FCSTD DOCUMENT  (FreeCAD 0.18R16117 (Git))
Label: final-prototype
License: All rights reserved
LicenseURL: http://en.wikipedia.org/wiki/All_rights_reserved
objects: Part::Feature×843, Sketcher::SketchObject×264, PartDesign::Pad×127, PartDesign::Pocket×86, PartDesign::Body×36, Part::MultiFuse×28, App::DocumentObjectGroup×24, App::Part×18, Part::FeaturePython×14, Part::Fillet×12, PartDesign::Hole×10, PartDesign::AdditivePipe×10, PartDesign::FeatureBase×8, Part::Mirroring×6, Part::Part2DObjectPython×2, Part::Box×2, PartDesign::Mirrored×2, Spreadsheet::Sheet×1, Mesh::Feature×1, PartDesign::Fillet×1
note: 1684 computed .brp shape members not serialized (recipe doc carries the construction recipe); baked Part::Feature solids carry a one-line shape summary decoded from their .brp

FEATURE [Spreadsheet::Sheet] Spreadsheet  label="bom"
  cells = A1=Part; B1=Number; C1=Prize; D1=Total prize; E1=Comments; F1=Links; A2=SG90; B2=8; C2=1.5; D2==B2 * C2; E2=If the SG90 are limited in torque, take a look at the SG91; A3=Icezum Alhambra II; B3=1; C3=60; D3==B3 * C3; A4=RaspberryPi3_ModelB+; B4=1; C4=50
FEATURE [App::DocumentObjectGroup] Grupo003  label="doc"
  Group = -> [Spreadsheet]
FEATURE [Mesh::Feature] RaspberryPi3_ModelB  label="RaspberryPi3-ModelB"
  Placement = pos=(0,0,0) rot=(1,0,0;4.71239rad)
FEATURE [Part::Feature] Fusion007001  label="Servo-sg90-final"
  Placement = pos=(0,-16.6,0) rot=(0,0,1;0rad)
  shape: bbox 11.8 x 32.4 x 29.9 mm, 77 faces (baked)
FEATURE [Part::Feature] Pocket002001  label="Final-1-arm-horn"
  Placement = pos=(0.0197124,-0.0361996,31.3278) rot=(1,0,0;3.14159rad)
  shape: bbox 22.5 x 8 x 5 mm, 19 faces (baked)
FEATURE [Part::Feature] Pocket003001  label="Final-2-arms-horn"
  Placement = pos=(28.7491,12.6638,37.3278) rot=(1,0,0;3.14159rad)
  shape: bbox 33 x 8 x 5 mm, 28 faces (baked)
FEATURE [Part::Feature] Pocket003004  label="Final-1-rotated"
  Placement = pos=(-0.0921605,3.85986,31.3278) rot=(0.996709,-0.081069,0;3.14159rad)
  shape: bbox 22.28 x 8.247 x 5 mm, 19 faces (baked)
FEATURE [App::DocumentObjectGroup] Grupo005  label="horns"
  Group = -> [Pocket002001,Pocket003001,Pocket003004]
FEATURE [App::DocumentObjectGroup] Grupo006  label="Servomotors"
  Group = -> [Grupo005,Fusion007001]
FEATURE [Part::Feature] Part__Feature388  label="LiPo battery 500 mAh158"
  Placement = pos=(-6e-15,47,-5) rot=(0,0,1;3.14159rad)
  shape: bbox 0.3004 x 0.1808 x 0.005 mm, 6 faces (baked)
FEATURE [Part::Feature] Part__Feature389  label="LiPo battery 500 mAh159"
  Placement = pos=(-6e-15,47,-5) rot=(0,0,1;3.14159rad)
  shape: bbox 0.3004 x 0.1808 x 0.005 mm, 6 faces (baked)
FEATURE [Part::Feature] Part__Feature391  label="LiPo battery 500 mAh161"
  Placement = pos=(-6e-15,47,-5) rot=(0,0,1;3.14159rad)
  shape: bbox 0.3004 x 0.1808 x 0.005 mm, 6 faces (baked)
FEATURE [Part::Feature] Part__Feature230  label="LiPo battery 500 mAh"
  Placement = pos=(-6e-15,47,-5) rot=(0,0,1;3.14159rad)
  shape: bbox 32.9 x 35 x 5 mm, 51 faces (baked)
FEATURE [Part::Feature] Part__Feature231  label="LiPo battery 500 mAh001"
  Placement = pos=(-6e-15,47,-5) rot=(0,0,1;3.14159rad)
  shape: bbox 29 x 4.5 x 1.2 mm, 6 faces (baked)
FEATURE [Part::Feature] Part__Feature232  label="LiPo battery 500 mAh002"
  Placement = pos=(-6e-15,47,-5) rot=(0,0,1;3.14159rad)
  shape: bbox 4 x 4.2 x 0.035 mm, 10 faces (baked)
FEATURE [Part::Feature] Part__Feature233  label="LiPo battery 500 mAh003"
  Placement = pos=(-6e-15,47,-5) rot=(0,0,1;3.14159rad)
  shape: bbox 4 x 4.2 x 0.035 mm, 10 faces (baked)
FEATURE [Part::Feature] Part__Feature234  label="LiPo battery 500 mAh004"
  Placement = pos=(-6e-15,47,-5) rot=(0,0,1;3.14159rad)
  shape: bbox 31.44 x 35.54 x 5.5 mm, 94 faces (baked)
FEATURE [Part::Feature] Part__Feature235  label="LiPo battery 500 mAh005"
  Placement = pos=(-6e-15,47,-5) rot=(0,0,1;3.14159rad)
  shape: bbox 1.098 x 2.25 x 1 mm, 3 faces (baked)
FEATURE [Part::Feature] Part__Feature236  label="LiPo battery 500 mAh006"
  Placement = pos=(-6e-15,47,-5) rot=(0,0,1;3.14159rad)
  shape: bbox 3.548 x 12.25 x 1 mm, 5 faces (baked)
FEATURE [Part::Feature] Part__Feature237  label="LiPo battery 500 mAh007"
  Placement = pos=(-6e-15,47,-5) rot=(0,0,1;3.14159rad)
  shape: bbox 3.45 x 10 x 1 mm, 5 faces (baked)
FEATURE [Part::Feature] Part__Feature238  label="LiPo battery 500 mAh008"
  Placement = pos=(-6e-15,47,-5) rot=(0,0,1;3.14159rad)
  shape: bbox 0.3004 x 0.1793 x 0.005 mm, 6 faces (baked)
FEATURE [Part::Feature] Part__Feature239  label="LiPo battery 500 mAh009"
  Placement = pos=(-6e-15,47,-5) rot=(0,0,1;3.14159rad)
  shape: bbox 0.3004 x 0.1793 x 0.005 mm, 6 faces (baked)
FEATURE [Part::Feature] Part__Feature240  label="LiPo battery 500 mAh010"
  Placement = pos=(-6e-15,47,-5) rot=(0,0,1;3.14159rad)
  shape: bbox 0.3004 x 0.1793 x 0.005 mm, 6 faces (baked)
FEATURE [Part::Feature] Part__Feature241  label="LiPo battery 500 mAh011"
  Placement = pos=(-6e-15,47,-5) rot=(0,0,1;3.14159rad)
  shape: bbox 0.3004 x 0.1808 x 0.005 mm, 6 faces (baked)
FEATURE [Part::Feature] Part__Feature242  label="LiPo battery 500 mAh012"
  Placement = pos=(-6e-15,47,-5) rot=(0,0,1;3.14159rad)
  shape: bbox 0.3004 x 0.1808 x 0.005 mm, 6 faces (baked)
FEATURE [Part::Feature] Part__Feature243  label="LiPo battery 500 mAh013"
  Placement = pos=(-6e-15,47,-5) rot=(0,0,1;3.14159rad)
  shape: bbox 0.3004 x 0.1808 x 0.005 mm, 6 faces (baked)
FEATURE [Part::Feature] Part__Feature244  label="LiPo battery 500 mAh014"
  Placement = pos=(-6e-15,47,-5) rot=(0,0,1;3.14159rad)
  shape: bbox 0.3004 x 0.1808 x 0.005 mm, 6 faces (baked)
FEATURE [Part::Feature] Part__Feature245  label="LiPo battery 500 mAh015"
  Placement = pos=(-6e-15,47,-5) rot=(0,0,1;3.14159rad)
  shape: bbox 0.3004 x 0.1808 x 0.005 mm, 6 faces (baked)
FEATURE [Part::Feature] Part__Feature246  label="LiPo battery 500 mAh016"
  Placement = pos=(-6e-15,47,-5) rot=(0,0,1;3.14159rad)
  shape: bbox 0.3004 x 0.1793 x 0.005 mm, 6 faces (baked)
FEATURE [Part::Feature] Part__Feature247  label="LiPo battery 500 mAh017"
  Placement = pos=(-6e-15,47,-5) rot=(0,0,1;3.14159rad)
  shape: bbox 0.3004 x 0.1793 x 0.005 mm, 6 faces (baked)
FEATURE [Part::Feature] Part__Feature248  label="LiPo battery 500 mAh018"
  Placement = pos=(-6e-15,47,-5) rot=(0,0,1;3.14159rad)
  shape: bbox 0.3004 x 0.1808 x 0.005 mm, 6 faces (baked)
FEATURE [Part::Feature] Part__Feature249  label="LiPo battery 500 mAh019"
  Placement = pos=(-6e-15,47,-5) rot=(0,0,1;3.14159rad)
  shape: bbox 0.3004 x 0.1808 x 0.005 mm, 6 faces (baked)
FEATURE [Part::Feature] Part__Feature250  label="LiPo battery 500 mAh020"
  Placement = pos=(-6e-15,47,-5) rot=(0,0,1;3.14159rad)
  shape: bbox 0.3004 x 0.1808 x 0.005 mm, 6 faces (baked)
FEATURE [Part::Feature] Part__Feature251  label="LiPo battery 500 mAh021"
  Placement = pos=(-6e-15,47,-5) rot=(0,0,1;3.14159rad)
  shape: bbox 0.3004 x 0.1793 x 0.005 mm, 6 faces (baked)
FEATURE [Part::Feature] Part__Feature252  label="LiPo battery 500 mAh022"
  Placement = pos=(-6e-15,47,-5) rot=(0,0,1;3.14159rad)
  shape: bbox 0.3004 x 0.1808 x 0.005 mm, 6 faces (baked)
FEATURE [Part::Feature] Part__Feature253  label="LiPo battery 500 mAh023"
  Placement = pos=(-6e-15,47,-5) rot=(0,0,1;3.14159rad)
  shape: bbox 0.3004 x 0.1808 x 0.005 mm, 6 faces (baked)
FEATURE [Part::Feature] Part__Feature254  label="LiPo battery 500 mAh024"
  Placement = pos=(-6e-15,47,-5) rot=(0,0,1;3.14159rad)
  shape: bbox 0.3004 x 0.1793 x 0.005 mm, 6 faces (baked)
FEATURE [Part::Feature] Part__Feature255  label="LiPo battery 500 mAh025"
  Placement = pos=(-6e-15,47,-5) rot=(0,0,1;3.14159rad)
  shape: bbox 0.3004 x 0.1793 x 0.005 mm, 6 faces (baked)
FEATURE [Part::Feature] Part__Feature256  label="LiPo battery 500 mAh026"
  Placement = pos=(-6e-15,47,-5) rot=(0,0,1;3.14159rad)
  shape: bbox 0.3004 x 0.1793 x 0.005 mm, 6 faces (baked)
FEATURE [Part::Feature] Part__Feature257  label="LiPo battery 500 mAh027"
  Placement = pos=(-6e-15,47,-5) rot=(0,0,1;3.14159rad)
  shape: bbox 0.3004 x 0.1808 x 0.005 mm, 6 faces (baked)
FEATURE [Part::Feature] Part__Feature258  label="LiPo battery 500 mAh028"
  Placement = pos=(-6e-15,47,-5) rot=(0,0,1;3.14159rad)
  shape: bbox 0.3004 x 0.1808 x 0.005 mm, 6 faces (baked)
FEATURE [Part::Feature] Part__Feature259  label="LiPo battery 500 mAh029"
  Placement = pos=(-6e-15,47,-5) rot=(0,0,1;3.14159rad)
  shape: bbox 0.3004 x 0.1808 x 0.005 mm, 6 faces (baked)
FEATURE [Part::Feature] Part__Feature260  label="LiPo battery 500 mAh030"
  Placement = pos=(-6e-15,47,-5) rot=(0,0,1;3.14159rad)
  shape: bbox 0.3004 x 0.1808 x 0.005 mm, 6 faces (baked)
FEATURE [Part::Feature] Part__Feature261  label="LiPo battery 500 mAh031"
  Placement = pos=(-6e-15,47,-5) rot=(0,0,1;3.14159rad)
  shape: bbox 0.3004 x 0.1808 x 0.005 mm, 6 faces (baked)
FEATURE [Part::Feature] Part__Feature262  label="LiPo battery 500 mAh032"
  Placement = pos=(-6e-15,47,-5) rot=(0,0,1;3.14159rad)
  shape: bbox 0.3004 x 0.1793 x 0.005 mm, 6 faces (baked)
FEATURE [Part::Feature] Part__Feature263  label="LiPo battery 500 mAh033"
  Placement = pos=(-6e-15,47,-5) rot=(0,0,1;3.14159rad)
  shape: bbox 0.3004 x 0.1793 x 0.005 mm, 6 faces (baked)
FEATURE [Part::Feature] Part__Feature264  label="LiPo battery 500 mAh034"
  Placement = pos=(-6e-15,47,-5) rot=(0,0,1;3.14159rad)
  shape: bbox 0.3004 x 0.1793 x 0.005 mm, 6 faces (baked)
FEATURE [Part::Feature] Part__Feature265  label="LiPo battery 500 mAh035"
  Placement = pos=(-6e-15,47,-5) rot=(0,0,1;3.14159rad)
  shape: bbox 0.3004 x 0.1808 x 0.005 mm, 6 faces (baked)
FEATURE [Part::Feature] Part__Feature266  label="LiPo battery 500 mAh036"
  Placement = pos=(-6e-15,47,-5) rot=(0,0,1;3.14159rad)
  shape: bbox 0.3004 x 0.1808 x 0.005 mm, 6 faces (baked)
FEATURE [Part::Feature] Part__Feature267  label="LiPo battery 500 mAh037"
  Placement = pos=(-6e-15,47,-5) rot=(0,0,1;3.14159rad)
  shape: bbox 0.3004 x 0.1808 x 0.005 mm, 6 faces (baked)
FEATURE [Part::Feature] Part__Feature268  label="LiPo battery 500 mAh038"
  Placement = pos=(-6e-15,47,-5) rot=(0,0,1;3.14159rad)
  shape: bbox 0.3004 x 0.1808 x 0.005 mm, 6 faces (baked)
FEATURE [Part::Feature] Part__Feature269  label="LiPo battery 500 mAh039"
  Placement = pos=(-6e-15,47,-5) rot=(0,0,1;3.14159rad)
  shape: bbox 0.3004 x 0.1808 x 0.005 mm, 6 faces (baked)
FEATURE [Part::Feature] Part__Feature270  label="LiPo battery 500 mAh040"
  Placement = pos=(-6e-15,47,-5) rot=(0,0,1;3.14159rad)
  shape: bbox 0.3004 x 0.1808 x 0.005 mm, 6 faces (baked)
FEATURE [Part::Feature] Part__Feature271  label="LiPo battery 500 mAh041"
  Placement = pos=(-6e-15,47,-5) rot=(0,0,1;3.14159rad)
  shape: bbox 0.3004 x 0.1808 x 0.005 mm, 6 faces (baked)
FEATURE [Part::Feature] Part__Feature272  label="LiPo battery 500 mAh042"
  Placement = pos=(-6e-15,47,-5) rot=(0,0,1;3.14159rad)
  shape: bbox 0.3004 x 0.1793 x 0.005 mm, 6 faces (baked)
FEATURE [Part::Feature] Part__Feature273  label="LiPo battery 500 mAh043"
  Placement = pos=(-6e-15,47,-5) rot=(0,0,1;3.14159rad)
  shape: bbox 0.3004 x 0.1808 x 0.005 mm, 6 faces (baked)
FEATURE [Part::Feature] Part__Feature274  label="LiPo battery 500 mAh044"
  Placement = pos=(-6e-15,47,-5) rot=(0,0,1;3.14159rad)
  shape: bbox 0.3004 x 0.1793 x 0.005 mm, 6 faces (baked)
FEATURE [Part::Feature] Part__Feature275  label="LiPo battery 500 mAh045"
  Placement = pos=(-6e-15,47,-5) rot=(0,0,1;3.14159rad)
  shape: bbox 0.3004 x 0.1793 x 0.005 mm, 6 faces (baked)
FEATURE [Part::Feature] Part__Feature276  label="LiPo battery 500 mAh046"
  Placement = pos=(-6e-15,47,-5) rot=(0,0,1;3.14159rad)
  shape: bbox 0.3004 x 0.1793 x 0.005 mm, 6 faces (baked)
FEATURE [Part::Feature] Part__Feature277  label="LiPo battery 500 mAh047"
  Placement = pos=(-6e-15,47,-5) rot=(0,0,1;3.14159rad)
  shape: bbox 0.3004 x 0.1808 x 0.005 mm, 6 faces (baked)
FEATURE [Part::Feature] Part__Feature278  label="LiPo battery 500 mAh048"
  Placement = pos=(-6e-15,47,-5) rot=(0,0,1;3.14159rad)
  shape: bbox 0.3004 x 0.1808 x 0.005 mm, 6 faces (baked)
FEATURE [Part::Feature] Part__Feature279  label="LiPo battery 500 mAh049"
  Placement = pos=(-6e-15,47,-5) rot=(0,0,1;3.14159rad)
  shape: bbox 0.3004 x 0.1808 x 0.005 mm, 6 faces (baked)
FEATURE [Part::Feature] Part__Feature280  label="LiPo battery 500 mAh050"
  Placement = pos=(-6e-15,47,-5) rot=(0,0,1;3.14159rad)
  shape: bbox 0.3004 x 0.1808 x 0.005 mm, 6 faces (baked)
FEATURE [Part::Feature] Part__Feature281  label="LiPo battery 500 mAh051"
  Placement = pos=(-6e-15,47,-5) rot=(0,0,1;3.14159rad)
  shape: bbox 0.3004 x 0.1808 x 0.005 mm, 6 faces (baked)
FEATURE [Part::Feature] Part__Feature282  label="LiPo battery 500 mAh052"
  Placement = pos=(-6e-15,47,-5) rot=(0,0,1;3.14159rad)
  shape: bbox 0.3004 x 0.1808 x 0.005 mm, 6 faces (baked)
FEATURE [Part::Feature] Part__Feature283  label="LiPo battery 500 mAh053"
  Placement = pos=(-6e-15,47,-5) rot=(0,0,1;3.14159rad)
  shape: bbox 0.3004 x 0.1793 x 0.005 mm, 6 faces (baked)
FEATURE [Part::Feature] Part__Feature284  label="LiPo battery 500 mAh054"
  Placement = pos=(-6e-15,47,-5) rot=(0,0,1;3.14159rad)
  shape: bbox 0.3004 x 0.1808 x 0.005 mm, 6 faces (baked)
FEATURE [Part::Feature] Part__Feature285  label="LiPo battery 500 mAh055"
  Placement = pos=(-6e-15,47,-5) rot=(0,0,1;3.14159rad)
  shape: bbox 0.3004 x 0.1808 x 0.005 mm, 6 faces (baked)
FEATURE [Part::Feature] Part__Feature286  label="LiPo battery 500 mAh056"
  Placement = pos=(-6e-15,47,-5) rot=(0,0,1;3.14159rad)
  shape: bbox 0.3004 x 0.1808 x 0.005 mm, 6 faces (baked)
FEATURE [Part::Feature] Part__Feature287  label="LiPo battery 500 mAh057"
  Placement = pos=(-6e-15,47,-5) rot=(0,0,1;3.14159rad)
  shape: bbox 0.3004 x 0.1808 x 0.005 mm, 6 faces (baked)
FEATURE [Part::Feature] Part__Feature288  label="LiPo battery 500 mAh058"
  Placement = pos=(-6e-15,47,-5) rot=(0,0,1;3.14159rad)
  shape: bbox 0.3004 x 0.1793 x 0.005 mm, 6 faces (baked)
FEATURE [Part::Feature] Part__Feature289  label="LiPo battery 500 mAh059"
  Placement = pos=(-6e-15,47,-5) rot=(0,0,1;3.14159rad)
  shape: bbox 0.3004 x 0.1793 x 0.005 mm, 6 faces (baked)
FEATURE [Part::Feature] Part__Feature290  label="LiPo battery 500 mAh060"
  Placement = pos=(-6e-15,47,-5) rot=(0,0,1;3.14159rad)
  shape: bbox 0.3004 x 0.1793 x 0.005 mm, 6 faces (baked)
FEATURE [Part::Feature] Part__Feature291  label="LiPo battery 500 mAh061"
  Placement = pos=(-6e-15,47,-5) rot=(0,0,1;3.14159rad)
  shape: bbox 0.3004 x 0.1808 x 0.005 mm, 6 faces (baked)
FEATURE [Part::Feature] Part__Feature292  label="LiPo battery 500 mAh062"
  Placement = pos=(-6e-15,47,-5) rot=(0,0,1;3.14159rad)
  shape: bbox 0.3004 x 0.1808 x 0.005 mm, 6 faces (baked)
FEATURE [Part::Feature] Part__Feature293  label="LiPo battery 500 mAh063"
  Placement = pos=(-6e-15,47,-5) rot=(0,0,1;3.14159rad)
  shape: bbox 0.3004 x 0.1808 x 0.005 mm, 6 faces (baked)
FEATURE [Part::Feature] Part__Feature294  label="LiPo battery 500 mAh064"
  Placement = pos=(-6e-15,47,-5) rot=(0,0,1;3.14159rad)
  shape: bbox 0.3004 x 0.1808 x 0.005 mm, 6 faces (baked)
FEATURE [Part::Feature] Part__Feature295  label="LiPo battery 500 mAh065"
  Placement = pos=(-6e-15,47,-5) rot=(0,0,1;3.14159rad)
  shape: bbox 0.3004 x 0.1808 x 0.005 mm, 6 faces (baked)
FEATURE [Part::Feature] Part__Feature296  label="LiPo battery 500 mAh066"
  Placement = pos=(-6e-15,47,-5) rot=(0,0,1;3.14159rad)
  shape: bbox 0.3004 x 0.1808 x 0.005 mm, 6 faces (baked)
FEATURE [Part::Feature] Part__Feature297  label="LiPo battery 500 mAh067"
  Placement = pos=(-6e-15,47,-5) rot=(0,0,1;3.14159rad)
  shape: bbox 0.3004 x 0.1793 x 0.005 mm, 6 faces (baked)
FEATURE [Part::Feature] Part__Feature298  label="LiPo battery 500 mAh068"
  Placement = pos=(-6e-15,47,-5) rot=(0,0,1;3.14159rad)
  shape: bbox 0.3004 x 0.1793 x 0.005 mm, 6 faces (baked)
FEATURE [Part::Feature] Part__Feature299  label="LiPo battery 500 mAh069"
  Placement = pos=(-6e-15,47,-5) rot=(0,0,1;3.14159rad)
  shape: bbox 0.3004 x 0.1793 x 0.005 mm, 6 faces (baked)
FEATURE [Part::Feature] Part__Feature300  label="LiPo battery 500 mAh070"
  Placement = pos=(-6e-15,47,-5) rot=(0,0,1;3.14159rad)
  shape: bbox 0.3004 x 0.1808 x 0.005 mm, 6 faces (baked)
FEATURE [Part::Feature] Part__Feature301  label="LiPo battery 500 mAh071"
  Placement = pos=(-6e-15,47,-5) rot=(0,0,1;3.14159rad)
  shape: bbox 0.3004 x 0.1808 x 0.005 mm, 6 faces (baked)
FEATURE [Part::Feature] Part__Feature302  label="LiPo battery 500 mAh072"
  Placement = pos=(-6e-15,47,-5) rot=(0,0,1;3.14159rad)
  shape: bbox 0.3004 x 0.1808 x 0.005 mm, 6 faces (baked)
FEATURE [Part::Feature] Part__Feature303  label="LiPo battery 500 mAh073"
  Placement = pos=(-6e-15,47,-5) rot=(0,0,1;3.14159rad)
  shape: bbox 0.3004 x 0.1808 x 0.005 mm, 6 faces (baked)
FEATURE [Part::Feature] Part__Feature304  label="LiPo battery 500 mAh074"
  Placement = pos=(-6e-15,47,-5) rot=(0,0,1;3.14159rad)
  shape: bbox 0.3004 x 0.1808 x 0.005 mm, 6 faces (baked)
FEATURE [Part::Feature] Part__Feature305  label="LiPo battery 500 mAh075"
  Placement = pos=(-6e-15,47,-5) rot=(0,0,1;3.14159rad)
  shape: bbox 0.3004 x 0.1793 x 0.005 mm, 6 faces (baked)
FEATURE [Part::Feature] Part__Feature306  label="LiPo battery 500 mAh076"
  Placement = pos=(-6e-15,47,-5) rot=(0,0,1;3.14159rad)
  shape: bbox 0.3004 x 0.1808 x 0.005 mm, 6 faces (baked)
FEATURE [Part::Feature] Part__Feature307  label="LiPo battery 500 mAh077"
  Placement = pos=(-6e-15,47,-5) rot=(0,0,1;3.14159rad)
  shape: bbox 0.3004 x 0.1808 x 0.005 mm, 6 faces (baked)
FEATURE [Part::Feature] Part__Feature308  label="LiPo battery 500 mAh078"
  Placement = pos=(-6e-15,47,-5) rot=(0,0,1;3.14159rad)
  shape: bbox 0.3004 x 0.1808 x 0.005 mm, 6 faces (baked)
FEATURE [Part::Feature] Part__Feature309  label="LiPo battery 500 mAh079"
  Placement = pos=(-6e-15,47,-5) rot=(0,0,1;3.14159rad)
  shape: bbox 0.3004 x 0.1808 x 0.005 mm, 6 faces (baked)
FEATURE [Part::Feature] Part__Feature310  label="LiPo battery 500 mAh080"
  Placement = pos=(-6e-15,47,-5) rot=(0,0,1;3.14159rad)
  shape: bbox 0.3004 x 0.1808 x 0.005 mm, 6 faces (baked)
FEATURE [Part::Feature] Part__Feature311  label="LiPo battery 500 mAh081"
  Placement = pos=(-6e-15,47,-5) rot=(0,0,1;3.14159rad)
  shape: bbox 0.3004 x 0.1808 x 0.005 mm, 6 faces (baked)
FEATURE [Part::Feature] Part__Feature312  label="LiPo battery 500 mAh082"
  Placement = pos=(-6e-15,47,-5) rot=(0,0,1;3.14159rad)
  shape: bbox 0.3004 x 0.1808 x 0.005 mm, 6 faces (baked)
FEATURE [Part::Feature] Part__Feature313  label="LiPo battery 500 mAh083"
  Placement = pos=(-6e-15,47,-5) rot=(0,0,1;3.14159rad)
  shape: bbox 0.3004 x 0.1793 x 0.005 mm, 6 faces (baked)
FEATURE [Part::Feature] Part__Feature314  label="LiPo battery 500 mAh084"
  Placement = pos=(-6e-15,47,-5) rot=(0,0,1;3.14159rad)
  shape: bbox 0.3004 x 0.1793 x 0.005 mm, 6 faces (baked)
FEATURE [Part::Feature] Part__Feature315  label="LiPo battery 500 mAh085"
  Placement = pos=(-6e-15,47,-5) rot=(0,0,1;3.14159rad)
  shape: bbox 0.3004 x 0.1808 x 0.005 mm, 6 faces (baked)
FEATURE [Part::Feature] Part__Feature316  label="LiPo battery 500 mAh086"
  Placement = pos=(-6e-15,47,-5) rot=(0,0,1;3.14159rad)
  shape: bbox 0.3004 x 0.1808 x 0.005 mm, 6 faces (baked)
FEATURE [Part::Feature] Part__Feature317  label="LiPo battery 500 mAh087"
  Placement = pos=(-6e-15,47,-5) rot=(0,0,1;3.14159rad)
  shape: bbox 0.3004 x 0.1808 x 0.005 mm, 6 faces (baked)
FEATURE [Part::Feature] Part__Feature318  label="LiPo battery 500 mAh088"
  Placement = pos=(-6e-15,47,-5) rot=(0,0,1;3.14159rad)
  shape: bbox 0.3004 x 0.1808 x 0.005 mm, 6 faces (baked)
FEATURE [Part::Feature] Part__Feature319  label="LiPo battery 500 mAh089"
  Placement = pos=(-6e-15,47,-5) rot=(0,0,1;3.14159rad)
  shape: bbox 0.3004 x 0.1808 x 0.005 mm, 6 faces (baked)
FEATURE [Part::Feature] Part__Feature320  label="LiPo battery 500 mAh090"
  Placement = pos=(-6e-15,47,-5) rot=(0,0,1;3.14159rad)
  shape: bbox 0.3004 x 0.1808 x 0.005 mm, 6 faces (baked)
FEATURE [Part::Feature] Part__Feature321  label="LiPo battery 500 mAh091"
  Placement = pos=(-6e-15,47,-5) rot=(0,0,1;3.14159rad)
  shape: bbox 0.3004 x 0.1793 x 0.005 mm, 6 faces (baked)
FEATURE [Part::Feature] Part__Feature322  label="LiPo battery 500 mAh092"
  Placement = pos=(-6e-15,47,-5) rot=(0,0,1;3.14159rad)
  shape: bbox 0.3004 x 0.1808 x 0.005 mm, 6 faces (baked)
FEATURE [Part::Feature] Part__Feature323  label="LiPo battery 500 mAh093"
  Placement = pos=(-6e-15,47,-5) rot=(0,0,1;3.14159rad)
  shape: bbox 0.3004 x 0.1808 x 0.005 mm, 6 faces (baked)
FEATURE [Part::Feature] Part__Feature324  label="LiPo battery 500 mAh094"
  Placement = pos=(-6e-15,47,-5) rot=(0,0,1;3.14159rad)
  shape: bbox 0.3004 x 0.1808 x 0.005 mm, 6 faces (baked)
FEATURE [Part::Feature] Part__Feature325  label="LiPo battery 500 mAh095"
  Placement = pos=(-6e-15,47,-5) rot=(0,0,1;3.14159rad)
  shape: bbox 0.3004 x 0.1808 x 0.005 mm, 6 faces (baked)
FEATURE [Part::Feature] Part__Feature326  label="LiPo battery 500 mAh096"
  Placement = pos=(-6e-15,47,-5) rot=(0,0,1;3.14159rad)
  shape: bbox 0.3004 x 0.1808 x 0.005 mm, 6 faces (baked)
FEATURE [Part::Feature] Part__Feature327  label="LiPo battery 500 mAh097"
  Placement = pos=(-6e-15,47,-5) rot=(0,0,1;3.14159rad)
  shape: bbox 0.3004 x 0.1808 x 0.005 mm, 6 faces (baked)
FEATURE [Part::Feature] Part__Feature328  label="LiPo battery 500 mAh098"
  Placement = pos=(-6e-15,47,-5) rot=(0,0,1;3.14159rad)
  shape: bbox 0.3004 x 0.1793 x 0.005 mm, 6 faces (baked)
FEATURE [Part::Feature] Part__Feature329  label="LiPo battery 500 mAh099"
  Placement = pos=(-6e-15,47,-5) rot=(0,0,1;3.14159rad)
  shape: bbox 0.3004 x 0.1793 x 0.005 mm, 6 faces (baked)
FEATURE [Part::Feature] Part__Feature330  label="LiPo battery 500 mAh100"
  Placement = pos=(-6e-15,47,-5) rot=(0,0,1;3.14159rad)
  shape: bbox 0.3004 x 0.1793 x 0.005 mm, 6 faces (baked)
FEATURE [Part::Feature] Part__Feature331  label="LiPo battery 500 mAh101"
  Placement = pos=(-6e-15,47,-5) rot=(0,0,1;3.14159rad)
  shape: bbox 0.3004 x 0.1808 x 0.005 mm, 6 faces (baked)
FEATURE [Part::Feature] Part__Feature332  label="LiPo battery 500 mAh102"
  Placement = pos=(-6e-15,47,-5) rot=(0,0,1;3.14159rad)
  shape: bbox 0.3004 x 0.1808 x 0.005 mm, 6 faces (baked)
FEATURE [Part::Feature] Part__Feature333  label="LiPo battery 500 mAh103"
  Placement = pos=(-6e-15,47,-5) rot=(0,0,1;3.14159rad)
  shape: bbox 0.3004 x 0.1808 x 0.005 mm, 6 faces (baked)
FEATURE [Part::Feature] Part__Feature334  label="LiPo battery 500 mAh104"
  Placement = pos=(-6e-15,47,-5) rot=(0,0,1;3.14159rad)
  shape: bbox 0.3004 x 0.1808 x 0.005 mm, 6 faces (baked)
FEATURE [Part::Feature] Part__Feature335  label="LiPo battery 500 mAh105"
  Placement = pos=(-6e-15,47,-5) rot=(0,0,1;3.14159rad)
  shape: bbox 0.3004 x 0.1808 x 0.005 mm, 6 faces (baked)
FEATURE [Part::Feature] Part__Feature336  label="LiPo battery 500 mAh106"
  Placement = pos=(-6e-15,47,-5) rot=(0,0,1;3.14159rad)
  shape: bbox 0.3004 x 0.1808 x 0.005 mm, 6 faces (baked)
FEATURE [Part::Feature] Part__Feature337  label="LiPo battery 500 mAh107"
  Placement = pos=(-6e-15,47,-5) rot=(0,0,1;3.14159rad)
  shape: bbox 0.3004 x 0.1808 x 0.005 mm, 6 faces (baked)
FEATURE [Part::Feature] Part__Feature338  label="LiPo battery 500 mAh108"
  Placement = pos=(-6e-15,47,-5) rot=(0,0,1;3.14159rad)
  shape: bbox 0.3004 x 0.1793 x 0.005 mm, 6 faces (baked)
FEATURE [Part::Feature] Part__Feature339  label="LiPo battery 500 mAh109"
  Placement = pos=(-6e-15,47,-5) rot=(0,0,1;3.14159rad)
  shape: bbox 0.3004 x 0.1793 x 0.005 mm, 6 faces (baked)
FEATURE [Part::Feature] Part__Feature340  label="LiPo battery 500 mAh110"
  Placement = pos=(-6e-15,47,-5) rot=(0,0,1;3.14159rad)
  shape: bbox 0.3004 x 0.1793 x 0.005 mm, 6 faces (baked)
FEATURE [Part::Feature] Part__Feature341  label="LiPo battery 500 mAh111"
  Placement = pos=(-6e-15,47,-5) rot=(0,0,1;3.14159rad)
  shape: bbox 0.3004 x 0.1808 x 0.005 mm, 6 faces (baked)
FEATURE [Part::Feature] Part__Feature342  label="LiPo battery 500 mAh112"
  Placement = pos=(-6e-15,47,-5) rot=(0,0,1;3.14159rad)
  shape: bbox 0.3004 x 0.1808 x 0.005 mm, 6 faces (baked)
FEATURE [Part::Feature] Part__Feature343  label="LiPo battery 500 mAh113"
  Placement = pos=(-6e-15,47,-5) rot=(0,0,1;3.14159rad)
  shape: bbox 0.3004 x 0.1808 x 0.005 mm, 6 faces (baked)
FEATURE [Part::Feature] Part__Feature344  label="LiPo battery 500 mAh114"
  Placement = pos=(-6e-15,47,-5) rot=(0,0,1;3.14159rad)
  shape: bbox 0.3004 x 0.1808 x 0.005 mm, 6 faces (baked)
FEATURE [Part::Feature] Part__Feature345  label="LiPo battery 500 mAh115"
  Placement = pos=(-6e-15,47,-5) rot=(0,0,1;3.14159rad)
  shape: bbox 0.3004 x 0.1808 x 0.005 mm, 6 faces (baked)
FEATURE [Part::Feature] Part__Feature346  label="LiPo battery 500 mAh116"
  Placement = pos=(-6e-15,47,-5) rot=(0,0,1;3.14159rad)
  shape: bbox 0.3004 x 0.1808 x 0.005 mm, 6 faces (baked)
FEATURE [Part::Feature] Part__Feature347  label="LiPo battery 500 mAh117"
  Placement = pos=(-6e-15,47,-5) rot=(0,0,1;3.14159rad)
  shape: bbox 0.3004 x 0.1793 x 0.005 mm, 6 faces (baked)
FEATURE [Part::Feature] Part__Feature348  label="LiPo battery 500 mAh118"
  Placement = pos=(-6e-15,47,-5) rot=(0,0,1;3.14159rad)
  shape: bbox 0.3004 x 0.1793 x 0.005 mm, 6 faces (baked)
FEATURE [Part::Feature] Part__Feature349  label="LiPo battery 500 mAh119"
  Placement = pos=(-6e-15,47,-5) rot=(0,0,1;3.14159rad)
  shape: bbox 0.3004 x 0.1793 x 0.005 mm, 6 faces (baked)
FEATURE [Part::Feature] Part__Feature350  label="LiPo battery 500 mAh120"
  Placement = pos=(-6e-15,47,-5) rot=(0,0,1;3.14159rad)
  shape: bbox 0.3004 x 0.1808 x 0.005 mm, 6 faces (baked)
FEATURE [Part::Feature] Part__Feature351  label="LiPo battery 500 mAh121"
  Placement = pos=(-6e-15,47,-5) rot=(0,0,1;3.14159rad)
  shape: bbox 0.3004 x 0.1808 x 0.005 mm, 6 faces (baked)
FEATURE [Part::Feature] Part__Feature352  label="LiPo battery 500 mAh122"
  Placement = pos=(-6e-15,47,-5) rot=(0,0,1;3.14159rad)
  shape: bbox 0.3004 x 0.1808 x 0.005 mm, 6 faces (baked)
FEATURE [Part::Feature] Part__Feature353  label="LiPo battery 500 mAh123"
  Placement = pos=(-6e-15,47,-5) rot=(0,0,1;3.14159rad)
  shape: bbox 0.3004 x 0.1808 x 0.005 mm, 6 faces (baked)
FEATURE [Part::Feature] Part__Feature354  label="LiPo battery 500 mAh124"
  Placement = pos=(-6e-15,47,-5) rot=(0,0,1;3.14159rad)
  shape: bbox 0.3004 x 0.1808 x 0.005 mm, 6 faces (baked)
FEATURE [Part::Feature] Part__Feature355  label="LiPo battery 500 mAh125"
  Placement = pos=(-6e-15,47,-5) rot=(0,0,1;3.14159rad)
  shape: bbox 0.3004 x 0.1808 x 0.005 mm, 6 faces (baked)
FEATURE [Part::Feature] Part__Feature356  label="LiPo battery 500 mAh126"
  Placement = pos=(-6e-15,47,-5) rot=(0,0,1;3.14159rad)
  shape: bbox 0.3004 x 0.1793 x 0.005 mm, 6 faces (baked)
FEATURE [Part::Feature] Part__Feature357  label="LiPo battery 500 mAh127"
  Placement = pos=(-6e-15,47,-5) rot=(0,0,1;3.14159rad)
  shape: bbox 0.3004 x 0.1808 x 0.005 mm, 6 faces (baked)
FEATURE [Part::Feature] Part__Feature358  label="LiPo battery 500 mAh128"
  Placement = pos=(-6e-15,47,-5) rot=(0,0,1;3.14159rad)
  shape: bbox 0.3004 x 0.1808 x 0.005 mm, 6 faces (baked)
FEATURE [Part::Feature] Part__Feature359  label="LiPo battery 500 mAh129"
  Placement = pos=(-6e-15,47,-5) rot=(0,0,1;3.14159rad)
  shape: bbox 0.3004 x 0.1808 x 0.005 mm, 6 faces (baked)
FEATURE [Part::Feature] Part__Feature360  label="LiPo battery 500 mAh130"
  Placement = pos=(-6e-15,47,-5) rot=(0,0,1;3.14159rad)
  shape: bbox 0.3004 x 0.1808 x 0.005 mm, 6 faces (baked)
FEATURE [Part::Feature] Part__Feature361  label="LiPo battery 500 mAh131"
  Placement = pos=(-6e-15,47,-5) rot=(0,0,1;3.14159rad)
  shape: bbox 0.3004 x 0.1808 x 0.005 mm, 6 faces (baked)
FEATURE [Part::Feature] Part__Feature362  label="LiPo battery 500 mAh132"
  Placement = pos=(-6e-15,47,-5) rot=(0,0,1;3.14159rad)
  shape: bbox 0.3004 x 0.1793 x 0.005 mm, 6 faces (baked)
FEATURE [Part::Feature] Part__Feature363  label="LiPo battery 500 mAh133"
  Placement = pos=(-6e-15,47,-5) rot=(0,0,1;3.14159rad)
  shape: bbox 0.3004 x 0.1793 x 0.005 mm, 6 faces (baked)
FEATURE [Part::Feature] Part__Feature364  label="LiPo battery 500 mAh134"
  Placement = pos=(-6e-15,47,-5) rot=(0,0,1;3.14159rad)
  shape: bbox 0.3004 x 0.1808 x 0.005 mm, 6 faces (baked)
FEATURE [Part::Feature] Part__Feature365  label="LiPo battery 500 mAh135"
  Placement = pos=(-6e-15,47,-5) rot=(0,0,1;3.14159rad)
  shape: bbox 0.3004 x 0.1808 x 0.005 mm, 6 faces (baked)
FEATURE [Part::Feature] Part__Feature366  label="LiPo battery 500 mAh136"
  Placement = pos=(-6e-15,47,-5) rot=(0,0,1;3.14159rad)
  shape: bbox 0.3004 x 0.1808 x 0.005 mm, 6 faces (baked)
FEATURE [Part::Feature] Part__Feature367  label="LiPo battery 500 mAh137"
  Placement = pos=(-6e-15,47,-5) rot=(0,0,1;3.14159rad)
  shape: bbox 0.3004 x 0.1808 x 0.005 mm, 6 faces (baked)
FEATURE [Part::Feature] Part__Feature368  label="LiPo battery 500 mAh138"
  Placement = pos=(-6e-15,47,-5) rot=(0,0,1;3.14159rad)
  shape: bbox 0.3004 x 0.1793 x 0.005 mm, 6 faces (baked)
FEATURE [Part::Feature] Part__Feature369  label="LiPo battery 500 mAh139"
  Placement = pos=(-6e-15,47,-5) rot=(0,0,1;3.14159rad)
  shape: bbox 0.3004 x 0.1808 x 0.005 mm, 6 faces (baked)
FEATURE [Part::Feature] Part__Feature370  label="LiPo battery 500 mAh140"
  Placement = pos=(-6e-15,47,-5) rot=(0,0,1;3.14159rad)
  shape: bbox 0.3004 x 0.1793 x 0.005 mm, 6 faces (baked)
FEATURE [Part::Feature] Part__Feature371  label="LiPo battery 500 mAh141"
  Placement = pos=(-6e-15,47,-5) rot=(0,0,1;3.14159rad)
  shape: bbox 0.3004 x 0.1793 x 0.005 mm, 6 faces (baked)
FEATURE [Part::Feature] Part__Feature372  label="LiPo battery 500 mAh142"
  Placement = pos=(-6e-15,47,-5) rot=(0,0,1;3.14159rad)
  shape: bbox 0.3004 x 0.1793 x 0.005 mm, 6 faces (baked)
FEATURE [Part::Feature] Part__Feature373  label="LiPo battery 500 mAh143"
  Placement = pos=(-6e-15,47,-5) rot=(0,0,1;3.14159rad)
  shape: bbox 0.3004 x 0.1808 x 0.005 mm, 6 faces (baked)
FEATURE [Part::Feature] Part__Feature374  label="LiPo battery 500 mAh144"
  Placement = pos=(-6e-15,47,-5) rot=(0,0,1;3.14159rad)
  shape: bbox 0.3004 x 0.1808 x 0.005 mm, 6 faces (baked)
FEATURE [Part::Feature] Part__Feature375  label="LiPo battery 500 mAh145"
  Placement = pos=(-6e-15,47,-5) rot=(0,0,1;3.14159rad)
  shape: bbox 0.3004 x 0.1808 x 0.005 mm, 6 faces (baked)
FEATURE [Part::Feature] Part__Feature376  label="LiPo battery 500 mAh146"
  Placement = pos=(-6e-15,47,-5) rot=(0,0,1;3.14159rad)
  shape: bbox 0.3004 x 0.1808 x 0.005 mm, 6 faces (baked)
FEATURE [Part::Feature] Part__Feature377  label="LiPo battery 500 mAh147"
  Placement = pos=(-6e-15,47,-5) rot=(0,0,1;3.14159rad)
  shape: bbox 3.883 x 0.7165 x 0.005 mm, 6 faces (baked)
FEATURE [Part::Feature] Part__Feature378  label="LiPo battery 500 mAh148"
  Placement = pos=(-6e-15,47,-5) rot=(0,0,1;3.14159rad)
  shape: bbox 3.498 x 3.487 x 0.005 mm, 14 faces (baked)
FEATURE [Part::Feature] Part__Feature379  label="LiPo battery 500 mAh149"
  Placement = pos=(-6e-15,47,-5) rot=(0,0,1;3.14159rad)
  shape: bbox 0.3004 x 0.1808 x 0.005 mm, 6 faces (baked)
FEATURE [Part::Feature] Part__Feature380  label="LiPo battery 500 mAh150"
  Placement = pos=(-6e-15,47,-5) rot=(0,0,1;3.14159rad)
  shape: bbox 0.3004 x 0.1808 x 0.005 mm, 6 faces (baked)
FEATURE [Part::Feature] Part__Feature381  label="LiPo battery 500 mAh151"
  Placement = pos=(-6e-15,47,-5) rot=(0,0,1;3.14159rad)
  shape: bbox 0.3004 x 0.1808 x 0.005 mm, 6 faces (baked)
FEATURE [Part::Feature] Part__Feature382  label="LiPo battery 500 mAh152"
  Placement = pos=(-6e-15,47,-5) rot=(0,0,1;3.14159rad)
  shape: bbox 0.3004 x 0.1808 x 0.005 mm, 6 faces (baked)
FEATURE [Part::Feature] Part__Feature383  label="LiPo battery 500 mAh153"
  Placement = pos=(-6e-15,47,-5) rot=(0,0,1;3.14159rad)
  shape: bbox 0.3004 x 0.1808 x 0.005 mm, 6 faces (baked)
FEATURE [Part::Feature] Part__Feature384  label="LiPo battery 500 mAh154"
  Placement = pos=(-6e-15,47,-5) rot=(0,0,1;3.14159rad)
  shape: bbox 0.3004 x 0.1793 x 0.005 mm, 6 faces (baked)
FEATURE [Part::Feature] Part__Feature385  label="LiPo battery 500 mAh155"
  Placement = pos=(-6e-15,47,-5) rot=(0,0,1;3.14159rad)
  shape: bbox 0.3004 x 0.1793 x 0.005 mm, 6 faces (baked)
FEATURE [Part::Feature] Part__Feature386  label="LiPo battery 500 mAh156"
  Placement = pos=(-6e-15,47,-5) rot=(0,0,1;3.14159rad)
  shape: bbox 0.3004 x 0.1808 x 0.005 mm, 6 faces (baked)
FEATURE [Part::Feature] Part__Feature387  label="LiPo battery 500 mAh157"
  Placement = pos=(-6e-15,47,-5) rot=(0,0,1;3.14159rad)
  shape: bbox 0.3004 x 0.1793 x 0.005 mm, 6 faces (baked)
FEATURE [Part::Feature] Part__Feature390  label="LiPo battery 500 mAh160"
  Placement = pos=(-6e-15,47,-5) rot=(0,0,1;3.14159rad)
  shape: bbox 0.3004 x 0.1808 x 0.005 mm, 6 faces (baked)
FEATURE [Part::Feature] Part__Feature392  label="LiPo battery 500 mAh162"
  Placement = pos=(-6e-15,47,-5) rot=(0,0,1;3.14159rad)
  shape: bbox 0.3004 x 0.1808 x 0.005 mm, 6 faces (baked)
FEATURE [Part::Feature] Part__Feature393  label="LiPo battery 500 mAh163"
  Placement = pos=(-6e-15,47,-5) rot=(0,0,1;3.14159rad)
  shape: bbox 0.3004 x 0.1793 x 0.005 mm, 6 faces (baked)
FEATURE [Part::Feature] Part__Feature394  label="LiPo battery 500 mAh164"
  Placement = pos=(-6e-15,47,-5) rot=(0,0,1;3.14159rad)
  shape: bbox 0.3004 x 0.1808 x 0.005 mm, 6 faces (baked)
FEATURE [Part::Feature] Part__Feature395  label="LiPo battery 500 mAh165"
  Placement = pos=(-6e-15,47,-5) rot=(0,0,1;3.14159rad)
  shape: bbox 0.3004 x 0.1808 x 0.005 mm, 6 faces (baked)
FEATURE [Part::Feature] Part__Feature396  label="LiPo battery 500 mAh166"
  Placement = pos=(-6e-15,47,-5) rot=(0,0,1;3.14159rad)
  shape: bbox 0.3004 x 0.1808 x 0.005 mm, 6 faces (baked)
FEATURE [Part::Feature] Part__Feature397  label="LiPo battery 500 mAh167"
  Placement = pos=(-6e-15,47,-5) rot=(0,0,1;3.14159rad)
  shape: bbox 0.3004 x 0.1808 x 0.005 mm, 6 faces (baked)
FEATURE [Part::Feature] Part__Feature398  label="LiPo battery 500 mAh168"
  Placement = pos=(-6e-15,47,-5) rot=(0,0,1;3.14159rad)
  shape: bbox 0.3004 x 0.1808 x 0.005 mm, 6 faces (baked)
FEATURE [Part::Feature] Part__Feature399  label="LiPo battery 500 mAh169"
  Placement = pos=(-6e-15,47,-5) rot=(0,0,1;3.14159rad)
  shape: bbox 0.3004 x 0.1808 x 0.005 mm, 6 faces (baked)
FEATURE [Part::Feature] Part__Feature400  label="LiPo battery 500 mAh170"
  Placement = pos=(-6e-15,47,-5) rot=(0,0,1;3.14159rad)
  shape: bbox 0.3004 x 0.1793 x 0.005 mm, 6 faces (baked)
FEATURE [Part::Feature] Part__Feature401  label="LiPo battery 500 mAh171"
  Placement = pos=(-6e-15,47,-5) rot=(0,0,1;3.14159rad)
  shape: bbox 0.3004 x 0.1808 x 0.005 mm, 6 faces (baked)
FEATURE [Part::Feature] Part__Feature402  label="LiPo battery 500 mAh172"
  Placement = pos=(-6e-15,47,-5) rot=(0,0,1;3.14159rad)
  shape: bbox 0.3004 x 0.1808 x 0.005 mm, 6 faces (baked)
FEATURE [Part::Feature] Part__Feature403  label="LiPo battery 500 mAh173"
  Placement = pos=(-6e-15,47,-5) rot=(0,0,1;3.14159rad)
  shape: bbox 0.3004 x 0.1808 x 0.005 mm, 6 faces (baked)
FEATURE [Part::Feature] Part__Feature404  label="LiPo battery 500 mAh174"
  Placement = pos=(-6e-15,47,-5) rot=(0,0,1;3.14159rad)
  shape: bbox 0.3004 x 0.1808 x 0.005 mm, 6 faces (baked)
FEATURE [Part::Feature] Part__Feature405  label="LiPo battery 500 mAh175"
  Placement = pos=(-6e-15,47,-5) rot=(0,0,1;3.14159rad)
  shape: bbox 0.3004 x 0.1808 x 0.005 mm, 6 faces (baked)
FEATURE [Part::Feature] Part__Feature406  label="LiPo battery 500 mAh176"
  Placement = pos=(-6e-15,47,-5) rot=(0,0,1;3.14159rad)
  shape: bbox 0.3004 x 0.1793 x 0.005 mm, 6 faces (baked)
FEATURE [Part::Feature] Part__Feature407  label="LiPo battery 500 mAh177"
  Placement = pos=(-6e-15,47,-5) rot=(0,0,1;3.14159rad)
  shape: bbox 0.3004 x 0.1793 x 0.005 mm, 6 faces (baked)
FEATURE [Part::Feature] Part__Feature408  label="LiPo battery 500 mAh178"
  Placement = pos=(-6e-15,47,-5) rot=(0,0,1;3.14159rad)
  shape: bbox 0.3004 x 0.1793 x 0.005 mm, 6 faces (baked)
FEATURE [Part::Feature] Part__Feature409  label="LiPo battery 500 mAh179"
  Placement = pos=(-6e-15,47,-5) rot=(0,0,1;3.14159rad)
  shape: bbox 0.3004 x 0.1808 x 0.005 mm, 6 faces (baked)
FEATURE [Part::Feature] Part__Feature410  label="LiPo battery 500 mAh180"
  Placement = pos=(-6e-15,47,-5) rot=(0,0,1;3.14159rad)
  shape: bbox 0.3004 x 0.1808 x 0.005 mm, 6 faces (baked)
FEATURE [Part::Feature] Part__Feature411  label="LiPo battery 500 mAh181"
  Placement = pos=(-6e-15,47,-5) rot=(0,0,1;3.14159rad)
  shape: bbox 0.3004 x 0.1808 x 0.005 mm, 6 faces (baked)
FEATURE [Part::Feature] Part__Feature412  label="LiPo battery 500 mAh182"
  Placement = pos=(-6e-15,47,-5) rot=(0,0,1;3.14159rad)
  shape: bbox 0.3004 x 0.1808 x 0.005 mm, 6 faces (baked)
FEATURE [Part::Feature] Part__Feature413  label="LiPo battery 500 mAh183"
  Placement = pos=(-6e-15,47,-5) rot=(0,0,1;3.14159rad)
  shape: bbox 0.3004 x 0.1808 x 0.005 mm, 6 faces (baked)
FEATURE [Part::Feature] Part__Feature414  label="LiPo battery 500 mAh184"
  Placement = pos=(-6e-15,47,-5) rot=(0,0,1;3.14159rad)
  shape: bbox 0.3004 x 0.1808 x 0.005 mm, 6 faces (baked)
FEATURE [Part::Feature] Part__Feature415  label="LiPo battery 500 mAh185"
  Placement = pos=(-6e-15,47,-5) rot=(0,0,1;3.14159rad)
  shape: bbox 0.3004 x 0.1808 x 0.005 mm, 6 faces (baked)
FEATURE [Part::Feature] Part__Feature416  label="LiPo battery 500 mAh186"
  Placement = pos=(-6e-15,47,-5) rot=(0,0,1;3.14159rad)
  shape: bbox 0.3004 x 0.1793 x 0.005 mm, 6 faces (baked)
FEATURE [Part::Feature] Part__Feature417  label="LiPo battery 500 mAh187"
  Placement = pos=(-6e-15,47,-5) rot=(0,0,1;3.14159rad)
  shape: bbox 0.3004 x 0.1793 x 0.005 mm, 6 faces (baked)
FEATURE [Part::Feature] Part__Feature418  label="LiPo battery 500 mAh188"
  Placement = pos=(-6e-15,47,-5) rot=(0,0,1;3.14159rad)
  shape: bbox 0.3004 x 0.1793 x 0.005 mm, 6 faces (baked)
FEATURE [Part::Feature] Part__Feature419  label="LiPo battery 500 mAh189"
  Placement = pos=(-6e-15,47,-5) rot=(0,0,1;3.14159rad)
  shape: bbox 0.3004 x 0.1808 x 0.005 mm, 6 faces (baked)
FEATURE [Part::Feature] Part__Feature420  label="LiPo battery 500 mAh190"
  Placement = pos=(-6e-15,47,-5) rot=(0,0,1;3.14159rad)
  shape: bbox 0.3004 x 0.1808 x 0.005 mm, 6 faces (baked)
FEATURE [Part::Feature] Part__Feature421  label="LiPo battery 500 mAh191"
  Placement = pos=(-6e-15,47,-5) rot=(0,0,1;3.14159rad)
  shape: bbox 0.3004 x 0.1808 x 0.005 mm, 6 faces (baked)
FEATURE [Part::Feature] Part__Feature422  label="LiPo battery 500 mAh192"
  Placement = pos=(-6e-15,47,-5) rot=(0,0,1;3.14159rad)
  shape: bbox 0.3004 x 0.1808 x 0.005 mm, 6 faces (baked)
FEATURE [Part::Feature] Part__Feature423  label="LiPo battery 500 mAh193"
  Placement = pos=(-6e-15,47,-5) rot=(0,0,1;3.14159rad)
  shape: bbox 0.3004 x 0.1808 x 0.005 mm, 6 faces (baked)
FEATURE [Part::Feature] Part__Feature424  label="LiPo battery 500 mAh194"
  Placement = pos=(-6e-15,47,-5) rot=(0,0,1;3.14159rad)
  shape: bbox 0.3004 x 0.1808 x 0.005 mm, 6 faces (baked)
FEATURE [Part::Feature] Part__Feature425  label="LiPo battery 500 mAh195"
  Placement = pos=(-6e-15,47,-5) rot=(0,0,1;3.14159rad)
  shape: bbox 0.3004 x 0.1793 x 0.005 mm, 6 faces (baked)
FEATURE [Part::Feature] Part__Feature426  label="LiPo battery 500 mAh196"
  Placement = pos=(-6e-15,47,-5) rot=(0,0,1;3.14159rad)
  shape: bbox 0.3004 x 0.1793 x 0.005 mm, 6 faces (baked)
FEATURE [Part::Feature] Part__Feature427  label="LiPo battery 500 mAh197"
  Placement = pos=(-6e-15,47,-5) rot=(0,0,1;3.14159rad)
  shape: bbox 0.3004 x 0.1793 x 0.005 mm, 6 faces (baked)
FEATURE [Part::Feature] Part__Feature428  label="LiPo battery 500 mAh198"
  Placement = pos=(-6e-15,47,-5) rot=(0,0,1;3.14159rad)
  shape: bbox 0.3004 x 0.1808 x 0.005 mm, 6 faces (baked)
FEATURE [Part::Feature] Part__Feature429  label="LiPo battery 500 mAh199"
  Placement = pos=(-6e-15,47,-5) rot=(0,0,1;3.14159rad)
  shape: bbox 0.3004 x 0.1808 x 0.005 mm, 6 faces (baked)
FEATURE [Part::Feature] Part__Feature430  label="LiPo battery 500 mAh200"
  Placement = pos=(-6e-15,47,-5) rot=(0,0,1;3.14159rad)
  shape: bbox 0.3004 x 0.1808 x 0.005 mm, 6 faces (baked)
FEATURE [Part::Feature] Part__Feature431  label="LiPo battery 500 mAh201"
  Placement = pos=(-6e-15,47,-5) rot=(0,0,1;3.14159rad)
  shape: bbox 0.3004 x 0.1808 x 0.005 mm, 6 faces (baked)
FEATURE [Part::Feature] Part__Feature432  label="LiPo battery 500 mAh202"
  Placement = pos=(-6e-15,47,-5) rot=(0,0,1;3.14159rad)
  shape: bbox 0.3004 x 0.1808 x 0.005 mm, 6 faces (baked)
FEATURE [Part::Feature] Part__Feature433  label="LiPo battery 500 mAh203"
  Placement = pos=(-6e-15,47,-5) rot=(0,0,1;3.14159rad)
  shape: bbox 0.3004 x 0.1808 x 0.005 mm, 6 faces (baked)
FEATURE [Part::Feature] Part__Feature434  label="LiPo battery 500 mAh204"
  Placement = pos=(-6e-15,47,-5) rot=(0,0,1;3.14159rad)
  shape: bbox 0.3004 x 0.1793 x 0.005 mm, 6 faces (baked)
FEATURE [Part::Feature] Part__Feature435  label="LiPo battery 500 mAh205"
  Placement = pos=(-6e-15,47,-5) rot=(0,0,1;3.14159rad)
  shape: bbox 0.3004 x 0.1808 x 0.005 mm, 6 faces (baked)
FEATURE [Part::Feature] Part__Feature436  label="LiPo battery 500 mAh206"
  Placement = pos=(-6e-15,47,-5) rot=(0,0,1;3.14159rad)
  shape: bbox 0.3004 x 0.1808 x 0.005 mm, 6 faces (baked)
FEATURE [Part::Feature] Part__Feature437  label="LiPo battery 500 mAh207"
  Placement = pos=(-6e-15,47,-5) rot=(0,0,1;3.14159rad)
  shape: bbox 0.3004 x 0.1808 x 0.005 mm, 6 faces (baked)
FEATURE [Part::Feature] Part__Feature438  label="LiPo battery 500 mAh208"
  Placement = pos=(-6e-15,47,-5) rot=(0,0,1;3.14159rad)
  shape: bbox 0.3004 x 0.1808 x 0.005 mm, 6 faces (baked)
FEATURE [Part::Feature] Part__Feature439  label="LiPo battery 500 mAh209"
  Placement = pos=(-6e-15,47,-5) rot=(0,0,1;3.14159rad)
  shape: bbox 0.3004 x 0.1808 x 0.005 mm, 6 faces (baked)
FEATURE [Part::Feature] Part__Feature440  label="LiPo battery 500 mAh210"
  Placement = pos=(-6e-15,47,-5) rot=(0,0,1;3.14159rad)
  shape: bbox 0.3004 x 0.1808 x 0.005 mm, 6 faces (baked)
FEATURE [Part::Feature] Part__Feature441  label="LiPo battery 500 mAh211"
  Placement = pos=(-6e-15,47,-5) rot=(0,0,1;3.14159rad)
  shape: bbox 0.3004 x 0.1793 x 0.005 mm, 6 faces (baked)
FEATURE [Part::Feature] Part__Feature442  label="LiPo battery 500 mAh212"
  Placement = pos=(-6e-15,47,-5) rot=(0,0,1;3.14159rad)
  shape: bbox 0.3004 x 0.1793 x 0.005 mm, 6 faces (baked)
FEATURE [Part::Feature] Part__Feature443  label="LiPo battery 500 mAh213"
  Placement = pos=(-6e-15,47,-5) rot=(0,0,1;3.14159rad)
  shape: bbox 0.3004 x 0.1808 x 0.005 mm, 6 faces (baked)
FEATURE [Part::Feature] Part__Feature444  label="LiPo battery 500 mAh214"
  Placement = pos=(-6e-15,47,-5) rot=(0,0,1;3.14159rad)
  shape: bbox 0.3004 x 0.1808 x 0.005 mm, 6 faces (baked)
FEATURE [Part::Feature] Part__Feature445  label="LiPo battery 500 mAh215"
  Placement = pos=(-6e-15,47,-5) rot=(0,0,1;3.14159rad)
  shape: bbox 0.3004 x 0.1808 x 0.005 mm, 6 faces (baked)
FEATURE [Part::Feature] Part__Feature446  label="LiPo battery 500 mAh216"
  Placement = pos=(-6e-15,47,-5) rot=(0,0,1;3.14159rad)
  shape: bbox 0.3004 x 0.1808 x 0.005 mm, 6 faces (baked)
FEATURE [Part::Feature] Part__Feature447  label="LiPo battery 500 mAh217"
  Placement = pos=(-6e-15,47,-5) rot=(0,0,1;3.14159rad)
  shape: bbox 0.3004 x 0.1808 x 0.005 mm, 6 faces (baked)
FEATURE [Part::Feature] Part__Feature448  label="LiPo battery 500 mAh218"
  Placement = pos=(-6e-15,47,-5) rot=(0,0,1;3.14159rad)
  shape: bbox 0.3004 x 0.1808 x 0.005 mm, 6 faces (baked)
FEATURE [Part::Feature] Part__Feature449  label="LiPo battery 500 mAh219"
  Placement = pos=(-6e-15,47,-5) rot=(0,0,1;3.14159rad)
  shape: bbox 0.3004 x 0.1808 x 0.005 mm, 6 faces (baked)
FEATURE [Part::Feature] Part__Feature450  label="LiPo battery 500 mAh220"
  Placement = pos=(-6e-15,47,-5) rot=(0,0,1;3.14159rad)
  shape: bbox 0.3004 x 0.1808 x 0.005 mm, 6 faces (baked)
FEATURE [Part::Feature] Part__Feature451  label="LiPo battery 500 mAh221"
  Placement = pos=(-6e-15,47,-5) rot=(0,0,1;3.14159rad)
  shape: bbox 0.3004 x 0.1793 x 0.005 mm, 6 faces (baked)
FEATURE [Part::Feature] Part__Feature452  label="LiPo battery 500 mAh222"
  Placement = pos=(-6e-15,47,-5) rot=(0,0,1;3.14159rad)
  shape: bbox 0.3004 x 0.1808 x 0.005 mm, 6 faces (baked)
FEATURE [Part::Feature] Part__Feature453  label="LiPo battery 500 mAh223"
  Placement = pos=(-6e-15,47,-5) rot=(0,0,1;3.14159rad)
  shape: bbox 0.3004 x 0.1808 x 0.005 mm, 6 faces (baked)
FEATURE [Part::Feature] Part__Feature454  label="LiPo battery 500 mAh224"
  Placement = pos=(-6e-15,47,-5) rot=(0,0,1;3.14159rad)
  shape: bbox 0.3004 x 0.1808 x 0.005 mm, 6 faces (baked)
FEATURE [Part::Feature] Part__Feature455  label="LiPo battery 500 mAh225"
  Placement = pos=(-6e-15,47,-5) rot=(0,0,1;3.14159rad)
  shape: bbox 0.3004 x 0.1808 x 0.005 mm, 6 faces (baked)
FEATURE [Part::Feature] Part__Feature456  label="LiPo battery 500 mAh226"
  Placement = pos=(-6e-15,47,-5) rot=(0,0,1;3.14159rad)
  shape: bbox 0.3004 x 0.1793 x 0.005 mm, 6 faces (baked)
FEATURE [Part::Feature] Part__Feature457  label="LiPo battery 500 mAh227"
  Placement = pos=(-6e-15,47,-5) rot=(0,0,1;3.14159rad)
  shape: bbox 0.3004 x 0.1793 x 0.005 mm, 6 faces (baked)
FEATURE [Part::Feature] Part__Feature458  label="LiPo battery 500 mAh228"
  Placement = pos=(-6e-15,47,-5) rot=(0,0,1;3.14159rad)
  shape: bbox 0.3004 x 0.1793 x 0.005 mm, 6 faces (baked)
FEATURE [Part::Feature] Part__Feature459  label="LiPo battery 500 mAh229"
  Placement = pos=(-6e-15,47,-5) rot=(0,0,1;3.14159rad)
  shape: bbox 0.3004 x 0.1808 x 0.005 mm, 6 faces (baked)
FEATURE [Part::Feature] Part__Feature460  label="LiPo battery 500 mAh230"
  Placement = pos=(-6e-15,47,-5) rot=(0,0,1;3.14159rad)
  shape: bbox 0.3004 x 0.1808 x 0.005 mm, 6 faces (baked)
FEATURE [Part::Feature] Part__Feature461  label="LiPo battery 500 mAh231"
  Placement = pos=(-6e-15,47,-5) rot=(0,0,1;3.14159rad)
  shape: bbox 0.3004 x 0.1808 x 0.005 mm, 6 faces (baked)
FEATURE [Part::Feature] Part__Feature462  label="LiPo battery 500 mAh232"
  Placement = pos=(-6e-15,47,-5) rot=(0,0,1;3.14159rad)
  shape: bbox 0.3004 x 0.1808 x 0.005 mm, 6 faces (baked)
FEATURE [Part::Feature] Part__Feature463  label="LiPo battery 500 mAh233"
  Placement = pos=(-6e-15,47,-5) rot=(0,0,1;3.14159rad)
  shape: bbox 0.3004 x 0.1808 x 0.005 mm, 6 faces (baked)
FEATURE [Part::Feature] Part__Feature464  label="LiPo battery 500 mAh234"
  Placement = pos=(-6e-15,47,-5) rot=(0,0,1;3.14159rad)
  shape: bbox 0.3004 x 0.1808 x 0.005 mm, 6 faces (baked)
FEATURE [Part::Feature] Part__Feature465  label="LiPo battery 500 mAh235"
  Placement = pos=(-6e-15,47,-5) rot=(0,0,1;3.14159rad)
  shape: bbox 0.3004 x 0.1808 x 0.005 mm, 6 faces (baked)
FEATURE [Part::Feature] Part__Feature466  label="LiPo battery 500 mAh236"
  Placement = pos=(-6e-15,47,-5) rot=(0,0,1;3.14159rad)
  shape: bbox 0.3004 x 0.1793 x 0.005 mm, 6 faces (baked)
FEATURE [Part::Feature] Part__Feature467  label="LiPo battery 500 mAh237"
  Placement = pos=(-6e-15,47,-5) rot=(0,0,1;3.14159rad)
  shape: bbox 0.3004 x 0.1793 x 0.005 mm, 6 faces (baked)
FEATURE [Part::Feature] Part__Feature468  label="LiPo battery 500 mAh238"
  Placement = pos=(-6e-15,47,-5) rot=(0,0,1;3.14159rad)
  shape: bbox 0.3004 x 0.1793 x 0.005 mm, 6 faces (baked)
FEATURE [Part::Feature] Part__Feature469  label="LiPo battery 500 mAh239"
  Placement = pos=(-6e-15,47,-5) rot=(0,0,1;3.14159rad)
  shape: bbox 0.3004 x 0.1808 x 0.005 mm, 6 faces (baked)
FEATURE [Part::Feature] Part__Feature470  label="LiPo battery 500 mAh240"
  Placement = pos=(-6e-15,47,-5) rot=(0,0,1;3.14159rad)
  shape: bbox 0.3004 x 0.1808 x 0.005 mm, 6 faces (baked)
FEATURE [Part::Feature] Part__Feature471  label="LiPo battery 500 mAh241"
  Placement = pos=(-6e-15,47,-5) rot=(0,0,1;3.14159rad)
  shape: bbox 0.3004 x 0.1808 x 0.005 mm, 6 faces (baked)
FEATURE [Part::Feature] Part__Feature472  label="LiPo battery 500 mAh242"
  Placement = pos=(-6e-15,47,-5) rot=(0,0,1;3.14159rad)
  shape: bbox 0.3004 x 0.1793 x 0.005 mm, 6 faces (baked)
FEATURE [Part::Feature] Part__Feature473  label="LiPo battery 500 mAh243"
  Placement = pos=(-6e-15,47,-5) rot=(0,0,1;3.14159rad)
  shape: bbox 0.3004 x 0.1793 x 0.005 mm, 6 faces (baked)
FEATURE [Part::Feature] Part__Feature474  label="LiPo battery 500 mAh244"
  Placement = pos=(-6e-15,47,-5) rot=(0,0,1;3.14159rad)
  shape: bbox 0.3004 x 0.1808 x 0.005 mm, 6 faces (baked)
FEATURE [Part::Feature] Part__Feature475  label="LiPo battery 500 mAh245"
  Placement = pos=(-6e-15,47,-5) rot=(0,0,1;3.14159rad)
  shape: bbox 0.3004 x 0.1808 x 0.005 mm, 6 faces (baked)
FEATURE [Part::Feature] Part__Feature476  label="LiPo battery 500 mAh246"
  Placement = pos=(-6e-15,47,-5) rot=(0,0,1;3.14159rad)
  shape: bbox 0.3004 x 0.1808 x 0.005 mm, 6 faces (baked)
FEATURE [Part::Feature] Part__Feature477  label="LiPo battery 500 mAh247"
  Placement = pos=(-6e-15,47,-5) rot=(0,0,1;3.14159rad)
  shape: bbox 0.3004 x 0.1808 x 0.005 mm, 6 faces (baked)
FEATURE [Part::Feature] Part__Feature478  label="LiPo battery 500 mAh248"
  Placement = pos=(-6e-15,47,-5) rot=(0,0,1;3.14159rad)
  shape: bbox 0.3004 x 0.1808 x 0.005 mm, 6 faces (baked)
FEATURE [Part::Feature] Part__Feature479  label="LiPo battery 500 mAh249"
  Placement = pos=(-6e-15,47,-5) rot=(0,0,1;3.14159rad)
  shape: bbox 0.3004 x 0.1793 x 0.005 mm, 6 faces (baked)
FEATURE [Part::Feature] Part__Feature480  label="LiPo battery 500 mAh250"
  Placement = pos=(-6e-15,47,-5) rot=(0,0,1;3.14159rad)
  shape: bbox 0.3004 x 0.1793 x 0.005 mm, 6 faces (baked)
FEATURE [Part::Feature] Part__Feature481  label="LiPo battery 500 mAh251"
  Placement = pos=(-6e-15,47,-5) rot=(0,0,1;3.14159rad)
  shape: bbox 0.3004 x 0.1793 x 0.005 mm, 6 faces (baked)
FEATURE [Part::Feature] Part__Feature482  label="LiPo battery 500 mAh252"
  Placement = pos=(-6e-15,47,-5) rot=(0,0,1;3.14159rad)
  shape: bbox 0.3004 x 0.1808 x 0.005 mm, 6 faces (baked)
FEATURE [Part::Feature] Part__Feature483  label="LiPo battery 500 mAh253"
  Placement = pos=(-6e-15,47,-5) rot=(0,0,1;3.14159rad)
  shape: bbox 0.3004 x 0.1808 x 0.005 mm, 6 faces (baked)
FEATURE [Part::Feature] Part__Feature484  label="LiPo battery 500 mAh254"
  Placement = pos=(-6e-15,47,-5) rot=(0,0,1;3.14159rad)
  shape: bbox 0.3004 x 0.1793 x 0.005 mm, 6 faces (baked)
FEATURE [Part::Feature] Part__Feature485  label="LiPo battery 500 mAh255"
  Placement = pos=(-6e-15,47,-5) rot=(0,0,1;3.14159rad)
  shape: bbox 0.3004 x 0.1808 x 0.005 mm, 6 faces (baked)
FEATURE [Part::Feature] Part__Feature486  label="LiPo battery 500 mAh256"
  Placement = pos=(-6e-15,47,-5) rot=(0,0,1;3.14159rad)
  shape: bbox 0.3004 x 0.1808 x 0.005 mm, 6 faces (baked)
FEATURE [Part::Feature] Part__Feature487  label="LiPo battery 500 mAh257"
  Placement = pos=(-6e-15,47,-5) rot=(0,0,1;3.14159rad)
  shape: bbox 0.3004 x 0.1808 x 0.005 mm, 6 faces (baked)
FEATURE [Part::Feature] Part__Feature488  label="LiPo battery 500 mAh258"
  Placement = pos=(-6e-15,47,-5) rot=(0,0,1;3.14159rad)
  shape: bbox 0.3004 x 0.1808 x 0.005 mm, 6 faces (baked)
FEATURE [Part::Feature] Part__Feature489  label="LiPo battery 500 mAh259"
  Placement = pos=(-6e-15,47,-5) rot=(0,0,1;3.14159rad)
  shape: bbox 0.3004 x 0.1808 x 0.005 mm, 6 faces (baked)
FEATURE [Part::Feature] Part__Feature490  label="LiPo battery 500 mAh260"
  Placement = pos=(-6e-15,47,-5) rot=(0,0,1;3.14159rad)
  shape: bbox 0.3004 x 0.1808 x 0.005 mm, 6 faces (baked)
FEATURE [Part::Feature] Part__Feature491  label="LiPo battery 500 mAh261"
  Placement = pos=(-6e-15,47,-5) rot=(0,0,1;3.14159rad)
  shape: bbox 0.3004 x 0.1793 x 0.005 mm, 6 faces (baked)
FEATURE [Part::Feature] Part__Feature492  label="LiPo battery 500 mAh262"
  Placement = pos=(-6e-15,47,-5) rot=(0,0,1;3.14159rad)
  shape: bbox 0.3004 x 0.1793 x 0.005 mm, 6 faces (baked)
FEATURE [Part::Feature] Part__Feature493  label="LiPo battery 500 mAh263"
  Placement = pos=(-6e-15,47,-5) rot=(0,0,1;3.14159rad)
  shape: bbox 0.3004 x 0.1793 x 0.005 mm, 6 faces (baked)
FEATURE [Part::Feature] Part__Feature494  label="LiPo battery 500 mAh264"
  Placement = pos=(-6e-15,47,-5) rot=(0,0,1;3.14159rad)
  shape: bbox 0.3004 x 0.1808 x 0.005 mm, 6 faces (baked)
FEATURE [Part::Feature] Part__Feature495  label="LiPo battery 500 mAh265"
  Placement = pos=(-6e-15,47,-5) rot=(0,0,1;3.14159rad)
  shape: bbox 0.3004 x 0.1808 x 0.005 mm, 6 faces (baked)
FEATURE [Part::Feature] Part__Feature496  label="LiPo battery 500 mAh266"
  Placement = pos=(-6e-15,47,-5) rot=(0,0,1;3.14159rad)
  shape: bbox 0.3004 x 0.1808 x 0.005 mm, 6 faces (baked)
FEATURE [Part::Feature] Part__Feature497  label="LiPo battery 500 mAh267"
  Placement = pos=(-6e-15,47,-5) rot=(0,0,1;3.14159rad)
  shape: bbox 0.3004 x 0.1808 x 0.005 mm, 6 faces (baked)
FEATURE [Part::Feature] Part__Feature498  label="LiPo battery 500 mAh268"
  Placement = pos=(-6e-15,47,-5) rot=(0,0,1;3.14159rad)
  shape: bbox 0.3004 x 0.1808 x 0.005 mm, 6 faces (baked)
FEATURE [Part::Feature] Part__Feature499  label="LiPo battery 500 mAh269"
  Placement = pos=(-6e-15,47,-5) rot=(0,0,1;3.14159rad)
  shape: bbox 0.3004 x 0.1808 x 0.005 mm, 6 faces (baked)
FEATURE [Part::Feature] Part__Feature500  label="LiPo battery 500 mAh270"
  Placement = pos=(-6e-15,47,-5) rot=(0,0,1;3.14159rad)
  shape: bbox 0.3004 x 0.1793 x 0.005 mm, 6 faces (baked)
FEATURE [Part::Feature] Part__Feature501  label="LiPo battery 500 mAh271"
  Placement = pos=(-6e-15,47,-5) rot=(0,0,1;3.14159rad)
  shape: bbox 0.3004 x 0.1793 x 0.005 mm, 6 faces (baked)
FEATURE [Part::Feature] Part__Feature502  label="LiPo battery 500 mAh272"
  Placement = pos=(-6e-15,47,-5) rot=(0,0,1;3.14159rad)
  shape: bbox 0.3004 x 0.1793 x 0.005 mm, 6 faces (baked)
FEATURE [Part::Feature] Part__Feature503  label="LiPo battery 500 mAh273"
  Placement = pos=(-6e-15,47,-5) rot=(0,0,1;3.14159rad)
  shape: bbox 0.3004 x 0.1808 x 0.005 mm, 6 faces (baked)
FEATURE [Part::Feature] Part__Feature504  label="LiPo battery 500 mAh274"
  Placement = pos=(-6e-15,47,-5) rot=(0,0,1;3.14159rad)
  shape: bbox 0.3004 x 0.1793 x 0.005 mm, 6 faces (baked)
FEATURE [Part::Feature] Part__Feature505  label="LiPo battery 500 mAh275"
  Placement = pos=(-6e-15,47,-5) rot=(0,0,1;3.14159rad)
  shape: bbox 0.3004 x 0.1808 x 0.005 mm, 6 faces (baked)
FEATURE [Part::Feature] Part__Feature506  label="LiPo battery 500 mAh276"
  Placement = pos=(-6e-15,47,-5) rot=(0,0,1;3.14159rad)
  shape: bbox 0.3004 x 0.1808 x 0.005 mm, 6 faces (baked)
FEATURE [Part::Feature] Part__Feature507  label="LiPo battery 500 mAh277"
  Placement = pos=(-6e-15,47,-5) rot=(0,0,1;3.14159rad)
  shape: bbox 0.3004 x 0.1808 x 0.005 mm, 6 faces (baked)
FEATURE [Part::Feature] Part__Feature508  label="LiPo battery 500 mAh278"
  Placement = pos=(-6e-15,47,-5) rot=(0,0,1;3.14159rad)
  shape: bbox 0.3004 x 0.1808 x 0.005 mm, 6 faces (baked)
FEATURE [Part::Feature] Part__Feature509  label="LiPo battery 500 mAh279"
  Placement = pos=(-6e-15,47,-5) rot=(0,0,1;3.14159rad)
  shape: bbox 0.3004 x 0.1793 x 0.005 mm, 6 faces (baked)
FEATURE [Part::Feature] Part__Feature510  label="LiPo battery 500 mAh280"
  Placement = pos=(-6e-15,47,-5) rot=(0,0,1;3.14159rad)
  shape: bbox 0.3004 x 0.1808 x 0.005 mm, 6 faces (baked)
FEATURE [Part::Feature] Part__Feature511  label="LiPo battery 500 mAh281"
  Placement = pos=(-6e-15,47,-5) rot=(0,0,1;3.14159rad)
  shape: bbox 0.3004 x 0.1808 x 0.005 mm, 6 faces (baked)
FEATURE [Part::Feature] Part__Feature512  label="LiPo battery 500 mAh282"
  Placement = pos=(-6e-15,47,-5) rot=(0,0,1;3.14159rad)
  shape: bbox 0.3004 x 0.1808 x 0.005 mm, 6 faces (baked)
FEATURE [Part::Feature] Part__Feature513  label="LiPo battery 500 mAh283"
  Placement = pos=(-6e-15,47,-5) rot=(0,0,1;3.14159rad)
  shape: bbox 0.3004 x 0.1808 x 0.005 mm, 6 faces (baked)
FEATURE [Part::Feature] Part__Feature514  label="LiPo battery 500 mAh284"
  Placement = pos=(-6e-15,47,-5) rot=(0,0,1;3.14159rad)
  shape: bbox 0.3004 x 0.1808 x 0.005 mm, 6 faces (baked)
FEATURE [Part::Feature] Part__Feature515  label="LiPo battery 500 mAh285"
  Placement = pos=(-6e-15,47,-5) rot=(0,0,1;3.14159rad)
  shape: bbox 0.3004 x 0.1808 x 0.005 mm, 6 faces (baked)
FEATURE [Part::Feature] Part__Feature516  label="LiPo battery 500 mAh286"
  Placement = pos=(-6e-15,47,-5) rot=(0,0,1;3.14159rad)
  shape: bbox 0.3004 x 0.1793 x 0.005 mm, 6 faces (baked)
FEATURE [Part::Feature] Part__Feature517  label="LiPo battery 500 mAh287"
  Placement = pos=(-6e-15,47,-5) rot=(0,0,1;3.14159rad)
  shape: bbox 0.3004 x 0.1793 x 0.005 mm, 6 faces (baked)
FEATURE [Part::Feature] Part__Feature518  label="LiPo battery 500 mAh288"
  Placement = pos=(-6e-15,47,-5) rot=(0,0,1;3.14159rad)
  shape: bbox 0.3004 x 0.1793 x 0.005 mm, 6 faces (baked)
FEATURE [App::DocumentObjectGroup] Grupo021  label="battery 3,7 V 500 mah"
  Group = -> [Part__Feature230,Part__Feature231,Part__Feature232,Part__Feature233,Part__Feature234,Part__Feature235,Part__Feature236,Part__Feature237,Part__Feature238,Part__Feature239,Part__Feature240,Part__Feature241,Part__Feature242,Part__Feature243,Part__Feature244,Part__Feature245,Part__Feature246,Part__Feature247,Part__Feature248,Part__Feature249,Part__Feature250,Part__Feature251,Part__Feature252,+266 more]
FEATURE [Part::FeaturePython] Clone029  label="Clone of plus_wire"  # WARN: FeaturePython — macro-defined, semantics opaque (R4)
  Placement = pos=(-2.5,22,-1.4) rot=(0,0,1;1.5708rad)
  Scale = (1,1,1)
FEATURE [Part::FeaturePython] Clone002  label="Clone of celonfan_rounded_2"  # WARN: FeaturePython — macro-defined, semantics opaque (R4)
  Placement = pos=(15,30,-6.5) rot=(0,0,1;1.5708rad)
  Scale = (1,1,1)
FEATURE [Part::FeaturePython] Clone004  label="Clone of celofan_rounded"  # WARN: FeaturePython — macro-defined, semantics opaque (R4)
  Placement = pos=(15,30,-2) rot=(0,0,1;1.5708rad)
  Scale = (1,1,1)
FEATURE [Part::Part2DObjectPython] Clone2D  label="Clone of data_text (2D)"  # Draft 2D object (typed FeaturePython)
  MapMode = 5
  Placement = pos=(-7.613,55.4561,-0.5) rot=(0,0,1;1.5708rad)
  Scale = (1,1,1)
FEATURE [Part::FeaturePython] Clone001  label="Clone of minus_wire"  # WARN: FeaturePython — macro-defined, semantics opaque (R4)
  Placement = pos=(2.5,22,-1.4) rot=(0,0,1;1.5708rad)
  Scale = (1,1,1)
FEATURE [Part::FeaturePython] Clone003  label="Clone of battery_rounded"  # WARN: FeaturePython — macro-defined, semantics opaque (R4)
  Placement = pos=(15,30,-6.5) rot=(0,0,1;1.5708rad)
  Scale = (1,1,1)
FEATURE [App::DocumentObjectGroup] Grupo022  label="battery_3_7v_240mah"
  Group = -> [Clone004,Clone003,Clone029,Clone002,Clone2D,Clone001]
FEATURE [Part::FeaturePython] Clone030  label="Clone of celofan_rounded001"  # WARN: FeaturePython — macro-defined, semantics opaque (R4)
  Placement = pos=(15,30,-8.5) rot=(0,0,1;1.5708rad)
  Scale = (1,1,1)
FEATURE [Part::FeaturePython] Clone031  label="Clone of battery_rounded001"  # WARN: FeaturePython — macro-defined, semantics opaque (R4)
  Placement = pos=(15,30,-13) rot=(0,0,1;1.5708rad)
  Scale = (1,1,1)
FEATURE [Part::FeaturePython] Clone032  label="Clone of plus_wire001"  # WARN: FeaturePython — macro-defined, semantics opaque (R4)
  Placement = pos=(-2.5,22,-7.9) rot=(0,0,1;1.5708rad)
  Scale = (1,1,1)
FEATURE [Part::FeaturePython] Clone033  label="Clone of celonfan_rounded_003"  # WARN: FeaturePython — macro-defined, semantics opaque (R4)
  Placement = pos=(15,30,-13) rot=(0,0,1;1.5708rad)
  Scale = (1,1,1)
FEATURE [Part::Part2DObjectPython] Clone2D001  label="Clone of data_text (2D)001"  # Draft 2D object (typed FeaturePython)
  MapMode = 5
  Placement = pos=(-7.613,55.4561,-7) rot=(0,0,1;1.5708rad)
  Scale = (1,1,1)
FEATURE [Part::FeaturePython] Clone034  label="Clone of minus_wire001"  # WARN: FeaturePython — macro-defined, semantics opaque (R4)
  Placement = pos=(2.5,22,-7.9) rot=(0,0,1;1.5708rad)
  Scale = (1,1,1)
FEATURE [App::DocumentObjectGroup] Grupo023  label="batterry_2_3_7v_240mah"
  Group = -> [Clone034,Clone031,Clone2D001,Clone030,Clone032,Clone033]
FEATURE [App::DocumentObjectGroup] Grupo020  label="lipo_battery"
  Group = -> [Grupo021,Grupo022,Grupo023]
FEATURE [Part::Feature] Fusion007024  label="hex-m3-30mm001"
  shape: bbox 5.5 x 5.5 x 33 mm, 16 faces (baked)
FEATURE [Part::Feature] Chamfer019  label="hex-m2-4mm001"
  shape: bbox 5.445 x 6.287 x 6.3 mm, 16 faces (baked)
FEATURE [Part::Feature] Chamfer020  label="hex-m2-6mm001"
  shape: bbox 5.445 x 6.287 x 7.5 mm, 16 faces (baked)
FEATURE [Part::Feature] Part__Feature172  label="m3-nut001"
  Placement = pos=(17.5,5,29) rot=(0,0,1;0.523599rad)
  shape: bbox 6.35 x 6.35 x 2.4 mm, 29 faces (baked)
FEATURE [Part::Feature] Part__Feature173  label="m3-nut002"
  Placement = pos=(17.5,6.5,29) rot=(0,0,1;0.191986rad)
  shape: bbox 6.35 x 6.35 x 2.4 mm, 29 faces (baked)
FEATURE [App::DocumentObjectGroup] Grupo015  label="screws_nuts001"
  Group = -> [Fusion007024,Chamfer020,Chamfer019,Part__Feature172,Part__Feature173]
FEATURE [Part::Feature] Part__Feature519  label="Nyloc-nut-M3"
  shape: bbox 6.35 x 6.35 x 3.86 mm, 32 faces (baked)
FEATURE [Part::Feature] Part__Feature520  label="Nyloc-nut-M004"
  shape: bbox 3.5 x 3.5 x 0.95 mm, 4 faces (baked)
FEATURE [Part::MultiFuse] Fusion007031  label="m3-nyloc-nut"
  Refine = true
  Shapes = -> [Part__Feature519,Part__Feature520]
FEATURE [Part::Feature] Part__Feature521  label="m3-nut003"
  Placement = pos=(0,0,0) rot=(0,0,1;0.523599rad)
  shape: bbox 6.35 x 6.35 x 2.4 mm, 29 faces (baked)
FEATURE [Part::Feature] Part__Feature522  label="hex-bolt"
  shape: bbox 5.5 x 5.5 x 13 mm, 16 faces (baked)
FEATURE [Part::Feature] Fusion007032  label="hex-m3-30mm002"
  shape: bbox 5.5 x 5.5 x 33 mm, 16 faces (baked)
FEATURE [Part::Feature] Chamfer010  label="hex-m3-8mm"
  Placement = pos=(160,0,0) rot=(0,0,1;0rad)
  shape: bbox 5.5 x 5.5 x 11 mm, 16 faces (baked)
FEATURE [Part::Feature] Chamfer021  label="hex-m2-4mm002"
  shape: bbox 5.445 x 6.287 x 6.3 mm, 16 faces (baked)
FEATURE [Part::Feature] Chamfer022  label="hex-m2-6mm002"
  shape: bbox 5.445 x 6.287 x 7.5 mm, 16 faces (baked)
FEATURE [App::DocumentObjectGroup] Grupo025  label="bolts and nuts"
  Group = -> [Chamfer010,Fusion007031,Part__Feature521,Part__Feature522,Fusion007032,Chamfer021,Chamfer022]
FEATURE [App::DocumentObjectGroup] Grupo026  label="screws_nuts"
  Group = -> [Grupo025,Grupo015]
FEATURE [Part::Feature] Part__Feature635  label="R_0402_038"
  Placement = pos=(-10.5283,-5.1855,26.1) rot=(0,0,1;3.14159rad)
  shape: bbox 1 x 0.5 x 0.3 mm, 40 faces (baked)
FEATURE [Part::Feature] Part__Feature524  label="Pcb007"
  Placement = pos=(-115.57,-125.01,26.1) rot=(0,0,1;1.5708rad)
  shape: bbox 53.34 x 68.58 x 1.6 mm, 170 faces (baked)
FEATURE [Part::Feature] Part__Feature525  label="LED_0603_009"
  Placement = pos=(-14.13,-25.59,26.1) rot=(0,0,1;1.5708rad)
  shape: bbox 0.725 x 1.65 x 0.675 mm, 50 faces (baked)
FEATURE [Part::Feature] Part__Feature526  label="LED_0603_010"
  Placement = pos=(-18.63,-25.57,26.1) rot=(0,0,1;1.5708rad)
  shape: bbox 0.725 x 1.65 x 0.675 mm, 50 faces (baked)
FEATURE [Part::Feature] Part__Feature527  label="1x10-socket-header_001"
  Placement = pos=(-24.13,13.166,26.1) rot=(0,0,1;1.5708rad)
  shape: bbox 2.54 x 25.4 x 11.85 mm, 186 faces (baked)
FEATURE [Part::Feature] Part__Feature528  label="1x6-male-pin-header-gray_002"
  Placement = pos=(14.605,18.5,26.1) rot=(0,0,-1;1.5708rad)
  shape: bbox 2.54 x 15.24 x 11.2 mm, 210 faces (baked)
FEATURE [Part::Feature] Part__Feature529  label="1x8-socket-header_002"
  Placement = pos=(-24.13,35.01,26.1) rot=(0,0,1;1.5708rad)
  shape: bbox 2.54 x 20.32 x 11.85 mm, 150 faces (baked)
FEATURE [Part::Feature] Part__Feature530  label="1x8-male-pin-header_001"
  Placement = pos=(-19.685,35.01,26.1) rot=(0,0,1;1.5708rad)
  shape: bbox 2.54 x 20.32 x 11.2 mm, 278 faces (baked)
FEATURE [Part::Feature] Part__Feature531  label="1x6-male-pin-header-red_002"
  Placement = pos=(17.145,18.5,26.1) rot=(0,0,-1;1.5708rad)
  shape: bbox 2.54 x 15.24 x 11.2 mm, 210 faces (baked)
FEATURE [Part::Feature] Part__Feature532  label="1x8-male-pin-header-red_001"
  Placement = pos=(-17.145,35.01,26.1) rot=(0,0,1;1.5708rad)
  shape: bbox 2.54 x 20.32 x 11.2 mm, 278 faces (baked)
FEATURE [Part::Feature] Part__Feature533  label="1x4-male-pin-header-red004_001"
  Placement = pos=(2.0574,35.7085,26.1) rot=(0,0,1;3.14159rad)
  shape: bbox 10.16 x 2.54 x 11.2 mm, 142 faces (baked)
FEATURE [Part::Feature] Part__Feature534  label="1x8-male-pin-header-gray_001"
  Placement = pos=(-14.605,35.01,26.1) rot=(0,0,1;1.5708rad)
  shape: bbox 2.54 x 20.32 x 11.2 mm, 278 faces (baked)
FEATURE [Part::Feature] Part__Feature535  label="1x8-socket-header_003"
  Placement = pos=(24.13,-0.55,26.1) rot=(0,0,-1;1.5708rad)
  shape: bbox 2.54 x 20.32 x 11.85 mm, 150 faces (baked)
FEATURE [Part::Feature] Part__Feature536  label="1x6-socket-header_001"
  Placement = pos=(24.13,22.31,26.1) rot=(0,0,-1;1.5708rad)
  shape: bbox 2.54 x 15.24 x 11.85 mm, 114 faces (baked)
FEATURE [Part::Feature] Part__Feature537  label="SOT23-3_003"
  Placement = pos=(4.57,-18.48,26.1) rot=(0,0,1;3.14159rad)
  shape: bbox 2.76 x 2.9 x 1.1 mm, 49 faces (baked)
FEATURE [Part::Feature] Part__Feature538  label="1x4-male-pin-header_001"
  Placement = pos=(2.0574,38.2485,26.1) rot=(0,0,1;3.14159rad)
  shape: bbox 10.16 x 2.54 x 11.2 mm, 142 faces (baked)
FEATURE [Part::Feature] Part__Feature539  label="SOT-563_001"
  Placement = pos=(-2.4384,-20.9208,26.1) rot=(0,0,-1;1.5708rad)
  shape: bbox 1.6 x 1.6 x 0.55 mm, 48 faces (baked)
FEATURE [Part::Feature] Part__Feature540  label="1x4-male-pin-header-cyan_001"
  Placement = pos=(2.0574,33.1685,26.1) rot=(0,0,1;3.14159rad)
  shape: bbox 10.16 x 2.54 x 11.2 mm, 142 faces (baked)
FEATURE [Part::Feature] Part__Feature541  label="2x4-pin-header-yello_001"
  Placement = pos=(8.8392,-12.7039,26.1) rot=(0,0,1;1.5708rad)
  shape: bbox 5.08 x 10.16 x 11.2 mm, 271 faces (baked)
FEATURE [Part::Feature] Part__Feature542  label="USB-micro-B_001"
  Placement = pos=(-2.25,-26.52,26.1) rot=(0,0,1;1.5708rad)
  shape: bbox 7.977 x 5.438 x 2.937 mm, 448 faces (baked)
FEATURE [Part::Feature] Part__Feature543  label="slide-sw-right-angle_001"
  Placement = pos=(21.463,-7.3953,26.1) rot=(0,0,1;1.5708rad)
  shape: bbox 7.561 x 10 x 5.5 mm, 95 faces (baked)
FEATURE [Part::Feature] Part__Feature544  label="SOT23-3_004"
  Placement = pos=(8.18,-25.79,26.1) rot=(0,0,1;1.5708rad)
  shape: bbox 2.9 x 2.76 x 1.1 mm, 49 faces (baked)
FEATURE [Part::Feature] Part__Feature545  label="LED_0603_011"
  Placement = pos=(-15.63,-25.59,26.1) rot=(0,0,1;1.5708rad)
  shape: bbox 0.725 x 1.65 x 0.675 mm, 50 faces (baked)
FEATURE [Part::Feature] Part__Feature546  label="R_Array_4x0603_002"
  Placement = pos=(-16.4211,-21.5304,26.1) rot=(0,0,-1;1.5708rad)
  shape: bbox 3.498 x 1.62 x 0.5525 mm, 95 faces (baked)
FEATURE [Part::Feature] Part__Feature547  label="LED_0603_012"
  Placement = pos=(-23.13,-25.59,26.1) rot=(0,0,1;1.5708rad)
  shape: bbox 0.725 x 1.65 x 0.675 mm, 50 faces (baked)
FEATURE [Part::Feature] Part__Feature548  label="sw_smd_6.0x3.8_002"
  Placement = pos=(-17.53,-11.39,26.1) rot=(0,0,1;1.5708rad)
  shape: bbox 7.3 x 3.899 x 2.5 mm, 90 faces (baked)
FEATURE [Part::Feature] Part__Feature549  label="1x6-pin-header_002"
  Placement = pos=(-19.685,13.166,26.1) rot=(0,0,1;1.5708rad)
  shape: bbox 2.54 x 15.24 x 11.2 mm, 210 faces (baked)
FEATURE [Part::Feature] Part__Feature550  label="PVQFN20_002"
  Placement = pos=(9.5631,27.5043,26.1) rot=(0,0,-1;1.5708rad)
  shape: bbox 3.52 x 4.52 x 0.9 mm, 133 faces (baked)
FEATURE [Part::Feature] Part__Feature551  label="1x6-pin-header_003"
  Placement = pos=(19.685,18.5,26.1) rot=(0,0,-1;1.5708rad)
  shape: bbox 2.54 x 15.24 x 11.2 mm, 210 faces (baked)
FEATURE [Part::Feature] Part__Feature552  label="LED_0603_013"
  Placement = pos=(-24.63,-25.59,26.1) rot=(0,0,1;1.5708rad)
  shape: bbox 0.725 x 1.65 x 0.675 mm, 50 faces (baked)
FEATURE [Part::Feature] Part__Feature553  label="1x6-male-pin-header-red_003"
  Placement = pos=(-17.145,13.166,26.1) rot=(0,0,1;1.5708rad)
  shape: bbox 2.54 x 15.24 x 11.2 mm, 210 faces (baked)
FEATURE [Part::Feature] Part__Feature554  label="LED_0603_014"
  Placement = pos=(-21.63,-25.59,26.1) rot=(0,0,1;1.5708rad)
  shape: bbox 0.725 x 1.65 x 0.675 mm, 50 faces (baked)
FEATURE [Part::Feature] Part__Feature555  label="1x6-male-pin-header-gray_003"
  Placement = pos=(-14.605,13.166,26.1) rot=(0,0,1;1.5708rad)
  shape: bbox 2.54 x 15.24 x 11.2 mm, 210 faces (baked)
FEATURE [Part::Feature] Part__Feature556  label="LED_0603_015"
  Placement = pos=(-17.13,-25.59,26.1) rot=(0,0,1;1.5708rad)
  shape: bbox 0.725 x 1.65 x 0.675 mm, 50 faces (baked)
FEATURE [Part::Feature] Part__Feature557  label="LED_0603_016"
  Placement = pos=(-20.13,-25.59,26.1) rot=(0,0,1;1.5708rad)
  shape: bbox 0.725 x 1.65 x 0.675 mm, 50 faces (baked)
FEATURE [Part::Feature] Part__Feature558  label="R_Array_4x0603_003"
  Placement = pos=(-21.9964,-21.5304,26.1) rot=(0,0,-1;1.5708rad)
  shape: bbox 3.498 x 1.62 x 0.5525 mm, 95 faces (baked)
FEATURE [Part::Feature] Part__Feature559  label="LED_0603_017"
  Placement = pos=(19.939,-1.9978,26.1) rot=(0,0,1;1.5708rad)
  shape: bbox 0.725 x 1.65 x 0.675 mm, 50 faces (baked)
FEATURE [Part::Feature] Part__Feature560  label="sw_smd_6.0x3.8_003"
  Placement = pos=(-17.53,-16.79,26.1) rot=(0,0,1;1.5708rad)
  shape: bbox 7.3 x 3.899 x 2.5 mm, 90 faces (baked)
FEATURE [Part::Feature] Part__Feature561  label="PVQFN20_003"
  Placement = pos=(-8.7122,28.0758,26.1) rot=(0,0,1;1.5708rad)
  shape: bbox 3.52 x 4.52 x 0.9 mm, 133 faces (baked)
FEATURE [Part::Feature] Part__Feature562  label="SOT23-3_005"
  Placement = pos=(4.56,-25.79,26.1) rot=(0,0,1;1.5708rad)
  shape: bbox 2.9 x 2.76 x 1.1 mm, 49 faces (baked)
FEATURE [Part::Feature] Part__Feature563  label="C_0402_053"
  Placement = pos=(-6.4262,-1.5533,26.1) rot=(0,0,1;3.14159rad)
  shape: bbox 0.985 x 0.5 x 0.5 mm, 44 faces (baked)
FEATURE [Part::Feature] Part__Feature564  label="MSOP-8_001"
  Placement = pos=(-9.7917,-12.0562,26.1) rot=(0,0,1;1.5708rad)
  shape: bbox 3.2 x 5.141 x 1 mm, 115 faces (baked)
FEATURE [Part::Feature] Part__Feature565  label="xtal-3_2x2_5_001"
  Placement = pos=(-8.8265,-18.7491,26.1) rot=(0,0,1;1.5708rad)
  shape: bbox 3.2 x 2.5 x 0.92 mm, 29 faces (baked)
FEATURE [Part::Feature] Part__Feature566  label="F1812-505k_001"
  Placement = pos=(-11.09,-24.72,26.1) rot=(0,0,-1;1.5708rad)
  shape: bbox 3.41 x 4.73 x 1.39 mm, 94 faces (baked)
FEATURE [Part::Feature] Part__Feature567  label="jack_DC_2.1mm_PCB_001"
  Placement = pos=(18.3134,-23.0798,26.1) rot=(0,0,1;0rad)
  shape: bbox 9.46 x 14.5 x 14.8 mm, 34 faces (baked)
FEATURE [Part::Feature] Part__Feature568  label="DO-214AC_001"
  Placement = pos=(11.7602,-24.2228,26.1) rot=(0,0,-1;1.5708rad)
  shape: bbox 2.8 x 5.475 x 2.574 mm, 39 faces (baked)
FEATURE [Part::Feature] Part__Feature569  label="SOD-323_002"
  Placement = pos=(3.1496,-21.6574,26.1) rot=(0,0,1;1.5708rad)
  shape: bbox 1.35 x 2.6 x 1.113 mm, 38 faces (baked)
FEATURE [Part::Feature] Part__Feature570  label="DFN-2523-6_003"
  Placement = pos=(11.7348,-14.3168,26.1) rot=(0,0,1;0rad)
  shape: bbox 2.5 x 2.4 x 0.62 mm, 44 faces (baked)
FEATURE [Part::Feature] Part__Feature571  label="DFN-2523-6_004"
  Placement = pos=(11.7729,-18.6602,26.1) rot=(0,0,1;3.14159rad)
  shape: bbox 2.5 x 2.4 x 0.62 mm, 44 faces (baked)
FEATURE [Part::Feature] Part__Feature572  label="C_0402_054"
  Placement = pos=(-16.8275,-7.3953,26.1) rot=(0,0,1;0rad)
  shape: bbox 0.985 x 0.5 x 0.5 mm, 44 faces (baked)
FEATURE [Part::Feature] Part__Feature573  label="DFN-2523-6_005"
  Placement = pos=(20.066,5.9016,26.1) rot=(0,0,1;0rad)
  shape: bbox 2.5 x 2.4 x 0.62 mm, 44 faces (baked)
FEATURE [Part::Feature] Part__Feature574  label="PVQFN16_001"
  Placement = pos=(-15.82,-3.72,26.1) rot=(0,0,1;1.5708rad)
  shape: bbox 3.7 x 4.17 x 1.1 mm, 109 faces (baked)
FEATURE [Part::Feature] Part__Feature575  label="C_0402_055"
  Placement = pos=(8.7757,31.1111,26.1) rot=(0,0,1;3.14159rad)
  shape: bbox 0.985 x 0.5 x 0.5 mm, 44 faces (baked)
FEATURE [Part::Feature] Part__Feature576  label="L_4040_001"
  Placement = pos=(15.0495,-2.2391,26.1) rot=(0,0,1;0rad)
  shape: bbox 4.3 x 4.3 x 2.33 mm, 122 faces (baked)
FEATURE [Part::Feature] Part__Feature577  label="QFN16_002"
  Placement = pos=(0.4826,27.7837,26.1) rot=(0,0,1;1.5708rad)
  shape: bbox 3.08 x 3.08 x 0.9 mm, 118 faces (baked)
FEATURE [Part::Feature] Part__Feature578  label="QFN16_003"
  Placement = pos=(14.6431,-7.0778,26.1) rot=(0,0,-1;1.5708rad)
  shape: bbox 3.08 x 3.08 x 0.9 mm, 118 faces (baked)
FEATURE [Part::Feature] Part__Feature579  label="C_0402_056"
  Placement = pos=(-8.2042,-22.8004,26.1) rot=(0,0,-1;1.5708rad)
  shape: bbox 0.5 x 0.985 x 0.5 mm, 44 faces (baked)
FEATURE [Part::Feature] Part__Feature580  label="FTDI-QFN-64_001"
  Placement = pos=(-1.4732,-11.9419,26.1) rot=(0,0,1;1.5708rad)
  shape: bbox 9.04 x 9.04 x 0.95 mm, 849 faces (baked)
FEATURE [Part::Feature] Part__Feature581  label="C_0402_057"
  Placement = pos=(-20.3327,-4.6902,26.1) rot=(0,0,1;3.14159rad)
  shape: bbox 0.985 x 0.5 x 0.5 mm, 44 faces (baked)
FEATURE [Part::Feature] Part__Feature582  label="C_0402_058"
  Placement = pos=(0.2667,-18.1903,26.1) rot=(0,0,-1;1.5708rad)
  shape: bbox 0.5 x 0.985 x 0.5 mm, 44 faces (baked)
FEATURE [Part::Feature] Part__Feature583  label="C_0402_059"
  Placement = pos=(-9.8298,24.6087,26.1) rot=(0,0,1;0rad)
  shape: bbox 0.985 x 0.5 x 0.5 mm, 44 faces (baked)
FEATURE [Part::Feature] Part__Feature584  label="C_1206_002"
  Placement = pos=(19.0373,-6.8238,26.1) rot=(0,0,-1;1.5708rad)
  shape: bbox 1.6 x 3.2 x 1 mm, 44 faces (baked)
FEATURE [Part::Feature] Part__Feature585  label="C_0402_060"
  Placement = pos=(17.399,-5.7062,26.1) rot=(0,0,-1;1.5708rad)
  shape: bbox 0.5 x 0.985 x 0.5 mm, 44 faces (baked)
FEATURE [Part::Feature] Part__Feature586  label="C_0402_061"
  Placement = pos=(-20.3327,-1.6803,26.1) rot=(0,0,1;3.14159rad)
  shape: bbox 0.985 x 0.5 x 0.5 mm, 44 faces (baked)
FEATURE [Part::Feature] Part__Feature587  label="C_0402_062"
  Placement = pos=(4.2799,-1.9978,26.1) rot=(0,0,-1;1.5708rad)
  shape: bbox 0.5 x 0.985 x 0.5 mm, 44 faces (baked)
FEATURE [Part::Feature] Part__Feature588  label="C_0603_014"
  Placement = pos=(11.3665,-8.1954,26.1) rot=(0,0,1;1.5708rad)
  shape: bbox 0.8 x 1.6 x 0.6 mm, 44 faces (baked)
FEATURE [Part::Feature] Part__Feature589  label="C_0402_063"
  Placement = pos=(-16.8275,-8.3859,26.1) rot=(0,0,1;3.14159rad)
  shape: bbox 0.985 x 0.5 x 0.5 mm, 44 faces (baked)
FEATURE [Part::Feature] Part__Feature590  label="C_0402_064"
  Placement = pos=(-20.33,-3.69,26.1) rot=(0,0,1;3.14159rad)
  shape: bbox 0.985 x 0.5 x 0.5 mm, 44 faces (baked)
FEATURE [Part::Feature] Part__Feature591  label="DFN-3030-8_001"
  Placement = pos=(13.8938,2.3202,26.1) rot=(0,0,-1;1.5708rad)
  shape: bbox 3 x 3.02 x 0.85 mm, 89 faces (baked)
FEATURE [Part::Feature] Part__Feature592  label="C_0603_015"
  Placement = pos=(11.6713,-5.3887,26.1) rot=(0,0,1;1.5708rad)
  shape: bbox 0.8 x 1.6 x 0.6 mm, 44 faces (baked)
FEATURE [Part::Feature] Part__Feature593  label="C_0402_065"
  Placement = pos=(-0.635,-18.1903,26.1) rot=(0,0,1;1.5708rad)
  shape: bbox 0.5 x 0.985 x 0.5 mm, 44 faces (baked)
FEATURE [Part::Feature] Part__Feature594  label="C_0402_066"
  Placement = pos=(12.4841,12.6707,26.1) rot=(0,0,1;1.5708rad)
  shape: bbox 0.5 x 0.985 x 0.5 mm, 44 faces (baked)
FEATURE [Part::Feature] Part__Feature595  label="C_0402_067"
  Placement = pos=(12.4714,8.7083,26.1) rot=(0,0,-1;1.5708rad)
  shape: bbox 0.5 x 0.985 x 0.5 mm, 44 faces (baked)
FEATURE [Part::Feature] Part__Feature596  label="C_0402_068"
  Placement = pos=(4.2418,-14.647,26.1) rot=(0,0,-1;1.5708rad)
  shape: bbox 0.5 x 0.985 x 0.5 mm, 44 faces (baked)
FEATURE [Part::Feature] Part__Feature597  label="C_0402_069"
  Placement = pos=(-7.1755,-12.1451,26.1) rot=(0,0,-1;1.5708rad)
  shape: bbox 0.5 x 0.985 x 0.5 mm, 44 faces (baked)
FEATURE [Part::Feature] Part__Feature598  label="C_0402_070"
  Placement = pos=(1.4732,23.199,26.1) rot=(0,0,1;0rad)
  shape: bbox 0.985 x 0.5 x 0.5 mm, 44 faces (baked)
FEATURE [Part::Feature] Part__Feature599  label="C_0603_016"
  Placement = pos=(8.3693,-2.4931,26.1) rot=(0,0,1;3.14159rad)
  shape: bbox 1.6 x 0.8 x 0.6 mm, 44 faces (baked)
FEATURE [Part::Feature] Part__Feature600  label="C_0402_071"
  Placement = pos=(-12.3317,28.7108,26.1) rot=(0,0,1;1.5708rad)
  shape: bbox 0.5 x 0.985 x 0.5 mm, 44 faces (baked)
FEATURE [Part::Feature] Part__Feature601  label="C_0603_017"
  Placement = pos=(-5.7404,-18.4062,26.1) rot=(0,0,-1;1.5708rad)
  shape: bbox 0.8 x 1.6 x 0.6 mm, 44 faces (baked)
FEATURE [Part::Feature] Part__Feature602  label="pushbutton-right-angle_001"
  Placement = pos=(9.779,37.169,26.1) rot=(0,0,1;3.14159rad)
  shape: bbox 7.4 x 7.9 x 11 mm, 130 faces (baked)
FEATURE [Part::Feature] Part__Feature603  label="C_0402_072"
  Placement = pos=(-14.1351,-7.3953,26.1) rot=(0,0,1;0rad)
  shape: bbox 0.985 x 0.5 x 0.5 mm, 44 faces (baked)
FEATURE [Part::Feature] Part__Feature604  label="C_0402_073"
  Placement = pos=(4.2672,-7.8271,26.1) rot=(0,0,1;1.5708rad)
  shape: bbox 0.5 x 0.985 x 0.5 mm, 44 faces (baked)
FEATURE [Part::Feature] Part__Feature605  label="C_0402_074"
  Placement = pos=(-7.62,24.6087,26.1) rot=(0,0,1;0rad)
  shape: bbox 0.985 x 0.5 x 0.5 mm, 44 faces (baked)
FEATURE [Part::Feature] Part__Feature606  label="WSON-6_001"
  Placement = pos=(17.272,3.2854,26.1) rot=(0,0,1;1.5708rad)
  shape: bbox 1.55 x 1.6 x 0.85 mm, 44 faces (baked)
FEATURE [Part::Feature] Part__Feature607  label="C_0402_075"
  Placement = pos=(10.7696,21.8782,26.1) rot=(0,0,1;0rad)
  shape: bbox 0.985 x 0.5 x 0.5 mm, 44 faces (baked)
FEATURE [Part::Feature] Part__Feature608  label="TQFP-144_001"
  Placement = pos=(0,10.9308,26.1) rot=(0,0,1;1.5708rad)
  shape: bbox 21.98 x 21.98 x 1.12 mm, 2168 faces (baked)
FEATURE [Part::Feature] Part__Feature609  label="C_0603_018"
  Placement = pos=(17.0942,5.1142,26.1) rot=(0,0,1;0rad)
  shape: bbox 1.6 x 0.8 x 0.6 mm, 44 faces (baked)
FEATURE [Part::Feature] Part__Feature610  label="C_0402_076"
  Placement = pos=(-9.9314,-15.8916,26.1) rot=(0,0,1;3.14159rad)
  shape: bbox 0.985 x 0.5 x 0.5 mm, 44 faces (baked)
FEATURE [Part::Feature] Part__Feature611  label="C_0603_019"
  Placement = pos=(15.0622,-13.1992,26.1) rot=(0,0,1;0rad)
  shape: bbox 1.6 x 0.8 x 0.6 mm, 44 faces (baked)
FEATURE [Part::Feature] Part__Feature612  label="C_0402_077"
  Placement = pos=(-12.319,31.2,26.1) rot=(0,0,-1;1.5708rad)
  shape: bbox 0.5 x 0.985 x 0.5 mm, 44 faces (baked)
FEATURE [Part::Feature] Part__Feature613  label="C_0402_078"
  Placement = pos=(-12.3317,33.7146,26.1) rot=(0,0,1;1.5708rad)
  shape: bbox 0.5 x 0.985 x 0.5 mm, 44 faces (baked)
FEATURE [Part::Feature] Part__Feature614  label="C_0402_079"
  Placement = pos=(-20.3327,-6.6968,26.1) rot=(0,0,1;3.14159rad)
  shape: bbox 0.985 x 0.5 x 0.5 mm, 44 faces (baked)
FEATURE [Part::Feature] Part__Feature615  label="L_0603_003"
  Placement = pos=(-6.0325,-22.4956,26.1) rot=(0,0,1;3.14159rad)
  shape: bbox 1.6 x 0.8 x 0.6 mm, 44 faces (baked)
FEATURE [Part::Feature] Part__Feature616  label="C_0402_080"
  Placement = pos=(-7.1374,-8.9066,26.1) rot=(0,0,-1;1.5708rad)
  shape: bbox 0.5 x 0.985 x 0.5 mm, 44 faces (baked)
FEATURE [Part::Feature] Part__Feature617  label="C_0603_020"
  Placement = pos=(-8.2042,-24.9467,26.1) rot=(0,0,1;1.5708rad)
  shape: bbox 0.8 x 1.6 x 0.6 mm, 44 faces (baked)
FEATURE [Part::Feature] Part__Feature618  label="C_0402_081"
  Placement = pos=(-5.4229,23.199,26.1) rot=(0,0,1;3.14159rad)
  shape: bbox 0.985 x 0.5 x 0.5 mm, 44 faces (baked)
FEATURE [Part::Feature] Part__Feature619  label="R_0402_037"
  Placement = pos=(-3.6322,-18.203,26.1) rot=(0,0,1;1.5708rad)
  shape: bbox 0.5 x 1 x 0.3 mm, 40 faces (baked)
FEATURE [Part::Feature] Part__Feature620  label="C_0402_082"
  Placement = pos=(-2.2352,-5.7951,26.1) rot=(0,0,1;1.5708rad)
  shape: bbox 0.5 x 0.985 x 0.5 mm, 44 faces (baked)
FEATURE [Part::Feature] Part__Feature621  label="C_0402_083"
  Placement = pos=(-20.3327,-2.6963,26.1) rot=(0,0,1;3.14159rad)
  shape: bbox 0.985 x 0.5 x 0.5 mm, 44 faces (baked)
FEATURE [Part::Feature] Part__Feature622  label="C_0603_021"
  Placement = pos=(-3.429,31.0095,26.1) rot=(0,0,1;3.14159rad)
  shape: bbox 1.6 x 0.8 x 0.6 mm, 44 faces (baked)
FEATURE [Part::Feature] Part__Feature623  label="C_1206_003"
  Placement = pos=(16.51,-11.1037,26.1) rot=(0,0,1;0rad)
  shape: bbox 3.2 x 1.6 x 1 mm, 44 faces (baked)
FEATURE [Part::Feature] Part__Feature624  label="C_0603_022"
  Placement = pos=(-0.3429,-20.7684,26.1) rot=(0,0,-1;1.5708rad)
  shape: bbox 0.8 x 1.6 x 0.6 mm, 44 faces (baked)
FEATURE [Part::Feature] Part__Feature625  label="C_0402_084"
  Placement = pos=(-7.2898,-15.79,26.1) rot=(0,0,-1;1.5708rad)
  shape: bbox 0.5 x 0.985 x 0.5 mm, 44 faces (baked)
FEATURE [Part::Feature] Part__Feature626  label="C_0603_023"
  Placement = pos=(9.271,-22.3432,26.1) rot=(0,0,1;1.5708rad)
  shape: bbox 0.8 x 1.6 x 0.6 mm, 44 faces (baked)
FEATURE [Part::Feature] Part__Feature627  label="C_0402_085"
  Placement = pos=(-14.13,-8.39,26.1) rot=(0,0,1;0rad)
  shape: bbox 0.985 x 0.5 x 0.5 mm, 44 faces (baked)
FEATURE [Part::Feature] Part__Feature628  label="SOD-323_003"
  Placement = pos=(-8.1,23.32,26.1) rot=(0,0,1;0rad)
  shape: bbox 2.6 x 1.35 x 1.113 mm, 38 faces (baked)
FEATURE [Part::Feature] Part__Feature629  label="DFN-8-6x5mm_001"
  Placement = pos=(16.1,12.61,26.1) rot=(0,0,-1;1.5708rad)
  shape: bbox 5 x 6.1 x 0.9466 mm, 62 faces (baked)
FEATURE [Part::Feature] Part__Feature630  label="C_0402_086"
  Placement = pos=(0.8636,-6.1888,26.1) rot=(0,0,1;0rad)
  shape: bbox 0.985 x 0.5 x 0.5 mm, 44 faces (baked)
FEATURE [Part::Feature] Part__Feature631  label="L_0603_004"
  Placement = pos=(-5.1054,-20.5144,26.1) rot=(0,0,1;3.14159rad)
  shape: bbox 1.6 x 0.8 x 0.6 mm, 44 faces (baked)
FEATURE [Part::Feature] Part__Feature632  label="C_0402_087"
  Placement = pos=(-1.524,23.2117,26.1) rot=(0,0,1;3.14159rad)
  shape: bbox 0.985 x 0.5 x 0.5 mm, 44 faces (baked)
FEATURE [Part::Feature] Part__Feature633  label="C_0603_024"
  Placement = pos=(7.4168,-15.9932,26.1) rot=(0,0,1;0rad)
  shape: bbox 1.6 x 0.8 x 0.6 mm, 44 faces (baked)
FEATURE [Part::Feature] Part__Feature634  label="C_0603_025"
  Placement = pos=(13.3477,4.9999,26.1) rot=(0,0,1;3.14159rad)
  shape: bbox 1.6 x 0.8 x 0.6 mm, 44 faces (baked)
FEATURE [Part::Feature] Part__Feature636  label="C_0402_088"
  Placement = pos=(-12.3317,26.1073,26.1) rot=(0,0,-1;1.5708rad)
  shape: bbox 0.5 x 0.985 x 0.5 mm, 44 faces (baked)
FEATURE [Part::Feature] Part__Feature637  label="C_0402_089"
  Placement = pos=(5.7658,-1.9978,26.1) rot=(0,0,-1;1.5708rad)
  shape: bbox 0.5 x 0.985 x 0.5 mm, 44 faces (baked)
FEATURE [Part::Feature] Part__Feature638  label="C_0402_090"
  Placement = pos=(8.5725,-1.3882,26.1) rot=(0,0,1;3.14159rad)
  shape: bbox 0.985 x 0.5 x 0.5 mm, 44 faces (baked)
FEATURE [Part::Feature] Part__Feature639  label="L_0603_005"
  Placement = pos=(13.0683,-11.091,26.1) rot=(0,0,1;1.5708rad)
  shape: bbox 0.8 x 1.6 x 0.6 mm, 44 faces (baked)
FEATURE [Part::Feature] Part__Feature640  label="C_0603_026"
  Placement = pos=(-5.3721,-6.265,26.1) rot=(0,0,1;0rad)
  shape: bbox 1.6 x 0.8 x 0.6 mm, 44 faces (baked)
FEATURE [Part::Feature] Part__Feature641  label="C_0402_091"
  Placement = pos=(10.668,31.1111,26.1) rot=(0,0,1;3.14159rad)
  shape: bbox 0.985 x 0.5 x 0.5 mm, 44 faces (baked)
FEATURE [Part::Feature] Part__Feature642  label="L_0805_001"
  Placement = pos=(1.1176,-21.3272,26.1) rot=(0,0,1;1.5708rad)
  shape: bbox 1.25 x 2 x 1.25 mm, 50 faces (baked)
FEATURE [Part::Feature] Part__Feature643  label="C_0402_092"
  Placement = pos=(-20.3327,-5.6935,26.1) rot=(0,0,1;3.14159rad)
  shape: bbox 0.985 x 0.5 x 0.5 mm, 44 faces (baked)
FEATURE [Part::Feature] Part__Feature644  label="C_0402_093"
  Placement = pos=(-4.6228,-18.203,26.1) rot=(0,0,-1;1.5708rad)
  shape: bbox 0.5 x 0.985 x 0.5 mm, 44 faces (baked)
FEATURE [Part::Feature] Part__Feature645  label="R_0402_039"
  Placement = pos=(-10.5283,-8.1954,26.1) rot=(0,0,1;3.14159rad)
  shape: bbox 1 x 0.5 x 0.3 mm, 40 faces (baked)
FEATURE [Part::Feature] Part__Feature646  label="C_0402_094"
  Placement = pos=(-12.3317,36.3054,26.1) rot=(0,0,-1;1.5708rad)
  shape: bbox 0.5 x 0.985 x 0.5 mm, 44 faces (baked)
FEATURE [Part::Feature] Part__Feature647  label="C_0402_095"
  Placement = pos=(-11.3665,-18.2919,26.1) rot=(0,0,-1;1.5708rad)
  shape: bbox 0.5 x 0.985 x 0.5 mm, 44 faces (baked)
FEATURE [Part::Feature] Part__Feature648  label="C_0402_096"
  Placement = pos=(17.4625,7.9082,26.1) rot=(0,0,1;3.14159rad)
  shape: bbox 0.985 x 0.5 x 0.5 mm, 44 faces (baked)
FEATURE [Part::Feature] Part__Feature649  label="C_0402_097"
  Placement = pos=(12.8651,6.7652,26.1) rot=(0,0,1;0rad)
  shape: bbox 0.985 x 0.5 x 0.5 mm, 44 faces (baked)
FEATURE [Part::Feature] Part__Feature650  label="C_0402_098"
  Placement = pos=(-2.3368,28.5076,26.1) rot=(0,0,-1;1.5708rad)
  shape: bbox 0.5 x 0.985 x 0.5 mm, 44 faces (baked)
FEATURE [Part::Feature] Part__Feature651  label="C_0402_099"
  Placement = pos=(-2.3368,26.6153,26.1) rot=(0,0,-1;1.5708rad)
  shape: bbox 0.5 x 0.985 x 0.5 mm, 44 faces (baked)
FEATURE [Part::Feature] Part__Feature652  label="C_0603_027"
  Placement = pos=(17.0942,6.3207,26.1) rot=(0,0,1;0rad)
  shape: bbox 1.6 x 0.8 x 0.6 mm, 44 faces (baked)
FEATURE [Part::Feature] Part__Feature653  label="C_0402_100"
  Placement = pos=(-12.3317,23.6054,26.1) rot=(0,0,1;1.5708rad)
  shape: bbox 0.5 x 0.985 x 0.5 mm, 44 faces (baked)
FEATURE [Part::Feature] Part__Feature654  label="C_0402_101"
  Placement = pos=(-12.3317,21.0019,26.1) rot=(0,0,1;1.5708rad)
  shape: bbox 0.5 x 0.985 x 0.5 mm, 44 faces (baked)
FEATURE [Part::Feature] Part__Feature655  label="C_0402_102"
  Placement = pos=(-12.3317,18.4111,26.1) rot=(0,0,-1;1.5708rad)
  shape: bbox 0.5 x 0.985 x 0.5 mm, 44 faces (baked)
FEATURE [Part::Feature] Part__Feature656  label="C_0402_103"
  Placement = pos=(-12.3317,12.0738,26.1) rot=(0,0,-1;1.5708rad)
  shape: bbox 0.5 x 0.985 x 0.5 mm, 44 faces (baked)
FEATURE [Part::Feature] Part__Feature657  label="C_0402_104"
  Placement = pos=(-12.3317,15.706,26.1) rot=(0,0,-1;1.5708rad)
  shape: bbox 0.5 x 0.985 x 0.5 mm, 44 faces (baked)
FEATURE [Part::Feature] Part__Feature658  label="C_0402_105"
  Placement = pos=(-12.4333,7.0319,26.1) rot=(0,0,1;1.5708rad)
  shape: bbox 0.5 x 0.985 x 0.5 mm, 44 faces (baked)
FEATURE [Part::Feature] Part__Feature659  label="R_0402_040"
  Placement = pos=(-10.5283,-6.1888,26.1) rot=(0,0,1;0rad)
  shape: bbox 1 x 0.5 x 0.3 mm, 40 faces (baked)
FEATURE [Part::Feature] Part__Feature660  label="R_0402_041"
  Placement = pos=(-10.5283,-7.1921,26.1) rot=(0,0,1;0rad)
  shape: bbox 1 x 0.5 x 0.3 mm, 40 faces (baked)
FEATURE [Part::Feature] Part__Feature661  label="R_0402_042"
  Placement = pos=(1.67,-18.19,26.1) rot=(0,0,1;1.5708rad)
  shape: bbox 0.5 x 1 x 0.3 mm, 40 faces (baked)
FEATURE [Part::Feature] Part__Feature662  label="R_0402_043"
  Placement = pos=(4.9657,-20.7938,26.1) rot=(0,0,1;3.14159rad)
  shape: bbox 1 x 0.5 x 0.3 mm, 40 faces (baked)
FEATURE [Part::Feature] Part__Feature663  label="R_0402_044"
  Placement = pos=(4.4704,-22.4956,26.1) rot=(0,0,-1;1.5708rad)
  shape: bbox 0.5 x 1 x 0.3 mm, 40 faces (baked)
FEATURE [Part::Feature] Part__Feature664  label="R_0402_045"
  Placement = pos=(5.461,-22.4956,26.1) rot=(0,0,-1;1.5708rad)
  shape: bbox 0.5 x 1 x 0.3 mm, 40 faces (baked)
FEATURE [Part::Feature] Part__Feature665  label="R_0402_046"
  Placement = pos=(7.6708,-18.0887,26.1) rot=(0,0,-1;1.5708rad)
  shape: bbox 0.5 x 1 x 0.3 mm, 40 faces (baked)
FEATURE [Part::Feature] Part__Feature666  label="R_0402_047"
  Placement = pos=(9.271,-20.0953,26.1) rot=(0,0,-1;1.5708rad)
  shape: bbox 0.5 x 1 x 0.3 mm, 40 faces (baked)
FEATURE [Part::Feature] Part__Feature667  label="R_0402_048"
  Placement = pos=(7.6708,-19.9937,26.1) rot=(0,0,-1;1.5708rad)
  shape: bbox 0.5 x 1 x 0.3 mm, 40 faces (baked)
FEATURE [Part::Feature] Part__Feature668  label="R_0402_049"
  Placement = pos=(9.271,-18.203,26.1) rot=(0,0,1;1.5708rad)
  shape: bbox 0.5 x 1 x 0.3 mm, 40 faces (baked)
FEATURE [Part::Feature] Part__Feature669  label="R_0402_050"
  Placement = pos=(21.5773,-1.1977,26.1) rot=(0,0,1;3.14159rad)
  shape: bbox 1 x 0.5 x 0.3 mm, 40 faces (baked)
FEATURE [Part::Feature] Part__Feature670  label="R_0402_051"
  Placement = pos=(9.271,-16.298,26.1) rot=(0,0,1;1.5708rad)
  shape: bbox 0.5 x 1 x 0.3 mm, 40 faces (baked)
FEATURE [Part::Feature] Part__Feature671  label="R_0402_052"
  Placement = pos=(10.2743,-1.9978,26.1) rot=(0,0,-1;1.5708rad)
  shape: bbox 0.5 x 1 x 0.3 mm, 40 faces (baked)
FEATURE [Part::Feature] Part__Feature672  label="R_0402_053"
  Placement = pos=(1.27,-1.9978,26.1) rot=(0,0,1;1.5708rad)
  shape: bbox 0.5 x 1 x 0.3 mm, 40 faces (baked)
FEATURE [Part::Feature] Part__Feature673  label="R_0402_054"
  Placement = pos=(17.272,1.3042,26.1) rot=(0,0,1;0rad)
  shape: bbox 1 x 0.5 x 0.3 mm, 40 faces (baked)
FEATURE [Part::Feature] Part__Feature674  label="R_0402_055"
  Placement = pos=(12.4714,15.706,26.1) rot=(0,0,-1;1.5708rad)
  shape: bbox 0.5 x 1 x 0.3 mm, 40 faces (baked)
FEATURE [Part::Feature] Part__Feature675  label="R_0402_056"
  Placement = pos=(18.9738,1.7106,26.1) rot=(0,0,-1;1.5708rad)
  shape: bbox 0.5 x 1 x 0.3 mm, 40 faces (baked)
FEATURE [Part::Feature] Part__Feature676  label="R_0402_057"
  Placement = pos=(6.8707,23.707,26.1) rot=(0,0,1;1.5708rad)
  shape: bbox 0.5 x 1 x 0.3 mm, 40 faces (baked)
FEATURE [Part::Feature] Part__Feature677  label="R_0402_058"
  Placement = pos=(19.9644,1.7106,26.1) rot=(0,0,-1;1.5708rad)
  shape: bbox 0.5 x 1 x 0.3 mm, 40 faces (baked)
FEATURE [Part::Feature] Part__Feature678  label="R_0402_059"
  Placement = pos=(20.0787,12.2135,26.1) rot=(0,0,1;3.14159rad)
  shape: bbox 1 x 0.5 x 0.3 mm, 40 faces (baked)
FEATURE [Part::Feature] Part__Feature679  label="R_0402_060"
  Placement = pos=(20.0787,11.2102,26.1) rot=(0,0,1;3.14159rad)
  shape: bbox 1 x 0.5 x 0.3 mm, 40 faces (baked)
FEATURE [Part::Feature] Part__Feature680  label="R_0402_061"
  Placement = pos=(20.0787,13.2041,26.1) rot=(0,0,1;3.14159rad)
  shape: bbox 1 x 0.5 x 0.3 mm, 40 faces (baked)
FEATURE [Part::Feature] Part__Feature681  label="R_0402_062"
  Placement = pos=(17.7673,33.2066,26.1) rot=(0,0,1;0rad)
  shape: bbox 1 x 0.5 x 0.3 mm, 40 faces (baked)
FEATURE [Part::Feature] Part__Feature682  label="R_0402_063"
  Placement = pos=(20.0787,14.2074,26.1) rot=(0,0,1;3.14159rad)
  shape: bbox 1 x 0.5 x 0.3 mm, 40 faces (baked)
FEATURE [Part::Feature] Part__Feature683  label="R_0402_064"
  Placement = pos=(19.8755,33.2066,26.1) rot=(0,0,1;3.14159rad)
  shape: bbox 1 x 0.5 x 0.3 mm, 40 faces (baked)
FEATURE [Part::Feature] Part__Feature684  label="R_0402_065"
  Placement = pos=(8.7757,32.3049,26.1) rot=(0,0,1;3.14159rad)
  shape: bbox 1 x 0.5 x 0.3 mm, 40 faces (baked)
FEATURE [Part::Feature] Part__Feature685  label="R_0402_066"
  Placement = pos=(1.8669,24.9008,26.1) rot=(0,0,1;0rad)
  shape: bbox 1 x 0.5 x 0.3 mm, 40 faces (baked)
FEATURE [Part::Feature] Part__Feature686  label="R_0402_067"
  Placement = pos=(10.668,32.3049,26.1) rot=(0,0,1;0rad)
  shape: bbox 1 x 0.5 x 0.3 mm, 40 faces (baked)
FEATURE [Part::Feature] Part__Feature687  label="R_0402_068"
  Placement = pos=(-5.63,31,26.1) rot=(0,0,1;3.14159rad)
  shape: bbox 1 x 0.5 x 0.3 mm, 40 faces (baked)
FEATURE [Part::Feature] Part__Feature688  label="R_0402_069"
  Placement = pos=(-1.1303,24.9008,26.1) rot=(0,0,1;3.14159rad)
  shape: bbox 1 x 0.5 x 0.3 mm, 40 faces (baked)
FEATURE [Part::Feature] Part__Feature689  label="R_0402_070"
  Placement = pos=(6.477,-22.4956,26.1) rot=(0,0,1;1.5708rad)
  shape: bbox 0.5 x 1 x 0.3 mm, 40 faces (baked)
FEATURE [Part::Feature] Part__Feature690  label="R_0402_071"
  Placement = pos=(7.6708,-22.4956,26.1) rot=(0,0,-1;1.5708rad)
  shape: bbox 0.5 x 1 x 0.3 mm, 40 faces (baked)
FEATURE [Part::Feature] Part__Feature691  label="R_0402_072"
  Placement = pos=(4.2672,-11.7895,26.1) rot=(0,0,-1;1.5708rad)
  shape: bbox 0.5 x 1 x 0.3 mm, 40 faces (baked)
FEATURE [Part::Feature] Part__Feature692  label="R_0402_073"
  Placement = pos=(4.2672,-9.8972,26.1) rot=(0,0,1;1.5708rad)
  shape: bbox 0.5 x 1 x 0.3 mm, 40 faces (baked)
FEATURE [Part::Feature] Part__Feature693  label="1x3-pin-header_001"
  Placement = pos=(-7.6581,33.0796,26.1) rot=(0,0,1;0rad)
  shape: bbox 7.62 x 2.54 x 11.2 mm, 108 faces (baked)
FEATURE [Part::Feature] Part__Feature694  label="jumper-cap-2.54mm_001"
  Placement = pos=(-7.6581,33.0796,26.1) rot=(0,0,1;3.14159rad)
  shape: bbox 5 x 2.5 x 6 mm, 108 faces (baked)
FEATURE [App::DocumentObjectGroup] Grupo028  label="step001"
  Group = -> [Part__Feature524,Part__Feature525,Part__Feature526,Part__Feature527,Part__Feature528,Part__Feature529,Part__Feature530,Part__Feature531,Part__Feature532,Part__Feature533,Part__Feature534,Part__Feature535,Part__Feature536,Part__Feature537,Part__Feature538,Part__Feature539,Part__Feature540,Part__Feature541,Part__Feature542,Part__Feature543,Part__Feature544,Part__Feature545,Part__Feature546,+148 more]
FEATURE [App::DocumentObjectGroup] Grupo027  label="icezum_alhambra001"
  Group = -> [Grupo028]
FEATURE [Part::Feature] Part__Feature  label="Rpi3Bplus"
  Placement = pos=(-28,41,0) rot=(0.57735,-0.57735,-0.57735;2.0944rad)
  shape: bbox 58.47 x 87.03 x 17.52 mm, 2323 faces, 179 solids (baked)
FEATURE [Part::Feature] Part__Feature816  label="0204- Resistor007"
  Placement = pos=(27.893,-1.45225,22.7279) rot=(-1,0,0;1.5708rad)
  shape: bbox 0.9906 x 0.3566 x 0.51 mm, 20 faces (baked)
FEATURE [Part::Feature] Part__Feature817  label="0204- Resistor008"
  Placement = pos=(4.84352,-1.45225,12.2479) rot=(0.57735,-0.57735,-0.57735;4.18879rad)
  shape: bbox 0.51 x 0.3566 x 0.9906 mm, 20 faces (baked)
FEATURE [Part::Feature] Part__Feature819  label="0204- Resistor010"
  Placement = pos=(-29.3937,-1.45225,25.9026) rot=(-1,0,0;1.5708rad)
  shape: bbox 0.9906 x 0.3566 x 0.51 mm, 20 faces (baked)
FEATURE [Part::Feature] Part__Feature726  label="Raspberry_pizero_PCB"
  Placement = pos=(0.00138154,-0.0966481,18.0542) rot=(0,0,1;3.14159rad)
  shape: bbox 1.5 x 1 x 1.5 mm, 6 faces (baked)
FEATURE [Part::Feature] Part__Feature727  label="Raspberry_pizero_PCB001"
  Placement = pos=(0.00138154,-0.0966481,18.0542) rot=(0,0,1;3.14159rad)
  shape: bbox 1.5 x 1 x 1.5 mm, 6 faces (baked)
FEATURE [Part::Feature] Part__Feature728  label="Raspberry_pizero_PCB002"
  Placement = pos=(0.00138154,-0.0966481,18.0542) rot=(0,0,1;3.14159rad)
  shape: bbox 1.5 x 1 x 1.5 mm, 6 faces (baked)
FEATURE [Part::Feature] Part__Feature729  label="Raspberry_pizero_PCB003"
  Placement = pos=(0.00138154,-0.0966481,18.0542) rot=(0,0,1;3.14159rad)
  shape: bbox 1.5 x 1 x 1.5 mm, 6 faces (baked)
FEATURE [Part::Feature] Part__Feature730  label="Raspberry_pizero_PCB004"
  Placement = pos=(0.00138154,-0.0966481,18.0542) rot=(0,0,1;3.14159rad)
  shape: bbox 1.5 x 1 x 1.5 mm, 6 faces (baked)
FEATURE [Part::Feature] Part__Feature731  label="Raspberry_pizero_PCB005"
  Placement = pos=(0.00138154,-0.0966481,18.0542) rot=(0,0,1;3.14159rad)
  shape: bbox 1.5 x 1 x 1.5 mm, 6 faces (baked)
FEATURE [Part::Feature] Part__Feature732  label="Raspberry_pizero_PCB006"
  Placement = pos=(0.00138154,-0.0966481,18.0542) rot=(0,0,1;3.14159rad)
  shape: bbox 1.5 x 1 x 1.5 mm, 6 faces (baked)
FEATURE [Part::Feature] Part__Feature733  label="Raspberry_pizero_PCB007"
  Placement = pos=(0.00138154,-0.0966481,18.0542) rot=(0,0,1;3.14159rad)
  shape: bbox 1.5 x 1 x 1.5 mm, 6 faces (baked)
FEATURE [Part::Feature] Part__Feature734  label="Raspberry_pizero_PCB008"
  Placement = pos=(0.00138154,-0.0966481,18.0542) rot=(0,0,1;3.14159rad)
  shape: bbox 1.5 x 1 x 1.5 mm, 6 faces (baked)
FEATURE [Part::Feature] Part__Feature735  label="Raspberry_pizero_PCB009"
  Placement = pos=(0.00138154,-0.0966481,18.0542) rot=(0,0,1;3.14159rad)
  shape: bbox 1.5 x 1 x 1.5 mm, 6 faces (baked)
FEATURE [Part::Feature] Part__Feature736  label="Raspberry_pizero_PCB010"
  Placement = pos=(0.00138154,-0.0966481,18.0542) rot=(0,0,1;3.14159rad)
  shape: bbox 1.5 x 1 x 1.5 mm, 6 faces (baked)
FEATURE [Part::Feature] Part__Feature737  label="Raspberry_pizero_PCB011"
  Placement = pos=(0.00138154,-0.0966481,18.0542) rot=(0,0,1;3.14159rad)
  shape: bbox 1.5 x 1 x 1.5 mm, 6 faces (baked)
FEATURE [Part::Feature] Part__Feature738  label="Raspberry_pizero_PCB012"
  Placement = pos=(0.00138154,-0.0966481,18.0542) rot=(0,0,1;3.14159rad)
  shape: bbox 1.5 x 1 x 1.5 mm, 6 faces (baked)
FEATURE [Part::Feature] Part__Feature739  label="Raspberry_pizero_PCB013"
  Placement = pos=(0.00138154,-0.0966481,18.0542) rot=(0,0,1;3.14159rad)
  shape: bbox 1.5 x 1 x 1.5 mm, 6 faces (baked)
FEATURE [Part::Feature] Part__Feature740  label="Raspberry_pizero_PCB014"
  Placement = pos=(0.00138154,-0.0966481,18.0542) rot=(0,0,1;3.14159rad)
  shape: bbox 1.5 x 1 x 1.5 mm, 6 faces (baked)
FEATURE [Part::Feature] Part__Feature741  label="Raspberry_pizero_PCB015"
  Placement = pos=(0.00138154,-0.0966481,18.0542) rot=(0,0,1;3.14159rad)
  shape: bbox 1.5 x 1 x 1.5 mm, 6 faces (baked)
FEATURE [Part::Feature] Part__Feature742  label="Raspberry_pizero_PCB016"
  Placement = pos=(0.00138154,-0.0966481,18.0542) rot=(0,0,1;3.14159rad)
  shape: bbox 1.5 x 1 x 1.5 mm, 6 faces (baked)
FEATURE [Part::Feature] Part__Feature743  label="Raspberry_pizero_PCB017"
  Placement = pos=(0.00138154,-0.0966481,18.0542) rot=(0,0,1;3.14159rad)
  shape: bbox 1.5 x 1 x 1.5 mm, 6 faces (baked)
FEATURE [Part::Feature] Part__Feature744  label="Raspberry_pizero_PCB018"
  Placement = pos=(0.00138154,-0.0966481,18.0542) rot=(0,0,1;3.14159rad)
  shape: bbox 1.5 x 1 x 1.5 mm, 6 faces (baked)
FEATURE [Part::Feature] Part__Feature745  label="Raspberry_pizero_PCB019"
  Placement = pos=(0.00138154,-0.0966481,18.0542) rot=(0,0,1;3.14159rad)
  shape: bbox 1.5 x 1 x 1.5 mm, 6 faces (baked)
FEATURE [Part::Feature] Part__Feature746  label="Raspberry_pizero_PCB020"
  Placement = pos=(0.00138154,-0.0966481,18.0542) rot=(0,0,1;3.14159rad)
  shape: bbox 1.5 x 1 x 1.5 mm, 6 faces (baked)
FEATURE [Part::Feature] Part__Feature747  label="Raspberry_pizero_PCB021"
  Placement = pos=(0.00138154,-0.0966481,18.0542) rot=(0,0,1;3.14159rad)
  shape: bbox 1.5 x 1 x 1.5 mm, 6 faces (baked)
FEATURE [Part::Feature] Part__Feature748  label="Raspberry_pizero_PCB022"
  Placement = pos=(0.00138154,-0.0966481,18.0542) rot=(0,0,1;3.14159rad)
  shape: bbox 1.5 x 1 x 1.5 mm, 6 faces (baked)
FEATURE [Part::Feature] Part__Feature749  label="Raspberry_pizero_PCB023"
  Placement = pos=(0.00138154,-0.0966481,18.0542) rot=(0,0,1;3.14159rad)
  shape: bbox 1.5 x 1 x 1.5 mm, 6 faces (baked)
FEATURE [Part::Feature] Part__Feature750  label="Raspberry_pizero_PCB024"
  Placement = pos=(0.00138154,-0.0966481,18.0542) rot=(0,0,1;3.14159rad)
  shape: bbox 1.5 x 1 x 1.5 mm, 6 faces (baked)
FEATURE [Part::Feature] Part__Feature751  label="Raspberry_pizero_PCB025"
  Placement = pos=(0.00138154,-0.0966481,18.0542) rot=(0,0,1;3.14159rad)
  shape: bbox 1.5 x 1 x 1.5 mm, 6 faces (baked)
FEATURE [Part::Feature] Part__Feature752  label="Raspberry_pizero_PCB026"
  Placement = pos=(0.00138154,-0.0966481,18.0542) rot=(0,0,1;3.14159rad)
  shape: bbox 1.5 x 1 x 1.5 mm, 6 faces (baked)
FEATURE [Part::Feature] Part__Feature753  label="Raspberry_pizero_PCB027"
  Placement = pos=(0.00138154,-0.0966481,18.0542) rot=(0,0,1;3.14159rad)
  shape: bbox 1.5 x 1 x 1.5 mm, 6 faces (baked)
FEATURE [Part::Feature] Part__Feature754  label="Raspberry_pizero_PCB028"
  Placement = pos=(0.00138154,-0.0966481,18.0542) rot=(0,0,1;3.14159rad)
  shape: bbox 1.5 x 1 x 1.5 mm, 6 faces (baked)
FEATURE [Part::Feature] Part__Feature755  label="Raspberry_pizero_PCB029"
  Placement = pos=(0.00138154,-0.0966481,18.0542) rot=(0,0,1;3.14159rad)
  shape: bbox 1.5 x 1 x 1.5 mm, 6 faces (baked)
FEATURE [Part::Feature] Part__Feature756  label="Raspberry_pizero_PCB030"
  Placement = pos=(0.00138154,-0.0966481,18.0542) rot=(0,0,1;3.14159rad)
  shape: bbox 1.5 x 1 x 1.5 mm, 6 faces (baked)
FEATURE [Part::Feature] Part__Feature757  label="Raspberry_pizero_PCB031"
  Placement = pos=(0.00138154,-0.0966481,18.0542) rot=(0,0,1;3.14159rad)
  shape: bbox 1.5 x 1 x 1.5 mm, 6 faces (baked)
FEATURE [Part::Feature] Part__Feature758  label="Raspberry_pizero_PCB032"
  Placement = pos=(0.00138154,-0.0966481,18.0542) rot=(0,0,1;3.14159rad)
  shape: bbox 1.5 x 1 x 1.5 mm, 6 faces (baked)
FEATURE [Part::Feature] Part__Feature759  label="Raspberry_pizero_PCB033"
  Placement = pos=(0.00138154,-0.0966481,18.0542) rot=(0,0,1;3.14159rad)
  shape: bbox 1.5 x 1 x 1.5 mm, 6 faces (baked)
FEATURE [Part::Feature] Part__Feature760  label="Raspberry_pizero_PCB034"
  Placement = pos=(0.00138154,-0.0966481,18.0542) rot=(0,0,1;3.14159rad)
  shape: bbox 1.5 x 1 x 1.5 mm, 6 faces (baked)
FEATURE [Part::Feature] Part__Feature761  label="Raspberry_pizero_PCB035"
  Placement = pos=(0.00138154,-0.0966481,18.0542) rot=(0,0,1;3.14159rad)
  shape: bbox 1.5 x 1 x 1.5 mm, 6 faces (baked)
FEATURE [Part::Feature] Part__Feature762  label="Raspberry_pizero_PCB036"
  Placement = pos=(0.00138154,-0.0966481,18.0542) rot=(0,0,1;3.14159rad)
  shape: bbox 1.5 x 1 x 1.5 mm, 6 faces (baked)
FEATURE [Part::Feature] Part__Feature763  label="Raspberry_pizero_PCB037"
  Placement = pos=(0.00138154,-0.0966481,18.0542) rot=(0,0,1;3.14159rad)
  shape: bbox 1.5 x 1 x 1.5 mm, 6 faces (baked)
FEATURE [Part::Feature] Part__Feature764  label="Raspberry_pizero_PCB038"
  Placement = pos=(0.00138154,-0.0966481,18.0542) rot=(0,0,1;3.14159rad)
  shape: bbox 1.5 x 1 x 1.5 mm, 6 faces (baked)
FEATURE [Part::Feature] Part__Feature765  label="Raspberry_pizero_PCB039"
  Placement = pos=(0.00138154,-0.0966481,18.0542) rot=(0,0,1;3.14159rad)
  shape: bbox 1.5 x 1 x 1.5 mm, 6 faces (baked)
FEATURE [Part::Feature] Part__Feature766  label="Raspberry_pizero_PCB040"
  Placement = pos=(0.00138154,-0.0966481,18.0542) rot=(0,0,1;3.14159rad)
  shape: bbox 1.5 x 1 x 1.5 mm, 6 faces (baked)
FEATURE [Part::Feature] Part__Feature767  label="Raspberry_pizero_PCB041"
  Placement = pos=(0.00138154,-0.0966481,18.0542) rot=(0,0,1;3.14159rad)
  shape: bbox 1.5 x 1 x 1.5 mm, 6 faces (baked)
FEATURE [Part::Feature] Part__Feature768  label="Raspberry_pizero_PCB042"
  Placement = pos=(0.00138154,-0.0966481,18.0542) rot=(0,0,1;3.14159rad)
  shape: bbox 1.541 x 1 x 1.5 mm, 8 faces (baked)
FEATURE [Part::Feature] Part__Feature769  label="Raspberry_pizero_PCB043"
  Placement = pos=(0.00138154,-0.0966481,18.0542) rot=(0,0,1;3.14159rad)
  shape: bbox 1.459 x 1 x 1.5 mm, 8 faces (baked)
FEATURE [Part::Feature] Part__Feature770  label="Raspberry_pizero_PCB044"
  Placement = pos=(0.00138154,-0.0966481,18.0542) rot=(0,0,1;3.14159rad)
  shape: bbox 6 x 1 x 6 mm, 6 faces (baked)
FEATURE [Part::Feature] Part__Feature771  label="Raspberry_pizero_PCB045"
  Placement = pos=(0.00138154,-0.0966481,18.0542) rot=(0,0,1;3.14159rad)
  shape: bbox 6 x 1 x 6 mm, 6 faces (baked)
FEATURE [Part::Feature] Part__Feature772  label="Raspberry_pizero_PCB046"
  Placement = pos=(0.00138154,-0.0966481,18.0542) rot=(0,0,1;3.14159rad)
  shape: bbox 6 x 1 x 6 mm, 6 faces (baked)
FEATURE [Part::Feature] Part__Feature773  label="Raspberry_pizero_PCB047"
  Placement = pos=(0.00138154,-0.0966481,18.0542) rot=(0,0,1;3.14159rad)
  shape: bbox 6 x 1 x 6 mm, 6 faces (baked)
FEATURE [Part::Feature] Part__Feature774  label="Raspberry_pizero_PCB048"
  Placement = pos=(0.00138154,-0.0966481,18.0542) rot=(0,0,1;3.14159rad)
  shape: bbox 65 x 1 x 30 mm, 130 faces (baked)
FEATURE [Part::Feature] Part__Feature775  label="Micro USB_input_female (short)-SMT"
  Placement = pos=(-8.89862,-2.32165,31.5042) rot=(0,0,1;3.14159rad)
  shape: bbox 7.98 x 2.94 x 5.43 mm, 410 faces (baked)
FEATURE [Part::Feature] Part__Feature776  label="Micro USB_input_female (short)-SMT001"
  Placement = pos=(-21.4986,-2.32165,31.5042) rot=(0,0,1;3.14159rad)
  shape: bbox 7.98 x 2.94 x 5.43 mm, 410 faces (baked)
FEATURE [Part::Feature] Part__Feature777  label="0204 - Capacitor"
  Placement = pos=(11.1571,-1.34665,16.2398) rot=(0,0,1;3.14159rad)
  shape: bbox 1 x 0.5 x 0.6 mm, 44 faces (baked)
FEATURE [Part::Feature] Part__Feature778  label="0204 - Capacitor001"
  Placement = pos=(11.1571,-1.34665,17.2528) rot=(0,0,1;3.14159rad)
  shape: bbox 1 x 0.5 x 0.6 mm, 44 faces (baked)
FEATURE [Part::Feature] Part__Feature779  label="0204 - Capacitor002"
  Placement = pos=(10.5572,-1.34665,18.3136) rot=(0,0,1;3.14159rad)
  shape: bbox 1 x 0.5 x 0.6 mm, 44 faces (baked)
FEATURE [Part::Feature] Part__Feature780  label="0204 - Capacitor003"
  Placement = pos=(10.5572,-1.34665,19.2646) rot=(0,0,1;3.14159rad)
  shape: bbox 1 x 0.5 x 0.6 mm, 44 faces (baked)
FEATURE [Part::Feature] Part__Feature781  label="0204 - Capacitor004"
  Placement = pos=(10.5572,-1.34665,20.241) rot=(0,0,1;3.14159rad)
  shape: bbox 1 x 0.5 x 0.6 mm, 44 faces (baked)
FEATURE [Part::Feature] Part__Feature782  label="0204 - Capacitor005"
  Placement = pos=(10.5572,-1.34665,21.2144) rot=(0,0,1;3.14159rad)
  shape: bbox 1 x 0.5 x 0.6 mm, 44 faces (baked)
FEATURE [Part::Feature] Part__Feature783  label="0204 - Capacitor006"
  Placement = pos=(10.5572,-1.34665,22.2416) rot=(0,0,1;3.14159rad)
  shape: bbox 1 x 0.5 x 0.6 mm, 44 faces (baked)
FEATURE [Part::Feature] Part__Feature784  label="0204 - Capacitor007"
  Placement = pos=(11.3369,-1.34665,25.9695) rot=(0,0,1;3.14159rad)
  shape: bbox 1 x 0.5 x 0.6 mm, 44 faces (baked)
FEATURE [Part::Feature] Part__Feature785  label="0204 - Capacitor008"
  Placement = pos=(11.3369,-1.34665,26.919) rot=(0,0,1;3.14159rad)
  shape: bbox 1 x 0.5 x 0.6 mm, 44 faces (baked)
FEATURE [Part::Feature] Part__Feature786  label="0204 - Capacitor009"
  Placement = pos=(9.20338,-1.34665,27.3712) rot=(0.707107,0,0.707107;3.14159rad)
  shape: bbox 0.6 x 0.5 x 1 mm, 44 faces (baked)
FEATURE [Part::Feature] Part__Feature787  label="0204 - Capacitor010"
  Placement = pos=(8.82571,-1.34665,27.3712) rot=(0.707107,0,-0.707107;3.14159rad)
  shape: bbox 0.6 x 0.5 x 1 mm, 44 faces (baked)
FEATURE [Part::Feature] Part__Feature788  label="0204 - Capacitor011"
  Placement = pos=(7.7916,-1.34665,27.3712) rot=(0.707107,0,-0.707107;3.14159rad)
  shape: bbox 0.6 x 0.5 x 1 mm, 44 faces (baked)
FEATURE [Part::Feature] Part__Feature789  label="0204 - Capacitor012"
  Placement = pos=(1.39463,-1.34665,27.316) rot=(0.707107,0,0.707107;3.14159rad)
  shape: bbox 0.6 x 0.5 x 1 mm, 44 faces (baked)
FEATURE [Part::Feature] Part__Feature790  label="0204 - Capacitor013"
  Placement = pos=(0.994966,-1.34665,27.316) rot=(0.707107,0,-0.707107;3.14159rad)
  shape: bbox 0.6 x 0.5 x 1 mm, 44 faces (baked)
FEATURE [Part::Feature] Part__Feature791  label="0204 - Capacitor014"
  Placement = pos=(-0.0151663,-1.34665,27.316) rot=(0.707107,0,-0.707107;3.14159rad)
  shape: bbox 0.6 x 0.5 x 1 mm, 44 faces (baked)
FEATURE [Part::Feature] Part__Feature792  label="0204 - Capacitor015"
  Placement = pos=(-2.07089,-1.34665,27.316) rot=(0.707107,0,-0.707107;3.14159rad)
  shape: bbox 0.6 x 0.5 x 1 mm, 44 faces (baked)
FEATURE [Part::Feature] Part__Feature793  label="0204 - Capacitor016"
  Placement = pos=(-3.11025,-1.34665,27.316) rot=(0.707107,0,-0.707107;3.14159rad)
  shape: bbox 0.6 x 0.5 x 1 mm, 44 faces (baked)
FEATURE [Part::Feature] Part__Feature794  label="0204 - Capacitor017"
  Placement = pos=(-4.77997,-1.34665,26.113) rot=(0,0,1;3.14159rad)
  shape: bbox 1 x 0.5 x 0.6 mm, 44 faces (baked)
FEATURE [Part::Feature] Part__Feature795  label="0204 - Capacitor018"
  Placement = pos=(-5.52276,-1.34665,25.0663) rot=(0,0,1;3.14159rad)
  shape: bbox 1 x 0.5 x 0.6 mm, 44 faces (baked)
FEATURE [Part::Feature] Part__Feature796  label="0204 - Capacitor019"
  Placement = pos=(-5.52276,-1.34665,24.0675) rot=(0,0,1;3.14159rad)
  shape: bbox 1 x 0.5 x 0.6 mm, 44 faces (baked)
FEATURE [Part::Feature] Part__Feature797  label="0204 - Capacitor020"
  Placement = pos=(-5.52276,-1.34665,23.1249) rot=(0,0,1;3.14159rad)
  shape: bbox 1 x 0.5 x 0.6 mm, 44 faces (baked)
FEATURE [Part::Feature] Part__Feature798  label="0204 - Capacitor021"
  Placement = pos=(-5.52276,-1.34665,22.1095) rot=(0,0,1;3.14159rad)
  shape: bbox 1 x 0.5 x 0.6 mm, 44 faces (baked)
FEATURE [Part::Feature] Part__Feature799  label="0204 - Capacitor022"
  Placement = pos=(-4.90927,-1.34665,21.1412) rot=(0,0,1;3.14159rad)
  shape: bbox 1 x 0.5 x 0.6 mm, 44 faces (baked)
FEATURE [Part::Feature] Part__Feature800  label="0204 - Capacitor023"
  Placement = pos=(-4.90927,-1.34665,20.1229) rot=(0,0,1;3.14159rad)
  shape: bbox 1 x 0.5 x 0.6 mm, 44 faces (baked)
FEATURE [Part::Feature] Part__Feature801  label="0204 - Capacitor024"
  Placement = pos=(-4.90927,-1.34665,19.0197) rot=(0,0,1;3.14159rad)
  shape: bbox 1 x 0.5 x 0.6 mm, 44 faces (baked)
FEATURE [Part::Feature] Part__Feature802  label="0204 - Capacitor025"
  Placement = pos=(-4.90927,-1.34665,17.9589) rot=(0,0,1;3.14159rad)
  shape: bbox 1 x 0.5 x 0.6 mm, 44 faces (baked)
FEATURE [Part::Feature] Part__Feature803  label="0204 - Capacitor026"
  Placement = pos=(-7.63943,-1.34665,18.1418) rot=(0,0,1;3.14159rad)
  shape: bbox 1 x 0.5 x 0.6 mm, 44 faces (baked)
FEATURE [Part::Feature] Part__Feature804  label="0204 - Capacitor027"
  Placement = pos=(-7.63943,-1.34665,15.1424) rot=(0,0,1;3.14159rad)
  shape: bbox 1 x 0.5 x 0.6 mm, 44 faces (baked)
FEATURE [Part::Feature] Part__Feature805  label="0204 - Capacitor028"
  Placement = pos=(-2.34331,-1.34665,12.6917) rot=(0,0,1;3.14159rad)
  shape: bbox 1 x 0.5 x 0.6 mm, 44 faces (baked)
FEATURE [Part::Feature] Part__Feature806  label="0204 - Capacitor029"
  Placement = pos=(4.23759,-1.34665,12.2526) rot=(0.707107,0,-0.707107;3.14159rad)
  shape: bbox 0.6 x 0.5 x 1 mm, 44 faces (baked)
FEATURE [Part::Feature] Part__Feature807  label="0204 - Capacitor030"
  Placement = pos=(2.53825,-1.34665,12.2526) rot=(0.707107,0,0.707107;3.14159rad)
  shape: bbox 0.6 x 0.5 x 1 mm, 44 faces (baked)
FEATURE [Part::Feature] Part__Feature808  label="0204 - Capacitor031"
  Placement = pos=(8.59273,-1.34665,12.2526) rot=(0.707107,0,0.707107;3.14159rad)
  shape: bbox 0.6 x 0.5 x 1 mm, 44 faces (baked)
FEATURE [Part::Feature] Part__Feature809  label="0204- Resistor"
  Placement = pos=(-7.64413,-1.45225,20.4193) rot=(-1,0,0;1.5708rad)
  shape: bbox 0.9906 x 0.3566 x 0.51 mm, 20 faces (baked)
FEATURE [Part::Feature] Part__Feature810  label="0204- Resistor001"
  Placement = pos=(-7.64413,-1.45225,19.4127) rot=(-1,0,0;1.5708rad)
  shape: bbox 0.9906 x 0.3566 x 0.51 mm, 20 faces (baked)
FEATURE [Part::Feature] Part__Feature811  label="0204- Resistor002"
  Placement = pos=(-7.64413,-1.45225,17.4047) rot=(-1,0,0;1.5708rad)
  shape: bbox 0.9906 x 0.3566 x 0.51 mm, 20 faces (baked)
FEATURE [Part::Feature] Part__Feature812  label="0204- Resistor003"
  Placement = pos=(-8.5614,-1.45225,23.4076) rot=(-1,0,0;1.5708rad)
  shape: bbox 0.9906 x 0.3566 x 0.51 mm, 20 faces (baked)
FEATURE [Part::Feature] Part__Feature813  label="0204- Resistor004"
  Placement = pos=(-11.424,-1.45225,23.1462) rot=(0.57735,0.57735,0.57735;4.18879rad)
  shape: bbox 0.51 x 0.3566 x 0.9906 mm, 20 faces (baked)
FEATURE [Part::Feature] Part__Feature814  label="0204- Resistor005"
  Placement = pos=(10.5619,-1.45225,24.8533) rot=(-1,0,0;1.5708rad)
  shape: bbox 0.9906 x 0.3566 x 0.51 mm, 20 faces (baked)
FEATURE [Part::Feature] Part__Feature815  label="0204- Resistor006"
  Placement = pos=(10.5619,-1.45225,23.5178) rot=(-1,0,0;1.5708rad)
  shape: bbox 0.9906 x 0.3566 x 0.51 mm, 20 faces (baked)
FEATURE [Part::Feature] Part__Feature818  label="0204- Resistor009"
  Placement = pos=(-23.1723,-1.45225,14.5819) rot=(-1,0,0;1.5708rad)
  shape: bbox 0.9906 x 0.3566 x 0.51 mm, 20 faces (baked)
FEATURE [Part::Feature] Part__Feature820  label="CAP-0306"
  Placement = pos=(-5.36466,-1.49665,13.7634) rot=(0,0,1;3.14159rad)
  shape: bbox 1.6 x 0.8 x 0.9 mm, 44 faces (baked)
FEATURE [Part::Feature] Part__Feature821  label="CAP-0307"
  Placement = pos=(30.7481,-1.49665,24.0464) rot=(0.707107,0,0.707107;3.14159rad)
  shape: bbox 0.9 x 0.8 x 1.6 mm, 44 faces (baked)
FEATURE [Part::Feature] Part__Feature822  label="Raspberry_pizero_BCM2835 with VC4"
  Placement = pos=(2.90576,-1.54665,20.1238) rot=(0,1,0;3.14159rad)
  shape: bbox 12 x 0.65 x 12 mm, 513 faces (baked)
FEATURE [Part::Feature] Part__Feature823  label="Crystal 3.4x2.4mm"
  Placement = pos=(14.0539,-1.09665,24.2633) rot=(0,0,1;3.14159rad)
  shape: bbox 3.2 x 0.7 x 2.4 mm, 10 faces (baked)
FEATURE [Part::Feature] Part__Feature824  label="Crystal 3.4x2.4mm001"
  Placement = pos=(14.0539,-1.09665,24.2633) rot=(0,0,1;3.14159rad)
  shape: bbox 2.972 x 0.15 x 2.174 mm, 10 faces (baked)
FEATURE [Part::Feature] Part__Feature825  label="Crystal 3.4x2.4mm002"
  Placement = pos=(14.0539,-1.09665,24.2633) rot=(0,0,1;3.14159rad)
  shape: bbox 2.889 x 0.15 x 2.082 mm, 18 faces (baked)
FEATURE [Part::Feature] Part__Feature826  label="0204- Resistor011"
  Placement = pos=(17.1779,-1.45225,10.4384) rot=(0.57735,0.57735,0.57735;4.18879rad)
  shape: bbox 0.51 x 0.3566 x 0.9906 mm, 20 faces (baked)
FEATURE [Part::Feature] Part__Feature827  label="0204- Resistor012"
  Placement = pos=(18.4705,-1.45225,10.4384) rot=(0.57735,0.57735,0.57735;4.18879rad)
  shape: bbox 0.51 x 0.3566 x 0.9906 mm, 20 faces (baked)
FEATURE [Part::Feature] Part__Feature828  label="0204- Resistor013"
  Placement = pos=(13.8076,-1.45225,21.5355) rot=(0,0.707107,0.707107;3.14159rad)
  shape: bbox 0.9906 x 0.3566 x 0.51 mm, 20 faces (baked)
FEATURE [Part::Feature] Part__Feature829  label="32,768 Khz Crystal"
  Placement = pos=(9.26038,-1.14283,31.5473) rot=(0,0,1;3.12414rad)
  shape: bbox 3.4 x 1.071 x 1.5 mm, 30 faces (baked)
FEATURE [Part::Feature] Part__Feature830  label="0805- Capacitor"
  Placement = pos=(0.694564,-1.99665,10.2384) rot=(0,0.707107,0.707107;3.14159rad)
  shape: bbox 2 x 0.9 x 1.25 mm, 56 faces (baked)
FEATURE [Part::Feature] Part__Feature831  label="0805- Capacitor001"
  Placement = pos=(0.694564,-1.99665,12.3589) rot=(0,0.707107,0.707107;3.14159rad)
  shape: bbox 2 x 0.9 x 1.25 mm, 56 faces (baked)
FEATURE [Part::Feature] Part__Feature832  label="0805- Capacitor002"
  Placement = pos=(-14.246,-1.99665,27.5384) rot=(0.57735,-0.57735,-0.57735;4.18879rad)
  shape: bbox 1.25 x 0.9 x 2 mm, 56 faces (baked)
FEATURE [Part::Feature] Part__Feature833  label="0805- Capacitor003"
  Placement = pos=(-21.4303,-1.99665,18.3538) rot=(0.57735,0.57735,0.57735;4.18879rad)
  shape: bbox 1.25 x 0.9 x 2 mm, 56 faces (baked)
FEATURE [Part::Feature] Part__Feature834  label="0805- Capacitor004"
  Placement = pos=(-23.3498,-1.99665,18.3538) rot=(0.57735,-0.57735,-0.57735;4.18879rad)
  shape: bbox 1.25 x 0.9 x 2 mm, 56 faces (baked)
FEATURE [Part::Feature] Part__Feature835  label="0805- Capacitor005"
  Placement = pos=(-28.4547,-1.99665,18.3538) rot=(0.57735,-0.57735,-0.57735;4.18879rad)
  shape: bbox 1.25 x 0.9 x 2 mm, 56 faces (baked)
FEATURE [Part::Feature] Part__Feature836  label="0805- Capacitor006"
  Placement = pos=(-30.2626,-1.99665,18.3538) rot=(0.57735,-0.57735,-0.57735;4.18879rad)
  shape: bbox 1.25 x 0.9 x 2 mm, 56 faces (baked)
FEATURE [Part::Feature] Part__Feature837  label="0204- Resistor014"
  Placement = pos=(-2.37813,-1.45225,28.8207) rot=(0,0.707107,0.707107;3.14159rad)
  shape: bbox 0.9906 x 0.3566 x 0.51 mm, 20 faces (baked)
FEATURE [Part::Feature] Part__Feature838  label="0204- Resistor015"
  Placement = pos=(1.16154,-1.45225,29.0419) rot=(0,0.707107,0.707107;3.14159rad)
  shape: bbox 0.9906 x 0.3566 x 0.51 mm, 20 faces (baked)
FEATURE [Part::Feature] Part__Feature839  label="0204 - Capacitor032"
  Placement = pos=(-4.13512,-1.34665,28.926) rot=(0.707107,0,0.707107;3.14159rad)
  shape: bbox 0.6 x 0.5 x 1 mm, 44 faces (baked)
FEATURE [Part::Feature] Part__Feature840  label="0204 - Capacitor Brown"
  Placement = pos=(6.32673,-1.34665,31.803) rot=(0,0,1;3.14159rad)
  shape: bbox 1 x 0.5 x 0.6 mm, 44 faces (baked)
FEATURE [Part::Feature] Part__Feature841  label="0204 - Capacitor Brown001"
  Placement = pos=(12.7762,-1.34665,31.8794) rot=(0,0,1;3.14159rad)
  shape: bbox 1 x 0.5 x 0.6 mm, 44 faces (baked)
FEATURE [Part::Feature] Part__Feature842  label="0204 - Capacitor Brown002"
  Placement = pos=(-4.90927,-1.34665,17.214) rot=(0,0,1;3.14159rad)
  shape: bbox 1 x 0.5 x 0.6 mm, 44 faces (baked)
FEATURE [Part::Feature] Part__Feature843  label="0204 - Capacitor Brown003"
  Placement = pos=(-4.90927,-1.34665,16.0963) rot=(0,0,1;3.14159rad)
  shape: bbox 1 x 0.5 x 0.6 mm, 44 faces (baked)
FEATURE [Part::Feature] Part__Feature844  label="0204 - Capacitor Brown004"
  Placement = pos=(-4.90927,-1.34665,15.1566) rot=(0,0,1;3.14159rad)
  shape: bbox 1 x 0.5 x 0.6 mm, 44 faces (baked)
FEATURE [Part::Feature] Part__Feature845  label="0204 - Capacitor Brown005"
  Placement = pos=(-7.63943,-1.34665,16.1151) rot=(0,0,1;3.14159rad)
  shape: bbox 1 x 0.5 x 0.6 mm, 44 faces (baked)
FEATURE [Part::Feature] Part__Feature846  label="0204 - Capacitor Brown006"
  Placement = pos=(-23.1676,-1.34665,15.3236) rot=(0,0,1;3.14159rad)
  shape: bbox 1 x 0.5 x 0.6 mm, 44 faces (baked)
FEATURE [Part::Feature] Part__Feature847  label="0204 - Capacitor Brown007"
  Placement = pos=(29.3647,-1.34665,25.6997) rot=(0,0,1;3.14159rad)
  shape: bbox 1 x 0.5 x 0.6 mm, 44 faces (baked)
FEATURE [Part::Feature] Part__Feature848  label="0204- Resistor016"
  Placement = pos=(27.6555,-1.45225,26.1554) rot=(0,0.707107,0.707107;3.14159rad)
  shape: bbox 0.9906 x 0.3566 x 0.51 mm, 20 faces (baked)
FEATURE [Part::Feature] Part__Feature849  label="6-Pin SOT"
  Placement = pos=(28.459,-1.09665,24.2138) rot=(0.57735,-0.57735,0.57735;2.0944rad)
  shape: bbox 1.84 x 0.96 x 1.512 mm, 125 faces (baked)
FEATURE [Part::Feature] Part__Feature850  label="micro sd molex"
  Placement = pos=(23.5218,-1.67665,-28.0961) rot=(0.57735,-0.57735,0.57735;2.0944rad)
  shape: bbox 11.43 x 1.48 x 11.98 mm, 410 faces (baked)
FEATURE [Part::Feature] Part__Feature851  label="hdmi type C"
  Placement = pos=(20.1014,-2.94665,33.6542) rot=(0,0,1;3.14159rad)
  shape: bbox 12.9 x 4.05 x 7.7 mm, 690 faces (baked)
FEATURE [Part::Feature] Part__Feature852  label="Voltage Regulator 3x3mm 12-Pin"
  Placement = pos=(-27.5708,-1.09665,17.6105) rot=(0,0.707107,-0.707107;3.14159rad)
  shape: bbox 0.2 x 0.6919 x 0.5488 mm, 13 faces (baked)
FEATURE [Part::Feature] Part__Feature853  label="Voltage Regulator 3x3mm 12-Pin001"
  Placement = pos=(-27.5708,-1.09665,17.6105) rot=(0,0.707107,-0.707107;3.14159rad)
  shape: bbox 3 x 1.28 x 3.549 mm, 145 faces (baked)
FEATURE [Part::Feature] Part__Feature854  label="Voltage Regulator 3x3mm 12-Pin002"
  Placement = pos=(-27.5708,-1.09665,17.6105) rot=(0,0.707107,-0.707107;3.14159rad)
  shape: bbox 0.2 x 0.6919 x 0.5488 mm, 13 faces (baked)
FEATURE [Part::Feature] Part__Feature855  label="Voltage Regulator 3x3mm 12-Pin003"
  Placement = pos=(-27.5708,-1.09665,17.6105) rot=(0,0.707107,-0.707107;3.14159rad)
  shape: bbox 0.2 x 0.6919 x 0.5488 mm, 13 faces (baked)
FEATURE [Part::Feature] Part__Feature856  label="Voltage Regulator 3x3mm 12-Pin004"
  Placement = pos=(-27.5708,-1.09665,17.6105) rot=(0,0.707107,-0.707107;3.14159rad)
  shape: bbox 0.2 x 0.6919 x 0.5488 mm, 13 faces (baked)
FEATURE [Part::Feature] Part__Feature857  label="Voltage Regulator 3x3mm 12-Pin005"
  Placement = pos=(-27.5708,-1.09665,17.6105) rot=(0,0.707107,-0.707107;3.14159rad)
  shape: bbox 0.2 x 0.6919 x 0.5488 mm, 13 faces (baked)
FEATURE [Part::Feature] Part__Feature858  label="Voltage Regulator 3x3mm 12-Pin006"
  Placement = pos=(-27.5708,-1.09665,17.6105) rot=(0,0.707107,-0.707107;3.14159rad)
  shape: bbox 0.2 x 0.6919 x 0.5488 mm, 13 faces (baked)
FEATURE [Part::Feature] Part__Feature859  label="1210 inductor"
  Placement = pos=(-4.75875,-1.09165,11.3909) rot=(0.57735,-0.57735,0.57735;2.0944rad)
  shape: bbox 2.531 x 0.581 x 3.231 mm, 39 faces (baked)
FEATURE [Part::Feature] Part__Feature860  label="1210 inductor001"
  Placement = pos=(-28.5145,-1.09165,14.2394) rot=(0,0.707107,-0.707107;3.14159rad)
  shape: bbox 3.231 x 0.581 x 2.531 mm, 39 faces (baked)
FEATURE [Part::Feature] Part__Feature861  label="1210 inductor002"
  Placement = pos=(-22.9696,-1.09165,22.6682) rot=(0,0.707107,-0.707107;3.14159rad)
  shape: bbox 3.231 x 0.581 x 2.531 mm, 39 faces (baked)
FEATURE [Part::Feature] Part__Feature862  label="0204 - Capacitor033"
  Placement = pos=(-2.34331,-1.34665,11.5273) rot=(0,0,1;3.14159rad)
  shape: bbox 1 x 0.5 x 0.6 mm, 44 faces (baked)
FEATURE [App::DocumentObjectGroup] Grupo029  label="raspberrypizerow"
  Group = -> [Part__Feature726,Part__Feature727,Part__Feature728,Part__Feature729,Part__Feature730,Part__Feature731,Part__Feature732,Part__Feature733,Part__Feature734,Part__Feature735,Part__Feature736,Part__Feature737,Part__Feature738,Part__Feature739,Part__Feature740,Part__Feature741,Part__Feature742,Part__Feature743,Part__Feature744,Part__Feature745,Part__Feature746,Part__Feature747,Part__Feature748,+114 more]
FEATURE [App::DocumentObjectGroup] Grupo035  label="boards"
  Group = -> [Grupo027,RaspberryPi3_ModelB,Part__Feature,Grupo029]
FEATURE [Part::Box] Box  label="Prusa hephestos volume"
  AttacherType = Attacher::AttachEngine3D
  Height = 180
  Length = 215
  Placement = pos=(-107.5,-105,0) rot=(0,0,1;0rad)
  Width = 210
FEATURE [Sketcher::SketchObject] Sketch
  MapMode = 5
  Support = -> [XY_Plane001]
  sketch-geometry (16):
    g0: LineSegment StartX=-25.0001 StartY=40.9997 StartZ=0 EndX=25 EndY=40.9997 EndZ=0
    g1: LineSegment StartX=25 StartY=-25 StartZ=0 EndX=-25 EndY=-25 EndZ=0
    g2: LineSegment StartX=-27.9999 StartY=-22 StartZ=0 EndX=-27.9999 EndY=37.9999 EndZ=0
    g3: LineSegment StartX=22 StartY=33 StartZ=0 EndX=22 EndY=-1 EndZ=0
    g4: LineSegment StartX=23 StartY=-2 StartZ=0 EndX=27 EndY=-2 EndZ=0
    g5: LineSegment StartX=28 StartY=-3 StartZ=0 EndX=28 EndY=-22 EndZ=0
    g6: ArcOfCircle CenterX=23 CenterY=-1 CenterZ=0 NormalX=0 NormalY=0 NormalZ=1 AngleXU=0 Radius=1 StartAngle=3.14159 EndAngle=4.71239
    g7: ArcOfCircle CenterX=27 CenterY=-3 CenterZ=0 NormalX=0 NormalY=0 NormalZ=1 AngleXU=0 Radius=0.999998 StartAngle=0 EndAngle=1.5708
    g8: ArcOfCircle CenterX=25 CenterY=37.9997 CenterZ=0 NormalX=0 NormalY=0 NormalZ=1 AngleXU=0 Radius=3.00006 StartAngle=0.000107291 EndAngle=1.5708
    g9: ArcOfCircle CenterX=-25.0001 CenterY=37.9999 CenterZ=0 NormalX=0 NormalY=0 NormalZ=1 AngleXU=0 Radius=2.99987 StartAngle=1.5708 EndAngle=3.14159
    g10: ArcOfCircle CenterX=-25 CenterY=-22 CenterZ=0 NormalX=0 NormalY=0 NormalZ=1 AngleXU=0 Radius=2.99997 StartAngle=3.14159 EndAngle=4.71239
    g11: ArcOfCircle CenterX=25 CenterY=-22 CenterZ=0 NormalX=0 NormalY=0 NormalZ=1 AngleXU=0 Radius=2.99999 StartAngle=4.71239 EndAngle=6.28319
    g12: LineSegment StartX=28 StartY=38 StartZ=0 EndX=28.0001 EndY=37 EndZ=0
    g13: LineSegment StartX=25.0004 StartY=34 StartZ=0 EndX=23 EndY=34 EndZ=0
    g14: ArcOfCircle CenterX=23 CenterY=33 CenterZ=0 NormalX=0 NormalY=0 NormalZ=1 AngleXU=0 Radius=1 StartAngle=1.5708 EndAngle=3.14159
    g15: ArcOfCircle CenterX=25.0004 CenterY=36.9997 CenterZ=0 NormalX=0 NormalY=0 NormalZ=1 AngleXU=0 Radius=2.99968 StartAngle=4.71239 EndAngle=6.28329
  constraints (23):
    c: Horizontal(g0)
    c: Horizontal(g1)
    c: Vertical(g2)
    c: Vertical(g3)
    c: Horizontal(g4)
    c: Vertical(g5)
    c: Tangent(g3,g6) = -1.5708
    c: Tangent(g4,g6) = -1.5708
    c: Tangent(g4,g7) = 1.5708
    c: Tangent(g5,g7) = 1.5708
    c: Tangent(g0,g8) = 1.5708
    c: Tangent(g0,g9) = 1.5708
    c: Tangent(g2,g9) = 1.5708
    c: Tangent(g2,g10) = 1.5708
    c: Tangent(g1,g10) = 1.5708
    c: Tangent(g5,g11) = 1.5708
    c: Tangent(g1,g11) = 1.5708
    c: Tangent(g8,g12) = 1.5708
    c: Horizontal(g13)
    c: Tangent(g3,g14) = -1.5708
    c: Tangent(g13,g14) = -1.5708
    c: Tangent(g12,g15) = 1.5708
    c: Tangent(g13,g15) = 1.5708
FEATURE [PartDesign::Pad] Pad
  Length = 2
  Length2 = 100
  Profile = -> Sketch
  Refine = true
  Reversed = true
  Type = 0
FEATURE [Sketcher::SketchObject] Sketch001  label="base_hole001"
  MapMode = 5
  Support = -> [Pad]
  sketch-geometry (4):
    g0: Circle CenterX=-8.89655 CenterY=37.5352 CenterZ=0 NormalX=0 NormalY=0 NormalZ=1 AngleXU=0 Radius=1.75
    g1: Circle CenterX=19.0482 CenterY=37.5542 CenterZ=0 NormalX=0 NormalY=0 NormalZ=1 AngleXU=0 Radius=1.75
    g2: Circle CenterX=-24.1122 CenterY=-13.2549 CenterZ=0 NormalX=0 NormalY=0 NormalZ=1 AngleXU=0 Radius=1.75
    g3: Circle CenterX=24.1531 CenterY=-14.5174 CenterZ=0 NormalX=0 NormalY=0 NormalZ=1 AngleXU=0 Radius=1.75
  constraints (4):
    c: Radius(g0) = 1.75
    c: Equal(g0,g1) = 1.75
    c: Equal(g0,g2) = 1.75
    c: Equal(g0,g3) = 1.75
FEATURE [PartDesign::Pocket] Pocket  label="base_hole"
  BaseFeature = -> Pad
  Length = 5
  Length2 = 100
  Profile = -> Sketch001
  Refine = true
  Type = 0
FEATURE [Sketcher::SketchObject] Sketch002  label="columns"
  MapMode = 5
  Placement = pos=(0,0,-2) rot=(1,0,0;3.14159rad)
  Support = -> [Pocket]
  sketch-geometry (8):
    g0: Circle CenterX=-24.441 CenterY=20.4974 CenterZ=0 NormalX=0 NormalY=0 NormalZ=1 AngleXU=0 Radius=3
    g1: Circle CenterX=24.4919 CenterY=20.4964 CenterZ=0 NormalX=0 NormalY=0 NormalZ=1 AngleXU=0 Radius=3
    g2: Circle CenterX=-24.5115 CenterY=-37.516 CenterZ=0 NormalX=0 NormalY=0 NormalZ=1 AngleXU=0 Radius=3
    g3: Circle CenterX=24.5041 CenterY=-37.5051 CenterZ=0 NormalX=0 NormalY=0 NormalZ=1 AngleXU=0 Radius=3
    g4: Circle CenterX=-24.441 CenterY=20.4974 CenterZ=0 NormalX=0 NormalY=0 NormalZ=1 AngleXU=0 Radius=1.6
    g5: Circle CenterX=24.4919 CenterY=20.4964 CenterZ=0 NormalX=0 NormalY=0 NormalZ=1 AngleXU=0 Radius=1.6
    g6: Circle CenterX=-24.5115 CenterY=-37.516 CenterZ=0 NormalX=0 NormalY=0 NormalZ=1 AngleXU=0 Radius=1.6
    g7: Circle CenterX=24.5041 CenterY=-37.5051 CenterZ=0 NormalX=0 NormalY=0 NormalZ=1 AngleXU=0 Radius=1.6
  constraints (12):
    c: Radius(g0) = 3
    c: Equal(g0,g1) = 3
    c: Equal(g0,g2) = 3
    c: Equal(g0,g3) = 3
    c: Coincident(g4,g0)
    c: Radius(g4) = 1.6
    c: Equal(g4,g5) = 1.6
    c: Coincident(g1,g5)
    c: Equal(g4,g6) = 1.6
    c: Coincident(g2,g6)
    c: Equal(g4,g7) = 1.6
    c: Coincident(g3,g7)
FEATURE [PartDesign::Pad] Pad001  label="columns001"
  BaseFeature = -> Pocket
  Length = 21
  Length2 = 100
  Profile = -> Sketch002
  Refine = true
  Type = 0
FEATURE [PartDesign::Body] Body  label="base"
  Group = -> [Sketch,Pad,Sketch001,Pocket,Sketch002,Pad001]
  Origin = -> Origin001
  Placement = pos=(0,0,24.5) rot=(0,0,1;0rad)
  Tip = -> Pad001
FEATURE [App::Part] Part  label="raspy_alhambra_holder"
  Group = -> [Body]
  License = CC BY 3.0
  LicenseURL = http://creativecommons.org/licenses/by/3.0/
  Origin = -> Origin
FEATURE [Sketcher::SketchObject] Sketch003
  MapMode = 5
  Support = -> [XY_Plane002]
  sketch-geometry (6):
    g0: LineSegment StartX=-28 StartY=37.529 StartZ=0 EndX=-28 EndY=33.4133 EndZ=0
    g1: LineSegment StartX=-28 StartY=33.4133 StartZ=0 EndX=-21 EndY=33.4133 EndZ=0
    g2: LineSegment StartX=-21 StartY=33.4133 StartZ=0 EndX=-21 EndY=37.4648 EndZ=0
    g3: LineSegment StartX=-21 StartY=37.4648 StartZ=0 EndX=-22 EndY=37.4648 EndZ=0
    g4: LineSegment StartX=-28 StartY=37.529 StartZ=0 EndX=-27 EndY=37.529 EndZ=0
    g5: ArcOfCircle CenterX=-24.5 CenterY=37.4999 CenterZ=0 NormalX=0 NormalY=0 NormalZ=1 AngleXU=0 Radius=2.50021 StartAngle=6.26915 EndAngle=9.41312
  constraints (11):
    c: Vertical(g0)
    c: Coincident(g0,g1)
    c: Horizontal(g1)
    c: Coincident(g1,g2)
    c: Vertical(g2)
    c: Coincident(g2,g3)
    c: Horizontal(g3)
    c: Coincident(g0,g4)
    c: Horizontal(g4)
    c: Coincident(g5,g4)
    c: Coincident(g5,g3)
FEATURE [PartDesign::Pad] Pad002
  Length = 10
  Length2 = 100
  Profile = -> Sketch003
  Refine = true
  Type = 0
FEATURE [PartDesign::Body] Body001  label="empty_columns"
  Group = -> [Sketch003,Pad002]
  Origin = -> Origin002
  Placement = pos=(0,0,3.5) rot=(0,0,1;0rad)
  Tip = -> Pad002
FEATURE [Sketcher::SketchObject] Sketch004
  MapMode = 5
  Support = -> [XY_Plane003]
  sketch-geometry (6):
    g0: LineSegment StartX=-28 StartY=37.529 StartZ=0 EndX=-28 EndY=33.4133 EndZ=0
    g1: LineSegment StartX=-28 StartY=33.4133 StartZ=0 EndX=-21 EndY=33.4133 EndZ=0
    g2: LineSegment StartX=-21 StartY=33.4133 StartZ=0 EndX=-21 EndY=37.4648 EndZ=0
    g3: LineSegment StartX=-21 StartY=37.4648 StartZ=0 EndX=-22 EndY=37.4648 EndZ=0
    g4: LineSegment StartX=-28 StartY=37.529 StartZ=0 EndX=-27 EndY=37.529 EndZ=0
    g5: ArcOfCircle CenterX=-24.5 CenterY=37.4999 CenterZ=0 NormalX=0 NormalY=0 NormalZ=1 AngleXU=0 Radius=2.50021 StartAngle=6.26915 EndAngle=9.41312
  constraints (11):
    c: Vertical(g0)
    c: Coincident(g0,g1)
    c: Horizontal(g1)
    c: Coincident(g1,g2)
    c: Vertical(g2)
    c: Coincident(g2,g3)
    c: Horizontal(g3)
    c: Coincident(g0,g4)
    c: Horizontal(g4)
    c: Coincident(g5,g4)
    c: Coincident(g5,g3)
FEATURE [PartDesign::Pad] Pad003
  Length = 10
  Length2 = 100
  Profile = -> Sketch004
  Refine = true
  Type = 0
FEATURE [PartDesign::Body] Body002  label="empty_columns001"
  Group = -> [Sketch004,Pad003]
  Origin = -> Origin003
  Placement = pos=(49,0,3.5) rot=(0,0,1;0rad)
  Tip = -> Pad003
FEATURE [Sketcher::SketchObject] Sketch005
  MapMode = 5
  Support = -> [XY_Plane004]
  sketch-geometry (6):
    g0: LineSegment StartX=-28 StartY=37.529 StartZ=0 EndX=-28 EndY=33.4133 EndZ=0
    g1: LineSegment StartX=-28 StartY=33.4133 StartZ=0 EndX=-21 EndY=33.4133 EndZ=0
    g2: LineSegment StartX=-21 StartY=33.4133 StartZ=0 EndX=-21 EndY=37.4648 EndZ=0
    g3: LineSegment StartX=-21 StartY=37.4648 StartZ=0 EndX=-22 EndY=37.4648 EndZ=0
    g4: LineSegment StartX=-28 StartY=37.529 StartZ=0 EndX=-27 EndY=37.529 EndZ=0
    g5: ArcOfCircle CenterX=-24.5 CenterY=37.4999 CenterZ=0 NormalX=0 NormalY=0 NormalZ=1 AngleXU=0 Radius=2.50021 StartAngle=6.26915 EndAngle=9.41312
  constraints (11):
    c: Vertical(g0)
    c: Coincident(g0,g1)
    c: Horizontal(g1)
    c: Coincident(g1,g2)
    c: Vertical(g2)
    c: Coincident(g2,g3)
    c: Horizontal(g3)
    c: Coincident(g0,g4)
    c: Horizontal(g4)
    c: Coincident(g5,g4)
    c: Coincident(g5,g3)
FEATURE [PartDesign::Pad] Pad004
  Length = 10
  Length2 = 100
  Profile = -> Sketch005
  Refine = true
  Type = 0
FEATURE [PartDesign::Body] Body003  label="empty_columns002"
  Group = -> [Sketch005,Pad004]
  Origin = -> Origin004
  Placement = pos=(0,17,3.5) rot=(0,0,1;3.14159rad)
  Tip = -> Pad004
FEATURE [Sketcher::SketchObject] Sketch006
  MapMode = 5
  Support = -> [XY_Plane005]
  sketch-geometry (6):
    g0: LineSegment StartX=-28 StartY=37.529 StartZ=0 EndX=-28 EndY=33.4133 EndZ=0
    g1: LineSegment StartX=-28 StartY=33.4133 StartZ=0 EndX=-21 EndY=33.4133 EndZ=0
    g2: LineSegment StartX=-21 StartY=33.4133 StartZ=0 EndX=-21 EndY=37.4648 EndZ=0
    g3: LineSegment StartX=-21 StartY=37.4648 StartZ=0 EndX=-22 EndY=37.4648 EndZ=0
    g4: LineSegment StartX=-28 StartY=37.529 StartZ=0 EndX=-27 EndY=37.529 EndZ=0
    g5: ArcOfCircle CenterX=-24.5 CenterY=37.4999 CenterZ=0 NormalX=0 NormalY=0 NormalZ=1 AngleXU=0 Radius=2.50021 StartAngle=6.26915 EndAngle=9.41312
  constraints (11):
    c: Vertical(g0)
    c: Coincident(g0,g1)
    c: Horizontal(g1)
    c: Coincident(g1,g2)
    c: Vertical(g2)
    c: Coincident(g2,g3)
    c: Horizontal(g3)
    c: Coincident(g0,g4)
    c: Horizontal(g4)
    c: Coincident(g5,g4)
    c: Coincident(g5,g3)
FEATURE [PartDesign::Pad] Pad005
  Length = 10
  Length2 = 100
  Profile = -> Sketch006
  Refine = true
  Type = 0
FEATURE [PartDesign::Body] Body004  label="empty_columns003"
  Group = -> [Sketch006,Pad005]
  Origin = -> Origin005
  Placement = pos=(-49,17,3.5) rot=(0,0,1;3.14159rad)
  Tip = -> Pad005
FEATURE [Part::MultiFuse] Fusion  label="empty_columns004"
  Refine = true
  Shapes = -> [Body001,Body004,Body003,Body002]
FEATURE [Part::FeaturePython] Clone  label="raspy_alhambra_holder_clone"  # Draft clone (typed FeaturePython)
  AttacherType = Attacher::AttachEngine3D
  Fuse = false
  Objects = -> [Body]
  Placement = pos=(0,0,80) rot=(0,0,1;0rad)
  Scale = (1,1,1)
FEATURE [App::DocumentObjectGroup] Grupo037  label="raspy_alhambra_holder002"
  Group = -> [Clone]
FEATURE [Part::Box] Box001  label="Prusa hephestos area"
  AttacherType = Attacher::AttachEngine3D
  Height = 0.1
  Length = 215
  Placement = pos=(-107.5,-105,-1) rot=(0,0,1;0rad)
  Width = 210
FEATURE [Part::Feature] Fusion007033  label="Servo-sg90-final001"
  Placement = pos=(56.5,-57.5,0) rot=(0,0,1;0rad)
  shape: bbox 11.8 x 32.4 x 29.9 mm, 77 faces (baked)
FEATURE [Part::Feature] Fusion007034  label="Servo-sg90-final002"
  Placement = pos=(56.5,-57.5,0) rot=(0,0,1;0rad)
  shape: bbox 11.8 x 32.4 x 29.9 mm, 77 faces (baked)
FEATURE [Part::Feature] Part__Feature863  label="Rpi3Bplus001"
  Placement = pos=(-28,41,56) rot=(0.57735,-0.57735,-0.57735;2.0944rad)
  shape: bbox 58.47 x 87.03 x 17.52 mm, 2323 faces, 179 solids (baked)
FEATURE [Part::Feature] Part__Feature864  label="C_0402_106"
  Placement = pos=(-8.2042,-22.8004,81.7) rot=(0,0,-1;1.5708rad)
  shape: bbox 0.5 x 0.985 x 0.5 mm, 44 faces (baked)
FEATURE [Part::Feature] Part__Feature865  label="R_0402_074"
  Placement = pos=(-10.5283,-5.1855,81.7) rot=(0,0,1;3.14159rad)
  shape: bbox 1 x 0.5 x 0.3 mm, 40 faces (baked)
FEATURE [Part::Feature] Part__Feature866  label="Pcb008"
  Placement = pos=(-115.57,-125.01,81.7) rot=(0,0,1;1.5708rad)
  shape: bbox 53.34 x 68.58 x 1.6 mm, 170 faces (baked)
FEATURE [Part::Feature] Part__Feature867  label="LED_0603_018"
  Placement = pos=(-14.13,-25.59,81.7) rot=(0,0,1;1.5708rad)
  shape: bbox 0.725 x 1.65 x 0.675 mm, 50 faces (baked)
FEATURE [Part::Feature] Part__Feature868  label="LED_0603_019"
  Placement = pos=(-18.63,-25.57,81.7) rot=(0,0,1;1.5708rad)
  shape: bbox 0.725 x 1.65 x 0.675 mm, 50 faces (baked)
FEATURE [Part::Feature] Part__Feature869  label="1x10-socket-header_002"
  Placement = pos=(-24.13,13.166,81.7) rot=(0,0,1;1.5708rad)
  shape: bbox 2.54 x 25.4 x 11.85 mm, 186 faces (baked)
FEATURE [Part::Feature] Part__Feature870  label="1x6-male-pin-header-gray_004"
  Placement = pos=(14.605,18.5,81.7) rot=(0,0,-1;1.5708rad)
  shape: bbox 2.54 x 15.24 x 11.2 mm, 210 faces (baked)
FEATURE [Part::Feature] Part__Feature871  label="1x8-socket-header_004"
  Placement = pos=(-24.13,35.01,81.7) rot=(0,0,1;1.5708rad)
  shape: bbox 2.54 x 20.32 x 11.85 mm, 150 faces (baked)
FEATURE [Part::Feature] Part__Feature872  label="1x8-male-pin-header_002"
  Placement = pos=(-19.685,35.01,81.7) rot=(0,0,1;1.5708rad)
  shape: bbox 2.54 x 20.32 x 11.2 mm, 278 faces (baked)
FEATURE [Part::Feature] Part__Feature873  label="1x6-male-pin-header-red_004"
  Placement = pos=(17.145,18.5,81.7) rot=(0,0,-1;1.5708rad)
  shape: bbox 2.54 x 15.24 x 11.2 mm, 210 faces (baked)
FEATURE [Part::Feature] Part__Feature874  label="1x8-male-pin-header-red_002"
  Placement = pos=(-17.145,35.01,81.7) rot=(0,0,1;1.5708rad)
  shape: bbox 2.54 x 20.32 x 11.2 mm, 278 faces (baked)
FEATURE [Part::Feature] Part__Feature875  label="1x4-male-pin-header-red004_002"
  Placement = pos=(2.0574,35.7085,81.7) rot=(0,0,1;3.14159rad)
  shape: bbox 10.16 x 2.54 x 11.2 mm, 142 faces (baked)
FEATURE [Part::Feature] Part__Feature876  label="1x8-male-pin-header-gray_002"
  Placement = pos=(-14.605,35.01,81.7) rot=(0,0,1;1.5708rad)
  shape: bbox 2.54 x 20.32 x 11.2 mm, 278 faces (baked)
FEATURE [Part::Feature] Part__Feature877  label="1x8-socket-header_005"
  Placement = pos=(24.13,-0.55,81.7) rot=(0,0,-1;1.5708rad)
  shape: bbox 2.54 x 20.32 x 11.85 mm, 150 faces (baked)
FEATURE [Part::Feature] Part__Feature878  label="1x6-socket-header_002"
  Placement = pos=(24.13,22.31,81.7) rot=(0,0,-1;1.5708rad)
  shape: bbox 2.54 x 15.24 x 11.85 mm, 114 faces (baked)
FEATURE [Part::Feature] Part__Feature879  label="SOT23-3_006"
  Placement = pos=(4.57,-18.48,81.7) rot=(0,0,1;3.14159rad)
  shape: bbox 2.76 x 2.9 x 1.1 mm, 49 faces (baked)
FEATURE [Part::Feature] Part__Feature880  label="1x4-male-pin-header_002"
  Placement = pos=(2.0574,38.2485,81.7) rot=(0,0,1;3.14159rad)
  shape: bbox 10.16 x 2.54 x 11.2 mm, 142 faces (baked)
FEATURE [Part::Feature] Part__Feature881  label="SOT-563_002"
  Placement = pos=(-2.4384,-20.9208,81.7) rot=(0,0,-1;1.5708rad)
  shape: bbox 1.6 x 1.6 x 0.55 mm, 48 faces (baked)
FEATURE [Part::Feature] Part__Feature882  label="1x4-male-pin-header-cyan_002"
  Placement = pos=(2.0574,33.1685,81.7) rot=(0,0,1;3.14159rad)
  shape: bbox 10.16 x 2.54 x 11.2 mm, 142 faces (baked)
FEATURE [Part::Feature] Part__Feature883  label="2x4-pin-header-yello_002"
  Placement = pos=(8.8392,-12.7039,81.7) rot=(0,0,1;1.5708rad)
  shape: bbox 5.08 x 10.16 x 11.2 mm, 271 faces (baked)
FEATURE [Part::Feature] Part__Feature884  label="USB-micro-B_002"
  Placement = pos=(-2.25,-26.52,81.7) rot=(0,0,1;1.5708rad)
  shape: bbox 7.977 x 5.438 x 2.937 mm, 448 faces (baked)
FEATURE [Part::Feature] Part__Feature885  label="slide-sw-right-angle_002"
  Placement = pos=(21.463,-7.3953,81.7) rot=(0,0,1;1.5708rad)
  shape: bbox 7.561 x 10 x 5.5 mm, 95 faces (baked)
FEATURE [Part::Feature] Part__Feature886  label="SOT23-3_007"
  Placement = pos=(8.18,-25.79,81.7) rot=(0,0,1;1.5708rad)
  shape: bbox 2.9 x 2.76 x 1.1 mm, 49 faces (baked)
FEATURE [Part::Feature] Part__Feature887  label="LED_0603_020"
  Placement = pos=(-15.63,-25.59,81.7) rot=(0,0,1;1.5708rad)
  shape: bbox 0.725 x 1.65 x 0.675 mm, 50 faces (baked)
FEATURE [Part::Feature] Part__Feature888  label="R_Array_4x0603_004"
  Placement = pos=(-16.4211,-21.5304,81.7) rot=(0,0,-1;1.5708rad)
  shape: bbox 3.498 x 1.62 x 0.5525 mm, 95 faces (baked)
FEATURE [Part::Feature] Part__Feature889  label="LED_0603_021"
  Placement = pos=(-23.13,-25.59,81.7) rot=(0,0,1;1.5708rad)
  shape: bbox 0.725 x 1.65 x 0.675 mm, 50 faces (baked)
FEATURE [Part::Feature] Part__Feature890  label="sw_smd_6.0x3.8_004"
  Placement = pos=(-17.53,-11.39,81.7) rot=(0,0,1;1.5708rad)
  shape: bbox 7.3 x 3.899 x 2.5 mm, 90 faces (baked)
FEATURE [Part::Feature] Part__Feature891  label="1x6-pin-header_004"
  Placement = pos=(-19.685,13.166,81.7) rot=(0,0,1;1.5708rad)
  shape: bbox 2.54 x 15.24 x 11.2 mm, 210 faces (baked)
FEATURE [Part::Feature] Part__Feature892  label="PVQFN20_004"
  Placement = pos=(9.5631,27.5043,81.7) rot=(0,0,-1;1.5708rad)
  shape: bbox 3.52 x 4.52 x 0.9 mm, 133 faces (baked)
FEATURE [Part::Feature] Part__Feature893  label="1x6-pin-header_005"
  Placement = pos=(19.685,18.5,81.7) rot=(0,0,-1;1.5708rad)
  shape: bbox 2.54 x 15.24 x 11.2 mm, 210 faces (baked)
FEATURE [Part::Feature] Part__Feature894  label="LED_0603_022"
  Placement = pos=(-24.63,-25.59,81.7) rot=(0,0,1;1.5708rad)
  shape: bbox 0.725 x 1.65 x 0.675 mm, 50 faces (baked)
FEATURE [Part::Feature] Part__Feature895  label="1x6-male-pin-header-red_005"
  Placement = pos=(-17.145,13.166,81.7) rot=(0,0,1;1.5708rad)
  shape: bbox 2.54 x 15.24 x 11.2 mm, 210 faces (baked)
FEATURE [Part::Feature] Part__Feature896  label="LED_0603_023"
  Placement = pos=(-21.63,-25.59,81.7) rot=(0,0,1;1.5708rad)
  shape: bbox 0.725 x 1.65 x 0.675 mm, 50 faces (baked)
FEATURE [Part::Feature] Part__Feature897  label="1x6-male-pin-header-gray_005"
  Placement = pos=(-14.605,13.166,81.7) rot=(0,0,1;1.5708rad)
  shape: bbox 2.54 x 15.24 x 11.2 mm, 210 faces (baked)
FEATURE [Part::Feature] Part__Feature898  label="LED_0603_024"
  Placement = pos=(-17.13,-25.59,81.7) rot=(0,0,1;1.5708rad)
  shape: bbox 0.725 x 1.65 x 0.675 mm, 50 faces (baked)
FEATURE [Part::Feature] Part__Feature899  label="LED_0603_025"
  Placement = pos=(-20.13,-25.59,81.7) rot=(0,0,1;1.5708rad)
  shape: bbox 0.725 x 1.65 x 0.675 mm, 50 faces (baked)
FEATURE [Part::Feature] Part__Feature900  label="R_Array_4x0603_005"
  Placement = pos=(-21.9964,-21.5304,81.7) rot=(0,0,-1;1.5708rad)
  shape: bbox 3.498 x 1.62 x 0.5525 mm, 95 faces (baked)
FEATURE [Part::Feature] Part__Feature901  label="LED_0603_026"
  Placement = pos=(19.939,-1.9978,81.7) rot=(0,0,1;1.5708rad)
  shape: bbox 0.725 x 1.65 x 0.675 mm, 50 faces (baked)
FEATURE [Part::Feature] Part__Feature902  label="sw_smd_6.0x3.8_005"
  Placement = pos=(-17.53,-16.79,81.7) rot=(0,0,1;1.5708rad)
  shape: bbox 7.3 x 3.899 x 2.5 mm, 90 faces (baked)
FEATURE [Part::Feature] Part__Feature903  label="PVQFN20_005"
  Placement = pos=(-8.7122,28.0758,81.7) rot=(0,0,1;1.5708rad)
  shape: bbox 3.52 x 4.52 x 0.9 mm, 133 faces (baked)
FEATURE [Part::Feature] Part__Feature904  label="SOT23-3_008"
  Placement = pos=(4.56,-25.79,81.7) rot=(0,0,1;1.5708rad)
  shape: bbox 2.9 x 2.76 x 1.1 mm, 49 faces (baked)
FEATURE [Part::Feature] Part__Feature905  label="C_0402_107"
  Placement = pos=(-6.4262,-1.5533,81.7) rot=(0,0,1;3.14159rad)
  shape: bbox 0.985 x 0.5 x 0.5 mm, 44 faces (baked)
FEATURE [Part::Feature] Part__Feature906  label="MSOP-8_002"
  Placement = pos=(-9.7917,-12.0562,81.7) rot=(0,0,1;1.5708rad)
  shape: bbox 3.2 x 5.141 x 1 mm, 115 faces (baked)
FEATURE [Part::Feature] Part__Feature907  label="xtal-3_2x2_5_002"
  Placement = pos=(-8.8265,-18.7491,81.7) rot=(0,0,1;1.5708rad)
  shape: bbox 3.2 x 2.5 x 0.92 mm, 29 faces (baked)
FEATURE [Part::Feature] Part__Feature908  label="F1812-505k_002"
  Placement = pos=(-11.09,-24.72,81.7) rot=(0,0,-1;1.5708rad)
  shape: bbox 3.41 x 4.73 x 1.39 mm, 94 faces (baked)
FEATURE [Part::Feature] Part__Feature909  label="jack_DC_2.1mm_PCB_002"
  Placement = pos=(18.3134,-23.0798,81.7) rot=(0,0,1;0rad)
  shape: bbox 9.46 x 14.5 x 14.8 mm, 34 faces (baked)
FEATURE [Part::Feature] Part__Feature910  label="DO-214AC_002"
  Placement = pos=(11.7602,-24.2228,81.7) rot=(0,0,-1;1.5708rad)
  shape: bbox 2.8 x 5.475 x 2.574 mm, 39 faces (baked)
FEATURE [Part::Feature] Part__Feature911  label="SOD-323_004"
  Placement = pos=(3.1496,-21.6574,81.7) rot=(0,0,1;1.5708rad)
  shape: bbox 1.35 x 2.6 x 1.113 mm, 38 faces (baked)
FEATURE [Part::Feature] Part__Feature912  label="DFN-2523-6_006"
  Placement = pos=(11.7348,-14.3168,81.7) rot=(0,0,1;0rad)
  shape: bbox 2.5 x 2.4 x 0.62 mm, 44 faces (baked)
FEATURE [Part::Feature] Part__Feature913  label="DFN-2523-6_007"
  Placement = pos=(11.7729,-18.6602,81.7) rot=(0,0,1;3.14159rad)
  shape: bbox 2.5 x 2.4 x 0.62 mm, 44 faces (baked)
FEATURE [Part::Feature] Part__Feature914  label="C_0402_108"
  Placement = pos=(-16.8275,-7.3953,81.7) rot=(0,0,1;0rad)
  shape: bbox 0.985 x 0.5 x 0.5 mm, 44 faces (baked)
FEATURE [Part::Feature] Part__Feature915  label="DFN-2523-6_008"
  Placement = pos=(20.066,5.9016,81.7) rot=(0,0,1;0rad)
  shape: bbox 2.5 x 2.4 x 0.62 mm, 44 faces (baked)
FEATURE [Part::Feature] Part__Feature916  label="PVQFN16_002"
  Placement = pos=(-15.82,-3.72,81.7) rot=(0,0,1;1.5708rad)
  shape: bbox 3.7 x 4.17 x 1.1 mm, 109 faces (baked)
FEATURE [Part::Feature] Part__Feature917  label="C_0402_109"
  Placement = pos=(8.7757,31.1111,81.7) rot=(0,0,1;3.14159rad)
  shape: bbox 0.985 x 0.5 x 0.5 mm, 44 faces (baked)
FEATURE [Part::Feature] Part__Feature918  label="L_4040_002"
  Placement = pos=(15.0495,-2.2391,81.7) rot=(0,0,1;0rad)
  shape: bbox 4.3 x 4.3 x 2.33 mm, 122 faces (baked)
FEATURE [Part::Feature] Part__Feature919  label="QFN16_004"
  Placement = pos=(0.4826,27.7837,81.7) rot=(0,0,1;1.5708rad)
  shape: bbox 3.08 x 3.08 x 0.9 mm, 118 faces (baked)
FEATURE [Part::Feature] Part__Feature920  label="QFN16_005"
  Placement = pos=(14.6431,-7.0778,81.7) rot=(0,0,-1;1.5708rad)
  shape: bbox 3.08 x 3.08 x 0.9 mm, 118 faces (baked)
FEATURE [Part::Feature] Part__Feature921  label="FTDI-QFN-64_002"
  Placement = pos=(-1.4732,-11.9419,81.7) rot=(0,0,1;1.5708rad)
  shape: bbox 9.04 x 9.04 x 0.95 mm, 849 faces (baked)
FEATURE [Part::Feature] Part__Feature922  label="C_0402_110"
  Placement = pos=(-20.3327,-4.6902,81.7) rot=(0,0,1;3.14159rad)
  shape: bbox 0.985 x 0.5 x 0.5 mm, 44 faces (baked)
FEATURE [Part::Feature] Part__Feature923  label="C_0402_111"
  Placement = pos=(0.2667,-18.1903,81.7) rot=(0,0,-1;1.5708rad)
  shape: bbox 0.5 x 0.985 x 0.5 mm, 44 faces (baked)
FEATURE [Part::Feature] Part__Feature924  label="C_0402_112"
  Placement = pos=(-9.8298,24.6087,81.7) rot=(0,0,1;0rad)
  shape: bbox 0.985 x 0.5 x 0.5 mm, 44 faces (baked)
FEATURE [Part::Feature] Part__Feature925  label="C_1206_004"
  Placement = pos=(19.0373,-6.8238,81.7) rot=(0,0,-1;1.5708rad)
  shape: bbox 1.6 x 3.2 x 1 mm, 44 faces (baked)
FEATURE [Part::Feature] Part__Feature926  label="C_0402_113"
  Placement = pos=(17.399,-5.7062,81.7) rot=(0,0,-1;1.5708rad)
  shape: bbox 0.5 x 0.985 x 0.5 mm, 44 faces (baked)
FEATURE [Part::Feature] Part__Feature927  label="C_0402_114"
  Placement = pos=(-20.3327,-1.6803,81.7) rot=(0,0,1;3.14159rad)
  shape: bbox 0.985 x 0.5 x 0.5 mm, 44 faces (baked)
FEATURE [Part::Feature] Part__Feature928  label="C_0402_115"
  Placement = pos=(4.2799,-1.9978,81.7) rot=(0,0,-1;1.5708rad)
  shape: bbox 0.5 x 0.985 x 0.5 mm, 44 faces (baked)
FEATURE [Part::Feature] Part__Feature929  label="C_0603_028"
  Placement = pos=(11.3665,-8.1954,81.7) rot=(0,0,1;1.5708rad)
  shape: bbox 0.8 x 1.6 x 0.6 mm, 44 faces (baked)
FEATURE [Part::Feature] Part__Feature930  label="C_0402_116"
  Placement = pos=(-16.8275,-8.3859,81.7) rot=(0,0,1;3.14159rad)
  shape: bbox 0.985 x 0.5 x 0.5 mm, 44 faces (baked)
FEATURE [Part::Feature] Part__Feature931  label="C_0402_117"
  Placement = pos=(-20.33,-3.69,81.7) rot=(0,0,1;3.14159rad)
  shape: bbox 0.985 x 0.5 x 0.5 mm, 44 faces (baked)
FEATURE [Part::Feature] Part__Feature932  label="DFN-3030-8_002"
  Placement = pos=(13.8938,2.3202,81.7) rot=(0,0,-1;1.5708rad)
  shape: bbox 3 x 3.02 x 0.85 mm, 89 faces (baked)
FEATURE [Part::Feature] Part__Feature933  label="C_0603_029"
  Placement = pos=(11.6713,-5.3887,81.7) rot=(0,0,1;1.5708rad)
  shape: bbox 0.8 x 1.6 x 0.6 mm, 44 faces (baked)
FEATURE [Part::Feature] Part__Feature934  label="C_0402_118"
  Placement = pos=(-0.635,-18.1903,81.7) rot=(0,0,1;1.5708rad)
  shape: bbox 0.5 x 0.985 x 0.5 mm, 44 faces (baked)
FEATURE [Part::Feature] Part__Feature935  label="C_0402_119"
  Placement = pos=(12.4841,12.6707,81.7) rot=(0,0,1;1.5708rad)
  shape: bbox 0.5 x 0.985 x 0.5 mm, 44 faces (baked)
FEATURE [Part::Feature] Part__Feature936  label="C_0402_120"
  Placement = pos=(12.4714,8.7083,81.7) rot=(0,0,-1;1.5708rad)
  shape: bbox 0.5 x 0.985 x 0.5 mm, 44 faces (baked)
FEATURE [Part::Feature] Part__Feature937  label="C_0402_121"
  Placement = pos=(4.2418,-14.647,81.7) rot=(0,0,-1;1.5708rad)
  shape: bbox 0.5 x 0.985 x 0.5 mm, 44 faces (baked)
FEATURE [Part::Feature] Part__Feature938  label="C_0402_122"
  Placement = pos=(-7.1755,-12.1451,81.7) rot=(0,0,-1;1.5708rad)
  shape: bbox 0.5 x 0.985 x 0.5 mm, 44 faces (baked)
FEATURE [Part::Feature] Part__Feature939  label="C_0402_123"
  Placement = pos=(1.4732,23.199,81.7) rot=(0,0,1;0rad)
  shape: bbox 0.985 x 0.5 x 0.5 mm, 44 faces (baked)
FEATURE [Part::Feature] Part__Feature940  label="C_0603_030"
  Placement = pos=(8.3693,-2.4931,81.7) rot=(0,0,1;3.14159rad)
  shape: bbox 1.6 x 0.8 x 0.6 mm, 44 faces (baked)
FEATURE [Part::Feature] Part__Feature941  label="C_0402_124"
  Placement = pos=(-12.3317,28.7108,81.7) rot=(0,0,1;1.5708rad)
  shape: bbox 0.5 x 0.985 x 0.5 mm, 44 faces (baked)
FEATURE [Part::Feature] Part__Feature942  label="C_0603_031"
  Placement = pos=(-5.7404,-18.4062,81.7) rot=(0,0,-1;1.5708rad)
  shape: bbox 0.8 x 1.6 x 0.6 mm, 44 faces (baked)
FEATURE [Part::Feature] Part__Feature943  label="pushbutton-right-angle_002"
  Placement = pos=(9.779,37.169,81.7) rot=(0,0,1;3.14159rad)
  shape: bbox 7.4 x 7.9 x 11 mm, 130 faces (baked)
FEATURE [Part::Feature] Part__Feature944  label="C_0402_125"
  Placement = pos=(-14.1351,-7.3953,81.7) rot=(0,0,1;0rad)
  shape: bbox 0.985 x 0.5 x 0.5 mm, 44 faces (baked)
FEATURE [Part::Feature] Part__Feature945  label="C_0402_126"
  Placement = pos=(4.2672,-7.8271,81.7) rot=(0,0,1;1.5708rad)
  shape: bbox 0.5 x 0.985 x 0.5 mm, 44 faces (baked)
FEATURE [Part::Feature] Part__Feature946  label="C_0402_127"
  Placement = pos=(-7.62,24.6087,81.7) rot=(0,0,1;0rad)
  shape: bbox 0.985 x 0.5 x 0.5 mm, 44 faces (baked)
FEATURE [Part::Feature] Part__Feature947  label="WSON-6_002"
  Placement = pos=(17.272,3.2854,81.7) rot=(0,0,1;1.5708rad)
  shape: bbox 1.55 x 1.6 x 0.85 mm, 44 faces (baked)
FEATURE [Part::Feature] Part__Feature948  label="C_0402_128"
  Placement = pos=(10.7696,21.8782,81.7) rot=(0,0,1;0rad)
  shape: bbox 0.985 x 0.5 x 0.5 mm, 44 faces (baked)
FEATURE [Part::Feature] Part__Feature949  label="TQFP-144_002"
  Placement = pos=(0,10.9308,81.7) rot=(0,0,1;1.5708rad)
  shape: bbox 21.98 x 21.98 x 1.12 mm, 2168 faces (baked)
FEATURE [Part::Feature] Part__Feature950  label="C_0603_032"
  Placement = pos=(17.0942,5.1142,81.7) rot=(0,0,1;0rad)
  shape: bbox 1.6 x 0.8 x 0.6 mm, 44 faces (baked)
FEATURE [Part::Feature] Part__Feature951  label="C_0402_129"
  Placement = pos=(-9.9314,-15.8916,81.7) rot=(0,0,1;3.14159rad)
  shape: bbox 0.985 x 0.5 x 0.5 mm, 44 faces (baked)
FEATURE [Part::Feature] Part__Feature952  label="C_0603_033"
  Placement = pos=(15.0622,-13.1992,81.7) rot=(0,0,1;0rad)
  shape: bbox 1.6 x 0.8 x 0.6 mm, 44 faces (baked)
FEATURE [Part::Feature] Part__Feature953  label="C_0402_130"
  Placement = pos=(-12.319,31.2,81.7) rot=(0,0,-1;1.5708rad)
  shape: bbox 0.5 x 0.985 x 0.5 mm, 44 faces (baked)
FEATURE [Part::Feature] Part__Feature954  label="C_0402_131"
  Placement = pos=(-12.3317,33.7146,81.7) rot=(0,0,1;1.5708rad)
  shape: bbox 0.5 x 0.985 x 0.5 mm, 44 faces (baked)
FEATURE [Part::Feature] Part__Feature955  label="C_0402_132"
  Placement = pos=(-20.3327,-6.6968,81.7) rot=(0,0,1;3.14159rad)
  shape: bbox 0.985 x 0.5 x 0.5 mm, 44 faces (baked)
FEATURE [Part::Feature] Part__Feature956  label="L_0603_006"
  Placement = pos=(-6.0325,-22.4956,81.7) rot=(0,0,1;3.14159rad)
  shape: bbox 1.6 x 0.8 x 0.6 mm, 44 faces (baked)
FEATURE [Part::Feature] Part__Feature957  label="C_0402_133"
  Placement = pos=(-7.1374,-8.9066,81.7) rot=(0,0,-1;1.5708rad)
  shape: bbox 0.5 x 0.985 x 0.5 mm, 44 faces (baked)
FEATURE [Part::Feature] Part__Feature958  label="C_0603_034"
  Placement = pos=(-8.2042,-24.9467,81.7) rot=(0,0,1;1.5708rad)
  shape: bbox 0.8 x 1.6 x 0.6 mm, 44 faces (baked)
FEATURE [Part::Feature] Part__Feature959  label="C_0402_134"
  Placement = pos=(-5.4229,23.199,81.7) rot=(0,0,1;3.14159rad)
  shape: bbox 0.985 x 0.5 x 0.5 mm, 44 faces (baked)
FEATURE [Part::Feature] Part__Feature960  label="R_0402_075"
  Placement = pos=(-3.6322,-18.203,81.7) rot=(0,0,1;1.5708rad)
  shape: bbox 0.5 x 1 x 0.3 mm, 40 faces (baked)
FEATURE [Part::Feature] Part__Feature961  label="C_0402_135"
  Placement = pos=(-2.2352,-5.7951,81.7) rot=(0,0,1;1.5708rad)
  shape: bbox 0.5 x 0.985 x 0.5 mm, 44 faces (baked)
FEATURE [Part::Feature] Part__Feature962  label="C_0402_136"
  Placement = pos=(-20.3327,-2.6963,81.7) rot=(0,0,1;3.14159rad)
  shape: bbox 0.985 x 0.5 x 0.5 mm, 44 faces (baked)
FEATURE [Part::Feature] Part__Feature963  label="C_0603_035"
  Placement = pos=(-3.429,31.0095,81.7) rot=(0,0,1;3.14159rad)
  shape: bbox 1.6 x 0.8 x 0.6 mm, 44 faces (baked)
FEATURE [Part::Feature] Part__Feature964  label="C_1206_005"
  Placement = pos=(16.51,-11.1037,81.7) rot=(0,0,1;0rad)
  shape: bbox 3.2 x 1.6 x 1 mm, 44 faces (baked)
FEATURE [Part::Feature] Part__Feature965  label="C_0603_036"
  Placement = pos=(-0.3429,-20.7684,81.7) rot=(0,0,-1;1.5708rad)
  shape: bbox 0.8 x 1.6 x 0.6 mm, 44 faces (baked)
FEATURE [Part::Feature] Part__Feature966  label="C_0402_137"
  Placement = pos=(-7.2898,-15.79,81.7) rot=(0,0,-1;1.5708rad)
  shape: bbox 0.5 x 0.985 x 0.5 mm, 44 faces (baked)
FEATURE [Part::Feature] Part__Feature967  label="C_0603_037"
  Placement = pos=(9.271,-22.3432,81.7) rot=(0,0,1;1.5708rad)
  shape: bbox 0.8 x 1.6 x 0.6 mm, 44 faces (baked)
FEATURE [Part::Feature] Part__Feature968  label="C_0402_138"
  Placement = pos=(-14.13,-8.39,81.7) rot=(0,0,1;0rad)
  shape: bbox 0.985 x 0.5 x 0.5 mm, 44 faces (baked)
FEATURE [Part::Feature] Part__Feature969  label="SOD-323_005"
  Placement = pos=(-8.1,23.32,81.7) rot=(0,0,1;0rad)
  shape: bbox 2.6 x 1.35 x 1.113 mm, 38 faces (baked)
FEATURE [Part::Feature] Part__Feature970  label="DFN-8-6x5mm_002"
  Placement = pos=(16.1,12.61,81.7) rot=(0,0,-1;1.5708rad)
  shape: bbox 5 x 6.1 x 0.9466 mm, 62 faces (baked)
FEATURE [Part::Feature] Part__Feature971  label="C_0402_139"
  Placement = pos=(0.8636,-6.1888,81.7) rot=(0,0,1;0rad)
  shape: bbox 0.985 x 0.5 x 0.5 mm, 44 faces (baked)
FEATURE [Part::Feature] Part__Feature972  label="L_0603_007"
  Placement = pos=(-5.1054,-20.5144,81.7) rot=(0,0,1;3.14159rad)
  shape: bbox 1.6 x 0.8 x 0.6 mm, 44 faces (baked)
FEATURE [Part::Feature] Part__Feature973  label="C_0402_140"
  Placement = pos=(-1.524,23.2117,81.7) rot=(0,0,1;3.14159rad)
  shape: bbox 0.985 x 0.5 x 0.5 mm, 44 faces (baked)
FEATURE [Part::Feature] Part__Feature974  label="C_0603_038"
  Placement = pos=(7.4168,-15.9932,81.7) rot=(0,0,1;0rad)
  shape: bbox 1.6 x 0.8 x 0.6 mm, 44 faces (baked)
FEATURE [Part::Feature] Part__Feature975  label="C_0603_039"
  Placement = pos=(13.3477,4.9999,81.7) rot=(0,0,1;3.14159rad)
  shape: bbox 1.6 x 0.8 x 0.6 mm, 44 faces (baked)
FEATURE [Part::Feature] Part__Feature976  label="C_0402_141"
  Placement = pos=(-12.3317,26.1073,81.7) rot=(0,0,-1;1.5708rad)
  shape: bbox 0.5 x 0.985 x 0.5 mm, 44 faces (baked)
FEATURE [Part::Feature] Part__Feature977  label="C_0402_142"
  Placement = pos=(5.7658,-1.9978,81.7) rot=(0,0,-1;1.5708rad)
  shape: bbox 0.5 x 0.985 x 0.5 mm, 44 faces (baked)
FEATURE [Part::Feature] Part__Feature978  label="C_0402_143"
  Placement = pos=(8.5725,-1.3882,81.7) rot=(0,0,1;3.14159rad)
  shape: bbox 0.985 x 0.5 x 0.5 mm, 44 faces (baked)
FEATURE [Part::Feature] Part__Feature979  label="L_0603_008"
  Placement = pos=(13.0683,-11.091,81.7) rot=(0,0,1;1.5708rad)
  shape: bbox 0.8 x 1.6 x 0.6 mm, 44 faces (baked)
FEATURE [Part::Feature] Part__Feature980  label="C_0603_040"
  Placement = pos=(-5.3721,-6.265,81.7) rot=(0,0,1;0rad)
  shape: bbox 1.6 x 0.8 x 0.6 mm, 44 faces (baked)
FEATURE [Part::Feature] Part__Feature981  label="C_0402_144"
  Placement = pos=(10.668,31.1111,81.7) rot=(0,0,1;3.14159rad)
  shape: bbox 0.985 x 0.5 x 0.5 mm, 44 faces (baked)
FEATURE [Part::Feature] Part__Feature982  label="L_0805_002"
  Placement = pos=(1.1176,-21.3272,81.7) rot=(0,0,1;1.5708rad)
  shape: bbox 1.25 x 2 x 1.25 mm, 50 faces (baked)
FEATURE [Part::Feature] Part__Feature983  label="C_0402_145"
  Placement = pos=(-20.3327,-5.6935,81.7) rot=(0,0,1;3.14159rad)
  shape: bbox 0.985 x 0.5 x 0.5 mm, 44 faces (baked)
FEATURE [Part::Feature] Part__Feature984  label="C_0402_146"
  Placement = pos=(-4.6228,-18.203,81.7) rot=(0,0,-1;1.5708rad)
  shape: bbox 0.5 x 0.985 x 0.5 mm, 44 faces (baked)
FEATURE [Part::Feature] Part__Feature985  label="R_0402_076"
  Placement = pos=(-10.5283,-8.1954,81.7) rot=(0,0,1;3.14159rad)
  shape: bbox 1 x 0.5 x 0.3 mm, 40 faces (baked)
FEATURE [Part::Feature] Part__Feature986  label="C_0402_147"
  Placement = pos=(-12.3317,36.3054,81.7) rot=(0,0,-1;1.5708rad)
  shape: bbox 0.5 x 0.985 x 0.5 mm, 44 faces (baked)
FEATURE [Part::Feature] Part__Feature987  label="C_0402_148"
  Placement = pos=(-11.3665,-18.2919,81.7) rot=(0,0,-1;1.5708rad)
  shape: bbox 0.5 x 0.985 x 0.5 mm, 44 faces (baked)
FEATURE [Part::Feature] Part__Feature988  label="C_0402_149"
  Placement = pos=(17.4625,7.9082,81.7) rot=(0,0,1;3.14159rad)
  shape: bbox 0.985 x 0.5 x 0.5 mm, 44 faces (baked)
FEATURE [Part::Feature] Part__Feature989  label="C_0402_150"
  Placement = pos=(12.8651,6.7652,81.7) rot=(0,0,1;0rad)
  shape: bbox 0.985 x 0.5 x 0.5 mm, 44 faces (baked)
FEATURE [Part::Feature] Part__Feature990  label="C_0402_151"
  Placement = pos=(-2.3368,28.5076,81.7) rot=(0,0,-1;1.5708rad)
  shape: bbox 0.5 x 0.985 x 0.5 mm, 44 faces (baked)
FEATURE [Part::Feature] Part__Feature991  label="C_0402_152"
  Placement = pos=(-2.3368,26.6153,81.7) rot=(0,0,-1;1.5708rad)
  shape: bbox 0.5 x 0.985 x 0.5 mm, 44 faces (baked)
FEATURE [Part::Feature] Part__Feature992  label="C_0603_041"
  Placement = pos=(17.0942,6.3207,81.7) rot=(0,0,1;0rad)
  shape: bbox 1.6 x 0.8 x 0.6 mm, 44 faces (baked)
FEATURE [Part::Feature] Part__Feature993  label="C_0402_153"
  Placement = pos=(-12.3317,23.6054,81.7) rot=(0,0,1;1.5708rad)
  shape: bbox 0.5 x 0.985 x 0.5 mm, 44 faces (baked)
FEATURE [Part::Feature] Part__Feature994  label="C_0402_154"
  Placement = pos=(-12.3317,21.0019,81.7) rot=(0,0,1;1.5708rad)
  shape: bbox 0.5 x 0.985 x 0.5 mm, 44 faces (baked)
FEATURE [Part::Feature] Part__Feature995  label="C_0402_155"
  Placement = pos=(-12.3317,18.4111,81.7) rot=(0,0,-1;1.5708rad)
  shape: bbox 0.5 x 0.985 x 0.5 mm, 44 faces (baked)
FEATURE [Part::Feature] Part__Feature996  label="C_0402_156"
  Placement = pos=(-12.3317,12.0738,81.7) rot=(0,0,-1;1.5708rad)
  shape: bbox 0.5 x 0.985 x 0.5 mm, 44 faces (baked)
FEATURE [Part::Feature] Part__Feature997  label="C_0402_157"
  Placement = pos=(-12.3317,15.706,81.7) rot=(0,0,-1;1.5708rad)
  shape: bbox 0.5 x 0.985 x 0.5 mm, 44 faces (baked)
FEATURE [Part::Feature] Part__Feature998  label="C_0402_158"
  Placement = pos=(-12.4333,7.0319,81.7) rot=(0,0,1;1.5708rad)
  shape: bbox 0.5 x 0.985 x 0.5 mm, 44 faces (baked)
FEATURE [Part::Feature] Part__Feature999  label="R_0402_077"
  Placement = pos=(-10.5283,-6.1888,81.7) rot=(0,0,1;0rad)
  shape: bbox 1 x 0.5 x 0.3 mm, 40 faces (baked)
FEATURE [Part::Feature] Part__Feature1000  label="R_0402_078"
  Placement = pos=(-10.5283,-7.1921,81.7) rot=(0,0,1;0rad)
  shape: bbox 1 x 0.5 x 0.3 mm, 40 faces (baked)
FEATURE [Part::Feature] Part__Feature1001  label="R_0402_079"
  Placement = pos=(1.67,-18.19,81.7) rot=(0,0,1;1.5708rad)
  shape: bbox 0.5 x 1 x 0.3 mm, 40 faces (baked)
FEATURE [Part::Feature] Part__Feature1002  label="R_0402_080"
  Placement = pos=(4.9657,-20.7938,81.7) rot=(0,0,1;3.14159rad)
  shape: bbox 1 x 0.5 x 0.3 mm, 40 faces (baked)
FEATURE [Part::Feature] Part__Feature1003  label="R_0402_081"
  Placement = pos=(4.4704,-22.4956,81.7) rot=(0,0,-1;1.5708rad)
  shape: bbox 0.5 x 1 x 0.3 mm, 40 faces (baked)
FEATURE [Part::Feature] Part__Feature1004  label="R_0402_082"
  Placement = pos=(5.461,-22.4956,81.7) rot=(0,0,-1;1.5708rad)
  shape: bbox 0.5 x 1 x 0.3 mm, 40 faces (baked)
FEATURE [Part::Feature] Part__Feature1005  label="R_0402_083"
  Placement = pos=(7.6708,-18.0887,81.7) rot=(0,0,-1;1.5708rad)
  shape: bbox 0.5 x 1 x 0.3 mm, 40 faces (baked)
FEATURE [Part::Feature] Part__Feature1006  label="R_0402_084"
  Placement = pos=(9.271,-20.0953,81.7) rot=(0,0,-1;1.5708rad)
  shape: bbox 0.5 x 1 x 0.3 mm, 40 faces (baked)
FEATURE [Part::Feature] Part__Feature1007  label="R_0402_085"
  Placement = pos=(7.6708,-19.9937,81.7) rot=(0,0,-1;1.5708rad)
  shape: bbox 0.5 x 1 x 0.3 mm, 40 faces (baked)
FEATURE [Part::Feature] Part__Feature1008  label="R_0402_086"
  Placement = pos=(9.271,-18.203,81.7) rot=(0,0,1;1.5708rad)
  shape: bbox 0.5 x 1 x 0.3 mm, 40 faces (baked)
FEATURE [Part::Feature] Part__Feature1009  label="R_0402_087"
  Placement = pos=(21.5773,-1.1977,81.7) rot=(0,0,1;3.14159rad)
  shape: bbox 1 x 0.5 x 0.3 mm, 40 faces (baked)
FEATURE [Part::Feature] Part__Feature1010  label="R_0402_088"
  Placement = pos=(9.271,-16.298,81.7) rot=(0,0,1;1.5708rad)
  shape: bbox 0.5 x 1 x 0.3 mm, 40 faces (baked)
FEATURE [Part::Feature] Part__Feature1011  label="R_0402_089"
  Placement = pos=(10.2743,-1.9978,81.7) rot=(0,0,-1;1.5708rad)
  shape: bbox 0.5 x 1 x 0.3 mm, 40 faces (baked)
FEATURE [Part::Feature] Part__Feature1012  label="R_0402_090"
  Placement = pos=(1.27,-1.9978,81.7) rot=(0,0,1;1.5708rad)
  shape: bbox 0.5 x 1 x 0.3 mm, 40 faces (baked)
FEATURE [Part::Feature] Part__Feature1013  label="R_0402_091"
  Placement = pos=(17.272,1.3042,81.7) rot=(0,0,1;0rad)
  shape: bbox 1 x 0.5 x 0.3 mm, 40 faces (baked)
FEATURE [Part::Feature] Part__Feature1014  label="R_0402_092"
  Placement = pos=(12.4714,15.706,81.7) rot=(0,0,-1;1.5708rad)
  shape: bbox 0.5 x 1 x 0.3 mm, 40 faces (baked)
FEATURE [Part::Feature] Part__Feature1015  label="R_0402_093"
  Placement = pos=(18.9738,1.7106,81.7) rot=(0,0,-1;1.5708rad)
  shape: bbox 0.5 x 1 x 0.3 mm, 40 faces (baked)
FEATURE [Part::Feature] Part__Feature1016  label="R_0402_094"
  Placement = pos=(6.8707,23.707,81.7) rot=(0,0,1;1.5708rad)
  shape: bbox 0.5 x 1 x 0.3 mm, 40 faces (baked)
FEATURE [Part::Feature] Part__Feature1017  label="R_0402_095"
  Placement = pos=(19.9644,1.7106,81.7) rot=(0,0,-1;1.5708rad)
  shape: bbox 0.5 x 1 x 0.3 mm, 40 faces (baked)
FEATURE [Part::Feature] Part__Feature1018  label="R_0402_096"
  Placement = pos=(20.0787,12.2135,81.7) rot=(0,0,1;3.14159rad)
  shape: bbox 1 x 0.5 x 0.3 mm, 40 faces (baked)
FEATURE [Part::Feature] Part__Feature1019  label="R_0402_097"
  Placement = pos=(20.0787,11.2102,81.7) rot=(0,0,1;3.14159rad)
  shape: bbox 1 x 0.5 x 0.3 mm, 40 faces (baked)
FEATURE [Part::Feature] Part__Feature1020  label="R_0402_098"
  Placement = pos=(20.0787,13.2041,81.7) rot=(0,0,1;3.14159rad)
  shape: bbox 1 x 0.5 x 0.3 mm, 40 faces (baked)
FEATURE [Part::Feature] Part__Feature1021  label="R_0402_099"
  Placement = pos=(17.7673,33.2066,81.7) rot=(0,0,1;0rad)
  shape: bbox 1 x 0.5 x 0.3 mm, 40 faces (baked)
FEATURE [Part::Feature] Part__Feature1022  label="R_0402_100"
  Placement = pos=(20.0787,14.2074,81.7) rot=(0,0,1;3.14159rad)
  shape: bbox 1 x 0.5 x 0.3 mm, 40 faces (baked)
FEATURE [Part::Feature] Part__Feature1023  label="R_0402_101"
  Placement = pos=(19.8755,33.2066,81.7) rot=(0,0,1;3.14159rad)
  shape: bbox 1 x 0.5 x 0.3 mm, 40 faces (baked)
FEATURE [Part::Feature] Part__Feature1024  label="R_0402_102"
  Placement = pos=(8.7757,32.3049,81.7) rot=(0,0,1;3.14159rad)
  shape: bbox 1 x 0.5 x 0.3 mm, 40 faces (baked)
FEATURE [Part::Feature] Part__Feature1025  label="R_0402_103"
  Placement = pos=(1.8669,24.9008,81.7) rot=(0,0,1;0rad)
  shape: bbox 1 x 0.5 x 0.3 mm, 40 faces (baked)
FEATURE [Part::Feature] Part__Feature1026  label="R_0402_104"
  Placement = pos=(10.668,32.3049,81.7) rot=(0,0,1;0rad)
  shape: bbox 1 x 0.5 x 0.3 mm, 40 faces (baked)
FEATURE [Part::Feature] Part__Feature1027  label="R_0402_105"
  Placement = pos=(-5.63,31,81.7) rot=(0,0,1;3.14159rad)
  shape: bbox 1 x 0.5 x 0.3 mm, 40 faces (baked)
FEATURE [Part::Feature] Part__Feature1028  label="R_0402_106"
  Placement = pos=(-1.1303,24.9008,81.7) rot=(0,0,1;3.14159rad)
  shape: bbox 1 x 0.5 x 0.3 mm, 40 faces (baked)
FEATURE [Part::Feature] Part__Feature1029  label="R_0402_107"
  Placement = pos=(6.477,-22.4956,81.7) rot=(0,0,1;1.5708rad)
  shape: bbox 0.5 x 1 x 0.3 mm, 40 faces (baked)
FEATURE [Part::Feature] Part__Feature1030  label="R_0402_108"
  Placement = pos=(7.6708,-22.4956,81.7) rot=(0,0,-1;1.5708rad)
  shape: bbox 0.5 x 1 x 0.3 mm, 40 faces (baked)
FEATURE [Part::Feature] Part__Feature1031  label="R_0402_109"
  Placement = pos=(4.2672,-11.7895,81.7) rot=(0,0,-1;1.5708rad)
  shape: bbox 0.5 x 1 x 0.3 mm, 40 faces (baked)
FEATURE [Part::Feature] Part__Feature1032  label="R_0402_110"
  Placement = pos=(4.2672,-9.8972,81.7) rot=(0,0,1;1.5708rad)
  shape: bbox 0.5 x 1 x 0.3 mm, 40 faces (baked)
FEATURE [Part::Feature] Part__Feature1033  label="1x3-pin-header_002"
  Placement = pos=(-7.6581,33.0796,81.7) rot=(0,0,1;0rad)
  shape: bbox 7.62 x 2.54 x 11.2 mm, 108 faces (baked)
FEATURE [Part::Feature] Part__Feature1034  label="jumper-cap-2.54mm_002"
  Placement = pos=(-7.6581,33.0796,81.7) rot=(0,0,1;3.14159rad)
  shape: bbox 5 x 2.5 x 6 mm, 108 faces (baked)
FEATURE [App::DocumentObjectGroup] Grupo040  label="step002"
  Group = -> [Part__Feature866,Part__Feature867,Part__Feature868,Part__Feature869,Part__Feature870,Part__Feature871,Part__Feature872,Part__Feature873,Part__Feature874,Part__Feature875,Part__Feature876,Part__Feature877,Part__Feature878,Part__Feature879,Part__Feature880,Part__Feature881,Part__Feature882,Part__Feature883,Part__Feature884,Part__Feature885,Part__Feature886,Part__Feature887,Part__Feature888,+148 more]
FEATURE [App::DocumentObjectGroup] Grupo039  label="icezum_alhambra002"
  Group = -> [Grupo040]
FEATURE [Part::Feature] Part__Feature1035  label="final-can"
  Placement = pos=(139,209,0) rot=(0,0,1;0rad)
  shape: bbox 66.1 x 66.1 x 115.2 mm, 53 faces (baked)
FEATURE [Sketcher::SketchObject] Sketch035
  MapMode = 5
  Support = -> [XY_Plane010]
  sketch-geometry (24):
    g0: LineSegment StartX=24.9755 StartY=-25.0363 StartZ=0 EndX=-25.0006 EndY=-25.0363 EndZ=0
    g1: LineSegment StartX=-28.0138 StartY=-22.0232 StartZ=0 EndX=-28.0138 EndY=37.9894 EndZ=0
    g2: ArcOfCircle CenterX=25 CenterY=37.9997 CenterZ=0 NormalX=0 NormalY=0 NormalZ=1 AngleXU=0 Radius=3.00034 StartAngle=0.0138849 EndAngle=1.5708
    g3: ArcOfCircle CenterX=-25.0032 CenterY=37.9894 CenterZ=0 NormalX=0 NormalY=0 NormalZ=1 AngleXU=0 Radius=3.0106 StartAngle=1.56995 EndAngle=3.14159
    g4: ArcOfCircle CenterX=-25.0006 CenterY=-22.0232 CenterZ=0 NormalX=0 NormalY=0 NormalZ=1 AngleXU=0 Radius=3.01315 StartAngle=3.14159 EndAngle=4.71239
    g5: ArcOfCircle CenterX=24.9755 CenterY=-22.0118 CenterZ=0 NormalX=0 NormalY=0 NormalZ=1 AngleXU=0 Radius=3.02451 StartAngle=4.71239 EndAngle=6.28319
    g6: LineSegment StartX=7.47627 StartY=39 StartZ=0 EndX=7.47627 EndY=26 EndZ=0
    g7: LineSegment StartX=5.47627 StartY=24 StartZ=0 EndX=-5.51323 EndY=24 EndZ=0
    g8: LineSegment StartX=-7.51323 StartY=26 StartZ=0 EndX=-7.51323 EndY=39 EndZ=0
    g9: LineSegment StartX=-25.0006 StartY=41 StartZ=0 EndX=-9.51323 EndY=41 EndZ=0
    g10: LineSegment StartX=9.47627 StartY=41 StartZ=0 EndX=25 EndY=41 EndZ=0
    g11: ArcOfCircle CenterX=-9.51323 CenterY=39 CenterZ=0 NormalX=0 NormalY=0 NormalZ=1 AngleXU=0 Radius=2 StartAngle=0 EndAngle=1.5708
    g12: ArcOfCircle CenterX=-5.51323 CenterY=26 CenterZ=0 NormalX=0 NormalY=0 NormalZ=1 AngleXU=0 Radius=2 StartAngle=3.14159 EndAngle=4.71239
    g13: ArcOfCircle CenterX=5.47627 CenterY=26 CenterZ=0 NormalX=0 NormalY=0 NormalZ=1 AngleXU=0 Radius=2 StartAngle=4.71239 EndAngle=6.28319
    g14: ArcOfCircle CenterX=9.47627 CenterY=39 CenterZ=0 NormalX=0 NormalY=0 NormalZ=1 AngleXU=0 Radius=2 StartAngle=1.5708 EndAngle=3.14159
    g15: LineSegment StartX=28 StartY=-22.0118 StartZ=0 EndX=28 EndY=-20 EndZ=0
    g16: LineSegment StartX=25 StartY=-17 StartZ=0 EndX=22 EndY=-17 EndZ=0
    g17: LineSegment StartX=21 StartY=-16 StartZ=0 EndX=21 EndY=33 EndZ=0
    g18: ArcOfCircle CenterX=25 CenterY=-20 CenterZ=0 NormalX=0 NormalY=0 NormalZ=1 AngleXU=0 Radius=2.99998 StartAngle=6.28319 EndAngle=7.85398
    g19: ArcOfCircle CenterX=22 CenterY=-16 CenterZ=0 NormalX=0 NormalY=0 NormalZ=1 AngleXU=0 Radius=1 StartAngle=3.14159 EndAngle=4.71239
    g20: LineSegment StartX=28 StartY=38.0413 StartZ=0 EndX=28 EndY=37 EndZ=0
    g21: LineSegment StartX=25 StartY=34 StartZ=0 EndX=22 EndY=34 EndZ=0
    g22: ArcOfCircle CenterX=25 CenterY=37 CenterZ=0 NormalX=0 NormalY=0 NormalZ=1 AngleXU=0 Radius=3 StartAngle=4.71239 EndAngle=6.28319
    g23: ArcOfCircle CenterX=22 CenterY=33 CenterZ=0 NormalX=0 NormalY=0 NormalZ=1 AngleXU=0 Radius=1 StartAngle=1.5708 EndAngle=3.14159
  constraints (42):
    c: Horizontal(g0)
    c: Vertical(g1)
    c: Tangent(g1,g3) = 1.5708
    c: Tangent(g1,g4) = 1.5708
    c: Tangent(g0,g4) = 1.5708
    c: Tangent(g0,g5) = 1.5708
    c: Horizontal(g7)
    c: Vertical(g6)
    c: Vertical(g8)
    c: Coincident(g9,g3)
    c: Horizontal(g9)
    c: Coincident(g10,g2)
    c: Horizontal(g10)
    c: Tangent(g10,g2)
    c: DistanceX(g2) = 25
    c: DistanceY(g2) = 37.9997
    c: Tangent(g9,g11) = 1.5708
    c: Tangent(g8,g11) = -1.5708
    c: Radius(g11) = 2
    c: Tangent(g8,g12) = 1.5708
    c: Tangent(g7,g12) = 1.5708
    c: Tangent(g6,g13) = 1.5708
    c: Tangent(g7,g13) = 1.5708
    c: Radius(g12) = 2
    c: Radius(g13) = 2
    c: Tangent(g6,g14) = -1.5708
    c: Tangent(g10,g14) = 1.5708
    c: Radius(g14) = 2
    c: Tangent(g5,g15) = -1.5708
    c: Horizontal(g16)
    c: Vertical(g17)
    c: Tangent(g15,g18) = -1.5708
    c: Tangent(g16,g18) = -1.5708
    c: Tangent(g16,g19) = 1.5708
    c: Tangent(g17,g19) = 1.5708
    c: Coincident(g20,g2)
    c: Vertical(g20)
    c: Horizontal(g21)
    c: Tangent(g20,g22) = 1.5708
    c: Tangent(g21,g22) = 1.5708
    c: Tangent(g21,g23) = -1.5708
    c: Tangent(g17,g23) = 1.5708
FEATURE [PartDesign::Pad] Pad008
  Length = 2
  Length2 = 100
  Profile = -> Sketch035
  Refine = true
  Reversed = true
  Type = 0
FEATURE [Sketcher::SketchObject] Sketch037  label="columns003"
  MapMode = 5
  Placement = pos=(0,0,-2) rot=(1,0,0;3.14159rad)
  sketch-geometry (4):
    g0: Circle CenterX=-24.441 CenterY=20.4974 CenterZ=0 NormalX=0 NormalY=0 NormalZ=1 AngleXU=0 Radius=3
    g1: Circle CenterX=24.4919 CenterY=20.4964 CenterZ=0 NormalX=0 NormalY=0 NormalZ=1 AngleXU=0 Radius=3
    g2: Circle CenterX=-24.5115 CenterY=-37.516 CenterZ=0 NormalX=0 NormalY=0 NormalZ=1 AngleXU=0 Radius=3
    g3: Circle CenterX=24.5041 CenterY=-37.5051 CenterZ=0 NormalX=0 NormalY=0 NormalZ=1 AngleXU=0 Radius=3
  constraints (4):
    c: Radius(g0) = 3
    c: Equal(g0,g1) = 3
    c: Equal(g0,g2) = 3
    c: Equal(g0,g3) = 3
FEATURE [PartDesign::Pad] Pad009  label="columns002_out"
  BaseFeature = -> Pad008
  Length = 21
  Length2 = 100
  Profile = -> Sketch037
  Refine = true
  Type = 0
FEATURE [Sketcher::SketchObject] Sketch038  label="columns_in"
  MapMode = 5
  Placement = pos=(0,0,-23) rot=(1,0,0;3.14159rad)
  Support = -> [Pad009]
  expr: Constraints[0] = Sketch037.Constraints[5]
  sketch-geometry (4):
    g0: Circle CenterX=-24.441 CenterY=20.4974 CenterZ=0 NormalX=0 NormalY=0 NormalZ=1 AngleXU=0 Radius=1.6
    g1: Circle CenterX=24.4919 CenterY=20.4964 CenterZ=0 NormalX=0 NormalY=0 NormalZ=1 AngleXU=0 Radius=1.6
    g2: Circle CenterX=-24.5115 CenterY=-37.516 CenterZ=0 NormalX=0 NormalY=0 NormalZ=1 AngleXU=0 Radius=1.6
    g3: Circle CenterX=24.5041 CenterY=-37.5051 CenterZ=0 NormalX=0 NormalY=0 NormalZ=1 AngleXU=0 Radius=1.6
  constraints (4):
    c: Radius(g0) = 1.6
    c: Equal(g0,g1) = 1.6
    c: Equal(g0,g2) = 1.6
    c: Equal(g0,g3) = 1.6
FEATURE [PartDesign::Pocket] Pocket003005  label="base_with_columns"
  BaseFeature = -> Pad009
  Length = 30
  Length2 = 100
  Profile = -> Sketch038
  Refine = true
  Type = 0
FEATURE [PartDesign::Body] Body007  label="base002"
  Group = -> [Sketch035,Pad008,Sketch037,Pad009,Sketch038,Pocket003005]
  Origin = -> Origin011
  Placement = pos=(0,0,23) rot=(0,0,1;0rad)
  Tip = -> Pocket003005
FEATURE [App::Part] Part003  label="electronic_base_holder"
  Group = -> [Body007]
  License = CC BY 3.0
  LicenseURL = http://creativecommons.org/licenses/by/3.0/
  Origin = -> Origin010
FEATURE [Part::FeaturePython] Clone035  label="electronic_base_holder003"  # Draft clone (typed FeaturePython)
  AttacherType = Attacher::AttachEngine3D
  Fuse = false
  Objects = -> [Part003]
  Placement = pos=(0,0,56) rot=(0,0,1;0rad)
  Scale = (1,1,1)
FEATURE [App::DocumentObjectGroup] Grupo041  label="electronic_base_holder002"
  Group = -> [Clone035]
FEATURE [Part::Feature] Fusion007027  label="Servo-sg90-final008"
  Placement = pos=(-5,21,-13) rot=(0,0,1;0rad)
  shape: bbox 11.8 x 32.4 x 29.9 mm, 77 faces (baked)
FEATURE [Part::Feature] Pocket003040  label="Final-1-arm-horn006"
  Placement = pos=(-5,37.6,19) rot=(0,1,0;3.14159rad)
  shape: bbox 22.5 x 8 x 5 mm, 19 faces (baked)
FEATURE [Part::MultiFuse] Fusion007035  label="sg90-plus-1-horn-left"
  Placement = pos=(-51.5,-90,30.25) rot=(0,0,1;0rad)
  Refine = true
  Shapes = -> [Fusion007027,Pocket003040]
FEATURE [Part::FeaturePython] Array  label="servos-left-with-horn"  # Draft array (typed FeaturePython)
  Angle = 360
  ArrayType = 0
  Axis = (0,0,1)
  Base = -> Fusion007035
  Center = (0,0,0)
  Fuse = false
  IntervalAxis = (0,0,0)
  IntervalX = (1,0,0)
  IntervalY = (0,35,0)
  IntervalZ = (0,0,0)
  NumberPolar = 1
  NumberX = 1
  NumberY = 4
  NumberZ = 1
FEATURE [Part::Feature] Fusion007037  label="Servo-sg90-final009"
  Placement = pos=(-5,21,-13) rot=(0,0,1;0rad)
  shape: bbox 11.8 x 32.4 x 29.9 mm, 77 faces (baked)
FEATURE [Part::Feature] Pocket003041  label="Final-1-arm-horn007"
  Placement = pos=(-5,37.6,19) rot=(1,0,0;3.14159rad)
  shape: bbox 22.5 x 8 x 5 mm, 19 faces (baked)
FEATURE [Part::MultiFuse] Fusion007038  label="sg90-plus-1-horn-right"
  Placement = pos=(61.5,-90,30.25) rot=(0,0,1;0rad)
  Refine = true
  Shapes = -> [Fusion007037,Pocket003041]
FEATURE [Part::FeaturePython] Array001  label="servos-right-with-horn"  # Draft array (typed FeaturePython)
  Angle = 360
  ArrayType = 0
  Axis = (0,0,1)
  Base = -> Fusion007038
  Center = (0,0,0)
  Fuse = false
  IntervalAxis = (0,0,0)
  IntervalX = (1,0,0)
  IntervalY = (0,35,0)
  IntervalZ = (0,0,0)
  NumberPolar = 1
  NumberX = 1
  NumberY = 4
  NumberZ = 1
FEATURE [App::DocumentObjectGroup] Grupo038  label="servos"
  Group = -> [Fusion007034,Fusion007033,Fusion007035,Array,Array001]
FEATURE [Part::Feature] Fusion007040  label="Servo-sg90-final010"
  Placement = pos=(0,-16.6,0) rot=(0,0,1;0rad)
  shape: bbox 11.8 x 32.4 x 29.9 mm, 77 faces (baked)
FEATURE [Part::Feature] Pocket003042  label="Final-1-arm-horn008"
  Placement = pos=(0,0,32) rot=(0.707107,-0.707107,0;3.14159rad)
  shape: bbox 8 x 22.5 x 5 mm, 19 faces (baked)
FEATURE [Part::MultiFuse] Fusion007041  label="q1-aux-servo"
  Placement = pos=(0,0,17.25) rot=(0,0,1;0rad)
  Refine = true
  Shapes = -> [Pocket003042,Fusion007040]
FEATURE [Sketcher::SketchObject] Sketch039  label="base_cylinder"
  MapMode = 5
  Support = -> [XY_Plane013]
  sketch-geometry (2):
    g0: Circle CenterX=0 CenterY=0 CenterZ=0 NormalX=0 NormalY=0 NormalZ=1 AngleXU=0 Radius=3.75
    g1: Circle CenterX=0 CenterY=0 CenterZ=0 NormalX=0 NormalY=0 NormalZ=1 AngleXU=0 Radius=5.75
  constraints (4):
    c: Coincident(g0,g-1)
    c: Radius(g0) = 3.75
    c: Coincident(g1,g-1)
    c: Radius(g1) = 5.75
FEATURE [PartDesign::Pad] Pad010  label="low_base"
  Length = 2.25
  Length2 = 100
  Profile = -> Sketch039
  Refine = true
  Type = 0
FEATURE [Part::Feature] Fusion007043  label="Servo-sg90-final011"
  Placement = pos=(0,-16.6,0) rot=(0,0,1;0rad)
  shape: bbox 11.8 x 32.4 x 29.9 mm, 77 faces (baked)
FEATURE [Part::Feature] Pocket003043  label="Final-1-arm-horn009"
  Placement = pos=(0,0,32) rot=(0.707107,0.707107,0;3.14159rad)
  shape: bbox 8 x 22.5 x 5 mm, 19 faces (baked)
FEATURE [Part::MultiFuse] Fusion007044  label="q2-aux-servo"
  Placement = pos=(-24,-20.5,64) rot=(-0.377964,0.654654,0.654654;2.41885rad)
  Refine = true
  Shapes = -> [Fusion007043,Pocket003043]
FEATURE [Sketcher::SketchObject] Sketch041  label="basic_base001"
  MapMode = 5
  Placement = pos=(0,0,2.25) rot=(0,0,1;0rad)
  Support = -> [Pad010]
  sketch-geometry (6):
    g0: LineSegment StartX=0 StartY=5.71563 StartZ=0 EndX=-20.5 EndY=5.71563 EndZ=0
    g1: LineSegment StartX=1.86762e-06 StartY=-5.71497 StartZ=0 EndX=-20.5 EndY=-5.71497 EndZ=0
    g2: LineSegment StartX=-20.5 StartY=5.71563 StartZ=0 EndX=-20.5 EndY=-5.71497 EndZ=0
    g3: LineSegment StartX=0 StartY=5.71563 StartZ=0 EndX=5.71497 EndY=5.71563 EndZ=0
    g4: LineSegment StartX=5.71497 StartY=5.71563 StartZ=0 EndX=5.71497 EndY=0 EndZ=0
    g5: ArcOfCircle CenterX=0 CenterY=0 CenterZ=0 NormalX=0 NormalY=0 NormalZ=1 AngleXU=0 Radius=5.71497 StartAngle=4.71239 EndAngle=6.28319
  constraints (14):
    c: PointOnObject(g0,g-2)
    c: Horizontal(g0)
    c: DistanceX(g0,g0) = 20.5
    c: Coincident(g2,g0)
    c: Vertical(g2)
    c: Coincident(g1,g2)
    c: Coincident(g0,g3)
    c: Horizontal(g3)
    c: Coincident(g4,g3)
    c: PointOnObject(g4,g-1)
    c: Vertical(g4)
    c: Coincident(g5,g-1)
    c: Coincident(g5,g1)
    c: Coincident(g5,g4)
FEATURE [PartDesign::Pad] Pad011  label="q1_basic_base"
  BaseFeature = -> Pad010
  Length = 3.5
  Length2 = 100
  Profile = -> Sketch041
  Refine = true
  Type = 0
FEATURE [Sketcher::SketchObject] Sketch040  label="q1_base_horn"
  MapMode = 5
  Placement = pos=(0,0,5.75) rot=(0,0,1;0rad)
  Support = -> [Pad011]
  sketch-geometry (7):
    g0: LineSegment StartX=-1.25 StartY=3.53553 StartZ=0 EndX=-17 EndY=1.74295 EndZ=0
    g1: ArcOfCircle CenterX=-17 CenterY=0 CenterZ=0 NormalX=0 NormalY=0 NormalZ=1 AngleXU=0 Radius=1.74295 StartAngle=1.5708 EndAngle=3.14159
    g2: LineSegment [constr] StartX=-18.743 StartY=0 StartZ=0 EndX=0 EndY=0 EndZ=0
    g3: ArcOfCircle CenterX=0 CenterY=0 CenterZ=0 NormalX=0 NormalY=0 NormalZ=1 AngleXU=0 Radius=3.75 StartAngle=0 EndAngle=1.91063
    g4: LineSegment StartX=-1.25 StartY=-3.53553 StartZ=0 EndX=-17 EndY=-1.74295 EndZ=0
    g5: ArcOfCircle CenterX=-17 CenterY=-1e-12 CenterZ=0 NormalX=0 NormalY=0 NormalZ=1 AngleXU=0 Radius=1.74295 StartAngle=3.14159 EndAngle=4.71239
    g6: ArcOfCircle CenterX=0 CenterY=0 CenterZ=0 NormalX=0 NormalY=0 NormalZ=1 AngleXU=0 Radius=3.75 StartAngle=4.37255 EndAngle=6.28319
  constraints (11):
    c: PointOnObject(g1,g-1)
    c: Coincident(g1,g0)
    c: PointOnObject(g1,g-1)
    c: Coincident(g1,g2)
    c: Coincident(g3,g-1)
    c: Radius(g3) = 3.75
    c: Coincident(g3,g0)
    c: DistanceX(g0,g3) = 5
    c: Coincident(g5,g4)
    c: Radius(g6) = 3.75
    c: Coincident(g6,g4)
FEATURE [PartDesign::Pocket] Pocket003044  label="q1_basic_horn"
  BaseFeature = -> Pad011
  Length = 2.9
  Length2 = 100
  Profile = -> Sketch040
  Refine = true
  Type = 0
FEATURE [Sketcher::SketchObject] Sketch042  label="horn_holes"
  MapMode = 5
  Placement = pos=(0,0,2.85) rot=(0,0,1;0rad)
  Support = -> [Pocket003044]
  sketch-geometry (10):
    g0: Circle CenterX=0 CenterY=0 CenterZ=0 NormalX=0 NormalY=0 NormalZ=1 AngleXU=0 Radius=3.75
    g1: Circle CenterX=-14.5 CenterY=0 CenterZ=0 NormalX=0 NormalY=0 NormalZ=1 AngleXU=0 Radius=0.75
    g2: Circle CenterX=-12.5 CenterY=0 CenterZ=0 NormalX=0 NormalY=0 NormalZ=1 AngleXU=0 Radius=0.75
    g3: LineSegment [constr] StartX=-14.5 StartY=0 StartZ=0 EndX=-12.5 EndY=0 EndZ=0
    g4: Circle CenterX=-10.5 CenterY=0 CenterZ=0 NormalX=0 NormalY=0 NormalZ=1 AngleXU=0 Radius=0.75
    g5: LineSegment [constr] StartX=-12.5 StartY=0 StartZ=0 EndX=-10.5 EndY=0 EndZ=0
    g6: Circle CenterX=-8.5 CenterY=0 CenterZ=0 NormalX=0 NormalY=0 NormalZ=1 AngleXU=0 Radius=0.75
    g7: LineSegment [constr] StartX=-10.5 StartY=0 StartZ=0 EndX=-8.5 EndY=0 EndZ=0
    g8: Circle CenterX=-6.5 CenterY=0 CenterZ=0 NormalX=0 NormalY=0 NormalZ=1 AngleXU=0 Radius=0.75
    g9: LineSegment [constr] StartX=-8.5 StartY=0 StartZ=0 EndX=-6.5 EndY=0 EndZ=0
  constraints (25):
    c: Coincident(g0,g-1)
    c: Radius(g1) = 0.75
    c: Radius(g0) = 3.75
    c: Radius(g2) = 0.75
    c: Coincident(g1,g3)
    c: Coincident(g2,g3)
    c: Distance(g3) = 2
    c: Angle(g3) = 0
    c: Radius(g4) = 0.75
    c: Coincident(g2,g5)
    c: Coincident(g4,g5)
    c: Equal(g3,g5)
    c: Parallel(g5,g3)
    c: Radius(g6) = 0.75
    c: Coincident(g4,g7)
    c: Coincident(g6,g7)
    c: Equal(g3,g7)
    c: Parallel(g7,g3)
    c: Radius(g8) = 0.75
    c: Coincident(g6,g9)
    c: Coincident(g8,g9)
    c: Equal(g3,g9)
    c: Parallel(g9,g3)
    c: PointOnObject(g2,g-1)
    c: DistanceX(g8,g-1) = 6.5
FEATURE [PartDesign::Pocket] Pocket003045  label="q1_basic_horn_shape"
  BaseFeature = -> Pocket003044
  Length = 5
  Length2 = 100
  Profile = -> Sketch042
  Refine = true
  Type = 0
FEATURE [Part::Feature] Fusion007047  label="Servo-sg90-final012"
  Placement = pos=(0,-16.6,0) rot=(0,0,1;0rad)
  shape: bbox 11.8 x 32.4 x 29.9 mm, 77 faces (baked)
FEATURE [Part::Feature] Pocket003046  label="Final-1-arm-horn010"
  Placement = pos=(0,0,32) rot=(0,1,0;3.14159rad)
  shape: bbox 22.5 x 8 x 5 mm, 19 faces (baked)
FEATURE [Part::MultiFuse] Fusion007046  label="q1-aux-servo001"
  Placement = pos=(0,0,17.25) rot=(0,0,1;0rad)
  Refine = true
  Shapes = -> [Pocket003046,Fusion007047]
FEATURE [Sketcher::SketchObject] Sketch045  label="base_cylinder001"
  MapMode = 5
  Support = -> [XY_Plane015]
  sketch-geometry (2):
    g0: Circle CenterX=0 CenterY=0 CenterZ=0 NormalX=0 NormalY=0 NormalZ=1 AngleXU=0 Radius=3.75
    g1: Circle CenterX=0 CenterY=0 CenterZ=0 NormalX=0 NormalY=0 NormalZ=1 AngleXU=0 Radius=5.75
  constraints (4):
    c: Coincident(g0,g-1)
    c: Radius(g0) = 3.75
    c: Coincident(g1,g-1)
    c: Radius(g1) = 5.75
FEATURE [PartDesign::Pad] Pad013  label="low_base001"
  Length = 2.25
  Length2 = 100
  Profile = -> Sketch045
  Refine = true
  Type = 0
FEATURE [Part::Feature] Fusion007048  label="Servo-sg90-final013"
  Placement = pos=(0,-16.6,0) rot=(0,0,1;0rad)
  shape: bbox 11.8 x 32.4 x 29.9 mm, 77 faces (baked)
FEATURE [Part::Feature] Pocket003047  label="Final-1-arm-horn011"
  Placement = pos=(0,0,32) rot=(0.707107,0.707107,0;3.14159rad)
  shape: bbox 8 x 22.5 x 5 mm, 19 faces (baked)
FEATURE [Part::MultiFuse] Fusion007045  label="q2-aux-servo001"
  Placement = pos=(-32,-20.75,71) rot=(-0.281085,0.678598,0.678598;2.59356rad)
  Refine = true
  Shapes = -> [Fusion007048,Pocket003047]
FEATURE [Sketcher::SketchObject] Sketch047  label="basic_base002"
  MapMode = 5
  Placement = pos=(0,0,2.25) rot=(0,0,1;0rad)
  Support = -> [Pad013]
  sketch-geometry (4):
    g0: LineSegment StartX=3e-12 StartY=5.71497 StartZ=0 EndX=-20.5 EndY=5.71497 EndZ=0
    g1: ArcOfCircle CenterX=0 CenterY=0 CenterZ=0 NormalX=0 NormalY=0 NormalZ=1 AngleXU=0 Radius=5.71497 StartAngle=4.71239 EndAngle=7.85398
    g2: LineSegment StartX=2e-12 StartY=-5.71497 StartZ=0 EndX=-20.5 EndY=-5.71497 EndZ=0
    g3: LineSegment StartX=-20.5 StartY=5.71497 StartZ=0 EndX=-20.5 EndY=-5.71497 EndZ=0
  constraints (10):
    c: PointOnObject(g0,g-2)
    c: Horizontal(g0)
    c: Coincident(g1,g-1)
    c: Coincident(g1,g0)
    c: PointOnObject(g1,g-2)
    c: Tangent(g1,g2) = 1.5708
    c: DistanceX(g0,g0) = 20.5
    c: Coincident(g3,g0)
    c: Vertical(g3)
    c: Coincident(g2,g3)
FEATURE [PartDesign::Pad] Pad014  label="q1_basic_base001"
  BaseFeature = -> Pad013
  Length = 3.5
  Length2 = 100
  Profile = -> Sketch047
  Refine = true
  Type = 0
FEATURE [Sketcher::SketchObject] Sketch046  label="q1_base_horn001"
  MapMode = 5
  Placement = pos=(0,0,5.75) rot=(0,0,1;0rad)
  Support = -> [Pad014]
  sketch-geometry (7):
    g0: LineSegment StartX=-1.25 StartY=3.53553 StartZ=0 EndX=-17 EndY=1.74295 EndZ=0
    g1: ArcOfCircle CenterX=-17 CenterY=0 CenterZ=0 NormalX=0 NormalY=0 NormalZ=1 AngleXU=0 Radius=1.74295 StartAngle=1.5708 EndAngle=3.14159
    g2: LineSegment [constr] StartX=-18.743 StartY=0 StartZ=0 EndX=0 EndY=0 EndZ=0
    g3: ArcOfCircle CenterX=0 CenterY=0 CenterZ=0 NormalX=0 NormalY=0 NormalZ=1 AngleXU=0 Radius=3.75 StartAngle=0 EndAngle=1.91063
    g4: LineSegment StartX=-1.25 StartY=-3.53553 StartZ=0 EndX=-17 EndY=-1.74295 EndZ=0
    g5: ArcOfCircle CenterX=-17 CenterY=-1e-12 CenterZ=0 NormalX=0 NormalY=0 NormalZ=1 AngleXU=0 Radius=1.74295 StartAngle=3.14159 EndAngle=4.71239
    g6: ArcOfCircle CenterX=0 CenterY=0 CenterZ=0 NormalX=0 NormalY=0 NormalZ=1 AngleXU=0 Radius=3.75 StartAngle=4.37255 EndAngle=6.28319
  constraints (11):
    c: PointOnObject(g1,g-1)
    c: Coincident(g1,g0)
    c: PointOnObject(g1,g-1)
    c: Coincident(g1,g2)
    c: Coincident(g3,g-1)
    c: Radius(g3) = 3.75
    c: Coincident(g3,g0)
    c: DistanceX(g0,g3) = 5
    c: Coincident(g5,g4)
    c: Radius(g6) = 3.75
    c: Coincident(g6,g4)
FEATURE [PartDesign::Pocket] Pocket003048  label="q1_basic_horn001"
  BaseFeature = -> Pad014
  Length = 2.65
  Length2 = 100
  Profile = -> Sketch046
  Refine = true
  Type = 0
FEATURE [Sketcher::SketchObject] Sketch048  label="horn_holes001"
  MapMode = 5
  Placement = pos=(0,0,3.1) rot=(0,0,1;0rad)
  Support = -> [Pocket003048]
  sketch-geometry (10):
    g0: Circle CenterX=0 CenterY=0 CenterZ=0 NormalX=0 NormalY=0 NormalZ=1 AngleXU=0 Radius=3.75
    g1: Circle CenterX=-14.5 CenterY=0 CenterZ=0 NormalX=0 NormalY=0 NormalZ=1 AngleXU=0 Radius=0.75
    g2: Circle CenterX=-12.5 CenterY=0 CenterZ=0 NormalX=0 NormalY=0 NormalZ=1 AngleXU=0 Radius=0.75
    g3: LineSegment [constr] StartX=-14.5 StartY=0 StartZ=0 EndX=-12.5 EndY=0 EndZ=0
    g4: Circle CenterX=-10.5 CenterY=0 CenterZ=0 NormalX=0 NormalY=0 NormalZ=1 AngleXU=0 Radius=0.75
    g5: LineSegment [constr] StartX=-12.5 StartY=0 StartZ=0 EndX=-10.5 EndY=0 EndZ=0
    g6: Circle CenterX=-8.5 CenterY=0 CenterZ=0 NormalX=0 NormalY=0 NormalZ=1 AngleXU=0 Radius=0.75
    g7: LineSegment [constr] StartX=-10.5 StartY=0 StartZ=0 EndX=-8.5 EndY=0 EndZ=0
    g8: Circle CenterX=-6.5 CenterY=0 CenterZ=0 NormalX=0 NormalY=0 NormalZ=1 AngleXU=0 Radius=0.75
    g9: LineSegment [constr] StartX=-8.5 StartY=0 StartZ=0 EndX=-6.5 EndY=0 EndZ=0
  constraints (24):
    c: Coincident(g0,g-1)
    c: Radius(g1) = 0.75
    c: Radius(g0) = 3.75
    c: Radius(g2) = 0.75
    c: Coincident(g1,g3)
    c: Coincident(g2,g3)
    c: Distance(g3) = 2
    c: Angle(g3) = 0
    c: Radius(g4) = 0.75
    c: Coincident(g2,g5)
    c: Coincident(g4,g5)
    c: Equal(g3,g5)
    c: Parallel(g5,g3)
    c: Radius(g6) = 0.75
    c: Coincident(g4,g7)
    c: Coincident(g6,g7)
    c: Equal(g3,g7)
    c: Parallel(g7,g3)
    c: Radius(g8) = 0.75
    c: Coincident(g6,g9)
    c: Coincident(g8,g9)
    c: Equal(g3,g9)
    c: Parallel(g9,g3)
    c: PointOnObject(g2,g-1)
FEATURE [PartDesign::Pocket] Pocket003049  label="q1_basic_horn_shape001"
  BaseFeature = -> Pocket003048
  Length = 5
  Length2 = 100
  Profile = -> Sketch048
  Refine = true
  Type = 0
FEATURE [Sketcher::SketchObject] Sketch049
  MapMode = 5
  Placement = pos=(0,0,5.75) rot=(0,0,1;0rad)
  Support = -> [Pocket003049]
FEATURE [Sketcher::SketchObject] Sketch050
  ExternalGeometry = -> [Pocket003049]
  MapMode = 5
  Placement = pos=(0,-5.71497,0) rot=(1,0,0;1.5708rad)
  Support = -> [Pocket003049]
  sketch-geometry (14):
    g0: LineSegment StartX=-41.0098 StartY=27.0024 StartZ=0 EndX=-31.7604 EndY=36.1659 EndZ=0
    g1: LineSegment StartX=-31.7604 StartY=36.1659 StartZ=0 EndX=-15.2492 EndY=19.5 EndZ=0
    g2: LineSegment StartX=-15.2492 StartY=19.5 StartZ=0 EndX=-24.4986 EndY=10.3365 EndZ=0
    g3: LineSegment StartX=-24.4986 StartY=10.3365 StartZ=0 EndX=-41.0098 EndY=27.0024 EndZ=0
    g4: LineSegment StartX=-20.5 StartY=2.25 StartZ=0 EndX=-43.2559 EndY=25.0059 EndZ=0
    g5: LineSegment StartX=-43.2559 StartY=33.2342 StartZ=0 EndX=-38.3098 EndY=38.1804 EndZ=0
    g6: LineSegment StartX=-29.5322 StartY=38.1804 StartZ=0 EndX=-3.42593 EndY=12.0741 EndZ=0
    g7: LineSegment StartX=-20.5 StartY=2.25 StartZ=0 EndX=0 EndY=2.25 EndZ=0
    g8: Circle CenterX=-37.8254 CenterY=32.8179 CenterZ=0 NormalX=0 NormalY=0 NormalZ=1 AngleXU=0 Radius=1.25
    g9: Circle CenterX=-18.6103 CenterY=13.6164 CenterZ=0 NormalX=0 NormalY=0 NormalZ=1 AngleXU=0 Radius=1.25
    g10: LineSegment StartX=0 StartY=3.80315 StartZ=0 EndX=0 EndY=2.25 EndZ=0
    g11: ArcOfCircle CenterX=-39.1418 CenterY=29.1201 CenterZ=0 NormalX=0 NormalY=0 NormalZ=1 AngleXU=0 Radius=5.81825 StartAngle=2.35619 EndAngle=3.92699
    g12: ArcOfCircle CenterX=-33.921 CenterY=33.7916 CenterZ=0 NormalX=0 NormalY=0 NormalZ=1 AngleXU=0 Radius=6.20666 StartAngle=0.785398 EndAngle=2.35619
    g13: ArcOfCircle CenterX=-11.6969 CenterY=3.80315 CenterZ=0 NormalX=0 NormalY=0 NormalZ=1 AngleXU=0 Radius=11.6969 StartAngle=0 EndAngle=0.785398
  constraints (27):
    c: Coincident(g0,g1)
    c: Coincident(g1,g2)
    c: Coincident(g2,g3)
    c: Coincident(g3,g0)
    c: Perpendicular(g3,g0)
    c: Perpendicular(g2,g1)
    c: Perpendicular(g1,g0)
    c: Coincident(g-5,g4)
    c: Angle(g-3,g4) = 2.35619
    c: Perpendicular(g4,g5)
    c: Distance(g0,g4) = 3
    c: Perpendicular(g5,g6)
    c: Distance(g0,g6) = 3
    c: Coincident(g4,g7)
    c: PointOnObject(g7,g-2)
    c: Horizontal(g7)
    c: Radius(g8) = 1.25
    c: Equal(g8,g9) = 1.25
    c: Distance(g3) = 23.46
    c: Distance(g2) = 13.02
    c: Coincident(g10,g7)
    c: Tangent(g4,g11) = 1.5708
    c: Tangent(g5,g11) = 1.5708
    c: Tangent(g6,g12) = 1.5708
    c: Tangent(g5,g12) = 1.5708
    c: Tangent(g6,g13) = 1.5708
    c: Tangent(g10,g13) = 1.5708
FEATURE [PartDesign::Pad] Pad015  label="concept-try001"
  BaseFeature = -> Pocket003049
  Length = 2
  Length2 = 100
  Profile = -> Sketch050
  Refine = true
  Reversed = true
  Type = 0
FEATURE [PartDesign::Body] Body009  label="Q1-base001"
  Group = -> [Sketch045,Pad013,Sketch046,Sketch047,Pad014,Pocket003048,Sketch048,Pocket003049,Sketch049,Sketch050,Pad015]
  Origin = -> Origin015
  Placement = pos=(0,0,44) rot=(0,0,1;0rad)
  Tip = -> Pad015
FEATURE [App::Part] Part005  label="Leg_left_q1_45_degrees"
  Group = -> [Pocket003046,Fusion007047,Fusion007046,Body009,Fusion007048,Pocket003047,Fusion007045]
  License = CC BY 3.0
  LicenseURL = http://creativecommons.org/licenses/by/3.0/
  Origin = -> Origin014
FEATURE [Part::Feature] Pad012001  label="concept-try002"
  shape: bbox 43.52 x 11.5 x 36.32 mm, 35 faces (baked)
FEATURE [Part::Fillet] Fillet
  Base = -> Pad012001
  Edges = 1 edges r=5: [Edge34]
FEATURE [Part::Fillet] Fillet001
  Base = -> Fillet
  Edges = 1 edges r=2: [Edge39]
  Placement = pos=(0,0,86) rot=(0,0,1;0rad)
FEATURE [Part::Feature] Fusion007051  label="Servo-sg90-final014"
  Placement = pos=(0,-16.6,0) rot=(0,0,1;0rad)
  shape: bbox 11.8 x 32.4 x 29.9 mm, 77 faces (baked)
FEATURE [Part::Feature] Pocket003050  label="Final-1-arm-horn012"
  Placement = pos=(0,0,32) rot=(0,1,0;3.14159rad)
  shape: bbox 22.5 x 8 x 5 mm, 19 faces (baked)
FEATURE [Part::MultiFuse] Fusion007049  label="q1-aux-servo002"
  Placement = pos=(0,0,17.25) rot=(0,0,1;0rad)
  Refine = true
  Shapes = -> [Pocket003050,Fusion007051]
FEATURE [Sketcher::SketchObject] Sketch051  label="base_cylinder002"
  MapMode = 5
  Support = -> [XY_Plane017]
  sketch-geometry (2):
    g0: Circle CenterX=0 CenterY=0 CenterZ=0 NormalX=0 NormalY=0 NormalZ=1 AngleXU=0 Radius=3.75
    g1: Circle CenterX=0 CenterY=0 CenterZ=0 NormalX=0 NormalY=0 NormalZ=1 AngleXU=0 Radius=5.75
  constraints (4):
    c: Coincident(g0,g-1)
    c: Radius(g0) = 3.75
    c: Coincident(g1,g-1)
    c: Radius(g1) = 5.75
FEATURE [PartDesign::Pad] Pad012002  label="low_base002"
  Length = 2.25
  Length2 = 100
  Profile = -> Sketch051
  Refine = true
  Type = 0
FEATURE [Part::Feature] Fusion007052  label="Servo-sg90-final015"
  Placement = pos=(0,-16.6,0) rot=(0,0,1;0rad)
  shape: bbox 11.8 x 32.4 x 29.9 mm, 77 faces (baked)
FEATURE [Part::Feature] Pocket003051  label="Final-1-arm-horn013"
  Placement = pos=(0,0,32) rot=(0.707107,0.707107,0;3.14159rad)
  shape: bbox 8 x 22.5 x 5 mm, 19 faces (baked)
FEATURE [Part::MultiFuse] Fusion007050  label="q2-aux-servo002"
  Placement = pos=(-24,-19.5,68) rot=(-0.377964,0.654654,0.654654;2.41885rad)
  Refine = true
  Shapes = -> [Fusion007052,Pocket003051]
FEATURE [Sketcher::SketchObject] Sketch053  label="basic_base003"
  MapMode = 5
  Placement = pos=(0,0,2.25) rot=(0,0,1;0rad)
  Support = -> [Pad012002]
  sketch-geometry (4):
    g0: LineSegment StartX=3e-12 StartY=5.71497 StartZ=0 EndX=-20.5 EndY=5.71497 EndZ=0
    g1: ArcOfCircle CenterX=0 CenterY=0 CenterZ=0 NormalX=0 NormalY=0 NormalZ=1 AngleXU=0 Radius=5.71497 StartAngle=4.71239 EndAngle=7.85398
    g2: LineSegment StartX=2e-12 StartY=-5.71497 StartZ=0 EndX=-20.5 EndY=-5.71497 EndZ=0
    g3: LineSegment StartX=-20.5 StartY=5.71497 StartZ=0 EndX=-20.5 EndY=-5.71497 EndZ=0
  constraints (10):
    c: PointOnObject(g0,g-2)
    c: Horizontal(g0)
    c: Coincident(g1,g-1)
    c: Coincident(g1,g0)
    c: PointOnObject(g1,g-2)
    c: Tangent(g1,g2) = 1.5708
    c: DistanceX(g0,g0) = 20.5
    c: Coincident(g3,g0)
    c: Vertical(g3)
    c: Coincident(g2,g3)
FEATURE [PartDesign::Pad] Pad012003  label="q1_basic_base002"
  BaseFeature = -> Pad012002
  Length = 3.5
  Length2 = 100
  Profile = -> Sketch053
  Refine = true
  Type = 0
FEATURE [Sketcher::SketchObject] Sketch052  label="q1_base_horn002"
  MapMode = 5
  Placement = pos=(0,0,5.75) rot=(0,0,1;0rad)
  Support = -> [Pad012003]
  sketch-geometry (7):
    g0: LineSegment StartX=-1.25 StartY=3.53553 StartZ=0 EndX=-17 EndY=1.74295 EndZ=0
    g1: ArcOfCircle CenterX=-17 CenterY=0 CenterZ=0 NormalX=0 NormalY=0 NormalZ=1 AngleXU=0 Radius=1.74295 StartAngle=1.5708 EndAngle=3.14159
    g2: LineSegment [constr] StartX=-18.743 StartY=0 StartZ=0 EndX=0 EndY=0 EndZ=0
    g3: ArcOfCircle CenterX=0 CenterY=0 CenterZ=0 NormalX=0 NormalY=0 NormalZ=1 AngleXU=0 Radius=3.75 StartAngle=0 EndAngle=1.91063
    g4: LineSegment StartX=-1.25 StartY=-3.53553 StartZ=0 EndX=-17 EndY=-1.74295 EndZ=0
    g5: ArcOfCircle CenterX=-17 CenterY=-1e-12 CenterZ=0 NormalX=0 NormalY=0 NormalZ=1 AngleXU=0 Radius=1.74295 StartAngle=3.14159 EndAngle=4.71239
    g6: ArcOfCircle CenterX=0 CenterY=0 CenterZ=0 NormalX=0 NormalY=0 NormalZ=1 AngleXU=0 Radius=3.75 StartAngle=4.37255 EndAngle=6.28319
  constraints (11):
    c: PointOnObject(g1,g-1)
    c: Coincident(g1,g0)
    c: PointOnObject(g1,g-1)
    c: Coincident(g1,g2)
    c: Coincident(g3,g-1)
    c: Radius(g3) = 3.75
    c: Coincident(g3,g0)
    c: DistanceX(g0,g3) = 5
    c: Coincident(g5,g4)
    c: Radius(g6) = 3.75
    c: Coincident(g6,g4)
FEATURE [PartDesign::Pocket] Pocket003052  label="q1_basic_horn002"
  BaseFeature = -> Pad012003
  Length = 2.65
  Length2 = 100
  Profile = -> Sketch052
  Refine = true
  Type = 0
FEATURE [Sketcher::SketchObject] Sketch054  label="horn_holes002"
  MapMode = 5
  Placement = pos=(0,0,3.1) rot=(0,0,1;0rad)
  Support = -> [Pocket003052]
  sketch-geometry (10):
    g0: Circle CenterX=0 CenterY=0 CenterZ=0 NormalX=0 NormalY=0 NormalZ=1 AngleXU=0 Radius=3.75
    g1: Circle CenterX=-14.5 CenterY=0 CenterZ=0 NormalX=0 NormalY=0 NormalZ=1 AngleXU=0 Radius=0.75
    g2: Circle CenterX=-12.5 CenterY=0 CenterZ=0 NormalX=0 NormalY=0 NormalZ=1 AngleXU=0 Radius=0.75
    g3: LineSegment [constr] StartX=-14.5 StartY=0 StartZ=0 EndX=-12.5 EndY=0 EndZ=0
    g4: Circle CenterX=-10.5 CenterY=0 CenterZ=0 NormalX=0 NormalY=0 NormalZ=1 AngleXU=0 Radius=0.75
    g5: LineSegment [constr] StartX=-12.5 StartY=0 StartZ=0 EndX=-10.5 EndY=0 EndZ=0
    g6: Circle CenterX=-8.5 CenterY=0 CenterZ=0 NormalX=0 NormalY=0 NormalZ=1 AngleXU=0 Radius=0.75
    g7: LineSegment [constr] StartX=-10.5 StartY=0 StartZ=0 EndX=-8.5 EndY=0 EndZ=0
    g8: Circle CenterX=-6.5 CenterY=0 CenterZ=0 NormalX=0 NormalY=0 NormalZ=1 AngleXU=0 Radius=0.75
    g9: LineSegment [constr] StartX=-8.5 StartY=0 StartZ=0 EndX=-6.5 EndY=0 EndZ=0
  constraints (24):
    c: Coincident(g0,g-1)
    c: Radius(g1) = 0.75
    c: Radius(g0) = 3.75
    c: Radius(g2) = 0.75
    c: Coincident(g1,g3)
    c: Coincident(g2,g3)
    c: Distance(g3) = 2
    c: Angle(g3) = 0
    c: Radius(g4) = 0.75
    c: Coincident(g2,g5)
    c: Coincident(g4,g5)
    c: Equal(g3,g5)
    c: Parallel(g5,g3)
    c: Radius(g6) = 0.75
    c: Coincident(g4,g7)
    c: Coincident(g6,g7)
    c: Equal(g3,g7)
    c: Parallel(g7,g3)
    c: Radius(g8) = 0.75
    c: Coincident(g6,g9)
    c: Coincident(g8,g9)
    c: Equal(g3,g9)
    c: Parallel(g9,g3)
    c: PointOnObject(g2,g-1)
FEATURE [PartDesign::Pocket] Pocket003053  label="q1_basic_horn_shape002"
  BaseFeature = -> Pocket003052
  Length = 5
  Length2 = 100
  Profile = -> Sketch054
  Refine = true
  Type = 0
FEATURE [Sketcher::SketchObject] Sketch055
  ExternalGeometry = -> [Pocket003053]
  MapMode = 5
  Placement = pos=(0,-5.71497,0) rot=(1,0,0;1.5708rad)
  Support = -> [Pocket003053]
  sketch-geometry (16):
    g0: LineSegment StartX=-32.7402 StartY=21.4982 StartZ=0 EndX=-26.2302 EndY=32.7739 EndZ=0
    g1: LineSegment StartX=-26.2302 StartY=32.7739 StartZ=0 EndX=-5.91323 EndY=21.0439 EndZ=0
    g2: LineSegment StartX=-5.91322 StartY=21.0439 StartZ=0 EndX=-12.4232 EndY=9.76825 EndZ=0
    g3: LineSegment StartX=-12.4232 StartY=9.76825 StartZ=0 EndX=-32.7402 EndY=21.4982 EndZ=0
    g4: LineSegment StartX=-20.5 StartY=2.25 StartZ=0 EndX=0 EndY=2.25 EndZ=0
    g5: Circle CenterX=-31.1135 CenterY=28.1156 CenterZ=0 NormalX=0 NormalY=0 NormalZ=1 AngleXU=0 Radius=1.25
    g6: Circle CenterX=-7.6089 CenterY=14.5 CenterZ=0 NormalX=0 NormalY=0 NormalZ=1 AngleXU=0 Radius=1.25
    g7: GeomPoint X=-5 Y=2.25 Z=0
    g8: LineSegment StartX=-34.3161 StartY=18.944 StartZ=0 EndX=-19.2826 EndY=10.2644 EndZ=0
    g9: ArcOfCircle CenterX=-20.6983 CenterY=8.22484 CenterZ=0 NormalX=0 NormalY=0 NormalZ=1 AngleXU=0 Radius=2.48277 StartAngle=4.79236 EndAngle=7.24721
    g10: LineSegment StartX=-24.7486 StartY=35.3826 StartZ=0 EndX=-4.30948 EndY=23.5821 EndZ=0
    g11: LineSegment StartX=-36.8445 StartY=28.3802 StartZ=0 EndX=-34.2755 EndY=32.8299 EndZ=0
    g12: ArcOfCircle CenterX=-11.8509 CenterY=10.9572 CenterZ=0 NormalX=0 NormalY=0 NormalZ=1 AngleXU=0 Radius=14.7058 StartAngle=5.64953 EndAngle=7.31551
    g13: ArcOfCircle CenterX=-30.8622 CenterY=24.9263 CenterZ=0 NormalX=0 NormalY=0 NormalZ=1 AngleXU=0 Radius=6.9078 StartAngle=2.61799 EndAngle=4.18879
    g14: ArcOfCircle CenterX=-28.2357 CenterY=29.3428 CenterZ=0 NormalX=0 NormalY=0 NormalZ=1 AngleXU=0 Radius=6.97419 StartAngle=1.0472 EndAngle=2.61799
    g15: LineSegment StartX=-20.5 StartY=5.75 StartZ=0 EndX=-20.5 EndY=2.25 EndZ=0
  constraints (33):
    c: Coincident(g0,g1)
    c: Coincident(g1,g2)
    c: Coincident(g2,g3)
    c: Coincident(g3,g0)
    c: Perpendicular(g3,g0)
    c: Perpendicular(g2,g1)
    c: Perpendicular(g1,g0)
    c: PointOnObject(g4,g-2)
    c: Horizontal(g4)
    c: Radius(g5) = 1.25
    c: Equal(g5,g6) = 1.25
    c: Distance(g3) = 23.46
    c: Distance(g2) = 13.02
    c: Angle(g4,g3) = 2.61799
    c: PointOnObject(g7,g4)
    c: DistanceX(g2) = -12.4232
    c: DistanceY(g2) = 9.76825
    c: Distance(g0,g8) = 3
    c: Parallel(g3,g8)
    c: Coincident(g9,g-5)
    c: Coincident(g9,g8)
    c: Parallel(g1,g10)
    c: Distance(g0,g10) = 3
    c: Perpendicular(g11,g8)
    c: Coincident(g12,g10)
    c: Coincident(g12,g4)
    c: Tangent(g8,g13) = -1.5708
    c: Tangent(g11,g13) = 1.5708
    c: Tangent(g10,g14) = 1.5708
    c: Tangent(g11,g14) = 1.5708
    c: Coincident(g15,g9)
    c: Coincident(g15,g-5)
    c: Coincident(g4,g15)
FEATURE [PartDesign::Pad] Pad012004  label="concept-try003"
  BaseFeature = -> Pocket003053
  Length = 2
  Length2 = 100
  Profile = -> Sketch055
  Refine = true
  Reversed = true
  Type = 0
FEATURE [PartDesign::Body] Body010  label="Q1-base002"
  Group = -> [Sketch051,Pad012002,Sketch052,Sketch053,Pad012003,Pocket003052,Sketch054,Pocket003053,Sketch055,Pad012004]
  Origin = -> Origin017
  Placement = pos=(0,0,44) rot=(0,0,1;0rad)
  Tip = -> Pad012004
FEATURE [App::Part] Part006  label="Leg_left_q1_30_degrees"
  Group = -> [Pocket003050,Fusion007051,Fusion007049,Body010,Fusion007052,Pocket003051,Fusion007050]
  License = CC BY 3.0
  LicenseURL = http://creativecommons.org/licenses/by/3.0/
  Origin = -> Origin016
FEATURE [Sketcher::SketchObject] Sketch056  label="q2-base"
  ExternalGeometry = -> [Pocket003045]
  MapMode = 5
  Placement = pos=(-20.5,0,0) rot=(0.57735,-0.57735,-0.57735;2.0944rad)
  Support = -> [Pocket003045]
  sketch-geometry (6):
    g0: LineSegment StartX=-5.71563 StartY=2.25 StartZ=0 EndX=-11.6041 EndY=2.25 EndZ=0
    g1: LineSegment StartX=-11.6041 StartY=2.25 StartZ=0 EndX=-38.6752 EndY=17.8795 EndZ=0
    g2: LineSegment StartX=-11.6626 StartY=5.74787 StartZ=0 EndX=-37.1752 EndY=20.4776 EndZ=0
    g3: LineSegment StartX=-37.1752 StartY=20.4776 StartZ=0 EndX=-38.6752 EndY=17.8795 EndZ=0
    g4: LineSegment StartX=-5.71563 StartY=5.74787 StartZ=0 EndX=-5.71563 EndY=2.25 EndZ=0
    g5: LineSegment StartX=-11.6626 StartY=5.74787 StartZ=0 EndX=-5.71563 EndY=5.74787 EndZ=0
  constraints (13):
    c: Coincident(g3,g2)
    c: Coincident(g3,g1)
    c: Perpendicular(g3,g1)
    c: Coincident(g0,g-3)
    c: Parallel(g1,g2)
    c: Coincident(g4,g0)
    c: Perpendicular(g4,g0)
    c: Distance(g1,g2) = 3
    c: Angle(g0,g1) = 2.61799
    c: Coincident(g0,g1)
    c: Coincident(g2,g5)
    c: Coincident(g5,g4)
    c: Horizontal(g5)
FEATURE [PartDesign::Pad] Pad012005  label="q2-bed-base"
  BaseFeature = -> Pocket003045
  Length = 26.215
  Length2 = 100
  Profile = -> Sketch056
  Refine = true
  Reversed = true
  Type = 0
FEATURE [Sketcher::SketchObject] Sketch057  label="q2-corner-hole"
  MapMode = 5
  Placement = pos=(0,0,5.74787) rot=(0,0,1;0rad)
  Support = -> [Pad012005]
  sketch-geometry (4):
    g0: LineSegment StartX=-1.62396 StartY=12 StartZ=0 EndX=-5 EndY=12 EndZ=0
    g1: LineSegment StartX=-5 StartY=12 StartZ=0 EndX=-5 EndY=6.68085 EndZ=0
    g2: LineSegment StartX=-5 StartY=6.68085 StartZ=0 EndX=-1.62396 EndY=6.68085 EndZ=0
    g3: LineSegment StartX=-1.62396 StartY=6.68085 StartZ=0 EndX=-1.62396 EndY=12 EndZ=0
  constraints (8):
    c: Coincident(g0,g1)
    c: Coincident(g1,g2)
    c: Coincident(g2,g3)
    c: Coincident(g3,g0)
    c: Horizontal(g0)
    c: Horizontal(g2)
    c: Vertical(g1)
    c: Vertical(g3)
FEATURE [PartDesign::Pocket] Pocket003054  label="q2-corner-hole001"
  BaseFeature = -> Pad012005
  Length = 2
  Length2 = 100
  Profile = -> Sketch057
  Refine = true
  Type = 0
FEATURE [Sketcher::SketchObject] Sketch058  label="servo-walls"
  ExternalGeometry = -> [Pocket003054]
  MapMode = 5
  Placement = pos=(0,0.426745,-0.739143) rot=(1,0,0;0.523599rad)
  Support = -> [Pocket003054]
  sketch-geometry (24):
    g0: LineSegment StartX=-5 StartY=42.4334 StartZ=0 EndX=-5 EndY=37 EndZ=0
    g1: LineSegment StartX=-5 StartY=37 StartZ=0 EndX=-20.5 EndY=37 EndZ=0
    g2: LineSegment StartX=-20.5 StartY=37 StartZ=0 EndX=-20.5 EndY=39 EndZ=0
    g3: LineSegment StartX=2 StartY=39 StartZ=0 EndX=2 EndY=37 EndZ=0
    g4: LineSegment StartX=2 StartY=37 StartZ=0 EndX=-1.60533 EndY=37 EndZ=0
    g5: LineSegment StartX=-1.60533 StartY=37 StartZ=0 EndX=-1.60533 EndY=42.4334 EndZ=0
    g6: LineSegment StartX=-20.5 StartY=39 StartZ=0 EndX=-7 EndY=39 EndZ=0
    g7: LineSegment StartX=-7 StartY=39 StartZ=0 EndX=-7 EndY=42.4334 EndZ=0
    g8: LineSegment StartX=-7 StartY=42.4334 StartZ=0 EndX=-5 EndY=42.4334 EndZ=0
    g9: LineSegment StartX=2 StartY=39 StartZ=0 EndX=0.5 EndY=39 EndZ=0
    g10: LineSegment StartX=0.5 StartY=39 StartZ=0 EndX=0.5 EndY=42.4334 EndZ=0
    g11: LineSegment StartX=-1.60533 StartY=42.4334 StartZ=0 EndX=0.5 EndY=42.4334 EndZ=0
    g12: LineSegment StartX=-5 StartY=9.5 StartZ=0 EndX=-5 EndY=14 EndZ=0
    g13: LineSegment StartX=-5 StartY=14 StartZ=0 EndX=-20.5 EndY=14 EndZ=0
    g14: LineSegment StartX=-20.5 StartY=14 StartZ=0 EndX=-20.5 EndY=12 EndZ=0
    g15: LineSegment StartX=2 StartY=12 StartZ=0 EndX=2 EndY=14 EndZ=0
    g16: LineSegment StartX=2 StartY=14 StartZ=0 EndX=-1.61532 EndY=14 EndZ=0
    g17: LineSegment StartX=-1.61532 StartY=14 StartZ=0 EndX=-1.61532 EndY=9.5 EndZ=0
    g18: LineSegment StartX=-20.5 StartY=12 StartZ=0 EndX=-7 EndY=12 EndZ=0
    g19: LineSegment StartX=-7 StartY=12 StartZ=0 EndX=-7 EndY=9.5 EndZ=0
    g20: LineSegment StartX=-7 StartY=9.5 StartZ=0 EndX=-5 EndY=9.5 EndZ=0
    g21: LineSegment StartX=2 StartY=12 StartZ=0 EndX=0.5 EndY=12 EndZ=0
    g22: LineSegment StartX=0.5 StartY=12 StartZ=0 EndX=0.5 EndY=9.5 EndZ=0
    g23: LineSegment StartX=-1.61532 StartY=9.5 StartZ=0 EndX=0.5 EndY=9.5 EndZ=0
  constraints (50):
    c: Coincident(g0,g1)
    c: Coincident(g1,g2)
    c: Horizontal(g1)
    c: Vertical(g0)
    c: Vertical(g2)
    c: Coincident(g3,g4)
    c: Coincident(g4,g5)
    c: Horizontal(g4)
    c: Vertical(g3)
    c: Vertical(g5)
    c: Coincident(g2,g6)
    c: Horizontal(g6)
    c: Coincident(g6,g7)
    c: Vertical(g7)
    c: PointOnObject(g7,g-3)
    c: PointOnObject(g0,g-3)
    c: Coincident(g8,g7)
    c: Coincident(g8,g0)
    c: Coincident(g3,g9)
    c: Horizontal(g9)
    c: Coincident(g9,g10)
    c: PointOnObject(g10,g-3)
    c: Vertical(g10)
    c: PointOnObject(g5,g-3)
    c: Coincident(g11,g5)
    c: Coincident(g11,g10)
    c: Coincident(g12,g13)
    c: Coincident(g13,g14)
    c: Horizontal(g13)
    c: Vertical(g12)
    c: Vertical(g14)
    c: Coincident(g15,g16)
    c: Coincident(g16,g17)
    c: Horizontal(g16)
    c: Vertical(g15)
    c: Vertical(g17)
    c: Coincident(g14,g18)
    c: Horizontal(g18)
    c: Coincident(g18,g19)
    c: Vertical(g19)
    c: Coincident(g19,g20)
    c: Coincident(g20,g12)
    c: Horizontal(g20)
    c: Coincident(g15,g21)
    c: Horizontal(g21)
    c: Coincident(g21,g22)
    c: Vertical(g22)
    c: Coincident(g17,g23)
    c: Coincident(g23,g22)
    c: Horizontal(g23)
FEATURE [PartDesign::Pad] Pad012006  label="servo_walls"
  BaseFeature = -> Pocket003054
  Length = 12.5
  Length2 = 100
  Profile = -> Sketch058
  Refine = true
  Type = 0
FEATURE [Sketcher::SketchObject] Sketch059  label="front_wall"
  ExternalGeometry = -> [Pad012006]
  MapMode = 5
  Placement = pos=(2,0,0) rot=(0.57735,0.57735,0.57735;2.0944rad)
  Support = -> [Pad012006]
  sketch-geometry (9):
    g0: ArcOfCircle CenterX=18.4487 CenterY=16.9211 CenterZ=0 NormalX=0 NormalY=0 NormalZ=1 AngleXU=0 Radius=3.06832 StartAngle=3.68648 EndAngle=5.44463
    g1: LineSegment StartX=10.969 StartY=5.00105 StartZ=0 EndX=34.5617 EndY=18.1373 EndZ=0
    g2: LineSegment StartX=12.6837 StartY=20.7712 StartZ=0 EndX=4.56905 EndY=16.0862 EndZ=0
    g3: LineSegment StartX=4.56905 StartY=16.0862 StartZ=0 EndX=10.969 EndY=5.00105 EndZ=0
    g4: ArcOfCircle CenterX=24 CenterY=19.9888 CenterZ=0 NormalX=0 NormalY=0 NormalZ=1 AngleXU=0 Radius=6.3928 StartAngle=4.13303 EndAngle=7.03916
    g5: LineSegment StartX=28.6514 StartY=24.3743 StartZ=0 EndX=26.2197 EndY=28.5862 EndZ=0
    g6: LineSegment StartX=26.2197 StartY=28.5862 StartZ=0 EndX=27.9517 EndY=29.5862 EndZ=0
    g7: LineSegment StartX=27.9517 StartY=29.5862 StartZ=0 EndX=34.5617 EndY=18.1373 EndZ=0
    g8: LineSegment StartX=12.6837 StartY=20.7712 StartZ=0 EndX=15.8247 EndY=15.3307 EndZ=0
  constraints (20):
    c: Coincident(g3,g2)
    c: Parallel(g-7,g3)
    c: Coincident(g-7,g2)
    c: Coincident(g1,g3)
    c: Parallel(g-8,g2)
    c: Coincident(g4,g0)
    c: PointOnObject(g4,g-4)
    c: Coincident(g5,g4)
    c: Coincident(g5,g-5)
    c: Coincident(g5,g6)
    c: Coincident(g6,g-5)
    c: Coincident(g6,g7)
    c: Parallel(g-9,g7)
    c: Coincident(g7,g1)
    c: Coincident(g8,g2)
    c: Coincident(g8,g0)
    c: Perpendicular(g8,g2)
    c: Distance(g2) = 9.37
    c: Distance(g3) = 12.8
    c: Distance(g7) = 13.22
FEATURE [PartDesign::Pad] Pad012007  label="front_wall001"
  BaseFeature = -> Pad012006
  Length = 3.715
  Length2 = 100
  Profile = -> Sketch059
  Refine = true
  Type = 0
FEATURE [Sketcher::SketchObject] Sketch061  label="back_wall001"
  ExternalGeometry = -> [Pad012007]
  MapMode = 5
  Placement = pos=(-20.5,0,0) rot=(0.57735,-0.57735,-0.57735;2.0944rad)
  Support = -> [Pad012007]
  sketch-geometry (9):
    g0: LineSegment StartX=5.71497 StartY=2.25 StartZ=0 EndX=-11.6041 EndY=2.25 EndZ=0
    g1: LineSegment StartX=-11.6041 StartY=2.25 StartZ=0 EndX=-38.6752 EndY=17.8795 EndZ=0
    g2: LineSegment StartX=-38.6752 StartY=17.8795 StartZ=0 EndX=-37.1752 EndY=20.4776 EndZ=0
    g3: LineSegment StartX=-37.1752 StartY=20.4776 StartZ=0 EndX=-34.2017 EndY=18.7609 EndZ=0
    g4: LineSegment StartX=-34.2017 StartY=18.7609 StartZ=0 EndX=-27.9517 EndY=29.5862 EndZ=0
    g5: LineSegment StartX=-27.9517 StartY=29.5862 StartZ=0 EndX=-4.56905 EndY=16.0862 EndZ=0
    g6: LineSegment StartX=-4.56905 StartY=16.0862 StartZ=0 EndX=-10.5379 EndY=5.74787 EndZ=0
    g7: LineSegment StartX=-10.5379 StartY=5.74787 StartZ=0 EndX=5.71497 EndY=5.75 EndZ=0
    g8: LineSegment StartX=5.71497 StartY=5.75 StartZ=0 EndX=5.71497 EndY=2.25 EndZ=0
  constraints (18):
    c: Coincident(g-11,g0)
    c: Coincident(g0,g-11)
    c: Coincident(g0,g1)
    c: Coincident(g1,g-4)
    c: Coincident(g1,g2)
    c: Coincident(g2,g-5)
    c: Coincident(g2,g3)
    c: Coincident(g3,g-6)
    c: Coincident(g3,g4)
    c: Coincident(g4,g-6)
    c: Coincident(g4,g5)
    c: Coincident(g5,g-7)
    c: Coincident(g5,g6)
    c: Coincident(g6,g-8)
    c: Coincident(g6,g7)
    c: Coincident(g7,g-10)
    c: Coincident(g7,g8)
    c: Coincident(g8,g0)
FEATURE [PartDesign::Pad] Pad012008  label="back_wall"
  BaseFeature = -> Pad012007
  Length = 1.75
  Length2 = 100
  Profile = -> Sketch061
  Refine = true
  Type = 0
FEATURE [Sketcher::SketchObject] Sketch064  label="q2_axis"
  MapMode = 5
  Placement = pos=(-22.25,0,0) rot=(0.57735,-0.57735,-0.57735;2.0944rad)
  Support = -> [Pad012008]
  sketch-geometry (1):
    g0: Circle CenterX=-24 CenterY=20 CenterZ=0 NormalX=0 NormalY=0 NormalZ=1 AngleXU=0 Radius=1.75
  constraints (1):
    c: Radius(g0) = 1.75
FEATURE [PartDesign::Pad] Pad012009  label="servo_axis"
  BaseFeature = -> Pad012008
  Length = 3
  Length2 = 100
  Profile = -> Sketch064
  Refine = true
  Type = 0
FEATURE [Sketcher::SketchObject] Sketch062  label="servo_tollerance"
  MapMode = 5
  Placement = pos=(2.495e-13,-5.82326,10.0862) rot=(1,0,0;0.523599rad)
  Support = -> [Pad012009]
  sketch-geometry (4):
    g0: LineSegment StartX=-20.5 StartY=37 StartZ=0 EndX=-21.25 EndY=37 EndZ=0
    g1: LineSegment StartX=-21.25 StartY=37 StartZ=0 EndX=-21.25 EndY=14 EndZ=0
    g2: LineSegment StartX=-21.25 StartY=14 StartZ=0 EndX=-20.5 EndY=14 EndZ=0
    g3: LineSegment StartX=-20.5 StartY=14 StartZ=0 EndX=-20.5 EndY=37 EndZ=0
  constraints (9):
    c: Coincident(g0,g1)
    c: Coincident(g1,g2)
    c: Coincident(g2,g3)
    c: Coincident(g3,g0)
    c: Horizontal(g0)
    c: Horizontal(g2)
    c: Vertical(g1)
    c: Vertical(g3)
    c: DistanceX(g0,g0) = 0.75
FEATURE [PartDesign::Pocket] Pocket003055  label="servo_tollerance001"
  BaseFeature = -> Pad012009
  Length = 12.5
  Length2 = 100
  Profile = -> Sketch062
  Refine = true
  Type = 0
FEATURE [Sketcher::SketchObject] Sketch063  label="cable_slot"
  ExternalGeometry = -> [Pocket003055]
  MapMode = 5
  Placement = pos=(-4.306e-13,33.775,19.5) rot=(0,0.5,0.866025;3.14159rad)
  Support = -> [Pocket003055]
  sketch-geometry (4):
    g0: LineSegment StartX=20.25 StartY=3 StartZ=0 EndX=18.01 EndY=3 EndZ=0
    g1: LineSegment StartX=18.01 StartY=3 StartZ=0 EndX=18.01 EndY=12.5 EndZ=0
    g2: LineSegment StartX=18.01 StartY=12.5 StartZ=0 EndX=20.25 EndY=12.5 EndZ=0
    g3: LineSegment StartX=20.25 StartY=12.5 StartZ=0 EndX=20.25 EndY=3 EndZ=0
  constraints (11):
    c: Coincident(g0,g1)
    c: Coincident(g1,g2)
    c: Coincident(g2,g3)
    c: Coincident(g3,g0)
    c: Horizontal(g0)
    c: Horizontal(g2)
    c: Vertical(g1)
    c: Vertical(g3)
    c: DistanceX(g2,g2) = 2.24
    c: DistanceY(g1,g1) = 9.5
    c: DistanceX(g2,g-3) = 2
FEATURE [PartDesign::Pocket] Pocket003056  label="cable_slot001"
  BaseFeature = -> Pocket003055
  Length = 5
  Length2 = 100
  Profile = -> Sketch063
  Refine = true
  Type = 0
FEATURE [Sketcher::SketchObject] Sketch060  label="m2_screw_holes"
  MapMode = 5
  Placement = pos=(-22.25,0,0) rot=(0.57735,-0.57735,-0.57735;2.0944rad)
  Support = -> [Pocket003056]
  sketch-geometry (2):
    g0: Circle CenterX=-31.1478 CenterY=24.1208 CenterZ=0 NormalX=0 NormalY=0 NormalZ=1 AngleXU=0 Radius=1.25
    g1: Circle CenterX=-7.61619 CenterY=10.5 CenterZ=0 NormalX=0 NormalY=0 NormalZ=1 AngleXU=0 Radius=1.25
  constraints (2):
    c: Radius(g0) = 1.25
    c: Equal(g0,g1) = 1.25
FEATURE [PartDesign::Hole] Hole  label="m2_screw_holes001"
  BaseFeature = -> Pocket003056
  Depth = 35
  DepthType = 0
  Diameter = 2.5
  DrillPoint = 1
  DrillPointAngle = 118
  HoleCutCountersinkAngle = 90
  HoleCutDepth = 0
  HoleCutDiameter = 0
  HoleCutType = 0
  ModelActualThread = false
  Profile = -> Sketch060
  Refine = true
  Tapered = false
  TaperedAngle = 90
  ThreadAngle = 0
  ThreadClass = 0
  ThreadCutOffInner = 0
  ThreadCutOffOuter = 0
  ThreadDirection = 0
  ThreadFit = 0
  ThreadPitch = 0
  ThreadSize = 0
  ThreadType = 0
  Threaded = false
FEATURE [Sketcher::SketchObject] Sketch065  label="finger_hole"
  ExternalGeometry = -> [Hole]
  MapMode = 5
  Placement = pos=(0,1.92674,-3.33722) rot=(1,0,0;3.66519rad)
  Support = -> [Hole]
  sketch-geometry (2):
    g0: Circle CenterX=-8.2675 CenterY=-26.8039 CenterZ=0 NormalX=0 NormalY=0 NormalZ=1 AngleXU=0 Radius=6
    g1: LineSegment [constr] StartX=-8.2675 StartY=-11.1744 StartZ=0 EndX=-8.2675 EndY=-42.4334 EndZ=0
  constraints (7):
    c: Radius(g0) = 6
    c: PointOnObject(g1,g-3)
    c: PointOnObject(g1,g-4)
    c: Vertical(g1)
    c: PointOnObject(g0,g1)
    c: Symmetric(g-3,g-3,g1)
    c: Symmetric(g1,g1,g0)
FEATURE [PartDesign::Pocket] Pocket003057  label="q1-leg"
  BaseFeature = -> Hole
  Length = 5
  Length2 = 100
  Profile = -> Sketch065
  Refine = true
  Type = 0
FEATURE [PartDesign::FeatureBase] Clone036
  BaseFeature = -> Pocket003057
FEATURE [Part::Fillet] Fillet002  label="rounder_q1_servo"
  Base = -> Clone036
  Edges = 1 edges r=8: [Edge27]
  Placement = pos=(0,0,44) rot=(0,0,1;1.5708rad)
FEATURE [Sketcher::SketchObject] Sketch066  label="base_cylinder003"
  MapMode = 5
  Placement = pos=(0,6.2,0) rot=(0,0.707107,0.707107;3.14159rad)
  sketch-geometry (2):
    g0: Circle CenterX=24 CenterY=64 CenterZ=0 NormalX=0 NormalY=0 NormalZ=1 AngleXU=0 Radius=3.75
    g1: Circle CenterX=24 CenterY=64 CenterZ=0 NormalX=0 NormalY=0 NormalZ=1 AngleXU=0 Radius=5.75
  constraints (3):
    c: Radius(g0) = 3.75
    c: Radius(g1) = 5.75
    c: Coincident(g1,g0)
FEATURE [PartDesign::Pad] Pad012010  label="q2_base_cylinder"
  Length = 2.25
  Length2 = 100
  Placement = pos=(0,6.2,0) rot=(0,0.707107,0.707107;3.14159rad)
  Profile = -> Sketch066
  Refine = true
  Type = 0
FEATURE [Sketcher::SketchObject] Sketch067  label="q2_base"
  ExternalGeometry = -> [Pad012010]
  MapMode = 5
  Placement = pos=(2e-16,8.45,-9e-16) rot=(0,0.707107,0.707107;3.14159rad)
  Support = -> [Pad012010]
  sketch-geometry (6):
    g0: ArcOfCircle CenterX=24 CenterY=64 CenterZ=0 NormalX=0 NormalY=0 NormalZ=1 AngleXU=0 Radius=5.75 StartAngle=2.0944 EndAngle=5.23599
    g1: LineSegment [constr] StartX=12.5 StartY=64 StartZ=0 EndX=37 EndY=64 EndZ=0
    g2: LineSegment [constr] StartX=24 StartY=64 StartZ=0 EndX=21.125 EndY=68.9796 EndZ=0
    g3: LineSegment StartX=21.125 StartY=68.9796 StartZ=0 EndX=39.516 EndY=79.5977 EndZ=0
    g4: LineSegment StartX=39.516 StartY=79.5977 StartZ=0 EndX=45.266 EndY=69.6384 EndZ=0
    g5: LineSegment StartX=45.266 StartY=69.6384 StartZ=0 EndX=26.875 EndY=59.0204 EndZ=0
  constraints (14):
    c: Coincident(g0,g-3)
    c: PointOnObject(g0,g-3)
    c: Angle(g0) = 3.14159
    c: Horizontal(g1)
    c: PointOnObject(g0,g1)
    c: Coincident(g2,g0)
    c: Coincident(g2,g0)
    c: Angle(g1,g2) = 2.0944
    c: Tangent(g0,g3) = 1.5708
    c: Coincident(g3,g4)
    c: Coincident(g4,g5)
    c: Coincident(g5,g0)
    c: Equal(g3,g5)
    c: Parallel(g3,g5)
FEATURE [PartDesign::Pad] Pad012011  label="q2_basic_base"
  BaseFeature = -> Pad012010
  Length = 3.5
  Length2 = 100
  Placement = pos=(0,6.2,0) rot=(0,0.707107,0.707107;3.14159rad)
  Profile = -> Sketch067
  Refine = true
  Type = 0
FEATURE [Sketcher::SketchObject] Sketch068  label="AUX_q2_base_horn003"
  ExternalGeometry = -> [Pad012011]
  MapMode = 5
  Placement = pos=(-3e-15,11.95,-6e-15) rot=(0.186157,0.694747,0.694747;3.50969rad)
  sketch-geometry (5):
    g0: LineSegment StartX=54.0346 StartY=46.9656 StartZ=0 EndX=69.7804 EndY=45.1656 EndZ=0
    g1: ArcOfCircle CenterX=69.7804 CenterY=43.4256 CenterZ=0 NormalX=0 NormalY=0 NormalZ=1 AngleXU=0 Radius=1.74 StartAngle=0 EndAngle=1.5708
    g2: LineSegment [constr] StartX=71.5204 StartY=43.4256 StartZ=0 EndX=49.0304 EndY=43.4256 EndZ=0
    g3: ArcOfCircle CenterX=52.7846 CenterY=43.4256 CenterZ=0 NormalX=0 NormalY=0 NormalZ=1 AngleXU=0 Radius=3.75421 StartAngle=1.23136 EndAngle=3.14159
    g4: LineSegment [constr] StartX=52.7846 StartY=49.1756 StartZ=0 EndX=52.7846 EndY=37.6756 EndZ=0
  constraints (16):
    c: Coincident(g1,g0)
    c: Coincident(g1,g2)
    c: Coincident(g3,g0)
    c: Radius(g1) = 1.74
    c: PointOnObject(g1,g2)
    c: Coincident(g2,g3)
    c: PointOnObject(g3,g2)
    c: DistanceX(g2,g2) = 22.49
    c: DistanceY(g1,g0) = 1.74
    c: DistanceX(g3,g0) = 1.25
    c: DistanceY(g3,g0) = 3.54
    c: Horizontal(g2)
    c: Coincident(g4,g-3)
    c: Coincident(g4,g-4)
    c: PointOnObject(g3,g4)
    c: Symmetric(g4,g4,g3)
FEATURE [Sketcher::SketchObject] Sketch069  label="horn_shape"
  ExternalGeometry = -> [Sketch068]
  MapMode = 5
  Placement = pos=(6e-16,11.95,-5.8e-15) rot=(0,0.707107,0.707107;3.14159rad)
  Support = -> [Pad012011]
  sketch-geometry (7):
    g0: LineSegment [constr] StartX=20.7488 StartY=62.1229 StartZ=0 EndX=40.2257 EndY=73.3679 EndZ=0
    g1: ArcOfCircle CenterX=24 CenterY=64 CenterZ=0 NormalX=0 NormalY=0 NormalZ=1 AngleXU=0 Radius=3.75421 StartAngle=1.75495 EndAngle=3.66519
    g2: ArcOfCircle CenterX=38.7188 CenterY=72.4979 CenterZ=0 NormalX=0 NormalY=0 NormalZ=1 AngleXU=0 Radius=1.74 StartAngle=0.523599 EndAngle=2.0944
    g3: LineSegment StartX=23.3125 StartY=67.6907 StartZ=0 EndX=37.8488 EndY=74.0048 EndZ=0
    g4: ArcOfCircle CenterX=24 CenterY=64 CenterZ=0 NormalX=0 NormalY=0 NormalZ=1 AngleXU=0 Radius=3.75421 StartAngle=3.66519 EndAngle=5.57543
    g5: ArcOfCircle CenterX=38.7188 CenterY=72.4979 CenterZ=0 NormalX=0 NormalY=0 NormalZ=1 AngleXU=0 Radius=1.74 StartAngle=5.23599 EndAngle=6.80678
    g6: LineSegment StartX=26.8525 StartY=61.5593 StartZ=0 EndX=39.5888 EndY=70.991 EndZ=0
  constraints (16):
    c: Coincident(g0,g-5)
    c: Coincident(g0,g-4)
    c: Coincident(g1,g-5)
    c: Coincident(g1,g-5)
    c: Coincident(g1,g0)
    c: Coincident(g2,g-4)
    c: Coincident(g2,g0)
    c: Coincident(g2,g-4)
    c: Coincident(g3,g1)
    c: Coincident(g3,g2)
    c: Coincident(g6,g4)
    c: Coincident(g6,g5)
    c: Coincident(g0,g4)
    c: Coincident(g1,g4)
    c: Coincident(g2,g5)
    c: Coincident(g0,g5)
FEATURE [PartDesign::Pocket] Pocket003058  label="horn_shape001"
  BaseFeature = -> Pad012011
  Length = 2.65
  Length2 = 100
  Placement = pos=(0,6.2,0) rot=(0,0.707107,0.707107;3.14159rad)
  Profile = -> Sketch069
  Refine = true
  Type = 0
FEATURE [Sketcher::SketchObject] Sketch070  label="horn_holes003"
  ExternalGeometry = -> [Pocket003058]
  MapMode = 5
  Placement = pos=(2e-16,9.3,-5.3e-15) rot=(0,0.707107,0.707107;3.14159rad)
  Support = -> [Pocket003058]
  sketch-geometry (16):
    g0: Circle CenterX=24 CenterY=64 CenterZ=0 NormalX=0 NormalY=0 NormalZ=1 AngleXU=0 Radius=3.75
    g1: Circle CenterX=-14.6952 CenterY=0 CenterZ=0 NormalX=0 NormalY=0 NormalZ=1 AngleXU=0 Radius=0.75
    g2: Circle CenterX=-12.6952 CenterY=0 CenterZ=0 NormalX=0 NormalY=0 NormalZ=1 AngleXU=0 Radius=0.75
    g3: LineSegment [constr] StartX=-14.6952 StartY=0 StartZ=0 EndX=-12.6952 EndY=0 EndZ=0
    g4: Circle CenterX=-10.6952 CenterY=0 CenterZ=0 NormalX=0 NormalY=0 NormalZ=1 AngleXU=0 Radius=0.75
    g5: LineSegment [constr] StartX=-12.6952 StartY=0 StartZ=0 EndX=-10.6952 EndY=0 EndZ=0
    g6: Circle CenterX=-8.69518 CenterY=0 CenterZ=0 NormalX=0 NormalY=0 NormalZ=1 AngleXU=0 Radius=0.75
    g7: LineSegment [constr] StartX=-10.6952 StartY=0 StartZ=0 EndX=-8.69518 EndY=0 EndZ=0
    g8: Circle CenterX=-6.69518 CenterY=0 CenterZ=0 NormalX=0 NormalY=0 NormalZ=1 AngleXU=0 Radius=0.75
    g9: LineSegment [constr] StartX=-8.69518 StartY=0 StartZ=0 EndX=-6.69518 EndY=0 EndZ=0
    g10: LineSegment [constr] StartX=24 StartY=64 StartZ=0 EndX=43.3449 EndY=75.1688 EndZ=0
    g11: Circle CenterX=29.6292 CenterY=67.25 CenterZ=0 NormalX=0 NormalY=0 NormalZ=1 AngleXU=0 Radius=0.75
    g12: Circle CenterX=31.3612 CenterY=68.25 CenterZ=0 NormalX=0 NormalY=0 NormalZ=1 AngleXU=0 Radius=0.75
    g13: Circle CenterX=33.0933 CenterY=69.25 CenterZ=0 NormalX=0 NormalY=0 NormalZ=1 AngleXU=0 Radius=0.75
    g14: Circle CenterX=34.8253 CenterY=70.25 CenterZ=0 NormalX=0 NormalY=0 NormalZ=1 AngleXU=0 Radius=0.75
    g15: Circle CenterX=36.5574 CenterY=71.25 CenterZ=0 NormalX=0 NormalY=0 NormalZ=1 AngleXU=0 Radius=0.75
  constraints (41):
    c: Radius(g1) = 0.75
    c: Radius(g0) = 3.75
    c: Radius(g2) = 0.75
    c: Coincident(g1,g3)
    c: Coincident(g2,g3)
    c: Distance(g3) = 2
    c: Angle(g3) = 0
    c: Radius(g4) = 0.75
    c: Coincident(g2,g5)
    c: Coincident(g4,g5)
    c: Equal(g3,g5)
    c: Radius(g6) = 0.75
    c: Coincident(g4,g7)
    c: Coincident(g6,g7)
    c: Equal(g3,g7)
    c: Radius(g8) = 0.75
    c: Coincident(g6,g9)
    c: Coincident(g8,g9)
    c: Equal(g3,g9)
    c: Parallel(g9,g3)
    c: Parallel(g9,g7)
    c: Parallel(g7,g5)
    c: Coincident(g10,g0)
    c: Angle(g10) = 0.523599
    c: Radius(g11) = 0.75
    c: Distance(g0,g11) = 6.5
    c: PointOnObject(g11,g10)
    c: Equal(g11,g12) = 0.75
    c: PointOnObject(g12,g10)
    c: DistanceX(g0) = 24
    c: DistanceY(g0) = 64
    c: Distance(g11,g12) = 2
    c: Equal(g11,g13) = 0.75
    c: PointOnObject(g13,g10)
    c: Equal(g11,g14) = 0.75
    c: PointOnObject(g14,g10)
    c: Equal(g11,g15) = 0.75
    c: PointOnObject(g15,g10)
    c: Distance(g12,g13) = 2
    c: Distance(g13,g14) = 2
    c: Distance(g14,g15) = 2
FEATURE [PartDesign::Pocket] Pocket003059  label="basic_horn_union"
  BaseFeature = -> Pocket003058
  Length = 5
  Length2 = 100
  Placement = pos=(0,6.2,0) rot=(0,0.707107,0.707107;3.14159rad)
  Profile = -> Sketch070
  Refine = true
  Type = 0
FEATURE [Sketcher::SketchObject] Sketch071  label="q2_bridge"
  ExternalGeometry = -> [Pocket003059]
  MapMode = 5
  Placement = pos=(2e-16,8.45,-2.3e-15) rot=(0,-0.707107,0.707107;3.14159rad)
  Support = -> [Pocket003059]
  sketch-geometry (4):
    g0: LineSegment StartX=39.516 StartY=-79.5977 StartZ=0 EndX=45.266 EndY=-69.6384 EndZ=0
    g1: LineSegment StartX=45.266 StartY=-69.6384 StartZ=0 EndX=40.9358 EndY=-67.1384 EndZ=0
    g2: LineSegment StartX=39.516 StartY=-79.5977 StartZ=0 EndX=35.1858 EndY=-77.0977 EndZ=0
    g3: ArcOfCircle CenterX=24.5001 CenterY=-64.2888 CenterZ=0 NormalX=0 NormalY=0 NormalZ=1 AngleXU=0 Radius=16.6809 StartAngle=5.40766 EndAngle=6.11151
  constraints (10):
    c: Coincident(g-5,g0)
    c: Coincident(g0,g-5)
    c: Coincident(g0,g1)
    c: PointOnObject(g1,g-3)
    c: Coincident(g0,g2)
    c: PointOnObject(g2,g-4)
    c: Distance(g2) = 5
    c: Equal(g2,g1)
    c: Coincident(g3,g1)
    c: Coincident(g3,g2)
FEATURE [PartDesign::Pad] Pad012012  label="q2_bridge001"
  BaseFeature = -> Pocket003059
  Length = 31
  Length2 = 100
  Placement = pos=(0,6.2,0) rot=(0,0.707107,0.707107;3.14159rad)
  Profile = -> Sketch071
  Refine = true
  Type = 0
FEATURE [Sketcher::SketchObject] Sketch072  label="q2_back_union"
  ExternalGeometry = -> [Pad012010,Sketch067]
  MapMode = 5
  Placement = pos=(-2.3e-15,-22.55,3.83e-14) rot=(0,-0.707107,0.707107;3.14159rad)
  Support = -> [Pad012012]
  expr: Constraints[2] = Sketch067.Constraints[2]
  sketch-geometry (7):
    g0: ArcOfCircle CenterX=24 CenterY=-64 CenterZ=0 NormalX=0 NormalY=0 NormalZ=1 AngleXU=0 Radius=5.75 StartAngle=1.0472 EndAngle=4.18879
    g1: LineSegment [constr] StartX=12.5 StartY=-64 StartZ=0 EndX=37 EndY=-64 EndZ=0
    g2: LineSegment [constr] StartX=24 StartY=-64 StartZ=0 EndX=26.875 EndY=-59.0204 EndZ=0
    g3: LineSegment StartX=45.266 StartY=-69.6384 StartZ=0 EndX=26.875 EndY=-59.0204 EndZ=0
    g4: LineSegment StartX=45.266 StartY=-69.6384 StartZ=0 EndX=39.516 EndY=-79.5977 EndZ=0
    g5: LineSegment StartX=39.516 StartY=-79.5977 StartZ=0 EndX=21.125 EndY=-68.9796 EndZ=0
    g6: Circle CenterX=24 CenterY=-64 CenterZ=0 NormalX=0 NormalY=0 NormalZ=1 AngleXU=0 Radius=2
  constraints (16):
    c: Coincident(g0,g-3)
    c: PointOnObject(g0,g-3)
    c: Angle(g0) = 3.14159
    c: Horizontal(g1)
    c: PointOnObject(g0,g1)
    c: Coincident(g2,g0)
    c: Coincident(g2,g0)
    c: Parallel(g2,g-4)
    c: Coincident(g-4,g3)
    c: Coincident(g3,g0)
    c: Coincident(g3,g4)
    c: Coincident(g4,g-4)
    c: Coincident(g4,g5)
    c: Coincident(g5,g0)
    c: Coincident(g6,g0)
    c: Radius(g6) = 2
FEATURE [PartDesign::Pad] Pad012013  label="q2_joint"
  BaseFeature = -> Pad012012
  Length = 3.5
  Length2 = 100
  Placement = pos=(0,6.2,0) rot=(0,0.707107,0.707107;3.14159rad)
  Profile = -> Sketch072
  Refine = true
  Type = 0
FEATURE [Sketcher::SketchObject] Sketch077  label="trajectory"
  ExternalGeometry = -> [Pad012013]
  MapMode = 5
  Placement = pos=(6e-16,11.95,-5.8e-15) rot=(0,0.707107,0.707107;3.14159rad)
  Support = -> [Pad012013]
  sketch-geometry (8):
    g0: GeomPoint X=42.3808 Y=74.6356 Z=0
    g1-g4: Circle [constr] x4 (B-spline internal-alignment scaffolding for g5; pole/knot coordinates omitted)
    g5: BSplineCurve PolesCount=4 KnotsCount=2 Degree=3 IsPeriodic=0
    g6: GeomPoint [constr] X=42.3808 Y=74.6356 Z=0
    g7: GeomPoint [constr] X=64.6677 Y=0 Z=0
  constraints (10):
    c: PointOnObject(g0,g-3)
    c: Coincident(g1,g0)
    c: Radius(g1) = 4
    c: Equal(g1,g2)
    c: Equal(g1,g3)
    c: Equal(g1,g4)
    c: PointOnObject(g4,g-1)
    c: InternalAlignment(g1-g4 -> g5) x4
    c: InternalAlignment(g6,g5)
    c: InternalAlignment(g7,g5)
FEATURE [Sketcher::SketchObject] Sketch078  label="q2-leg_union_section"
  ExternalGeometry = -> [Pad012013]
  MapMode = 5
  Placement = pos=(-64.1038,6.2,37.0103) rot=(0,-1,0;1.0472rad)
  Support = -> [Pad012013]
  sketch-geometry (4):
    g0: LineSegment StartX=49.1756 StartY=5.75 StartZ=0 EndX=49.1756 EndY=-32.25 EndZ=0
    g1: LineSegment StartX=49.1756 StartY=-32.25 StartZ=0 EndX=37.6756 EndY=-32.25 EndZ=0
    g2: LineSegment StartX=37.6756 StartY=-32.25 StartZ=0 EndX=37.6756 EndY=5.75 EndZ=0
    g3: LineSegment StartX=37.6756 StartY=5.75 StartZ=0 EndX=49.1756 EndY=5.75 EndZ=0
  constraints (8):
    c: Coincident(g-6,g0)
    c: Coincident(g0,g-6)
    c: Coincident(g0,g1)
    c: Coincident(g1,g-5)
    c: Coincident(g-5,g2)
    c: Coincident(g2,g-4)
    c: Coincident(g2,g3)
    c: Coincident(g3,g0)
FEATURE [Sketcher::SketchObject] Sketch079  label="q2-bone-touch_section"
  ExternalGeometry = -> [Sketch077,Pad012013]
  MapMode = 5
  Support = -> [XY_Plane018]
  sketch-geometry (7):
    g0: LineSegment StartX=-66.1677 StartY=-4.55 StartZ=0 EndX=-63.1677 EndY=-4.55 EndZ=0
    g1: LineSegment StartX=-63.1677 StartY=-4.55 StartZ=0 EndX=-63.1677 EndY=-9.55 EndZ=0
    g2: LineSegment StartX=-63.1677 StartY=-9.55 StartZ=0 EndX=-66.1677 EndY=-9.55 EndZ=0
    g3: LineSegment StartX=-66.1677 StartY=-9.55 StartZ=0 EndX=-66.1677 EndY=-4.55 EndZ=0
    g4: GeomPoint X=-45.266 Y=-7.05 Z=0
    g5: GeomPoint X=-63.1677 Y=-7.05 Z=0
    g6: GeomPoint X=-64.6677 Y=-4.55 Z=0
  constraints (18):
    c: Coincident(g0,g1)
    c: Coincident(g1,g2)
    c: Coincident(g2,g3)
    c: Coincident(g3,g0)
    c: Horizontal(g0)
    c: Horizontal(g2)
    c: Vertical(g1)
    c: Vertical(g3)
    c: PointOnObject(g4,g-4)
    c: Symmetric(g-4,g-4,g4)
    c: PointOnObject(g5,g1)
    c: Symmetric(g0,g1,g5)
    c: Horizontal(g5,g4)
    c: PointOnObject(g6,g0)
    c: Symmetric(g0,g0,g6)
    c: Vertical(g6,g-3)
    c: DistanceX(g2,g2) = 3
    c: DistanceY(g3,g3) = 5
FEATURE [PartDesign::AdditivePipe] AdditivePipe
  AuxilleryCurvelinear = true
  AuxillerySpineTangent = false
  BaseFeature = -> Pad012013
  Binormal = (0,0,0)
  Mode = 0
  Placement = pos=(0,6.2,0) rot=(0,0.707107,0.707107;3.14159rad)
  Profile = -> Sketch078
  Refine = true
  Sections = -> [Sketch079]
  Spine = -> Sketch077
  SpineTangent = false
  Transformation = 1
  Transition = 0
FEATURE [PartDesign::Body] Body011  label="Q2-Leg-joint"
  Group = -> [Sketch066,Pad012010,Sketch067,Pad012011,Sketch068,Sketch069,Pocket003058,Sketch070,Pocket003059,Sketch071,Pad012012,Sketch072,Pad012013,Sketch077,Sketch078,Sketch079,AdditivePipe]
  Origin = -> Origin018
  Tip = -> AdditivePipe
FEATURE [PartDesign::FeatureBase] Clone037  label="moved_aux_design_base"
  Placement = pos=(56.5,-17.5,30) rot=(0,0,1;0rad)
FEATURE [PartDesign::Body] Clone037Body
  Group = -> [Clone037]
  Origin = -> Origin020
  Tip = -> Clone037
FEATURE [PartDesign::Body] Clone036Body
  Origin = -> Origin021
FEATURE [App::Part] Part007  label="aux-base-leg-design"
  Group = -> [Clone037Body,Clone036Body]
  License = CC BY 3.0
  LicenseURL = http://creativecommons.org/licenses/by/3.0/
  Origin = -> Origin019
FEATURE [App::DocumentObjectGroup] Grupo002  label="aux"
  Group = -> [Grupo006,Grupo020,Grupo026,Grupo035,Box,Box001,Part__Feature1035,Part007]
FEATURE [Part::Feature] Fusion007055  label="Servo-sg90-final016"
  Placement = pos=(0,-16.6,0) rot=(0,0,1;0rad)
  shape: bbox 11.8 x 32.4 x 29.9 mm, 77 faces (baked)
FEATURE [Part::Feature] Pocket003060  label="Final-1-arm-horn014"
  Placement = pos=(0,0,32) rot=(0.707107,-0.707107,0;3.14159rad)
  shape: bbox 8 x 22.5 x 5 mm, 19 faces (baked)
FEATURE [Part::MultiFuse] Fusion007054  label="q1-aux-servo003"
  Placement = pos=(0,0,17.25) rot=(0,0,1;0rad)
  Refine = true
  Shapes = -> [Pocket003060,Fusion007055]
FEATURE [Sketcher::SketchObject] Sketch080  label="base_cylinder004"
  MapMode = 5
  Support = -> [XY_Plane023]
  sketch-geometry (2):
    g0: Circle CenterX=0 CenterY=0 CenterZ=0 NormalX=0 NormalY=0 NormalZ=1 AngleXU=0 Radius=3.75
    g1: Circle CenterX=0 CenterY=0 CenterZ=0 NormalX=0 NormalY=0 NormalZ=1 AngleXU=0 Radius=5.75
  constraints (4):
    c: Coincident(g0,g-1)
    c: Radius(g0) = 3.75
    c: Coincident(g1,g-1)
    c: Radius(g1) = 5.75
FEATURE [PartDesign::Pad] Pad012014  label="low_base003"
  Length = 2.25
  Length2 = 100
  Profile = -> Sketch080
  Refine = true
  Type = 0
FEATURE [Part::Feature] Fusion007056  label="Servo-sg90-final017"
  Placement = pos=(0,-16.6,0) rot=(0,0,1;0rad)
  shape: bbox 11.8 x 32.4 x 29.9 mm, 77 faces (baked)
FEATURE [Part::Feature] Pocket003061  label="Final-1-arm-horn015"
  Placement = pos=(0,0,32) rot=(0.707107,0.707107,0;3.14159rad)
  shape: bbox 8 x 22.5 x 5 mm, 19 faces (baked)
FEATURE [Part::MultiFuse] Fusion007053  label="q2-aux-servo003"
  Placement = pos=(-24,-20.5,64) rot=(-0.377964,0.654654,0.654654;2.41885rad)
  Refine = true
  Shapes = -> [Fusion007056,Pocket003061]
FEATURE [Sketcher::SketchObject] Sketch082  label="basic_base004"
  MapMode = 5
  Placement = pos=(0,0,2.25) rot=(0,0,1;0rad)
  Support = -> [Pad012014]
  sketch-geometry (6):
    g0: LineSegment StartX=0 StartY=5.71563 StartZ=0 EndX=-20.5 EndY=5.71563 EndZ=0
    g1: LineSegment StartX=1.86762e-06 StartY=-5.71497 StartZ=0 EndX=-20.5 EndY=-5.71497 EndZ=0
    g2: LineSegment StartX=-20.5 StartY=5.71563 StartZ=0 EndX=-20.5 EndY=-5.71497 EndZ=0
    g3: LineSegment StartX=0 StartY=5.71563 StartZ=0 EndX=5.71497 EndY=5.71563 EndZ=0
    g4: LineSegment StartX=5.71497 StartY=5.71563 StartZ=0 EndX=5.71497 EndY=0 EndZ=0
    g5: ArcOfCircle CenterX=0 CenterY=0 CenterZ=0 NormalX=0 NormalY=0 NormalZ=1 AngleXU=0 Radius=5.71497 StartAngle=4.71239 EndAngle=6.28319
  constraints (14):
    c: PointOnObject(g0,g-2)
    c: Horizontal(g0)
    c: DistanceX(g0,g0) = 20.5
    c: Coincident(g2,g0)
    c: Vertical(g2)
    c: Coincident(g1,g2)
    c: Coincident(g0,g3)
    c: Horizontal(g3)
    c: Coincident(g4,g3)
    c: PointOnObject(g4,g-1)
    c: Vertical(g4)
    c: Coincident(g5,g-1)
    c: Coincident(g5,g1)
    c: Coincident(g5,g4)
FEATURE [PartDesign::Pad] Pad012015  label="q1_basic_base003"
  BaseFeature = -> Pad012014
  Length = 3.5
  Length2 = 100
  Profile = -> Sketch082
  Refine = true
  Type = 0
FEATURE [Sketcher::SketchObject] Sketch081  label="q1_base_horn003"
  MapMode = 5
  Placement = pos=(0,0,5.75) rot=(0,0,1;0rad)
  Support = -> [Pad012015]
  sketch-geometry (7):
    g0: LineSegment StartX=-1.25 StartY=3.53553 StartZ=0 EndX=-17 EndY=1.74295 EndZ=0
    g1: ArcOfCircle CenterX=-17 CenterY=0 CenterZ=0 NormalX=0 NormalY=0 NormalZ=1 AngleXU=0 Radius=1.74295 StartAngle=1.5708 EndAngle=3.14159
    g2: LineSegment [constr] StartX=-18.743 StartY=0 StartZ=0 EndX=0 EndY=0 EndZ=0
    g3: ArcOfCircle CenterX=0 CenterY=0 CenterZ=0 NormalX=0 NormalY=0 NormalZ=1 AngleXU=0 Radius=3.75 StartAngle=0 EndAngle=1.91063
    g4: LineSegment StartX=-1.25 StartY=-3.53553 StartZ=0 EndX=-17 EndY=-1.74295 EndZ=0
    g5: ArcOfCircle CenterX=-17 CenterY=-1e-12 CenterZ=0 NormalX=0 NormalY=0 NormalZ=1 AngleXU=0 Radius=1.74295 StartAngle=3.14159 EndAngle=4.71239
    g6: ArcOfCircle CenterX=0 CenterY=0 CenterZ=0 NormalX=0 NormalY=0 NormalZ=1 AngleXU=0 Radius=3.75 StartAngle=4.37255 EndAngle=6.28319
  constraints (11):
    c: PointOnObject(g1,g-1)
    c: Coincident(g1,g0)
    c: PointOnObject(g1,g-1)
    c: Coincident(g1,g2)
    c: Coincident(g3,g-1)
    c: Radius(g3) = 3.75
    c: Coincident(g3,g0)
    c: DistanceX(g0,g3) = 5
    c: Coincident(g5,g4)
    c: Radius(g6) = 3.75
    c: Coincident(g6,g4)
FEATURE [PartDesign::Pocket] Pocket003062  label="q1_basic_horn003"
  BaseFeature = -> Pad012015
  Length = 2.65
  Length2 = 100
  Profile = -> Sketch081
  Refine = true
  Type = 0
FEATURE [Sketcher::SketchObject] Sketch083  label="horn_holes004"
  MapMode = 5
  Placement = pos=(0,0,3.1) rot=(0,0,1;0rad)
  Support = -> [Pocket003062]
  sketch-geometry (10):
    g0: Circle CenterX=0 CenterY=0 CenterZ=0 NormalX=0 NormalY=0 NormalZ=1 AngleXU=0 Radius=3.75
    g1: Circle CenterX=-14.5 CenterY=0 CenterZ=0 NormalX=0 NormalY=0 NormalZ=1 AngleXU=0 Radius=0.75
    g2: Circle CenterX=-12.5 CenterY=0 CenterZ=0 NormalX=0 NormalY=0 NormalZ=1 AngleXU=0 Radius=0.75
    g3: LineSegment [constr] StartX=-14.5 StartY=0 StartZ=0 EndX=-12.5 EndY=0 EndZ=0
    g4: Circle CenterX=-10.5 CenterY=0 CenterZ=0 NormalX=0 NormalY=0 NormalZ=1 AngleXU=0 Radius=0.75
    g5: LineSegment [constr] StartX=-12.5 StartY=0 StartZ=0 EndX=-10.5 EndY=0 EndZ=0
    g6: Circle CenterX=-8.5 CenterY=0 CenterZ=0 NormalX=0 NormalY=0 NormalZ=1 AngleXU=0 Radius=0.75
    g7: LineSegment [constr] StartX=-10.5 StartY=0 StartZ=0 EndX=-8.5 EndY=0 EndZ=0
    g8: Circle CenterX=-6.5 CenterY=0 CenterZ=0 NormalX=0 NormalY=0 NormalZ=1 AngleXU=0 Radius=0.75
    g9: LineSegment [constr] StartX=-8.5 StartY=0 StartZ=0 EndX=-6.5 EndY=0 EndZ=0
  constraints (25):
    c: Coincident(g0,g-1)
    c: Radius(g1) = 0.75
    c: Radius(g0) = 3.75
    c: Radius(g2) = 0.75
    c: Coincident(g1,g3)
    c: Coincident(g2,g3)
    c: Distance(g3) = 2
    c: Angle(g3) = 0
    c: Radius(g4) = 0.75
    c: Coincident(g2,g5)
    c: Coincident(g4,g5)
    c: Equal(g3,g5)
    c: Parallel(g5,g3)
    c: Radius(g6) = 0.75
    c: Coincident(g4,g7)
    c: Coincident(g6,g7)
    c: Equal(g3,g7)
    c: Parallel(g7,g3)
    c: Radius(g8) = 0.75
    c: Coincident(g6,g9)
    c: Coincident(g8,g9)
    c: Equal(g3,g9)
    c: Parallel(g9,g3)
    c: PointOnObject(g2,g-1)
    c: DistanceX(g8,g-1) = 6.5
FEATURE [PartDesign::Pocket] Pocket003063  label="q1_basic_horn_shape003"
  BaseFeature = -> Pocket003062
  Length = 5
  Length2 = 100
  Profile = -> Sketch083
  Refine = true
  Type = 0
FEATURE [Sketcher::SketchObject] Sketch084  label="q2-base001"
  ExternalGeometry = -> [Pocket003063]
  MapMode = 5
  Placement = pos=(-20.5,0,0) rot=(0.57735,-0.57735,-0.57735;2.0944rad)
  Support = -> [Pocket003063]
  sketch-geometry (6):
    g0: LineSegment StartX=-5.71563 StartY=2.25 StartZ=0 EndX=-11.6041 EndY=2.25 EndZ=0
    g1: LineSegment StartX=-11.6041 StartY=2.25 StartZ=0 EndX=-38.6752 EndY=17.8795 EndZ=0
    g2: LineSegment StartX=-11.6626 StartY=5.74787 StartZ=0 EndX=-37.1752 EndY=20.4776 EndZ=0
    g3: LineSegment StartX=-37.1752 StartY=20.4776 StartZ=0 EndX=-38.6752 EndY=17.8795 EndZ=0
    g4: LineSegment StartX=-5.71563 StartY=5.74787 StartZ=0 EndX=-5.71563 EndY=2.25 EndZ=0
    g5: LineSegment StartX=-11.6626 StartY=5.74787 StartZ=0 EndX=-5.71563 EndY=5.74787 EndZ=0
  constraints (13):
    c: Coincident(g3,g2)
    c: Coincident(g3,g1)
    c: Perpendicular(g3,g1)
    c: Coincident(g0,g-3)
    c: Parallel(g1,g2)
    c: Coincident(g4,g0)
    c: Perpendicular(g4,g0)
    c: Distance(g1,g2) = 3
    c: Angle(g0,g1) = 2.61799
    c: Coincident(g0,g1)
    c: Coincident(g2,g5)
    c: Coincident(g5,g4)
    c: Horizontal(g5)
FEATURE [PartDesign::Pad] Pad012016  label="q2-bed-base001"
  BaseFeature = -> Pocket003063
  Length = 26.215
  Length2 = 100
  Profile = -> Sketch084
  Refine = true
  Reversed = true
  Type = 0
FEATURE [Sketcher::SketchObject] Sketch085  label="q2-corner-hole002"
  MapMode = 5
  Placement = pos=(0,0,5.74787) rot=(0,0,1;0rad)
  Support = -> [Pad012016]
  sketch-geometry (4):
    g0: LineSegment StartX=-1.62396 StartY=12 StartZ=0 EndX=-5 EndY=12 EndZ=0
    g1: LineSegment StartX=-5 StartY=12 StartZ=0 EndX=-5 EndY=6.68085 EndZ=0
    g2: LineSegment StartX=-5 StartY=6.68085 StartZ=0 EndX=-1.62396 EndY=6.68085 EndZ=0
    g3: LineSegment StartX=-1.62396 StartY=6.68085 StartZ=0 EndX=-1.62396 EndY=12 EndZ=0
  constraints (8):
    c: Coincident(g0,g1)
    c: Coincident(g1,g2)
    c: Coincident(g2,g3)
    c: Coincident(g3,g0)
    c: Horizontal(g0)
    c: Horizontal(g2)
    c: Vertical(g1)
    c: Vertical(g3)
FEATURE [PartDesign::Pocket] Pocket003064  label="q2-corner-hole003"
  BaseFeature = -> Pad012016
  Length = 2
  Length2 = 100
  Profile = -> Sketch085
  Refine = true
  Type = 0
FEATURE [Sketcher::SketchObject] Sketch094  label="base_cylinder005"
  MapMode = 5
  Placement = pos=(0,6.2,0) rot=(0,0.707107,0.707107;3.14159rad)
  sketch-geometry (2):
    g0: Circle CenterX=24 CenterY=64 CenterZ=0 NormalX=0 NormalY=0 NormalZ=1 AngleXU=0 Radius=3.75
    g1: Circle CenterX=24 CenterY=64 CenterZ=0 NormalX=0 NormalY=0 NormalZ=1 AngleXU=0 Radius=5.75
  constraints (3):
    c: Radius(g0) = 3.75
    c: Radius(g1) = 5.75
    c: Coincident(g1,g0)
FEATURE [PartDesign::Pad] Pad012021  label="q2_base_cylinder001"
  Length = 2.25
  Length2 = 100
  Placement = pos=(0,6.2,0) rot=(0,0.707107,0.707107;3.14159rad)
  Profile = -> Sketch094
  Refine = true
  Type = 0
FEATURE [Sketcher::SketchObject] Sketch095  label="q2_base001"
  ExternalGeometry = -> [Pad012021]
  MapMode = 5
  Placement = pos=(2e-16,8.45,-9e-16) rot=(0,0.707107,0.707107;3.14159rad)
  Support = -> [Pad012021]
  sketch-geometry (6):
    g0: ArcOfCircle CenterX=24 CenterY=64 CenterZ=0 NormalX=0 NormalY=0 NormalZ=1 AngleXU=0 Radius=5.75 StartAngle=2.0944 EndAngle=5.23599
    g1: LineSegment [constr] StartX=12.5 StartY=64 StartZ=0 EndX=37 EndY=64 EndZ=0
    g2: LineSegment [constr] StartX=24 StartY=64 StartZ=0 EndX=21.125 EndY=68.9796 EndZ=0
    g3: LineSegment StartX=21.125 StartY=68.9796 StartZ=0 EndX=39.516 EndY=79.5977 EndZ=0
    g4: LineSegment StartX=39.516 StartY=79.5977 StartZ=0 EndX=45.266 EndY=69.6384 EndZ=0
    g5: LineSegment StartX=45.266 StartY=69.6384 StartZ=0 EndX=26.875 EndY=59.0204 EndZ=0
  constraints (14):
    c: Coincident(g0,g-3)
    c: PointOnObject(g0,g-3)
    c: Angle(g0) = 3.14159
    c: Horizontal(g1)
    c: PointOnObject(g0,g1)
    c: Coincident(g2,g0)
    c: Coincident(g2,g0)
    c: Angle(g1,g2) = 2.0944
    c: Tangent(g0,g3) = 1.5708
    c: Coincident(g3,g4)
    c: Coincident(g4,g5)
    c: Coincident(g5,g0)
    c: Equal(g3,g5)
    c: Parallel(g3,g5)
FEATURE [PartDesign::Pad] Pad012022  label="q2_basic_base001"
  BaseFeature = -> Pad012021
  Length = 3.5
  Length2 = 100
  Placement = pos=(0,6.2,0) rot=(0,0.707107,0.707107;3.14159rad)
  Profile = -> Sketch095
  Refine = true
  Type = 0
FEATURE [Sketcher::SketchObject] Sketch096  label="AUX_q2_base_horn004"
  ExternalGeometry = -> [Pad012022]
  MapMode = 5
  Placement = pos=(-3e-15,11.95,-6e-15) rot=(0.186157,0.694747,0.694747;3.50969rad)
  sketch-geometry (5):
    g0: LineSegment StartX=54.0346 StartY=46.9656 StartZ=0 EndX=69.7804 EndY=45.1656 EndZ=0
    g1: ArcOfCircle CenterX=69.7804 CenterY=43.4256 CenterZ=0 NormalX=0 NormalY=0 NormalZ=1 AngleXU=0 Radius=1.74 StartAngle=0 EndAngle=1.5708
    g2: LineSegment [constr] StartX=71.5204 StartY=43.4256 StartZ=0 EndX=49.0304 EndY=43.4256 EndZ=0
    g3: ArcOfCircle CenterX=52.7846 CenterY=43.4256 CenterZ=0 NormalX=0 NormalY=0 NormalZ=1 AngleXU=0 Radius=3.75421 StartAngle=1.23136 EndAngle=3.14159
    g4: LineSegment [constr] StartX=52.7846 StartY=49.1756 StartZ=0 EndX=52.7846 EndY=37.6756 EndZ=0
  constraints (16):
    c: Coincident(g1,g0)
    c: Coincident(g1,g2)
    c: Coincident(g3,g0)
    c: Radius(g1) = 1.74
    c: PointOnObject(g1,g2)
    c: Coincident(g2,g3)
    c: PointOnObject(g3,g2)
    c: DistanceX(g2,g2) = 22.49
    c: DistanceY(g1,g0) = 1.74
    c: DistanceX(g3,g0) = 1.25
    c: DistanceY(g3,g0) = 3.54
    c: Horizontal(g2)
    c: Coincident(g4,g-3)
    c: Coincident(g4,g-4)
    c: PointOnObject(g3,g4)
    c: Symmetric(g4,g4,g3)
FEATURE [Sketcher::SketchObject] Sketch097  label="horn_shape002"
  ExternalGeometry = -> [Sketch096]
  MapMode = 5
  Placement = pos=(6e-16,11.95,-5.8e-15) rot=(0,0.707107,0.707107;3.14159rad)
  Support = -> [Pad012022]
  sketch-geometry (7):
    g0: LineSegment [constr] StartX=20.7488 StartY=62.1229 StartZ=0 EndX=40.2257 EndY=73.3679 EndZ=0
    g1: ArcOfCircle CenterX=24 CenterY=64 CenterZ=0 NormalX=0 NormalY=0 NormalZ=1 AngleXU=0 Radius=3.75421 StartAngle=1.75495 EndAngle=3.66519
    g2: ArcOfCircle CenterX=38.7188 CenterY=72.4979 CenterZ=0 NormalX=0 NormalY=0 NormalZ=1 AngleXU=0 Radius=1.74 StartAngle=0.523599 EndAngle=2.0944
    g3: LineSegment StartX=23.3125 StartY=67.6907 StartZ=0 EndX=37.8488 EndY=74.0048 EndZ=0
    g4: ArcOfCircle CenterX=24 CenterY=64 CenterZ=0 NormalX=0 NormalY=0 NormalZ=1 AngleXU=0 Radius=3.75421 StartAngle=3.66519 EndAngle=5.57543
    g5: ArcOfCircle CenterX=38.7188 CenterY=72.4979 CenterZ=0 NormalX=0 NormalY=0 NormalZ=1 AngleXU=0 Radius=1.74 StartAngle=5.23599 EndAngle=6.80678
    g6: LineSegment StartX=26.8525 StartY=61.5593 StartZ=0 EndX=39.5888 EndY=70.991 EndZ=0
  constraints (16):
    c: Coincident(g0,g-5)
    c: Coincident(g0,g-4)
    c: Coincident(g1,g-5)
    c: Coincident(g1,g-5)
    c: Coincident(g1,g0)
    c: Coincident(g2,g-4)
    c: Coincident(g2,g0)
    c: Coincident(g2,g-4)
    c: Coincident(g3,g1)
    c: Coincident(g3,g2)
    c: Coincident(g6,g4)
    c: Coincident(g6,g5)
    c: Coincident(g0,g4)
    c: Coincident(g1,g4)
    c: Coincident(g2,g5)
    c: Coincident(g0,g5)
FEATURE [PartDesign::Pocket] Pocket003068  label="horn_shape003"
  BaseFeature = -> Pad012022
  Length = 2.65
  Length2 = 100
  Placement = pos=(0,6.2,0) rot=(0,0.707107,0.707107;3.14159rad)
  Profile = -> Sketch097
  Refine = true
  Type = 0
FEATURE [Sketcher::SketchObject] Sketch098  label="horn_holes005"
  ExternalGeometry = -> [Pocket003068]
  MapMode = 5
  Placement = pos=(2e-16,9.3,-5.3e-15) rot=(0,0.707107,0.707107;3.14159rad)
  Support = -> [Pocket003068]
  sketch-geometry (16):
    g0: Circle CenterX=24 CenterY=64 CenterZ=0 NormalX=0 NormalY=0 NormalZ=1 AngleXU=0 Radius=3.75
    g1: Circle CenterX=-14.6952 CenterY=0 CenterZ=0 NormalX=0 NormalY=0 NormalZ=1 AngleXU=0 Radius=0.75
    g2: Circle CenterX=-12.6952 CenterY=0 CenterZ=0 NormalX=0 NormalY=0 NormalZ=1 AngleXU=0 Radius=0.75
    g3: LineSegment [constr] StartX=-14.6952 StartY=0 StartZ=0 EndX=-12.6952 EndY=0 EndZ=0
    g4: Circle CenterX=-10.6952 CenterY=0 CenterZ=0 NormalX=0 NormalY=0 NormalZ=1 AngleXU=0 Radius=0.75
    g5: LineSegment [constr] StartX=-12.6952 StartY=0 StartZ=0 EndX=-10.6952 EndY=0 EndZ=0
    g6: Circle CenterX=-8.69518 CenterY=0 CenterZ=0 NormalX=0 NormalY=0 NormalZ=1 AngleXU=0 Radius=0.75
    g7: LineSegment [constr] StartX=-10.6952 StartY=0 StartZ=0 EndX=-8.69518 EndY=0 EndZ=0
    g8: Circle CenterX=-6.69518 CenterY=0 CenterZ=0 NormalX=0 NormalY=0 NormalZ=1 AngleXU=0 Radius=0.75
    g9: LineSegment [constr] StartX=-8.69518 StartY=0 StartZ=0 EndX=-6.69518 EndY=0 EndZ=0
    g10: LineSegment [constr] StartX=24 StartY=64 StartZ=0 EndX=43.3449 EndY=75.1688 EndZ=0
    g11: Circle CenterX=29.6292 CenterY=67.25 CenterZ=0 NormalX=0 NormalY=0 NormalZ=1 AngleXU=0 Radius=0.75
    g12: Circle CenterX=31.3612 CenterY=68.25 CenterZ=0 NormalX=0 NormalY=0 NormalZ=1 AngleXU=0 Radius=0.75
    g13: Circle CenterX=33.0933 CenterY=69.25 CenterZ=0 NormalX=0 NormalY=0 NormalZ=1 AngleXU=0 Radius=0.75
    g14: Circle CenterX=34.8253 CenterY=70.25 CenterZ=0 NormalX=0 NormalY=0 NormalZ=1 AngleXU=0 Radius=0.75
    g15: Circle CenterX=36.5574 CenterY=71.25 CenterZ=0 NormalX=0 NormalY=0 NormalZ=1 AngleXU=0 Radius=0.75
  constraints (41):
    c: Radius(g1) = 0.75
    c: Radius(g0) = 3.75
    c: Radius(g2) = 0.75
    c: Coincident(g1,g3)
    c: Coincident(g2,g3)
    c: Distance(g3) = 2
    c: Angle(g3) = 0
    c: Radius(g4) = 0.75
    c: Coincident(g2,g5)
    c: Coincident(g4,g5)
    c: Equal(g3,g5)
    c: Radius(g6) = 0.75
    c: Coincident(g4,g7)
    c: Coincident(g6,g7)
    c: Equal(g3,g7)
    c: Radius(g8) = 0.75
    c: Coincident(g6,g9)
    c: Coincident(g8,g9)
    c: Equal(g3,g9)
    c: Parallel(g9,g3)
    c: Parallel(g9,g7)
    c: Parallel(g7,g5)
    c: Coincident(g10,g0)
    c: Angle(g10) = 0.523599
    c: Radius(g11) = 0.75
    c: Distance(g0,g11) = 6.5
    c: PointOnObject(g11,g10)
    c: Equal(g11,g12) = 0.75
    c: PointOnObject(g12,g10)
    c: DistanceX(g0) = 24
    c: DistanceY(g0) = 64
    c: Distance(g11,g12) = 2
    c: Equal(g11,g13) = 0.75
    c: PointOnObject(g13,g10)
    c: Equal(g11,g14) = 0.75
    c: PointOnObject(g14,g10)
    c: Equal(g11,g15) = 0.75
    c: PointOnObject(g15,g10)
    c: Distance(g12,g13) = 2
    c: Distance(g13,g14) = 2
    c: Distance(g14,g15) = 2
FEATURE [PartDesign::Pocket] Pocket003069  label="basic_horn_union001"
  BaseFeature = -> Pocket003068
  Length = 5
  Length2 = 100
  Placement = pos=(0,6.2,0) rot=(0,0.707107,0.707107;3.14159rad)
  Profile = -> Sketch098
  Refine = true
  Type = 0
FEATURE [Sketcher::SketchObject] Sketch099  label="q2_bridge002"
  ExternalGeometry = -> [Pocket003069]
  MapMode = 5
  Placement = pos=(2e-16,8.45,-2.3e-15) rot=(0,-0.707107,0.707107;3.14159rad)
  Support = -> [Pocket003069]
  sketch-geometry (4):
    g0: LineSegment StartX=39.516 StartY=-79.5977 StartZ=0 EndX=45.266 EndY=-69.6384 EndZ=0
    g1: LineSegment StartX=45.266 StartY=-69.6384 StartZ=0 EndX=40.9358 EndY=-67.1384 EndZ=0
    g2: LineSegment StartX=39.516 StartY=-79.5977 StartZ=0 EndX=35.1858 EndY=-77.0977 EndZ=0
    g3: ArcOfCircle CenterX=24.5001 CenterY=-64.2888 CenterZ=0 NormalX=0 NormalY=0 NormalZ=1 AngleXU=0 Radius=16.6809 StartAngle=5.40766 EndAngle=6.11151
  constraints (10):
    c: Coincident(g-5,g0)
    c: Coincident(g0,g-5)
    c: Coincident(g0,g1)
    c: PointOnObject(g1,g-3)
    c: Coincident(g0,g2)
    c: PointOnObject(g2,g-4)
    c: Distance(g2) = 5
    c: Equal(g2,g1)
    c: Coincident(g3,g1)
    c: Coincident(g3,g2)
FEATURE [PartDesign::Pad] Pad012023  label="q2_bridge003"
  BaseFeature = -> Pocket003069
  Length = 31
  Length2 = 100
  Placement = pos=(0,6.2,0) rot=(0,0.707107,0.707107;3.14159rad)
  Profile = -> Sketch099
  Refine = true
  Type = 0
FEATURE [Sketcher::SketchObject] Sketch100  label="q2_back_union001"
  ExternalGeometry = -> [Pad012021,Sketch095]
  MapMode = 5
  Placement = pos=(-2.3e-15,-22.55,3.83e-14) rot=(0,-0.707107,0.707107;3.14159rad)
  Support = -> [Pad012023]
  expr: Constraints[2] = Sketch067.Constraints[2]
  sketch-geometry (7):
    g0: ArcOfCircle CenterX=24 CenterY=-64 CenterZ=0 NormalX=0 NormalY=0 NormalZ=1 AngleXU=0 Radius=5.75 StartAngle=1.0472 EndAngle=4.18879
    g1: LineSegment [constr] StartX=12.5 StartY=-64 StartZ=0 EndX=37 EndY=-64 EndZ=0
    g2: LineSegment [constr] StartX=24 StartY=-64 StartZ=0 EndX=26.875 EndY=-59.0204 EndZ=0
    g3: LineSegment StartX=45.266 StartY=-69.6384 StartZ=0 EndX=26.875 EndY=-59.0204 EndZ=0
    g4: LineSegment StartX=45.266 StartY=-69.6384 StartZ=0 EndX=39.516 EndY=-79.5977 EndZ=0
    g5: LineSegment StartX=39.516 StartY=-79.5977 StartZ=0 EndX=21.125 EndY=-68.9796 EndZ=0
    g6: Circle CenterX=24 CenterY=-64 CenterZ=0 NormalX=0 NormalY=0 NormalZ=1 AngleXU=0 Radius=2
  constraints (16):
    c: Coincident(g0,g-3)
    c: PointOnObject(g0,g-3)
    c: Angle(g0) = 3.14159
    c: Horizontal(g1)
    c: PointOnObject(g0,g1)
    c: Coincident(g2,g0)
    c: Coincident(g2,g0)
    c: Parallel(g2,g-4)
    c: Coincident(g-4,g3)
    c: Coincident(g3,g0)
    c: Coincident(g3,g4)
    c: Coincident(g4,g-4)
    c: Coincident(g4,g5)
    c: Coincident(g5,g0)
    c: Coincident(g6,g0)
    c: Radius(g6) = 2
FEATURE [PartDesign::Pad] Pad012024  label="q2_joint001"
  BaseFeature = -> Pad012023
  Length = 3.5
  Length2 = 100
  Placement = pos=(0,6.2,0) rot=(0,0.707107,0.707107;3.14159rad)
  Profile = -> Sketch100
  Refine = true
  Type = 0
FEATURE [Sketcher::SketchObject] Sketch101  label="trajectory001"
  ExternalGeometry = -> [Pad012024]
  MapMode = 5
  Placement = pos=(6e-16,11.95,-5.8e-15) rot=(0,0.707107,0.707107;3.14159rad)
  Support = -> [Pad012024]
  sketch-geometry (8):
    g0: GeomPoint X=42.3808 Y=74.6356 Z=0
    g1-g4: Circle [constr] x4 (B-spline internal-alignment scaffolding for g5; pole/knot coordinates omitted)
    g5: BSplineCurve PolesCount=4 KnotsCount=2 Degree=3 IsPeriodic=0
    g6: GeomPoint [constr] X=42.3808 Y=74.6356 Z=0
    g7: GeomPoint [constr] X=64.6677 Y=0 Z=0
  constraints (10):
    c: PointOnObject(g0,g-3)
    c: Coincident(g1,g0)
    c: Radius(g1) = 4
    c: Equal(g1,g2)
    c: Equal(g1,g3)
    c: Equal(g1,g4)
    c: PointOnObject(g4,g-1)
    c: InternalAlignment(g1-g4 -> g5) x4
    c: InternalAlignment(g6,g5)
    c: InternalAlignment(g7,g5)
FEATURE [Sketcher::SketchObject] Sketch102  label="q2-leg_union_section001"
  ExternalGeometry = -> [Pad012024]
  MapMode = 5
  Placement = pos=(-64.1038,6.2,37.0103) rot=(0,-1,0;1.0472rad)
  Support = -> [Pad012024]
  sketch-geometry (4):
    g0: LineSegment StartX=49.1756 StartY=5.75 StartZ=0 EndX=49.1756 EndY=-32.25 EndZ=0
    g1: LineSegment StartX=49.1756 StartY=-32.25 StartZ=0 EndX=37.6756 EndY=-32.25 EndZ=0
    g2: LineSegment StartX=37.6756 StartY=-32.25 StartZ=0 EndX=37.6756 EndY=5.75 EndZ=0
    g3: LineSegment StartX=37.6756 StartY=5.75 StartZ=0 EndX=49.1756 EndY=5.75 EndZ=0
  constraints (8):
    c: Coincident(g-6,g0)
    c: Coincident(g0,g-6)
    c: Coincident(g0,g1)
    c: Coincident(g1,g-5)
    c: Coincident(g-5,g2)
    c: Coincident(g2,g-4)
    c: Coincident(g2,g3)
    c: Coincident(g3,g0)
FEATURE [Sketcher::SketchObject] Sketch103  label="q2-bone-touch_section001"
  ExternalGeometry = -> [Sketch101,Pad012024]
  MapMode = 5
  Support = -> [XY_Plane024]
  sketch-geometry (7):
    g0: LineSegment StartX=-66.1677 StartY=-4.55 StartZ=0 EndX=-63.1677 EndY=-4.55 EndZ=0
    g1: LineSegment StartX=-63.1677 StartY=-4.55 StartZ=0 EndX=-63.1677 EndY=-9.55 EndZ=0
    g2: LineSegment StartX=-63.1677 StartY=-9.55 StartZ=0 EndX=-66.1677 EndY=-9.55 EndZ=0
    g3: LineSegment StartX=-66.1677 StartY=-9.55 StartZ=0 EndX=-66.1677 EndY=-4.55 EndZ=0
    g4: GeomPoint X=-45.266 Y=-7.05 Z=0
    g5: GeomPoint X=-63.1677 Y=-7.05 Z=0
    g6: GeomPoint X=-64.6677 Y=-4.55 Z=0
  constraints (18):
    c: Coincident(g0,g1)
    c: Coincident(g1,g2)
    c: Coincident(g2,g3)
    c: Coincident(g3,g0)
    c: Horizontal(g0)
    c: Horizontal(g2)
    c: Vertical(g1)
    c: Vertical(g3)
    c: PointOnObject(g4,g-4)
    c: Symmetric(g-4,g-4,g4)
    c: PointOnObject(g5,g1)
    c: Symmetric(g0,g1,g5)
    c: Horizontal(g5,g4)
    c: PointOnObject(g6,g0)
    c: Symmetric(g0,g0,g6)
    c: Vertical(g6,g-3)
    c: DistanceX(g2,g2) = 3
    c: DistanceY(g3,g3) = 5
FEATURE [PartDesign::AdditivePipe] AdditivePipe001
  AuxilleryCurvelinear = true
  AuxillerySpineTangent = false
  BaseFeature = -> Pad012024
  Binormal = (0,0,0)
  Mode = 0
  Placement = pos=(0,6.2,0) rot=(0,0.707107,0.707107;3.14159rad)
  Profile = -> Sketch102
  Refine = true
  Sections = -> [Sketch103]
  Spine = -> Sketch101
  SpineTangent = false
  Transformation = 1
  Transition = 0
FEATURE [PartDesign::Body] Body013  label="Q2-Leg-joint001"
  Group = -> [Sketch094,Pad012021,Sketch095,Pad012022,Sketch096,Sketch097,Pocket003068,Sketch098,Pocket003069,Sketch099,Pad012023,Sketch100,Pad012024,Sketch101,Sketch102,Sketch103,AdditivePipe001]
  Origin = -> Origin024
  Tip = -> AdditivePipe001
FEATURE [Part::Feature] Pocket003076  label="Final-1-arm-horn016"
  Placement = pos=(0,0,32) rot=(0.707107,0.707107,0;3.14159rad)
  shape: bbox 8 x 22.5 x 5 mm, 19 faces (baked)
FEATURE [Part::Feature] Fusion007059  label="Servo-sg90-final018"
  Placement = pos=(0,-16.6,0) rot=(0,0,1;0rad)
  shape: bbox 11.8 x 32.4 x 29.9 mm, 77 faces (baked)
FEATURE [Part::MultiFuse] Fusion007058  label="q2-aux-servo004"
  Placement = pos=(-24,-20.5,64) rot=(-0.377964,0.654654,0.654654;2.41885rad)
  Refine = true
  Shapes = -> [Fusion007059,Pocket003076]
FEATURE [Part::Feature] Fusion007060  label="Servo-sg90-final019"
  Placement = pos=(0,-16.6,0) rot=(0,0,1;0rad)
  shape: bbox 11.8 x 32.4 x 29.9 mm, 77 faces (baked)
FEATURE [Part::Feature] Pocket003078  label="Final-1-arm-horn017"
  Placement = pos=(0,0,32) rot=(0.707107,-0.707107,0;3.14159rad)
  shape: bbox 8 x 22.5 x 5 mm, 19 faces (baked)
FEATURE [Part::MultiFuse] Fusion007057  label="q1-aux-servo004"
  Placement = pos=(0,0,17.25) rot=(0,0,1;0rad)
  Refine = true
  Shapes = -> [Pocket003078,Fusion007060]
FEATURE [Sketcher::SketchObject] Sketch125  label="base_cylinder007"
  MapMode = 5
  Placement = pos=(0,6.2,0) rot=(0,0.707107,0.707107;3.14159rad)
  sketch-geometry (2):
    g0: Circle CenterX=24 CenterY=64 CenterZ=0 NormalX=0 NormalY=0 NormalZ=1 AngleXU=0 Radius=3.75
    g1: Circle CenterX=24 CenterY=64 CenterZ=0 NormalX=0 NormalY=0 NormalZ=1 AngleXU=0 Radius=5.75
  constraints (3):
    c: Radius(g0) = 3.75
    c: Radius(g1) = 5.75
    c: Coincident(g1,g0)
FEATURE [PartDesign::Pad] Pad012029  label="q2_base_cylinder003"
  Length = 2.25
  Length2 = 100
  Placement = pos=(0,6.2,0) rot=(0,0.707107,0.707107;3.14159rad)
  Profile = -> Sketch125
  Refine = true
  Type = 0
FEATURE [Sketcher::SketchObject] Sketch104  label="q2_base002"
  ExternalGeometry = -> [Pad012029]
  MapMode = 5
  Placement = pos=(2e-16,8.45,-9e-16) rot=(0,0.707107,0.707107;3.14159rad)
  Support = -> [Pad012029]
  sketch-geometry (6):
    g0: ArcOfCircle CenterX=24 CenterY=64 CenterZ=0 NormalX=0 NormalY=0 NormalZ=1 AngleXU=0 Radius=5.75 StartAngle=2.0944 EndAngle=5.23599
    g1: LineSegment [constr] StartX=12.5 StartY=64 StartZ=0 EndX=37 EndY=64 EndZ=0
    g2: LineSegment [constr] StartX=24 StartY=64 StartZ=0 EndX=21.125 EndY=68.9796 EndZ=0
    g3: LineSegment StartX=21.125 StartY=68.9796 StartZ=0 EndX=39.516 EndY=79.5977 EndZ=0
    g4: LineSegment StartX=39.516 StartY=79.5977 StartZ=0 EndX=45.266 EndY=69.6384 EndZ=0
    g5: LineSegment StartX=45.266 StartY=69.6384 StartZ=0 EndX=26.875 EndY=59.0204 EndZ=0
  constraints (14):
    c: Coincident(g0,g-3)
    c: PointOnObject(g0,g-3)
    c: Angle(g0) = 3.14159
    c: Horizontal(g1)
    c: PointOnObject(g0,g1)
    c: Coincident(g2,g0)
    c: Coincident(g2,g0)
    c: Angle(g1,g2) = 2.0944
    c: Tangent(g0,g3) = 1.5708
    c: Coincident(g3,g4)
    c: Coincident(g4,g5)
    c: Coincident(g5,g0)
    c: Equal(g3,g5)
    c: Parallel(g3,g5)
FEATURE [PartDesign::Pad] Pad012033  label="q2_basic_base002"
  BaseFeature = -> Pad012029
  Length = 3.5
  Length2 = 100
  Placement = pos=(0,6.2,0) rot=(0,0.707107,0.707107;3.14159rad)
  Profile = -> Sketch104
  Refine = true
  Type = 0
FEATURE [Sketcher::SketchObject] Sketch116  label="AUX_q2_base_horn005"
  ExternalGeometry = -> [Pad012033]
  MapMode = 5
  Placement = pos=(-3e-15,11.95,-6e-15) rot=(0.186157,0.694747,0.694747;3.50969rad)
  sketch-geometry (5):
    g0: LineSegment StartX=54.0346 StartY=46.9656 StartZ=0 EndX=69.7804 EndY=45.1656 EndZ=0
    g1: ArcOfCircle CenterX=69.7804 CenterY=43.4256 CenterZ=0 NormalX=0 NormalY=0 NormalZ=1 AngleXU=0 Radius=1.74 StartAngle=0 EndAngle=1.5708
    g2: LineSegment [constr] StartX=71.5204 StartY=43.4256 StartZ=0 EndX=49.0304 EndY=43.4256 EndZ=0
    g3: ArcOfCircle CenterX=52.7846 CenterY=43.4256 CenterZ=0 NormalX=0 NormalY=0 NormalZ=1 AngleXU=0 Radius=3.75421 StartAngle=1.23136 EndAngle=3.14159
    g4: LineSegment [constr] StartX=52.7846 StartY=49.1756 StartZ=0 EndX=52.7846 EndY=37.6756 EndZ=0
  constraints (16):
    c: Coincident(g1,g0)
    c: Coincident(g1,g2)
    c: Coincident(g3,g0)
    c: Radius(g1) = 1.74
    c: PointOnObject(g1,g2)
    c: Coincident(g2,g3)
    c: PointOnObject(g3,g2)
    c: DistanceX(g2,g2) = 22.49
    c: DistanceY(g1,g0) = 1.74
    c: DistanceX(g3,g0) = 1.25
    c: DistanceY(g3,g0) = 3.54
    c: Horizontal(g2)
    c: Coincident(g4,g-3)
    c: Coincident(g4,g-4)
    c: PointOnObject(g3,g4)
    c: Symmetric(g4,g4,g3)
FEATURE [Sketcher::SketchObject] Sketch121  label="horn_shape005"
  ExternalGeometry = -> [Sketch116]
  MapMode = 5
  Placement = pos=(6e-16,11.95,-5.8e-15) rot=(0,0.707107,0.707107;3.14159rad)
  Support = -> [Pad012033]
  sketch-geometry (7):
    g0: LineSegment [constr] StartX=20.7488 StartY=62.1229 StartZ=0 EndX=40.2257 EndY=73.3679 EndZ=0
    g1: ArcOfCircle CenterX=24 CenterY=64 CenterZ=0 NormalX=0 NormalY=0 NormalZ=1 AngleXU=0 Radius=3.75421 StartAngle=1.75495 EndAngle=3.66519
    g2: ArcOfCircle CenterX=38.7188 CenterY=72.4979 CenterZ=0 NormalX=0 NormalY=0 NormalZ=1 AngleXU=0 Radius=1.74 StartAngle=0.523599 EndAngle=2.0944
    g3: LineSegment StartX=23.3125 StartY=67.6907 StartZ=0 EndX=37.8488 EndY=74.0048 EndZ=0
    g4: ArcOfCircle CenterX=24 CenterY=64 CenterZ=0 NormalX=0 NormalY=0 NormalZ=1 AngleXU=0 Radius=3.75421 StartAngle=3.66519 EndAngle=5.57543
    g5: ArcOfCircle CenterX=38.7188 CenterY=72.4979 CenterZ=0 NormalX=0 NormalY=0 NormalZ=1 AngleXU=0 Radius=1.74 StartAngle=5.23599 EndAngle=6.80678
    g6: LineSegment StartX=26.8525 StartY=61.5593 StartZ=0 EndX=39.5888 EndY=70.991 EndZ=0
  constraints (16):
    c: Coincident(g0,g-5)
    c: Coincident(g0,g-4)
    c: Coincident(g1,g-5)
    c: Coincident(g1,g-5)
    c: Coincident(g1,g0)
    c: Coincident(g2,g-4)
    c: Coincident(g2,g0)
    c: Coincident(g2,g-4)
    c: Coincident(g3,g1)
    c: Coincident(g3,g2)
    c: Coincident(g6,g4)
    c: Coincident(g6,g5)
    c: Coincident(g0,g4)
    c: Coincident(g1,g4)
    c: Coincident(g2,g5)
    c: Coincident(g0,g5)
FEATURE [PartDesign::Pocket] Pocket003075  label="horn_shape004"
  BaseFeature = -> Pad012033
  Length = 2.65
  Length2 = 100
  Placement = pos=(0,6.2,0) rot=(0,0.707107,0.707107;3.14159rad)
  Profile = -> Sketch121
  Refine = true
  Type = 0
FEATURE [Sketcher::SketchObject] Sketch106  label="horn_holes006"
  ExternalGeometry = -> [Pocket003075]
  MapMode = 5
  Placement = pos=(2e-16,9.3,-5.3e-15) rot=(0,0.707107,0.707107;3.14159rad)
  Support = -> [Pocket003075]
  sketch-geometry (16):
    g0: Circle CenterX=24 CenterY=64 CenterZ=0 NormalX=0 NormalY=0 NormalZ=1 AngleXU=0 Radius=3.75
    g1: Circle CenterX=-14.6952 CenterY=0 CenterZ=0 NormalX=0 NormalY=0 NormalZ=1 AngleXU=0 Radius=0.75
    g2: Circle CenterX=-12.6952 CenterY=0 CenterZ=0 NormalX=0 NormalY=0 NormalZ=1 AngleXU=0 Radius=0.75
    g3: LineSegment [constr] StartX=-14.6952 StartY=0 StartZ=0 EndX=-12.6952 EndY=0 EndZ=0
    g4: Circle CenterX=-10.6952 CenterY=0 CenterZ=0 NormalX=0 NormalY=0 NormalZ=1 AngleXU=0 Radius=0.75
    g5: LineSegment [constr] StartX=-12.6952 StartY=0 StartZ=0 EndX=-10.6952 EndY=0 EndZ=0
    g6: Circle CenterX=-8.69518 CenterY=0 CenterZ=0 NormalX=0 NormalY=0 NormalZ=1 AngleXU=0 Radius=0.75
    g7: LineSegment [constr] StartX=-10.6952 StartY=0 StartZ=0 EndX=-8.69518 EndY=0 EndZ=0
    g8: Circle CenterX=-6.69518 CenterY=0 CenterZ=0 NormalX=0 NormalY=0 NormalZ=1 AngleXU=0 Radius=0.75
    g9: LineSegment [constr] StartX=-8.69518 StartY=0 StartZ=0 EndX=-6.69518 EndY=0 EndZ=0
    g10: LineSegment [constr] StartX=24 StartY=64 StartZ=0 EndX=43.3449 EndY=75.1688 EndZ=0
    g11: Circle CenterX=29.6292 CenterY=67.25 CenterZ=0 NormalX=0 NormalY=0 NormalZ=1 AngleXU=0 Radius=0.75
    g12: Circle CenterX=31.3612 CenterY=68.25 CenterZ=0 NormalX=0 NormalY=0 NormalZ=1 AngleXU=0 Radius=0.75
    g13: Circle CenterX=33.0933 CenterY=69.25 CenterZ=0 NormalX=0 NormalY=0 NormalZ=1 AngleXU=0 Radius=0.75
    g14: Circle CenterX=34.8253 CenterY=70.25 CenterZ=0 NormalX=0 NormalY=0 NormalZ=1 AngleXU=0 Radius=0.75
    g15: Circle CenterX=36.5574 CenterY=71.25 CenterZ=0 NormalX=0 NormalY=0 NormalZ=1 AngleXU=0 Radius=0.75
  constraints (41):
    c: Radius(g1) = 0.75
    c: Radius(g0) = 3.75
    c: Radius(g2) = 0.75
    c: Coincident(g1,g3)
    c: Coincident(g2,g3)
    c: Distance(g3) = 2
    c: Angle(g3) = 0
    c: Radius(g4) = 0.75
    c: Coincident(g2,g5)
    c: Coincident(g4,g5)
    c: Equal(g3,g5)
    c: Radius(g6) = 0.75
    c: Coincident(g4,g7)
    c: Coincident(g6,g7)
    c: Equal(g3,g7)
    c: Radius(g8) = 0.75
    c: Coincident(g6,g9)
    c: Coincident(g8,g9)
    c: Equal(g3,g9)
    c: Parallel(g9,g3)
    c: Parallel(g9,g7)
    c: Parallel(g7,g5)
    c: Coincident(g10,g0)
    c: Angle(g10) = 0.523599
    c: Radius(g11) = 0.75
    c: Distance(g0,g11) = 6.5
    c: PointOnObject(g11,g10)
    c: Equal(g11,g12) = 0.75
    c: PointOnObject(g12,g10)
    c: DistanceX(g0) = 24
    c: DistanceY(g0) = 64
    c: Distance(g11,g12) = 2
    c: Equal(g11,g13) = 0.75
    c: PointOnObject(g13,g10)
    c: Equal(g11,g14) = 0.75
    c: PointOnObject(g14,g10)
    c: Equal(g11,g15) = 0.75
    c: PointOnObject(g15,g10)
    c: Distance(g12,g13) = 2
    c: Distance(g13,g14) = 2
    c: Distance(g14,g15) = 2
FEATURE [PartDesign::Pocket] Pocket003074  label="basic_horn_union002"
  BaseFeature = -> Pocket003075
  Length = 5
  Length2 = 100
  Placement = pos=(0,6.2,0) rot=(0,0.707107,0.707107;3.14159rad)
  Profile = -> Sketch106
  Refine = true
  Type = 0
FEATURE [Sketcher::SketchObject] Sketch120  label="q2_bridge004"
  ExternalGeometry = -> [Pocket003074]
  MapMode = 5
  Placement = pos=(2e-16,8.45,-2.3e-15) rot=(0,-0.707107,0.707107;3.14159rad)
  Support = -> [Pocket003074]
  sketch-geometry (4):
    g0: LineSegment StartX=39.516 StartY=-79.5977 StartZ=0 EndX=45.266 EndY=-69.6384 EndZ=0
    g1: LineSegment StartX=45.266 StartY=-69.6384 StartZ=0 EndX=40.9358 EndY=-67.1384 EndZ=0
    g2: LineSegment StartX=39.516 StartY=-79.5977 StartZ=0 EndX=35.1858 EndY=-77.0977 EndZ=0
    g3: ArcOfCircle CenterX=24.5001 CenterY=-64.2888 CenterZ=0 NormalX=0 NormalY=0 NormalZ=1 AngleXU=0 Radius=16.6809 StartAngle=5.40766 EndAngle=6.11151
  constraints (10):
    c: Coincident(g-5,g0)
    c: Coincident(g0,g-5)
    c: Coincident(g0,g1)
    c: PointOnObject(g1,g-3)
    c: Coincident(g0,g2)
    c: PointOnObject(g2,g-4)
    c: Distance(g2) = 5
    c: Equal(g2,g1)
    c: Coincident(g3,g1)
    c: Coincident(g3,g2)
FEATURE [PartDesign::Pad] Pad012035  label="q2_bridge005"
  BaseFeature = -> Pocket003074
  Length = 31
  Length2 = 100
  Placement = pos=(0,6.2,0) rot=(0,0.707107,0.707107;3.14159rad)
  Profile = -> Sketch120
  Refine = true
  Type = 0
FEATURE [Sketcher::SketchObject] Sketch114  label="q2_back_union002"
  ExternalGeometry = -> [Pad012029,Sketch104]
  MapMode = 5
  Placement = pos=(-2.3e-15,-22.55,3.83e-14) rot=(0,-0.707107,0.707107;3.14159rad)
  Support = -> [Pad012035]
  expr: Constraints[2] = Sketch067.Constraints[2]
  sketch-geometry (7):
    g0: ArcOfCircle CenterX=24 CenterY=-64 CenterZ=0 NormalX=0 NormalY=0 NormalZ=1 AngleXU=0 Radius=5.75 StartAngle=1.0472 EndAngle=4.18879
    g1: LineSegment [constr] StartX=12.5 StartY=-64 StartZ=0 EndX=37 EndY=-64 EndZ=0
    g2: LineSegment [constr] StartX=24 StartY=-64 StartZ=0 EndX=26.875 EndY=-59.0204 EndZ=0
    g3: LineSegment StartX=45.266 StartY=-69.6384 StartZ=0 EndX=26.875 EndY=-59.0204 EndZ=0
    g4: LineSegment StartX=45.266 StartY=-69.6384 StartZ=0 EndX=39.516 EndY=-79.5977 EndZ=0
    g5: LineSegment StartX=39.516 StartY=-79.5977 StartZ=0 EndX=21.125 EndY=-68.9796 EndZ=0
    g6: Circle CenterX=24 CenterY=-64 CenterZ=0 NormalX=0 NormalY=0 NormalZ=1 AngleXU=0 Radius=2
  constraints (16):
    c: Coincident(g0,g-3)
    c: PointOnObject(g0,g-3)
    c: Angle(g0) = 3.14159
    c: Horizontal(g1)
    c: PointOnObject(g0,g1)
    c: Coincident(g2,g0)
    c: Coincident(g2,g0)
    c: Parallel(g2,g-4)
    c: Coincident(g-4,g3)
    c: Coincident(g3,g0)
    c: Coincident(g3,g4)
    c: Coincident(g4,g-4)
    c: Coincident(g4,g5)
    c: Coincident(g5,g0)
    c: Coincident(g6,g0)
    c: Radius(g6) = 2
FEATURE [PartDesign::Pad] Pad012031  label="q2_joint002"
  BaseFeature = -> Pad012035
  Length = 3.5
  Length2 = 100
  Placement = pos=(0,6.2,0) rot=(0,0.707107,0.707107;3.14159rad)
  Profile = -> Sketch114
  Refine = true
  Type = 0
FEATURE [Sketcher::SketchObject] Sketch105  label="q2-leg_union_section002"
  ExternalGeometry = -> [Pad012031]
  MapMode = 5
  Placement = pos=(-64.1038,6.2,37.0103) rot=(0,-1,0;1.0472rad)
  Support = -> [Pad012031]
  sketch-geometry (4):
    g0: LineSegment StartX=49.1756 StartY=5.75 StartZ=0 EndX=49.1756 EndY=-32.25 EndZ=0
    g1: LineSegment StartX=49.1756 StartY=-32.25 StartZ=0 EndX=37.6756 EndY=-32.25 EndZ=0
    g2: LineSegment StartX=37.6756 StartY=-32.25 StartZ=0 EndX=37.6756 EndY=5.75 EndZ=0
    g3: LineSegment StartX=37.6756 StartY=5.75 StartZ=0 EndX=49.1756 EndY=5.75 EndZ=0
  constraints (8):
    c: Coincident(g-6,g0)
    c: Coincident(g0,g-6)
    c: Coincident(g0,g1)
    c: Coincident(g1,g-5)
    c: Coincident(g-5,g2)
    c: Coincident(g2,g-4)
    c: Coincident(g2,g3)
    c: Coincident(g3,g0)
FEATURE [Sketcher::SketchObject] Sketch111  label="trajectory002"
  ExternalGeometry = -> [Pad012031]
  MapMode = 5
  Placement = pos=(6e-16,11.95,-5.8e-15) rot=(0,0.707107,0.707107;3.14159rad)
  Support = -> [Pad012031]
  sketch-geometry (8):
    g0: GeomPoint X=42.3808 Y=74.6356 Z=0
    g1-g4: Circle [constr] x4 (B-spline internal-alignment scaffolding for g5; pole/knot coordinates omitted)
    g5: BSplineCurve PolesCount=4 KnotsCount=2 Degree=3 IsPeriodic=0
    g6: GeomPoint [constr] X=42.3808 Y=74.6356 Z=0
    g7: GeomPoint [constr] X=64.6677 Y=0 Z=0
  constraints (10):
    c: PointOnObject(g0,g-3)
    c: Coincident(g1,g0)
    c: Radius(g1) = 4
    c: Equal(g1,g2)
    c: Equal(g1,g3)
    c: Equal(g1,g4)
    c: PointOnObject(g4,g-1)
    c: InternalAlignment(g1-g4 -> g5) x4
    c: InternalAlignment(g6,g5)
    c: InternalAlignment(g7,g5)
FEATURE [Sketcher::SketchObject] Sketch110  label="q2-bone-touch_section002"
  ExternalGeometry = -> [Sketch111,Pad012031]
  MapMode = 5
  Support = -> [XY_Plane027]
  sketch-geometry (7):
    g0: LineSegment StartX=-66.1677 StartY=-4.55 StartZ=0 EndX=-63.1677 EndY=-4.55 EndZ=0
    g1: LineSegment StartX=-63.1677 StartY=-4.55 StartZ=0 EndX=-63.1677 EndY=-9.55 EndZ=0
    g2: LineSegment StartX=-63.1677 StartY=-9.55 StartZ=0 EndX=-66.1677 EndY=-9.55 EndZ=0
    g3: LineSegment StartX=-66.1677 StartY=-9.55 StartZ=0 EndX=-66.1677 EndY=-4.55 EndZ=0
    g4: GeomPoint X=-45.266 Y=-7.05 Z=0
    g5: GeomPoint X=-63.1677 Y=-7.05 Z=0
    g6: GeomPoint X=-64.6677 Y=-4.55 Z=0
  constraints (18):
    c: Coincident(g0,g1)
    c: Coincident(g1,g2)
    c: Coincident(g2,g3)
    c: Coincident(g3,g0)
    c: Horizontal(g0)
    c: Horizontal(g2)
    c: Vertical(g1)
    c: Vertical(g3)
    c: PointOnObject(g4,g-4)
    c: Symmetric(g-4,g-4,g4)
    c: PointOnObject(g5,g1)
    c: Symmetric(g0,g1,g5)
    c: Horizontal(g5,g4)
    c: PointOnObject(g6,g0)
    c: Symmetric(g0,g0,g6)
    c: Vertical(g6,g-3)
    c: DistanceX(g2,g2) = 3
    c: DistanceY(g3,g3) = 5
FEATURE [PartDesign::AdditivePipe] AdditivePipe002
  AuxilleryCurvelinear = true
  AuxillerySpineTangent = false
  BaseFeature = -> Pad012031
  Binormal = (0,0,0)
  Mode = 0
  Placement = pos=(0,6.2,0) rot=(0,0.707107,0.707107;3.14159rad)
  Profile = -> Sketch105
  Refine = true
  Sections = -> [Sketch110]
  Spine = -> Sketch111
  SpineTangent = false
  Transformation = 1
  Transition = 0
FEATURE [PartDesign::Body] Body015  label="Q2-Leg-joint002"
  Group = -> [Sketch125,Pad012029,Sketch104,Pad012033,Sketch116,Sketch121,Pocket003075,Sketch106,Pocket003074,Sketch120,Pad012035,Sketch114,Pad012031,Sketch111,Sketch105,Sketch110,AdditivePipe002]
  Origin = -> Origin027
  Tip = -> AdditivePipe002
FEATURE [Sketcher::SketchObject] Sketch128  label="base_cylinder008"
  MapMode = 5
  Support = -> [XY_Plane025]
  sketch-geometry (2):
    g0: Circle CenterX=0 CenterY=0 CenterZ=0 NormalX=0 NormalY=0 NormalZ=1 AngleXU=0 Radius=3.75
    g1: Circle CenterX=0 CenterY=0 CenterZ=0 NormalX=0 NormalY=0 NormalZ=1 AngleXU=0 Radius=5.75
  constraints (4):
    c: Coincident(g0,g-1)
    c: Radius(g0) = 3.75
    c: Coincident(g1,g-1)
    c: Radius(g1) = 5.75
FEATURE [PartDesign::Pad] Pad012028  label="low_base004"
  Length = 2.25
  Length2 = 100
  Profile = -> Sketch128
  Refine = true
  Type = 0
FEATURE [Sketcher::SketchObject] Sketch127  label="basic_base005"
  MapMode = 5
  Placement = pos=(0,0,2.25) rot=(0,0,1;0rad)
  Support = -> [Pad012028]
  sketch-geometry (6):
    g0: LineSegment StartX=0 StartY=5.71563 StartZ=0 EndX=-20.5 EndY=5.71563 EndZ=0
    g1: LineSegment StartX=1.86762e-06 StartY=-5.71497 StartZ=0 EndX=-20.5 EndY=-5.71497 EndZ=0
    g2: LineSegment StartX=-20.5 StartY=5.71563 StartZ=0 EndX=-20.5 EndY=-5.71497 EndZ=0
    g3: LineSegment StartX=0 StartY=5.71563 StartZ=0 EndX=5.71497 EndY=5.71563 EndZ=0
    g4: LineSegment StartX=5.71497 StartY=5.71563 StartZ=0 EndX=5.71497 EndY=0 EndZ=0
    g5: ArcOfCircle CenterX=0 CenterY=0 CenterZ=0 NormalX=0 NormalY=0 NormalZ=1 AngleXU=0 Radius=5.71497 StartAngle=4.71239 EndAngle=6.28319
  constraints (14):
    c: PointOnObject(g0,g-2)
    c: Horizontal(g0)
    c: DistanceX(g0,g0) = 20.5
    c: Coincident(g2,g0)
    c: Vertical(g2)
    c: Coincident(g1,g2)
    c: Coincident(g0,g3)
    c: Horizontal(g3)
    c: Coincident(g4,g3)
    c: PointOnObject(g4,g-1)
    c: Vertical(g4)
    c: Coincident(g5,g-1)
    c: Coincident(g5,g1)
    c: Coincident(g5,g4)
FEATURE [PartDesign::Pad] Pad012032  label="q1_basic_base004"
  BaseFeature = -> Pad012028
  Length = 3.5
  Length2 = 100
  Profile = -> Sketch127
  Refine = true
  Type = 0
FEATURE [Sketcher::SketchObject] Sketch118  label="q1_base_horn004"
  MapMode = 5
  Placement = pos=(0,0,5.75) rot=(0,0,1;0rad)
  Support = -> [Pad012032]
  sketch-geometry (7):
    g0: LineSegment StartX=-1.25 StartY=3.53553 StartZ=0 EndX=-17 EndY=1.74295 EndZ=0
    g1: ArcOfCircle CenterX=-17 CenterY=0 CenterZ=0 NormalX=0 NormalY=0 NormalZ=1 AngleXU=0 Radius=1.74295 StartAngle=1.5708 EndAngle=3.14159
    g2: LineSegment [constr] StartX=-18.743 StartY=0 StartZ=0 EndX=0 EndY=0 EndZ=0
    g3: ArcOfCircle CenterX=0 CenterY=0 CenterZ=0 NormalX=0 NormalY=0 NormalZ=1 AngleXU=0 Radius=3.75 StartAngle=0 EndAngle=1.91063
    g4: LineSegment StartX=-1.25 StartY=-3.53553 StartZ=0 EndX=-17 EndY=-1.74295 EndZ=0
    g5: ArcOfCircle CenterX=-17 CenterY=-1e-12 CenterZ=0 NormalX=0 NormalY=0 NormalZ=1 AngleXU=0 Radius=1.74295 StartAngle=3.14159 EndAngle=4.71239
    g6: ArcOfCircle CenterX=0 CenterY=0 CenterZ=0 NormalX=0 NormalY=0 NormalZ=1 AngleXU=0 Radius=3.75 StartAngle=4.37255 EndAngle=6.28319
  constraints (11):
    c: PointOnObject(g1,g-1)
    c: Coincident(g1,g0)
    c: PointOnObject(g1,g-1)
    c: Coincident(g1,g2)
    c: Coincident(g3,g-1)
    c: Radius(g3) = 3.75
    c: Coincident(g3,g0)
    c: DistanceX(g0,g3) = 5
    c: Coincident(g5,g4)
    c: Radius(g6) = 3.75
    c: Coincident(g6,g4)
FEATURE [PartDesign::Pocket] Pocket003077  label="q1_basic_horn004"
  BaseFeature = -> Pad012032
  Length = 2.65
  Length2 = 100
  Profile = -> Sketch118
  Refine = true
  Type = 0
FEATURE [Sketcher::SketchObject] Sketch126  label="horn_holes007"
  MapMode = 5
  Placement = pos=(0,0,3.1) rot=(0,0,1;0rad)
  Support = -> [Pocket003077]
  sketch-geometry (10):
    g0: Circle CenterX=0 CenterY=0 CenterZ=0 NormalX=0 NormalY=0 NormalZ=1 AngleXU=0 Radius=3.75
    g1: Circle CenterX=-14.5 CenterY=0 CenterZ=0 NormalX=0 NormalY=0 NormalZ=1 AngleXU=0 Radius=0.75
    g2: Circle CenterX=-12.5 CenterY=0 CenterZ=0 NormalX=0 NormalY=0 NormalZ=1 AngleXU=0 Radius=0.75
    g3: LineSegment [constr] StartX=-14.5 StartY=0 StartZ=0 EndX=-12.5 EndY=0 EndZ=0
    g4: Circle CenterX=-10.5 CenterY=0 CenterZ=0 NormalX=0 NormalY=0 NormalZ=1 AngleXU=0 Radius=0.75
    g5: LineSegment [constr] StartX=-12.5 StartY=0 StartZ=0 EndX=-10.5 EndY=0 EndZ=0
    g6: Circle CenterX=-8.5 CenterY=0 CenterZ=0 NormalX=0 NormalY=0 NormalZ=1 AngleXU=0 Radius=0.75
    g7: LineSegment [constr] StartX=-10.5 StartY=0 StartZ=0 EndX=-8.5 EndY=0 EndZ=0
    g8: Circle CenterX=-6.5 CenterY=0 CenterZ=0 NormalX=0 NormalY=0 NormalZ=1 AngleXU=0 Radius=0.75
    g9: LineSegment [constr] StartX=-8.5 StartY=0 StartZ=0 EndX=-6.5 EndY=0 EndZ=0
  constraints (25):
    c: Coincident(g0,g-1)
    c: Radius(g1) = 0.75
    c: Radius(g0) = 3.75
    c: Radius(g2) = 0.75
    c: Coincident(g1,g3)
    c: Coincident(g2,g3)
    c: Distance(g3) = 2
    c: Angle(g3) = 0
    c: Radius(g4) = 0.75
    c: Coincident(g2,g5)
    c: Coincident(g4,g5)
    c: Equal(g3,g5)
    c: Parallel(g5,g3)
    c: Radius(g6) = 0.75
    c: Coincident(g4,g7)
    c: Coincident(g6,g7)
    c: Equal(g3,g7)
    c: Parallel(g7,g3)
    c: Radius(g8) = 0.75
    c: Coincident(g6,g9)
    c: Coincident(g8,g9)
    c: Equal(g3,g9)
    c: Parallel(g9,g3)
    c: PointOnObject(g2,g-1)
    c: DistanceX(g8,g-1) = 6.5
FEATURE [PartDesign::Pocket] Pocket003071  label="q1_basic_horn_shape004"
  BaseFeature = -> Pocket003077
  Length = 5
  Length2 = 100
  Profile = -> Sketch126
  Refine = true
  Type = 0
FEATURE [Sketcher::SketchObject] Sketch115  label="q2-base002"
  ExternalGeometry = -> [Pocket003071]
  MapMode = 5
  Placement = pos=(-20.5,0,0) rot=(0.57735,-0.57735,-0.57735;2.0944rad)
  Support = -> [Pocket003071]
  sketch-geometry (6):
    g0: LineSegment StartX=-5.71563 StartY=2.25 StartZ=0 EndX=-11.6041 EndY=2.25 EndZ=0
    g1: LineSegment StartX=-11.6041 StartY=2.25 StartZ=0 EndX=-38.6752 EndY=17.8795 EndZ=0
    g2: LineSegment StartX=-11.6626 StartY=5.74787 StartZ=0 EndX=-37.1752 EndY=20.4776 EndZ=0
    g3: LineSegment StartX=-37.1752 StartY=20.4776 StartZ=0 EndX=-38.6752 EndY=17.8795 EndZ=0
    g4: LineSegment StartX=-5.71563 StartY=5.74787 StartZ=0 EndX=-5.71563 EndY=2.25 EndZ=0
    g5: LineSegment StartX=-11.6626 StartY=5.74787 StartZ=0 EndX=-5.71563 EndY=5.74787 EndZ=0
  constraints (13):
    c: Coincident(g3,g2)
    c: Coincident(g3,g1)
    c: Perpendicular(g3,g1)
    c: Coincident(g0,g-3)
    c: Parallel(g1,g2)
    c: Coincident(g4,g0)
    c: Perpendicular(g4,g0)
    c: Distance(g1,g2) = 3
    c: Angle(g0,g1) = 2.61799
    c: Coincident(g0,g1)
    c: Coincident(g2,g5)
    c: Coincident(g5,g4)
    c: Horizontal(g5)
FEATURE [PartDesign::Pad] Pad012026  label="q2-bed-base002"
  BaseFeature = -> Pocket003071
  Length = 26.215
  Length2 = 100
  Profile = -> Sketch115
  Refine = true
  Reversed = true
  Type = 0
FEATURE [Sketcher::SketchObject] Sketch117  label="q2-corner-hole005"
  MapMode = 5
  Placement = pos=(0,0,5.74787) rot=(0,0,1;0rad)
  Support = -> [Pad012026]
  sketch-geometry (4):
    g0: LineSegment StartX=-1.62396 StartY=12 StartZ=0 EndX=-5 EndY=12 EndZ=0
    g1: LineSegment StartX=-5 StartY=12 StartZ=0 EndX=-5 EndY=6.68085 EndZ=0
    g2: LineSegment StartX=-5 StartY=6.68085 StartZ=0 EndX=-1.62396 EndY=6.68085 EndZ=0
    g3: LineSegment StartX=-1.62396 StartY=6.68085 StartZ=0 EndX=-1.62396 EndY=12 EndZ=0
  constraints (8):
    c: Coincident(g0,g1)
    c: Coincident(g1,g2)
    c: Coincident(g2,g3)
    c: Coincident(g3,g0)
    c: Horizontal(g0)
    c: Horizontal(g2)
    c: Vertical(g1)
    c: Vertical(g3)
FEATURE [PartDesign::Pocket] Pocket003070  label="q2-corner-hole004"
  BaseFeature = -> Pad012026
  Length = 2
  Length2 = 100
  Profile = -> Sketch117
  Refine = true
  Type = 0
FEATURE [Sketcher::SketchObject] Sketch136  label="base_cylinder010"
  MapMode = 5
  Placement = pos=(0,6.2,0) rot=(0,0.707107,0.707107;3.14159rad)
  sketch-geometry (2):
    g0: Circle CenterX=24 CenterY=64 CenterZ=0 NormalX=0 NormalY=0 NormalZ=1 AngleXU=0 Radius=3.75
    g1: Circle CenterX=24 CenterY=64 CenterZ=0 NormalX=0 NormalY=0 NormalZ=1 AngleXU=0 Radius=5.75
  constraints (3):
    c: Radius(g0) = 3.75
    c: Radius(g1) = 5.75
    c: Coincident(g1,g0)
FEATURE [PartDesign::Pad] Pad012047  label="q2_base_cylinder005"
  Length = 2.25
  Length2 = 100
  Placement = pos=(0,6.2,0) rot=(0,0.707107,0.707107;3.14159rad)
  Profile = -> Sketch136
  Refine = true
  Type = 0
FEATURE [Sketcher::SketchObject] Sketch144  label="q2_base004"
  ExternalGeometry = -> [Pad012047]
  MapMode = 5
  Placement = pos=(2e-16,8.45,-9e-16) rot=(0,0.707107,0.707107;3.14159rad)
  Support = -> [Pad012047]
  sketch-geometry (6):
    g0: ArcOfCircle CenterX=24 CenterY=64 CenterZ=0 NormalX=0 NormalY=0 NormalZ=1 AngleXU=0 Radius=5.75 StartAngle=2.0944 EndAngle=5.23599
    g1: LineSegment [constr] StartX=12.5 StartY=64 StartZ=0 EndX=37 EndY=64 EndZ=0
    g2: LineSegment [constr] StartX=24 StartY=64 StartZ=0 EndX=21.125 EndY=68.9796 EndZ=0
    g3: LineSegment StartX=21.125 StartY=68.9796 StartZ=0 EndX=39.516 EndY=79.5977 EndZ=0
    g4: LineSegment StartX=39.516 StartY=79.5977 StartZ=0 EndX=45.266 EndY=69.6384 EndZ=0
    g5: LineSegment StartX=45.266 StartY=69.6384 StartZ=0 EndX=26.875 EndY=59.0204 EndZ=0
  constraints (14):
    c: Coincident(g0,g-3)
    c: PointOnObject(g0,g-3)
    c: Angle(g0) = 3.14159
    c: Horizontal(g1)
    c: PointOnObject(g0,g1)
    c: Coincident(g2,g0)
    c: Coincident(g2,g0)
    c: Angle(g1,g2) = 2.0944
    c: Tangent(g0,g3) = 1.5708
    c: Coincident(g3,g4)
    c: Coincident(g4,g5)
    c: Coincident(g5,g0)
    c: Equal(g3,g5)
    c: Parallel(g3,g5)
FEATURE [PartDesign::Pad] Pad012044  label="q2_basic_base003"
  BaseFeature = -> Pad012047
  Length = 3.5
  Length2 = 100
  Placement = pos=(0,6.2,0) rot=(0,0.707107,0.707107;3.14159rad)
  Profile = -> Sketch144
  Refine = true
  Type = 0
FEATURE [Sketcher::SketchObject] Sketch138  label="AUX_q2_base_horn006"
  ExternalGeometry = -> [Pad012044]
  MapMode = 5
  Placement = pos=(-3e-15,11.95,-6e-15) rot=(0.186157,0.694747,0.694747;3.50969rad)
  sketch-geometry (5):
    g0: LineSegment StartX=54.0346 StartY=46.9656 StartZ=0 EndX=69.7804 EndY=45.1656 EndZ=0
    g1: ArcOfCircle CenterX=69.7804 CenterY=43.4256 CenterZ=0 NormalX=0 NormalY=0 NormalZ=1 AngleXU=0 Radius=1.74 StartAngle=0 EndAngle=1.5708
    g2: LineSegment [constr] StartX=71.5204 StartY=43.4256 StartZ=0 EndX=49.0304 EndY=43.4256 EndZ=0
    g3: ArcOfCircle CenterX=52.7846 CenterY=43.4256 CenterZ=0 NormalX=0 NormalY=0 NormalZ=1 AngleXU=0 Radius=3.75421 StartAngle=1.23136 EndAngle=3.14159
    g4: LineSegment [constr] StartX=52.7846 StartY=49.1756 StartZ=0 EndX=52.7846 EndY=37.6756 EndZ=0
  constraints (16):
    c: Coincident(g1,g0)
    c: Coincident(g1,g2)
    c: Coincident(g3,g0)
    c: Radius(g1) = 1.74
    c: PointOnObject(g1,g2)
    c: Coincident(g2,g3)
    c: PointOnObject(g3,g2)
    c: DistanceX(g2,g2) = 22.49
    c: DistanceY(g1,g0) = 1.74
    c: DistanceX(g3,g0) = 1.25
    c: DistanceY(g3,g0) = 3.54
    c: Horizontal(g2)
    c: Coincident(g4,g-3)
    c: Coincident(g4,g-4)
    c: PointOnObject(g3,g4)
    c: Symmetric(g4,g4,g3)
FEATURE [Sketcher::SketchObject] Sketch132  label="horn_shape006"
  ExternalGeometry = -> [Sketch138]
  MapMode = 5
  Placement = pos=(6e-16,11.95,-5.8e-15) rot=(0,0.707107,0.707107;3.14159rad)
  Support = -> [Pad012044]
  sketch-geometry (7):
    g0: LineSegment [constr] StartX=20.7488 StartY=62.1229 StartZ=0 EndX=40.2257 EndY=73.3679 EndZ=0
    g1: ArcOfCircle CenterX=24 CenterY=64 CenterZ=0 NormalX=0 NormalY=0 NormalZ=1 AngleXU=0 Radius=3.75421 StartAngle=1.75495 EndAngle=3.66519
    g2: ArcOfCircle CenterX=38.7188 CenterY=72.4979 CenterZ=0 NormalX=0 NormalY=0 NormalZ=1 AngleXU=0 Radius=1.74 StartAngle=0.523599 EndAngle=2.0944
    g3: LineSegment StartX=23.3125 StartY=67.6907 StartZ=0 EndX=37.8488 EndY=74.0048 EndZ=0
    g4: ArcOfCircle CenterX=24 CenterY=64 CenterZ=0 NormalX=0 NormalY=0 NormalZ=1 AngleXU=0 Radius=3.75421 StartAngle=3.66519 EndAngle=5.57543
    g5: ArcOfCircle CenterX=38.7188 CenterY=72.4979 CenterZ=0 NormalX=0 NormalY=0 NormalZ=1 AngleXU=0 Radius=1.74 StartAngle=5.23599 EndAngle=6.80678
    g6: LineSegment StartX=26.8525 StartY=61.5593 StartZ=0 EndX=39.5888 EndY=70.991 EndZ=0
  constraints (16):
    c: Coincident(g0,g-5)
    c: Coincident(g0,g-4)
    c: Coincident(g1,g-5)
    c: Coincident(g1,g-5)
    c: Coincident(g1,g0)
    c: Coincident(g2,g-4)
    c: Coincident(g2,g0)
    c: Coincident(g2,g-4)
    c: Coincident(g3,g1)
    c: Coincident(g3,g2)
    c: Coincident(g6,g4)
    c: Coincident(g6,g5)
    c: Coincident(g0,g4)
    c: Coincident(g1,g4)
    c: Coincident(g2,g5)
    c: Coincident(g0,g5)
FEATURE [PartDesign::Pocket] Pocket003080  label="horn_shape007"
  BaseFeature = -> Pad012044
  Length = 2.65
  Length2 = 100
  Placement = pos=(0,6.2,0) rot=(0,0.707107,0.707107;3.14159rad)
  Profile = -> Sketch132
  Refine = true
  Type = 0
FEATURE [Sketcher::SketchObject] Sketch135  label="horn_holes008"
  ExternalGeometry = -> [Pocket003080]
  MapMode = 5
  Placement = pos=(2e-16,9.3,-5.3e-15) rot=(0,0.707107,0.707107;3.14159rad)
  Support = -> [Pocket003080]
  sketch-geometry (16):
    g0: Circle CenterX=24 CenterY=64 CenterZ=0 NormalX=0 NormalY=0 NormalZ=1 AngleXU=0 Radius=3.75
    g1: Circle CenterX=-14.6952 CenterY=0 CenterZ=0 NormalX=0 NormalY=0 NormalZ=1 AngleXU=0 Radius=0.75
    g2: Circle CenterX=-12.6952 CenterY=0 CenterZ=0 NormalX=0 NormalY=0 NormalZ=1 AngleXU=0 Radius=0.75
    g3: LineSegment [constr] StartX=-14.6952 StartY=0 StartZ=0 EndX=-12.6952 EndY=0 EndZ=0
    g4: Circle CenterX=-10.6952 CenterY=0 CenterZ=0 NormalX=0 NormalY=0 NormalZ=1 AngleXU=0 Radius=0.75
    g5: LineSegment [constr] StartX=-12.6952 StartY=0 StartZ=0 EndX=-10.6952 EndY=0 EndZ=0
    g6: Circle CenterX=-8.69518 CenterY=0 CenterZ=0 NormalX=0 NormalY=0 NormalZ=1 AngleXU=0 Radius=0.75
    g7: LineSegment [constr] StartX=-10.6952 StartY=0 StartZ=0 EndX=-8.69518 EndY=0 EndZ=0
    g8: Circle CenterX=-6.69518 CenterY=0 CenterZ=0 NormalX=0 NormalY=0 NormalZ=1 AngleXU=0 Radius=0.75
    g9: LineSegment [constr] StartX=-8.69518 StartY=0 StartZ=0 EndX=-6.69518 EndY=0 EndZ=0
    g10: LineSegment [constr] StartX=24 StartY=64 StartZ=0 EndX=43.3449 EndY=75.1688 EndZ=0
    g11: Circle CenterX=29.6292 CenterY=67.25 CenterZ=0 NormalX=0 NormalY=0 NormalZ=1 AngleXU=0 Radius=0.75
    g12: Circle CenterX=31.3612 CenterY=68.25 CenterZ=0 NormalX=0 NormalY=0 NormalZ=1 AngleXU=0 Radius=0.75
    g13: Circle CenterX=33.0933 CenterY=69.25 CenterZ=0 NormalX=0 NormalY=0 NormalZ=1 AngleXU=0 Radius=0.75
    g14: Circle CenterX=34.8253 CenterY=70.25 CenterZ=0 NormalX=0 NormalY=0 NormalZ=1 AngleXU=0 Radius=0.75
    g15: Circle CenterX=36.5574 CenterY=71.25 CenterZ=0 NormalX=0 NormalY=0 NormalZ=1 AngleXU=0 Radius=0.75
  constraints (41):
    c: Radius(g1) = 0.75
    c: Radius(g0) = 3.75
    c: Radius(g2) = 0.75
    c: Coincident(g1,g3)
    c: Coincident(g2,g3)
    c: Distance(g3) = 2
    c: Angle(g3) = 0
    c: Radius(g4) = 0.75
    c: Coincident(g2,g5)
    c: Coincident(g4,g5)
    c: Equal(g3,g5)
    c: Radius(g6) = 0.75
    c: Coincident(g4,g7)
    c: Coincident(g6,g7)
    c: Equal(g3,g7)
    c: Radius(g8) = 0.75
    c: Coincident(g6,g9)
    c: Coincident(g8,g9)
    c: Equal(g3,g9)
    c: Parallel(g9,g3)
    c: Parallel(g9,g7)
    c: Parallel(g7,g5)
    c: Coincident(g10,g0)
    c: Angle(g10) = 0.523599
    c: Radius(g11) = 0.75
    c: Distance(g0,g11) = 6.5
    c: PointOnObject(g11,g10)
    c: Equal(g11,g12) = 0.75
    c: PointOnObject(g12,g10)
    c: DistanceX(g0) = 24
    c: DistanceY(g0) = 64
    c: Distance(g11,g12) = 2
    c: Equal(g11,g13) = 0.75
    c: PointOnObject(g13,g10)
    c: Equal(g11,g14) = 0.75
    c: PointOnObject(g14,g10)
    c: Equal(g11,g15) = 0.75
    c: PointOnObject(g15,g10)
    c: Distance(g12,g13) = 2
    c: Distance(g13,g14) = 2
    c: Distance(g14,g15) = 2
FEATURE [PartDesign::Pocket] Pocket003083  label="basic_horn_union003"
  BaseFeature = -> Pocket003080
  Length = 5
  Length2 = 100
  Placement = pos=(0,6.2,0) rot=(0,0.707107,0.707107;3.14159rad)
  Profile = -> Sketch135
  Refine = true
  Type = 0
FEATURE [Part::Feature] Pocket003086  label="Final-1-arm-horn018"
  Placement = pos=(0,0,32) rot=(0.707107,-0.707107,0;3.14159rad)
  shape: bbox 8 x 22.5 x 5 mm, 19 faces (baked)
FEATURE [Sketcher::SketchObject] Sketch148  label="q2_bridge007"
  ExternalGeometry = -> [Pocket003083]
  MapMode = 5
  Placement = pos=(2e-16,8.45,-2.3e-15) rot=(0,-0.707107,0.707107;3.14159rad)
  Support = -> [Pocket003083]
  sketch-geometry (4):
    g0: LineSegment StartX=39.516 StartY=-79.5977 StartZ=0 EndX=45.266 EndY=-69.6384 EndZ=0
    g1: LineSegment StartX=45.266 StartY=-69.6384 StartZ=0 EndX=40.9358 EndY=-67.1384 EndZ=0
    g2: LineSegment StartX=39.516 StartY=-79.5977 StartZ=0 EndX=35.1858 EndY=-77.0977 EndZ=0
    g3: ArcOfCircle CenterX=24.5001 CenterY=-64.2888 CenterZ=0 NormalX=0 NormalY=0 NormalZ=1 AngleXU=0 Radius=16.6809 StartAngle=5.40766 EndAngle=6.11151
  constraints (10):
    c: Coincident(g-5,g0)
    c: Coincident(g0,g-5)
    c: Coincident(g0,g1)
    c: PointOnObject(g1,g-3)
    c: Coincident(g0,g2)
    c: PointOnObject(g2,g-4)
    c: Distance(g2) = 5
    c: Equal(g2,g1)
    c: Coincident(g3,g1)
    c: Coincident(g3,g2)
FEATURE [PartDesign::Pad] Pad012037  label="q2_bridge006"
  BaseFeature = -> Pocket003083
  Length = 31
  Length2 = 100
  Placement = pos=(0,6.2,0) rot=(0,0.707107,0.707107;3.14159rad)
  Profile = -> Sketch148
  Refine = true
  Type = 0
FEATURE [Sketcher::SketchObject] Sketch145  label="q2_back_union003"
  ExternalGeometry = -> [Pad012047,Sketch144]
  MapMode = 5
  Placement = pos=(-2.3e-15,-22.55,3.83e-14) rot=(0,-0.707107,0.707107;3.14159rad)
  Support = -> [Pad012037]
  expr: Constraints[2] = Sketch067.Constraints[2]
  sketch-geometry (7):
    g0: ArcOfCircle CenterX=24 CenterY=-64 CenterZ=0 NormalX=0 NormalY=0 NormalZ=1 AngleXU=0 Radius=5.75 StartAngle=1.0472 EndAngle=4.18879
    g1: LineSegment [constr] StartX=12.5 StartY=-64 StartZ=0 EndX=37 EndY=-64 EndZ=0
    g2: LineSegment [constr] StartX=24 StartY=-64 StartZ=0 EndX=26.875 EndY=-59.0204 EndZ=0
    g3: LineSegment StartX=45.266 StartY=-69.6384 StartZ=0 EndX=26.875 EndY=-59.0204 EndZ=0
    g4: LineSegment StartX=45.266 StartY=-69.6384 StartZ=0 EndX=39.516 EndY=-79.5977 EndZ=0
    g5: LineSegment StartX=39.516 StartY=-79.5977 StartZ=0 EndX=21.125 EndY=-68.9796 EndZ=0
    g6: Circle CenterX=24 CenterY=-64 CenterZ=0 NormalX=0 NormalY=0 NormalZ=1 AngleXU=0 Radius=2
  constraints (16):
    c: Coincident(g0,g-3)
    c: PointOnObject(g0,g-3)
    c: Angle(g0) = 3.14159
    c: Horizontal(g1)
    c: PointOnObject(g0,g1)
    c: Coincident(g2,g0)
    c: Coincident(g2,g0)
    c: Parallel(g2,g-4)
    c: Coincident(g-4,g3)
    c: Coincident(g3,g0)
    c: Coincident(g3,g4)
    c: Coincident(g4,g-4)
    c: Coincident(g4,g5)
    c: Coincident(g5,g0)
    c: Coincident(g6,g0)
    c: Radius(g6) = 2
FEATURE [PartDesign::Pad] Pad012039  label="q2_joint003"
  BaseFeature = -> Pad012037
  Length = 3.5
  Length2 = 100
  Placement = pos=(0,6.2,0) rot=(0,0.707107,0.707107;3.14159rad)
  Profile = -> Sketch145
  Refine = true
  Type = 0
FEATURE [Sketcher::SketchObject] Sketch142  label="trajectory003"
  ExternalGeometry = -> [Pad012039]
  MapMode = 5
  Placement = pos=(6e-16,11.95,-5.8e-15) rot=(0,0.707107,0.707107;3.14159rad)
  Support = -> [Pad012039]
  sketch-geometry (8):
    g0: GeomPoint X=42.3808 Y=74.6356 Z=0
    g1-g4: Circle [constr] x4 (B-spline internal-alignment scaffolding for g5; pole/knot coordinates omitted)
    g5: BSplineCurve PolesCount=4 KnotsCount=2 Degree=3 IsPeriodic=0
    g6: GeomPoint [constr] X=42.3808 Y=74.6356 Z=0
    g7: GeomPoint [constr] X=64.6677 Y=0 Z=0
  constraints (10):
    c: PointOnObject(g0,g-3)
    c: Coincident(g1,g0)
    c: Radius(g1) = 4
    c: Equal(g1,g2)
    c: Equal(g1,g3)
    c: Equal(g1,g4)
    c: PointOnObject(g4,g-1)
    c: InternalAlignment(g1-g4 -> g5) x4
    c: InternalAlignment(g6,g5)
    c: InternalAlignment(g7,g5)
FEATURE [Sketcher::SketchObject] Sketch143  label="q2-bone-touch_section003"
  ExternalGeometry = -> [Sketch142,Pad012039]
  MapMode = 5
  Support = -> [XY_Plane029]
  sketch-geometry (7):
    g0: LineSegment StartX=-66.1677 StartY=-4.55 StartZ=0 EndX=-63.1677 EndY=-4.55 EndZ=0
    g1: LineSegment StartX=-63.1677 StartY=-4.55 StartZ=0 EndX=-63.1677 EndY=-9.55 EndZ=0
    g2: LineSegment StartX=-63.1677 StartY=-9.55 StartZ=0 EndX=-66.1677 EndY=-9.55 EndZ=0
    g3: LineSegment StartX=-66.1677 StartY=-9.55 StartZ=0 EndX=-66.1677 EndY=-4.55 EndZ=0
    g4: GeomPoint X=-45.266 Y=-7.05 Z=0
    g5: GeomPoint X=-63.1677 Y=-7.05 Z=0
    g6: GeomPoint X=-64.6677 Y=-4.55 Z=0
  constraints (18):
    c: Coincident(g0,g1)
    c: Coincident(g1,g2)
    c: Coincident(g2,g3)
    c: Coincident(g3,g0)
    c: Horizontal(g0)
    c: Horizontal(g2)
    c: Vertical(g1)
    c: Vertical(g3)
    c: PointOnObject(g4,g-4)
    c: Symmetric(g-4,g-4,g4)
    c: PointOnObject(g5,g1)
    c: Symmetric(g0,g1,g5)
    c: Horizontal(g5,g4)
    c: PointOnObject(g6,g0)
    c: Symmetric(g0,g0,g6)
    c: Vertical(g6,g-3)
    c: DistanceX(g2,g2) = 3
    c: DistanceY(g3,g3) = 5
FEATURE [Part::Feature] Pocket003087  label="Final-1-arm-horn019"
  Placement = pos=(0,0,32) rot=(0.707107,0.707107,0;3.14159rad)
  shape: bbox 8 x 22.5 x 5 mm, 19 faces (baked)
FEATURE [Part::Feature] Fusion007063  label="Servo-sg90-final020"
  Placement = pos=(0,-16.6,0) rot=(0,0,1;0rad)
  shape: bbox 11.8 x 32.4 x 29.9 mm, 77 faces (baked)
FEATURE [Part::MultiFuse] Fusion007061  label="q2-aux-servo005"
  Placement = pos=(-24,-20.5,64) rot=(-0.377964,0.654654,0.654654;2.41885rad)
  Refine = true
  Shapes = -> [Fusion007063,Pocket003087]
FEATURE [Part::Feature] Fusion007064  label="Servo-sg90-final021"
  Placement = pos=(0,-16.6,0) rot=(0,0,1;0rad)
  shape: bbox 11.8 x 32.4 x 29.9 mm, 77 faces (baked)
FEATURE [Part::MultiFuse] Fusion007062  label="q1-aux-servo005"
  Placement = pos=(0,0,17.25) rot=(0,0,1;0rad)
  Refine = true
  Shapes = -> [Pocket003086,Fusion007064]
FEATURE [Sketcher::SketchObject] Sketch151  label="base_cylinder011"
  MapMode = 5
  Support = -> [XY_Plane028]
  sketch-geometry (2):
    g0: Circle CenterX=0 CenterY=0 CenterZ=0 NormalX=0 NormalY=0 NormalZ=1 AngleXU=0 Radius=3.75
    g1: Circle CenterX=0 CenterY=0 CenterZ=0 NormalX=0 NormalY=0 NormalZ=1 AngleXU=0 Radius=5.75
  constraints (4):
    c: Coincident(g0,g-1)
    c: Radius(g0) = 3.75
    c: Coincident(g1,g-1)
    c: Radius(g1) = 5.75
FEATURE [PartDesign::Pad] Pad012041  label="low_base005"
  Length = 2.25
  Length2 = 100
  Profile = -> Sketch151
  Refine = true
  Type = 0
FEATURE [Sketcher::SketchObject] Sketch140  label="basic_base006"
  MapMode = 5
  Placement = pos=(0,0,2.25) rot=(0,0,1;0rad)
  Support = -> [Pad012041]
  sketch-geometry (6):
    g0: LineSegment StartX=0 StartY=5.71563 StartZ=0 EndX=-20.5 EndY=5.71563 EndZ=0
    g1: LineSegment StartX=1.86762e-06 StartY=-5.71497 StartZ=0 EndX=-20.5 EndY=-5.71497 EndZ=0
    g2: LineSegment StartX=-20.5 StartY=5.71563 StartZ=0 EndX=-20.5 EndY=-5.71497 EndZ=0
    g3: LineSegment StartX=0 StartY=5.71563 StartZ=0 EndX=5.71497 EndY=5.71563 EndZ=0
    g4: LineSegment StartX=5.71497 StartY=5.71563 StartZ=0 EndX=5.71497 EndY=0 EndZ=0
    g5: ArcOfCircle CenterX=0 CenterY=0 CenterZ=0 NormalX=0 NormalY=0 NormalZ=1 AngleXU=0 Radius=5.71497 StartAngle=4.71239 EndAngle=6.28319
  constraints (14):
    c: PointOnObject(g0,g-2)
    c: Horizontal(g0)
    c: DistanceX(g0,g0) = 20.5
    c: Coincident(g2,g0)
    c: Vertical(g2)
    c: Coincident(g1,g2)
    c: Coincident(g0,g3)
    c: Horizontal(g3)
    c: Coincident(g4,g3)
    c: PointOnObject(g4,g-1)
    c: Vertical(g4)
    c: Coincident(g5,g-1)
    c: Coincident(g5,g1)
    c: Coincident(g5,g4)
FEATURE [PartDesign::Pad] Pad012043  label="q1_basic_base005"
  BaseFeature = -> Pad012041
  Length = 3.5
  Length2 = 100
  Profile = -> Sketch140
  Refine = true
  Type = 0
FEATURE [Sketcher::SketchObject] Sketch141  label="q1_base_horn005"
  MapMode = 5
  Placement = pos=(0,0,5.75) rot=(0,0,1;0rad)
  Support = -> [Pad012043]
  sketch-geometry (7):
    g0: LineSegment StartX=-1.25 StartY=3.53553 StartZ=0 EndX=-17 EndY=1.74295 EndZ=0
    g1: ArcOfCircle CenterX=-17 CenterY=0 CenterZ=0 NormalX=0 NormalY=0 NormalZ=1 AngleXU=0 Radius=1.74295 StartAngle=1.5708 EndAngle=3.14159
    g2: LineSegment [constr] StartX=-18.743 StartY=0 StartZ=0 EndX=0 EndY=0 EndZ=0
    g3: ArcOfCircle CenterX=0 CenterY=0 CenterZ=0 NormalX=0 NormalY=0 NormalZ=1 AngleXU=0 Radius=3.75 StartAngle=0 EndAngle=1.91063
    g4: LineSegment StartX=-1.25 StartY=-3.53553 StartZ=0 EndX=-17 EndY=-1.74295 EndZ=0
    g5: ArcOfCircle CenterX=-17 CenterY=-1e-12 CenterZ=0 NormalX=0 NormalY=0 NormalZ=1 AngleXU=0 Radius=1.74295 StartAngle=3.14159 EndAngle=4.71239
    g6: ArcOfCircle CenterX=0 CenterY=0 CenterZ=0 NormalX=0 NormalY=0 NormalZ=1 AngleXU=0 Radius=3.75 StartAngle=4.37255 EndAngle=6.28319
  constraints (11):
    c: PointOnObject(g1,g-1)
    c: Coincident(g1,g0)
    c: PointOnObject(g1,g-1)
    c: Coincident(g1,g2)
    c: Coincident(g3,g-1)
    c: Radius(g3) = 3.75
    c: Coincident(g3,g0)
    c: DistanceX(g0,g3) = 5
    c: Coincident(g5,g4)
    c: Radius(g6) = 3.75
    c: Coincident(g6,g4)
FEATURE [PartDesign::Pocket] Pocket003084  label="q1_basic_horn005"
  BaseFeature = -> Pad012043
  Length = 2.65
  Length2 = 100
  Profile = -> Sketch141
  Refine = true
  Type = 0
FEATURE [Sketcher::SketchObject] Sketch149  label="horn_holes009"
  MapMode = 5
  Placement = pos=(0,0,3.1) rot=(0,0,1;0rad)
  Support = -> [Pocket003084]
  sketch-geometry (10):
    g0: Circle CenterX=0 CenterY=0 CenterZ=0 NormalX=0 NormalY=0 NormalZ=1 AngleXU=0 Radius=3.75
    g1: Circle CenterX=-14.5 CenterY=0 CenterZ=0 NormalX=0 NormalY=0 NormalZ=1 AngleXU=0 Radius=0.75
    g2: Circle CenterX=-12.5 CenterY=0 CenterZ=0 NormalX=0 NormalY=0 NormalZ=1 AngleXU=0 Radius=0.75
    g3: LineSegment [constr] StartX=-14.5 StartY=0 StartZ=0 EndX=-12.5 EndY=0 EndZ=0
    g4: Circle CenterX=-10.5 CenterY=0 CenterZ=0 NormalX=0 NormalY=0 NormalZ=1 AngleXU=0 Radius=0.75
    g5: LineSegment [constr] StartX=-12.5 StartY=0 StartZ=0 EndX=-10.5 EndY=0 EndZ=0
    g6: Circle CenterX=-8.5 CenterY=0 CenterZ=0 NormalX=0 NormalY=0 NormalZ=1 AngleXU=0 Radius=0.75
    g7: LineSegment [constr] StartX=-10.5 StartY=0 StartZ=0 EndX=-8.5 EndY=0 EndZ=0
    g8: Circle CenterX=-6.5 CenterY=0 CenterZ=0 NormalX=0 NormalY=0 NormalZ=1 AngleXU=0 Radius=0.75
    g9: LineSegment [constr] StartX=-8.5 StartY=0 StartZ=0 EndX=-6.5 EndY=0 EndZ=0
  constraints (25):
    c: Coincident(g0,g-1)
    c: Radius(g1) = 0.75
    c: Radius(g0) = 3.75
    c: Radius(g2) = 0.75
    c: Coincident(g1,g3)
    c: Coincident(g2,g3)
    c: Distance(g3) = 2
    c: Angle(g3) = 0
    c: Radius(g4) = 0.75
    c: Coincident(g2,g5)
    c: Coincident(g4,g5)
    c: Equal(g3,g5)
    c: Parallel(g5,g3)
    c: Radius(g6) = 0.75
    c: Coincident(g4,g7)
    c: Coincident(g6,g7)
    c: Equal(g3,g7)
    c: Parallel(g7,g3)
    c: Radius(g8) = 0.75
    c: Coincident(g6,g9)
    c: Coincident(g8,g9)
    c: Equal(g3,g9)
    c: Parallel(g9,g3)
    c: PointOnObject(g2,g-1)
    c: DistanceX(g8,g-1) = 6.5
FEATURE [PartDesign::Pocket] Pocket003088  label="q1_basic_horn_shape005"
  BaseFeature = -> Pocket003084
  Length = 5
  Length2 = 100
  Profile = -> Sketch149
  Refine = true
  Type = 0
FEATURE [Sketcher::SketchObject] Sketch150  label="q2-base003"
  ExternalGeometry = -> [Pocket003088]
  MapMode = 5
  Placement = pos=(-20.5,0,0) rot=(0.57735,-0.57735,-0.57735;2.0944rad)
  Support = -> [Pocket003088]
  sketch-geometry (6):
    g0: LineSegment StartX=-5.71563 StartY=2.25 StartZ=0 EndX=-11.6041 EndY=2.25 EndZ=0
    g1: LineSegment StartX=-11.6041 StartY=2.25 StartZ=0 EndX=-38.6752 EndY=17.8795 EndZ=0
    g2: LineSegment StartX=-11.6626 StartY=5.74787 StartZ=0 EndX=-37.1752 EndY=20.4776 EndZ=0
    g3: LineSegment StartX=-37.1752 StartY=20.4776 StartZ=0 EndX=-38.6752 EndY=17.8795 EndZ=0
    g4: LineSegment StartX=-5.71563 StartY=5.74787 StartZ=0 EndX=-5.71563 EndY=2.25 EndZ=0
    g5: LineSegment StartX=-11.6626 StartY=5.74787 StartZ=0 EndX=-5.71563 EndY=5.74787 EndZ=0
  constraints (13):
    c: Coincident(g3,g2)
    c: Coincident(g3,g1)
    c: Perpendicular(g3,g1)
    c: Coincident(g0,g-3)
    c: Parallel(g1,g2)
    c: Coincident(g4,g0)
    c: Perpendicular(g4,g0)
    c: Distance(g1,g2) = 3
    c: Angle(g0,g1) = 2.61799
    c: Coincident(g0,g1)
    c: Coincident(g2,g5)
    c: Coincident(g5,g4)
    c: Horizontal(g5)
FEATURE [PartDesign::Pad] Pad012045  label="q2-bed-base003"
  BaseFeature = -> Pocket003088
  Length = 26.215
  Length2 = 100
  Profile = -> Sketch150
  Refine = true
  Reversed = true
  Type = 0
FEATURE [Sketcher::SketchObject] Sketch152  label="q2-leg_union_section003"
  ExternalGeometry = -> [Pad012039]
  MapMode = 5
  Placement = pos=(-64.1038,6.2,37.0103) rot=(0,-1,0;1.0472rad)
  Support = -> [Pad012039]
  sketch-geometry (4):
    g0: LineSegment StartX=49.1756 StartY=5.75 StartZ=0 EndX=49.1756 EndY=-32.25 EndZ=0
    g1: LineSegment StartX=49.1756 StartY=-32.25 StartZ=0 EndX=37.6756 EndY=-32.25 EndZ=0
    g2: LineSegment StartX=37.6756 StartY=-32.25 StartZ=0 EndX=37.6756 EndY=5.75 EndZ=0
    g3: LineSegment StartX=37.6756 StartY=5.75 StartZ=0 EndX=49.1756 EndY=5.75 EndZ=0
  constraints (8):
    c: Coincident(g-6,g0)
    c: Coincident(g0,g-6)
    c: Coincident(g0,g1)
    c: Coincident(g1,g-5)
    c: Coincident(g-5,g2)
    c: Coincident(g2,g-4)
    c: Coincident(g2,g3)
    c: Coincident(g3,g0)
FEATURE [PartDesign::AdditivePipe] AdditivePipe003
  AuxilleryCurvelinear = true
  AuxillerySpineTangent = false
  BaseFeature = -> Pad012039
  Binormal = (0,0,0)
  Mode = 0
  Placement = pos=(0,6.2,0) rot=(0,0.707107,0.707107;3.14159rad)
  Profile = -> Sketch152
  Refine = true
  Sections = -> [Sketch143]
  Spine = -> Sketch142
  SpineTangent = false
  Transformation = 1
  Transition = 0
FEATURE [PartDesign::Body] Body017  label="Q2-Leg-joint003"
  Group = -> [Sketch136,Pad012047,Sketch144,Pad012044,Sketch138,Sketch132,Pocket003080,Sketch135,Pocket003083,Sketch148,Pad012037,Sketch145,Pad012039,Sketch142,Sketch152,Sketch143,AdditivePipe003]
  Origin = -> Origin029
  Tip = -> AdditivePipe003
FEATURE [Sketcher::SketchObject] Sketch155  label="q2-corner-hole007"
  MapMode = 5
  Placement = pos=(0,0,5.74787) rot=(0,0,1;0rad)
  Support = -> [Pad012045]
  sketch-geometry (4):
    g0: LineSegment StartX=-1.62396 StartY=12 StartZ=0 EndX=-5 EndY=12 EndZ=0
    g1: LineSegment StartX=-5 StartY=12 StartZ=0 EndX=-5 EndY=6.68085 EndZ=0
    g2: LineSegment StartX=-5 StartY=6.68085 StartZ=0 EndX=-1.62396 EndY=6.68085 EndZ=0
    g3: LineSegment StartX=-1.62396 StartY=6.68085 StartZ=0 EndX=-1.62396 EndY=12 EndZ=0
  constraints (8):
    c: Coincident(g0,g1)
    c: Coincident(g1,g2)
    c: Coincident(g2,g3)
    c: Coincident(g3,g0)
    c: Horizontal(g0)
    c: Horizontal(g2)
    c: Vertical(g1)
    c: Vertical(g3)
FEATURE [PartDesign::Pocket] Pocket003081  label="q2-corner-hole006"
  BaseFeature = -> Pad012045
  Length = 2
  Length2 = 100
  Profile = -> Sketch155
  Refine = true
  Type = 0
FEATURE [Part::Feature] Pocket003092  label="Final-1-arm-horn020"
  Placement = pos=(0,0,32) rot=(0.707107,0.707107,0;3.14159rad)
  shape: bbox 8 x 22.5 x 5 mm, 19 faces (baked)
FEATURE [Part::Feature] Fusion007065  label="Servo-sg90-final022"
  Placement = pos=(0,-16.6,0) rot=(0,0,1;0rad)
  shape: bbox 11.8 x 32.4 x 29.9 mm, 77 faces (baked)
FEATURE [Part::Feature] Pocket003093  label="Final-1-arm-horn021"
  Placement = pos=(0,0,32) rot=(0.707107,-0.707107,0;3.14159rad)
  shape: bbox 8 x 22.5 x 5 mm, 19 faces (baked)
FEATURE [Part::Feature] Fusion007066  label="Servo-sg90-final023"
  Placement = pos=(0,-16.6,0) rot=(0,0,1;0rad)
  shape: bbox 11.8 x 32.4 x 29.9 mm, 77 faces (baked)
FEATURE [Sketcher::SketchObject] Sketch175  label="base_cylinder013"
  MapMode = 5
  Support = -> [XY_Plane033]
  sketch-geometry (2):
    g0: Circle CenterX=0 CenterY=0 CenterZ=0 NormalX=0 NormalY=0 NormalZ=1 AngleXU=0 Radius=3.75
    g1: Circle CenterX=0 CenterY=0 CenterZ=0 NormalX=0 NormalY=0 NormalZ=1 AngleXU=0 Radius=5.75
  constraints (4):
    c: Coincident(g0,g-1)
    c: Radius(g0) = 3.75
    c: Coincident(g1,g-1)
    c: Radius(g1) = 5.75
FEATURE [PartDesign::Pad] Pad012050  label="low_base006"
  Length = 2.25
  Length2 = 100
  Profile = -> Sketch175
  Refine = true
  Type = 0
FEATURE [Sketcher::SketchObject] Sketch160  label="basic_base007"
  MapMode = 5
  Placement = pos=(0,0,2.25) rot=(0,0,1;0rad)
  Support = -> [Pad012050]
  sketch-geometry (6):
    g0: LineSegment StartX=0 StartY=5.71563 StartZ=0 EndX=-20.5 EndY=5.71563 EndZ=0
    g1: LineSegment StartX=1.86762e-06 StartY=-5.71497 StartZ=0 EndX=-20.5 EndY=-5.71497 EndZ=0
    g2: LineSegment StartX=-20.5 StartY=5.71563 StartZ=0 EndX=-20.5 EndY=-5.71497 EndZ=0
    g3: LineSegment StartX=0 StartY=5.71563 StartZ=0 EndX=5.71497 EndY=5.71563 EndZ=0
    g4: LineSegment StartX=5.71497 StartY=5.71563 StartZ=0 EndX=5.71497 EndY=0 EndZ=0
    g5: ArcOfCircle CenterX=0 CenterY=0 CenterZ=0 NormalX=0 NormalY=0 NormalZ=1 AngleXU=0 Radius=5.71497 StartAngle=4.71239 EndAngle=6.28319
  constraints (14):
    c: PointOnObject(g0,g-2)
    c: Horizontal(g0)
    c: DistanceX(g0,g0) = 20.5
    c: Coincident(g2,g0)
    c: Vertical(g2)
    c: Coincident(g1,g2)
    c: Coincident(g0,g3)
    c: Horizontal(g3)
    c: Coincident(g4,g3)
    c: PointOnObject(g4,g-1)
    c: Vertical(g4)
    c: Coincident(g5,g-1)
    c: Coincident(g5,g1)
    c: Coincident(g5,g4)
FEATURE [PartDesign::Pad] Pad012054  label="q1_basic_base006"
  BaseFeature = -> Pad012050
  Length = 3.5
  Length2 = 100
  Profile = -> Sketch160
  Refine = true
  Type = 0
FEATURE [Sketcher::SketchObject] Sketch161  label="q1_base_horn006"
  MapMode = 5
  Placement = pos=(0,0,5.75) rot=(0,0,1;0rad)
  Support = -> [Pad012054]
  sketch-geometry (7):
    g0: LineSegment StartX=-1.25 StartY=3.53553 StartZ=0 EndX=-17 EndY=1.74295 EndZ=0
    g1: ArcOfCircle CenterX=-17 CenterY=0 CenterZ=0 NormalX=0 NormalY=0 NormalZ=1 AngleXU=0 Radius=1.74295 StartAngle=1.5708 EndAngle=3.14159
    g2: LineSegment [constr] StartX=-18.743 StartY=0 StartZ=0 EndX=0 EndY=0 EndZ=0
    g3: ArcOfCircle CenterX=0 CenterY=0 CenterZ=0 NormalX=0 NormalY=0 NormalZ=1 AngleXU=0 Radius=3.75 StartAngle=0 EndAngle=1.91063
    g4: LineSegment StartX=-1.25 StartY=-3.53553 StartZ=0 EndX=-17 EndY=-1.74295 EndZ=0
    g5: ArcOfCircle CenterX=-17 CenterY=-1e-12 CenterZ=0 NormalX=0 NormalY=0 NormalZ=1 AngleXU=0 Radius=1.74295 StartAngle=3.14159 EndAngle=4.71239
    g6: ArcOfCircle CenterX=0 CenterY=0 CenterZ=0 NormalX=0 NormalY=0 NormalZ=1 AngleXU=0 Radius=3.75 StartAngle=4.37255 EndAngle=6.28319
  constraints (11):
    c: PointOnObject(g1,g-1)
    c: Coincident(g1,g0)
    c: PointOnObject(g1,g-1)
    c: Coincident(g1,g2)
    c: Coincident(g3,g-1)
    c: Radius(g3) = 3.75
    c: Coincident(g3,g0)
    c: DistanceX(g0,g3) = 5
    c: Coincident(g5,g4)
    c: Radius(g6) = 3.75
    c: Coincident(g6,g4)
FEATURE [PartDesign::Pocket] Pocket003094  label="q1_basic_horn006"
  BaseFeature = -> Pad012054
  Length = 2.65
  Length2 = 100
  Profile = -> Sketch161
  Refine = true
  Type = 0
FEATURE [Sketcher::SketchObject] Sketch173  label="horn_holes010"
  MapMode = 5
  Placement = pos=(0,0,3.1) rot=(0,0,1;0rad)
  Support = -> [Pocket003094]
  sketch-geometry (10):
    g0: Circle CenterX=0 CenterY=0 CenterZ=0 NormalX=0 NormalY=0 NormalZ=1 AngleXU=0 Radius=3.75
    g1: Circle CenterX=-14.5 CenterY=0 CenterZ=0 NormalX=0 NormalY=0 NormalZ=1 AngleXU=0 Radius=0.75
    g2: Circle CenterX=-12.5 CenterY=0 CenterZ=0 NormalX=0 NormalY=0 NormalZ=1 AngleXU=0 Radius=0.75
    g3: LineSegment [constr] StartX=-14.5 StartY=0 StartZ=0 EndX=-12.5 EndY=0 EndZ=0
    g4: Circle CenterX=-10.5 CenterY=0 CenterZ=0 NormalX=0 NormalY=0 NormalZ=1 AngleXU=0 Radius=0.75
    g5: LineSegment [constr] StartX=-12.5 StartY=0 StartZ=0 EndX=-10.5 EndY=0 EndZ=0
    g6: Circle CenterX=-8.5 CenterY=0 CenterZ=0 NormalX=0 NormalY=0 NormalZ=1 AngleXU=0 Radius=0.75
    g7: LineSegment [constr] StartX=-10.5 StartY=0 StartZ=0 EndX=-8.5 EndY=0 EndZ=0
    g8: Circle CenterX=-6.5 CenterY=0 CenterZ=0 NormalX=0 NormalY=0 NormalZ=1 AngleXU=0 Radius=0.75
    g9: LineSegment [constr] StartX=-8.5 StartY=0 StartZ=0 EndX=-6.5 EndY=0 EndZ=0
  constraints (25):
    c: Coincident(g0,g-1)
    c: Radius(g1) = 0.75
    c: Radius(g0) = 3.75
    c: Radius(g2) = 0.75
    c: Coincident(g1,g3)
    c: Coincident(g2,g3)
    c: Distance(g3) = 2
    c: Angle(g3) = 0
    c: Radius(g4) = 0.75
    c: Coincident(g2,g5)
    c: Coincident(g4,g5)
    c: Equal(g3,g5)
    c: Parallel(g5,g3)
    c: Radius(g6) = 0.75
    c: Coincident(g4,g7)
    c: Coincident(g6,g7)
    c: Equal(g3,g7)
    c: Parallel(g7,g3)
    c: Radius(g8) = 0.75
    c: Coincident(g6,g9)
    c: Coincident(g8,g9)
    c: Equal(g3,g9)
    c: Parallel(g9,g3)
    c: PointOnObject(g2,g-1)
    c: DistanceX(g8,g-1) = 6.5
FEATURE [PartDesign::Pocket] Pocket003096  label="q1_basic_horn_shape006"
  BaseFeature = -> Pocket003094
  Length = 5
  Length2 = 100
  Profile = -> Sketch173
  Refine = true
  Type = 0
FEATURE [Sketcher::SketchObject] Sketch174  label="q2-base004"
  ExternalGeometry = -> [Pocket003096]
  MapMode = 5
  Placement = pos=(-20.5,0,0) rot=(0.57735,-0.57735,-0.57735;2.0944rad)
  Support = -> [Pocket003096]
  sketch-geometry (6):
    g0: LineSegment StartX=-5.71563 StartY=2.25 StartZ=0 EndX=-11.6041 EndY=2.25 EndZ=0
    g1: LineSegment StartX=-11.6041 StartY=2.25 StartZ=0 EndX=-38.6752 EndY=17.8795 EndZ=0
    g2: LineSegment StartX=-11.6626 StartY=5.74787 StartZ=0 EndX=-37.1752 EndY=20.4776 EndZ=0
    g3: LineSegment StartX=-37.1752 StartY=20.4776 StartZ=0 EndX=-38.6752 EndY=17.8795 EndZ=0
    g4: LineSegment StartX=-5.71563 StartY=5.74787 StartZ=0 EndX=-5.71563 EndY=2.25 EndZ=0
    g5: LineSegment StartX=-11.6626 StartY=5.74787 StartZ=0 EndX=-5.71563 EndY=5.74787 EndZ=0
  constraints (13):
    c: Coincident(g3,g2)
    c: Coincident(g3,g1)
    c: Perpendicular(g3,g1)
    c: Coincident(g0,g-3)
    c: Parallel(g1,g2)
    c: Coincident(g4,g0)
    c: Perpendicular(g4,g0)
    c: Distance(g1,g2) = 3
    c: Angle(g0,g1) = 2.61799
    c: Coincident(g0,g1)
    c: Coincident(g2,g5)
    c: Coincident(g5,g4)
    c: Horizontal(g5)
FEATURE [PartDesign::Pad] Pad012056  label="q2-bed-base004"
  BaseFeature = -> Pocket003096
  Length = 26.215
  Length2 = 100
  Profile = -> Sketch174
  Refine = true
  Reversed = true
  Type = 0
FEATURE [Sketcher::SketchObject] Sketch179  label="base_cylinder014"
  MapMode = 5
  Placement = pos=(0,6.2,0) rot=(0,0.707107,0.707107;3.14159rad)
  sketch-geometry (2):
    g0: Circle CenterX=24 CenterY=64 CenterZ=0 NormalX=0 NormalY=0 NormalZ=1 AngleXU=0 Radius=3.75
    g1: Circle CenterX=24 CenterY=64 CenterZ=0 NormalX=0 NormalY=0 NormalZ=1 AngleXU=0 Radius=5.75
  constraints (3):
    c: Radius(g0) = 3.75
    c: Radius(g1) = 5.75
    c: Coincident(g1,g0)
FEATURE [PartDesign::Pad] Pad012058  label="q2_base_cylinder007"
  Length = 2.25
  Length2 = 100
  Placement = pos=(0,6.2,0) rot=(0,0.707107,0.707107;3.14159rad)
  Profile = -> Sketch179
  Refine = true
  Type = 0
FEATURE [Sketcher::SketchObject] Sketch167  label="q2_base006"
  ExternalGeometry = -> [Pad012058]
  MapMode = 5
  Placement = pos=(2e-16,8.45,-9e-16) rot=(0,0.707107,0.707107;3.14159rad)
  Support = -> [Pad012058]
  sketch-geometry (6):
    g0: ArcOfCircle CenterX=24 CenterY=64 CenterZ=0 NormalX=0 NormalY=0 NormalZ=1 AngleXU=0 Radius=5.75 StartAngle=2.0944 EndAngle=5.23599
    g1: LineSegment [constr] StartX=12.5 StartY=64 StartZ=0 EndX=37 EndY=64 EndZ=0
    g2: LineSegment [constr] StartX=24 StartY=64 StartZ=0 EndX=21.125 EndY=68.9796 EndZ=0
    g3: LineSegment StartX=21.125 StartY=68.9796 StartZ=0 EndX=39.516 EndY=79.5977 EndZ=0
    g4: LineSegment StartX=39.516 StartY=79.5977 StartZ=0 EndX=45.266 EndY=69.6384 EndZ=0
    g5: LineSegment StartX=45.266 StartY=69.6384 StartZ=0 EndX=26.875 EndY=59.0204 EndZ=0
  constraints (14):
    c: Coincident(g0,g-3)
    c: PointOnObject(g0,g-3)
    c: Angle(g0) = 3.14159
    c: Horizontal(g1)
    c: PointOnObject(g0,g1)
    c: Coincident(g2,g0)
    c: Coincident(g2,g0)
    c: Angle(g1,g2) = 2.0944
    c: Tangent(g0,g3) = 1.5708
    c: Coincident(g3,g4)
    c: Coincident(g4,g5)
    c: Coincident(g5,g0)
    c: Equal(g3,g5)
    c: Parallel(g3,g5)
FEATURE [PartDesign::Pad] Pad012055  label="q2_basic_base004"
  BaseFeature = -> Pad012058
  Length = 3.5
  Length2 = 100
  Placement = pos=(0,6.2,0) rot=(0,0.707107,0.707107;3.14159rad)
  Profile = -> Sketch167
  Refine = true
  Type = 0
FEATURE [Sketcher::SketchObject] Sketch162  label="AUX_q2_base_horn007"
  ExternalGeometry = -> [Pad012055]
  MapMode = 5
  Placement = pos=(-3e-15,11.95,-6e-15) rot=(0.186157,0.694747,0.694747;3.50969rad)
  sketch-geometry (5):
    g0: LineSegment StartX=54.0346 StartY=46.9656 StartZ=0 EndX=69.7804 EndY=45.1656 EndZ=0
    g1: ArcOfCircle CenterX=69.7804 CenterY=43.4256 CenterZ=0 NormalX=0 NormalY=0 NormalZ=1 AngleXU=0 Radius=1.74 StartAngle=0 EndAngle=1.5708
    g2: LineSegment [constr] StartX=71.5204 StartY=43.4256 StartZ=0 EndX=49.0304 EndY=43.4256 EndZ=0
    g3: ArcOfCircle CenterX=52.7846 CenterY=43.4256 CenterZ=0 NormalX=0 NormalY=0 NormalZ=1 AngleXU=0 Radius=3.75421 StartAngle=1.23136 EndAngle=3.14159
    g4: LineSegment [constr] StartX=52.7846 StartY=49.1756 StartZ=0 EndX=52.7846 EndY=37.6756 EndZ=0
  constraints (16):
    c: Coincident(g1,g0)
    c: Coincident(g1,g2)
    c: Coincident(g3,g0)
    c: Radius(g1) = 1.74
    c: PointOnObject(g1,g2)
    c: Coincident(g2,g3)
    c: PointOnObject(g3,g2)
    c: DistanceX(g2,g2) = 22.49
    c: DistanceY(g1,g0) = 1.74
    c: DistanceX(g3,g0) = 1.25
    c: DistanceY(g3,g0) = 3.54
    c: Horizontal(g2)
    c: Coincident(g4,g-3)
    c: Coincident(g4,g-4)
    c: PointOnObject(g3,g4)
    c: Symmetric(g4,g4,g3)
FEATURE [Sketcher::SketchObject] Sketch163  label="horn_shape008"
  ExternalGeometry = -> [Sketch162]
  MapMode = 5
  Placement = pos=(6e-16,11.95,-5.8e-15) rot=(0,0.707107,0.707107;3.14159rad)
  Support = -> [Pad012055]
  sketch-geometry (7):
    g0: LineSegment [constr] StartX=20.7488 StartY=62.1229 StartZ=0 EndX=40.2257 EndY=73.3679 EndZ=0
    g1: ArcOfCircle CenterX=24 CenterY=64 CenterZ=0 NormalX=0 NormalY=0 NormalZ=1 AngleXU=0 Radius=3.75421 StartAngle=1.75495 EndAngle=3.66519
    g2: ArcOfCircle CenterX=38.7188 CenterY=72.4979 CenterZ=0 NormalX=0 NormalY=0 NormalZ=1 AngleXU=0 Radius=1.74 StartAngle=0.523599 EndAngle=2.0944
    g3: LineSegment StartX=23.3125 StartY=67.6907 StartZ=0 EndX=37.8488 EndY=74.0048 EndZ=0
    g4: ArcOfCircle CenterX=24 CenterY=64 CenterZ=0 NormalX=0 NormalY=0 NormalZ=1 AngleXU=0 Radius=3.75421 StartAngle=3.66519 EndAngle=5.57543
    g5: ArcOfCircle CenterX=38.7188 CenterY=72.4979 CenterZ=0 NormalX=0 NormalY=0 NormalZ=1 AngleXU=0 Radius=1.74 StartAngle=5.23599 EndAngle=6.80678
    g6: LineSegment StartX=26.8525 StartY=61.5593 StartZ=0 EndX=39.5888 EndY=70.991 EndZ=0
  constraints (16):
    c: Coincident(g0,g-5)
    c: Coincident(g0,g-4)
    c: Coincident(g1,g-5)
    c: Coincident(g1,g-5)
    c: Coincident(g1,g0)
    c: Coincident(g2,g-4)
    c: Coincident(g2,g0)
    c: Coincident(g2,g-4)
    c: Coincident(g3,g1)
    c: Coincident(g3,g2)
    c: Coincident(g6,g4)
    c: Coincident(g6,g5)
    c: Coincident(g0,g4)
    c: Coincident(g1,g4)
    c: Coincident(g2,g5)
    c: Coincident(g0,g5)
FEATURE [PartDesign::Pocket] Pocket003098  label="horn_shape009"
  BaseFeature = -> Pad012055
  Length = 2.65
  Length2 = 100
  Placement = pos=(0,6.2,0) rot=(0,0.707107,0.707107;3.14159rad)
  Profile = -> Sketch163
  Refine = true
  Type = 0
FEATURE [Sketcher::SketchObject] Sketch178  label="horn_holes011"
  ExternalGeometry = -> [Pocket003098]
  MapMode = 5
  Placement = pos=(2e-16,9.3,-5.3e-15) rot=(0,0.707107,0.707107;3.14159rad)
  Support = -> [Pocket003098]
  sketch-geometry (16):
    g0: Circle CenterX=24 CenterY=64 CenterZ=0 NormalX=0 NormalY=0 NormalZ=1 AngleXU=0 Radius=3.75
    g1: Circle CenterX=-14.6952 CenterY=0 CenterZ=0 NormalX=0 NormalY=0 NormalZ=1 AngleXU=0 Radius=0.75
    g2: Circle CenterX=-12.6952 CenterY=0 CenterZ=0 NormalX=0 NormalY=0 NormalZ=1 AngleXU=0 Radius=0.75
    g3: LineSegment [constr] StartX=-14.6952 StartY=0 StartZ=0 EndX=-12.6952 EndY=0 EndZ=0
    g4: Circle CenterX=-10.6952 CenterY=0 CenterZ=0 NormalX=0 NormalY=0 NormalZ=1 AngleXU=0 Radius=0.75
    g5: LineSegment [constr] StartX=-12.6952 StartY=0 StartZ=0 EndX=-10.6952 EndY=0 EndZ=0
    g6: Circle CenterX=-8.69518 CenterY=0 CenterZ=0 NormalX=0 NormalY=0 NormalZ=1 AngleXU=0 Radius=0.75
    g7: LineSegment [constr] StartX=-10.6952 StartY=0 StartZ=0 EndX=-8.69518 EndY=0 EndZ=0
    g8: Circle CenterX=-6.69518 CenterY=0 CenterZ=0 NormalX=0 NormalY=0 NormalZ=1 AngleXU=0 Radius=0.75
    g9: LineSegment [constr] StartX=-8.69518 StartY=0 StartZ=0 EndX=-6.69518 EndY=0 EndZ=0
    g10: LineSegment [constr] StartX=24 StartY=64 StartZ=0 EndX=43.3449 EndY=75.1688 EndZ=0
    g11: Circle CenterX=29.6292 CenterY=67.25 CenterZ=0 NormalX=0 NormalY=0 NormalZ=1 AngleXU=0 Radius=0.75
    g12: Circle CenterX=31.3612 CenterY=68.25 CenterZ=0 NormalX=0 NormalY=0 NormalZ=1 AngleXU=0 Radius=0.75
    g13: Circle CenterX=33.0933 CenterY=69.25 CenterZ=0 NormalX=0 NormalY=0 NormalZ=1 AngleXU=0 Radius=0.75
    g14: Circle CenterX=34.8253 CenterY=70.25 CenterZ=0 NormalX=0 NormalY=0 NormalZ=1 AngleXU=0 Radius=0.75
    g15: Circle CenterX=36.5574 CenterY=71.25 CenterZ=0 NormalX=0 NormalY=0 NormalZ=1 AngleXU=0 Radius=0.75
  constraints (41):
    c: Radius(g1) = 0.75
    c: Radius(g0) = 3.75
    c: Radius(g2) = 0.75
    c: Coincident(g1,g3)
    c: Coincident(g2,g3)
    c: Distance(g3) = 2
    c: Angle(g3) = 0
    c: Radius(g4) = 0.75
    c: Coincident(g2,g5)
    c: Coincident(g4,g5)
    c: Equal(g3,g5)
    c: Radius(g6) = 0.75
    c: Coincident(g4,g7)
    c: Coincident(g6,g7)
    c: Equal(g3,g7)
    c: Radius(g8) = 0.75
    c: Coincident(g6,g9)
    c: Coincident(g8,g9)
    c: Equal(g3,g9)
    c: Parallel(g9,g3)
    c: Parallel(g9,g7)
    c: Parallel(g7,g5)
    c: Coincident(g10,g0)
    c: Angle(g10) = 0.523599
    c: Radius(g11) = 0.75
    c: Distance(g0,g11) = 6.5
    c: PointOnObject(g11,g10)
    c: Equal(g11,g12) = 0.75
    c: PointOnObject(g12,g10)
    c: DistanceX(g0) = 24
    c: DistanceY(g0) = 64
    c: Distance(g11,g12) = 2
    c: Equal(g11,g13) = 0.75
    c: PointOnObject(g13,g10)
    c: Equal(g11,g14) = 0.75
    c: PointOnObject(g14,g10)
    c: Equal(g11,g15) = 0.75
    c: PointOnObject(g15,g10)
    c: Distance(g12,g13) = 2
    c: Distance(g13,g14) = 2
    c: Distance(g14,g15) = 2
FEATURE [PartDesign::Pocket] Pocket003090  label="basic_horn_union004"
  BaseFeature = -> Pocket003098
  Length = 5
  Length2 = 100
  Placement = pos=(0,6.2,0) rot=(0,0.707107,0.707107;3.14159rad)
  Profile = -> Sketch178
  Refine = true
  Type = 0
FEATURE [Sketcher::SketchObject] Sketch172  label="q2_bridge009"
  ExternalGeometry = -> [Pocket003090]
  MapMode = 5
  Placement = pos=(2e-16,8.45,-2.3e-15) rot=(0,-0.707107,0.707107;3.14159rad)
  Support = -> [Pocket003090]
  sketch-geometry (4):
    g0: LineSegment StartX=39.516 StartY=-79.5977 StartZ=0 EndX=45.266 EndY=-69.6384 EndZ=0
    g1: LineSegment StartX=45.266 StartY=-69.6384 StartZ=0 EndX=40.9358 EndY=-67.1384 EndZ=0
    g2: LineSegment StartX=39.516 StartY=-79.5977 StartZ=0 EndX=35.1858 EndY=-77.0977 EndZ=0
    g3: ArcOfCircle CenterX=24.5001 CenterY=-64.2888 CenterZ=0 NormalX=0 NormalY=0 NormalZ=1 AngleXU=0 Radius=16.6809 StartAngle=5.40766 EndAngle=6.11151
  constraints (10):
    c: Coincident(g-5,g0)
    c: Coincident(g0,g-5)
    c: Coincident(g0,g1)
    c: PointOnObject(g1,g-3)
    c: Coincident(g0,g2)
    c: PointOnObject(g2,g-4)
    c: Distance(g2) = 5
    c: Equal(g2,g1)
    c: Coincident(g3,g1)
    c: Coincident(g3,g2)
FEATURE [PartDesign::Pad] Pad012052  label="q2_bridge008"
  BaseFeature = -> Pocket003090
  Length = 31
  Length2 = 100
  Placement = pos=(0,6.2,0) rot=(0,0.707107,0.707107;3.14159rad)
  Profile = -> Sketch172
  Refine = true
  Type = 0
FEATURE [Sketcher::SketchObject] Sketch169  label="q2_back_union004"
  ExternalGeometry = -> [Pad012058,Sketch167]
  MapMode = 5
  Placement = pos=(-2.3e-15,-22.55,3.83e-14) rot=(0,-0.707107,0.707107;3.14159rad)
  Support = -> [Pad012052]
  expr: Constraints[2] = Sketch067.Constraints[2]
  sketch-geometry (7):
    g0: ArcOfCircle CenterX=24 CenterY=-64 CenterZ=0 NormalX=0 NormalY=0 NormalZ=1 AngleXU=0 Radius=5.75 StartAngle=1.0472 EndAngle=4.18879
    g1: LineSegment [constr] StartX=12.5 StartY=-64 StartZ=0 EndX=37 EndY=-64 EndZ=0
    g2: LineSegment [constr] StartX=24 StartY=-64 StartZ=0 EndX=26.875 EndY=-59.0204 EndZ=0
    g3: LineSegment StartX=45.266 StartY=-69.6384 StartZ=0 EndX=26.875 EndY=-59.0204 EndZ=0
    g4: LineSegment StartX=45.266 StartY=-69.6384 StartZ=0 EndX=39.516 EndY=-79.5977 EndZ=0
    g5: LineSegment StartX=39.516 StartY=-79.5977 StartZ=0 EndX=21.125 EndY=-68.9796 EndZ=0
    g6: Circle CenterX=24 CenterY=-64 CenterZ=0 NormalX=0 NormalY=0 NormalZ=1 AngleXU=0 Radius=2
  constraints (16):
    c: Coincident(g0,g-3)
    c: PointOnObject(g0,g-3)
    c: Angle(g0) = 3.14159
    c: Horizontal(g1)
    c: PointOnObject(g0,g1)
    c: Coincident(g2,g0)
    c: Coincident(g2,g0)
    c: Parallel(g2,g-4)
    c: Coincident(g-4,g3)
    c: Coincident(g3,g0)
    c: Coincident(g3,g4)
    c: Coincident(g4,g-4)
    c: Coincident(g4,g5)
    c: Coincident(g5,g0)
    c: Coincident(g6,g0)
    c: Radius(g6) = 2
FEATURE [Part::MultiFuse] Fusion007067  label="q1-aux-servo006"
  Placement = pos=(0,0,17.25) rot=(0,0,1;0rad)
  Refine = true
  Shapes = -> [Pocket003093,Fusion007066]
FEATURE [Part::MultiFuse] Fusion007068  label="q2-aux-servo006"
  Placement = pos=(-24,-20.5,64) rot=(-0.377964,0.654654,0.654654;2.41885rad)
  Refine = true
  Shapes = -> [Fusion007065,Pocket003092]
FEATURE [PartDesign::Pad] Pad012059  label="q2_joint004"
  BaseFeature = -> Pad012052
  Length = 3.5
  Length2 = 100
  Placement = pos=(0,6.2,0) rot=(0,0.707107,0.707107;3.14159rad)
  Profile = -> Sketch169
  Refine = true
  Type = 0
FEATURE [Sketcher::SketchObject] Sketch165  label="trajectory004"
  ExternalGeometry = -> [Pad012059]
  MapMode = 5
  Placement = pos=(6e-16,11.95,-5.8e-15) rot=(0,0.707107,0.707107;3.14159rad)
  Support = -> [Pad012059]
  sketch-geometry (8):
    g0: GeomPoint X=42.3808 Y=74.6356 Z=0
    g1-g4: Circle [constr] x4 (B-spline internal-alignment scaffolding for g5; pole/knot coordinates omitted)
    g5: BSplineCurve PolesCount=4 KnotsCount=2 Degree=3 IsPeriodic=0
    g6: GeomPoint [constr] X=42.3808 Y=74.6356 Z=0
    g7: GeomPoint [constr] X=64.6677 Y=0 Z=0
  constraints (10):
    c: PointOnObject(g0,g-3)
    c: Coincident(g1,g0)
    c: Radius(g1) = 4
    c: Equal(g1,g2)
    c: Equal(g1,g3)
    c: Equal(g1,g4)
    c: PointOnObject(g4,g-1)
    c: InternalAlignment(g1-g4 -> g5) x4
    c: InternalAlignment(g6,g5)
    c: InternalAlignment(g7,g5)
FEATURE [Sketcher::SketchObject] Sketch166  label="q2-bone-touch_section004"
  ExternalGeometry = -> [Sketch165,Pad012059]
  MapMode = 5
  Support = -> [XY_Plane031]
  sketch-geometry (7):
    g0: LineSegment StartX=-66.1677 StartY=-4.55 StartZ=0 EndX=-63.1677 EndY=-4.55 EndZ=0
    g1: LineSegment StartX=-63.1677 StartY=-4.55 StartZ=0 EndX=-63.1677 EndY=-9.55 EndZ=0
    g2: LineSegment StartX=-63.1677 StartY=-9.55 StartZ=0 EndX=-66.1677 EndY=-9.55 EndZ=0
    g3: LineSegment StartX=-66.1677 StartY=-9.55 StartZ=0 EndX=-66.1677 EndY=-4.55 EndZ=0
    g4: GeomPoint X=-45.266 Y=-7.05 Z=0
    g5: GeomPoint X=-63.1677 Y=-7.05 Z=0
    g6: GeomPoint X=-64.6677 Y=-4.55 Z=0
  constraints (18):
    c: Coincident(g0,g1)
    c: Coincident(g1,g2)
    c: Coincident(g2,g3)
    c: Coincident(g3,g0)
    c: Horizontal(g0)
    c: Horizontal(g2)
    c: Vertical(g1)
    c: Vertical(g3)
    c: PointOnObject(g4,g-4)
    c: Symmetric(g-4,g-4,g4)
    c: PointOnObject(g5,g1)
    c: Symmetric(g0,g1,g5)
    c: Horizontal(g5,g4)
    c: PointOnObject(g6,g0)
    c: Symmetric(g0,g0,g6)
    c: Vertical(g6,g-3)
    c: DistanceX(g2,g2) = 3
    c: DistanceY(g3,g3) = 5
FEATURE [Sketcher::SketchObject] Sketch176  label="q2-leg_union_section004"
  ExternalGeometry = -> [Pad012059]
  MapMode = 5
  Placement = pos=(-64.1038,6.2,37.0103) rot=(0,-1,0;1.0472rad)
  Support = -> [Pad012059]
  sketch-geometry (4):
    g0: LineSegment StartX=49.1756 StartY=5.75 StartZ=0 EndX=49.1756 EndY=-32.25 EndZ=0
    g1: LineSegment StartX=49.1756 StartY=-32.25 StartZ=0 EndX=37.6756 EndY=-32.25 EndZ=0
    g2: LineSegment StartX=37.6756 StartY=-32.25 StartZ=0 EndX=37.6756 EndY=5.75 EndZ=0
    g3: LineSegment StartX=37.6756 StartY=5.75 StartZ=0 EndX=49.1756 EndY=5.75 EndZ=0
  constraints (8):
    c: Coincident(g-6,g0)
    c: Coincident(g0,g-6)
    c: Coincident(g0,g1)
    c: Coincident(g1,g-5)
    c: Coincident(g-5,g2)
    c: Coincident(g2,g-4)
    c: Coincident(g2,g3)
    c: Coincident(g3,g0)
FEATURE [PartDesign::AdditivePipe] AdditivePipe004
  AuxilleryCurvelinear = true
  AuxillerySpineTangent = false
  BaseFeature = -> Pad012059
  Binormal = (0,0,0)
  Mode = 0
  Placement = pos=(0,6.2,0) rot=(0,0.707107,0.707107;3.14159rad)
  Profile = -> Sketch176
  Refine = true
  Sections = -> [Sketch166]
  Spine = -> Sketch165
  SpineTangent = false
  Transformation = 1
  Transition = 0
FEATURE [PartDesign::Body] Body019  label="Q2-Leg-joint004"
  Group = -> [Sketch179,Pad012058,Sketch167,Pad012055,Sketch162,Sketch163,Pocket003098,Sketch178,Pocket003090,Sketch172,Pad012052,Sketch169,Pad012059,Sketch165,Sketch176,Sketch166,AdditivePipe004]
  Origin = -> Origin031
  Tip = -> AdditivePipe004
FEATURE [Sketcher::SketchObject] Sketch181  label="q2-corner-hole009"
  MapMode = 5
  Placement = pos=(0,0,5.74787) rot=(0,0,1;0rad)
  Support = -> [Pad012056]
  sketch-geometry (4):
    g0: LineSegment StartX=-1.62396 StartY=12 StartZ=0 EndX=-5 EndY=12 EndZ=0
    g1: LineSegment StartX=-5 StartY=12 StartZ=0 EndX=-5 EndY=6.68085 EndZ=0
    g2: LineSegment StartX=-5 StartY=6.68085 StartZ=0 EndX=-1.62396 EndY=6.68085 EndZ=0
    g3: LineSegment StartX=-1.62396 StartY=6.68085 StartZ=0 EndX=-1.62396 EndY=12 EndZ=0
  constraints (8):
    c: Coincident(g0,g1)
    c: Coincident(g1,g2)
    c: Coincident(g2,g3)
    c: Coincident(g3,g0)
    c: Horizontal(g0)
    c: Horizontal(g2)
    c: Vertical(g1)
    c: Vertical(g3)
FEATURE [PartDesign::Pocket] Pocket003097  label="q2-corner-hole008"
  BaseFeature = -> Pad012056
  Length = 2
  Length2 = 100
  Profile = -> Sketch181
  Refine = true
  Type = 0
FEATURE [Part::Feature] Pocket003103  label="Final-1-arm-horn022"
  Placement = pos=(0,0,32) rot=(0.707107,-0.707107,0;3.14159rad)
  shape: bbox 8 x 22.5 x 5 mm, 19 faces (baked)
FEATURE [Part::Feature] Fusion007071  label="Servo-sg90-final024"
  Placement = pos=(0,-16.6,0) rot=(0,0,1;0rad)
  shape: bbox 11.8 x 32.4 x 29.9 mm, 77 faces (baked)
FEATURE [Part::MultiFuse] Fusion007070  label="q1-aux-servo007"
  Placement = pos=(0,0,17.25) rot=(0,0,1;0rad)
  Refine = true
  Shapes = -> [Pocket003103,Fusion007071]
FEATURE [Part::Feature] Pocket003105  label="Final-1-arm-horn023"
  Placement = pos=(0,0,32) rot=(0.707107,0.707107,0;3.14159rad)
  shape: bbox 8 x 22.5 x 5 mm, 19 faces (baked)
FEATURE [Part::Feature] Fusion007072  label="Servo-sg90-final025"
  Placement = pos=(0,-16.6,0) rot=(0,0,1;0rad)
  shape: bbox 11.8 x 32.4 x 29.9 mm, 77 faces (baked)
FEATURE [Part::MultiFuse] Fusion007069  label="q2-aux-servo007"
  Placement = pos=(-24,-20.5,64) rot=(-0.377964,0.654654,0.654654;2.41885rad)
  Refine = true
  Shapes = -> [Fusion007072,Pocket003105]
FEATURE [Sketcher::SketchObject] Sketch198  label="base_cylinder016"
  MapMode = 5
  Placement = pos=(0,6.2,0) rot=(0,0.707107,0.707107;3.14159rad)
  sketch-geometry (2):
    g0: Circle CenterX=24 CenterY=64 CenterZ=0 NormalX=0 NormalY=0 NormalZ=1 AngleXU=0 Radius=3.75
    g1: Circle CenterX=24 CenterY=64 CenterZ=0 NormalX=0 NormalY=0 NormalZ=1 AngleXU=0 Radius=5.75
  constraints (3):
    c: Radius(g0) = 3.75
    c: Radius(g1) = 5.75
    c: Coincident(g1,g0)
FEATURE [PartDesign::Pad] Pad012068  label="q2_base_cylinder009"
  Length = 2.25
  Length2 = 100
  Placement = pos=(0,6.2,0) rot=(0,0.707107,0.707107;3.14159rad)
  Profile = -> Sketch198
  Refine = true
  Type = 0
FEATURE [Sketcher::SketchObject] Sketch196  label="q2_base008"
  ExternalGeometry = -> [Pad012068]
  MapMode = 5
  Placement = pos=(2e-16,8.45,-9e-16) rot=(0,0.707107,0.707107;3.14159rad)
  Support = -> [Pad012068]
  sketch-geometry (6):
    g0: ArcOfCircle CenterX=24 CenterY=64 CenterZ=0 NormalX=0 NormalY=0 NormalZ=1 AngleXU=0 Radius=5.75 StartAngle=2.0944 EndAngle=5.23599
    g1: LineSegment [constr] StartX=12.5 StartY=64 StartZ=0 EndX=37 EndY=64 EndZ=0
    g2: LineSegment [constr] StartX=24 StartY=64 StartZ=0 EndX=21.125 EndY=68.9796 EndZ=0
    g3: LineSegment StartX=21.125 StartY=68.9796 StartZ=0 EndX=39.516 EndY=79.5977 EndZ=0
    g4: LineSegment StartX=39.516 StartY=79.5977 StartZ=0 EndX=45.266 EndY=69.6384 EndZ=0
    g5: LineSegment StartX=45.266 StartY=69.6384 StartZ=0 EndX=26.875 EndY=59.0204 EndZ=0
  constraints (14):
    c: Coincident(g0,g-3)
    c: PointOnObject(g0,g-3)
    c: Angle(g0) = 3.14159
    c: Horizontal(g1)
    c: PointOnObject(g0,g1)
    c: Coincident(g2,g0)
    c: Coincident(g2,g0)
    c: Angle(g1,g2) = 2.0944
    c: Tangent(g0,g3) = 1.5708
    c: Coincident(g3,g4)
    c: Coincident(g4,g5)
    c: Coincident(g5,g0)
    c: Equal(g3,g5)
    c: Parallel(g3,g5)
FEATURE [PartDesign::Pad] Pad012065  label="q2_basic_base005"
  BaseFeature = -> Pad012068
  Length = 3.5
  Length2 = 100
  Placement = pos=(0,6.2,0) rot=(0,0.707107,0.707107;3.14159rad)
  Profile = -> Sketch196
  Refine = true
  Type = 0
FEATURE [Sketcher::SketchObject] Sketch197  label="AUX_q2_base_horn008"
  ExternalGeometry = -> [Pad012065]
  MapMode = 5
  Placement = pos=(-3e-15,11.95,-6e-15) rot=(0.186157,0.694747,0.694747;3.50969rad)
  sketch-geometry (5):
    g0: LineSegment StartX=54.0346 StartY=46.9656 StartZ=0 EndX=69.7804 EndY=45.1656 EndZ=0
    g1: ArcOfCircle CenterX=69.7804 CenterY=43.4256 CenterZ=0 NormalX=0 NormalY=0 NormalZ=1 AngleXU=0 Radius=1.74 StartAngle=0 EndAngle=1.5708
    g2: LineSegment [constr] StartX=71.5204 StartY=43.4256 StartZ=0 EndX=49.0304 EndY=43.4256 EndZ=0
    g3: ArcOfCircle CenterX=52.7846 CenterY=43.4256 CenterZ=0 NormalX=0 NormalY=0 NormalZ=1 AngleXU=0 Radius=3.75421 StartAngle=1.23136 EndAngle=3.14159
    g4: LineSegment [constr] StartX=52.7846 StartY=49.1756 StartZ=0 EndX=52.7846 EndY=37.6756 EndZ=0
  constraints (16):
    c: Coincident(g1,g0)
    c: Coincident(g1,g2)
    c: Coincident(g3,g0)
    c: Radius(g1) = 1.74
    c: PointOnObject(g1,g2)
    c: Coincident(g2,g3)
    c: PointOnObject(g3,g2)
    c: DistanceX(g2,g2) = 22.49
    c: DistanceY(g1,g0) = 1.74
    c: DistanceX(g3,g0) = 1.25
    c: DistanceY(g3,g0) = 3.54
    c: Horizontal(g2)
    c: Coincident(g4,g-3)
    c: Coincident(g4,g-4)
    c: PointOnObject(g3,g4)
    c: Symmetric(g4,g4,g3)
FEATURE [Sketcher::SketchObject] Sketch195  label="horn_shape010"
  ExternalGeometry = -> [Sketch197]
  MapMode = 5
  Placement = pos=(6e-16,11.95,-5.8e-15) rot=(0,0.707107,0.707107;3.14159rad)
  Support = -> [Pad012065]
  sketch-geometry (7):
    g0: LineSegment [constr] StartX=20.7488 StartY=62.1229 StartZ=0 EndX=40.2257 EndY=73.3679 EndZ=0
    g1: ArcOfCircle CenterX=24 CenterY=64 CenterZ=0 NormalX=0 NormalY=0 NormalZ=1 AngleXU=0 Radius=3.75421 StartAngle=1.75495 EndAngle=3.66519
    g2: ArcOfCircle CenterX=38.7188 CenterY=72.4979 CenterZ=0 NormalX=0 NormalY=0 NormalZ=1 AngleXU=0 Radius=1.74 StartAngle=0.523599 EndAngle=2.0944
    g3: LineSegment StartX=23.3125 StartY=67.6907 StartZ=0 EndX=37.8488 EndY=74.0048 EndZ=0
    g4: ArcOfCircle CenterX=24 CenterY=64 CenterZ=0 NormalX=0 NormalY=0 NormalZ=1 AngleXU=0 Radius=3.75421 StartAngle=3.66519 EndAngle=5.57543
    g5: ArcOfCircle CenterX=38.7188 CenterY=72.4979 CenterZ=0 NormalX=0 NormalY=0 NormalZ=1 AngleXU=0 Radius=1.74 StartAngle=5.23599 EndAngle=6.80678
    g6: LineSegment StartX=26.8525 StartY=61.5593 StartZ=0 EndX=39.5888 EndY=70.991 EndZ=0
  constraints (16):
    c: Coincident(g0,g-5)
    c: Coincident(g0,g-4)
    c: Coincident(g1,g-5)
    c: Coincident(g1,g-5)
    c: Coincident(g1,g0)
    c: Coincident(g2,g-4)
    c: Coincident(g2,g0)
    c: Coincident(g2,g-4)
    c: Coincident(g3,g1)
    c: Coincident(g3,g2)
    c: Coincident(g6,g4)
    c: Coincident(g6,g5)
    c: Coincident(g0,g4)
    c: Coincident(g1,g4)
    c: Coincident(g2,g5)
    c: Coincident(g0,g5)
FEATURE [Sketcher::SketchObject] Sketch203  label="base_cylinder017"
  MapMode = 5
  Support = -> [XY_Plane036]
  sketch-geometry (2):
    g0: Circle CenterX=0 CenterY=0 CenterZ=0 NormalX=0 NormalY=0 NormalZ=1 AngleXU=0 Radius=3.75
    g1: Circle CenterX=0 CenterY=0 CenterZ=0 NormalX=0 NormalY=0 NormalZ=1 AngleXU=0 Radius=5.75
  constraints (4):
    c: Coincident(g0,g-1)
    c: Radius(g0) = 3.75
    c: Coincident(g1,g-1)
    c: Radius(g1) = 5.75
FEATURE [PartDesign::Pad] Pad012062  label="low_base007"
  Length = 2.25
  Length2 = 100
  Profile = -> Sketch203
  Refine = true
  Type = 0
FEATURE [Sketcher::SketchObject] Sketch194  label="basic_base008"
  MapMode = 5
  Placement = pos=(0,0,2.25) rot=(0,0,1;0rad)
  Support = -> [Pad012062]
  sketch-geometry (6):
    g0: LineSegment StartX=0 StartY=5.71563 StartZ=0 EndX=-20.5 EndY=5.71563 EndZ=0
    g1: LineSegment StartX=1.86762e-06 StartY=-5.71497 StartZ=0 EndX=-20.5 EndY=-5.71497 EndZ=0
    g2: LineSegment StartX=-20.5 StartY=5.71563 StartZ=0 EndX=-20.5 EndY=-5.71497 EndZ=0
    g3: LineSegment StartX=0 StartY=5.71563 StartZ=0 EndX=5.71497 EndY=5.71563 EndZ=0
    g4: LineSegment StartX=5.71497 StartY=5.71563 StartZ=0 EndX=5.71497 EndY=0 EndZ=0
    g5: ArcOfCircle CenterX=0 CenterY=0 CenterZ=0 NormalX=0 NormalY=0 NormalZ=1 AngleXU=0 Radius=5.71497 StartAngle=4.71239 EndAngle=6.28319
  constraints (14):
    c: PointOnObject(g0,g-2)
    c: Horizontal(g0)
    c: DistanceX(g0,g0) = 20.5
    c: Coincident(g2,g0)
    c: Vertical(g2)
    c: Coincident(g1,g2)
    c: Coincident(g0,g3)
    c: Horizontal(g3)
    c: Coincident(g4,g3)
    c: PointOnObject(g4,g-1)
    c: Vertical(g4)
    c: Coincident(g5,g-1)
    c: Coincident(g5,g1)
    c: Coincident(g5,g4)
FEATURE [PartDesign::Pocket] Pocket003108  label="horn_shape011"
  BaseFeature = -> Pad012065
  Length = 2.65
  Length2 = 100
  Placement = pos=(0,6.2,0) rot=(0,0.707107,0.707107;3.14159rad)
  Profile = -> Sketch195
  Refine = true
  Type = 0
FEATURE [Sketcher::SketchObject] Sketch192  label="horn_holes012"
  ExternalGeometry = -> [Pocket003108]
  MapMode = 5
  Placement = pos=(2e-16,9.3,-5.3e-15) rot=(0,0.707107,0.707107;3.14159rad)
  Support = -> [Pocket003108]
  sketch-geometry (16):
    g0: Circle CenterX=24 CenterY=64 CenterZ=0 NormalX=0 NormalY=0 NormalZ=1 AngleXU=0 Radius=3.75
    g1: Circle CenterX=-14.6952 CenterY=0 CenterZ=0 NormalX=0 NormalY=0 NormalZ=1 AngleXU=0 Radius=0.75
    g2: Circle CenterX=-12.6952 CenterY=0 CenterZ=0 NormalX=0 NormalY=0 NormalZ=1 AngleXU=0 Radius=0.75
    g3: LineSegment [constr] StartX=-14.6952 StartY=0 StartZ=0 EndX=-12.6952 EndY=0 EndZ=0
    g4: Circle CenterX=-10.6952 CenterY=0 CenterZ=0 NormalX=0 NormalY=0 NormalZ=1 AngleXU=0 Radius=0.75
    g5: LineSegment [constr] StartX=-12.6952 StartY=0 StartZ=0 EndX=-10.6952 EndY=0 EndZ=0
    g6: Circle CenterX=-8.69518 CenterY=0 CenterZ=0 NormalX=0 NormalY=0 NormalZ=1 AngleXU=0 Radius=0.75
    g7: LineSegment [constr] StartX=-10.6952 StartY=0 StartZ=0 EndX=-8.69518 EndY=0 EndZ=0
    g8: Circle CenterX=-6.69518 CenterY=0 CenterZ=0 NormalX=0 NormalY=0 NormalZ=1 AngleXU=0 Radius=0.75
    g9: LineSegment [constr] StartX=-8.69518 StartY=0 StartZ=0 EndX=-6.69518 EndY=0 EndZ=0
    g10: LineSegment [constr] StartX=24 StartY=64 StartZ=0 EndX=43.3449 EndY=75.1688 EndZ=0
    g11: Circle CenterX=29.6292 CenterY=67.25 CenterZ=0 NormalX=0 NormalY=0 NormalZ=1 AngleXU=0 Radius=0.75
    g12: Circle CenterX=31.3612 CenterY=68.25 CenterZ=0 NormalX=0 NormalY=0 NormalZ=1 AngleXU=0 Radius=0.75
    g13: Circle CenterX=33.0933 CenterY=69.25 CenterZ=0 NormalX=0 NormalY=0 NormalZ=1 AngleXU=0 Radius=0.75
    g14: Circle CenterX=34.8253 CenterY=70.25 CenterZ=0 NormalX=0 NormalY=0 NormalZ=1 AngleXU=0 Radius=0.75
    g15: Circle CenterX=36.5574 CenterY=71.25 CenterZ=0 NormalX=0 NormalY=0 NormalZ=1 AngleXU=0 Radius=0.75
  constraints (41):
    c: Radius(g1) = 0.75
    c: Radius(g0) = 3.75
    c: Radius(g2) = 0.75
    c: Coincident(g1,g3)
    c: Coincident(g2,g3)
    c: Distance(g3) = 2
    c: Angle(g3) = 0
    c: Radius(g4) = 0.75
    c: Coincident(g2,g5)
    c: Coincident(g4,g5)
    c: Equal(g3,g5)
    c: Radius(g6) = 0.75
    c: Coincident(g4,g7)
    c: Coincident(g6,g7)
    c: Equal(g3,g7)
    c: Radius(g8) = 0.75
    c: Coincident(g6,g9)
    c: Coincident(g8,g9)
    c: Equal(g3,g9)
    c: Parallel(g9,g3)
    c: Parallel(g9,g7)
    c: Parallel(g7,g5)
    c: Coincident(g10,g0)
    c: Angle(g10) = 0.523599
    c: Radius(g11) = 0.75
    c: Distance(g0,g11) = 6.5
    c: PointOnObject(g11,g10)
    c: Equal(g11,g12) = 0.75
    c: PointOnObject(g12,g10)
    c: DistanceX(g0) = 24
    c: DistanceY(g0) = 64
    c: Distance(g11,g12) = 2
    c: Equal(g11,g13) = 0.75
    c: PointOnObject(g13,g10)
    c: Equal(g11,g14) = 0.75
    c: PointOnObject(g14,g10)
    c: Equal(g11,g15) = 0.75
    c: PointOnObject(g15,g10)
    c: Distance(g12,g13) = 2
    c: Distance(g13,g14) = 2
    c: Distance(g14,g15) = 2
FEATURE [PartDesign::Pocket] Pocket003104  label="basic_horn_union005"
  BaseFeature = -> Pocket003108
  Length = 5
  Length2 = 100
  Placement = pos=(0,6.2,0) rot=(0,0.707107,0.707107;3.14159rad)
  Profile = -> Sketch192
  Refine = true
  Type = 0
FEATURE [Sketcher::SketchObject] Sketch205  label="q2_bridge011"
  ExternalGeometry = -> [Pocket003104]
  MapMode = 5
  Placement = pos=(2e-16,8.45,-2.3e-15) rot=(0,-0.707107,0.707107;3.14159rad)
  Support = -> [Pocket003104]
  sketch-geometry (4):
    g0: LineSegment StartX=39.516 StartY=-79.5977 StartZ=0 EndX=45.266 EndY=-69.6384 EndZ=0
    g1: LineSegment StartX=45.266 StartY=-69.6384 StartZ=0 EndX=40.9358 EndY=-67.1384 EndZ=0
    g2: LineSegment StartX=39.516 StartY=-79.5977 StartZ=0 EndX=35.1858 EndY=-77.0977 EndZ=0
    g3: ArcOfCircle CenterX=24.5001 CenterY=-64.2888 CenterZ=0 NormalX=0 NormalY=0 NormalZ=1 AngleXU=0 Radius=16.6809 StartAngle=5.40766 EndAngle=6.11151
  constraints (10):
    c: Coincident(g-5,g0)
    c: Coincident(g0,g-5)
    c: Coincident(g0,g1)
    c: PointOnObject(g1,g-3)
    c: Coincident(g0,g2)
    c: PointOnObject(g2,g-4)
    c: Distance(g2) = 5
    c: Equal(g2,g1)
    c: Coincident(g3,g1)
    c: Coincident(g3,g2)
FEATURE [PartDesign::Pad] Pad012063  label="q2_bridge010"
  BaseFeature = -> Pocket003104
  Length = 31
  Length2 = 100
  Placement = pos=(0,6.2,0) rot=(0,0.707107,0.707107;3.14159rad)
  Profile = -> Sketch205
  Refine = true
  Type = 0
FEATURE [Sketcher::SketchObject] Sketch191  label="q2_back_union005"
  ExternalGeometry = -> [Pad012068,Sketch196]
  MapMode = 5
  Placement = pos=(-2.3e-15,-22.55,3.83e-14) rot=(0,-0.707107,0.707107;3.14159rad)
  Support = -> [Pad012063]
  expr: Constraints[2] = Sketch067.Constraints[2]
  sketch-geometry (7):
    g0: ArcOfCircle CenterX=24 CenterY=-64 CenterZ=0 NormalX=0 NormalY=0 NormalZ=1 AngleXU=0 Radius=5.75 StartAngle=1.0472 EndAngle=4.18879
    g1: LineSegment [constr] StartX=12.5 StartY=-64 StartZ=0 EndX=37 EndY=-64 EndZ=0
    g2: LineSegment [constr] StartX=24 StartY=-64 StartZ=0 EndX=26.875 EndY=-59.0204 EndZ=0
    g3: LineSegment StartX=45.266 StartY=-69.6384 StartZ=0 EndX=26.875 EndY=-59.0204 EndZ=0
    g4: LineSegment StartX=45.266 StartY=-69.6384 StartZ=0 EndX=39.516 EndY=-79.5977 EndZ=0
    g5: LineSegment StartX=39.516 StartY=-79.5977 StartZ=0 EndX=21.125 EndY=-68.9796 EndZ=0
    g6: Circle CenterX=24 CenterY=-64 CenterZ=0 NormalX=0 NormalY=0 NormalZ=1 AngleXU=0 Radius=2
  constraints (16):
    c: Coincident(g0,g-3)
    c: PointOnObject(g0,g-3)
    c: Angle(g0) = 3.14159
    c: Horizontal(g1)
    c: PointOnObject(g0,g1)
    c: Coincident(g2,g0)
    c: Coincident(g2,g0)
    c: Parallel(g2,g-4)
    c: Coincident(g-4,g3)
    c: Coincident(g3,g0)
    c: Coincident(g3,g4)
    c: Coincident(g4,g-4)
    c: Coincident(g4,g5)
    c: Coincident(g5,g0)
    c: Coincident(g6,g0)
    c: Radius(g6) = 2
FEATURE [PartDesign::Pad] Pad012067  label="q2_joint005"
  BaseFeature = -> Pad012063
  Length = 3.5
  Length2 = 100
  Placement = pos=(0,6.2,0) rot=(0,0.707107,0.707107;3.14159rad)
  Profile = -> Sketch191
  Refine = true
  Type = 0
FEATURE [Sketcher::SketchObject] Sketch188  label="trajectory005"
  ExternalGeometry = -> [Pad012067]
  MapMode = 5
  Placement = pos=(6e-16,11.95,-5.8e-15) rot=(0,0.707107,0.707107;3.14159rad)
  Support = -> [Pad012067]
  sketch-geometry (8):
    g0: GeomPoint X=42.3808 Y=74.6356 Z=0
    g1-g4: Circle [constr] x4 (B-spline internal-alignment scaffolding for g5; pole/knot coordinates omitted)
    g5: BSplineCurve PolesCount=4 KnotsCount=2 Degree=3 IsPeriodic=0
    g6: GeomPoint [constr] X=42.3808 Y=74.6356 Z=0
    g7: GeomPoint [constr] X=64.6677 Y=0 Z=0
  constraints (10):
    c: PointOnObject(g0,g-3)
    c: Coincident(g1,g0)
    c: Radius(g1) = 4
    c: Equal(g1,g2)
    c: Equal(g1,g3)
    c: Equal(g1,g4)
    c: PointOnObject(g4,g-1)
    c: InternalAlignment(g1-g4 -> g5) x4
    c: InternalAlignment(g6,g5)
    c: InternalAlignment(g7,g5)
FEATURE [Sketcher::SketchObject] Sketch190  label="q2-bone-touch_section005"
  ExternalGeometry = -> [Sketch188,Pad012067]
  MapMode = 5
  Support = -> [XY_Plane034]
  sketch-geometry (7):
    g0: LineSegment StartX=-66.1677 StartY=-4.55 StartZ=0 EndX=-63.1677 EndY=-4.55 EndZ=0
    g1: LineSegment StartX=-63.1677 StartY=-4.55 StartZ=0 EndX=-63.1677 EndY=-9.55 EndZ=0
    g2: LineSegment StartX=-63.1677 StartY=-9.55 StartZ=0 EndX=-66.1677 EndY=-9.55 EndZ=0
    g3: LineSegment StartX=-66.1677 StartY=-9.55 StartZ=0 EndX=-66.1677 EndY=-4.55 EndZ=0
    g4: GeomPoint X=-45.266 Y=-7.05 Z=0
    g5: GeomPoint X=-63.1677 Y=-7.05 Z=0
    g6: GeomPoint X=-64.6677 Y=-4.55 Z=0
  constraints (18):
    c: Coincident(g0,g1)
    c: Coincident(g1,g2)
    c: Coincident(g2,g3)
    c: Coincident(g3,g0)
    c: Horizontal(g0)
    c: Horizontal(g2)
    c: Vertical(g1)
    c: Vertical(g3)
    c: PointOnObject(g4,g-4)
    c: Symmetric(g-4,g-4,g4)
    c: PointOnObject(g5,g1)
    c: Symmetric(g0,g1,g5)
    c: Horizontal(g5,g4)
    c: PointOnObject(g6,g0)
    c: Symmetric(g0,g0,g6)
    c: Vertical(g6,g-3)
    c: DistanceX(g2,g2) = 3
    c: DistanceY(g3,g3) = 5
FEATURE [Sketcher::SketchObject] Sketch204  label="q2-leg_union_section005"
  ExternalGeometry = -> [Pad012067]
  MapMode = 5
  Placement = pos=(-64.1038,6.2,37.0103) rot=(0,-1,0;1.0472rad)
  Support = -> [Pad012067]
  sketch-geometry (4):
    g0: LineSegment StartX=49.1756 StartY=5.75 StartZ=0 EndX=49.1756 EndY=-32.25 EndZ=0
    g1: LineSegment StartX=49.1756 StartY=-32.25 StartZ=0 EndX=37.6756 EndY=-32.25 EndZ=0
    g2: LineSegment StartX=37.6756 StartY=-32.25 StartZ=0 EndX=37.6756 EndY=5.75 EndZ=0
    g3: LineSegment StartX=37.6756 StartY=5.75 StartZ=0 EndX=49.1756 EndY=5.75 EndZ=0
  constraints (8):
    c: Coincident(g-6,g0)
    c: Coincident(g0,g-6)
    c: Coincident(g0,g1)
    c: Coincident(g1,g-5)
    c: Coincident(g-5,g2)
    c: Coincident(g2,g-4)
    c: Coincident(g2,g3)
    c: Coincident(g3,g0)
FEATURE [PartDesign::AdditivePipe] AdditivePipe005
  AuxilleryCurvelinear = true
  AuxillerySpineTangent = false
  BaseFeature = -> Pad012067
  Binormal = (0,0,0)
  Mode = 0
  Placement = pos=(0,6.2,0) rot=(0,0.707107,0.707107;3.14159rad)
  Profile = -> Sketch204
  Refine = true
  Sections = -> [Sketch190]
  Spine = -> Sketch188
  SpineTangent = false
  Transformation = 1
  Transition = 0
FEATURE [PartDesign::Body] Body021  label="Q2-Leg-joint005"
  Group = -> [Sketch198,Pad012068,Sketch196,Pad012065,Sketch197,Sketch195,Pocket003108,Sketch192,Pocket003104,Sketch205,Pad012063,Sketch191,Pad012067,Sketch188,Sketch204,Sketch190,AdditivePipe005]
  Origin = -> Origin036
  Tip = -> AdditivePipe005
FEATURE [PartDesign::Pad] Pad012071  label="q1_basic_base007"
  BaseFeature = -> Pad012062
  Length = 3.5
  Length2 = 100
  Profile = -> Sketch194
  Refine = true
  Type = 0
FEATURE [Sketcher::SketchObject] Sketch189  label="q1_base_horn007"
  MapMode = 5
  Placement = pos=(0,0,5.75) rot=(0,0,1;0rad)
  Support = -> [Pad012071]
  sketch-geometry (7):
    g0: LineSegment StartX=-1.25 StartY=3.53553 StartZ=0 EndX=-17 EndY=1.74295 EndZ=0
    g1: ArcOfCircle CenterX=-17 CenterY=0 CenterZ=0 NormalX=0 NormalY=0 NormalZ=1 AngleXU=0 Radius=1.74295 StartAngle=1.5708 EndAngle=3.14159
    g2: LineSegment [constr] StartX=-18.743 StartY=0 StartZ=0 EndX=0 EndY=0 EndZ=0
    g3: ArcOfCircle CenterX=0 CenterY=0 CenterZ=0 NormalX=0 NormalY=0 NormalZ=1 AngleXU=0 Radius=3.75 StartAngle=0 EndAngle=1.91063
    g4: LineSegment StartX=-1.25 StartY=-3.53553 StartZ=0 EndX=-17 EndY=-1.74295 EndZ=0
    g5: ArcOfCircle CenterX=-17 CenterY=-1e-12 CenterZ=0 NormalX=0 NormalY=0 NormalZ=1 AngleXU=0 Radius=1.74295 StartAngle=3.14159 EndAngle=4.71239
    g6: ArcOfCircle CenterX=0 CenterY=0 CenterZ=0 NormalX=0 NormalY=0 NormalZ=1 AngleXU=0 Radius=3.75 StartAngle=4.37255 EndAngle=6.28319
  constraints (11):
    c: PointOnObject(g1,g-1)
    c: Coincident(g1,g0)
    c: PointOnObject(g1,g-1)
    c: Coincident(g1,g2)
    c: Coincident(g3,g-1)
    c: Radius(g3) = 3.75
    c: Coincident(g3,g0)
    c: DistanceX(g0,g3) = 5
    c: Coincident(g5,g4)
    c: Radius(g6) = 3.75
    c: Coincident(g6,g4)
FEATURE [PartDesign::Pocket] Pocket003100  label="q1_basic_horn007"
  BaseFeature = -> Pad012071
  Length = 2.65
  Length2 = 100
  Profile = -> Sketch189
  Refine = true
  Type = 0
FEATURE [Sketcher::SketchObject] Sketch207  label="horn_holes013"
  MapMode = 5
  Placement = pos=(0,0,3.1) rot=(0,0,1;0rad)
  Support = -> [Pocket003100]
  sketch-geometry (10):
    g0: Circle CenterX=0 CenterY=0 CenterZ=0 NormalX=0 NormalY=0 NormalZ=1 AngleXU=0 Radius=3.75
    g1: Circle CenterX=-14.5 CenterY=0 CenterZ=0 NormalX=0 NormalY=0 NormalZ=1 AngleXU=0 Radius=0.75
    g2: Circle CenterX=-12.5 CenterY=0 CenterZ=0 NormalX=0 NormalY=0 NormalZ=1 AngleXU=0 Radius=0.75
    g3: LineSegment [constr] StartX=-14.5 StartY=0 StartZ=0 EndX=-12.5 EndY=0 EndZ=0
    g4: Circle CenterX=-10.5 CenterY=0 CenterZ=0 NormalX=0 NormalY=0 NormalZ=1 AngleXU=0 Radius=0.75
    g5: LineSegment [constr] StartX=-12.5 StartY=0 StartZ=0 EndX=-10.5 EndY=0 EndZ=0
    g6: Circle CenterX=-8.5 CenterY=0 CenterZ=0 NormalX=0 NormalY=0 NormalZ=1 AngleXU=0 Radius=0.75
    g7: LineSegment [constr] StartX=-10.5 StartY=0 StartZ=0 EndX=-8.5 EndY=0 EndZ=0
    g8: Circle CenterX=-6.5 CenterY=0 CenterZ=0 NormalX=0 NormalY=0 NormalZ=1 AngleXU=0 Radius=0.75
    g9: LineSegment [constr] StartX=-8.5 StartY=0 StartZ=0 EndX=-6.5 EndY=0 EndZ=0
  constraints (25):
    c: Coincident(g0,g-1)
    c: Radius(g1) = 0.75
    c: Radius(g0) = 3.75
    c: Radius(g2) = 0.75
    c: Coincident(g1,g3)
    c: Coincident(g2,g3)
    c: Distance(g3) = 2
    c: Angle(g3) = 0
    c: Radius(g4) = 0.75
    c: Coincident(g2,g5)
    c: Coincident(g4,g5)
    c: Equal(g3,g5)
    c: Parallel(g5,g3)
    c: Radius(g6) = 0.75
    c: Coincident(g4,g7)
    c: Coincident(g6,g7)
    c: Equal(g3,g7)
    c: Parallel(g7,g3)
    c: Radius(g8) = 0.75
    c: Coincident(g6,g9)
    c: Coincident(g8,g9)
    c: Equal(g3,g9)
    c: Parallel(g9,g3)
    c: PointOnObject(g2,g-1)
    c: DistanceX(g8,g-1) = 6.5
FEATURE [PartDesign::Pocket] Pocket003109  label="q1_basic_horn_shape007"
  BaseFeature = -> Pocket003100
  Length = 5
  Length2 = 100
  Profile = -> Sketch207
  Refine = true
  Type = 0
FEATURE [Sketcher::SketchObject] Sketch202  label="q2-base005"
  ExternalGeometry = -> [Pocket003109]
  MapMode = 5
  Placement = pos=(-20.5,0,0) rot=(0.57735,-0.57735,-0.57735;2.0944rad)
  Support = -> [Pocket003109]
  sketch-geometry (6):
    g0: LineSegment StartX=-5.71563 StartY=2.25 StartZ=0 EndX=-11.6041 EndY=2.25 EndZ=0
    g1: LineSegment StartX=-11.6041 StartY=2.25 StartZ=0 EndX=-38.6752 EndY=17.8795 EndZ=0
    g2: LineSegment StartX=-11.6626 StartY=5.74787 StartZ=0 EndX=-37.1752 EndY=20.4776 EndZ=0
    g3: LineSegment StartX=-37.1752 StartY=20.4776 StartZ=0 EndX=-38.6752 EndY=17.8795 EndZ=0
    g4: LineSegment StartX=-5.71563 StartY=5.74787 StartZ=0 EndX=-5.71563 EndY=2.25 EndZ=0
    g5: LineSegment StartX=-11.6626 StartY=5.74787 StartZ=0 EndX=-5.71563 EndY=5.74787 EndZ=0
  constraints (13):
    c: Coincident(g3,g2)
    c: Coincident(g3,g1)
    c: Perpendicular(g3,g1)
    c: Coincident(g0,g-3)
    c: Parallel(g1,g2)
    c: Coincident(g4,g0)
    c: Perpendicular(g4,g0)
    c: Distance(g1,g2) = 3
    c: Angle(g0,g1) = 2.61799
    c: Coincident(g0,g1)
    c: Coincident(g2,g5)
    c: Coincident(g5,g4)
    c: Horizontal(g5)
FEATURE [PartDesign::Pad] Pad012072  label="q2-bed-base005"
  BaseFeature = -> Pocket003109
  Length = 26.215
  Length2 = 100
  Profile = -> Sketch202
  Refine = true
  Reversed = true
  Type = 0
FEATURE [Sketcher::SketchObject] Sketch201  label="q2-corner-hole011"
  MapMode = 5
  Placement = pos=(0,0,5.74787) rot=(0,0,1;0rad)
  Support = -> [Pad012072]
  sketch-geometry (4):
    g0: LineSegment StartX=-1.62396 StartY=12 StartZ=0 EndX=-5 EndY=12 EndZ=0
    g1: LineSegment StartX=-5 StartY=12 StartZ=0 EndX=-5 EndY=6.68085 EndZ=0
    g2: LineSegment StartX=-5 StartY=6.68085 StartZ=0 EndX=-1.62396 EndY=6.68085 EndZ=0
    g3: LineSegment StartX=-1.62396 StartY=6.68085 StartZ=0 EndX=-1.62396 EndY=12 EndZ=0
  constraints (8):
    c: Coincident(g0,g1)
    c: Coincident(g1,g2)
    c: Coincident(g2,g3)
    c: Coincident(g3,g0)
    c: Horizontal(g0)
    c: Horizontal(g2)
    c: Vertical(g1)
    c: Vertical(g3)
FEATURE [PartDesign::Pocket] Pocket003106  label="q2-corner-hole010"
  BaseFeature = -> Pad012072
  Length = 2
  Length2 = 100
  Profile = -> Sketch201
  Refine = true
  Type = 0
FEATURE [PartDesign::Body] Clone036Body001
  Origin = -> Origin037
FEATURE [Part::Feature] Pocket003116  label="Final-1-arm-horn024"
  Placement = pos=(0,0,32) rot=(0.707107,0.707107,0;3.14159rad)
  shape: bbox 8 x 22.5 x 5 mm, 19 faces (baked)
FEATURE [Part::Feature] Fusion007075  label="Servo-sg90-final026"
  Placement = pos=(0,-16.6,0) rot=(0,0,1;0rad)
  shape: bbox 11.8 x 32.4 x 29.9 mm, 77 faces (baked)
FEATURE [Part::MultiFuse] Fusion007074  label="q2-aux-servo008"
  Placement = pos=(-24,-20.5,64) rot=(-0.377964,0.654654,0.654654;2.41885rad)
  Refine = true
  Shapes = -> [Fusion007075,Pocket003116]
FEATURE [Part::Feature] Fusion007076  label="Servo-sg90-final027"
  Placement = pos=(0,-16.6,0) rot=(0,0,1;0rad)
  shape: bbox 11.8 x 32.4 x 29.9 mm, 77 faces (baked)
FEATURE [Part::Feature] Pocket003118  label="Final-1-arm-horn025"
  Placement = pos=(0,0,32) rot=(0.707107,-0.707107,0;3.14159rad)
  shape: bbox 8 x 22.5 x 5 mm, 19 faces (baked)
FEATURE [Part::MultiFuse] Fusion007073  label="q1-aux-servo008"
  Placement = pos=(0,0,17.25) rot=(0,0,1;0rad)
  Refine = true
  Shapes = -> [Pocket003118,Fusion007076]
FEATURE [Sketcher::SketchObject] Sketch229  label="base_cylinder019"
  MapMode = 5
  Placement = pos=(0,6.2,0) rot=(0,0.707107,0.707107;3.14159rad)
  sketch-geometry (2):
    g0: Circle CenterX=24 CenterY=64 CenterZ=0 NormalX=0 NormalY=0 NormalZ=1 AngleXU=0 Radius=3.75
    g1: Circle CenterX=24 CenterY=64 CenterZ=0 NormalX=0 NormalY=0 NormalZ=1 AngleXU=0 Radius=5.75
  constraints (3):
    c: Radius(g0) = 3.75
    c: Radius(g1) = 5.75
    c: Coincident(g1,g0)
FEATURE [PartDesign::Pad] Pad012077  label="q2_base_cylinder011"
  Length = 2.25
  Length2 = 100
  Placement = pos=(0,6.2,0) rot=(0,0.707107,0.707107;3.14159rad)
  Profile = -> Sketch229
  Refine = true
  Type = 0
FEATURE [Sketcher::SketchObject] Sketch208  label="q2_base009"
  ExternalGeometry = -> [Pad012077]
  MapMode = 5
  Placement = pos=(2e-16,8.45,-9e-16) rot=(0,0.707107,0.707107;3.14159rad)
  Support = -> [Pad012077]
  sketch-geometry (6):
    g0: ArcOfCircle CenterX=24 CenterY=64 CenterZ=0 NormalX=0 NormalY=0 NormalZ=1 AngleXU=0 Radius=5.75 StartAngle=2.0944 EndAngle=5.23599
    g1: LineSegment [constr] StartX=12.5 StartY=64 StartZ=0 EndX=37 EndY=64 EndZ=0
    g2: LineSegment [constr] StartX=24 StartY=64 StartZ=0 EndX=21.125 EndY=68.9796 EndZ=0
    g3: LineSegment StartX=21.125 StartY=68.9796 StartZ=0 EndX=39.516 EndY=79.5977 EndZ=0
    g4: LineSegment StartX=39.516 StartY=79.5977 StartZ=0 EndX=45.266 EndY=69.6384 EndZ=0
    g5: LineSegment StartX=45.266 StartY=69.6384 StartZ=0 EndX=26.875 EndY=59.0204 EndZ=0
  constraints (14):
    c: Coincident(g0,g-3)
    c: PointOnObject(g0,g-3)
    c: Angle(g0) = 3.14159
    c: Horizontal(g1)
    c: PointOnObject(g0,g1)
    c: Coincident(g2,g0)
    c: Coincident(g2,g0)
    c: Angle(g1,g2) = 2.0944
    c: Tangent(g0,g3) = 1.5708
    c: Coincident(g3,g4)
    c: Coincident(g4,g5)
    c: Coincident(g5,g0)
    c: Equal(g3,g5)
    c: Parallel(g3,g5)
FEATURE [PartDesign::Pad] Pad012081  label="q2_basic_base006"
  BaseFeature = -> Pad012077
  Length = 3.5
  Length2 = 100
  Placement = pos=(0,6.2,0) rot=(0,0.707107,0.707107;3.14159rad)
  Profile = -> Sketch208
  Refine = true
  Type = 0
FEATURE [Sketcher::SketchObject] Sketch220  label="AUX_q2_base_horn009"
  ExternalGeometry = -> [Pad012081]
  MapMode = 5
  Placement = pos=(-3e-15,11.95,-6e-15) rot=(0.186157,0.694747,0.694747;3.50969rad)
  sketch-geometry (5):
    g0: LineSegment StartX=54.0346 StartY=46.9656 StartZ=0 EndX=69.7804 EndY=45.1656 EndZ=0
    g1: ArcOfCircle CenterX=69.7804 CenterY=43.4256 CenterZ=0 NormalX=0 NormalY=0 NormalZ=1 AngleXU=0 Radius=1.74 StartAngle=0 EndAngle=1.5708
    g2: LineSegment [constr] StartX=71.5204 StartY=43.4256 StartZ=0 EndX=49.0304 EndY=43.4256 EndZ=0
    g3: ArcOfCircle CenterX=52.7846 CenterY=43.4256 CenterZ=0 NormalX=0 NormalY=0 NormalZ=1 AngleXU=0 Radius=3.75421 StartAngle=1.23136 EndAngle=3.14159
    g4: LineSegment [constr] StartX=52.7846 StartY=49.1756 StartZ=0 EndX=52.7846 EndY=37.6756 EndZ=0
  constraints (16):
    c: Coincident(g1,g0)
    c: Coincident(g1,g2)
    c: Coincident(g3,g0)
    c: Radius(g1) = 1.74
    c: PointOnObject(g1,g2)
    c: Coincident(g2,g3)
    c: PointOnObject(g3,g2)
    c: DistanceX(g2,g2) = 22.49
    c: DistanceY(g1,g0) = 1.74
    c: DistanceX(g3,g0) = 1.25
    c: DistanceY(g3,g0) = 3.54
    c: Horizontal(g2)
    c: Coincident(g4,g-3)
    c: Coincident(g4,g-4)
    c: PointOnObject(g3,g4)
    c: Symmetric(g4,g4,g3)
FEATURE [Sketcher::SketchObject] Sketch225  label="horn_shape013"
  ExternalGeometry = -> [Sketch220]
  MapMode = 5
  Placement = pos=(6e-16,11.95,-5.8e-15) rot=(0,0.707107,0.707107;3.14159rad)
  Support = -> [Pad012081]
  sketch-geometry (7):
    g0: LineSegment [constr] StartX=20.7488 StartY=62.1229 StartZ=0 EndX=40.2257 EndY=73.3679 EndZ=0
    g1: ArcOfCircle CenterX=24 CenterY=64 CenterZ=0 NormalX=0 NormalY=0 NormalZ=1 AngleXU=0 Radius=3.75421 StartAngle=1.75495 EndAngle=3.66519
    g2: ArcOfCircle CenterX=38.7188 CenterY=72.4979 CenterZ=0 NormalX=0 NormalY=0 NormalZ=1 AngleXU=0 Radius=1.74 StartAngle=0.523599 EndAngle=2.0944
    g3: LineSegment StartX=23.3125 StartY=67.6907 StartZ=0 EndX=37.8488 EndY=74.0048 EndZ=0
    g4: ArcOfCircle CenterX=24 CenterY=64 CenterZ=0 NormalX=0 NormalY=0 NormalZ=1 AngleXU=0 Radius=3.75421 StartAngle=3.66519 EndAngle=5.57543
    g5: ArcOfCircle CenterX=38.7188 CenterY=72.4979 CenterZ=0 NormalX=0 NormalY=0 NormalZ=1 AngleXU=0 Radius=1.74 StartAngle=5.23599 EndAngle=6.80678
    g6: LineSegment StartX=26.8525 StartY=61.5593 StartZ=0 EndX=39.5888 EndY=70.991 EndZ=0
  constraints (16):
    c: Coincident(g0,g-5)
    c: Coincident(g0,g-4)
    c: Coincident(g1,g-5)
    c: Coincident(g1,g-5)
    c: Coincident(g1,g0)
    c: Coincident(g2,g-4)
    c: Coincident(g2,g0)
    c: Coincident(g2,g-4)
    c: Coincident(g3,g1)
    c: Coincident(g3,g2)
    c: Coincident(g6,g4)
    c: Coincident(g6,g5)
    c: Coincident(g0,g4)
    c: Coincident(g1,g4)
    c: Coincident(g2,g5)
    c: Coincident(g0,g5)
FEATURE [PartDesign::Pocket] Pocket003115  label="horn_shape012"
  BaseFeature = -> Pad012081
  Length = 2.65
  Length2 = 100
  Placement = pos=(0,6.2,0) rot=(0,0.707107,0.707107;3.14159rad)
  Profile = -> Sketch225
  Refine = true
  Type = 0
FEATURE [Sketcher::SketchObject] Sketch210  label="horn_holes014"
  ExternalGeometry = -> [Pocket003115]
  MapMode = 5
  Placement = pos=(2e-16,9.3,-5.3e-15) rot=(0,0.707107,0.707107;3.14159rad)
  Support = -> [Pocket003115]
  sketch-geometry (16):
    g0: Circle CenterX=24 CenterY=64 CenterZ=0 NormalX=0 NormalY=0 NormalZ=1 AngleXU=0 Radius=3.75
    g1: Circle CenterX=-14.6952 CenterY=0 CenterZ=0 NormalX=0 NormalY=0 NormalZ=1 AngleXU=0 Radius=0.75
    g2: Circle CenterX=-12.6952 CenterY=0 CenterZ=0 NormalX=0 NormalY=0 NormalZ=1 AngleXU=0 Radius=0.75
    g3: LineSegment [constr] StartX=-14.6952 StartY=0 StartZ=0 EndX=-12.6952 EndY=0 EndZ=0
    g4: Circle CenterX=-10.6952 CenterY=0 CenterZ=0 NormalX=0 NormalY=0 NormalZ=1 AngleXU=0 Radius=0.75
    g5: LineSegment [constr] StartX=-12.6952 StartY=0 StartZ=0 EndX=-10.6952 EndY=0 EndZ=0
    g6: Circle CenterX=-8.69518 CenterY=0 CenterZ=0 NormalX=0 NormalY=0 NormalZ=1 AngleXU=0 Radius=0.75
    g7: LineSegment [constr] StartX=-10.6952 StartY=0 StartZ=0 EndX=-8.69518 EndY=0 EndZ=0
    g8: Circle CenterX=-6.69518 CenterY=0 CenterZ=0 NormalX=0 NormalY=0 NormalZ=1 AngleXU=0 Radius=0.75
    g9: LineSegment [constr] StartX=-8.69518 StartY=0 StartZ=0 EndX=-6.69518 EndY=0 EndZ=0
    g10: LineSegment [constr] StartX=24 StartY=64 StartZ=0 EndX=43.3449 EndY=75.1688 EndZ=0
    g11: Circle CenterX=29.6292 CenterY=67.25 CenterZ=0 NormalX=0 NormalY=0 NormalZ=1 AngleXU=0 Radius=0.75
    g12: Circle CenterX=31.3612 CenterY=68.25 CenterZ=0 NormalX=0 NormalY=0 NormalZ=1 AngleXU=0 Radius=0.75
    g13: Circle CenterX=33.0933 CenterY=69.25 CenterZ=0 NormalX=0 NormalY=0 NormalZ=1 AngleXU=0 Radius=0.75
    g14: Circle CenterX=34.8253 CenterY=70.25 CenterZ=0 NormalX=0 NormalY=0 NormalZ=1 AngleXU=0 Radius=0.75
    g15: Circle CenterX=36.5574 CenterY=71.25 CenterZ=0 NormalX=0 NormalY=0 NormalZ=1 AngleXU=0 Radius=0.75
  constraints (41):
    c: Radius(g1) = 0.75
    c: Radius(g0) = 3.75
    c: Radius(g2) = 0.75
    c: Coincident(g1,g3)
    c: Coincident(g2,g3)
    c: Distance(g3) = 2
    c: Angle(g3) = 0
    c: Radius(g4) = 0.75
    c: Coincident(g2,g5)
    c: Coincident(g4,g5)
    c: Equal(g3,g5)
    c: Radius(g6) = 0.75
    c: Coincident(g4,g7)
    c: Coincident(g6,g7)
    c: Equal(g3,g7)
    c: Radius(g8) = 0.75
    c: Coincident(g6,g9)
    c: Coincident(g8,g9)
    c: Equal(g3,g9)
    c: Parallel(g9,g3)
    c: Parallel(g9,g7)
    c: Parallel(g7,g5)
    c: Coincident(g10,g0)
    c: Angle(g10) = 0.523599
    c: Radius(g11) = 0.75
    c: Distance(g0,g11) = 6.5
    c: PointOnObject(g11,g10)
    c: Equal(g11,g12) = 0.75
    c: PointOnObject(g12,g10)
    c: DistanceX(g0) = 24
    c: DistanceY(g0) = 64
    c: Distance(g11,g12) = 2
    c: Equal(g11,g13) = 0.75
    c: PointOnObject(g13,g10)
    c: Equal(g11,g14) = 0.75
    c: PointOnObject(g14,g10)
    c: Equal(g11,g15) = 0.75
    c: PointOnObject(g15,g10)
    c: Distance(g12,g13) = 2
    c: Distance(g13,g14) = 2
    c: Distance(g14,g15) = 2
FEATURE [PartDesign::Pocket] Pocket003114  label="basic_horn_union006"
  BaseFeature = -> Pocket003115
  Length = 5
  Length2 = 100
  Placement = pos=(0,6.2,0) rot=(0,0.707107,0.707107;3.14159rad)
  Profile = -> Sketch210
  Refine = true
  Type = 0
FEATURE [Sketcher::SketchObject] Sketch224  label="q2_bridge012"
  ExternalGeometry = -> [Pocket003114]
  MapMode = 5
  Placement = pos=(2e-16,8.45,-2.3e-15) rot=(0,-0.707107,0.707107;3.14159rad)
  Support = -> [Pocket003114]
  sketch-geometry (4):
    g0: LineSegment StartX=39.516 StartY=-79.5977 StartZ=0 EndX=45.266 EndY=-69.6384 EndZ=0
    g1: LineSegment StartX=45.266 StartY=-69.6384 StartZ=0 EndX=40.9358 EndY=-67.1384 EndZ=0
    g2: LineSegment StartX=39.516 StartY=-79.5977 StartZ=0 EndX=35.1858 EndY=-77.0977 EndZ=0
    g3: ArcOfCircle CenterX=24.5001 CenterY=-64.2888 CenterZ=0 NormalX=0 NormalY=0 NormalZ=1 AngleXU=0 Radius=16.6809 StartAngle=5.40766 EndAngle=6.11151
  constraints (10):
    c: Coincident(g-5,g0)
    c: Coincident(g0,g-5)
    c: Coincident(g0,g1)
    c: PointOnObject(g1,g-3)
    c: Coincident(g0,g2)
    c: PointOnObject(g2,g-4)
    c: Distance(g2) = 5
    c: Equal(g2,g1)
    c: Coincident(g3,g1)
    c: Coincident(g3,g2)
FEATURE [PartDesign::Pad] Pad012083  label="q2_bridge013"
  BaseFeature = -> Pocket003114
  Length = 31
  Length2 = 100
  Placement = pos=(0,6.2,0) rot=(0,0.707107,0.707107;3.14159rad)
  Profile = -> Sketch224
  Refine = true
  Type = 0
FEATURE [Sketcher::SketchObject] Sketch218  label="q2_back_union006"
  ExternalGeometry = -> [Pad012077,Sketch208]
  MapMode = 5
  Placement = pos=(-2.3e-15,-22.55,3.83e-14) rot=(0,-0.707107,0.707107;3.14159rad)
  Support = -> [Pad012083]
  expr: Constraints[2] = Sketch067.Constraints[2]
  sketch-geometry (7):
    g0: ArcOfCircle CenterX=24 CenterY=-64 CenterZ=0 NormalX=0 NormalY=0 NormalZ=1 AngleXU=0 Radius=5.75 StartAngle=1.0472 EndAngle=4.18879
    g1: LineSegment [constr] StartX=12.5 StartY=-64 StartZ=0 EndX=37 EndY=-64 EndZ=0
    g2: LineSegment [constr] StartX=24 StartY=-64 StartZ=0 EndX=26.875 EndY=-59.0204 EndZ=0
    g3: LineSegment StartX=45.266 StartY=-69.6384 StartZ=0 EndX=26.875 EndY=-59.0204 EndZ=0
    g4: LineSegment StartX=45.266 StartY=-69.6384 StartZ=0 EndX=39.516 EndY=-79.5977 EndZ=0
    g5: LineSegment StartX=39.516 StartY=-79.5977 StartZ=0 EndX=21.125 EndY=-68.9796 EndZ=0
    g6: Circle CenterX=24 CenterY=-64 CenterZ=0 NormalX=0 NormalY=0 NormalZ=1 AngleXU=0 Radius=2
  constraints (16):
    c: Coincident(g0,g-3)
    c: PointOnObject(g0,g-3)
    c: Angle(g0) = 3.14159
    c: Horizontal(g1)
    c: PointOnObject(g0,g1)
    c: Coincident(g2,g0)
    c: Coincident(g2,g0)
    c: Parallel(g2,g-4)
    c: Coincident(g-4,g3)
    c: Coincident(g3,g0)
    c: Coincident(g3,g4)
    c: Coincident(g4,g-4)
    c: Coincident(g4,g5)
    c: Coincident(g5,g0)
    c: Coincident(g6,g0)
    c: Radius(g6) = 2
FEATURE [PartDesign::Pad] Pad012079  label="q2_joint006"
  BaseFeature = -> Pad012083
  Length = 3.5
  Length2 = 100
  Placement = pos=(0,6.2,0) rot=(0,0.707107,0.707107;3.14159rad)
  Profile = -> Sketch218
  Refine = true
  Type = 0
FEATURE [Sketcher::SketchObject] Sketch209  label="q2-leg_union_section006"
  ExternalGeometry = -> [Pad012079]
  MapMode = 5
  Placement = pos=(-64.1038,6.2,37.0103) rot=(0,-1,0;1.0472rad)
  Support = -> [Pad012079]
  sketch-geometry (4):
    g0: LineSegment StartX=49.1756 StartY=5.75 StartZ=0 EndX=49.1756 EndY=-32.25 EndZ=0
    g1: LineSegment StartX=49.1756 StartY=-32.25 StartZ=0 EndX=37.6756 EndY=-32.25 EndZ=0
    g2: LineSegment StartX=37.6756 StartY=-32.25 StartZ=0 EndX=37.6756 EndY=5.75 EndZ=0
    g3: LineSegment StartX=37.6756 StartY=5.75 StartZ=0 EndX=49.1756 EndY=5.75 EndZ=0
  constraints (8):
    c: Coincident(g-6,g0)
    c: Coincident(g0,g-6)
    c: Coincident(g0,g1)
    c: Coincident(g1,g-5)
    c: Coincident(g-5,g2)
    c: Coincident(g2,g-4)
    c: Coincident(g2,g3)
    c: Coincident(g3,g0)
FEATURE [Sketcher::SketchObject] Sketch215  label="trajectory006"
  ExternalGeometry = -> [Pad012079]
  MapMode = 5
  Placement = pos=(6e-16,11.95,-5.8e-15) rot=(0,0.707107,0.707107;3.14159rad)
  Support = -> [Pad012079]
  sketch-geometry (8):
    g0: GeomPoint X=42.3808 Y=74.6356 Z=0
    g1-g4: Circle [constr] x4 (B-spline internal-alignment scaffolding for g5; pole/knot coordinates omitted)
    g5: BSplineCurve PolesCount=4 KnotsCount=2 Degree=3 IsPeriodic=0
    g6: GeomPoint [constr] X=42.3808 Y=74.6356 Z=0
    g7: GeomPoint [constr] X=64.6677 Y=0 Z=0
  constraints (10):
    c: PointOnObject(g0,g-3)
    c: Coincident(g1,g0)
    c: Radius(g1) = 4
    c: Equal(g1,g2)
    c: Equal(g1,g3)
    c: Equal(g1,g4)
    c: PointOnObject(g4,g-1)
    c: InternalAlignment(g1-g4 -> g5) x4
    c: InternalAlignment(g6,g5)
    c: InternalAlignment(g7,g5)
FEATURE [Sketcher::SketchObject] Sketch214  label="q2-bone-touch_section006"
  ExternalGeometry = -> [Sketch215,Pad012079]
  MapMode = 5
  Support = -> [XY_Plane040]
  sketch-geometry (7):
    g0: LineSegment StartX=-66.1677 StartY=-4.55 StartZ=0 EndX=-63.1677 EndY=-4.55 EndZ=0
    g1: LineSegment StartX=-63.1677 StartY=-4.55 StartZ=0 EndX=-63.1677 EndY=-9.55 EndZ=0
    g2: LineSegment StartX=-63.1677 StartY=-9.55 StartZ=0 EndX=-66.1677 EndY=-9.55 EndZ=0
    g3: LineSegment StartX=-66.1677 StartY=-9.55 StartZ=0 EndX=-66.1677 EndY=-4.55 EndZ=0
    g4: GeomPoint X=-45.266 Y=-7.05 Z=0
    g5: GeomPoint X=-63.1677 Y=-7.05 Z=0
    g6: GeomPoint X=-64.6677 Y=-4.55 Z=0
  constraints (18):
    c: Coincident(g0,g1)
    c: Coincident(g1,g2)
    c: Coincident(g2,g3)
    c: Coincident(g3,g0)
    c: Horizontal(g0)
    c: Horizontal(g2)
    c: Vertical(g1)
    c: Vertical(g3)
    c: PointOnObject(g4,g-4)
    c: Symmetric(g-4,g-4,g4)
    c: PointOnObject(g5,g1)
    c: Symmetric(g0,g1,g5)
    c: Horizontal(g5,g4)
    c: PointOnObject(g6,g0)
    c: Symmetric(g0,g0,g6)
    c: Vertical(g6,g-3)
    c: DistanceX(g2,g2) = 3
    c: DistanceY(g3,g3) = 5
FEATURE [PartDesign::AdditivePipe] AdditivePipe006
  AuxilleryCurvelinear = true
  AuxillerySpineTangent = false
  BaseFeature = -> Pad012079
  Binormal = (0,0,0)
  Mode = 0
  Placement = pos=(0,6.2,0) rot=(0,0.707107,0.707107;3.14159rad)
  Profile = -> Sketch209
  Refine = true
  Sections = -> [Sketch214]
  Spine = -> Sketch215
  SpineTangent = false
  Transformation = 1
  Transition = 0
FEATURE [PartDesign::Body] Body023  label="Q2-Leg-joint006"
  Group = -> [Sketch229,Pad012077,Sketch208,Pad012081,Sketch220,Sketch225,Pocket003115,Sketch210,Pocket003114,Sketch224,Pad012083,Sketch218,Pad012079,Sketch215,Sketch209,Sketch214,AdditivePipe006]
  Origin = -> Origin040
  Tip = -> AdditivePipe006
FEATURE [Sketcher::SketchObject] Sketch232  label="base_cylinder020"
  MapMode = 5
  Support = -> [XY_Plane038]
  sketch-geometry (2):
    g0: Circle CenterX=0 CenterY=0 CenterZ=0 NormalX=0 NormalY=0 NormalZ=1 AngleXU=0 Radius=3.75
    g1: Circle CenterX=0 CenterY=0 CenterZ=0 NormalX=0 NormalY=0 NormalZ=1 AngleXU=0 Radius=5.75
  constraints (4):
    c: Coincident(g0,g-1)
    c: Radius(g0) = 3.75
    c: Coincident(g1,g-1)
    c: Radius(g1) = 5.75
FEATURE [PartDesign::Pad] Pad012076  label="low_base008"
  Length = 2.25
  Length2 = 100
  Profile = -> Sketch232
  Refine = true
  Type = 0
FEATURE [Sketcher::SketchObject] Sketch231  label="basic_base009"
  MapMode = 5
  Placement = pos=(0,0,2.25) rot=(0,0,1;0rad)
  Support = -> [Pad012076]
  sketch-geometry (6):
    g0: LineSegment StartX=0 StartY=5.71563 StartZ=0 EndX=-20.5 EndY=5.71563 EndZ=0
    g1: LineSegment StartX=1.86762e-06 StartY=-5.71497 StartZ=0 EndX=-20.5 EndY=-5.71497 EndZ=0
    g2: LineSegment StartX=-20.5 StartY=5.71563 StartZ=0 EndX=-20.5 EndY=-5.71497 EndZ=0
    g3: LineSegment StartX=0 StartY=5.71563 StartZ=0 EndX=5.71497 EndY=5.71563 EndZ=0
    g4: LineSegment StartX=5.71497 StartY=5.71563 StartZ=0 EndX=5.71497 EndY=0 EndZ=0
    g5: ArcOfCircle CenterX=0 CenterY=0 CenterZ=0 NormalX=0 NormalY=0 NormalZ=1 AngleXU=0 Radius=5.71497 StartAngle=4.71239 EndAngle=6.28319
  constraints (14):
    c: PointOnObject(g0,g-2)
    c: Horizontal(g0)
    c: DistanceX(g0,g0) = 20.5
    c: Coincident(g2,g0)
    c: Vertical(g2)
    c: Coincident(g1,g2)
    c: Coincident(g0,g3)
    c: Horizontal(g3)
    c: Coincident(g4,g3)
    c: PointOnObject(g4,g-1)
    c: Vertical(g4)
    c: Coincident(g5,g-1)
    c: Coincident(g5,g1)
    c: Coincident(g5,g4)
FEATURE [PartDesign::Pad] Pad012080  label="q1_basic_base008"
  BaseFeature = -> Pad012076
  Length = 3.5
  Length2 = 100
  Profile = -> Sketch231
  Refine = true
  Type = 0
FEATURE [Sketcher::SketchObject] Sketch222  label="q1_base_horn008"
  MapMode = 5
  Placement = pos=(0,0,5.75) rot=(0,0,1;0rad)
  Support = -> [Pad012080]
  sketch-geometry (7):
    g0: LineSegment StartX=-1.25 StartY=3.53553 StartZ=0 EndX=-17 EndY=1.74295 EndZ=0
    g1: ArcOfCircle CenterX=-17 CenterY=0 CenterZ=0 NormalX=0 NormalY=0 NormalZ=1 AngleXU=0 Radius=1.74295 StartAngle=1.5708 EndAngle=3.14159
    g2: LineSegment [constr] StartX=-18.743 StartY=0 StartZ=0 EndX=0 EndY=0 EndZ=0
    g3: ArcOfCircle CenterX=0 CenterY=0 CenterZ=0 NormalX=0 NormalY=0 NormalZ=1 AngleXU=0 Radius=3.75 StartAngle=0 EndAngle=1.91063
    g4: LineSegment StartX=-1.25 StartY=-3.53553 StartZ=0 EndX=-17 EndY=-1.74295 EndZ=0
    g5: ArcOfCircle CenterX=-17 CenterY=-1e-12 CenterZ=0 NormalX=0 NormalY=0 NormalZ=1 AngleXU=0 Radius=1.74295 StartAngle=3.14159 EndAngle=4.71239
    g6: ArcOfCircle CenterX=0 CenterY=0 CenterZ=0 NormalX=0 NormalY=0 NormalZ=1 AngleXU=0 Radius=3.75 StartAngle=4.37255 EndAngle=6.28319
  constraints (11):
    c: PointOnObject(g1,g-1)
    c: Coincident(g1,g0)
    c: PointOnObject(g1,g-1)
    c: Coincident(g1,g2)
    c: Coincident(g3,g-1)
    c: Radius(g3) = 3.75
    c: Coincident(g3,g0)
    c: DistanceX(g0,g3) = 5
    c: Coincident(g5,g4)
    c: Radius(g6) = 3.75
    c: Coincident(g6,g4)
FEATURE [PartDesign::Pocket] Pocket003117  label="q1_basic_horn008"
  BaseFeature = -> Pad012080
  Length = 2.65
  Length2 = 100
  Profile = -> Sketch222
  Refine = true
  Type = 0
FEATURE [Sketcher::SketchObject] Sketch230  label="horn_holes015"
  MapMode = 5
  Placement = pos=(0,0,3.1) rot=(0,0,1;0rad)
  Support = -> [Pocket003117]
  sketch-geometry (10):
    g0: Circle CenterX=0 CenterY=0 CenterZ=0 NormalX=0 NormalY=0 NormalZ=1 AngleXU=0 Radius=3.75
    g1: Circle CenterX=-14.5 CenterY=0 CenterZ=0 NormalX=0 NormalY=0 NormalZ=1 AngleXU=0 Radius=0.75
    g2: Circle CenterX=-12.5 CenterY=0 CenterZ=0 NormalX=0 NormalY=0 NormalZ=1 AngleXU=0 Radius=0.75
    g3: LineSegment [constr] StartX=-14.5 StartY=0 StartZ=0 EndX=-12.5 EndY=0 EndZ=0
    g4: Circle CenterX=-10.5 CenterY=0 CenterZ=0 NormalX=0 NormalY=0 NormalZ=1 AngleXU=0 Radius=0.75
    g5: LineSegment [constr] StartX=-12.5 StartY=0 StartZ=0 EndX=-10.5 EndY=0 EndZ=0
    g6: Circle CenterX=-8.5 CenterY=0 CenterZ=0 NormalX=0 NormalY=0 NormalZ=1 AngleXU=0 Radius=0.75
    g7: LineSegment [constr] StartX=-10.5 StartY=0 StartZ=0 EndX=-8.5 EndY=0 EndZ=0
    g8: Circle CenterX=-6.5 CenterY=0 CenterZ=0 NormalX=0 NormalY=0 NormalZ=1 AngleXU=0 Radius=0.75
    g9: LineSegment [constr] StartX=-8.5 StartY=0 StartZ=0 EndX=-6.5 EndY=0 EndZ=0
  constraints (25):
    c: Coincident(g0,g-1)
    c: Radius(g1) = 0.75
    c: Radius(g0) = 3.75
    c: Radius(g2) = 0.75
    c: Coincident(g1,g3)
    c: Coincident(g2,g3)
    c: Distance(g3) = 2
    c: Angle(g3) = 0
    c: Radius(g4) = 0.75
    c: Coincident(g2,g5)
    c: Coincident(g4,g5)
    c: Equal(g3,g5)
    c: Parallel(g5,g3)
    c: Radius(g6) = 0.75
    c: Coincident(g4,g7)
    c: Coincident(g6,g7)
    c: Equal(g3,g7)
    c: Parallel(g7,g3)
    c: Radius(g8) = 0.75
    c: Coincident(g6,g9)
    c: Coincident(g8,g9)
    c: Equal(g3,g9)
    c: Parallel(g9,g3)
    c: PointOnObject(g2,g-1)
    c: DistanceX(g8,g-1) = 6.5
FEATURE [PartDesign::Pocket] Pocket003111  label="q1_basic_horn_shape008"
  BaseFeature = -> Pocket003117
  Length = 5
  Length2 = 100
  Profile = -> Sketch230
  Refine = true
  Type = 0
FEATURE [Sketcher::SketchObject] Sketch219  label="q2-base006"
  ExternalGeometry = -> [Pocket003111]
  MapMode = 5
  Placement = pos=(-20.5,0,0) rot=(0.57735,-0.57735,-0.57735;2.0944rad)
  Support = -> [Pocket003111]
  sketch-geometry (6):
    g0: LineSegment StartX=-5.71563 StartY=2.25 StartZ=0 EndX=-11.6041 EndY=2.25 EndZ=0
    g1: LineSegment StartX=-11.6041 StartY=2.25 StartZ=0 EndX=-38.6752 EndY=17.8795 EndZ=0
    g2: LineSegment StartX=-11.6626 StartY=5.74787 StartZ=0 EndX=-37.1752 EndY=20.4776 EndZ=0
    g3: LineSegment StartX=-37.1752 StartY=20.4776 StartZ=0 EndX=-38.6752 EndY=17.8795 EndZ=0
    g4: LineSegment StartX=-5.71563 StartY=5.74787 StartZ=0 EndX=-5.71563 EndY=2.25 EndZ=0
    g5: LineSegment StartX=-11.6626 StartY=5.74787 StartZ=0 EndX=-5.71563 EndY=5.74787 EndZ=0
  constraints (13):
    c: Coincident(g3,g2)
    c: Coincident(g3,g1)
    c: Perpendicular(g3,g1)
    c: Coincident(g0,g-3)
    c: Parallel(g1,g2)
    c: Coincident(g4,g0)
    c: Perpendicular(g4,g0)
    c: Distance(g1,g2) = 3
    c: Angle(g0,g1) = 2.61799
    c: Coincident(g0,g1)
    c: Coincident(g2,g5)
    c: Coincident(g5,g4)
    c: Horizontal(g5)
FEATURE [PartDesign::Pad] Pad012074  label="q2-bed-base006"
  BaseFeature = -> Pocket003111
  Length = 26.215
  Length2 = 100
  Profile = -> Sketch219
  Refine = true
  Reversed = true
  Type = 0
FEATURE [Sketcher::SketchObject] Sketch221  label="q2-corner-hole013"
  MapMode = 5
  Placement = pos=(0,0,5.74787) rot=(0,0,1;0rad)
  Support = -> [Pad012074]
  sketch-geometry (4):
    g0: LineSegment StartX=-1.62396 StartY=12 StartZ=0 EndX=-5 EndY=12 EndZ=0
    g1: LineSegment StartX=-5 StartY=12 StartZ=0 EndX=-5 EndY=6.68085 EndZ=0
    g2: LineSegment StartX=-5 StartY=6.68085 StartZ=0 EndX=-1.62396 EndY=6.68085 EndZ=0
    g3: LineSegment StartX=-1.62396 StartY=6.68085 StartZ=0 EndX=-1.62396 EndY=12 EndZ=0
  constraints (8):
    c: Coincident(g0,g1)
    c: Coincident(g1,g2)
    c: Coincident(g2,g3)
    c: Coincident(g3,g0)
    c: Horizontal(g0)
    c: Horizontal(g2)
    c: Vertical(g1)
    c: Vertical(g3)
FEATURE [PartDesign::Pocket] Pocket003110  label="q2-corner-hole012"
  BaseFeature = -> Pad012074
  Length = 2
  Length2 = 100
  Profile = -> Sketch221
  Refine = true
  Type = 0
FEATURE [Sketcher::SketchObject] Sketch234  label="half_base_sketch001"
  MapMode = 5
  sketch-geometry (71):
    g0: LineSegment StartX=50 StartY=-45.9953 StartZ=0 EndX=50 EndY=-69.5018 EndZ=0
    g1: LineSegment StartX=50 StartY=-69.5018 StartZ=0 EndX=62.9374 EndY=-69.5018 EndZ=0
    g2: LineSegment StartX=62.9374 StartY=-69.5018 StartZ=0 EndX=62.9374 EndY=-45.9953 EndZ=0
    g3: LineSegment StartX=54 StartY=-43.1953 StartZ=0 EndX=58.9374 EndY=-43.1953 EndZ=0
    g4: LineSegment StartX=58.9374 StartY=-43.1953 StartZ=0 EndX=58.9374 EndY=-45.9953 EndZ=0
    g5: LineSegment StartX=54 StartY=-45.9953 StartZ=0 EndX=54 EndY=-43.1953 EndZ=0
    g6: LineSegment StartX=50 StartY=-45.9953 StartZ=0 EndX=54 EndY=-45.9953 EndZ=0
    g7: Circle CenterX=56.5003 CenterY=-71.5595 CenterZ=0 NormalX=0 NormalY=0 NormalZ=1 AngleXU=0 Radius=1.2
    g8: LineSegment StartX=58.9374 StartY=-45.9953 StartZ=0 EndX=62.9374 EndY=-45.9953 EndZ=0
    g9: Circle CenterX=46.5 CenterY=-59.2818 CenterZ=0 NormalX=0 NormalY=0 NormalZ=1 AngleXU=0 Radius=1.76
    g10: Circle CenterX=66.4374 CenterY=-59.2818 CenterZ=0 NormalX=0 NormalY=0 NormalZ=1 AngleXU=0 Radius=1.76
    g11: LineSegment StartX=50 StartY=-10.9992 StartZ=0 EndX=50 EndY=-34.5057 EndZ=0
    g12: LineSegment StartX=50 StartY=-34.5057 StartZ=0 EndX=62.9374 EndY=-34.5057 EndZ=0
    g13: LineSegment StartX=62.9374 StartY=-34.5057 StartZ=0 EndX=62.9374 EndY=-10.9992 EndZ=0
    g14: LineSegment StartX=54 StartY=-8.19917 StartZ=0 EndX=58.9374 EndY=-8.19917 EndZ=0
    g15: LineSegment StartX=58.9374 StartY=-8.19917 StartZ=0 EndX=58.9374 EndY=-10.9992 EndZ=0
    g16: LineSegment StartX=54 StartY=-10.9992 StartZ=0 EndX=54 EndY=-8.19917 EndZ=0
    g17: LineSegment StartX=50 StartY=-10.9992 StartZ=0 EndX=54 EndY=-10.9992 EndZ=0
    g18: Circle CenterX=56.5003 CenterY=-36.5634 CenterZ=0 NormalX=0 NormalY=0 NormalZ=1 AngleXU=0 Radius=1.2
    g19: LineSegment StartX=58.9374 StartY=-10.9992 StartZ=0 EndX=62.9374 EndY=-10.9992 EndZ=0
    g20: Circle CenterX=46.5 CenterY=-24.2857 CenterZ=0 NormalX=0 NormalY=0 NormalZ=1 AngleXU=0 Radius=1.76
    g21: Circle CenterX=66.4374 CenterY=-24.2857 CenterZ=0 NormalX=0 NormalY=0 NormalZ=1 AngleXU=0 Radius=1.76
    g22: LineSegment [constr] StartX=50 StartY=-45.9953 StartZ=0 EndX=50 EndY=-10.9992 EndZ=0
    g23: LineSegment StartX=50 StartY=23.997 StartZ=0 EndX=50 EndY=0.490497 EndZ=0
    g24: LineSegment StartX=50 StartY=0.490497 StartZ=0 EndX=62.9374 EndY=0.490497 EndZ=0
    g25: LineSegment StartX=62.9374 StartY=0.490497 StartZ=0 EndX=62.9374 EndY=23.997 EndZ=0
    g26: LineSegment StartX=54 StartY=26.797 StartZ=0 EndX=58.9374 EndY=26.797 EndZ=0
    g27: LineSegment StartX=58.9374 StartY=26.797 StartZ=0 EndX=58.9374 EndY=23.997 EndZ=0
    g28: LineSegment StartX=54 StartY=23.997 StartZ=0 EndX=54 EndY=26.797 EndZ=0
    g29: LineSegment StartX=50 StartY=23.997 StartZ=0 EndX=54 EndY=23.997 EndZ=0
    g30: Circle CenterX=56.5003 CenterY=-1.5672 CenterZ=0 NormalX=0 NormalY=0 NormalZ=1 AngleXU=0 Radius=1.2
    g31: LineSegment StartX=58.9374 StartY=23.997 StartZ=0 EndX=62.9374 EndY=23.997 EndZ=0
    g32: Circle CenterX=46.5 CenterY=10.7105 CenterZ=0 NormalX=0 NormalY=0 NormalZ=1 AngleXU=0 Radius=1.76
    g33: Circle CenterX=66.4374 CenterY=10.7105 CenterZ=0 NormalX=0 NormalY=0 NormalZ=1 AngleXU=0 Radius=1.76
    g34: LineSegment [constr] StartX=50 StartY=-10.9992 StartZ=0 EndX=50 EndY=23.997 EndZ=0
    g35: LineSegment StartX=50 StartY=58.9932 StartZ=0 EndX=50 EndY=35.4867 EndZ=0
    g36: LineSegment StartX=50 StartY=35.4867 StartZ=0 EndX=62.9374 EndY=35.4867 EndZ=0
    g37: LineSegment StartX=62.9374 StartY=35.4867 StartZ=0 EndX=62.9374 EndY=58.9932 EndZ=0
    g38: LineSegment StartX=54 StartY=61.7932 StartZ=0 EndX=58.9374 EndY=61.7932 EndZ=0
    g39: LineSegment StartX=58.9374 StartY=61.7932 StartZ=0 EndX=58.9374 EndY=58.9932 EndZ=0
    g40: LineSegment StartX=54 StartY=58.9932 StartZ=0 EndX=54 EndY=61.7932 EndZ=0
    g41: LineSegment StartX=50 StartY=58.9932 StartZ=0 EndX=54 EndY=58.9932 EndZ=0
    g42: Circle CenterX=56.5003 CenterY=33.429 CenterZ=0 NormalX=0 NormalY=0 NormalZ=1 AngleXU=0 Radius=1.2
    g43: LineSegment StartX=58.9374 StartY=58.9932 StartZ=0 EndX=62.9374 EndY=58.9932 EndZ=0
    g44: Circle CenterX=46.5 CenterY=45.7067 CenterZ=0 NormalX=0 NormalY=0 NormalZ=1 AngleXU=0 Radius=1.76
    g45: Circle CenterX=66.4374 CenterY=45.7067 CenterZ=0 NormalX=0 NormalY=0 NormalZ=1 AngleXU=0 Radius=1.76
    g46: LineSegment [constr] StartX=50 StartY=23.997 StartZ=0 EndX=50 EndY=58.9932 EndZ=0
    g47: LineSegment [constr] StartX=0 StartY=-85.2518 StartZ=0 EndX=71 EndY=-85.2518 EndZ=0
    g48: LineSegment [constr] StartX=71 StartY=-85.2518 StartZ=0 EndX=71 EndY=74.7482 EndZ=0
    g49: ArcOfCircle CenterX=1 CenterY=-319.059 CenterZ=0 NormalX=0 NormalY=0 NormalZ=1 AngleXU=0 Radius=244.061 StartAngle=1.2799 EndAngle=1.57489
    g50: LineSegment [constr] StartX=71 StartY=74.7482 StartZ=0 EndX=-3.40066e-11 EndY=74.7482 EndZ=0
    g51: ArcOfCircle CenterX=1 CenterY=-169.014 CenterZ=0 NormalX=0 NormalY=0 NormalZ=1 AngleXU=0 Radius=243.764 StartAngle=1.27951 EndAngle=1.5749
    g52: ArcOfCircle CenterX=-393.244 CenterY=-10.3715 CenterZ=0 NormalX=0 NormalY=0 NormalZ=1 AngleXU=0 Radius=470.244 StartAngle=6.12327 EndAngle=6.44305
    g53: LineSegment StartX=-6.8e-11 StartY=-75 StartZ=0 EndX=-3.4e-11 EndY=74.7482 EndZ=0
    g54: Circle [constr] CenterX=24.5109 CenterY=37.5126 CenterZ=0 NormalX=0 NormalY=0 NormalZ=1 AngleXU=0 Radius=1.6
    g55: Circle [constr] CenterX=24.5003 CenterY=-20.5109 CenterZ=0 NormalX=0 NormalY=0 NormalZ=1 AngleXU=0 Radius=1.6
    g56: Circle CenterX=24.5271 CenterY=17.5127 CenterZ=0 NormalX=0 NormalY=0 NormalZ=1 AngleXU=0 Radius=1.6
    g57: Circle CenterX=24.519 CenterY=27.5127 CenterZ=0 NormalX=0 NormalY=0 NormalZ=1 AngleXU=0 Radius=1.6
    g58: LineSegment [constr] StartX=24.5271 StartY=17.5127 StartZ=0 EndX=24.519 EndY=27.5127 EndZ=0
    g59: Circle CenterX=24.5109 CenterY=37.5127 CenterZ=0 NormalX=0 NormalY=0 NormalZ=1 AngleXU=0 Radius=1.6
    g60: LineSegment [constr] StartX=24.519 StartY=27.5127 StartZ=0 EndX=24.5109 EndY=37.5127 EndZ=0
    g61: Circle CenterX=24.5028 CenterY=47.5127 CenterZ=0 NormalX=0 NormalY=0 NormalZ=1 AngleXU=0 Radius=1.6
    g62: LineSegment [constr] StartX=24.5109 StartY=37.5127 StartZ=0 EndX=24.5028 EndY=47.5127 EndZ=0
    g63: Circle [constr] CenterX=24.5003 CenterY=-20.5111 CenterZ=0 NormalX=0 NormalY=0 NormalZ=1 AngleXU=0 Radius=1.6
    g64: Circle CenterX=24.5165 CenterY=-40.5109 CenterZ=0 NormalX=0 NormalY=0 NormalZ=1 AngleXU=0 Radius=1.6
    g65: Circle CenterX=24.5084 CenterY=-30.5109 CenterZ=0 NormalX=0 NormalY=0 NormalZ=1 AngleXU=0 Radius=1.6
    g66: LineSegment [constr] StartX=24.5165 StartY=-40.5109 StartZ=0 EndX=24.5084 EndY=-30.5109 EndZ=0
    g67: Circle CenterX=24.5003 CenterY=-20.5109 CenterZ=0 NormalX=0 NormalY=0 NormalZ=1 AngleXU=0 Radius=1.6
    g68: LineSegment [constr] StartX=24.5084 StartY=-30.5109 StartZ=0 EndX=24.5003 EndY=-20.5109 EndZ=0
    g69: Circle CenterX=24.4922 CenterY=-10.5109 CenterZ=0 NormalX=0 NormalY=0 NormalZ=1 AngleXU=0 Radius=1.6
    g70: LineSegment [constr] StartX=24.5003 StartY=-20.5109 StartZ=0 EndX=24.4922 EndY=-10.5109 EndZ=0
  constraints (183):
    c: Coincident(g0,g1)
    c: Coincident(g1,g2)
    c: Horizontal(g1)
    c: Vertical(g0)
    c: Vertical(g2)
    c: DistanceX(g1,g1) = 12.9374
    c: DistanceY(g0,g0) = 23.5065
    c: Coincident(g3,g4)
    c: Coincident(g5,g3)
    c: Horizontal(g3)
    c: Vertical(g4)
    c: Vertical(g5)
    c: DistanceY(g4,g4) = 2.8
    c: Coincident(g6,g0)
    c: Coincident(g6,g5)
    c: Horizontal(g6)
    c: DistanceY(g7,g0) = 2.0577
    c: DistanceX(g7,g1) = 6.4371
    c: Coincident(g8,g4)
    c: Coincident(g8,g2)
    c: Horizontal(g8)
    c: DistanceX(g8,g8) = 4
    c: Equal(g8,g6)
    c: DistanceX(g9,g0) = 3.5
    c: DistanceX(g1,g10) = 3.5
    c: DistanceY(g0,g9) = 10.22
    c: DistanceY(g1,g10) = 10.22
    c: Equal(g0,g2)
    c: Radius(g9) = 1.76
    c: Radius(g7) = 1.2
    c: DistanceX(g-1,g0) = 50
    c: Equal(g9,g10)
    c: Coincident(g11,g12)
    c: Coincident(g12,g13)
    c: Horizontal(g12)
    c: Vertical(g11)
    c: Vertical(g13)
    c: Equal(g1,g12) = 12.9374
    c: Equal(g0,g11) = 23.5065
    c: Coincident(g14,g15)
    c: Coincident(g16,g14)
    c: Horizontal(g14)
    c: Vertical(g15)
    c: Vertical(g16)
    c: Equal(g4,g15) = 2.8
    c: Coincident(g17,g11)
    c: Coincident(g17,g16)
    c: Horizontal(g17)
    c: DistanceY(g18,g11) = 2.0577
    c: DistanceX(g18,g12) = 6.4371
    c: Coincident(g19,g15)
    c: Coincident(g19,g13)
    c: Horizontal(g19)
    c: Equal(g8,g19) = 4
    c: Equal(g19,g17)
    c: DistanceX(g20,g11) = 3.5
    c: DistanceX(g12,g21) = 3.5
    c: DistanceY(g11,g20) = 10.22
    c: DistanceY(g12,g21) = 10.22
    c: Equal(g11,g13)
    c: Equal(g9,g20) = 1.76
    c: Equal(g7,g18) = 1.2
    c: Equal(g20,g21)
    c: Coincident(g0,g22)
    c: Coincident(g11,g22)
    c: Distance(g22) = 34.9962
    c: Angle(g22) = 1.5708
    c: Coincident(g23,g24)
    c: Coincident(g24,g25)
    c: Horizontal(g24)
    c: Vertical(g23)
    c: Vertical(g25)
    c: Equal(g1,g24) = 12.9374
    c: Equal(g0,g23) = 23.5065
    c: Coincident(g26,g27)
    c: Coincident(g28,g26)
    c: Horizontal(g26)
    c: Vertical(g27)
    c: Vertical(g28)
    c: Equal(g4,g27) = 2.8
    c: Coincident(g29,g23)
    c: Coincident(g29,g28)
    c: Horizontal(g29)
    c: DistanceY(g30,g23) = 2.0577
    c: DistanceX(g30,g24) = 6.4371
    c: Coincident(g31,g27)
    c: Coincident(g31,g25)
    c: Horizontal(g31)
    c: Equal(g8,g31) = 4
    c: Equal(g31,g29)
    c: DistanceX(g32,g23) = 3.5
    c: DistanceX(g24,g33) = 3.5
    c: DistanceY(g23,g32) = 10.22
    c: DistanceY(g24,g33) = 10.22
    c: Equal(g23,g25)
    c: Equal(g9,g32) = 1.76
    c: Equal(g7,g30) = 1.2
    c: Equal(g32,g33)
    c: Coincident(g11,g34)
    c: Coincident(g23,g34)
    c: Equal(g22,g34)
    c: Parallel(g34,g22)
    c: Coincident(g35,g36)
    c: Coincident(g36,g37)
    c: Horizontal(g36)
    c: Vertical(g35)
    c: Vertical(g37)
    c: Equal(g1,g36) = 12.9374
    c: Equal(g0,g35) = 23.5065
    c: Coincident(g38,g39)
    c: Coincident(g40,g38)
    c: Horizontal(g38)
    c: Vertical(g39)
    c: Vertical(g40)
    c: Equal(g4,g39) = 2.8
    c: Coincident(g41,g35)
    c: Coincident(g41,g40)
    c: Horizontal(g41)
    c: DistanceY(g42,g35) = 2.0577
    c: DistanceX(g42,g36) = 6.4371
    c: Coincident(g43,g39)
    c: Coincident(g43,g37)
    c: Horizontal(g43)
    c: Equal(g8,g43) = 4
    c: Equal(g43,g41)
    c: DistanceX(g44,g35) = 3.5
    c: DistanceX(g36,g45) = 3.5
    c: DistanceY(g35,g44) = 10.22
    c: DistanceY(g36,g45) = 10.22
    c: Equal(g35,g37)
    c: Equal(g9,g44) = 1.76
    c: Equal(g7,g42) = 1.2
    c: Equal(g44,g45)
    c: Coincident(g23,g46)
    c: Coincident(g35,g46)
    c: Equal(g22,g46)
    c: Parallel(g46,g22)
    c: PointOnObject(g47,g-2)
    c: Horizontal(g47)
    c: Coincident(g47,g48)
    c: Vertical(g48)
    c: DistanceX(g47,g47) = 71
    c: DistanceY(g48,g48) = 160
    c: DistanceY(g47,g1) = 15.75
    c: PointOnObject(g49,g-2)
    c: Coincident(g49,g47)
    c: Coincident(g48,g50)
    c: PointOnObject(g50,g-2)
    c: Horizontal(g50)
    c: Coincident(g52,g51)
    c: Coincident(g52,g47)
    c: Coincident(g53,g49)
    c: Coincident(g53,g50)
    c: Coincident(g50,g51)
    c: Radius(g54) = 1.6
    c: Equal(g54,g56) = 1.6
    c: Coincident(g56,g58)
    c: Coincident(g57,g58)
    c: Distance(g58) = 10
    c: Angle(g58) = 1.57161
    c: Coincident(g57,g60)
    c: Coincident(g59,g60)
    c: Equal(g58,g60)
    c: Parallel(g60,g58)
    c: Coincident(g59,g62)
    c: Coincident(g61,g62)
    c: Equal(g58,g62)
    c: Parallel(g62,g58)
    c: Equal(g54,g63) = 1.6
    c: Equal(g63,g64) = 1.6
    c: Coincident(g64,g66)
    c: Coincident(g65,g66)
    c: Equal(g58,g66) = 10
    c: Parallel(g58,g66) = 1.57161
    c: Coincident(g65,g68)
    c: Coincident(g67,g68)
    c: Equal(g66,g68)
    c: Parallel(g68,g66)
    c: Coincident(g67,g70)
    c: Coincident(g69,g70)
    c: Equal(g66,g70)
    c: Parallel(g70,g66)
    c: Coincident(g70,g55)
FEATURE [PartDesign::Pad] Pad012085  label="half_base003"
  Length = 3
  Length2 = 100
  Profile = -> Sketch234
  Refine = true
  Type = 0
FEATURE [PartDesign::Mirrored] Mirrored001  label="basic_base010"
  BaseFeature = -> Pad012085
  MirrorPlane = -> Sketch234 [V_Axis]
  Originals = -> [Pad012085]
  Refine = true
FEATURE [PartDesign::Body] Body024  label="robot_module_base001"
  Group = -> [Sketch234,Pad012085,Mirrored001]
  Origin = -> Origin042
  Tip = -> Mirrored001
FEATURE [App::Part] Part014  label="base004"
  Group = -> [Body024]
  License = CC BY 3.0
  LicenseURL = http://creativecommons.org/licenses/by/3.0/
  Origin = -> Origin041
  Placement = pos=(0,0,30) rot=(0,0,1;0rad)
FEATURE [App::DocumentObjectGroup] Grupo036  label="discarted-parts"
  Group = -> [Fusion,Part005,Part006,Fillet001,Part014]
FEATURE [Sketcher::SketchObject] Sketch237  label="base_cylinder022"
  MapMode = 5
  Support = -> [XY_Plane044]
  sketch-geometry (2):
    g0: Circle CenterX=0 CenterY=0 CenterZ=0 NormalX=0 NormalY=0 NormalZ=1 AngleXU=0 Radius=3.75
    g1: Circle CenterX=0 CenterY=0 CenterZ=0 NormalX=0 NormalY=0 NormalZ=1 AngleXU=0 Radius=5.75
  constraints (4):
    c: Coincident(g0,g-1)
    c: Radius(g0) = 3.75
    c: Coincident(g1,g-1)
    c: Radius(g1) = 5.75
FEATURE [Part::Feature] Pocket003122  label="Final-1-arm-horn026"
  Placement = pos=(0,0,32) rot=(0.707107,0.707107,0;3.14159rad)
  shape: bbox 8 x 22.5 x 5 mm, 19 faces (baked)
FEATURE [Part::Feature] Fusion007077  label="Servo-sg90-final028"
  Placement = pos=(0,-16.6,0) rot=(0,0,1;0rad)
  shape: bbox 11.8 x 32.4 x 29.9 mm, 77 faces (baked)
FEATURE [PartDesign::Pad] Pad012090  label="low_base009"
  Length = 2.25
  Length2 = 100
  Profile = -> Sketch237
  Refine = true
  Type = 0
FEATURE [Sketcher::SketchObject] Sketch246  label="basic_base011"
  MapMode = 5
  Placement = pos=(0,0,2.25) rot=(0,0,1;0rad)
  Support = -> [Pad012090]
  sketch-geometry (6):
    g0: LineSegment StartX=0 StartY=5.71563 StartZ=0 EndX=-20.5 EndY=5.71563 EndZ=0
    g1: LineSegment StartX=1.86762e-06 StartY=-5.71497 StartZ=0 EndX=-20.5 EndY=-5.71497 EndZ=0
    g2: LineSegment StartX=-20.5 StartY=5.71563 StartZ=0 EndX=-20.5 EndY=-5.71497 EndZ=0
    g3: LineSegment StartX=0 StartY=5.71563 StartZ=0 EndX=5.71497 EndY=5.71563 EndZ=0
    g4: LineSegment StartX=5.71497 StartY=5.71563 StartZ=0 EndX=5.71497 EndY=0 EndZ=0
    g5: ArcOfCircle CenterX=0 CenterY=0 CenterZ=0 NormalX=0 NormalY=0 NormalZ=1 AngleXU=0 Radius=5.71497 StartAngle=4.71239 EndAngle=6.28319
  constraints (14):
    c: PointOnObject(g0,g-2)
    c: Horizontal(g0)
    c: DistanceX(g0,g0) = 20.5
    c: Coincident(g2,g0)
    c: Vertical(g2)
    c: Coincident(g1,g2)
    c: Coincident(g0,g3)
    c: Horizontal(g3)
    c: Coincident(g4,g3)
    c: PointOnObject(g4,g-1)
    c: Vertical(g4)
    c: Coincident(g5,g-1)
    c: Coincident(g5,g1)
    c: Coincident(g5,g4)
FEATURE [PartDesign::Pad] Pad012089  label="q1_basic_base009"
  BaseFeature = -> Pad012090
  Length = 3.5
  Length2 = 100
  Profile = -> Sketch246
  Refine = true
  Type = 0
FEATURE [Sketcher::SketchObject] Sketch251  label="base_cylinder023"
  MapMode = 5
  Placement = pos=(0,6.2,0) rot=(0,0.707107,0.707107;3.14159rad)
  sketch-geometry (2):
    g0: Circle CenterX=24 CenterY=64 CenterZ=0 NormalX=0 NormalY=0 NormalZ=1 AngleXU=0 Radius=3.75
    g1: Circle CenterX=24 CenterY=64 CenterZ=0 NormalX=0 NormalY=0 NormalZ=1 AngleXU=0 Radius=5.75
  constraints (3):
    c: Radius(g0) = 3.75
    c: Radius(g1) = 5.75
    c: Coincident(g1,g0)
FEATURE [Part::Fillet] Fillet009  label="rounder_q1_servo007"
  Edges = 1 edges r=8: [Edge27]
  Placement = pos=(0,0,44) rot=(0,0,1;1.5708rad)
FEATURE [Sketcher::SketchObject] Sketch253  label="q1_base_horn009"
  MapMode = 5
  Placement = pos=(0,0,5.75) rot=(0,0,1;0rad)
  Support = -> [Pad012089]
  sketch-geometry (7):
    g0: LineSegment StartX=-1.25 StartY=3.53553 StartZ=0 EndX=-17 EndY=1.74295 EndZ=0
    g1: ArcOfCircle CenterX=-17 CenterY=0 CenterZ=0 NormalX=0 NormalY=0 NormalZ=1 AngleXU=0 Radius=1.74295 StartAngle=1.5708 EndAngle=3.14159
    g2: LineSegment [constr] StartX=-18.743 StartY=0 StartZ=0 EndX=0 EndY=0 EndZ=0
    g3: ArcOfCircle CenterX=0 CenterY=0 CenterZ=0 NormalX=0 NormalY=0 NormalZ=1 AngleXU=0 Radius=3.75 StartAngle=0 EndAngle=1.91063
    g4: LineSegment StartX=-1.25 StartY=-3.53553 StartZ=0 EndX=-17 EndY=-1.74295 EndZ=0
    g5: ArcOfCircle CenterX=-17 CenterY=-1e-12 CenterZ=0 NormalX=0 NormalY=0 NormalZ=1 AngleXU=0 Radius=1.74295 StartAngle=3.14159 EndAngle=4.71239
    g6: ArcOfCircle CenterX=0 CenterY=0 CenterZ=0 NormalX=0 NormalY=0 NormalZ=1 AngleXU=0 Radius=3.75 StartAngle=4.37255 EndAngle=6.28319
  constraints (11):
    c: PointOnObject(g1,g-1)
    c: Coincident(g1,g0)
    c: PointOnObject(g1,g-1)
    c: Coincident(g1,g2)
    c: Coincident(g3,g-1)
    c: Radius(g3) = 3.75
    c: Coincident(g3,g0)
    c: DistanceX(g0,g3) = 5
    c: Coincident(g5,g4)
    c: Radius(g6) = 3.75
    c: Coincident(g6,g4)
FEATURE [PartDesign::Pad] Pad012097  label="q2_base_cylinder013"
  Length = 2.25
  Length2 = 100
  Placement = pos=(0,6.2,0) rot=(0,0.707107,0.707107;3.14159rad)
  Profile = -> Sketch251
  Refine = true
  Type = 0
FEATURE [Sketcher::SketchObject] Sketch248  label="q2_base011"
  ExternalGeometry = -> [Pad012097]
  MapMode = 5
  Placement = pos=(2e-16,8.45,-9e-16) rot=(0,0.707107,0.707107;3.14159rad)
  Support = -> [Pad012097]
  sketch-geometry (6):
    g0: ArcOfCircle CenterX=24 CenterY=64 CenterZ=0 NormalX=0 NormalY=0 NormalZ=1 AngleXU=0 Radius=5.75 StartAngle=2.0944 EndAngle=5.23599
    g1: LineSegment [constr] StartX=12.5 StartY=64 StartZ=0 EndX=37 EndY=64 EndZ=0
    g2: LineSegment [constr] StartX=24 StartY=64 StartZ=0 EndX=21.125 EndY=68.9796 EndZ=0
    g3: LineSegment StartX=21.125 StartY=68.9796 StartZ=0 EndX=39.516 EndY=79.5977 EndZ=0
    g4: LineSegment StartX=39.516 StartY=79.5977 StartZ=0 EndX=45.266 EndY=69.6384 EndZ=0
    g5: LineSegment StartX=45.266 StartY=69.6384 StartZ=0 EndX=26.875 EndY=59.0204 EndZ=0
  constraints (14):
    c: Coincident(g0,g-3)
    c: PointOnObject(g0,g-3)
    c: Angle(g0) = 3.14159
    c: Horizontal(g1)
    c: PointOnObject(g0,g1)
    c: Coincident(g2,g0)
    c: Coincident(g2,g0)
    c: Angle(g1,g2) = 2.0944
    c: Tangent(g0,g3) = 1.5708
    c: Coincident(g3,g4)
    c: Coincident(g4,g5)
    c: Coincident(g5,g0)
    c: Equal(g3,g5)
    c: Parallel(g3,g5)
FEATURE [PartDesign::Pad] Pad012093  label="q2_basic_base007"
  BaseFeature = -> Pad012097
  Length = 3.5
  Length2 = 100
  Placement = pos=(0,6.2,0) rot=(0,0.707107,0.707107;3.14159rad)
  Profile = -> Sketch248
  Refine = true
  Type = 0
FEATURE [Sketcher::SketchObject] Sketch249  label="AUX_q2_base_horn010"
  ExternalGeometry = -> [Pad012093]
  MapMode = 5
  Placement = pos=(-3e-15,11.95,-6e-15) rot=(0.186157,0.694747,0.694747;3.50969rad)
  sketch-geometry (5):
    g0: LineSegment StartX=54.0346 StartY=46.9656 StartZ=0 EndX=69.7804 EndY=45.1656 EndZ=0
    g1: ArcOfCircle CenterX=69.7804 CenterY=43.4256 CenterZ=0 NormalX=0 NormalY=0 NormalZ=1 AngleXU=0 Radius=1.74 StartAngle=0 EndAngle=1.5708
    g2: LineSegment [constr] StartX=71.5204 StartY=43.4256 StartZ=0 EndX=49.0304 EndY=43.4256 EndZ=0
    g3: ArcOfCircle CenterX=52.7846 CenterY=43.4256 CenterZ=0 NormalX=0 NormalY=0 NormalZ=1 AngleXU=0 Radius=3.75421 StartAngle=1.23136 EndAngle=3.14159
    g4: LineSegment [constr] StartX=52.7846 StartY=49.1756 StartZ=0 EndX=52.7846 EndY=37.6756 EndZ=0
  constraints (16):
    c: Coincident(g1,g0)
    c: Coincident(g1,g2)
    c: Coincident(g3,g0)
    c: Radius(g1) = 1.74
    c: PointOnObject(g1,g2)
    c: Coincident(g2,g3)
    c: PointOnObject(g3,g2)
    c: DistanceX(g2,g2) = 22.49
    c: DistanceY(g1,g0) = 1.74
    c: DistanceX(g3,g0) = 1.25
    c: DistanceY(g3,g0) = 3.54
    c: Horizontal(g2)
    c: Coincident(g4,g-3)
    c: Coincident(g4,g-4)
    c: PointOnObject(g3,g4)
    c: Symmetric(g4,g4,g3)
FEATURE [Sketcher::SketchObject] Sketch244  label="horn_shape015"
  ExternalGeometry = -> [Sketch249]
  MapMode = 5
  Placement = pos=(6e-16,11.95,-5.8e-15) rot=(0,0.707107,0.707107;3.14159rad)
  Support = -> [Pad012093]
  sketch-geometry (7):
    g0: LineSegment [constr] StartX=20.7488 StartY=62.1229 StartZ=0 EndX=40.2257 EndY=73.3679 EndZ=0
    g1: ArcOfCircle CenterX=24 CenterY=64 CenterZ=0 NormalX=0 NormalY=0 NormalZ=1 AngleXU=0 Radius=3.75421 StartAngle=1.75495 EndAngle=3.66519
    g2: ArcOfCircle CenterX=38.7188 CenterY=72.4979 CenterZ=0 NormalX=0 NormalY=0 NormalZ=1 AngleXU=0 Radius=1.74 StartAngle=0.523599 EndAngle=2.0944
    g3: LineSegment StartX=23.3125 StartY=67.6907 StartZ=0 EndX=37.8488 EndY=74.0048 EndZ=0
    g4: ArcOfCircle CenterX=24 CenterY=64 CenterZ=0 NormalX=0 NormalY=0 NormalZ=1 AngleXU=0 Radius=3.75421 StartAngle=3.66519 EndAngle=5.57543
    g5: ArcOfCircle CenterX=38.7188 CenterY=72.4979 CenterZ=0 NormalX=0 NormalY=0 NormalZ=1 AngleXU=0 Radius=1.74 StartAngle=5.23599 EndAngle=6.80678
    g6: LineSegment StartX=26.8525 StartY=61.5593 StartZ=0 EndX=39.5888 EndY=70.991 EndZ=0
  constraints (16):
    c: Coincident(g0,g-5)
    c: Coincident(g0,g-4)
    c: Coincident(g1,g-5)
    c: Coincident(g1,g-5)
    c: Coincident(g1,g0)
    c: Coincident(g2,g-4)
    c: Coincident(g2,g0)
    c: Coincident(g2,g-4)
    c: Coincident(g3,g1)
    c: Coincident(g3,g2)
    c: Coincident(g6,g4)
    c: Coincident(g6,g5)
    c: Coincident(g0,g4)
    c: Coincident(g1,g4)
    c: Coincident(g2,g5)
    c: Coincident(g0,g5)
FEATURE [PartDesign::Pocket] Pocket003123  label="horn_shape014"
  BaseFeature = -> Pad012093
  Length = 2.65
  Length2 = 100
  Placement = pos=(0,6.2,0) rot=(0,0.707107,0.707107;3.14159rad)
  Profile = -> Sketch244
  Refine = true
  Type = 0
FEATURE [Sketcher::SketchObject] Sketch258  label="horn_holes017"
  ExternalGeometry = -> [Pocket003123]
  MapMode = 5
  Placement = pos=(2e-16,9.3,-5.3e-15) rot=(0,0.707107,0.707107;3.14159rad)
  Support = -> [Pocket003123]
  sketch-geometry (16):
    g0: Circle CenterX=24 CenterY=64 CenterZ=0 NormalX=0 NormalY=0 NormalZ=1 AngleXU=0 Radius=3.75
    g1: Circle CenterX=-14.6952 CenterY=0 CenterZ=0 NormalX=0 NormalY=0 NormalZ=1 AngleXU=0 Radius=0.75
    g2: Circle CenterX=-12.6952 CenterY=0 CenterZ=0 NormalX=0 NormalY=0 NormalZ=1 AngleXU=0 Radius=0.75
    g3: LineSegment [constr] StartX=-14.6952 StartY=0 StartZ=0 EndX=-12.6952 EndY=0 EndZ=0
    g4: Circle CenterX=-10.6952 CenterY=0 CenterZ=0 NormalX=0 NormalY=0 NormalZ=1 AngleXU=0 Radius=0.75
    g5: LineSegment [constr] StartX=-12.6952 StartY=0 StartZ=0 EndX=-10.6952 EndY=0 EndZ=0
    g6: Circle CenterX=-8.69518 CenterY=0 CenterZ=0 NormalX=0 NormalY=0 NormalZ=1 AngleXU=0 Radius=0.75
    g7: LineSegment [constr] StartX=-10.6952 StartY=0 StartZ=0 EndX=-8.69518 EndY=0 EndZ=0
    g8: Circle CenterX=-6.69518 CenterY=0 CenterZ=0 NormalX=0 NormalY=0 NormalZ=1 AngleXU=0 Radius=0.75
    g9: LineSegment [constr] StartX=-8.69518 StartY=0 StartZ=0 EndX=-6.69518 EndY=0 EndZ=0
    g10: LineSegment [constr] StartX=24 StartY=64 StartZ=0 EndX=43.3449 EndY=75.1688 EndZ=0
    g11: Circle CenterX=29.6292 CenterY=67.25 CenterZ=0 NormalX=0 NormalY=0 NormalZ=1 AngleXU=0 Radius=0.75
    g12: Circle CenterX=31.3612 CenterY=68.25 CenterZ=0 NormalX=0 NormalY=0 NormalZ=1 AngleXU=0 Radius=0.75
    g13: Circle CenterX=33.0933 CenterY=69.25 CenterZ=0 NormalX=0 NormalY=0 NormalZ=1 AngleXU=0 Radius=0.75
    g14: Circle CenterX=34.8253 CenterY=70.25 CenterZ=0 NormalX=0 NormalY=0 NormalZ=1 AngleXU=0 Radius=0.75
    g15: Circle CenterX=36.5574 CenterY=71.25 CenterZ=0 NormalX=0 NormalY=0 NormalZ=1 AngleXU=0 Radius=0.75
  constraints (41):
    c: Radius(g1) = 0.75
    c: Radius(g0) = 3.75
    c: Radius(g2) = 0.75
    c: Coincident(g1,g3)
    c: Coincident(g2,g3)
    c: Distance(g3) = 2
    c: Angle(g3) = 0
    c: Radius(g4) = 0.75
    c: Coincident(g2,g5)
    c: Coincident(g4,g5)
    c: Equal(g3,g5)
    c: Radius(g6) = 0.75
    c: Coincident(g4,g7)
    c: Coincident(g6,g7)
    c: Equal(g3,g7)
    c: Radius(g8) = 0.75
    c: Coincident(g6,g9)
    c: Coincident(g8,g9)
    c: Equal(g3,g9)
    c: Parallel(g9,g3)
    c: Parallel(g9,g7)
    c: Parallel(g7,g5)
    c: Coincident(g10,g0)
    c: Angle(g10) = 0.523599
    c: Radius(g11) = 0.75
    c: Distance(g0,g11) = 6.5
    c: PointOnObject(g11,g10)
    c: Equal(g11,g12) = 0.75
    c: PointOnObject(g12,g10)
    c: DistanceX(g0) = 24
    c: DistanceY(g0) = 64
    c: Distance(g11,g12) = 2
    c: Equal(g11,g13) = 0.75
    c: PointOnObject(g13,g10)
    c: Equal(g11,g14) = 0.75
    c: PointOnObject(g14,g10)
    c: Equal(g11,g15) = 0.75
    c: PointOnObject(g15,g10)
    c: Distance(g12,g13) = 2
    c: Distance(g13,g14) = 2
    c: Distance(g14,g15) = 2
FEATURE [Part::Feature] Fusion007079  label="Servo-sg90-final029"
  Placement = pos=(0,-16.6,0) rot=(0,0,1;0rad)
  shape: bbox 11.8 x 32.4 x 29.9 mm, 77 faces (baked)
FEATURE [PartDesign::Pocket] Pocket003126  label="q1_basic_horn009"
  BaseFeature = -> Pad012089
  Length = 2.65
  Length2 = 100
  Profile = -> Sketch253
  Refine = true
  Type = 0
FEATURE [Sketcher::SketchObject] Sketch240  label="horn_holes016"
  MapMode = 5
  Placement = pos=(0,0,3.1) rot=(0,0,1;0rad)
  Support = -> [Pocket003126]
  sketch-geometry (10):
    g0: Circle CenterX=0 CenterY=0 CenterZ=0 NormalX=0 NormalY=0 NormalZ=1 AngleXU=0 Radius=3.75
    g1: Circle CenterX=-14.5 CenterY=0 CenterZ=0 NormalX=0 NormalY=0 NormalZ=1 AngleXU=0 Radius=0.75
    g2: Circle CenterX=-12.5 CenterY=0 CenterZ=0 NormalX=0 NormalY=0 NormalZ=1 AngleXU=0 Radius=0.75
    g3: LineSegment [constr] StartX=-14.5 StartY=0 StartZ=0 EndX=-12.5 EndY=0 EndZ=0
    g4: Circle CenterX=-10.5 CenterY=0 CenterZ=0 NormalX=0 NormalY=0 NormalZ=1 AngleXU=0 Radius=0.75
    g5: LineSegment [constr] StartX=-12.5 StartY=0 StartZ=0 EndX=-10.5 EndY=0 EndZ=0
    g6: Circle CenterX=-8.5 CenterY=0 CenterZ=0 NormalX=0 NormalY=0 NormalZ=1 AngleXU=0 Radius=0.75
    g7: LineSegment [constr] StartX=-10.5 StartY=0 StartZ=0 EndX=-8.5 EndY=0 EndZ=0
    g8: Circle CenterX=-6.5 CenterY=0 CenterZ=0 NormalX=0 NormalY=0 NormalZ=1 AngleXU=0 Radius=0.75
    g9: LineSegment [constr] StartX=-8.5 StartY=0 StartZ=0 EndX=-6.5 EndY=0 EndZ=0
  constraints (25):
    c: Coincident(g0,g-1)
    c: Radius(g1) = 0.75
    c: Radius(g0) = 3.75
    c: Radius(g2) = 0.75
    c: Coincident(g1,g3)
    c: Coincident(g2,g3)
    c: Distance(g3) = 2
    c: Angle(g3) = 0
    c: Radius(g4) = 0.75
    c: Coincident(g2,g5)
    c: Coincident(g4,g5)
    c: Equal(g3,g5)
    c: Parallel(g5,g3)
    c: Radius(g6) = 0.75
    c: Coincident(g4,g7)
    c: Coincident(g6,g7)
    c: Equal(g3,g7)
    c: Parallel(g7,g3)
    c: Radius(g8) = 0.75
    c: Coincident(g6,g9)
    c: Coincident(g8,g9)
    c: Equal(g3,g9)
    c: Parallel(g9,g3)
    c: PointOnObject(g2,g-1)
    c: DistanceX(g8,g-1) = 6.5
FEATURE [PartDesign::Pocket] Pocket003124  label="q1_basic_horn_shape009"
  BaseFeature = -> Pocket003126
  Length = 5
  Length2 = 100
  Profile = -> Sketch240
  Refine = true
  Type = 0
FEATURE [Sketcher::SketchObject] Sketch242  label="q2-base007"
  ExternalGeometry = -> [Pocket003124]
  MapMode = 5
  Placement = pos=(-20.5,0,0) rot=(0.57735,-0.57735,-0.57735;2.0944rad)
  Support = -> [Pocket003124]
  sketch-geometry (6):
    g0: LineSegment StartX=-5.71563 StartY=2.25 StartZ=0 EndX=-11.6041 EndY=2.25 EndZ=0
    g1: LineSegment StartX=-11.6041 StartY=2.25 StartZ=0 EndX=-38.6752 EndY=17.8795 EndZ=0
    g2: LineSegment StartX=-11.6626 StartY=5.74787 StartZ=0 EndX=-37.1752 EndY=20.4776 EndZ=0
    g3: LineSegment StartX=-37.1752 StartY=20.4776 StartZ=0 EndX=-38.6752 EndY=17.8795 EndZ=0
    g4: LineSegment StartX=-5.71563 StartY=5.74787 StartZ=0 EndX=-5.71563 EndY=2.25 EndZ=0
    g5: LineSegment StartX=-11.6626 StartY=5.74787 StartZ=0 EndX=-5.71563 EndY=5.74787 EndZ=0
  constraints (13):
    c: Coincident(g3,g2)
    c: Coincident(g3,g1)
    c: Perpendicular(g3,g1)
    c: Coincident(g0,g-3)
    c: Parallel(g1,g2)
    c: Coincident(g4,g0)
    c: Perpendicular(g4,g0)
    c: Distance(g1,g2) = 3
    c: Angle(g0,g1) = 2.61799
    c: Coincident(g0,g1)
    c: Coincident(g2,g5)
    c: Coincident(g5,g4)
    c: Horizontal(g5)
FEATURE [PartDesign::Pad] Pad012091  label="q2-bed-base007"
  BaseFeature = -> Pocket003124
  Length = 26.215
  Length2 = 100
  Profile = -> Sketch242
  Refine = true
  Reversed = true
  Type = 0
FEATURE [Sketcher::SketchObject] Sketch259  label="q2-corner-hole015"
  MapMode = 5
  Placement = pos=(0,0,5.74787) rot=(0,0,1;0rad)
  Support = -> [Pad012091]
  sketch-geometry (4):
    g0: LineSegment StartX=-1.62396 StartY=12 StartZ=0 EndX=-5 EndY=12 EndZ=0
    g1: LineSegment StartX=-5 StartY=12 StartZ=0 EndX=-5 EndY=6.68085 EndZ=0
    g2: LineSegment StartX=-5 StartY=6.68085 StartZ=0 EndX=-1.62396 EndY=6.68085 EndZ=0
    g3: LineSegment StartX=-1.62396 StartY=6.68085 StartZ=0 EndX=-1.62396 EndY=12 EndZ=0
  constraints (8):
    c: Coincident(g0,g1)
    c: Coincident(g1,g2)
    c: Coincident(g2,g3)
    c: Coincident(g3,g0)
    c: Horizontal(g0)
    c: Horizontal(g2)
    c: Vertical(g1)
    c: Vertical(g3)
FEATURE [PartDesign::Pocket] Pocket003125  label="q2-corner-hole014"
  BaseFeature = -> Pad012091
  Length = 2
  Length2 = 100
  Profile = -> Sketch259
  Refine = true
  Type = 0
FEATURE [Part::MultiFuse] Fusion007080  label="q2-aux-servo009"
  Placement = pos=(23.9256,-20.5,63.7846) rot=(0.377964,0.654656,0.654652;3.86432rad)
  Refine = true
  Shapes = -> [Fusion007079,Pocket003122]
FEATURE [Part::Feature] Pocket003127  label="Final-1-arm-horn027"
  Placement = pos=(0,0,32) rot=(0.707107,-0.707107,0;3.14159rad)
  shape: bbox 8 x 22.5 x 5 mm, 19 faces (baked)
FEATURE [Part::MultiFuse] Fusion007078  label="q1-aux-servo009"
  Placement = pos=(0,0,17.25) rot=(0,0,1;0rad)
  Refine = true
  Shapes = -> [Pocket003127,Fusion007077]
FEATURE [PartDesign::Pocket] Pocket003128  label="basic_horn_union007"
  BaseFeature = -> Pocket003123
  Length = 5
  Length2 = 100
  Placement = pos=(0,6.2,0) rot=(0,0.707107,0.707107;3.14159rad)
  Profile = -> Sketch258
  Refine = true
  Type = 0
FEATURE [Sketcher::SketchObject] Sketch256  label="q2_bridge015"
  ExternalGeometry = -> [Pocket003128]
  MapMode = 5
  Placement = pos=(2e-16,8.45,-2.3e-15) rot=(0,-0.707107,0.707107;3.14159rad)
  Support = -> [Pocket003128]
  sketch-geometry (4):
    g0: LineSegment StartX=39.516 StartY=-79.5977 StartZ=0 EndX=45.266 EndY=-69.6384 EndZ=0
    g1: LineSegment StartX=45.266 StartY=-69.6384 StartZ=0 EndX=40.9358 EndY=-67.1384 EndZ=0
    g2: LineSegment StartX=39.516 StartY=-79.5977 StartZ=0 EndX=35.1858 EndY=-77.0977 EndZ=0
    g3: ArcOfCircle CenterX=24.5001 CenterY=-64.2888 CenterZ=0 NormalX=0 NormalY=0 NormalZ=1 AngleXU=0 Radius=16.6809 StartAngle=5.40766 EndAngle=6.11151
  constraints (10):
    c: Coincident(g-5,g0)
    c: Coincident(g0,g-5)
    c: Coincident(g0,g1)
    c: PointOnObject(g1,g-3)
    c: Coincident(g0,g2)
    c: PointOnObject(g2,g-4)
    c: Distance(g2) = 5
    c: Equal(g2,g1)
    c: Coincident(g3,g1)
    c: Coincident(g3,g2)
FEATURE [PartDesign::Pad] Pad012088  label="q2_bridge014"
  BaseFeature = -> Pocket003128
  Length = 31
  Length2 = 100
  Placement = pos=(0,6.2,0) rot=(0,0.707107,0.707107;3.14159rad)
  Profile = -> Sketch256
  Refine = true
  Type = 0
FEATURE [Sketcher::SketchObject] Sketch243  label="q2_back_union007"
  ExternalGeometry = -> [Pad012097,Sketch248]
  MapMode = 5
  Placement = pos=(-2.3e-15,-22.55,3.83e-14) rot=(0,-0.707107,0.707107;3.14159rad)
  Support = -> [Pad012088]
  expr: Constraints[2] = Sketch067.Constraints[2]
  sketch-geometry (7):
    g0: ArcOfCircle CenterX=24 CenterY=-64 CenterZ=0 NormalX=0 NormalY=0 NormalZ=1 AngleXU=0 Radius=5.75 StartAngle=1.0472 EndAngle=4.18879
    g1: LineSegment [constr] StartX=12.5 StartY=-64 StartZ=0 EndX=37 EndY=-64 EndZ=0
    g2: LineSegment [constr] StartX=24 StartY=-64 StartZ=0 EndX=26.875 EndY=-59.0204 EndZ=0
    g3: LineSegment StartX=45.266 StartY=-69.6384 StartZ=0 EndX=26.875 EndY=-59.0204 EndZ=0
    g4: LineSegment StartX=45.266 StartY=-69.6384 StartZ=0 EndX=39.516 EndY=-79.5977 EndZ=0
    g5: LineSegment StartX=39.516 StartY=-79.5977 StartZ=0 EndX=21.125 EndY=-68.9796 EndZ=0
    g6: Circle CenterX=24 CenterY=-64 CenterZ=0 NormalX=0 NormalY=0 NormalZ=1 AngleXU=0 Radius=2
  constraints (16):
    c: Coincident(g0,g-3)
    c: PointOnObject(g0,g-3)
    c: Angle(g0) = 3.14159
    c: Horizontal(g1)
    c: PointOnObject(g0,g1)
    c: Coincident(g2,g0)
    c: Coincident(g2,g0)
    c: Parallel(g2,g-4)
    c: Coincident(g-4,g3)
    c: Coincident(g3,g0)
    c: Coincident(g3,g4)
    c: Coincident(g4,g-4)
    c: Coincident(g4,g5)
    c: Coincident(g5,g0)
    c: Coincident(g6,g0)
    c: Radius(g6) = 2
FEATURE [PartDesign::Pad] Pad012096  label="q2_joint007"
  BaseFeature = -> Pad012088
  Length = 3.5
  Length2 = 100
  Placement = pos=(0,6.2,0) rot=(0,0.707107,0.707107;3.14159rad)
  Profile = -> Sketch243
  Refine = true
  Type = 0
FEATURE [Sketcher::SketchObject] Sketch239  label="q2-leg_union_section007"
  ExternalGeometry = -> [Pad012096]
  MapMode = 5
  Placement = pos=(-64.1038,6.2,37.0103) rot=(0,-1,0;1.0472rad)
  Support = -> [Pad012096]
  sketch-geometry (4):
    g0: LineSegment StartX=49.1756 StartY=5.75 StartZ=0 EndX=49.1756 EndY=-32.25 EndZ=0
    g1: LineSegment StartX=49.1756 StartY=-32.25 StartZ=0 EndX=37.6756 EndY=-32.25 EndZ=0
    g2: LineSegment StartX=37.6756 StartY=-32.25 StartZ=0 EndX=37.6756 EndY=5.75 EndZ=0
    g3: LineSegment StartX=37.6756 StartY=5.75 StartZ=0 EndX=49.1756 EndY=5.75 EndZ=0
  constraints (8):
    c: Coincident(g-6,g0)
    c: Coincident(g0,g-6)
    c: Coincident(g0,g1)
    c: Coincident(g1,g-5)
    c: Coincident(g-5,g2)
    c: Coincident(g2,g-4)
    c: Coincident(g2,g3)
    c: Coincident(g3,g0)
FEATURE [Sketcher::SketchObject] Sketch260  label="trajectory007"
  ExternalGeometry = -> [Pad012096]
  MapMode = 5
  Placement = pos=(6e-16,11.95,-5.8e-15) rot=(0,0.707107,0.707107;3.14159rad)
  Support = -> [Pad012096]
  sketch-geometry (8):
    g0: GeomPoint X=42.3808 Y=74.6356 Z=0
    g1-g4: Circle [constr] x4 (B-spline internal-alignment scaffolding for g5; pole/knot coordinates omitted)
    g5: BSplineCurve PolesCount=4 KnotsCount=2 Degree=3 IsPeriodic=0
    g6: GeomPoint [constr] X=42.3808 Y=74.6356 Z=0
    g7: GeomPoint [constr] X=64.6677 Y=0 Z=0
  constraints (10):
    c: PointOnObject(g0,g-3)
    c: Coincident(g1,g0)
    c: Radius(g1) = 4
    c: Equal(g1,g2)
    c: Equal(g1,g3)
    c: Equal(g1,g4)
    c: PointOnObject(g4,g-1)
    c: InternalAlignment(g1-g4 -> g5) x4
    c: InternalAlignment(g6,g5)
    c: InternalAlignment(g7,g5)
FEATURE [Sketcher::SketchObject] Sketch250  label="q2-bone-touch_section007"
  ExternalGeometry = -> [Sketch260,Pad012096]
  MapMode = 5
  Support = -> [XY_Plane043]
  sketch-geometry (7):
    g0: LineSegment StartX=-66.1677 StartY=-4.55 StartZ=0 EndX=-63.1677 EndY=-4.55 EndZ=0
    g1: LineSegment StartX=-63.1677 StartY=-4.55 StartZ=0 EndX=-63.1677 EndY=-9.55 EndZ=0
    g2: LineSegment StartX=-63.1677 StartY=-9.55 StartZ=0 EndX=-66.1677 EndY=-9.55 EndZ=0
    g3: LineSegment StartX=-66.1677 StartY=-9.55 StartZ=0 EndX=-66.1677 EndY=-4.55 EndZ=0
    g4: GeomPoint X=-45.266 Y=-7.05 Z=0
    g5: GeomPoint X=-63.1677 Y=-7.05 Z=0
    g6: GeomPoint X=-64.6677 Y=-4.55 Z=0
  constraints (18):
    c: Coincident(g0,g1)
    c: Coincident(g1,g2)
    c: Coincident(g2,g3)
    c: Coincident(g3,g0)
    c: Horizontal(g0)
    c: Horizontal(g2)
    c: Vertical(g1)
    c: Vertical(g3)
    c: PointOnObject(g4,g-4)
    c: Symmetric(g-4,g-4,g4)
    c: PointOnObject(g5,g1)
    c: Symmetric(g0,g1,g5)
    c: Horizontal(g5,g4)
    c: PointOnObject(g6,g0)
    c: Symmetric(g0,g0,g6)
    c: Vertical(g6,g-3)
    c: DistanceX(g2,g2) = 3
    c: DistanceY(g3,g3) = 5
FEATURE [PartDesign::AdditivePipe] AdditivePipe007
  AuxilleryCurvelinear = true
  AuxillerySpineTangent = false
  BaseFeature = -> Pad012096
  Binormal = (0,0,0)
  Mode = 0
  Placement = pos=(0,6.2,0) rot=(0,0.707107,0.707107;3.14159rad)
  Profile = -> Sketch239
  Refine = true
  Sections = -> [Sketch250]
  Spine = -> Sketch260
  SpineTangent = false
  Transformation = 1
  Transition = 0
FEATURE [PartDesign::Body] Body026  label="Q2-Leg-joint007"
  Group = -> [Sketch251,Pad012097,Sketch248,Pad012093,Sketch249,Sketch244,Pocket003123,Sketch258,Pocket003128,Sketch256,Pad012088,Sketch243,Pad012096,Sketch260,Sketch239,Sketch250,AdditivePipe007]
  Origin = -> Origin045
  Tip = -> AdditivePipe007
FEATURE [Sketcher::SketchObject] Sketch261  label="half_base_sketch002"
  MapMode = 5
  sketch-geometry (58):
    g0: LineSegment StartX=50 StartY=-45.9953 StartZ=0 EndX=50 EndY=-69.5018 EndZ=0
    g1: LineSegment StartX=50 StartY=-69.5018 StartZ=0 EndX=62.9374 EndY=-69.5018 EndZ=0
    g2: LineSegment StartX=62.9374 StartY=-69.5018 StartZ=0 EndX=62.9374 EndY=-45.9953 EndZ=0
    g3: LineSegment StartX=54 StartY=-43.1953 StartZ=0 EndX=58.9374 EndY=-43.1953 EndZ=0
    g4: LineSegment StartX=58.9374 StartY=-43.1953 StartZ=0 EndX=58.9374 EndY=-45.9953 EndZ=0
    g5: LineSegment StartX=54 StartY=-45.9953 StartZ=0 EndX=54 EndY=-43.1953 EndZ=0
    g6: LineSegment StartX=50 StartY=-45.9953 StartZ=0 EndX=54 EndY=-45.9953 EndZ=0
    g7: Circle CenterX=56.5003 CenterY=-71.5595 CenterZ=0 NormalX=0 NormalY=0 NormalZ=1 AngleXU=0 Radius=1.2
    g8: LineSegment StartX=58.9374 StartY=-45.9953 StartZ=0 EndX=62.9374 EndY=-45.9953 EndZ=0
    g9: Circle CenterX=46.5 CenterY=-59.2818 CenterZ=0 NormalX=0 NormalY=0 NormalZ=1 AngleXU=0 Radius=1.76
    g10: Circle CenterX=66.4374 CenterY=-59.2818 CenterZ=0 NormalX=0 NormalY=0 NormalZ=1 AngleXU=0 Radius=1.76
    g11: LineSegment StartX=50 StartY=6.50467 StartZ=0 EndX=50 EndY=-17.0018 EndZ=0
    g12: LineSegment StartX=50 StartY=-17.0018 StartZ=0 EndX=62.9374 EndY=-17.0018 EndZ=0
    g13: LineSegment StartX=62.9374 StartY=-17.0018 StartZ=0 EndX=62.9374 EndY=6.50467 EndZ=0
    g14: LineSegment StartX=54 StartY=9.30467 StartZ=0 EndX=58.9374 EndY=9.30467 EndZ=0
    g15: LineSegment StartX=58.9374 StartY=9.30467 StartZ=0 EndX=58.9374 EndY=6.50467 EndZ=0
    g16: LineSegment StartX=54 StartY=6.50467 StartZ=0 EndX=54 EndY=9.30467 EndZ=0
    g17: LineSegment StartX=50 StartY=6.50467 StartZ=0 EndX=54 EndY=6.50467 EndZ=0
    g18: Circle CenterX=56.5003 CenterY=-19.0595 CenterZ=0 NormalX=0 NormalY=0 NormalZ=1 AngleXU=0 Radius=1.2
    g19: LineSegment StartX=58.9374 StartY=6.50467 StartZ=0 EndX=62.9374 EndY=6.50467 EndZ=0
    g20: Circle CenterX=46.5 CenterY=-6.78183 CenterZ=0 NormalX=0 NormalY=0 NormalZ=1 AngleXU=0 Radius=1.76
    g21: Circle CenterX=66.4374 CenterY=-6.78183 CenterZ=0 NormalX=0 NormalY=0 NormalZ=1 AngleXU=0 Radius=1.76
    g22: LineSegment [constr] StartX=50 StartY=-45.9953 StartZ=0 EndX=50 EndY=6.50467 EndZ=0
    g23: LineSegment StartX=50 StartY=58.9932 StartZ=0 EndX=50 EndY=35.4867 EndZ=0
    g24: LineSegment StartX=50 StartY=35.4867 StartZ=0 EndX=62.9374 EndY=35.4867 EndZ=0
    g25: LineSegment StartX=62.9374 StartY=35.4867 StartZ=0 EndX=62.9374 EndY=58.9932 EndZ=0
    g26: LineSegment StartX=54 StartY=61.7932 StartZ=0 EndX=58.9374 EndY=61.7932 EndZ=0
    g27: LineSegment StartX=58.9374 StartY=61.7932 StartZ=0 EndX=58.9374 EndY=58.9932 EndZ=0
    g28: LineSegment StartX=54 StartY=58.9932 StartZ=0 EndX=54 EndY=61.7932 EndZ=0
    g29: LineSegment StartX=50 StartY=58.9932 StartZ=0 EndX=54 EndY=58.9932 EndZ=0
    g30: Circle CenterX=56.5003 CenterY=33.429 CenterZ=0 NormalX=0 NormalY=0 NormalZ=1 AngleXU=0 Radius=1.2
    g31: LineSegment StartX=58.9374 StartY=58.9932 StartZ=0 EndX=62.9374 EndY=58.9932 EndZ=0
    g32: Circle CenterX=46.5 CenterY=45.7067 CenterZ=0 NormalX=0 NormalY=0 NormalZ=1 AngleXU=0 Radius=1.76
    g33: Circle CenterX=66.4374 CenterY=45.7067 CenterZ=0 NormalX=0 NormalY=0 NormalZ=1 AngleXU=0 Radius=1.76
    g34: LineSegment [constr] StartX=0 StartY=-85.2518 StartZ=0 EndX=71 EndY=-85.2518 EndZ=0
    g35: LineSegment [constr] StartX=71 StartY=-85.2518 StartZ=0 EndX=71 EndY=74.7482 EndZ=0
    g36: ArcOfCircle CenterX=0.999999 CenterY=-319.059 CenterZ=0 NormalX=0 NormalY=0 NormalZ=1 AngleXU=0 Radius=244.061 StartAngle=1.2799 EndAngle=1.57489
    g37: LineSegment [constr] StartX=71 StartY=74.7482 StartZ=0 EndX=0 EndY=74.7482 EndZ=0
    g38: ArcOfCircle CenterX=1 CenterY=-169.014 CenterZ=0 NormalX=0 NormalY=0 NormalZ=1 AngleXU=0 Radius=243.764 StartAngle=1.27951 EndAngle=1.5749
    g39: ArcOfCircle CenterX=-393.244 CenterY=-10.3715 CenterZ=0 NormalX=0 NormalY=0 NormalZ=1 AngleXU=0 Radius=470.244 StartAngle=6.12327 EndAngle=6.44305
    g40: LineSegment StartX=0 StartY=-75 StartZ=0 EndX=0 EndY=74.7482 EndZ=0
    g41: Circle [constr] CenterX=24.5109 CenterY=37.5126 CenterZ=0 NormalX=0 NormalY=0 NormalZ=1 AngleXU=0 Radius=1.6
    g42: Circle [constr] CenterX=24.5003 CenterY=-20.5109 CenterZ=0 NormalX=0 NormalY=0 NormalZ=1 AngleXU=0 Radius=1.6
    g43: Circle CenterX=24.5271 CenterY=17.5127 CenterZ=0 NormalX=0 NormalY=0 NormalZ=1 AngleXU=0 Radius=1.6
    g44: Circle CenterX=24.519 CenterY=27.5127 CenterZ=0 NormalX=0 NormalY=0 NormalZ=1 AngleXU=0 Radius=1.6
    g45: LineSegment [constr] StartX=24.5271 StartY=17.5127 StartZ=0 EndX=24.519 EndY=27.5127 EndZ=0
    g46: Circle CenterX=24.5109 CenterY=37.5127 CenterZ=0 NormalX=0 NormalY=0 NormalZ=1 AngleXU=0 Radius=1.6
    g47: LineSegment [constr] StartX=24.519 StartY=27.5127 StartZ=0 EndX=24.5109 EndY=37.5127 EndZ=0
    g48: Circle CenterX=24.5028 CenterY=47.5127 CenterZ=0 NormalX=0 NormalY=0 NormalZ=1 AngleXU=0 Radius=1.6
    g49: LineSegment [constr] StartX=24.5109 StartY=37.5127 StartZ=0 EndX=24.5028 EndY=47.5127 EndZ=0
    g50: Circle [constr] CenterX=24.5003 CenterY=-20.5111 CenterZ=0 NormalX=0 NormalY=0 NormalZ=1 AngleXU=0 Radius=1.6
    g51: Circle CenterX=24.5165 CenterY=-40.5109 CenterZ=0 NormalX=0 NormalY=0 NormalZ=1 AngleXU=0 Radius=1.6
    g52: Circle CenterX=24.5084 CenterY=-30.5109 CenterZ=0 NormalX=0 NormalY=0 NormalZ=1 AngleXU=0 Radius=1.6
    g53: LineSegment [constr] StartX=24.5165 StartY=-40.5109 StartZ=0 EndX=24.5084 EndY=-30.5109 EndZ=0
    g54: Circle CenterX=24.5003 CenterY=-20.5109 CenterZ=0 NormalX=0 NormalY=0 NormalZ=1 AngleXU=0 Radius=1.6
    g55: LineSegment [constr] StartX=24.5084 StartY=-30.5109 StartZ=0 EndX=24.5003 EndY=-20.5109 EndZ=0
    g56: Circle CenterX=24.4922 CenterY=-10.5109 CenterZ=0 NormalX=0 NormalY=0 NormalZ=1 AngleXU=0 Radius=1.6
    g57: LineSegment [constr] StartX=24.5003 StartY=-20.5109 StartZ=0 EndX=24.4922 EndY=-10.5109 EndZ=0
  constraints (145):
    c: Coincident(g0,g1)
    c: Coincident(g1,g2)
    c: Horizontal(g1)
    c: Vertical(g0)
    c: Vertical(g2)
    c: DistanceX(g1,g1) = 12.9374
    c: DistanceY(g0,g0) = 23.5065
    c: Coincident(g3,g4)
    c: Coincident(g5,g3)
    c: Horizontal(g3)
    c: Vertical(g4)
    c: Vertical(g5)
    c: DistanceY(g4,g4) = 2.8
    c: Coincident(g6,g0)
    c: Coincident(g6,g5)
    c: Horizontal(g6)
    c: DistanceY(g7,g0) = 2.0577
    c: DistanceX(g7,g1) = 6.4371
    c: Coincident(g8,g4)
    c: Coincident(g8,g2)
    c: Horizontal(g8)
    c: DistanceX(g8,g8) = 4
    c: Equal(g8,g6)
    c: DistanceX(g9,g0) = 3.5
    c: DistanceX(g1,g10) = 3.5
    c: DistanceY(g0,g9) = 10.22
    c: DistanceY(g1,g10) = 10.22
    c: Equal(g0,g2)
    c: Radius(g9) = 1.76
    c: Radius(g7) = 1.2
    c: DistanceX(g-1,g0) = 50
    c: Equal(g9,g10)
    c: Coincident(g11,g12)
    c: Coincident(g12,g13)
    c: Horizontal(g12)
    c: Vertical(g11)
    c: Vertical(g13)
    c: Equal(g1,g12) = 12.9374
    c: Equal(g0,g11) = 23.5065
    c: Coincident(g14,g15)
    c: Coincident(g16,g14)
    c: Horizontal(g14)
    c: Vertical(g15)
    c: Vertical(g16)
    c: Equal(g4,g15) = 2.8
    c: Coincident(g17,g11)
    c: Coincident(g17,g16)
    c: Horizontal(g17)
    c: DistanceY(g18,g11) = 2.0577
    c: DistanceX(g18,g12) = 6.4371
    c: Coincident(g19,g15)
    c: Coincident(g19,g13)
    c: Horizontal(g19)
    c: Equal(g8,g19) = 4
    c: Equal(g19,g17)
    c: DistanceX(g20,g11) = 3.5
    c: DistanceX(g12,g21) = 3.5
    c: DistanceY(g11,g20) = 10.22
    c: DistanceY(g12,g21) = 10.22
    c: Equal(g11,g13)
    c: Equal(g9,g20) = 1.76
    c: Equal(g7,g18) = 1.2
    c: Equal(g20,g21)
    c: Coincident(g0,g22)
    c: Coincident(g11,g22)
    c: Distance(g22) = 52.5
    c: Angle(g22) = 1.5708
    c: Coincident(g23,g24)
    c: Coincident(g24,g25)
    c: Horizontal(g24)
    c: Vertical(g23)
    c: Vertical(g25)
    c: Equal(g1,g24) = 12.9374
    c: Equal(g0,g23) = 23.5065
    c: Coincident(g26,g27)
    c: Coincident(g28,g26)
    c: Horizontal(g26)
    c: Vertical(g27)
    c: Vertical(g28)
    c: Equal(g4,g27) = 2.8
    c: Coincident(g29,g23)
    c: Coincident(g29,g28)
    c: Horizontal(g29)
    c: DistanceY(g30,g23) = 2.0577
    c: DistanceX(g30,g24) = 6.4371
    c: Coincident(g31,g27)
    c: Coincident(g31,g25)
    c: Horizontal(g31)
    c: Equal(g8,g31) = 4
    c: Equal(g31,g29)
    c: DistanceX(g32,g23) = 3.5
    c: DistanceX(g24,g33) = 3.5
    c: DistanceY(g23,g32) = 10.22
    c: DistanceY(g24,g33) = 10.22
    c: Equal(g23,g25)
    c: Equal(g9,g32) = 1.76
    c: Equal(g7,g30) = 1.2
    c: Equal(g32,g33)
    c: PointOnObject(g34,g-2)
    c: Horizontal(g34)
    c: Coincident(g34,g35)
    c: Vertical(g35)
    c: DistanceX(g34,g34) = 71
    c: DistanceY(g35,g35) = 160
    c: DistanceY(g34,g1) = 15.75
    c: PointOnObject(g36,g-2)
    c: Coincident(g36,g34)
    c: Coincident(g35,g37)
    c: PointOnObject(g37,g-2)
    c: Horizontal(g37)
    c: Coincident(g39,g38)
    c: Coincident(g39,g34)
    c: Coincident(g40,g36)
    c: Coincident(g40,g37)
    c: Coincident(g37,g38)
    c: Radius(g41) = 1.6
    c: Equal(g41,g43) = 1.6
    c: Coincident(g43,g45)
    c: Coincident(g44,g45)
    c: Distance(g45) = 10
    c: Angle(g45) = 1.57161
    c: Coincident(g44,g47)
    c: Coincident(g46,g47)
    c: Equal(g45,g47)
    c: Parallel(g47,g45)
    c: Coincident(g46,g49)
    c: Coincident(g48,g49)
    c: Equal(g45,g49)
    c: Parallel(g49,g45)
    c: Equal(g41,g50) = 1.6
    c: Equal(g50,g51) = 1.6
    c: Coincident(g51,g53)
    c: Coincident(g52,g53)
    c: Equal(g45,g53) = 10
    c: Parallel(g45,g53) = 1.57161
    c: Coincident(g52,g55)
    c: Coincident(g54,g55)
    c: Equal(g53,g55)
    c: Parallel(g55,g53)
    c: Coincident(g54,g57)
    c: Coincident(g56,g57)
    c: Equal(g53,g57)
    c: Parallel(g57,g53)
    c: Coincident(g57,g42)
    c: DistanceY(g34) = -85.2518
FEATURE [PartDesign::Pad] Pad012098  label="half_base004"
  Length = 3
  Length2 = 100
  Profile = -> Sketch261
  Refine = true
  Type = 0
FEATURE [PartDesign::Mirrored] Mirrored002  label="basic_base012"
  BaseFeature = -> Pad012098
  MirrorPlane = -> Sketch261 [V_Axis]
  Originals = -> [Pad012098]
  Refine = true
FEATURE [PartDesign::Body] Body027  label="robot_module_base002"
  Group = -> [Sketch261,Pad012098,Mirrored002]
  Origin = -> Origin047
  Tip = -> Mirrored002
FEATURE [App::Part] Part016  label="base005"
  Group = -> [Body027]
  License = CC BY 3.0
  LicenseURL = http://creativecommons.org/licenses/by/3.0/
  Origin = -> Origin046
  Placement = pos=(0,0,30) rot=(0,0,1;0rad)
FEATURE [Part::Mirroring] Part__Mirroring  label="rounder_q1_servo007 (Mirror #1)"
  Base = (0,0,0)
  Normal = (1,0,0)
  Source = -> Fillet009
FEATURE [Part::Mirroring] Part__Mirroring001  label="Q2-Leg-joint007 (Mirror #2)"
  Base = (0,0,0)
  Normal = (1,0,0)
  Source = -> Body026
FEATURE [Sketcher::SketchObject] Sketch264  label="base_cylinder025"
  MapMode = 5
  Support = -> [XY_Plane049]
  sketch-geometry (2):
    g0: Circle CenterX=0 CenterY=0 CenterZ=0 NormalX=0 NormalY=0 NormalZ=1 AngleXU=0 Radius=3.75
    g1: Circle CenterX=0 CenterY=0 CenterZ=0 NormalX=0 NormalY=0 NormalZ=1 AngleXU=0 Radius=5.75
  constraints (4):
    c: Coincident(g0,g-1)
    c: Radius(g0) = 3.75
    c: Coincident(g1,g-1)
    c: Radius(g1) = 5.75
FEATURE [Part::Feature] Pocket003132  label="Final-1-arm-horn028"
  Placement = pos=(0,0,32) rot=(0.707107,0.707107,0;3.14159rad)
  shape: bbox 8 x 22.5 x 5 mm, 19 faces (baked)
FEATURE [Part::Feature] Fusion007081  label="Servo-sg90-final030"
  Placement = pos=(0,-16.6,0) rot=(0,0,1;0rad)
  shape: bbox 11.8 x 32.4 x 29.9 mm, 77 faces (baked)
FEATURE [PartDesign::Pad] Pad012103  label="low_base010"
  Length = 2.25
  Length2 = 100
  Profile = -> Sketch264
  Refine = true
  Type = 0
FEATURE [Sketcher::SketchObject] Sketch273  label="basic_base013"
  MapMode = 5
  Placement = pos=(0,0,2.25) rot=(0,0,1;0rad)
  Support = -> [Pad012103]
  sketch-geometry (6):
    g0: LineSegment StartX=0 StartY=5.71563 StartZ=0 EndX=-20.5 EndY=5.71563 EndZ=0
    g1: LineSegment StartX=1.86762e-06 StartY=-5.71497 StartZ=0 EndX=-20.5 EndY=-5.71497 EndZ=0
    g2: LineSegment StartX=-20.5 StartY=5.71563 StartZ=0 EndX=-20.5 EndY=-5.71497 EndZ=0
    g3: LineSegment StartX=0 StartY=5.71563 StartZ=0 EndX=5.71497 EndY=5.71563 EndZ=0
    g4: LineSegment StartX=5.71497 StartY=5.71563 StartZ=0 EndX=5.71497 EndY=0 EndZ=0
    g5: ArcOfCircle CenterX=0 CenterY=0 CenterZ=0 NormalX=0 NormalY=0 NormalZ=1 AngleXU=0 Radius=5.71497 StartAngle=4.71239 EndAngle=6.28319
  constraints (14):
    c: PointOnObject(g0,g-2)
    c: Horizontal(g0)
    c: DistanceX(g0,g0) = 20.5
    c: Coincident(g2,g0)
    c: Vertical(g2)
    c: Coincident(g1,g2)
    c: Coincident(g0,g3)
    c: Horizontal(g3)
    c: Coincident(g4,g3)
    c: PointOnObject(g4,g-1)
    c: Vertical(g4)
    c: Coincident(g5,g-1)
    c: Coincident(g5,g1)
    c: Coincident(g5,g4)
FEATURE [PartDesign::Pad] Pad012102  label="q1_basic_base010"
  BaseFeature = -> Pad012103
  Length = 3.5
  Length2 = 100
  Profile = -> Sketch273
  Refine = true
  Type = 0
FEATURE [Sketcher::SketchObject] Sketch278  label="base_cylinder026"
  MapMode = 5
  Placement = pos=(0,6.2,0) rot=(0,0.707107,0.707107;3.14159rad)
  sketch-geometry (2):
    g0: Circle CenterX=24 CenterY=64 CenterZ=0 NormalX=0 NormalY=0 NormalZ=1 AngleXU=0 Radius=3.75
    g1: Circle CenterX=24 CenterY=64 CenterZ=0 NormalX=0 NormalY=0 NormalZ=1 AngleXU=0 Radius=5.75
  constraints (3):
    c: Radius(g0) = 3.75
    c: Radius(g1) = 5.75
    c: Coincident(g1,g0)
FEATURE [Part::Fillet] Fillet010  label="rounder_q1_servo008"
  Edges = 1 edges r=8: [Edge27]
  Placement = pos=(0,0,44) rot=(0,0,1;1.5708rad)
FEATURE [Part::Mirroring] Part__Mirroring002  label="rounder_q1_servo007 (Mirror #1)001"
  Base = (0,0,0)
  Normal = (1,0,0)
  Source = -> Fillet010
FEATURE [Sketcher::SketchObject] Sketch280  label="q1_base_horn010"
  MapMode = 5
  Placement = pos=(0,0,5.75) rot=(0,0,1;0rad)
  Support = -> [Pad012102]
  sketch-geometry (7):
    g0: LineSegment StartX=-1.25 StartY=3.53553 StartZ=0 EndX=-17 EndY=1.74295 EndZ=0
    g1: ArcOfCircle CenterX=-17 CenterY=0 CenterZ=0 NormalX=0 NormalY=0 NormalZ=1 AngleXU=0 Radius=1.74295 StartAngle=1.5708 EndAngle=3.14159
    g2: LineSegment [constr] StartX=-18.743 StartY=0 StartZ=0 EndX=0 EndY=0 EndZ=0
    g3: ArcOfCircle CenterX=0 CenterY=0 CenterZ=0 NormalX=0 NormalY=0 NormalZ=1 AngleXU=0 Radius=3.75 StartAngle=0 EndAngle=1.91063
    g4: LineSegment StartX=-1.25 StartY=-3.53553 StartZ=0 EndX=-17 EndY=-1.74295 EndZ=0
    g5: ArcOfCircle CenterX=-17 CenterY=-1e-12 CenterZ=0 NormalX=0 NormalY=0 NormalZ=1 AngleXU=0 Radius=1.74295 StartAngle=3.14159 EndAngle=4.71239
    g6: ArcOfCircle CenterX=0 CenterY=0 CenterZ=0 NormalX=0 NormalY=0 NormalZ=1 AngleXU=0 Radius=3.75 StartAngle=4.37255 EndAngle=6.28319
  constraints (11):
    c: PointOnObject(g1,g-1)
    c: Coincident(g1,g0)
    c: PointOnObject(g1,g-1)
    c: Coincident(g1,g2)
    c: Coincident(g3,g-1)
    c: Radius(g3) = 3.75
    c: Coincident(g3,g0)
    c: DistanceX(g0,g3) = 5
    c: Coincident(g5,g4)
    c: Radius(g6) = 3.75
    c: Coincident(g6,g4)
FEATURE [PartDesign::Pad] Pad012110  label="q2_base_cylinder015"
  Length = 2.25
  Length2 = 100
  Placement = pos=(0,6.2,0) rot=(0,0.707107,0.707107;3.14159rad)
  Profile = -> Sketch278
  Refine = true
  Type = 0
FEATURE [Sketcher::SketchObject] Sketch275  label="q2_base013"
  ExternalGeometry = -> [Pad012110]
  MapMode = 5
  Placement = pos=(2e-16,8.45,-9e-16) rot=(0,0.707107,0.707107;3.14159rad)
  Support = -> [Pad012110]
  sketch-geometry (6):
    g0: ArcOfCircle CenterX=24 CenterY=64 CenterZ=0 NormalX=0 NormalY=0 NormalZ=1 AngleXU=0 Radius=5.75 StartAngle=2.0944 EndAngle=5.23599
    g1: LineSegment [constr] StartX=12.5 StartY=64 StartZ=0 EndX=37 EndY=64 EndZ=0
    g2: LineSegment [constr] StartX=24 StartY=64 StartZ=0 EndX=21.125 EndY=68.9796 EndZ=0
    g3: LineSegment StartX=21.125 StartY=68.9796 StartZ=0 EndX=39.516 EndY=79.5977 EndZ=0
    g4: LineSegment StartX=39.516 StartY=79.5977 StartZ=0 EndX=45.266 EndY=69.6384 EndZ=0
    g5: LineSegment StartX=45.266 StartY=69.6384 StartZ=0 EndX=26.875 EndY=59.0204 EndZ=0
  constraints (14):
    c: Coincident(g0,g-3)
    c: PointOnObject(g0,g-3)
    c: Angle(g0) = 3.14159
    c: Horizontal(g1)
    c: PointOnObject(g0,g1)
    c: Coincident(g2,g0)
    c: Coincident(g2,g0)
    c: Angle(g1,g2) = 2.0944
    c: Tangent(g0,g3) = 1.5708
    c: Coincident(g3,g4)
    c: Coincident(g4,g5)
    c: Coincident(g5,g0)
    c: Equal(g3,g5)
    c: Parallel(g3,g5)
FEATURE [PartDesign::Pad] Pad012106  label="q2_basic_base008"
  BaseFeature = -> Pad012110
  Length = 3.5
  Length2 = 100
  Placement = pos=(0,6.2,0) rot=(0,0.707107,0.707107;3.14159rad)
  Profile = -> Sketch275
  Refine = true
  Type = 0
FEATURE [Sketcher::SketchObject] Sketch276  label="AUX_q2_base_horn011"
  ExternalGeometry = -> [Pad012106]
  MapMode = 5
  Placement = pos=(-3e-15,11.95,-6e-15) rot=(0.186157,0.694747,0.694747;3.50969rad)
  sketch-geometry (5):
    g0: LineSegment StartX=54.0346 StartY=46.9656 StartZ=0 EndX=69.7804 EndY=45.1656 EndZ=0
    g1: ArcOfCircle CenterX=69.7804 CenterY=43.4256 CenterZ=0 NormalX=0 NormalY=0 NormalZ=1 AngleXU=0 Radius=1.74 StartAngle=0 EndAngle=1.5708
    g2: LineSegment [constr] StartX=71.5204 StartY=43.4256 StartZ=0 EndX=49.0304 EndY=43.4256 EndZ=0
    g3: ArcOfCircle CenterX=52.7846 CenterY=43.4256 CenterZ=0 NormalX=0 NormalY=0 NormalZ=1 AngleXU=0 Radius=3.75421 StartAngle=1.23136 EndAngle=3.14159
    g4: LineSegment [constr] StartX=52.7846 StartY=49.1756 StartZ=0 EndX=52.7846 EndY=37.6756 EndZ=0
  constraints (16):
    c: Coincident(g1,g0)
    c: Coincident(g1,g2)
    c: Coincident(g3,g0)
    c: Radius(g1) = 1.74
    c: PointOnObject(g1,g2)
    c: Coincident(g2,g3)
    c: PointOnObject(g3,g2)
    c: DistanceX(g2,g2) = 22.49
    c: DistanceY(g1,g0) = 1.74
    c: DistanceX(g3,g0) = 1.25
    c: DistanceY(g3,g0) = 3.54
    c: Horizontal(g2)
    c: Coincident(g4,g-3)
    c: Coincident(g4,g-4)
    c: PointOnObject(g3,g4)
    c: Symmetric(g4,g4,g3)
FEATURE [Sketcher::SketchObject] Sketch271  label="horn_shape017"
  ExternalGeometry = -> [Sketch276]
  MapMode = 5
  Placement = pos=(6e-16,11.95,-5.8e-15) rot=(0,0.707107,0.707107;3.14159rad)
  Support = -> [Pad012106]
  sketch-geometry (7):
    g0: LineSegment [constr] StartX=20.7488 StartY=62.1229 StartZ=0 EndX=40.2257 EndY=73.3679 EndZ=0
    g1: ArcOfCircle CenterX=24 CenterY=64 CenterZ=0 NormalX=0 NormalY=0 NormalZ=1 AngleXU=0 Radius=3.75421 StartAngle=1.75495 EndAngle=3.66519
    g2: ArcOfCircle CenterX=38.7188 CenterY=72.4979 CenterZ=0 NormalX=0 NormalY=0 NormalZ=1 AngleXU=0 Radius=1.74 StartAngle=0.523599 EndAngle=2.0944
    g3: LineSegment StartX=23.3125 StartY=67.6907 StartZ=0 EndX=37.8488 EndY=74.0048 EndZ=0
    g4: ArcOfCircle CenterX=24 CenterY=64 CenterZ=0 NormalX=0 NormalY=0 NormalZ=1 AngleXU=0 Radius=3.75421 StartAngle=3.66519 EndAngle=5.57543
    g5: ArcOfCircle CenterX=38.7188 CenterY=72.4979 CenterZ=0 NormalX=0 NormalY=0 NormalZ=1 AngleXU=0 Radius=1.74 StartAngle=5.23599 EndAngle=6.80678
    g6: LineSegment StartX=26.8525 StartY=61.5593 StartZ=0 EndX=39.5888 EndY=70.991 EndZ=0
  constraints (16):
    c: Coincident(g0,g-5)
    c: Coincident(g0,g-4)
    c: Coincident(g1,g-5)
    c: Coincident(g1,g-5)
    c: Coincident(g1,g0)
    c: Coincident(g2,g-4)
    c: Coincident(g2,g0)
    c: Coincident(g2,g-4)
    c: Coincident(g3,g1)
    c: Coincident(g3,g2)
    c: Coincident(g6,g4)
    c: Coincident(g6,g5)
    c: Coincident(g0,g4)
    c: Coincident(g1,g4)
    c: Coincident(g2,g5)
    c: Coincident(g0,g5)
FEATURE [PartDesign::Pocket] Pocket003133  label="horn_shape016"
  BaseFeature = -> Pad012106
  Length = 2.65
  Length2 = 100
  Placement = pos=(0,6.2,0) rot=(0,0.707107,0.707107;3.14159rad)
  Profile = -> Sketch271
  Refine = true
  Type = 0
FEATURE [Sketcher::SketchObject] Sketch285  label="horn_holes019"
  ExternalGeometry = -> [Pocket003133]
  MapMode = 5
  Placement = pos=(2e-16,9.3,-5.3e-15) rot=(0,0.707107,0.707107;3.14159rad)
  Support = -> [Pocket003133]
  sketch-geometry (16):
    g0: Circle CenterX=24 CenterY=64 CenterZ=0 NormalX=0 NormalY=0 NormalZ=1 AngleXU=0 Radius=3.75
    g1: Circle CenterX=-14.6952 CenterY=0 CenterZ=0 NormalX=0 NormalY=0 NormalZ=1 AngleXU=0 Radius=0.75
    g2: Circle CenterX=-12.6952 CenterY=0 CenterZ=0 NormalX=0 NormalY=0 NormalZ=1 AngleXU=0 Radius=0.75
    g3: LineSegment [constr] StartX=-14.6952 StartY=0 StartZ=0 EndX=-12.6952 EndY=0 EndZ=0
    g4: Circle CenterX=-10.6952 CenterY=0 CenterZ=0 NormalX=0 NormalY=0 NormalZ=1 AngleXU=0 Radius=0.75
    g5: LineSegment [constr] StartX=-12.6952 StartY=0 StartZ=0 EndX=-10.6952 EndY=0 EndZ=0
    g6: Circle CenterX=-8.69518 CenterY=0 CenterZ=0 NormalX=0 NormalY=0 NormalZ=1 AngleXU=0 Radius=0.75
    g7: LineSegment [constr] StartX=-10.6952 StartY=0 StartZ=0 EndX=-8.69518 EndY=0 EndZ=0
    g8: Circle CenterX=-6.69518 CenterY=0 CenterZ=0 NormalX=0 NormalY=0 NormalZ=1 AngleXU=0 Radius=0.75
    g9: LineSegment [constr] StartX=-8.69518 StartY=0 StartZ=0 EndX=-6.69518 EndY=0 EndZ=0
    g10: LineSegment [constr] StartX=24 StartY=64 StartZ=0 EndX=43.3449 EndY=75.1688 EndZ=0
    g11: Circle CenterX=29.6292 CenterY=67.25 CenterZ=0 NormalX=0 NormalY=0 NormalZ=1 AngleXU=0 Radius=0.75
    g12: Circle CenterX=31.3612 CenterY=68.25 CenterZ=0 NormalX=0 NormalY=0 NormalZ=1 AngleXU=0 Radius=0.75
    g13: Circle CenterX=33.0933 CenterY=69.25 CenterZ=0 NormalX=0 NormalY=0 NormalZ=1 AngleXU=0 Radius=0.75
    g14: Circle CenterX=34.8253 CenterY=70.25 CenterZ=0 NormalX=0 NormalY=0 NormalZ=1 AngleXU=0 Radius=0.75
    g15: Circle CenterX=36.5574 CenterY=71.25 CenterZ=0 NormalX=0 NormalY=0 NormalZ=1 AngleXU=0 Radius=0.75
  constraints (41):
    c: Radius(g1) = 0.75
    c: Radius(g0) = 3.75
    c: Radius(g2) = 0.75
    c: Coincident(g1,g3)
    c: Coincident(g2,g3)
    c: Distance(g3) = 2
    c: Angle(g3) = 0
    c: Radius(g4) = 0.75
    c: Coincident(g2,g5)
    c: Coincident(g4,g5)
    c: Equal(g3,g5)
    c: Radius(g6) = 0.75
    c: Coincident(g4,g7)
    c: Coincident(g6,g7)
    c: Equal(g3,g7)
    c: Radius(g8) = 0.75
    c: Coincident(g6,g9)
    c: Coincident(g8,g9)
    c: Equal(g3,g9)
    c: Parallel(g9,g3)
    c: Parallel(g9,g7)
    c: Parallel(g7,g5)
    c: Coincident(g10,g0)
    c: Angle(g10) = 0.523599
    c: Radius(g11) = 0.75
    c: Distance(g0,g11) = 6.5
    c: PointOnObject(g11,g10)
    c: Equal(g11,g12) = 0.75
    c: PointOnObject(g12,g10)
    c: DistanceX(g0) = 24
    c: DistanceY(g0) = 64
    c: Distance(g11,g12) = 2
    c: Equal(g11,g13) = 0.75
    c: PointOnObject(g13,g10)
    c: Equal(g11,g14) = 0.75
    c: PointOnObject(g14,g10)
    c: Equal(g11,g15) = 0.75
    c: PointOnObject(g15,g10)
    c: Distance(g12,g13) = 2
    c: Distance(g13,g14) = 2
    c: Distance(g14,g15) = 2
FEATURE [Part::Feature] Fusion007083  label="Servo-sg90-final031"
  Placement = pos=(0,-16.6,0) rot=(0,0,1;0rad)
  shape: bbox 11.8 x 32.4 x 29.9 mm, 77 faces (baked)
FEATURE [PartDesign::Pocket] Pocket003136  label="q1_basic_horn010"
  BaseFeature = -> Pad012102
  Length = 2.65
  Length2 = 100
  Profile = -> Sketch280
  Refine = true
  Type = 0
FEATURE [Sketcher::SketchObject] Sketch267  label="horn_holes018"
  MapMode = 5
  Placement = pos=(0,0,3.1) rot=(0,0,1;0rad)
  Support = -> [Pocket003136]
  sketch-geometry (10):
    g0: Circle CenterX=0 CenterY=0 CenterZ=0 NormalX=0 NormalY=0 NormalZ=1 AngleXU=0 Radius=3.75
    g1: Circle CenterX=-14.5 CenterY=0 CenterZ=0 NormalX=0 NormalY=0 NormalZ=1 AngleXU=0 Radius=0.75
    g2: Circle CenterX=-12.5 CenterY=0 CenterZ=0 NormalX=0 NormalY=0 NormalZ=1 AngleXU=0 Radius=0.75
    g3: LineSegment [constr] StartX=-14.5 StartY=0 StartZ=0 EndX=-12.5 EndY=0 EndZ=0
    g4: Circle CenterX=-10.5 CenterY=0 CenterZ=0 NormalX=0 NormalY=0 NormalZ=1 AngleXU=0 Radius=0.75
    g5: LineSegment [constr] StartX=-12.5 StartY=0 StartZ=0 EndX=-10.5 EndY=0 EndZ=0
    g6: Circle CenterX=-8.5 CenterY=0 CenterZ=0 NormalX=0 NormalY=0 NormalZ=1 AngleXU=0 Radius=0.75
    g7: LineSegment [constr] StartX=-10.5 StartY=0 StartZ=0 EndX=-8.5 EndY=0 EndZ=0
    g8: Circle CenterX=-6.5 CenterY=0 CenterZ=0 NormalX=0 NormalY=0 NormalZ=1 AngleXU=0 Radius=0.75
    g9: LineSegment [constr] StartX=-8.5 StartY=0 StartZ=0 EndX=-6.5 EndY=0 EndZ=0
  constraints (25):
    c: Coincident(g0,g-1)
    c: Radius(g1) = 0.75
    c: Radius(g0) = 3.75
    c: Radius(g2) = 0.75
    c: Coincident(g1,g3)
    c: Coincident(g2,g3)
    c: Distance(g3) = 2
    c: Angle(g3) = 0
    c: Radius(g4) = 0.75
    c: Coincident(g2,g5)
    c: Coincident(g4,g5)
    c: Equal(g3,g5)
    c: Parallel(g5,g3)
    c: Radius(g6) = 0.75
    c: Coincident(g4,g7)
    c: Coincident(g6,g7)
    c: Equal(g3,g7)
    c: Parallel(g7,g3)
    c: Radius(g8) = 0.75
    c: Coincident(g6,g9)
    c: Coincident(g8,g9)
    c: Equal(g3,g9)
    c: Parallel(g9,g3)
    c: PointOnObject(g2,g-1)
    c: DistanceX(g8,g-1) = 6.5
FEATURE [PartDesign::Pocket] Pocket003134  label="q1_basic_horn_shape010"
  BaseFeature = -> Pocket003136
  Length = 5
  Length2 = 100
  Profile = -> Sketch267
  Refine = true
  Type = 0
FEATURE [Sketcher::SketchObject] Sketch269  label="q2-base008"
  ExternalGeometry = -> [Pocket003134]
  MapMode = 5
  Placement = pos=(-20.5,0,0) rot=(0.57735,-0.57735,-0.57735;2.0944rad)
  Support = -> [Pocket003134]
  sketch-geometry (6):
    g0: LineSegment StartX=-5.71563 StartY=2.25 StartZ=0 EndX=-11.6041 EndY=2.25 EndZ=0
    g1: LineSegment StartX=-11.6041 StartY=2.25 StartZ=0 EndX=-38.6752 EndY=17.8795 EndZ=0
    g2: LineSegment StartX=-11.6626 StartY=5.74787 StartZ=0 EndX=-37.1752 EndY=20.4776 EndZ=0
    g3: LineSegment StartX=-37.1752 StartY=20.4776 StartZ=0 EndX=-38.6752 EndY=17.8795 EndZ=0
    g4: LineSegment StartX=-5.71563 StartY=5.74787 StartZ=0 EndX=-5.71563 EndY=2.25 EndZ=0
    g5: LineSegment StartX=-11.6626 StartY=5.74787 StartZ=0 EndX=-5.71563 EndY=5.74787 EndZ=0
  constraints (13):
    c: Coincident(g3,g2)
    c: Coincident(g3,g1)
    c: Perpendicular(g3,g1)
    c: Coincident(g0,g-3)
    c: Parallel(g1,g2)
    c: Coincident(g4,g0)
    c: Perpendicular(g4,g0)
    c: Distance(g1,g2) = 3
    c: Angle(g0,g1) = 2.61799
    c: Coincident(g0,g1)
    c: Coincident(g2,g5)
    c: Coincident(g5,g4)
    c: Horizontal(g5)
FEATURE [PartDesign::Pad] Pad012104  label="q2-bed-base008"
  BaseFeature = -> Pocket003134
  Length = 26.215
  Length2 = 100
  Profile = -> Sketch269
  Refine = true
  Reversed = true
  Type = 0
FEATURE [Sketcher::SketchObject] Sketch286  label="q2-corner-hole017"
  MapMode = 5
  Placement = pos=(0,0,5.74787) rot=(0,0,1;0rad)
  Support = -> [Pad012104]
  sketch-geometry (4):
    g0: LineSegment StartX=-1.62396 StartY=12 StartZ=0 EndX=-5 EndY=12 EndZ=0
    g1: LineSegment StartX=-5 StartY=12 StartZ=0 EndX=-5 EndY=6.68085 EndZ=0
    g2: LineSegment StartX=-5 StartY=6.68085 StartZ=0 EndX=-1.62396 EndY=6.68085 EndZ=0
    g3: LineSegment StartX=-1.62396 StartY=6.68085 StartZ=0 EndX=-1.62396 EndY=12 EndZ=0
  constraints (8):
    c: Coincident(g0,g1)
    c: Coincident(g1,g2)
    c: Coincident(g2,g3)
    c: Coincident(g3,g0)
    c: Horizontal(g0)
    c: Horizontal(g2)
    c: Vertical(g1)
    c: Vertical(g3)
FEATURE [PartDesign::Pocket] Pocket003135  label="q2-corner-hole016"
  BaseFeature = -> Pad012104
  Length = 2
  Length2 = 100
  Profile = -> Sketch286
  Refine = true
  Type = 0
FEATURE [Part::MultiFuse] Fusion007084  label="q2-aux-servo010"
  Placement = pos=(23.9256,-20.5,63.7846) rot=(0.377964,0.654656,0.654652;3.86432rad)
  Refine = true
  Shapes = -> [Fusion007083,Pocket003132]
FEATURE [Part::Feature] Pocket003137  label="Final-1-arm-horn029"
  Placement = pos=(0,0,32) rot=(0.707107,-0.707107,0;3.14159rad)
  shape: bbox 8 x 22.5 x 5 mm, 19 faces (baked)
FEATURE [Part::MultiFuse] Fusion007082  label="q1-aux-servo010"
  Placement = pos=(0,0,17.25) rot=(0,0,1;0rad)
  Refine = true
  Shapes = -> [Pocket003137,Fusion007081]
FEATURE [PartDesign::Pocket] Pocket003138  label="basic_horn_union008"
  BaseFeature = -> Pocket003133
  Length = 5
  Length2 = 100
  Placement = pos=(0,6.2,0) rot=(0,0.707107,0.707107;3.14159rad)
  Profile = -> Sketch285
  Refine = true
  Type = 0
FEATURE [Sketcher::SketchObject] Sketch283  label="q2_bridge017"
  ExternalGeometry = -> [Pocket003138]
  MapMode = 5
  Placement = pos=(2e-16,8.45,-2.3e-15) rot=(0,-0.707107,0.707107;3.14159rad)
  Support = -> [Pocket003138]
  sketch-geometry (4):
    g0: LineSegment StartX=39.516 StartY=-79.5977 StartZ=0 EndX=45.266 EndY=-69.6384 EndZ=0
    g1: LineSegment StartX=45.266 StartY=-69.6384 StartZ=0 EndX=40.9358 EndY=-67.1384 EndZ=0
    g2: LineSegment StartX=39.516 StartY=-79.5977 StartZ=0 EndX=35.1858 EndY=-77.0977 EndZ=0
    g3: ArcOfCircle CenterX=24.5001 CenterY=-64.2888 CenterZ=0 NormalX=0 NormalY=0 NormalZ=1 AngleXU=0 Radius=16.6809 StartAngle=5.40766 EndAngle=6.11151
  constraints (10):
    c: Coincident(g-5,g0)
    c: Coincident(g0,g-5)
    c: Coincident(g0,g1)
    c: PointOnObject(g1,g-3)
    c: Coincident(g0,g2)
    c: PointOnObject(g2,g-4)
    c: Distance(g2) = 5
    c: Equal(g2,g1)
    c: Coincident(g3,g1)
    c: Coincident(g3,g2)
FEATURE [PartDesign::Pad] Pad012101  label="q2_bridge016"
  BaseFeature = -> Pocket003138
  Length = 31
  Length2 = 100
  Placement = pos=(0,6.2,0) rot=(0,0.707107,0.707107;3.14159rad)
  Profile = -> Sketch283
  Refine = true
  Type = 0
FEATURE [Sketcher::SketchObject] Sketch270  label="q2_back_union008"
  ExternalGeometry = -> [Pad012110,Sketch275]
  MapMode = 5
  Placement = pos=(-2.3e-15,-22.55,3.83e-14) rot=(0,-0.707107,0.707107;3.14159rad)
  Support = -> [Pad012101]
  expr: Constraints[2] = Sketch067.Constraints[2]
  sketch-geometry (7):
    g0: ArcOfCircle CenterX=24 CenterY=-64 CenterZ=0 NormalX=0 NormalY=0 NormalZ=1 AngleXU=0 Radius=5.75 StartAngle=1.0472 EndAngle=4.18879
    g1: LineSegment [constr] StartX=12.5 StartY=-64 StartZ=0 EndX=37 EndY=-64 EndZ=0
    g2: LineSegment [constr] StartX=24 StartY=-64 StartZ=0 EndX=26.875 EndY=-59.0204 EndZ=0
    g3: LineSegment StartX=45.266 StartY=-69.6384 StartZ=0 EndX=26.875 EndY=-59.0204 EndZ=0
    g4: LineSegment StartX=45.266 StartY=-69.6384 StartZ=0 EndX=39.516 EndY=-79.5977 EndZ=0
    g5: LineSegment StartX=39.516 StartY=-79.5977 StartZ=0 EndX=21.125 EndY=-68.9796 EndZ=0
    g6: Circle CenterX=24 CenterY=-64 CenterZ=0 NormalX=0 NormalY=0 NormalZ=1 AngleXU=0 Radius=2
  constraints (16):
    c: Coincident(g0,g-3)
    c: PointOnObject(g0,g-3)
    c: Angle(g0) = 3.14159
    c: Horizontal(g1)
    c: PointOnObject(g0,g1)
    c: Coincident(g2,g0)
    c: Coincident(g2,g0)
    c: Parallel(g2,g-4)
    c: Coincident(g-4,g3)
    c: Coincident(g3,g0)
    c: Coincident(g3,g4)
    c: Coincident(g4,g-4)
    c: Coincident(g4,g5)
    c: Coincident(g5,g0)
    c: Coincident(g6,g0)
    c: Radius(g6) = 2
FEATURE [PartDesign::Pad] Pad012109  label="q2_joint008"
  BaseFeature = -> Pad012101
  Length = 3.5
  Length2 = 100
  Placement = pos=(0,6.2,0) rot=(0,0.707107,0.707107;3.14159rad)
  Profile = -> Sketch270
  Refine = true
  Type = 0
FEATURE [Sketcher::SketchObject] Sketch266  label="q2-leg_union_section008"
  ExternalGeometry = -> [Pad012109]
  MapMode = 5
  Placement = pos=(-64.1038,6.2,37.0103) rot=(0,-1,0;1.0472rad)
  Support = -> [Pad012109]
  sketch-geometry (4):
    g0: LineSegment StartX=49.1756 StartY=5.75 StartZ=0 EndX=49.1756 EndY=-32.25 EndZ=0
    g1: LineSegment StartX=49.1756 StartY=-32.25 StartZ=0 EndX=37.6756 EndY=-32.25 EndZ=0
    g2: LineSegment StartX=37.6756 StartY=-32.25 StartZ=0 EndX=37.6756 EndY=5.75 EndZ=0
    g3: LineSegment StartX=37.6756 StartY=5.75 StartZ=0 EndX=49.1756 EndY=5.75 EndZ=0
  constraints (8):
    c: Coincident(g-6,g0)
    c: Coincident(g0,g-6)
    c: Coincident(g0,g1)
    c: Coincident(g1,g-5)
    c: Coincident(g-5,g2)
    c: Coincident(g2,g-4)
    c: Coincident(g2,g3)
    c: Coincident(g3,g0)
FEATURE [Sketcher::SketchObject] Sketch287  label="trajectory008"
  ExternalGeometry = -> [Pad012109]
  MapMode = 5
  Placement = pos=(6e-16,11.95,-5.8e-15) rot=(0,0.707107,0.707107;3.14159rad)
  Support = -> [Pad012109]
  sketch-geometry (8):
    g0: GeomPoint X=42.3808 Y=74.6356 Z=0
    g1-g4: Circle [constr] x4 (B-spline internal-alignment scaffolding for g5; pole/knot coordinates omitted)
    g5: BSplineCurve PolesCount=4 KnotsCount=2 Degree=3 IsPeriodic=0
    g6: GeomPoint [constr] X=42.3808 Y=74.6356 Z=0
    g7: GeomPoint [constr] X=64.6677 Y=0 Z=0
  constraints (10):
    c: PointOnObject(g0,g-3)
    c: Coincident(g1,g0)
    c: Radius(g1) = 4
    c: Equal(g1,g2)
    c: Equal(g1,g3)
    c: Equal(g1,g4)
    c: PointOnObject(g4,g-1)
    c: InternalAlignment(g1-g4 -> g5) x4
    c: InternalAlignment(g6,g5)
    c: InternalAlignment(g7,g5)
FEATURE [Sketcher::SketchObject] Sketch277  label="q2-bone-touch_section008"
  ExternalGeometry = -> [Sketch287,Pad012109]
  MapMode = 5
  Support = -> [XY_Plane048]
  sketch-geometry (7):
    g0: LineSegment StartX=-66.1677 StartY=-4.55 StartZ=0 EndX=-63.1677 EndY=-4.55 EndZ=0
    g1: LineSegment StartX=-63.1677 StartY=-4.55 StartZ=0 EndX=-63.1677 EndY=-9.55 EndZ=0
    g2: LineSegment StartX=-63.1677 StartY=-9.55 StartZ=0 EndX=-66.1677 EndY=-9.55 EndZ=0
    g3: LineSegment StartX=-66.1677 StartY=-9.55 StartZ=0 EndX=-66.1677 EndY=-4.55 EndZ=0
    g4: GeomPoint X=-45.266 Y=-7.05 Z=0
    g5: GeomPoint X=-63.1677 Y=-7.05 Z=0
    g6: GeomPoint X=-64.6677 Y=-4.55 Z=0
  constraints (18):
    c: Coincident(g0,g1)
    c: Coincident(g1,g2)
    c: Coincident(g2,g3)
    c: Coincident(g3,g0)
    c: Horizontal(g0)
    c: Horizontal(g2)
    c: Vertical(g1)
    c: Vertical(g3)
    c: PointOnObject(g4,g-4)
    c: Symmetric(g-4,g-4,g4)
    c: PointOnObject(g5,g1)
    c: Symmetric(g0,g1,g5)
    c: Horizontal(g5,g4)
    c: PointOnObject(g6,g0)
    c: Symmetric(g0,g0,g6)
    c: Vertical(g6,g-3)
    c: DistanceX(g2,g2) = 3
    c: DistanceY(g3,g3) = 5
FEATURE [PartDesign::AdditivePipe] AdditivePipe008
  AuxilleryCurvelinear = true
  AuxillerySpineTangent = false
  BaseFeature = -> Pad012109
  Binormal = (0,0,0)
  Mode = 0
  Placement = pos=(0,6.2,0) rot=(0,0.707107,0.707107;3.14159rad)
  Profile = -> Sketch266
  Refine = true
  Sections = -> [Sketch277]
  Spine = -> Sketch287
  SpineTangent = false
  Transformation = 1
  Transition = 0
FEATURE [PartDesign::Body] Body029  label="Q2-Leg-joint008"
  Group = -> [Sketch278,Pad012110,Sketch275,Pad012106,Sketch276,Sketch271,Pocket003133,Sketch285,Pocket003138,Sketch283,Pad012101,Sketch270,Pad012109,Sketch287,Sketch266,Sketch277,AdditivePipe008]
  Origin = -> Origin050
  Tip = -> AdditivePipe008
FEATURE [Part::Mirroring] Part__Mirroring003  label="Q2-Leg-joint007 (Mirror #2)001"
  Base = (0,0,0)
  Normal = (1,0,0)
  Source = -> Body029
FEATURE [Sketcher::SketchObject] Sketch290  label="base_cylinder028"
  MapMode = 5
  Support = -> [XY_Plane052]
  sketch-geometry (2):
    g0: Circle CenterX=0 CenterY=0 CenterZ=0 NormalX=0 NormalY=0 NormalZ=1 AngleXU=0 Radius=3.75
    g1: Circle CenterX=0 CenterY=0 CenterZ=0 NormalX=0 NormalY=0 NormalZ=1 AngleXU=0 Radius=5.75
  constraints (4):
    c: Coincident(g0,g-1)
    c: Radius(g0) = 3.75
    c: Coincident(g1,g-1)
    c: Radius(g1) = 5.75
FEATURE [Part::Feature] Pocket003142  label="Final-1-arm-horn030"
  Placement = pos=(0,0,32) rot=(0.707107,0.707107,0;3.14159rad)
  shape: bbox 8 x 22.5 x 5 mm, 19 faces (baked)
FEATURE [Part::Feature] Fusion007085  label="Servo-sg90-final032"
  Placement = pos=(0,-16.6,0) rot=(0,0,1;0rad)
  shape: bbox 11.8 x 32.4 x 29.9 mm, 77 faces (baked)
FEATURE [PartDesign::Pad] Pad012115  label="low_base011"
  Length = 2.25
  Length2 = 100
  Profile = -> Sketch290
  Refine = true
  Type = 0
FEATURE [Sketcher::SketchObject] Sketch299  label="basic_base014"
  MapMode = 5
  Placement = pos=(0,0,2.25) rot=(0,0,1;0rad)
  Support = -> [Pad012115]
  sketch-geometry (6):
    g0: LineSegment StartX=0 StartY=5.71563 StartZ=0 EndX=-20.5 EndY=5.71563 EndZ=0
    g1: LineSegment StartX=1.86762e-06 StartY=-5.71497 StartZ=0 EndX=-20.5 EndY=-5.71497 EndZ=0
    g2: LineSegment StartX=-20.5 StartY=5.71563 StartZ=0 EndX=-20.5 EndY=-5.71497 EndZ=0
    g3: LineSegment StartX=0 StartY=5.71563 StartZ=0 EndX=5.71497 EndY=5.71563 EndZ=0
    g4: LineSegment StartX=5.71497 StartY=5.71563 StartZ=0 EndX=5.71497 EndY=0 EndZ=0
    g5: ArcOfCircle CenterX=0 CenterY=0 CenterZ=0 NormalX=0 NormalY=0 NormalZ=1 AngleXU=0 Radius=5.71497 StartAngle=4.71239 EndAngle=6.28319
  constraints (14):
    c: PointOnObject(g0,g-2)
    c: Horizontal(g0)
    c: DistanceX(g0,g0) = 20.5
    c: Coincident(g2,g0)
    c: Vertical(g2)
    c: Coincident(g1,g2)
    c: Coincident(g0,g3)
    c: Horizontal(g3)
    c: Coincident(g4,g3)
    c: PointOnObject(g4,g-1)
    c: Vertical(g4)
    c: Coincident(g5,g-1)
    c: Coincident(g5,g1)
    c: Coincident(g5,g4)
FEATURE [PartDesign::Pad] Pad012114  label="q1_basic_base011"
  BaseFeature = -> Pad012115
  Length = 3.5
  Length2 = 100
  Profile = -> Sketch299
  Refine = true
  Type = 0
FEATURE [Sketcher::SketchObject] Sketch304  label="base_cylinder029"
  MapMode = 5
  Placement = pos=(0,6.2,0) rot=(0,0.707107,0.707107;3.14159rad)
  sketch-geometry (2):
    g0: Circle CenterX=24 CenterY=64 CenterZ=0 NormalX=0 NormalY=0 NormalZ=1 AngleXU=0 Radius=3.75
    g1: Circle CenterX=24 CenterY=64 CenterZ=0 NormalX=0 NormalY=0 NormalZ=1 AngleXU=0 Radius=5.75
  constraints (3):
    c: Radius(g0) = 3.75
    c: Radius(g1) = 5.75
    c: Coincident(g1,g0)
FEATURE [Part::Fillet] Fillet011  label="rounder_q1_servo009"
  Edges = 1 edges r=8: [Edge27]
  Placement = pos=(0,0,44) rot=(0,0,1;1.5708rad)
FEATURE [Part::Mirroring] Part__Mirroring004  label="rounder_q1_servo007 (Mirror #1)002"
  Base = (0,0,0)
  Normal = (1,0,0)
  Source = -> Fillet011
FEATURE [Sketcher::SketchObject] Sketch306  label="q1_base_horn011"
  MapMode = 5
  Placement = pos=(0,0,5.75) rot=(0,0,1;0rad)
  Support = -> [Pad012114]
  sketch-geometry (7):
    g0: LineSegment StartX=-1.25 StartY=3.53553 StartZ=0 EndX=-17 EndY=1.74295 EndZ=0
    g1: ArcOfCircle CenterX=-17 CenterY=0 CenterZ=0 NormalX=0 NormalY=0 NormalZ=1 AngleXU=0 Radius=1.74295 StartAngle=1.5708 EndAngle=3.14159
    g2: LineSegment [constr] StartX=-18.743 StartY=0 StartZ=0 EndX=0 EndY=0 EndZ=0
    g3: ArcOfCircle CenterX=0 CenterY=0 CenterZ=0 NormalX=0 NormalY=0 NormalZ=1 AngleXU=0 Radius=3.75 StartAngle=0 EndAngle=1.91063
    g4: LineSegment StartX=-1.25 StartY=-3.53553 StartZ=0 EndX=-17 EndY=-1.74295 EndZ=0
    g5: ArcOfCircle CenterX=-17 CenterY=-1e-12 CenterZ=0 NormalX=0 NormalY=0 NormalZ=1 AngleXU=0 Radius=1.74295 StartAngle=3.14159 EndAngle=4.71239
    g6: ArcOfCircle CenterX=0 CenterY=0 CenterZ=0 NormalX=0 NormalY=0 NormalZ=1 AngleXU=0 Radius=3.75 StartAngle=4.37255 EndAngle=6.28319
  constraints (11):
    c: PointOnObject(g1,g-1)
    c: Coincident(g1,g0)
    c: PointOnObject(g1,g-1)
    c: Coincident(g1,g2)
    c: Coincident(g3,g-1)
    c: Radius(g3) = 3.75
    c: Coincident(g3,g0)
    c: DistanceX(g0,g3) = 5
    c: Coincident(g5,g4)
    c: Radius(g6) = 3.75
    c: Coincident(g6,g4)
FEATURE [PartDesign::Pad] Pad012122  label="q2_base_cylinder017"
  Length = 2.25
  Length2 = 100
  Placement = pos=(0,6.2,0) rot=(0,0.707107,0.707107;3.14159rad)
  Profile = -> Sketch304
  Refine = true
  Type = 0
FEATURE [Sketcher::SketchObject] Sketch301  label="q2_base015"
  ExternalGeometry = -> [Pad012122]
  MapMode = 5
  Placement = pos=(2e-16,8.45,-9e-16) rot=(0,0.707107,0.707107;3.14159rad)
  Support = -> [Pad012122]
  sketch-geometry (6):
    g0: ArcOfCircle CenterX=24 CenterY=64 CenterZ=0 NormalX=0 NormalY=0 NormalZ=1 AngleXU=0 Radius=5.75 StartAngle=2.0944 EndAngle=5.23599
    g1: LineSegment [constr] StartX=12.5 StartY=64 StartZ=0 EndX=37 EndY=64 EndZ=0
    g2: LineSegment [constr] StartX=24 StartY=64 StartZ=0 EndX=21.125 EndY=68.9796 EndZ=0
    g3: LineSegment StartX=21.125 StartY=68.9796 StartZ=0 EndX=39.516 EndY=79.5977 EndZ=0
    g4: LineSegment StartX=39.516 StartY=79.5977 StartZ=0 EndX=45.266 EndY=69.6384 EndZ=0
    g5: LineSegment StartX=45.266 StartY=69.6384 StartZ=0 EndX=26.875 EndY=59.0204 EndZ=0
  constraints (14):
    c: Coincident(g0,g-3)
    c: PointOnObject(g0,g-3)
    c: Angle(g0) = 3.14159
    c: Horizontal(g1)
    c: PointOnObject(g0,g1)
    c: Coincident(g2,g0)
    c: Coincident(g2,g0)
    c: Angle(g1,g2) = 2.0944
    c: Tangent(g0,g3) = 1.5708
    c: Coincident(g3,g4)
    c: Coincident(g4,g5)
    c: Coincident(g5,g0)
    c: Equal(g3,g5)
    c: Parallel(g3,g5)
FEATURE [PartDesign::Pad] Pad012118  label="q2_basic_base009"
  BaseFeature = -> Pad012122
  Length = 3.5
  Length2 = 100
  Placement = pos=(0,6.2,0) rot=(0,0.707107,0.707107;3.14159rad)
  Profile = -> Sketch301
  Refine = true
  Type = 0
FEATURE [Sketcher::SketchObject] Sketch302  label="AUX_q2_base_horn012"
  ExternalGeometry = -> [Pad012118]
  MapMode = 5
  Placement = pos=(-3e-15,11.95,-6e-15) rot=(0.186157,0.694747,0.694747;3.50969rad)
  sketch-geometry (5):
    g0: LineSegment StartX=54.0346 StartY=46.9656 StartZ=0 EndX=69.7804 EndY=45.1656 EndZ=0
    g1: ArcOfCircle CenterX=69.7804 CenterY=43.4256 CenterZ=0 NormalX=0 NormalY=0 NormalZ=1 AngleXU=0 Radius=1.74 StartAngle=0 EndAngle=1.5708
    g2: LineSegment [constr] StartX=71.5204 StartY=43.4256 StartZ=0 EndX=49.0304 EndY=43.4256 EndZ=0
    g3: ArcOfCircle CenterX=52.7846 CenterY=43.4256 CenterZ=0 NormalX=0 NormalY=0 NormalZ=1 AngleXU=0 Radius=3.75421 StartAngle=1.23136 EndAngle=3.14159
    g4: LineSegment [constr] StartX=52.7846 StartY=49.1756 StartZ=0 EndX=52.7846 EndY=37.6756 EndZ=0
  constraints (16):
    c: Coincident(g1,g0)
    c: Coincident(g1,g2)
    c: Coincident(g3,g0)
    c: Radius(g1) = 1.74
    c: PointOnObject(g1,g2)
    c: Coincident(g2,g3)
    c: PointOnObject(g3,g2)
    c: DistanceX(g2,g2) = 22.49
    c: DistanceY(g1,g0) = 1.74
    c: DistanceX(g3,g0) = 1.25
    c: DistanceY(g3,g0) = 3.54
    c: Horizontal(g2)
    c: Coincident(g4,g-3)
    c: Coincident(g4,g-4)
    c: PointOnObject(g3,g4)
    c: Symmetric(g4,g4,g3)
FEATURE [Sketcher::SketchObject] Sketch297  label="horn_shape019"
  ExternalGeometry = -> [Sketch302]
  MapMode = 5
  Placement = pos=(6e-16,11.95,-5.8e-15) rot=(0,0.707107,0.707107;3.14159rad)
  Support = -> [Pad012118]
  sketch-geometry (7):
    g0: LineSegment [constr] StartX=20.7488 StartY=62.1229 StartZ=0 EndX=40.2257 EndY=73.3679 EndZ=0
    g1: ArcOfCircle CenterX=24 CenterY=64 CenterZ=0 NormalX=0 NormalY=0 NormalZ=1 AngleXU=0 Radius=3.75421 StartAngle=1.75495 EndAngle=3.66519
    g2: ArcOfCircle CenterX=38.7188 CenterY=72.4979 CenterZ=0 NormalX=0 NormalY=0 NormalZ=1 AngleXU=0 Radius=1.74 StartAngle=0.523599 EndAngle=2.0944
    g3: LineSegment StartX=23.3125 StartY=67.6907 StartZ=0 EndX=37.8488 EndY=74.0048 EndZ=0
    g4: ArcOfCircle CenterX=24 CenterY=64 CenterZ=0 NormalX=0 NormalY=0 NormalZ=1 AngleXU=0 Radius=3.75421 StartAngle=3.66519 EndAngle=5.57543
    g5: ArcOfCircle CenterX=38.7188 CenterY=72.4979 CenterZ=0 NormalX=0 NormalY=0 NormalZ=1 AngleXU=0 Radius=1.74 StartAngle=5.23599 EndAngle=6.80678
    g6: LineSegment StartX=26.8525 StartY=61.5593 StartZ=0 EndX=39.5888 EndY=70.991 EndZ=0
  constraints (16):
    c: Coincident(g0,g-5)
    c: Coincident(g0,g-4)
    c: Coincident(g1,g-5)
    c: Coincident(g1,g-5)
    c: Coincident(g1,g0)
    c: Coincident(g2,g-4)
    c: Coincident(g2,g0)
    c: Coincident(g2,g-4)
    c: Coincident(g3,g1)
    c: Coincident(g3,g2)
    c: Coincident(g6,g4)
    c: Coincident(g6,g5)
    c: Coincident(g0,g4)
    c: Coincident(g1,g4)
    c: Coincident(g2,g5)
    c: Coincident(g0,g5)
FEATURE [PartDesign::Pocket] Pocket003143  label="horn_shape018"
  BaseFeature = -> Pad012118
  Length = 2.65
  Length2 = 100
  Placement = pos=(0,6.2,0) rot=(0,0.707107,0.707107;3.14159rad)
  Profile = -> Sketch297
  Refine = true
  Type = 0
FEATURE [Sketcher::SketchObject] Sketch311  label="horn_holes021"
  ExternalGeometry = -> [Pocket003143]
  MapMode = 5
  Placement = pos=(2e-16,9.3,-5.3e-15) rot=(0,0.707107,0.707107;3.14159rad)
  Support = -> [Pocket003143]
  sketch-geometry (16):
    g0: Circle CenterX=24 CenterY=64 CenterZ=0 NormalX=0 NormalY=0 NormalZ=1 AngleXU=0 Radius=3.75
    g1: Circle CenterX=-14.6952 CenterY=0 CenterZ=0 NormalX=0 NormalY=0 NormalZ=1 AngleXU=0 Radius=0.75
    g2: Circle CenterX=-12.6952 CenterY=0 CenterZ=0 NormalX=0 NormalY=0 NormalZ=1 AngleXU=0 Radius=0.75
    g3: LineSegment [constr] StartX=-14.6952 StartY=0 StartZ=0 EndX=-12.6952 EndY=0 EndZ=0
    g4: Circle CenterX=-10.6952 CenterY=0 CenterZ=0 NormalX=0 NormalY=0 NormalZ=1 AngleXU=0 Radius=0.75
    g5: LineSegment [constr] StartX=-12.6952 StartY=0 StartZ=0 EndX=-10.6952 EndY=0 EndZ=0
    g6: Circle CenterX=-8.69518 CenterY=0 CenterZ=0 NormalX=0 NormalY=0 NormalZ=1 AngleXU=0 Radius=0.75
    g7: LineSegment [constr] StartX=-10.6952 StartY=0 StartZ=0 EndX=-8.69518 EndY=0 EndZ=0
    g8: Circle CenterX=-6.69518 CenterY=0 CenterZ=0 NormalX=0 NormalY=0 NormalZ=1 AngleXU=0 Radius=0.75
    g9: LineSegment [constr] StartX=-8.69518 StartY=0 StartZ=0 EndX=-6.69518 EndY=0 EndZ=0
    g10: LineSegment [constr] StartX=24 StartY=64 StartZ=0 EndX=43.3449 EndY=75.1688 EndZ=0
    g11: Circle CenterX=29.6292 CenterY=67.25 CenterZ=0 NormalX=0 NormalY=0 NormalZ=1 AngleXU=0 Radius=0.75
    g12: Circle CenterX=31.3612 CenterY=68.25 CenterZ=0 NormalX=0 NormalY=0 NormalZ=1 AngleXU=0 Radius=0.75
    g13: Circle CenterX=33.0933 CenterY=69.25 CenterZ=0 NormalX=0 NormalY=0 NormalZ=1 AngleXU=0 Radius=0.75
    g14: Circle CenterX=34.8253 CenterY=70.25 CenterZ=0 NormalX=0 NormalY=0 NormalZ=1 AngleXU=0 Radius=0.75
    g15: Circle CenterX=36.5574 CenterY=71.25 CenterZ=0 NormalX=0 NormalY=0 NormalZ=1 AngleXU=0 Radius=0.75
  constraints (41):
    c: Radius(g1) = 0.75
    c: Radius(g0) = 3.75
    c: Radius(g2) = 0.75
    c: Coincident(g1,g3)
    c: Coincident(g2,g3)
    c: Distance(g3) = 2
    c: Angle(g3) = 0
    c: Radius(g4) = 0.75
    c: Coincident(g2,g5)
    c: Coincident(g4,g5)
    c: Equal(g3,g5)
    c: Radius(g6) = 0.75
    c: Coincident(g4,g7)
    c: Coincident(g6,g7)
    c: Equal(g3,g7)
    c: Radius(g8) = 0.75
    c: Coincident(g6,g9)
    c: Coincident(g8,g9)
    c: Equal(g3,g9)
    c: Parallel(g9,g3)
    c: Parallel(g9,g7)
    c: Parallel(g7,g5)
    c: Coincident(g10,g0)
    c: Angle(g10) = 0.523599
    c: Radius(g11) = 0.75
    c: Distance(g0,g11) = 6.5
    c: PointOnObject(g11,g10)
    c: Equal(g11,g12) = 0.75
    c: PointOnObject(g12,g10)
    c: DistanceX(g0) = 24
    c: DistanceY(g0) = 64
    c: Distance(g11,g12) = 2
    c: Equal(g11,g13) = 0.75
    c: PointOnObject(g13,g10)
    c: Equal(g11,g14) = 0.75
    c: PointOnObject(g14,g10)
    c: Equal(g11,g15) = 0.75
    c: PointOnObject(g15,g10)
    c: Distance(g12,g13) = 2
    c: Distance(g13,g14) = 2
    c: Distance(g14,g15) = 2
FEATURE [Part::Feature] Fusion007087  label="Servo-sg90-final033"
  Placement = pos=(0,-16.6,0) rot=(0,0,1;0rad)
  shape: bbox 11.8 x 32.4 x 29.9 mm, 77 faces (baked)
FEATURE [PartDesign::Pocket] Pocket003146  label="q1_basic_horn011"
  BaseFeature = -> Pad012114
  Length = 2.65
  Length2 = 100
  Profile = -> Sketch306
  Refine = true
  Type = 0
FEATURE [Sketcher::SketchObject] Sketch293  label="horn_holes020"
  MapMode = 5
  Placement = pos=(0,0,3.1) rot=(0,0,1;0rad)
  Support = -> [Pocket003146]
  sketch-geometry (10):
    g0: Circle CenterX=0 CenterY=0 CenterZ=0 NormalX=0 NormalY=0 NormalZ=1 AngleXU=0 Radius=3.75
    g1: Circle CenterX=-14.5 CenterY=0 CenterZ=0 NormalX=0 NormalY=0 NormalZ=1 AngleXU=0 Radius=0.75
    g2: Circle CenterX=-12.5 CenterY=0 CenterZ=0 NormalX=0 NormalY=0 NormalZ=1 AngleXU=0 Radius=0.75
    g3: LineSegment [constr] StartX=-14.5 StartY=0 StartZ=0 EndX=-12.5 EndY=0 EndZ=0
    g4: Circle CenterX=-10.5 CenterY=0 CenterZ=0 NormalX=0 NormalY=0 NormalZ=1 AngleXU=0 Radius=0.75
    g5: LineSegment [constr] StartX=-12.5 StartY=0 StartZ=0 EndX=-10.5 EndY=0 EndZ=0
    g6: Circle CenterX=-8.5 CenterY=0 CenterZ=0 NormalX=0 NormalY=0 NormalZ=1 AngleXU=0 Radius=0.75
    g7: LineSegment [constr] StartX=-10.5 StartY=0 StartZ=0 EndX=-8.5 EndY=0 EndZ=0
    g8: Circle CenterX=-6.5 CenterY=0 CenterZ=0 NormalX=0 NormalY=0 NormalZ=1 AngleXU=0 Radius=0.75
    g9: LineSegment [constr] StartX=-8.5 StartY=0 StartZ=0 EndX=-6.5 EndY=0 EndZ=0
  constraints (25):
    c: Coincident(g0,g-1)
    c: Radius(g1) = 0.75
    c: Radius(g0) = 3.75
    c: Radius(g2) = 0.75
    c: Coincident(g1,g3)
    c: Coincident(g2,g3)
    c: Distance(g3) = 2
    c: Angle(g3) = 0
    c: Radius(g4) = 0.75
    c: Coincident(g2,g5)
    c: Coincident(g4,g5)
    c: Equal(g3,g5)
    c: Parallel(g5,g3)
    c: Radius(g6) = 0.75
    c: Coincident(g4,g7)
    c: Coincident(g6,g7)
    c: Equal(g3,g7)
    c: Parallel(g7,g3)
    c: Radius(g8) = 0.75
    c: Coincident(g6,g9)
    c: Coincident(g8,g9)
    c: Equal(g3,g9)
    c: Parallel(g9,g3)
    c: PointOnObject(g2,g-1)
    c: DistanceX(g8,g-1) = 6.5
FEATURE [PartDesign::Pocket] Pocket003144  label="q1_basic_horn_shape011"
  BaseFeature = -> Pocket003146
  Length = 5
  Length2 = 100
  Profile = -> Sketch293
  Refine = true
  Type = 0
FEATURE [Sketcher::SketchObject] Sketch295  label="q2-base009"
  ExternalGeometry = -> [Pocket003144]
  MapMode = 5
  Placement = pos=(-20.5,0,0) rot=(0.57735,-0.57735,-0.57735;2.0944rad)
  Support = -> [Pocket003144]
  sketch-geometry (6):
    g0: LineSegment StartX=-5.71563 StartY=2.25 StartZ=0 EndX=-11.6041 EndY=2.25 EndZ=0
    g1: LineSegment StartX=-11.6041 StartY=2.25 StartZ=0 EndX=-38.6752 EndY=17.8795 EndZ=0
    g2: LineSegment StartX=-11.6626 StartY=5.74787 StartZ=0 EndX=-37.1752 EndY=20.4776 EndZ=0
    g3: LineSegment StartX=-37.1752 StartY=20.4776 StartZ=0 EndX=-38.6752 EndY=17.8795 EndZ=0
    g4: LineSegment StartX=-5.71563 StartY=5.74787 StartZ=0 EndX=-5.71563 EndY=2.25 EndZ=0
    g5: LineSegment StartX=-11.6626 StartY=5.74787 StartZ=0 EndX=-5.71563 EndY=5.74787 EndZ=0
  constraints (13):
    c: Coincident(g3,g2)
    c: Coincident(g3,g1)
    c: Perpendicular(g3,g1)
    c: Coincident(g0,g-3)
    c: Parallel(g1,g2)
    c: Coincident(g4,g0)
    c: Perpendicular(g4,g0)
    c: Distance(g1,g2) = 3
    c: Angle(g0,g1) = 2.61799
    c: Coincident(g0,g1)
    c: Coincident(g2,g5)
    c: Coincident(g5,g4)
    c: Horizontal(g5)
FEATURE [PartDesign::Pad] Pad012116  label="q2-bed-base009"
  BaseFeature = -> Pocket003144
  Length = 26.215
  Length2 = 100
  Profile = -> Sketch295
  Refine = true
  Reversed = true
  Type = 0
FEATURE [Sketcher::SketchObject] Sketch312  label="q2-corner-hole019"
  MapMode = 5
  Placement = pos=(0,0,5.74787) rot=(0,0,1;0rad)
  Support = -> [Pad012116]
  sketch-geometry (4):
    g0: LineSegment StartX=-1.62396 StartY=12 StartZ=0 EndX=-5 EndY=12 EndZ=0
    g1: LineSegment StartX=-5 StartY=12 StartZ=0 EndX=-5 EndY=6.68085 EndZ=0
    g2: LineSegment StartX=-5 StartY=6.68085 StartZ=0 EndX=-1.62396 EndY=6.68085 EndZ=0
    g3: LineSegment StartX=-1.62396 StartY=6.68085 StartZ=0 EndX=-1.62396 EndY=12 EndZ=0
  constraints (8):
    c: Coincident(g0,g1)
    c: Coincident(g1,g2)
    c: Coincident(g2,g3)
    c: Coincident(g3,g0)
    c: Horizontal(g0)
    c: Horizontal(g2)
    c: Vertical(g1)
    c: Vertical(g3)
FEATURE [PartDesign::Pocket] Pocket003145  label="q2-corner-hole018"
  BaseFeature = -> Pad012116
  Length = 2
  Length2 = 100
  Profile = -> Sketch312
  Refine = true
  Type = 0
FEATURE [Part::MultiFuse] Fusion007088  label="q2-aux-servo011"
  Placement = pos=(23.9256,-20.5,63.7846) rot=(0.377964,0.654656,0.654652;3.86432rad)
  Refine = true
  Shapes = -> [Fusion007087,Pocket003142]
FEATURE [Part::Feature] Pocket003147  label="Final-1-arm-horn031"
  Placement = pos=(0,0,32) rot=(0.707107,-0.707107,0;3.14159rad)
  shape: bbox 8 x 22.5 x 5 mm, 19 faces (baked)
FEATURE [Part::MultiFuse] Fusion007086  label="q1-aux-servo011"
  Placement = pos=(0,0,17.25) rot=(0,0,1;0rad)
  Refine = true
  Shapes = -> [Pocket003147,Fusion007085]
FEATURE [PartDesign::Pocket] Pocket003148  label="basic_horn_union009"
  BaseFeature = -> Pocket003143
  Length = 5
  Length2 = 100
  Placement = pos=(0,6.2,0) rot=(0,0.707107,0.707107;3.14159rad)
  Profile = -> Sketch311
  Refine = true
  Type = 0
FEATURE [Sketcher::SketchObject] Sketch309  label="q2_bridge019"
  ExternalGeometry = -> [Pocket003148]
  MapMode = 5
  Placement = pos=(2e-16,8.45,-2.3e-15) rot=(0,-0.707107,0.707107;3.14159rad)
  Support = -> [Pocket003148]
  sketch-geometry (4):
    g0: LineSegment StartX=39.516 StartY=-79.5977 StartZ=0 EndX=45.266 EndY=-69.6384 EndZ=0
    g1: LineSegment StartX=45.266 StartY=-69.6384 StartZ=0 EndX=40.9358 EndY=-67.1384 EndZ=0
    g2: LineSegment StartX=39.516 StartY=-79.5977 StartZ=0 EndX=35.1858 EndY=-77.0977 EndZ=0
    g3: ArcOfCircle CenterX=24.5001 CenterY=-64.2888 CenterZ=0 NormalX=0 NormalY=0 NormalZ=1 AngleXU=0 Radius=16.6809 StartAngle=5.40766 EndAngle=6.11151
  constraints (10):
    c: Coincident(g-5,g0)
    c: Coincident(g0,g-5)
    c: Coincident(g0,g1)
    c: PointOnObject(g1,g-3)
    c: Coincident(g0,g2)
    c: PointOnObject(g2,g-4)
    c: Distance(g2) = 5
    c: Equal(g2,g1)
    c: Coincident(g3,g1)
    c: Coincident(g3,g2)
FEATURE [PartDesign::Pad] Pad012113  label="q2_bridge018"
  BaseFeature = -> Pocket003148
  Length = 31
  Length2 = 100
  Placement = pos=(0,6.2,0) rot=(0,0.707107,0.707107;3.14159rad)
  Profile = -> Sketch309
  Refine = true
  Type = 0
FEATURE [Sketcher::SketchObject] Sketch296  label="q2_back_union009"
  ExternalGeometry = -> [Pad012122,Sketch301]
  MapMode = 5
  Placement = pos=(-2.3e-15,-22.55,3.83e-14) rot=(0,-0.707107,0.707107;3.14159rad)
  Support = -> [Pad012113]
  expr: Constraints[2] = Sketch067.Constraints[2]
  sketch-geometry (7):
    g0: ArcOfCircle CenterX=24 CenterY=-64 CenterZ=0 NormalX=0 NormalY=0 NormalZ=1 AngleXU=0 Radius=5.75 StartAngle=1.0472 EndAngle=4.18879
    g1: LineSegment [constr] StartX=12.5 StartY=-64 StartZ=0 EndX=37 EndY=-64 EndZ=0
    g2: LineSegment [constr] StartX=24 StartY=-64 StartZ=0 EndX=26.875 EndY=-59.0204 EndZ=0
    g3: LineSegment StartX=45.266 StartY=-69.6384 StartZ=0 EndX=26.875 EndY=-59.0204 EndZ=0
    g4: LineSegment StartX=45.266 StartY=-69.6384 StartZ=0 EndX=39.516 EndY=-79.5977 EndZ=0
    g5: LineSegment StartX=39.516 StartY=-79.5977 StartZ=0 EndX=21.125 EndY=-68.9796 EndZ=0
    g6: Circle CenterX=24 CenterY=-64 CenterZ=0 NormalX=0 NormalY=0 NormalZ=1 AngleXU=0 Radius=2
  constraints (16):
    c: Coincident(g0,g-3)
    c: PointOnObject(g0,g-3)
    c: Angle(g0) = 3.14159
    c: Horizontal(g1)
    c: PointOnObject(g0,g1)
    c: Coincident(g2,g0)
    c: Coincident(g2,g0)
    c: Parallel(g2,g-4)
    c: Coincident(g-4,g3)
    c: Coincident(g3,g0)
    c: Coincident(g3,g4)
    c: Coincident(g4,g-4)
    c: Coincident(g4,g5)
    c: Coincident(g5,g0)
    c: Coincident(g6,g0)
    c: Radius(g6) = 2
FEATURE [PartDesign::Pad] Pad012121  label="q2_joint009"
  BaseFeature = -> Pad012113
  Length = 3.5
  Length2 = 100
  Placement = pos=(0,6.2,0) rot=(0,0.707107,0.707107;3.14159rad)
  Profile = -> Sketch296
  Refine = true
  Type = 0
FEATURE [Sketcher::SketchObject] Sketch292  label="q2-leg_union_section009"
  ExternalGeometry = -> [Pad012121]
  MapMode = 5
  Placement = pos=(-64.1038,6.2,37.0103) rot=(0,-1,0;1.0472rad)
  Support = -> [Pad012121]
  sketch-geometry (4):
    g0: LineSegment StartX=49.1756 StartY=5.75 StartZ=0 EndX=49.1756 EndY=-32.25 EndZ=0
    g1: LineSegment StartX=49.1756 StartY=-32.25 StartZ=0 EndX=37.6756 EndY=-32.25 EndZ=0
    g2: LineSegment StartX=37.6756 StartY=-32.25 StartZ=0 EndX=37.6756 EndY=5.75 EndZ=0
    g3: LineSegment StartX=37.6756 StartY=5.75 StartZ=0 EndX=49.1756 EndY=5.75 EndZ=0
  constraints (8):
    c: Coincident(g-6,g0)
    c: Coincident(g0,g-6)
    c: Coincident(g0,g1)
    c: Coincident(g1,g-5)
    c: Coincident(g-5,g2)
    c: Coincident(g2,g-4)
    c: Coincident(g2,g3)
    c: Coincident(g3,g0)
FEATURE [Sketcher::SketchObject] Sketch313  label="trajectory009"
  ExternalGeometry = -> [Pad012121]
  MapMode = 5
  Placement = pos=(6e-16,11.95,-5.8e-15) rot=(0,0.707107,0.707107;3.14159rad)
  Support = -> [Pad012121]
  sketch-geometry (8):
    g0: GeomPoint X=42.3808 Y=74.6356 Z=0
    g1-g4: Circle [constr] x4 (B-spline internal-alignment scaffolding for g5; pole/knot coordinates omitted)
    g5: BSplineCurve PolesCount=4 KnotsCount=2 Degree=3 IsPeriodic=0
    g6: GeomPoint [constr] X=42.3808 Y=74.6356 Z=0
    g7: GeomPoint [constr] X=64.6677 Y=0 Z=0
  constraints (10):
    c: PointOnObject(g0,g-3)
    c: Coincident(g1,g0)
    c: Radius(g1) = 4
    c: Equal(g1,g2)
    c: Equal(g1,g3)
    c: Equal(g1,g4)
    c: PointOnObject(g4,g-1)
    c: InternalAlignment(g1-g4 -> g5) x4
    c: InternalAlignment(g6,g5)
    c: InternalAlignment(g7,g5)
FEATURE [Sketcher::SketchObject] Sketch303  label="q2-bone-touch_section009"
  ExternalGeometry = -> [Sketch313,Pad012121]
  MapMode = 5
  Support = -> [XY_Plane051]
  sketch-geometry (7):
    g0: LineSegment StartX=-66.1677 StartY=-4.55 StartZ=0 EndX=-63.1677 EndY=-4.55 EndZ=0
    g1: LineSegment StartX=-63.1677 StartY=-4.55 StartZ=0 EndX=-63.1677 EndY=-9.55 EndZ=0
    g2: LineSegment StartX=-63.1677 StartY=-9.55 StartZ=0 EndX=-66.1677 EndY=-9.55 EndZ=0
    g3: LineSegment StartX=-66.1677 StartY=-9.55 StartZ=0 EndX=-66.1677 EndY=-4.55 EndZ=0
    g4: GeomPoint X=-45.266 Y=-7.05 Z=0
    g5: GeomPoint X=-63.1677 Y=-7.05 Z=0
    g6: GeomPoint X=-64.6677 Y=-4.55 Z=0
  constraints (18):
    c: Coincident(g0,g1)
    c: Coincident(g1,g2)
    c: Coincident(g2,g3)
    c: Coincident(g3,g0)
    c: Horizontal(g0)
    c: Horizontal(g2)
    c: Vertical(g1)
    c: Vertical(g3)
    c: PointOnObject(g4,g-4)
    c: Symmetric(g-4,g-4,g4)
    c: PointOnObject(g5,g1)
    c: Symmetric(g0,g1,g5)
    c: Horizontal(g5,g4)
    c: PointOnObject(g6,g0)
    c: Symmetric(g0,g0,g6)
    c: Vertical(g6,g-3)
    c: DistanceX(g2,g2) = 3
    c: DistanceY(g3,g3) = 5
FEATURE [PartDesign::AdditivePipe] AdditivePipe009
  AuxilleryCurvelinear = true
  AuxillerySpineTangent = false
  BaseFeature = -> Pad012121
  Binormal = (0,0,0)
  Mode = 0
  Placement = pos=(0,6.2,0) rot=(0,0.707107,0.707107;3.14159rad)
  Profile = -> Sketch292
  Refine = true
  Sections = -> [Sketch303]
  Spine = -> Sketch313
  SpineTangent = false
  Transformation = 1
  Transition = 0
FEATURE [PartDesign::Body] Body031  label="Q2-Leg-joint009"
  Group = -> [Sketch304,Pad012122,Sketch301,Pad012118,Sketch302,Sketch297,Pocket003143,Sketch311,Pocket003148,Sketch309,Pad012113,Sketch296,Pad012121,Sketch313,Sketch292,Sketch303,AdditivePipe009]
  Origin = -> Origin053
  Tip = -> AdditivePipe009
FEATURE [Part::Mirroring] Part__Mirroring005  label="Q2-Leg-joint007 (Mirror #2)002"
  Base = (0,0,0)
  Normal = (1,0,0)
  Source = -> Body031
FEATURE [PartDesign::Body] Clone038Body
  Origin = -> Origin055
FEATURE [PartDesign::Body] Body032
  Origin = -> Origin056
FEATURE [App::Part] Part019
  Group = -> [Clone038Body,Body032]
  License = CC BY 3.0
  LicenseURL = http://creativecommons.org/licenses/by/3.0/
  Origin = -> Origin054
FEATURE [Sketcher::SketchObject] Sketch314  label="servo_offset"
  ExternalGeometry = -> [Pocket003057]
  MapMode = 5
  Placement = pos=(0,0,0) rot=(1,0,0;3.14159rad)
  Support = -> [Pocket003057]
  sketch-geometry (3):
    g0: Circle CenterX=0 CenterY=0 CenterZ=0 NormalX=0 NormalY=0 NormalZ=1 AngleXU=0 Radius=5.75
    g1: Circle CenterX=0 CenterY=0 CenterZ=0 NormalX=0 NormalY=0 NormalZ=1 AngleXU=0 Radius=3.75
    g2: GeomPoint X=3.75 Y=0 Z=0
  constraints (6):
    c: Coincident(g0,g-1)
    c: PointOnObject(g-3,g0)
    c: Coincident(g1,g-1)
    c: PointOnObject(g2,g-1)
    c: PointOnObject(g2,g-4)
    c: PointOnObject(g2,g1)
FEATURE [PartDesign::Pad] Pad012123  label="servo_offset001"
  BaseFeature = -> Pocket003057
  Length = 1
  Length2 = 100
  Profile = -> Sketch314
  Refine = true
  Type = 0
FEATURE [PartDesign::Body] Clone040Body
  Origin = -> Origin057
FEATURE [PartDesign::Fillet] Fillet012
  Base = -> Pad012123 [Edge27]
  BaseFeature = -> Pad012123
  Radius = 8
FEATURE [PartDesign::Body] Body008  label="Q1-base"
  Group = -> [Sketch039,Pad010,Sketch040,Sketch041,Pad011,Pocket003044,Sketch042,Pocket003045,Sketch056,Pad012005,Sketch057,Pocket003054,Sketch058,Pad012006,Sketch059,Pad012007,Sketch060,Sketch061,Sketch062,Sketch063,Pad012008,Sketch064,Pad012009,Pocket003055,Pocket003056,Hole,Sketch065,Pocket003057,Sketch314,Pad012123,Fillet012]
  Origin = -> Origin013
  Placement = pos=(0,0,44) rot=(0,0,1;1.5708rad)
  Tip = -> Fillet012
FEATURE [App::Part] Part004  label="Leg_left"
  Group = -> [Pocket003042,Fusion007040,Fusion007041,Body008,Fusion007043,Pocket003043,Fusion007044,Clone036,Fillet002,Body011,Clone040Body]
  License = CC BY 3.0
  LicenseURL = http://creativecommons.org/licenses/by/3.0/
  Origin = -> Origin012
FEATURE [App::DocumentObjectGroup] Grupo  label="src"
  Group = -> [Part,Part003,Part004,Part016]
FEATURE [App::DocumentObjectGroup] Grupo001  label="assembly"
  Group = -> [Grupo037,Part__Feature863,Grupo038,Grupo039,Grupo041,Grupo042]
FEATURE [App::DocumentObjectGroup] Grupo042  label="legs"
  Group = -> [Part008,Part009,Part010,Part011,Part012,Part013,Part015,Part017,Part018]
FEATURE [PartDesign::FeatureBase] Clone038
  BaseFeature = -> Pocket003067
FEATURE [App::Part] Part008  label="center_leg"
  Group = -> [Pocket003060,Fusion007055,Fusion007054,Body012,Fusion007056,Pocket003061,Fusion007053,Clone038,Fillet003,Body013]
  License = CC BY 3.0
  LicenseURL = http://creativecommons.org/licenses/by/3.0/
  Origin = -> Origin022
FEATURE [PartDesign::Body] Body012  label="Q1-base003"
  Group = -> [Sketch080,Pad012014,Sketch081,Sketch082,Pad012015,Pocket003062,Sketch083,Pocket003063,Sketch084,Pad012016,Sketch085,Pocket003064,Sketch086,Pad012017,Sketch087,Pad012018,Sketch088,Sketch089,Sketch090,Sketch091,Pad012019,Sketch092,Pad012020,Pocket003065,Pocket003066,Hole001,Sketch093,Pocket003067]
  Origin = -> Origin023
  Placement = pos=(0,0,44) rot=(0,0,1;1.5708rad)
  Tip = -> Pocket003067
FEATURE [Sketcher::SketchObject] Sketch086  label="servo-walls001"
  ExternalGeometry = -> [Pocket003064]
  MapMode = 5
  Placement = pos=(2.152e-13,-5.82326,10.0862) rot=(1,0,0;0.523599rad)
  Support = -> [Pad012019]
  sketch-geometry (24):
    g0: LineSegment StartX=-5 StartY=42.4334 StartZ=0 EndX=-5 EndY=37 EndZ=0
    g1: LineSegment StartX=-5 StartY=37 StartZ=0 EndX=-20.5 EndY=37 EndZ=0
    g2: LineSegment StartX=-20.5 StartY=37 StartZ=0 EndX=-20.5 EndY=39 EndZ=0
    g3: LineSegment StartX=2 StartY=39 StartZ=0 EndX=2 EndY=37 EndZ=0
    g4: LineSegment StartX=2 StartY=37 StartZ=0 EndX=-1.60533 EndY=37 EndZ=0
    g5: LineSegment StartX=-1.60533 StartY=37 StartZ=0 EndX=-1.60533 EndY=42.4334 EndZ=0
    g6: LineSegment StartX=-20.5 StartY=39 StartZ=0 EndX=-7 EndY=39 EndZ=0
    g7: LineSegment StartX=-7 StartY=39 StartZ=0 EndX=-7 EndY=42.4334 EndZ=0
    g8: LineSegment StartX=-7 StartY=42.4334 StartZ=0 EndX=-5 EndY=42.4334 EndZ=0
    g9: LineSegment StartX=2 StartY=39 StartZ=0 EndX=0.5 EndY=39 EndZ=0
    g10: LineSegment StartX=0.5 StartY=39 StartZ=0 EndX=0.5 EndY=42.4334 EndZ=0
    g11: LineSegment StartX=-1.60533 StartY=42.4334 StartZ=0 EndX=0.5 EndY=42.4334 EndZ=0
    g12: LineSegment StartX=-5 StartY=9.5 StartZ=0 EndX=-5 EndY=14 EndZ=0
    g13: LineSegment StartX=-5 StartY=14 StartZ=0 EndX=-20.5 EndY=14 EndZ=0
    g14: LineSegment StartX=-20.5 StartY=14 StartZ=0 EndX=-20.5 EndY=12 EndZ=0
    g15: LineSegment StartX=2 StartY=12 StartZ=0 EndX=2 EndY=14 EndZ=0
    g16: LineSegment StartX=2 StartY=14 StartZ=0 EndX=-1.61532 EndY=14 EndZ=0
    g17: LineSegment StartX=-1.61532 StartY=14 StartZ=0 EndX=-1.61532 EndY=9.5 EndZ=0
    g18: LineSegment StartX=-20.5 StartY=12 StartZ=0 EndX=-7 EndY=12 EndZ=0
    g19: LineSegment StartX=-7 StartY=12 StartZ=0 EndX=-7 EndY=9.5 EndZ=0
    g20: LineSegment StartX=-7 StartY=9.5 StartZ=0 EndX=-5 EndY=9.5 EndZ=0
    g21: LineSegment StartX=2 StartY=12 StartZ=0 EndX=0.5 EndY=12 EndZ=0
    g22: LineSegment StartX=0.5 StartY=12 StartZ=0 EndX=0.5 EndY=9.5 EndZ=0
    g23: LineSegment StartX=-1.61532 StartY=9.5 StartZ=0 EndX=0.5 EndY=9.5 EndZ=0
  constraints (50):
    c: Coincident(g0,g1)
    c: Coincident(g1,g2)
    c: Horizontal(g1)
    c: Vertical(g0)
    c: Vertical(g2)
    c: Coincident(g3,g4)
    c: Coincident(g4,g5)
    c: Horizontal(g4)
    c: Vertical(g3)
    c: Vertical(g5)
    c: Coincident(g2,g6)
    c: Horizontal(g6)
    c: Coincident(g6,g7)
    c: Vertical(g7)
    c: PointOnObject(g7,g-3)
    c: PointOnObject(g0,g-3)
    c: Coincident(g8,g7)
    c: Coincident(g8,g0)
    c: Coincident(g3,g9)
    c: Horizontal(g9)
    c: Coincident(g9,g10)
    c: PointOnObject(g10,g-3)
    c: Vertical(g10)
    c: PointOnObject(g5,g-3)
    c: Coincident(g11,g5)
    c: Coincident(g11,g10)
    c: Coincident(g12,g13)
    c: Coincident(g13,g14)
    c: Horizontal(g13)
    c: Vertical(g12)
    c: Vertical(g14)
    c: Coincident(g15,g16)
    c: Coincident(g16,g17)
    c: Horizontal(g16)
    c: Vertical(g15)
    c: Vertical(g17)
    c: Coincident(g14,g18)
    c: Horizontal(g18)
    c: Coincident(g18,g19)
    c: Vertical(g19)
    c: Coincident(g19,g20)
    c: Coincident(g20,g12)
    c: Horizontal(g20)
    c: Coincident(g15,g21)
    c: Horizontal(g21)
    c: Coincident(g21,g22)
    c: Vertical(g22)
    c: Coincident(g17,g23)
    c: Coincident(g23,g22)
    c: Horizontal(g23)
FEATURE [PartDesign::Pad] Pad012017  label="servo_walls001"
  BaseFeature = -> Pocket003064
  Length = 12.5
  Length2 = 100
  Profile = -> Sketch086
  Refine = true
  Type = 0
FEATURE [Sketcher::SketchObject] Sketch087  label="front_wall002"
  ExternalGeometry = -> [Pad012017]
  MapMode = 5
  Placement = pos=(2,0,0) rot=(0.57735,0.57735,0.57735;2.0944rad)
  Support = -> [Pad012017]
  sketch-geometry (9):
    g0: ArcOfCircle CenterX=18.4487 CenterY=16.9211 CenterZ=0 NormalX=0 NormalY=0 NormalZ=1 AngleXU=0 Radius=3.06832 StartAngle=3.68648 EndAngle=5.44463
    g1: LineSegment StartX=10.969 StartY=5.00105 StartZ=0 EndX=34.5617 EndY=18.1373 EndZ=0
    g2: LineSegment StartX=12.6837 StartY=20.7712 StartZ=0 EndX=4.56905 EndY=16.0862 EndZ=0
    g3: LineSegment StartX=4.56905 StartY=16.0862 StartZ=0 EndX=10.969 EndY=5.00105 EndZ=0
    g4: ArcOfCircle CenterX=24 CenterY=19.9888 CenterZ=0 NormalX=0 NormalY=0 NormalZ=1 AngleXU=0 Radius=6.3928 StartAngle=4.13303 EndAngle=7.03916
    g5: LineSegment StartX=28.6514 StartY=24.3743 StartZ=0 EndX=26.2197 EndY=28.5862 EndZ=0
    g6: LineSegment StartX=26.2197 StartY=28.5862 StartZ=0 EndX=27.9517 EndY=29.5862 EndZ=0
    g7: LineSegment StartX=27.9517 StartY=29.5862 StartZ=0 EndX=34.5617 EndY=18.1373 EndZ=0
    g8: LineSegment StartX=12.6837 StartY=20.7712 StartZ=0 EndX=15.8247 EndY=15.3307 EndZ=0
  constraints (20):
    c: Coincident(g3,g2)
    c: Parallel(g-7,g3)
    c: Coincident(g-7,g2)
    c: Coincident(g1,g3)
    c: Parallel(g-8,g2)
    c: Coincident(g4,g0)
    c: PointOnObject(g4,g-4)
    c: Coincident(g5,g4)
    c: Coincident(g5,g-5)
    c: Coincident(g5,g6)
    c: Coincident(g6,g-5)
    c: Coincident(g6,g7)
    c: Parallel(g-9,g7)
    c: Coincident(g7,g1)
    c: Coincident(g8,g2)
    c: Coincident(g8,g0)
    c: Perpendicular(g8,g2)
    c: Distance(g2) = 9.37
    c: Distance(g3) = 12.8
    c: Distance(g7) = 13.22
FEATURE [PartDesign::Pad] Pad012018  label="front_wall003"
  BaseFeature = -> Pad012017
  Length = 3.715
  Length2 = 100
  Profile = -> Sketch087
  Refine = true
  Type = 0
FEATURE [Sketcher::SketchObject] Sketch088  label="m2_screw_holes002"
  MapMode = 5
  Placement = pos=(-22.25,0,0) rot=(0.57735,-0.57735,-0.57735;2.0944rad)
  Support = -> [Pocket003066]
  sketch-geometry (2):
    g0: Circle CenterX=-31.1478 CenterY=24.1208 CenterZ=0 NormalX=0 NormalY=0 NormalZ=1 AngleXU=0 Radius=1.25
    g1: Circle CenterX=-7.61619 CenterY=10.5 CenterZ=0 NormalX=0 NormalY=0 NormalZ=1 AngleXU=0 Radius=1.25
  constraints (2):
    c: Radius(g0) = 1.25
    c: Equal(g0,g1) = 1.25
FEATURE [Sketcher::SketchObject] Sketch089  label="back_wall002"
  ExternalGeometry = -> [Pad012018]
  MapMode = 5
  Placement = pos=(-20.5,0,0) rot=(0.57735,-0.57735,-0.57735;2.0944rad)
  Support = -> [Pad012018]
  sketch-geometry (9):
    g0: LineSegment StartX=5.71497 StartY=2.25 StartZ=0 EndX=-11.6041 EndY=2.25 EndZ=0
    g1: LineSegment StartX=-11.6041 StartY=2.25 StartZ=0 EndX=-38.6752 EndY=17.8795 EndZ=0
    g2: LineSegment StartX=-38.6752 StartY=17.8795 StartZ=0 EndX=-37.1752 EndY=20.4776 EndZ=0
    g3: LineSegment StartX=-37.1752 StartY=20.4776 StartZ=0 EndX=-34.2017 EndY=18.7609 EndZ=0
    g4: LineSegment StartX=-34.2017 StartY=18.7609 StartZ=0 EndX=-27.9517 EndY=29.5862 EndZ=0
    g5: LineSegment StartX=-27.9517 StartY=29.5862 StartZ=0 EndX=-4.56905 EndY=16.0862 EndZ=0
    g6: LineSegment StartX=-4.56905 StartY=16.0862 StartZ=0 EndX=-10.5379 EndY=5.74787 EndZ=0
    g7: LineSegment StartX=-10.5379 StartY=5.74787 StartZ=0 EndX=5.71497 EndY=5.75 EndZ=0
    g8: LineSegment StartX=5.71497 StartY=5.75 StartZ=0 EndX=5.71497 EndY=2.25 EndZ=0
  constraints (18):
    c: Coincident(g-11,g0)
    c: Coincident(g0,g-11)
    c: Coincident(g0,g1)
    c: Coincident(g1,g-4)
    c: Coincident(g1,g2)
    c: Coincident(g2,g-5)
    c: Coincident(g2,g3)
    c: Coincident(g3,g-6)
    c: Coincident(g3,g4)
    c: Coincident(g4,g-6)
    c: Coincident(g4,g5)
    c: Coincident(g5,g-7)
    c: Coincident(g5,g6)
    c: Coincident(g6,g-8)
    c: Coincident(g6,g7)
    c: Coincident(g7,g-10)
    c: Coincident(g7,g8)
    c: Coincident(g8,g0)
FEATURE [Sketcher::SketchObject] Sketch090  label="servo_tollerance002"
  MapMode = 5
  Placement = pos=(2.152e-13,-5.82326,10.0862) rot=(1,0,0;0.523599rad)
  Support = -> [Pad012020]
  sketch-geometry (4):
    g0: LineSegment StartX=-20.5 StartY=37 StartZ=0 EndX=-21.25 EndY=37 EndZ=0
    g1: LineSegment StartX=-21.25 StartY=37 StartZ=0 EndX=-21.25 EndY=14 EndZ=0
    g2: LineSegment StartX=-21.25 StartY=14 StartZ=0 EndX=-20.5 EndY=14 EndZ=0
    g3: LineSegment StartX=-20.5 StartY=14 StartZ=0 EndX=-20.5 EndY=37 EndZ=0
  constraints (9):
    c: Coincident(g0,g1)
    c: Coincident(g1,g2)
    c: Coincident(g2,g3)
    c: Coincident(g3,g0)
    c: Horizontal(g0)
    c: Horizontal(g2)
    c: Vertical(g1)
    c: Vertical(g3)
    c: DistanceX(g0,g0) = 0.75
FEATURE [Sketcher::SketchObject] Sketch091  label="cable_slot002"
  ExternalGeometry = -> [Pocket003065]
  MapMode = 5
  Placement = pos=(-3.873e-13,33.775,19.5) rot=(0,0.5,0.866025;3.14159rad)
  Support = -> [Pocket003065]
  sketch-geometry (4):
    g0: LineSegment StartX=20.25 StartY=3 StartZ=0 EndX=18.01 EndY=3 EndZ=0
    g1: LineSegment StartX=18.01 StartY=3 StartZ=0 EndX=18.01 EndY=12.5 EndZ=0
    g2: LineSegment StartX=18.01 StartY=12.5 StartZ=0 EndX=20.25 EndY=12.5 EndZ=0
    g3: LineSegment StartX=20.25 StartY=12.5 StartZ=0 EndX=20.25 EndY=3 EndZ=0
  constraints (11):
    c: Coincident(g0,g1)
    c: Coincident(g1,g2)
    c: Coincident(g2,g3)
    c: Coincident(g3,g0)
    c: Horizontal(g0)
    c: Horizontal(g2)
    c: Vertical(g1)
    c: Vertical(g3)
    c: DistanceX(g2,g2) = 2.24
    c: DistanceY(g1,g1) = 9.5
    c: DistanceX(g2,g-3) = 2
FEATURE [PartDesign::Pad] Pad012019  label="back_wall003"
  BaseFeature = -> Pad012018
  Length = 1.75
  Length2 = 100
  Profile = -> Sketch089
  Refine = true
  Type = 0
FEATURE [Sketcher::SketchObject] Sketch092  label="q2_axis001"
  MapMode = 5
  Placement = pos=(-22.25,0,0) rot=(0.57735,-0.57735,-0.57735;2.0944rad)
  Support = -> [Pad012019]
  sketch-geometry (1):
    g0: Circle CenterX=-24 CenterY=20 CenterZ=0 NormalX=0 NormalY=0 NormalZ=1 AngleXU=0 Radius=1.75
  constraints (1):
    c: Radius(g0) = 1.75
FEATURE [PartDesign::Pad] Pad012020  label="servo_axis001"
  BaseFeature = -> Pad012019
  Length = 3
  Length2 = 100
  Profile = -> Sketch092
  Refine = true
  Type = 0
FEATURE [PartDesign::Pocket] Pocket003065  label="servo_tollerance003"
  BaseFeature = -> Pad012020
  Length = 12.5
  Length2 = 100
  Profile = -> Sketch090
  Refine = true
  Type = 0
FEATURE [PartDesign::Pocket] Pocket003066  label="cable_slot003"
  BaseFeature = -> Pocket003065
  Length = 5
  Length2 = 100
  Profile = -> Sketch091
  Refine = true
  Type = 0
FEATURE [PartDesign::Hole] Hole001  label="m2_screw_holes003"
  BaseFeature = -> Pocket003066
  Depth = 35
  DepthType = 0
  Diameter = 2.5
  DrillPoint = 1
  DrillPointAngle = 118
  HoleCutCountersinkAngle = 90
  HoleCutDepth = 0
  HoleCutDiameter = 0
  HoleCutType = 0
  ModelActualThread = false
  Profile = -> Sketch088
  Refine = true
  Tapered = false
  TaperedAngle = 90
  ThreadAngle = 0
  ThreadClass = 0
  ThreadCutOffInner = 0
  ThreadCutOffOuter = 0
  ThreadDirection = 0
  ThreadFit = 0
  ThreadPitch = 0
  ThreadSize = 0
  ThreadType = 0
  Threaded = false
FEATURE [PartDesign::Pocket] Pocket003067  label="q1-leg001"
  BaseFeature = -> Hole001
  Length = 5
  Length2 = 100
  Profile = -> Sketch093
  Refine = true
  Type = 0
FEATURE [Part::Fillet] Fillet003  label="rounder_q1_servo001"
  Base = -> Clone038
  Edges = 1 edges r=8: [Edge27]
  Placement = pos=(0,0,44) rot=(0,0,1;1.5708rad)
FEATURE [Sketcher::SketchObject] Sketch093  label="finger_hole001"
  ExternalGeometry = -> [Hole001]
  MapMode = 5
  Placement = pos=(2.5e-15,1.92674,-3.33722) rot=(1,0,0;3.66519rad)
  Support = -> [Hole001]
  sketch-geometry (2):
    g0: Circle CenterX=-8.2675 CenterY=-26.8039 CenterZ=0 NormalX=0 NormalY=0 NormalZ=1 AngleXU=0 Radius=6
    g1: LineSegment [constr] StartX=-8.2675 StartY=-11.1744 StartZ=0 EndX=-8.2675 EndY=-42.4334 EndZ=0
  constraints (7):
    c: Radius(g0) = 6
    c: PointOnObject(g1,g-3)
    c: PointOnObject(g1,g-4)
    c: Vertical(g1)
    c: PointOnObject(g0,g1)
    c: Symmetric(g-3,g-3,g1)
    c: Symmetric(g1,g1,g0)
FEATURE [PartDesign::Pad] Pad012025  label="front_wall004"
  BaseFeature = -> Pad012036
  Length = 3.715
  Length2 = 100
  Profile = -> Sketch124
  Refine = true
  Type = 0
FEATURE [PartDesign::Hole] Hole002  label="m2_screw_holes004"
  BaseFeature = -> Pocket003079
  Depth = 35
  DepthType = 0
  Diameter = 2.5
  DrillPoint = 1
  DrillPointAngle = 118
  HoleCutCountersinkAngle = 90
  HoleCutDepth = 0
  HoleCutDiameter = 0
  HoleCutType = 0
  ModelActualThread = false
  Profile = -> Sketch129
  Refine = true
  Tapered = false
  TaperedAngle = 90
  ThreadAngle = 0
  ThreadClass = 0
  ThreadCutOffInner = 0
  ThreadCutOffOuter = 0
  ThreadDirection = 0
  ThreadFit = 0
  ThreadPitch = 0
  ThreadSize = 0
  ThreadType = 0
  Threaded = false
FEATURE [Sketcher::SketchObject] Sketch109  label="q2_axis002"
  MapMode = 5
  Placement = pos=(-22.25,0,0) rot=(0.57735,-0.57735,-0.57735;2.0944rad)
  Support = -> [Pad012034]
  sketch-geometry (1):
    g0: Circle CenterX=-24 CenterY=20 CenterZ=0 NormalX=0 NormalY=0 NormalZ=1 AngleXU=0 Radius=1.75
  constraints (1):
    c: Radius(g0) = 1.75
FEATURE [PartDesign::Pocket] Pocket003072  label="servo_tollerance004"
  BaseFeature = -> Pad012030
  Length = 12.5
  Length2 = 100
  Profile = -> Sketch113
  Refine = true
  Type = 0
FEATURE [Sketcher::SketchObject] Sketch112  label="back_wall004"
  ExternalGeometry = -> [Pad012025]
  MapMode = 5
  Placement = pos=(-20.5,0,0) rot=(0.57735,-0.57735,-0.57735;2.0944rad)
  Support = -> [Pad012025]
  sketch-geometry (9):
    g0: LineSegment StartX=5.71497 StartY=2.25 StartZ=0 EndX=-11.6041 EndY=2.25 EndZ=0
    g1: LineSegment StartX=-11.6041 StartY=2.25 StartZ=0 EndX=-38.6752 EndY=17.8795 EndZ=0
    g2: LineSegment StartX=-38.6752 StartY=17.8795 StartZ=0 EndX=-37.1752 EndY=20.4776 EndZ=0
    g3: LineSegment StartX=-37.1752 StartY=20.4776 StartZ=0 EndX=-34.2017 EndY=18.7609 EndZ=0
    g4: LineSegment StartX=-34.2017 StartY=18.7609 StartZ=0 EndX=-27.9517 EndY=29.5862 EndZ=0
    g5: LineSegment StartX=-27.9517 StartY=29.5862 StartZ=0 EndX=-4.56905 EndY=16.0862 EndZ=0
    g6: LineSegment StartX=-4.56905 StartY=16.0862 StartZ=0 EndX=-10.5379 EndY=5.74787 EndZ=0
    g7: LineSegment StartX=-10.5379 StartY=5.74787 StartZ=0 EndX=5.71497 EndY=5.75 EndZ=0
    g8: LineSegment StartX=5.71497 StartY=5.75 StartZ=0 EndX=5.71497 EndY=2.25 EndZ=0
  constraints (18):
    c: Coincident(g-11,g0)
    c: Coincident(g0,g-11)
    c: Coincident(g0,g1)
    c: Coincident(g1,g-4)
    c: Coincident(g1,g2)
    c: Coincident(g2,g-5)
    c: Coincident(g2,g3)
    c: Coincident(g3,g-6)
    c: Coincident(g3,g4)
    c: Coincident(g4,g-6)
    c: Coincident(g4,g5)
    c: Coincident(g5,g-7)
    c: Coincident(g5,g6)
    c: Coincident(g6,g-8)
    c: Coincident(g6,g7)
    c: Coincident(g7,g-10)
    c: Coincident(g7,g8)
    c: Coincident(g8,g0)
FEATURE [Sketcher::SketchObject] Sketch113  label="servo_tollerance005"
  MapMode = 5
  Placement = pos=(2.152e-13,-5.82326,10.0862) rot=(1,0,0;0.523599rad)
  Support = -> [Pad012030]
  sketch-geometry (4):
    g0: LineSegment StartX=-20.5 StartY=37 StartZ=0 EndX=-21.25 EndY=37 EndZ=0
    g1: LineSegment StartX=-21.25 StartY=37 StartZ=0 EndX=-21.25 EndY=14 EndZ=0
    g2: LineSegment StartX=-21.25 StartY=14 StartZ=0 EndX=-20.5 EndY=14 EndZ=0
    g3: LineSegment StartX=-20.5 StartY=14 StartZ=0 EndX=-20.5 EndY=37 EndZ=0
  constraints (9):
    c: Coincident(g0,g1)
    c: Coincident(g1,g2)
    c: Coincident(g2,g3)
    c: Coincident(g3,g0)
    c: Horizontal(g0)
    c: Horizontal(g2)
    c: Vertical(g1)
    c: Vertical(g3)
    c: DistanceX(g0,g0) = 0.75
FEATURE [PartDesign::Pocket] Pocket003073  label="q1-leg002"
  BaseFeature = -> Hole002
  Length = 5
  Length2 = 100
  Profile = -> Sketch119
  Refine = true
  Type = 0
FEATURE [PartDesign::Body] Body014  label="Q1-base004"
  Group = -> [Sketch128,Pad012028,Sketch118,Sketch127,Pad012032,Pocket003077,Sketch126,Pocket003071,Sketch115,Pad012026,Sketch117,Pocket003070,Sketch123,Pad012036,Sketch124,Pad012025,Sketch129,Sketch112,Sketch113,Sketch122,Pad012034,Sketch109,Pad012030,Pocket003072,Pocket003079,Hole002,Sketch119,Pocket003073]
  Origin = -> Origin026
  Placement = pos=(0,0,44) rot=(0,0,1;1.5708rad)
  Tip = -> Pocket003073
FEATURE [PartDesign::Pad] Pad012030  label="servo_axis002"
  BaseFeature = -> Pad012034
  Length = 3
  Length2 = 100
  Profile = -> Sketch109
  Refine = true
  Type = 0
FEATURE [Sketcher::SketchObject] Sketch119  label="finger_hole002"
  ExternalGeometry = -> [Hole002]
  MapMode = 5
  Placement = pos=(2.5e-15,1.92674,-3.33722) rot=(1,0,0;3.66519rad)
  Support = -> [Hole002]
  sketch-geometry (2):
    g0: Circle CenterX=-8.2675 CenterY=-26.8039 CenterZ=0 NormalX=0 NormalY=0 NormalZ=1 AngleXU=0 Radius=6
    g1: LineSegment [constr] StartX=-8.2675 StartY=-11.1744 StartZ=0 EndX=-8.2675 EndY=-42.4334 EndZ=0
  constraints (7):
    c: Radius(g0) = 6
    c: PointOnObject(g1,g-3)
    c: PointOnObject(g1,g-4)
    c: Vertical(g1)
    c: PointOnObject(g0,g1)
    c: Symmetric(g-3,g-3,g1)
    c: Symmetric(g1,g1,g0)
FEATURE [PartDesign::Pad] Pad012034  label="back_wall005"
  BaseFeature = -> Pad012025
  Length = 1.75
  Length2 = 100
  Profile = -> Sketch112
  Refine = true
  Type = 0
FEATURE [Sketcher::SketchObject] Sketch122  label="cable_slot004"
  ExternalGeometry = -> [Pocket003072]
  MapMode = 5
  Placement = pos=(-3.873e-13,33.775,19.5) rot=(0,0.5,0.866025;3.14159rad)
  Support = -> [Pocket003072]
  sketch-geometry (4):
    g0: LineSegment StartX=20.25 StartY=3 StartZ=0 EndX=18.01 EndY=3 EndZ=0
    g1: LineSegment StartX=18.01 StartY=3 StartZ=0 EndX=18.01 EndY=12.5 EndZ=0
    g2: LineSegment StartX=18.01 StartY=12.5 StartZ=0 EndX=20.25 EndY=12.5 EndZ=0
    g3: LineSegment StartX=20.25 StartY=12.5 StartZ=0 EndX=20.25 EndY=3 EndZ=0
  constraints (11):
    c: Coincident(g0,g1)
    c: Coincident(g1,g2)
    c: Coincident(g2,g3)
    c: Coincident(g3,g0)
    c: Horizontal(g0)
    c: Horizontal(g2)
    c: Vertical(g1)
    c: Vertical(g3)
    c: DistanceX(g2,g2) = 2.24
    c: DistanceY(g1,g1) = 9.5
    c: DistanceX(g2,g-3) = 2
FEATURE [Sketcher::SketchObject] Sketch123  label="servo-walls002"
  ExternalGeometry = -> [Pocket003070]
  MapMode = 5
  Placement = pos=(2.152e-13,-5.82326,10.0862) rot=(1,0,0;0.523599rad)
  Support = -> [Pad012034]
  sketch-geometry (24):
    g0: LineSegment StartX=-5 StartY=42.4334 StartZ=0 EndX=-5 EndY=37 EndZ=0
    g1: LineSegment StartX=-5 StartY=37 StartZ=0 EndX=-20.5 EndY=37 EndZ=0
    g2: LineSegment StartX=-20.5 StartY=37 StartZ=0 EndX=-20.5 EndY=39 EndZ=0
    g3: LineSegment StartX=2 StartY=39 StartZ=0 EndX=2 EndY=37 EndZ=0
    g4: LineSegment StartX=2 StartY=37 StartZ=0 EndX=-1.60533 EndY=37 EndZ=0
    g5: LineSegment StartX=-1.60533 StartY=37 StartZ=0 EndX=-1.60533 EndY=42.4334 EndZ=0
    g6: LineSegment StartX=-20.5 StartY=39 StartZ=0 EndX=-7 EndY=39 EndZ=0
    g7: LineSegment StartX=-7 StartY=39 StartZ=0 EndX=-7 EndY=42.4334 EndZ=0
    g8: LineSegment StartX=-7 StartY=42.4334 StartZ=0 EndX=-5 EndY=42.4334 EndZ=0
    g9: LineSegment StartX=2 StartY=39 StartZ=0 EndX=0.5 EndY=39 EndZ=0
    g10: LineSegment StartX=0.5 StartY=39 StartZ=0 EndX=0.5 EndY=42.4334 EndZ=0
    g11: LineSegment StartX=-1.60533 StartY=42.4334 StartZ=0 EndX=0.5 EndY=42.4334 EndZ=0
    g12: LineSegment StartX=-5 StartY=9.5 StartZ=0 EndX=-5 EndY=14 EndZ=0
    g13: LineSegment StartX=-5 StartY=14 StartZ=0 EndX=-20.5 EndY=14 EndZ=0
    g14: LineSegment StartX=-20.5 StartY=14 StartZ=0 EndX=-20.5 EndY=12 EndZ=0
    g15: LineSegment StartX=2 StartY=12 StartZ=0 EndX=2 EndY=14 EndZ=0
    g16: LineSegment StartX=2 StartY=14 StartZ=0 EndX=-1.61532 EndY=14 EndZ=0
    g17: LineSegment StartX=-1.61532 StartY=14 StartZ=0 EndX=-1.61532 EndY=9.5 EndZ=0
    g18: LineSegment StartX=-20.5 StartY=12 StartZ=0 EndX=-7 EndY=12 EndZ=0
    g19: LineSegment StartX=-7 StartY=12 StartZ=0 EndX=-7 EndY=9.5 EndZ=0
    g20: LineSegment StartX=-7 StartY=9.5 StartZ=0 EndX=-5 EndY=9.5 EndZ=0
    g21: LineSegment StartX=2 StartY=12 StartZ=0 EndX=0.5 EndY=12 EndZ=0
    g22: LineSegment StartX=0.5 StartY=12 StartZ=0 EndX=0.5 EndY=9.5 EndZ=0
    g23: LineSegment StartX=-1.61532 StartY=9.5 StartZ=0 EndX=0.5 EndY=9.5 EndZ=0
  constraints (50):
    c: Coincident(g0,g1)
    c: Coincident(g1,g2)
    c: Horizontal(g1)
    c: Vertical(g0)
    c: Vertical(g2)
    c: Coincident(g3,g4)
    c: Coincident(g4,g5)
    c: Horizontal(g4)
    c: Vertical(g3)
    c: Vertical(g5)
    c: Coincident(g2,g6)
    c: Horizontal(g6)
    c: Coincident(g6,g7)
    c: Vertical(g7)
    c: PointOnObject(g7,g-3)
    c: PointOnObject(g0,g-3)
    c: Coincident(g8,g7)
    c: Coincident(g8,g0)
    c: Coincident(g3,g9)
    c: Horizontal(g9)
    c: Coincident(g9,g10)
    c: PointOnObject(g10,g-3)
    c: Vertical(g10)
    c: PointOnObject(g5,g-3)
    c: Coincident(g11,g5)
    c: Coincident(g11,g10)
    c: Coincident(g12,g13)
    c: Coincident(g13,g14)
    c: Horizontal(g13)
    c: Vertical(g12)
    c: Vertical(g14)
    c: Coincident(g15,g16)
    c: Coincident(g16,g17)
    c: Horizontal(g16)
    c: Vertical(g15)
    c: Vertical(g17)
    c: Coincident(g14,g18)
    c: Horizontal(g18)
    c: Coincident(g18,g19)
    c: Vertical(g19)
    c: Coincident(g19,g20)
    c: Coincident(g20,g12)
    c: Horizontal(g20)
    c: Coincident(g15,g21)
    c: Horizontal(g21)
    c: Coincident(g21,g22)
    c: Vertical(g22)
    c: Coincident(g17,g23)
    c: Coincident(g23,g22)
    c: Horizontal(g23)
FEATURE [App::Part] Part009  label="left_leg_1"
  Group = -> [Pocket003078,Fusion007060,Fusion007057,Body014,Fusion007059,Pocket003076,Fusion007058,Clone039,Fillet004,Body015]
  License = CC BY 3.0
  LicenseURL = http://creativecommons.org/licenses/by/3.0/
  Origin = -> Origin025
  Placement = pos=(-56.5,-52.5,0) rot=(0,0,1;0rad)
FEATURE [Sketcher::SketchObject] Sketch124  label="front_wall005"
  ExternalGeometry = -> [Pad012036]
  MapMode = 5
  Placement = pos=(2,0,0) rot=(0.57735,0.57735,0.57735;2.0944rad)
  Support = -> [Pad012036]
  sketch-geometry (9):
    g0: ArcOfCircle CenterX=18.4487 CenterY=16.9211 CenterZ=0 NormalX=0 NormalY=0 NormalZ=1 AngleXU=0 Radius=3.06832 StartAngle=3.68648 EndAngle=5.44463
    g1: LineSegment StartX=10.969 StartY=5.00105 StartZ=0 EndX=34.5617 EndY=18.1373 EndZ=0
    g2: LineSegment StartX=12.6837 StartY=20.7712 StartZ=0 EndX=4.56905 EndY=16.0862 EndZ=0
    g3: LineSegment StartX=4.56905 StartY=16.0862 StartZ=0 EndX=10.969 EndY=5.00105 EndZ=0
    g4: ArcOfCircle CenterX=24 CenterY=19.9888 CenterZ=0 NormalX=0 NormalY=0 NormalZ=1 AngleXU=0 Radius=6.3928 StartAngle=4.13303 EndAngle=7.03916
    g5: LineSegment StartX=28.6514 StartY=24.3743 StartZ=0 EndX=26.2197 EndY=28.5862 EndZ=0
    g6: LineSegment StartX=26.2197 StartY=28.5862 StartZ=0 EndX=27.9517 EndY=29.5862 EndZ=0
    g7: LineSegment StartX=27.9517 StartY=29.5862 StartZ=0 EndX=34.5617 EndY=18.1373 EndZ=0
    g8: LineSegment StartX=12.6837 StartY=20.7712 StartZ=0 EndX=15.8247 EndY=15.3307 EndZ=0
  constraints (20):
    c: Coincident(g3,g2)
    c: Parallel(g-7,g3)
    c: Coincident(g-7,g2)
    c: Coincident(g1,g3)
    c: Parallel(g-8,g2)
    c: Coincident(g4,g0)
    c: PointOnObject(g4,g-4)
    c: Coincident(g5,g4)
    c: Coincident(g5,g-5)
    c: Coincident(g5,g6)
    c: Coincident(g6,g-5)
    c: Coincident(g6,g7)
    c: Parallel(g-9,g7)
    c: Coincident(g7,g1)
    c: Coincident(g8,g2)
    c: Coincident(g8,g0)
    c: Perpendicular(g8,g2)
    c: Distance(g2) = 9.37
    c: Distance(g3) = 12.8
    c: Distance(g7) = 13.22
FEATURE [PartDesign::Pocket] Pocket003079  label="cable_slot005"
  BaseFeature = -> Pocket003072
  Length = 5
  Length2 = 100
  Profile = -> Sketch122
  Refine = true
  Type = 0
FEATURE [Sketcher::SketchObject] Sketch129  label="m2_screw_holes005"
  MapMode = 5
  Placement = pos=(-22.25,0,0) rot=(0.57735,-0.57735,-0.57735;2.0944rad)
  Support = -> [Pocket003079]
  sketch-geometry (2):
    g0: Circle CenterX=-31.1478 CenterY=24.1208 CenterZ=0 NormalX=0 NormalY=0 NormalZ=1 AngleXU=0 Radius=1.25
    g1: Circle CenterX=-7.61619 CenterY=10.5 CenterZ=0 NormalX=0 NormalY=0 NormalZ=1 AngleXU=0 Radius=1.25
  constraints (2):
    c: Radius(g0) = 1.25
    c: Equal(g0,g1) = 1.25
FEATURE [PartDesign::Pad] Pad012036  label="servo_walls002"
  BaseFeature = -> Pocket003070
  Length = 12.5
  Length2 = 100
  Profile = -> Sketch123
  Refine = true
  Type = 0
FEATURE [Part::Fillet] Fillet004  label="rounder_q1_servo002"
  Base = -> Clone039
  Edges = 1 edges r=8: [Edge27]
  Placement = pos=(0,0,44) rot=(0,0,1;1.5708rad)
FEATURE [PartDesign::FeatureBase] Clone039
  BaseFeature = -> Pocket003073
FEATURE [Sketcher::SketchObject] Sketch133  label="q2_axis003"
  MapMode = 5
  Placement = pos=(-22.25,0,0) rot=(0.57735,-0.57735,-0.57735;2.0944rad)
  Support = -> [Pad012046]
  sketch-geometry (1):
    g0: Circle CenterX=-24 CenterY=20 CenterZ=0 NormalX=0 NormalY=0 NormalZ=1 AngleXU=0 Radius=1.75
  constraints (1):
    c: Radius(g0) = 1.75
FEATURE [Sketcher::SketchObject] Sketch134  label="servo_tollerance006"
  MapMode = 5
  Placement = pos=(2.152e-13,-5.82326,10.0862) rot=(1,0,0;0.523599rad)
  Support = -> [Pad012048]
  sketch-geometry (4):
    g0: LineSegment StartX=-20.5 StartY=37 StartZ=0 EndX=-21.25 EndY=37 EndZ=0
    g1: LineSegment StartX=-21.25 StartY=37 StartZ=0 EndX=-21.25 EndY=14 EndZ=0
    g2: LineSegment StartX=-21.25 StartY=14 StartZ=0 EndX=-20.5 EndY=14 EndZ=0
    g3: LineSegment StartX=-20.5 StartY=14 StartZ=0 EndX=-20.5 EndY=37 EndZ=0
  constraints (9):
    c: Coincident(g0,g1)
    c: Coincident(g1,g2)
    c: Coincident(g2,g3)
    c: Coincident(g3,g0)
    c: Horizontal(g0)
    c: Horizontal(g2)
    c: Vertical(g1)
    c: Vertical(g3)
    c: DistanceX(g0,g0) = 0.75
FEATURE [PartDesign::Body] Body016  label="Q1-base005"
  Group = -> [Sketch151,Pad012041,Sketch141,Sketch140,Pad012043,Pocket003084,Sketch149,Pocket003088,Sketch150,Pad012045,Sketch155,Pocket003081,Sketch137,Pad012042,Sketch154,Pad012040,Sketch153,Sketch139,Sketch134,Sketch146,Pad012046,Sketch133,Pad012048,Pocket003085,Pocket003082,Hole003,Sketch147,Pocket003089]
  Origin = -> Origin028
  Placement = pos=(0,0,44) rot=(0,0,1;1.5708rad)
  Tip = -> Pocket003089
FEATURE [PartDesign::Pad] Pad012040  label="front_wall006"
  BaseFeature = -> Pad012042
  Length = 3.715
  Length2 = 100
  Profile = -> Sketch154
  Refine = true
  Type = 0
FEATURE [PartDesign::FeatureBase] Clone040
  BaseFeature = -> Pocket003089
FEATURE [Sketcher::SketchObject] Sketch137  label="servo-walls003"
  ExternalGeometry = -> [Pocket003081]
  MapMode = 5
  Placement = pos=(2.152e-13,-5.82326,10.0862) rot=(1,0,0;0.523599rad)
  Support = -> [Pad012046]
  sketch-geometry (24):
    g0: LineSegment StartX=-5 StartY=42.4334 StartZ=0 EndX=-5 EndY=37 EndZ=0
    g1: LineSegment StartX=-5 StartY=37 StartZ=0 EndX=-20.5 EndY=37 EndZ=0
    g2: LineSegment StartX=-20.5 StartY=37 StartZ=0 EndX=-20.5 EndY=39 EndZ=0
    g3: LineSegment StartX=2 StartY=39 StartZ=0 EndX=2 EndY=37 EndZ=0
    g4: LineSegment StartX=2 StartY=37 StartZ=0 EndX=-1.60533 EndY=37 EndZ=0
    g5: LineSegment StartX=-1.60533 StartY=37 StartZ=0 EndX=-1.60533 EndY=42.4334 EndZ=0
    g6: LineSegment StartX=-20.5 StartY=39 StartZ=0 EndX=-7 EndY=39 EndZ=0
    g7: LineSegment StartX=-7 StartY=39 StartZ=0 EndX=-7 EndY=42.4334 EndZ=0
    g8: LineSegment StartX=-7 StartY=42.4334 StartZ=0 EndX=-5 EndY=42.4334 EndZ=0
    g9: LineSegment StartX=2 StartY=39 StartZ=0 EndX=0.5 EndY=39 EndZ=0
    g10: LineSegment StartX=0.5 StartY=39 StartZ=0 EndX=0.5 EndY=42.4334 EndZ=0
    g11: LineSegment StartX=-1.60533 StartY=42.4334 StartZ=0 EndX=0.5 EndY=42.4334 EndZ=0
    g12: LineSegment StartX=-5 StartY=9.5 StartZ=0 EndX=-5 EndY=14 EndZ=0
    g13: LineSegment StartX=-5 StartY=14 StartZ=0 EndX=-20.5 EndY=14 EndZ=0
    g14: LineSegment StartX=-20.5 StartY=14 StartZ=0 EndX=-20.5 EndY=12 EndZ=0
    g15: LineSegment StartX=2 StartY=12 StartZ=0 EndX=2 EndY=14 EndZ=0
    g16: LineSegment StartX=2 StartY=14 StartZ=0 EndX=-1.61532 EndY=14 EndZ=0
    g17: LineSegment StartX=-1.61532 StartY=14 StartZ=0 EndX=-1.61532 EndY=9.5 EndZ=0
    g18: LineSegment StartX=-20.5 StartY=12 StartZ=0 EndX=-7 EndY=12 EndZ=0
    g19: LineSegment StartX=-7 StartY=12 StartZ=0 EndX=-7 EndY=9.5 EndZ=0
    g20: LineSegment StartX=-7 StartY=9.5 StartZ=0 EndX=-5 EndY=9.5 EndZ=0
    g21: LineSegment StartX=2 StartY=12 StartZ=0 EndX=0.5 EndY=12 EndZ=0
    g22: LineSegment StartX=0.5 StartY=12 StartZ=0 EndX=0.5 EndY=9.5 EndZ=0
    g23: LineSegment StartX=-1.61532 StartY=9.5 StartZ=0 EndX=0.5 EndY=9.5 EndZ=0
  constraints (50):
    c: Coincident(g0,g1)
    c: Coincident(g1,g2)
    c: Horizontal(g1)
    c: Vertical(g0)
    c: Vertical(g2)
    c: Coincident(g3,g4)
    c: Coincident(g4,g5)
    c: Horizontal(g4)
    c: Vertical(g3)
    c: Vertical(g5)
    c: Coincident(g2,g6)
    c: Horizontal(g6)
    c: Coincident(g6,g7)
    c: Vertical(g7)
    c: PointOnObject(g7,g-3)
    c: PointOnObject(g0,g-3)
    c: Coincident(g8,g7)
    c: Coincident(g8,g0)
    c: Coincident(g3,g9)
    c: Horizontal(g9)
    c: Coincident(g9,g10)
    c: PointOnObject(g10,g-3)
    c: Vertical(g10)
    c: PointOnObject(g5,g-3)
    c: Coincident(g11,g5)
    c: Coincident(g11,g10)
    c: Coincident(g12,g13)
    c: Coincident(g13,g14)
    c: Horizontal(g13)
    c: Vertical(g12)
    c: Vertical(g14)
    c: Coincident(g15,g16)
    c: Coincident(g16,g17)
    c: Horizontal(g16)
    c: Vertical(g15)
    c: Vertical(g17)
    c: Coincident(g14,g18)
    c: Horizontal(g18)
    c: Coincident(g18,g19)
    c: Vertical(g19)
    c: Coincident(g19,g20)
    c: Coincident(g20,g12)
    c: Horizontal(g20)
    c: Coincident(g15,g21)
    c: Horizontal(g21)
    c: Coincident(g21,g22)
    c: Vertical(g22)
    c: Coincident(g17,g23)
    c: Coincident(g23,g22)
    c: Horizontal(g23)
FEATURE [PartDesign::Hole] Hole003  label="m2_screw_holes006"
  BaseFeature = -> Pocket003082
  Depth = 35
  DepthType = 0
  Diameter = 2.5
  DrillPoint = 1
  DrillPointAngle = 118
  HoleCutCountersinkAngle = 90
  HoleCutDepth = 0
  HoleCutDiameter = 0
  HoleCutType = 0
  ModelActualThread = false
  Profile = -> Sketch153
  Refine = true
  Tapered = false
  TaperedAngle = 90
  ThreadAngle = 0
  ThreadClass = 0
  ThreadCutOffInner = 0
  ThreadCutOffOuter = 0
  ThreadDirection = 0
  ThreadFit = 0
  ThreadPitch = 0
  ThreadSize = 0
  ThreadType = 0
  Threaded = false
FEATURE [PartDesign::Pocket] Pocket003082  label="cable_slot006"
  BaseFeature = -> Pocket003085
  Length = 5
  Length2 = 100
  Profile = -> Sketch146
  Refine = true
  Type = 0
FEATURE [App::Part] Part010  label="left_leg_002"
  Group = -> [Pocket003086,Fusion007064,Fusion007062,Body016,Fusion007063,Pocket003087,Fusion007061,Clone040,Fillet005,Body017,Clone036Body001]
  License = CC BY 3.0
  LicenseURL = http://creativecommons.org/licenses/by/3.0/
  Origin = -> Origin030
  Placement = pos=(-56.5,-17.5,0) rot=(0,0,1;0rad)
FEATURE [PartDesign::Pad] Pad012042  label="servo_walls003"
  BaseFeature = -> Pocket003081
  Length = 12.5
  Length2 = 100
  Profile = -> Sketch137
  Refine = true
  Type = 0
FEATURE [Sketcher::SketchObject] Sketch139  label="back_wall006"
  ExternalGeometry = -> [Pad012040]
  MapMode = 5
  Placement = pos=(-20.5,0,0) rot=(0.57735,-0.57735,-0.57735;2.0944rad)
  Support = -> [Pad012040]
  sketch-geometry (9):
    g0: LineSegment StartX=5.71497 StartY=2.25 StartZ=0 EndX=-11.6041 EndY=2.25 EndZ=0
    g1: LineSegment StartX=-11.6041 StartY=2.25 StartZ=0 EndX=-38.6752 EndY=17.8795 EndZ=0
    g2: LineSegment StartX=-38.6752 StartY=17.8795 StartZ=0 EndX=-37.1752 EndY=20.4776 EndZ=0
    g3: LineSegment StartX=-37.1752 StartY=20.4776 StartZ=0 EndX=-34.2017 EndY=18.7609 EndZ=0
    g4: LineSegment StartX=-34.2017 StartY=18.7609 StartZ=0 EndX=-27.9517 EndY=29.5862 EndZ=0
    g5: LineSegment StartX=-27.9517 StartY=29.5862 StartZ=0 EndX=-4.56905 EndY=16.0862 EndZ=0
    g6: LineSegment StartX=-4.56905 StartY=16.0862 StartZ=0 EndX=-10.5379 EndY=5.74787 EndZ=0
    g7: LineSegment StartX=-10.5379 StartY=5.74787 StartZ=0 EndX=5.71497 EndY=5.75 EndZ=0
    g8: LineSegment StartX=5.71497 StartY=5.75 StartZ=0 EndX=5.71497 EndY=2.25 EndZ=0
  constraints (18):
    c: Coincident(g-11,g0)
    c: Coincident(g0,g-11)
    c: Coincident(g0,g1)
    c: Coincident(g1,g-4)
    c: Coincident(g1,g2)
    c: Coincident(g2,g-5)
    c: Coincident(g2,g3)
    c: Coincident(g3,g-6)
    c: Coincident(g3,g4)
    c: Coincident(g4,g-6)
    c: Coincident(g4,g5)
    c: Coincident(g5,g-7)
    c: Coincident(g5,g6)
    c: Coincident(g6,g-8)
    c: Coincident(g6,g7)
    c: Coincident(g7,g-10)
    c: Coincident(g7,g8)
    c: Coincident(g8,g0)
FEATURE [PartDesign::Pad] Pad012046  label="back_wall007"
  BaseFeature = -> Pad012040
  Length = 1.75
  Length2 = 100
  Profile = -> Sketch139
  Refine = true
  Type = 0
FEATURE [PartDesign::Pocket] Pocket003085  label="servo_tollerance007"
  BaseFeature = -> Pad012048
  Length = 12.5
  Length2 = 100
  Profile = -> Sketch134
  Refine = true
  Type = 0
FEATURE [Sketcher::SketchObject] Sketch146  label="cable_slot007"
  ExternalGeometry = -> [Pocket003085]
  MapMode = 5
  Placement = pos=(-3.873e-13,33.775,19.5) rot=(0,0.5,0.866025;3.14159rad)
  Support = -> [Pocket003085]
  sketch-geometry (4):
    g0: LineSegment StartX=20.25 StartY=3 StartZ=0 EndX=18.01 EndY=3 EndZ=0
    g1: LineSegment StartX=18.01 StartY=3 StartZ=0 EndX=18.01 EndY=12.5 EndZ=0
    g2: LineSegment StartX=18.01 StartY=12.5 StartZ=0 EndX=20.25 EndY=12.5 EndZ=0
    g3: LineSegment StartX=20.25 StartY=12.5 StartZ=0 EndX=20.25 EndY=3 EndZ=0
  constraints (11):
    c: Coincident(g0,g1)
    c: Coincident(g1,g2)
    c: Coincident(g2,g3)
    c: Coincident(g3,g0)
    c: Horizontal(g0)
    c: Horizontal(g2)
    c: Vertical(g1)
    c: Vertical(g3)
    c: DistanceX(g2,g2) = 2.24
    c: DistanceY(g1,g1) = 9.5
    c: DistanceX(g2,g-3) = 2
FEATURE [Sketcher::SketchObject] Sketch147  label="finger_hole003"
  ExternalGeometry = -> [Hole003]
  MapMode = 5
  Placement = pos=(2.5e-15,1.92674,-3.33722) rot=(1,0,0;3.66519rad)
  Support = -> [Hole003]
  sketch-geometry (2):
    g0: Circle CenterX=-8.2675 CenterY=-26.8039 CenterZ=0 NormalX=0 NormalY=0 NormalZ=1 AngleXU=0 Radius=6
    g1: LineSegment [constr] StartX=-8.2675 StartY=-11.1744 StartZ=0 EndX=-8.2675 EndY=-42.4334 EndZ=0
  constraints (7):
    c: Radius(g0) = 6
    c: PointOnObject(g1,g-3)
    c: PointOnObject(g1,g-4)
    c: Vertical(g1)
    c: PointOnObject(g0,g1)
    c: Symmetric(g-3,g-3,g1)
    c: Symmetric(g1,g1,g0)
FEATURE [Part::Fillet] Fillet005  label="rounder_q1_servo003"
  Base = -> Clone040
  Edges = 1 edges r=8: [Edge27]
  Placement = pos=(0,0,44) rot=(0,0,1;1.5708rad)
FEATURE [Sketcher::SketchObject] Sketch153  label="m2_screw_holes007"
  MapMode = 5
  Placement = pos=(-22.25,0,0) rot=(0.57735,-0.57735,-0.57735;2.0944rad)
  Support = -> [Pocket003082]
  sketch-geometry (2):
    g0: Circle CenterX=-31.1478 CenterY=24.1208 CenterZ=0 NormalX=0 NormalY=0 NormalZ=1 AngleXU=0 Radius=1.25
    g1: Circle CenterX=-7.61619 CenterY=10.5 CenterZ=0 NormalX=0 NormalY=0 NormalZ=1 AngleXU=0 Radius=1.25
  constraints (2):
    c: Radius(g0) = 1.25
    c: Equal(g0,g1) = 1.25
FEATURE [PartDesign::Pad] Pad012048  label="servo_axis003"
  BaseFeature = -> Pad012046
  Length = 3
  Length2 = 100
  Profile = -> Sketch133
  Refine = true
  Type = 0
FEATURE [Sketcher::SketchObject] Sketch154  label="front_wall007"
  ExternalGeometry = -> [Pad012042]
  MapMode = 5
  Placement = pos=(2,0,0) rot=(0.57735,0.57735,0.57735;2.0944rad)
  Support = -> [Pad012042]
  sketch-geometry (9):
    g0: ArcOfCircle CenterX=18.4487 CenterY=16.9211 CenterZ=0 NormalX=0 NormalY=0 NormalZ=1 AngleXU=0 Radius=3.06832 StartAngle=3.68648 EndAngle=5.44463
    g1: LineSegment StartX=10.969 StartY=5.00105 StartZ=0 EndX=34.5617 EndY=18.1373 EndZ=0
    g2: LineSegment StartX=12.6837 StartY=20.7712 StartZ=0 EndX=4.56905 EndY=16.0862 EndZ=0
    g3: LineSegment StartX=4.56905 StartY=16.0862 StartZ=0 EndX=10.969 EndY=5.00105 EndZ=0
    g4: ArcOfCircle CenterX=24 CenterY=19.9888 CenterZ=0 NormalX=0 NormalY=0 NormalZ=1 AngleXU=0 Radius=6.3928 StartAngle=4.13303 EndAngle=7.03916
    g5: LineSegment StartX=28.6514 StartY=24.3743 StartZ=0 EndX=26.2197 EndY=28.5862 EndZ=0
    g6: LineSegment StartX=26.2197 StartY=28.5862 StartZ=0 EndX=27.9517 EndY=29.5862 EndZ=0
    g7: LineSegment StartX=27.9517 StartY=29.5862 StartZ=0 EndX=34.5617 EndY=18.1373 EndZ=0
    g8: LineSegment StartX=12.6837 StartY=20.7712 StartZ=0 EndX=15.8247 EndY=15.3307 EndZ=0
  constraints (20):
    c: Coincident(g3,g2)
    c: Parallel(g-7,g3)
    c: Coincident(g-7,g2)
    c: Coincident(g1,g3)
    c: Parallel(g-8,g2)
    c: Coincident(g4,g0)
    c: PointOnObject(g4,g-4)
    c: Coincident(g5,g4)
    c: Coincident(g5,g-5)
    c: Coincident(g5,g6)
    c: Coincident(g6,g-5)
    c: Coincident(g6,g7)
    c: Parallel(g-9,g7)
    c: Coincident(g7,g1)
    c: Coincident(g8,g2)
    c: Coincident(g8,g0)
    c: Perpendicular(g8,g2)
    c: Distance(g2) = 9.37
    c: Distance(g3) = 12.8
    c: Distance(g7) = 13.22
FEATURE [PartDesign::Pocket] Pocket003089  label="q1-leg003"
  BaseFeature = -> Hole003
  Length = 5
  Length2 = 100
  Profile = -> Sketch147
  Refine = true
  Type = 0
FEATURE [PartDesign::Hole] Hole004  label="m2_screw_holes008"
  BaseFeature = -> Pocket003091
  Depth = 35
  DepthType = 0
  Diameter = 2.5
  DrillPoint = 1
  DrillPointAngle = 118
  HoleCutCountersinkAngle = 90
  HoleCutDepth = 0
  HoleCutDiameter = 0
  HoleCutType = 0
  ModelActualThread = false
  Profile = -> Sketch177
  Refine = true
  Tapered = false
  TaperedAngle = 90
  ThreadAngle = 0
  ThreadClass = 0
  ThreadCutOffInner = 0
  ThreadCutOffOuter = 0
  ThreadDirection = 0
  ThreadFit = 0
  ThreadPitch = 0
  ThreadSize = 0
  ThreadType = 0
  Threaded = false
FEATURE [App::Part] Part011  label="left_leg_003"
  Group = -> [Pocket003093,Fusion007066,Fusion007067,Body018,Fusion007065,Pocket003092,Fusion007068,Clone041,Fillet006,Body019]
  License = CC BY 3.0
  LicenseURL = http://creativecommons.org/licenses/by/3.0/
  Origin = -> Origin032
  Placement = pos=(-56.5,17.5,0) rot=(0,0,1;0rad)
FEATURE [Sketcher::SketchObject] Sketch158  label="servo_tollerance008"
  MapMode = 5
  Placement = pos=(2.152e-13,-5.82326,10.0862) rot=(1,0,0;0.523599rad)
  Support = -> [Pad012060]
  sketch-geometry (4):
    g0: LineSegment StartX=-20.5 StartY=37 StartZ=0 EndX=-21.25 EndY=37 EndZ=0
    g1: LineSegment StartX=-21.25 StartY=37 StartZ=0 EndX=-21.25 EndY=14 EndZ=0
    g2: LineSegment StartX=-21.25 StartY=14 StartZ=0 EndX=-20.5 EndY=14 EndZ=0
    g3: LineSegment StartX=-20.5 StartY=14 StartZ=0 EndX=-20.5 EndY=37 EndZ=0
  constraints (9):
    c: Coincident(g0,g1)
    c: Coincident(g1,g2)
    c: Coincident(g2,g3)
    c: Coincident(g3,g0)
    c: Horizontal(g0)
    c: Horizontal(g2)
    c: Vertical(g1)
    c: Vertical(g3)
    c: DistanceX(g0,g0) = 0.75
FEATURE [Sketcher::SketchObject] Sketch159  label="back_wall008"
  ExternalGeometry = -> [Pad012053]
  MapMode = 5
  Placement = pos=(-20.5,0,0) rot=(0.57735,-0.57735,-0.57735;2.0944rad)
  Support = -> [Pad012053]
  sketch-geometry (9):
    g0: LineSegment StartX=5.71497 StartY=2.25 StartZ=0 EndX=-11.6041 EndY=2.25 EndZ=0
    g1: LineSegment StartX=-11.6041 StartY=2.25 StartZ=0 EndX=-38.6752 EndY=17.8795 EndZ=0
    g2: LineSegment StartX=-38.6752 StartY=17.8795 StartZ=0 EndX=-37.1752 EndY=20.4776 EndZ=0
    g3: LineSegment StartX=-37.1752 StartY=20.4776 StartZ=0 EndX=-34.2017 EndY=18.7609 EndZ=0
    g4: LineSegment StartX=-34.2017 StartY=18.7609 StartZ=0 EndX=-27.9517 EndY=29.5862 EndZ=0
    g5: LineSegment StartX=-27.9517 StartY=29.5862 StartZ=0 EndX=-4.56905 EndY=16.0862 EndZ=0
    g6: LineSegment StartX=-4.56905 StartY=16.0862 StartZ=0 EndX=-10.5379 EndY=5.74787 EndZ=0
    g7: LineSegment StartX=-10.5379 StartY=5.74787 StartZ=0 EndX=5.71497 EndY=5.75 EndZ=0
    g8: LineSegment StartX=5.71497 StartY=5.75 StartZ=0 EndX=5.71497 EndY=2.25 EndZ=0
  constraints (18):
    c: Coincident(g-11,g0)
    c: Coincident(g0,g-11)
    c: Coincident(g0,g1)
    c: Coincident(g1,g-4)
    c: Coincident(g1,g2)
    c: Coincident(g2,g-5)
    c: Coincident(g2,g3)
    c: Coincident(g3,g-6)
    c: Coincident(g3,g4)
    c: Coincident(g4,g-6)
    c: Coincident(g4,g5)
    c: Coincident(g5,g-7)
    c: Coincident(g5,g6)
    c: Coincident(g6,g-8)
    c: Coincident(g6,g7)
    c: Coincident(g7,g-10)
    c: Coincident(g7,g8)
    c: Coincident(g8,g0)
FEATURE [Part::Fillet] Fillet006  label="rounder_q1_servo004"
  Base = -> Clone041
  Edges = 1 edges r=8: [Edge27]
  Placement = pos=(0,0,44) rot=(0,0,1;1.5708rad)
FEATURE [PartDesign::Pocket] Pocket003091  label="cable_slot008"
  BaseFeature = -> Pocket003095
  Length = 5
  Length2 = 100
  Profile = -> Sketch170
  Refine = true
  Type = 0
FEATURE [PartDesign::Pad] Pad012051  label="servo_walls004"
  BaseFeature = -> Pocket003097
  Length = 12.5
  Length2 = 100
  Profile = -> Sketch168
  Refine = true
  Type = 0
FEATURE [Sketcher::SketchObject] Sketch164  label="q2_axis004"
  MapMode = 5
  Placement = pos=(-22.25,0,0) rot=(0.57735,-0.57735,-0.57735;2.0944rad)
  Support = -> [Pad012057]
  sketch-geometry (1):
    g0: Circle CenterX=-24 CenterY=20 CenterZ=0 NormalX=0 NormalY=0 NormalZ=1 AngleXU=0 Radius=1.75
  constraints (1):
    c: Radius(g0) = 1.75
FEATURE [PartDesign::Pad] Pad012053  label="front_wall008"
  BaseFeature = -> Pad012051
  Length = 3.715
  Length2 = 100
  Profile = -> Sketch180
  Refine = true
  Type = 0
FEATURE [Sketcher::SketchObject] Sketch168  label="servo-walls004"
  ExternalGeometry = -> [Pocket003097]
  MapMode = 5
  Placement = pos=(2.152e-13,-5.82326,10.0862) rot=(1,0,0;0.523599rad)
  Support = -> [Pad012057]
  sketch-geometry (24):
    g0: LineSegment StartX=-5 StartY=42.4334 StartZ=0 EndX=-5 EndY=37 EndZ=0
    g1: LineSegment StartX=-5 StartY=37 StartZ=0 EndX=-20.5 EndY=37 EndZ=0
    g2: LineSegment StartX=-20.5 StartY=37 StartZ=0 EndX=-20.5 EndY=39 EndZ=0
    g3: LineSegment StartX=2 StartY=39 StartZ=0 EndX=2 EndY=37 EndZ=0
    g4: LineSegment StartX=2 StartY=37 StartZ=0 EndX=-1.60533 EndY=37 EndZ=0
    g5: LineSegment StartX=-1.60533 StartY=37 StartZ=0 EndX=-1.60533 EndY=42.4334 EndZ=0
    g6: LineSegment StartX=-20.5 StartY=39 StartZ=0 EndX=-7 EndY=39 EndZ=0
    g7: LineSegment StartX=-7 StartY=39 StartZ=0 EndX=-7 EndY=42.4334 EndZ=0
    g8: LineSegment StartX=-7 StartY=42.4334 StartZ=0 EndX=-5 EndY=42.4334 EndZ=0
    g9: LineSegment StartX=2 StartY=39 StartZ=0 EndX=0.5 EndY=39 EndZ=0
    g10: LineSegment StartX=0.5 StartY=39 StartZ=0 EndX=0.5 EndY=42.4334 EndZ=0
    g11: LineSegment StartX=-1.60533 StartY=42.4334 StartZ=0 EndX=0.5 EndY=42.4334 EndZ=0
    g12: LineSegment StartX=-5 StartY=9.5 StartZ=0 EndX=-5 EndY=14 EndZ=0
    g13: LineSegment StartX=-5 StartY=14 StartZ=0 EndX=-20.5 EndY=14 EndZ=0
    g14: LineSegment StartX=-20.5 StartY=14 StartZ=0 EndX=-20.5 EndY=12 EndZ=0
    g15: LineSegment StartX=2 StartY=12 StartZ=0 EndX=2 EndY=14 EndZ=0
    g16: LineSegment StartX=2 StartY=14 StartZ=0 EndX=-1.61532 EndY=14 EndZ=0
    g17: LineSegment StartX=-1.61532 StartY=14 StartZ=0 EndX=-1.61532 EndY=9.5 EndZ=0
    g18: LineSegment StartX=-20.5 StartY=12 StartZ=0 EndX=-7 EndY=12 EndZ=0
    g19: LineSegment StartX=-7 StartY=12 StartZ=0 EndX=-7 EndY=9.5 EndZ=0
    g20: LineSegment StartX=-7 StartY=9.5 StartZ=0 EndX=-5 EndY=9.5 EndZ=0
    g21: LineSegment StartX=2 StartY=12 StartZ=0 EndX=0.5 EndY=12 EndZ=0
    g22: LineSegment StartX=0.5 StartY=12 StartZ=0 EndX=0.5 EndY=9.5 EndZ=0
    g23: LineSegment StartX=-1.61532 StartY=9.5 StartZ=0 EndX=0.5 EndY=9.5 EndZ=0
  constraints (50):
    c: Coincident(g0,g1)
    c: Coincident(g1,g2)
    c: Horizontal(g1)
    c: Vertical(g0)
    c: Vertical(g2)
    c: Coincident(g3,g4)
    c: Coincident(g4,g5)
    c: Horizontal(g4)
    c: Vertical(g3)
    c: Vertical(g5)
    c: Coincident(g2,g6)
    c: Horizontal(g6)
    c: Coincident(g6,g7)
    c: Vertical(g7)
    c: PointOnObject(g7,g-3)
    c: PointOnObject(g0,g-3)
    c: Coincident(g8,g7)
    c: Coincident(g8,g0)
    c: Coincident(g3,g9)
    c: Horizontal(g9)
    c: Coincident(g9,g10)
    c: PointOnObject(g10,g-3)
    c: Vertical(g10)
    c: PointOnObject(g5,g-3)
    c: Coincident(g11,g5)
    c: Coincident(g11,g10)
    c: Coincident(g12,g13)
    c: Coincident(g13,g14)
    c: Horizontal(g13)
    c: Vertical(g12)
    c: Vertical(g14)
    c: Coincident(g15,g16)
    c: Coincident(g16,g17)
    c: Horizontal(g16)
    c: Vertical(g15)
    c: Vertical(g17)
    c: Coincident(g14,g18)
    c: Horizontal(g18)
    c: Coincident(g18,g19)
    c: Vertical(g19)
    c: Coincident(g19,g20)
    c: Coincident(g20,g12)
    c: Horizontal(g20)
    c: Coincident(g15,g21)
    c: Horizontal(g21)
    c: Coincident(g21,g22)
    c: Vertical(g22)
    c: Coincident(g17,g23)
    c: Coincident(g23,g22)
    c: Horizontal(g23)
FEATURE [PartDesign::Pad] Pad012057  label="back_wall009"
  BaseFeature = -> Pad012053
  Length = 1.75
  Length2 = 100
  Profile = -> Sketch159
  Refine = true
  Type = 0
FEATURE [PartDesign::Pocket] Pocket003095  label="servo_tollerance009"
  BaseFeature = -> Pad012060
  Length = 12.5
  Length2 = 100
  Profile = -> Sketch158
  Refine = true
  Type = 0
FEATURE [Sketcher::SketchObject] Sketch170  label="cable_slot009"
  ExternalGeometry = -> [Pocket003095]
  MapMode = 5
  Placement = pos=(-3.873e-13,33.775,19.5) rot=(0,0.5,0.866025;3.14159rad)
  Support = -> [Pocket003095]
  sketch-geometry (4):
    g0: LineSegment StartX=20.25 StartY=3 StartZ=0 EndX=18.01 EndY=3 EndZ=0
    g1: LineSegment StartX=18.01 StartY=3 StartZ=0 EndX=18.01 EndY=12.5 EndZ=0
    g2: LineSegment StartX=18.01 StartY=12.5 StartZ=0 EndX=20.25 EndY=12.5 EndZ=0
    g3: LineSegment StartX=20.25 StartY=12.5 StartZ=0 EndX=20.25 EndY=3 EndZ=0
  constraints (11):
    c: Coincident(g0,g1)
    c: Coincident(g1,g2)
    c: Coincident(g2,g3)
    c: Coincident(g3,g0)
    c: Horizontal(g0)
    c: Horizontal(g2)
    c: Vertical(g1)
    c: Vertical(g3)
    c: DistanceX(g2,g2) = 2.24
    c: DistanceY(g1,g1) = 9.5
    c: DistanceX(g2,g-3) = 2
FEATURE [Sketcher::SketchObject] Sketch171  label="finger_hole004"
  ExternalGeometry = -> [Hole004]
  MapMode = 5
  Placement = pos=(2.5e-15,1.92674,-3.33722) rot=(1,0,0;3.66519rad)
  Support = -> [Hole004]
  sketch-geometry (2):
    g0: Circle CenterX=-8.2675 CenterY=-26.8039 CenterZ=0 NormalX=0 NormalY=0 NormalZ=1 AngleXU=0 Radius=6
    g1: LineSegment [constr] StartX=-8.2675 StartY=-11.1744 StartZ=0 EndX=-8.2675 EndY=-42.4334 EndZ=0
  constraints (7):
    c: Radius(g0) = 6
    c: PointOnObject(g1,g-3)
    c: PointOnObject(g1,g-4)
    c: Vertical(g1)
    c: PointOnObject(g0,g1)
    c: Symmetric(g-3,g-3,g1)
    c: Symmetric(g1,g1,g0)
FEATURE [Sketcher::SketchObject] Sketch177  label="m2_screw_holes009"
  MapMode = 5
  Placement = pos=(-22.25,0,0) rot=(0.57735,-0.57735,-0.57735;2.0944rad)
  Support = -> [Pocket003091]
  sketch-geometry (2):
    g0: Circle CenterX=-31.1478 CenterY=24.1208 CenterZ=0 NormalX=0 NormalY=0 NormalZ=1 AngleXU=0 Radius=1.25
    g1: Circle CenterX=-7.61619 CenterY=10.5 CenterZ=0 NormalX=0 NormalY=0 NormalZ=1 AngleXU=0 Radius=1.25
  constraints (2):
    c: Radius(g0) = 1.25
    c: Equal(g0,g1) = 1.25
FEATURE [PartDesign::Body] Body018  label="Q1-base006"
  Group = -> [Sketch175,Pad012050,Sketch161,Sketch160,Pad012054,Pocket003094,Sketch173,Pocket003096,Sketch174,Pad012056,Sketch181,Pocket003097,Sketch168,Pad012051,Sketch180,Pad012053,Sketch177,Sketch159,Sketch158,Sketch170,Pad012057,Sketch164,Pad012060,Pocket003095,Pocket003091,Hole004,Sketch171,Pocket003099]
  Origin = -> Origin033
  Placement = pos=(0,0,44) rot=(0,0,1;1.5708rad)
  Tip = -> Pocket003099
FEATURE [PartDesign::FeatureBase] Clone041
  BaseFeature = -> Pocket003099
FEATURE [PartDesign::Pad] Pad012060  label="servo_axis004"
  BaseFeature = -> Pad012057
  Length = 3
  Length2 = 100
  Profile = -> Sketch164
  Refine = true
  Type = 0
FEATURE [Sketcher::SketchObject] Sketch180  label="front_wall009"
  ExternalGeometry = -> [Pad012051]
  MapMode = 5
  Placement = pos=(2,0,0) rot=(0.57735,0.57735,0.57735;2.0944rad)
  Support = -> [Pad012051]
  sketch-geometry (9):
    g0: ArcOfCircle CenterX=18.4487 CenterY=16.9211 CenterZ=0 NormalX=0 NormalY=0 NormalZ=1 AngleXU=0 Radius=3.06832 StartAngle=3.68648 EndAngle=5.44463
    g1: LineSegment StartX=10.969 StartY=5.00105 StartZ=0 EndX=34.5617 EndY=18.1373 EndZ=0
    g2: LineSegment StartX=12.6837 StartY=20.7712 StartZ=0 EndX=4.56905 EndY=16.0862 EndZ=0
    g3: LineSegment StartX=4.56905 StartY=16.0862 StartZ=0 EndX=10.969 EndY=5.00105 EndZ=0
    g4: ArcOfCircle CenterX=24 CenterY=19.9888 CenterZ=0 NormalX=0 NormalY=0 NormalZ=1 AngleXU=0 Radius=6.3928 StartAngle=4.13303 EndAngle=7.03916
    g5: LineSegment StartX=28.6514 StartY=24.3743 StartZ=0 EndX=26.2197 EndY=28.5862 EndZ=0
    g6: LineSegment StartX=26.2197 StartY=28.5862 StartZ=0 EndX=27.9517 EndY=29.5862 EndZ=0
    g7: LineSegment StartX=27.9517 StartY=29.5862 StartZ=0 EndX=34.5617 EndY=18.1373 EndZ=0
    g8: LineSegment StartX=12.6837 StartY=20.7712 StartZ=0 EndX=15.8247 EndY=15.3307 EndZ=0
  constraints (20):
    c: Coincident(g3,g2)
    c: Parallel(g-7,g3)
    c: Coincident(g-7,g2)
    c: Coincident(g1,g3)
    c: Parallel(g-8,g2)
    c: Coincident(g4,g0)
    c: PointOnObject(g4,g-4)
    c: Coincident(g5,g4)
    c: Coincident(g5,g-5)
    c: Coincident(g5,g6)
    c: Coincident(g6,g-5)
    c: Coincident(g6,g7)
    c: Parallel(g-9,g7)
    c: Coincident(g7,g1)
    c: Coincident(g8,g2)
    c: Coincident(g8,g0)
    c: Perpendicular(g8,g2)
    c: Distance(g2) = 9.37
    c: Distance(g3) = 12.8
    c: Distance(g7) = 13.22
FEATURE [PartDesign::Pocket] Pocket003099  label="q1-leg004"
  BaseFeature = -> Hole004
  Length = 5
  Length2 = 100
  Profile = -> Sketch171
  Refine = true
  Type = 0
FEATURE [Sketcher::SketchObject] Sketch184  label="servo_tollerance010"
  MapMode = 5
  Placement = pos=(2.152e-13,-5.82326,10.0862) rot=(1,0,0;0.523599rad)
  Support = -> [Pad012069]
  sketch-geometry (4):
    g0: LineSegment StartX=-20.5 StartY=37 StartZ=0 EndX=-21.25 EndY=37 EndZ=0
    g1: LineSegment StartX=-21.25 StartY=37 StartZ=0 EndX=-21.25 EndY=14 EndZ=0
    g2: LineSegment StartX=-21.25 StartY=14 StartZ=0 EndX=-20.5 EndY=14 EndZ=0
    g3: LineSegment StartX=-20.5 StartY=14 StartZ=0 EndX=-20.5 EndY=37 EndZ=0
  constraints (9):
    c: Coincident(g0,g1)
    c: Coincident(g1,g2)
    c: Coincident(g2,g3)
    c: Coincident(g3,g0)
    c: Horizontal(g0)
    c: Horizontal(g2)
    c: Vertical(g1)
    c: Vertical(g3)
    c: DistanceX(g0,g0) = 0.75
FEATURE [Sketcher::SketchObject] Sketch185  label="back_wall010"
  ExternalGeometry = -> [Pad012064]
  MapMode = 5
  Placement = pos=(-20.5,0,0) rot=(0.57735,-0.57735,-0.57735;2.0944rad)
  Support = -> [Pad012064]
  sketch-geometry (9):
    g0: LineSegment StartX=5.71497 StartY=2.25 StartZ=0 EndX=-11.6041 EndY=2.25 EndZ=0
    g1: LineSegment StartX=-11.6041 StartY=2.25 StartZ=0 EndX=-38.6752 EndY=17.8795 EndZ=0
    g2: LineSegment StartX=-38.6752 StartY=17.8795 StartZ=0 EndX=-37.1752 EndY=20.4776 EndZ=0
    g3: LineSegment StartX=-37.1752 StartY=20.4776 StartZ=0 EndX=-34.2017 EndY=18.7609 EndZ=0
    g4: LineSegment StartX=-34.2017 StartY=18.7609 StartZ=0 EndX=-27.9517 EndY=29.5862 EndZ=0
    g5: LineSegment StartX=-27.9517 StartY=29.5862 StartZ=0 EndX=-4.56905 EndY=16.0862 EndZ=0
    g6: LineSegment StartX=-4.56905 StartY=16.0862 StartZ=0 EndX=-10.5379 EndY=5.74787 EndZ=0
    g7: LineSegment StartX=-10.5379 StartY=5.74787 StartZ=0 EndX=5.71497 EndY=5.75 EndZ=0
    g8: LineSegment StartX=5.71497 StartY=5.75 StartZ=0 EndX=5.71497 EndY=2.25 EndZ=0
  constraints (18):
    c: Coincident(g-11,g0)
    c: Coincident(g0,g-11)
    c: Coincident(g0,g1)
    c: Coincident(g1,g-4)
    c: Coincident(g1,g2)
    c: Coincident(g2,g-5)
    c: Coincident(g2,g3)
    c: Coincident(g3,g-6)
    c: Coincident(g3,g4)
    c: Coincident(g4,g-6)
    c: Coincident(g4,g5)
    c: Coincident(g5,g-7)
    c: Coincident(g5,g6)
    c: Coincident(g6,g-8)
    c: Coincident(g6,g7)
    c: Coincident(g7,g-10)
    c: Coincident(g7,g8)
    c: Coincident(g8,g0)
FEATURE [Sketcher::SketchObject] Sketch186  label="cable_slot010"
  ExternalGeometry = -> [Pocket003101]
  MapMode = 5
  Placement = pos=(-3.873e-13,33.775,19.5) rot=(0,0.5,0.866025;3.14159rad)
  Support = -> [Pocket003101]
  sketch-geometry (4):
    g0: LineSegment StartX=20.25 StartY=3 StartZ=0 EndX=18.01 EndY=3 EndZ=0
    g1: LineSegment StartX=18.01 StartY=3 StartZ=0 EndX=18.01 EndY=12.5 EndZ=0
    g2: LineSegment StartX=18.01 StartY=12.5 StartZ=0 EndX=20.25 EndY=12.5 EndZ=0
    g3: LineSegment StartX=20.25 StartY=12.5 StartZ=0 EndX=20.25 EndY=3 EndZ=0
  constraints (11):
    c: Coincident(g0,g1)
    c: Coincident(g1,g2)
    c: Coincident(g2,g3)
    c: Coincident(g3,g0)
    c: Horizontal(g0)
    c: Horizontal(g2)
    c: Vertical(g1)
    c: Vertical(g3)
    c: DistanceX(g2,g2) = 2.24
    c: DistanceY(g1,g1) = 9.5
    c: DistanceX(g2,g-3) = 2
FEATURE [App::Part] Part012  label="left_leg_004"
  Group = -> [Pocket003103,Fusion007071,Fusion007070,Body020,Fusion007072,Pocket003105,Fusion007069,Clone042,Fillet007,Body021]
  License = CC BY 3.0
  LicenseURL = http://creativecommons.org/licenses/by/3.0/
  Origin = -> Origin034
  Placement = pos=(-56.5,52.5,0) rot=(0,0,1;0rad)
FEATURE [Sketcher::SketchObject] Sketch187  label="servo-walls005"
  ExternalGeometry = -> [Pocket003106]
  MapMode = 5
  Placement = pos=(2.152e-13,-5.82326,10.0862) rot=(1,0,0;0.523599rad)
  Support = -> [Pad012070]
  sketch-geometry (24):
    g0: LineSegment StartX=-5 StartY=42.4334 StartZ=0 EndX=-5 EndY=37 EndZ=0
    g1: LineSegment StartX=-5 StartY=37 StartZ=0 EndX=-20.5 EndY=37 EndZ=0
    g2: LineSegment StartX=-20.5 StartY=37 StartZ=0 EndX=-20.5 EndY=39 EndZ=0
    g3: LineSegment StartX=2 StartY=39 StartZ=0 EndX=2 EndY=37 EndZ=0
    g4: LineSegment StartX=2 StartY=37 StartZ=0 EndX=-1.60533 EndY=37 EndZ=0
    g5: LineSegment StartX=-1.60533 StartY=37 StartZ=0 EndX=-1.60533 EndY=42.4334 EndZ=0
    g6: LineSegment StartX=-20.5 StartY=39 StartZ=0 EndX=-7 EndY=39 EndZ=0
    g7: LineSegment StartX=-7 StartY=39 StartZ=0 EndX=-7 EndY=42.4334 EndZ=0
    g8: LineSegment StartX=-7 StartY=42.4334 StartZ=0 EndX=-5 EndY=42.4334 EndZ=0
    g9: LineSegment StartX=2 StartY=39 StartZ=0 EndX=0.5 EndY=39 EndZ=0
    g10: LineSegment StartX=0.5 StartY=39 StartZ=0 EndX=0.5 EndY=42.4334 EndZ=0
    g11: LineSegment StartX=-1.60533 StartY=42.4334 StartZ=0 EndX=0.5 EndY=42.4334 EndZ=0
    g12: LineSegment StartX=-5 StartY=9.5 StartZ=0 EndX=-5 EndY=14 EndZ=0
    g13: LineSegment StartX=-5 StartY=14 StartZ=0 EndX=-20.5 EndY=14 EndZ=0
    g14: LineSegment StartX=-20.5 StartY=14 StartZ=0 EndX=-20.5 EndY=12 EndZ=0
    g15: LineSegment StartX=2 StartY=12 StartZ=0 EndX=2 EndY=14 EndZ=0
    g16: LineSegment StartX=2 StartY=14 StartZ=0 EndX=-1.61532 EndY=14 EndZ=0
    g17: LineSegment StartX=-1.61532 StartY=14 StartZ=0 EndX=-1.61532 EndY=9.5 EndZ=0
    g18: LineSegment StartX=-20.5 StartY=12 StartZ=0 EndX=-7 EndY=12 EndZ=0
    g19: LineSegment StartX=-7 StartY=12 StartZ=0 EndX=-7 EndY=9.5 EndZ=0
    g20: LineSegment StartX=-7 StartY=9.5 StartZ=0 EndX=-5 EndY=9.5 EndZ=0
    g21: LineSegment StartX=2 StartY=12 StartZ=0 EndX=0.5 EndY=12 EndZ=0
    g22: LineSegment StartX=0.5 StartY=12 StartZ=0 EndX=0.5 EndY=9.5 EndZ=0
    g23: LineSegment StartX=-1.61532 StartY=9.5 StartZ=0 EndX=0.5 EndY=9.5 EndZ=0
  constraints (50):
    c: Coincident(g0,g1)
    c: Coincident(g1,g2)
    c: Horizontal(g1)
    c: Vertical(g0)
    c: Vertical(g2)
    c: Coincident(g3,g4)
    c: Coincident(g4,g5)
    c: Horizontal(g4)
    c: Vertical(g3)
    c: Vertical(g5)
    c: Coincident(g2,g6)
    c: Horizontal(g6)
    c: Coincident(g6,g7)
    c: Vertical(g7)
    c: PointOnObject(g7,g-3)
    c: PointOnObject(g0,g-3)
    c: Coincident(g8,g7)
    c: Coincident(g8,g0)
    c: Coincident(g3,g9)
    c: Horizontal(g9)
    c: Coincident(g9,g10)
    c: PointOnObject(g10,g-3)
    c: Vertical(g10)
    c: PointOnObject(g5,g-3)
    c: Coincident(g11,g5)
    c: Coincident(g11,g10)
    c: Coincident(g12,g13)
    c: Coincident(g13,g14)
    c: Horizontal(g13)
    c: Vertical(g12)
    c: Vertical(g14)
    c: Coincident(g15,g16)
    c: Coincident(g16,g17)
    c: Horizontal(g16)
    c: Vertical(g15)
    c: Vertical(g17)
    c: Coincident(g14,g18)
    c: Horizontal(g18)
    c: Coincident(g18,g19)
    c: Vertical(g19)
    c: Coincident(g19,g20)
    c: Coincident(g20,g12)
    c: Horizontal(g20)
    c: Coincident(g15,g21)
    c: Horizontal(g21)
    c: Coincident(g21,g22)
    c: Vertical(g22)
    c: Coincident(g17,g23)
    c: Coincident(g23,g22)
    c: Horizontal(g23)
FEATURE [PartDesign::Pad] Pad012064  label="front_wall010"
  BaseFeature = -> Pad012066
  Length = 3.715
  Length2 = 100
  Profile = -> Sketch200
  Refine = true
  Type = 0
FEATURE [PartDesign::Pocket] Pocket003101  label="servo_tollerance011"
  BaseFeature = -> Pad012069
  Length = 12.5
  Length2 = 100
  Profile = -> Sketch184
  Refine = true
  Type = 0
FEATURE [Part::Fillet] Fillet007  label="rounder_q1_servo005"
  Base = -> Clone042
  Edges = 1 edges r=8: [Edge27]
  Placement = pos=(0,0,44) rot=(0,0,1;1.5708rad)
FEATURE [PartDesign::Body] Body020  label="Q1-base007"
  Group = -> [Sketch203,Pad012062,Sketch189,Sketch194,Pad012071,Pocket003100,Sketch207,Pocket003109,Sketch202,Pad012072,Sketch201,Pocket003106,Sketch187,Pad012066,Sketch200,Pad012064,Sketch199,Sketch185,Sketch184,Sketch186,Pad012070,Sketch193,Pad012069,Pocket003101,Pocket003102,Hole005,Sketch206,Pocket003107]
  Origin = -> Origin035
  Placement = pos=(0,0,44) rot=(0,0,1;1.5708rad)
  Tip = -> Pocket003107
FEATURE [PartDesign::Pocket] Pocket003102  label="cable_slot011"
  BaseFeature = -> Pocket003101
  Length = 5
  Length2 = 100
  Profile = -> Sketch186
  Refine = true
  Type = 0
FEATURE [PartDesign::FeatureBase] Clone042
  BaseFeature = -> Pocket003107
FEATURE [PartDesign::Pad] Pad012066  label="servo_walls005"
  BaseFeature = -> Pocket003106
  Length = 12.5
  Length2 = 100
  Profile = -> Sketch187
  Refine = true
  Type = 0
FEATURE [PartDesign::Hole] Hole005  label="m2_screw_holes010"
  BaseFeature = -> Pocket003102
  Depth = 35
  DepthType = 0
  Diameter = 2.5
  DrillPoint = 1
  DrillPointAngle = 118
  HoleCutCountersinkAngle = 90
  HoleCutDepth = 0
  HoleCutDiameter = 0
  HoleCutType = 0
  ModelActualThread = false
  Profile = -> Sketch199
  Refine = true
  Tapered = false
  TaperedAngle = 90
  ThreadAngle = 0
  ThreadClass = 0
  ThreadCutOffInner = 0
  ThreadCutOffOuter = 0
  ThreadDirection = 0
  ThreadFit = 0
  ThreadPitch = 0
  ThreadSize = 0
  ThreadType = 0
  Threaded = false
FEATURE [Sketcher::SketchObject] Sketch193  label="q2_axis005"
  MapMode = 5
  Placement = pos=(-22.25,0,0) rot=(0.57735,-0.57735,-0.57735;2.0944rad)
  Support = -> [Pad012070]
  sketch-geometry (1):
    g0: Circle CenterX=-24 CenterY=20 CenterZ=0 NormalX=0 NormalY=0 NormalZ=1 AngleXU=0 Radius=1.75
  constraints (1):
    c: Radius(g0) = 1.75
FEATURE [Sketcher::SketchObject] Sketch199  label="m2_screw_holes011"
  MapMode = 5
  Placement = pos=(-22.25,0,0) rot=(0.57735,-0.57735,-0.57735;2.0944rad)
  Support = -> [Pocket003102]
  sketch-geometry (2):
    g0: Circle CenterX=-31.1478 CenterY=24.1208 CenterZ=0 NormalX=0 NormalY=0 NormalZ=1 AngleXU=0 Radius=1.25
    g1: Circle CenterX=-7.61619 CenterY=10.5 CenterZ=0 NormalX=0 NormalY=0 NormalZ=1 AngleXU=0 Radius=1.25
  constraints (2):
    c: Radius(g0) = 1.25
    c: Equal(g0,g1) = 1.25
FEATURE [PartDesign::Pad] Pad012069  label="servo_axis005"
  BaseFeature = -> Pad012070
  Length = 3
  Length2 = 100
  Profile = -> Sketch193
  Refine = true
  Type = 0
FEATURE [Sketcher::SketchObject] Sketch200  label="front_wall011"
  ExternalGeometry = -> [Pad012066]
  MapMode = 5
  Placement = pos=(2,0,0) rot=(0.57735,0.57735,0.57735;2.0944rad)
  Support = -> [Pad012066]
  sketch-geometry (9):
    g0: ArcOfCircle CenterX=18.4487 CenterY=16.9211 CenterZ=0 NormalX=0 NormalY=0 NormalZ=1 AngleXU=0 Radius=3.06832 StartAngle=3.68648 EndAngle=5.44463
    g1: LineSegment StartX=10.969 StartY=5.00105 StartZ=0 EndX=34.5617 EndY=18.1373 EndZ=0
    g2: LineSegment StartX=12.6837 StartY=20.7712 StartZ=0 EndX=4.56905 EndY=16.0862 EndZ=0
    g3: LineSegment StartX=4.56905 StartY=16.0862 StartZ=0 EndX=10.969 EndY=5.00105 EndZ=0
    g4: ArcOfCircle CenterX=24 CenterY=19.9888 CenterZ=0 NormalX=0 NormalY=0 NormalZ=1 AngleXU=0 Radius=6.3928 StartAngle=4.13303 EndAngle=7.03916
    g5: LineSegment StartX=28.6514 StartY=24.3743 StartZ=0 EndX=26.2197 EndY=28.5862 EndZ=0
    g6: LineSegment StartX=26.2197 StartY=28.5862 StartZ=0 EndX=27.9517 EndY=29.5862 EndZ=0
    g7: LineSegment StartX=27.9517 StartY=29.5862 StartZ=0 EndX=34.5617 EndY=18.1373 EndZ=0
    g8: LineSegment StartX=12.6837 StartY=20.7712 StartZ=0 EndX=15.8247 EndY=15.3307 EndZ=0
  constraints (20):
    c: Coincident(g3,g2)
    c: Parallel(g-7,g3)
    c: Coincident(g-7,g2)
    c: Coincident(g1,g3)
    c: Parallel(g-8,g2)
    c: Coincident(g4,g0)
    c: PointOnObject(g4,g-4)
    c: Coincident(g5,g4)
    c: Coincident(g5,g-5)
    c: Coincident(g5,g6)
    c: Coincident(g6,g-5)
    c: Coincident(g6,g7)
    c: Parallel(g-9,g7)
    c: Coincident(g7,g1)
    c: Coincident(g8,g2)
    c: Coincident(g8,g0)
    c: Perpendicular(g8,g2)
    c: Distance(g2) = 9.37
    c: Distance(g3) = 12.8
    c: Distance(g7) = 13.22
FEATURE [PartDesign::Pocket] Pocket003107  label="q1-leg005"
  BaseFeature = -> Hole005
  Length = 5
  Length2 = 100
  Profile = -> Sketch206
  Refine = true
  Type = 0
FEATURE [PartDesign::Pad] Pad012070  label="back_wall011"
  BaseFeature = -> Pad012064
  Length = 1.75
  Length2 = 100
  Profile = -> Sketch185
  Refine = true
  Type = 0
FEATURE [Sketcher::SketchObject] Sketch206  label="finger_hole005"
  ExternalGeometry = -> [Hole005]
  MapMode = 5
  Placement = pos=(2.5e-15,1.92674,-3.33722) rot=(1,0,0;3.66519rad)
  Support = -> [Hole005]
  sketch-geometry (2):
    g0: Circle CenterX=-8.2675 CenterY=-26.8039 CenterZ=0 NormalX=0 NormalY=0 NormalZ=1 AngleXU=0 Radius=6
    g1: LineSegment [constr] StartX=-8.2675 StartY=-11.1744 StartZ=0 EndX=-8.2675 EndY=-42.4334 EndZ=0
  constraints (7):
    c: Radius(g0) = 6
    c: PointOnObject(g1,g-3)
    c: PointOnObject(g1,g-4)
    c: Vertical(g1)
    c: PointOnObject(g0,g1)
    c: Symmetric(g-3,g-3,g1)
    c: Symmetric(g1,g1,g0)
FEATURE [PartDesign::Pad] Pad012073  label="front_wall012"
  BaseFeature = -> Pad012084
  Length = 3.715
  Length2 = 100
  Profile = -> Sketch228
  Refine = true
  Type = 0
FEATURE [PartDesign::Hole] Hole006  label="m2_screw_holes012"
  BaseFeature = -> Pocket003119
  Depth = 35
  DepthType = 0
  Diameter = 2.5
  DrillPoint = 1
  DrillPointAngle = 118
  HoleCutCountersinkAngle = 90
  HoleCutDepth = 0
  HoleCutDiameter = 0
  HoleCutType = 0
  ModelActualThread = false
  Profile = -> Sketch233
  Refine = true
  Tapered = false
  TaperedAngle = 90
  ThreadAngle = 0
  ThreadClass = 0
  ThreadCutOffInner = 0
  ThreadCutOffOuter = 0
  ThreadDirection = 0
  ThreadFit = 0
  ThreadPitch = 0
  ThreadSize = 0
  ThreadType = 0
  Threaded = false
FEATURE [Sketcher::SketchObject] Sketch213  label="q2_axis006"
  MapMode = 5
  Placement = pos=(-22.25,0,0) rot=(0.57735,-0.57735,-0.57735;2.0944rad)
  Support = -> [Pad012082]
  sketch-geometry (1):
    g0: Circle CenterX=-24 CenterY=20 CenterZ=0 NormalX=0 NormalY=0 NormalZ=1 AngleXU=0 Radius=1.75
  constraints (1):
    c: Radius(g0) = 1.75
FEATURE [PartDesign::Pocket] Pocket003112  label="servo_tollerance012"
  BaseFeature = -> Pad012078
  Length = 12.5
  Length2 = 100
  Profile = -> Sketch217
  Refine = true
  Type = 0
FEATURE [Sketcher::SketchObject] Sketch216  label="back_wall012"
  ExternalGeometry = -> [Pad012073]
  MapMode = 5
  Placement = pos=(-20.5,0,0) rot=(0.57735,-0.57735,-0.57735;2.0944rad)
  Support = -> [Pad012073]
  sketch-geometry (9):
    g0: LineSegment StartX=5.71497 StartY=2.25 StartZ=0 EndX=-11.6041 EndY=2.25 EndZ=0
    g1: LineSegment StartX=-11.6041 StartY=2.25 StartZ=0 EndX=-38.6752 EndY=17.8795 EndZ=0
    g2: LineSegment StartX=-38.6752 StartY=17.8795 StartZ=0 EndX=-37.1752 EndY=20.4776 EndZ=0
    g3: LineSegment StartX=-37.1752 StartY=20.4776 StartZ=0 EndX=-34.2017 EndY=18.7609 EndZ=0
    g4: LineSegment StartX=-34.2017 StartY=18.7609 StartZ=0 EndX=-27.9517 EndY=29.5862 EndZ=0
    g5: LineSegment StartX=-27.9517 StartY=29.5862 StartZ=0 EndX=-4.56905 EndY=16.0862 EndZ=0
    g6: LineSegment StartX=-4.56905 StartY=16.0862 StartZ=0 EndX=-10.5379 EndY=5.74787 EndZ=0
    g7: LineSegment StartX=-10.5379 StartY=5.74787 StartZ=0 EndX=5.71497 EndY=5.75 EndZ=0
    g8: LineSegment StartX=5.71497 StartY=5.75 StartZ=0 EndX=5.71497 EndY=2.25 EndZ=0
  constraints (18):
    c: Coincident(g-11,g0)
    c: Coincident(g0,g-11)
    c: Coincident(g0,g1)
    c: Coincident(g1,g-4)
    c: Coincident(g1,g2)
    c: Coincident(g2,g-5)
    c: Coincident(g2,g3)
    c: Coincident(g3,g-6)
    c: Coincident(g3,g4)
    c: Coincident(g4,g-6)
    c: Coincident(g4,g5)
    c: Coincident(g5,g-7)
    c: Coincident(g5,g6)
    c: Coincident(g6,g-8)
    c: Coincident(g6,g7)
    c: Coincident(g7,g-10)
    c: Coincident(g7,g8)
    c: Coincident(g8,g0)
FEATURE [Sketcher::SketchObject] Sketch217  label="servo_tollerance013"
  MapMode = 5
  Placement = pos=(2.152e-13,-5.82326,10.0862) rot=(1,0,0;0.523599rad)
  Support = -> [Pad012078]
  sketch-geometry (4):
    g0: LineSegment StartX=-20.5 StartY=37 StartZ=0 EndX=-21.25 EndY=37 EndZ=0
    g1: LineSegment StartX=-21.25 StartY=37 StartZ=0 EndX=-21.25 EndY=14 EndZ=0
    g2: LineSegment StartX=-21.25 StartY=14 StartZ=0 EndX=-20.5 EndY=14 EndZ=0
    g3: LineSegment StartX=-20.5 StartY=14 StartZ=0 EndX=-20.5 EndY=37 EndZ=0
  constraints (9):
    c: Coincident(g0,g1)
    c: Coincident(g1,g2)
    c: Coincident(g2,g3)
    c: Coincident(g3,g0)
    c: Horizontal(g0)
    c: Horizontal(g2)
    c: Vertical(g1)
    c: Vertical(g3)
    c: DistanceX(g0,g0) = 0.75
FEATURE [PartDesign::Pocket] Pocket003113  label="q1-leg006"
  BaseFeature = -> Hole006
  Length = 5
  Length2 = 100
  Profile = -> Sketch223
  Refine = true
  Type = 0
FEATURE [PartDesign::Body] Body022  label="Q1-base008"
  Group = -> [Sketch232,Pad012076,Sketch222,Sketch231,Pad012080,Pocket003117,Sketch230,Pocket003111,Sketch219,Pad012074,Sketch221,Pocket003110,Sketch227,Pad012084,Sketch228,Pad012073,Sketch233,Sketch216,Sketch217,Sketch226,Pad012082,Sketch213,Pad012078,Pocket003112,Pocket003119,Hole006,Sketch223,Pocket003113]
  Origin = -> Origin039
  Placement = pos=(0,0,44) rot=(0,0,1;1.5708rad)
  Tip = -> Pocket003113
FEATURE [PartDesign::Pad] Pad012078  label="servo_axis006"
  BaseFeature = -> Pad012082
  Length = 3
  Length2 = 100
  Profile = -> Sketch213
  Refine = true
  Type = 0
FEATURE [Sketcher::SketchObject] Sketch223  label="finger_hole006"
  ExternalGeometry = -> [Hole006]
  MapMode = 5
  Placement = pos=(2.5e-15,1.92674,-3.33722) rot=(1,0,0;3.66519rad)
  Support = -> [Hole006]
  sketch-geometry (2):
    g0: Circle CenterX=-8.2675 CenterY=-26.8039 CenterZ=0 NormalX=0 NormalY=0 NormalZ=1 AngleXU=0 Radius=6
    g1: LineSegment [constr] StartX=-8.2675 StartY=-11.1744 StartZ=0 EndX=-8.2675 EndY=-42.4334 EndZ=0
  constraints (7):
    c: Radius(g0) = 6
    c: PointOnObject(g1,g-3)
    c: PointOnObject(g1,g-4)
    c: Vertical(g1)
    c: PointOnObject(g0,g1)
    c: Symmetric(g-3,g-3,g1)
    c: Symmetric(g1,g1,g0)
FEATURE [PartDesign::Pad] Pad012082  label="back_wall013"
  BaseFeature = -> Pad012073
  Length = 1.75
  Length2 = 100
  Profile = -> Sketch216
  Refine = true
  Type = 0
FEATURE [Sketcher::SketchObject] Sketch226  label="cable_slot012"
  ExternalGeometry = -> [Pocket003112]
  MapMode = 5
  Placement = pos=(-3.873e-13,33.775,19.5) rot=(0,0.5,0.866025;3.14159rad)
  Support = -> [Pocket003112]
  sketch-geometry (4):
    g0: LineSegment StartX=20.25 StartY=3 StartZ=0 EndX=18.01 EndY=3 EndZ=0
    g1: LineSegment StartX=18.01 StartY=3 StartZ=0 EndX=18.01 EndY=12.5 EndZ=0
    g2: LineSegment StartX=18.01 StartY=12.5 StartZ=0 EndX=20.25 EndY=12.5 EndZ=0
    g3: LineSegment StartX=20.25 StartY=12.5 StartZ=0 EndX=20.25 EndY=3 EndZ=0
  constraints (11):
    c: Coincident(g0,g1)
    c: Coincident(g1,g2)
    c: Coincident(g2,g3)
    c: Coincident(g3,g0)
    c: Horizontal(g0)
    c: Horizontal(g2)
    c: Vertical(g1)
    c: Vertical(g3)
    c: DistanceX(g2,g2) = 2.24
    c: DistanceY(g1,g1) = 9.5
    c: DistanceX(g2,g-3) = 2
FEATURE [Sketcher::SketchObject] Sketch227  label="servo-walls006"
  ExternalGeometry = -> [Pocket003110]
  MapMode = 5
  Placement = pos=(2.152e-13,-5.82326,10.0862) rot=(1,0,0;0.523599rad)
  Support = -> [Pad012082]
  sketch-geometry (24):
    g0: LineSegment StartX=-5 StartY=42.4334 StartZ=0 EndX=-5 EndY=37 EndZ=0
    g1: LineSegment StartX=-5 StartY=37 StartZ=0 EndX=-20.5 EndY=37 EndZ=0
    g2: LineSegment StartX=-20.5 StartY=37 StartZ=0 EndX=-20.5 EndY=39 EndZ=0
    g3: LineSegment StartX=2 StartY=39 StartZ=0 EndX=2 EndY=37 EndZ=0
    g4: LineSegment StartX=2 StartY=37 StartZ=0 EndX=-1.60533 EndY=37 EndZ=0
    g5: LineSegment StartX=-1.60533 StartY=37 StartZ=0 EndX=-1.60533 EndY=42.4334 EndZ=0
    g6: LineSegment StartX=-20.5 StartY=39 StartZ=0 EndX=-7 EndY=39 EndZ=0
    g7: LineSegment StartX=-7 StartY=39 StartZ=0 EndX=-7 EndY=42.4334 EndZ=0
    g8: LineSegment StartX=-7 StartY=42.4334 StartZ=0 EndX=-5 EndY=42.4334 EndZ=0
    g9: LineSegment StartX=2 StartY=39 StartZ=0 EndX=0.5 EndY=39 EndZ=0
    g10: LineSegment StartX=0.5 StartY=39 StartZ=0 EndX=0.5 EndY=42.4334 EndZ=0
    g11: LineSegment StartX=-1.60533 StartY=42.4334 StartZ=0 EndX=0.5 EndY=42.4334 EndZ=0
    g12: LineSegment StartX=-5 StartY=9.5 StartZ=0 EndX=-5 EndY=14 EndZ=0
    g13: LineSegment StartX=-5 StartY=14 StartZ=0 EndX=-20.5 EndY=14 EndZ=0
    g14: LineSegment StartX=-20.5 StartY=14 StartZ=0 EndX=-20.5 EndY=12 EndZ=0
    g15: LineSegment StartX=2 StartY=12 StartZ=0 EndX=2 EndY=14 EndZ=0
    g16: LineSegment StartX=2 StartY=14 StartZ=0 EndX=-1.61532 EndY=14 EndZ=0
    g17: LineSegment StartX=-1.61532 StartY=14 StartZ=0 EndX=-1.61532 EndY=9.5 EndZ=0
    g18: LineSegment StartX=-20.5 StartY=12 StartZ=0 EndX=-7 EndY=12 EndZ=0
    g19: LineSegment StartX=-7 StartY=12 StartZ=0 EndX=-7 EndY=9.5 EndZ=0
    g20: LineSegment StartX=-7 StartY=9.5 StartZ=0 EndX=-5 EndY=9.5 EndZ=0
    g21: LineSegment StartX=2 StartY=12 StartZ=0 EndX=0.5 EndY=12 EndZ=0
    g22: LineSegment StartX=0.5 StartY=12 StartZ=0 EndX=0.5 EndY=9.5 EndZ=0
    g23: LineSegment StartX=-1.61532 StartY=9.5 StartZ=0 EndX=0.5 EndY=9.5 EndZ=0
  constraints (50):
    c: Coincident(g0,g1)
    c: Coincident(g1,g2)
    c: Horizontal(g1)
    c: Vertical(g0)
    c: Vertical(g2)
    c: Coincident(g3,g4)
    c: Coincident(g4,g5)
    c: Horizontal(g4)
    c: Vertical(g3)
    c: Vertical(g5)
    c: Coincident(g2,g6)
    c: Horizontal(g6)
    c: Coincident(g6,g7)
    c: Vertical(g7)
    c: PointOnObject(g7,g-3)
    c: PointOnObject(g0,g-3)
    c: Coincident(g8,g7)
    c: Coincident(g8,g0)
    c: Coincident(g3,g9)
    c: Horizontal(g9)
    c: Coincident(g9,g10)
    c: PointOnObject(g10,g-3)
    c: Vertical(g10)
    c: PointOnObject(g5,g-3)
    c: Coincident(g11,g5)
    c: Coincident(g11,g10)
    c: Coincident(g12,g13)
    c: Coincident(g13,g14)
    c: Horizontal(g13)
    c: Vertical(g12)
    c: Vertical(g14)
    c: Coincident(g15,g16)
    c: Coincident(g16,g17)
    c: Horizontal(g16)
    c: Vertical(g15)
    c: Vertical(g17)
    c: Coincident(g14,g18)
    c: Horizontal(g18)
    c: Coincident(g18,g19)
    c: Vertical(g19)
    c: Coincident(g19,g20)
    c: Coincident(g20,g12)
    c: Horizontal(g20)
    c: Coincident(g15,g21)
    c: Horizontal(g21)
    c: Coincident(g21,g22)
    c: Vertical(g22)
    c: Coincident(g17,g23)
    c: Coincident(g23,g22)
    c: Horizontal(g23)
FEATURE [App::Part] Part013  label="left_leg_center"
  Group = -> [Pocket003118,Fusion007076,Fusion007073,Body022,Fusion007075,Pocket003116,Fusion007074,Clone043,Fillet008,Body023]
  License = CC BY 3.0
  LicenseURL = http://creativecommons.org/licenses/by/3.0/
  Origin = -> Origin038
  Placement = pos=(-56.5,0,0) rot=(0,0,1;0rad)
FEATURE [Sketcher::SketchObject] Sketch228  label="front_wall013"
  ExternalGeometry = -> [Pad012084]
  MapMode = 5
  Placement = pos=(2,0,0) rot=(0.57735,0.57735,0.57735;2.0944rad)
  Support = -> [Pad012084]
  sketch-geometry (9):
    g0: ArcOfCircle CenterX=18.4487 CenterY=16.9211 CenterZ=0 NormalX=0 NormalY=0 NormalZ=1 AngleXU=0 Radius=3.06832 StartAngle=3.68648 EndAngle=5.44463
    g1: LineSegment StartX=10.969 StartY=5.00105 StartZ=0 EndX=34.5617 EndY=18.1373 EndZ=0
    g2: LineSegment StartX=12.6837 StartY=20.7712 StartZ=0 EndX=4.56905 EndY=16.0862 EndZ=0
    g3: LineSegment StartX=4.56905 StartY=16.0862 StartZ=0 EndX=10.969 EndY=5.00105 EndZ=0
    g4: ArcOfCircle CenterX=24 CenterY=19.9888 CenterZ=0 NormalX=0 NormalY=0 NormalZ=1 AngleXU=0 Radius=6.3928 StartAngle=4.13303 EndAngle=7.03916
    g5: LineSegment StartX=28.6514 StartY=24.3743 StartZ=0 EndX=26.2197 EndY=28.5862 EndZ=0
    g6: LineSegment StartX=26.2197 StartY=28.5862 StartZ=0 EndX=27.9517 EndY=29.5862 EndZ=0
    g7: LineSegment StartX=27.9517 StartY=29.5862 StartZ=0 EndX=34.5617 EndY=18.1373 EndZ=0
    g8: LineSegment StartX=12.6837 StartY=20.7712 StartZ=0 EndX=15.8247 EndY=15.3307 EndZ=0
  constraints (20):
    c: Coincident(g3,g2)
    c: Parallel(g-7,g3)
    c: Coincident(g-7,g2)
    c: Coincident(g1,g3)
    c: Parallel(g-8,g2)
    c: Coincident(g4,g0)
    c: PointOnObject(g4,g-4)
    c: Coincident(g5,g4)
    c: Coincident(g5,g-5)
    c: Coincident(g5,g6)
    c: Coincident(g6,g-5)
    c: Coincident(g6,g7)
    c: Parallel(g-9,g7)
    c: Coincident(g7,g1)
    c: Coincident(g8,g2)
    c: Coincident(g8,g0)
    c: Perpendicular(g8,g2)
    c: Distance(g2) = 9.37
    c: Distance(g3) = 12.8
    c: Distance(g7) = 13.22
FEATURE [PartDesign::Pocket] Pocket003119  label="cable_slot013"
  BaseFeature = -> Pocket003112
  Length = 5
  Length2 = 100
  Profile = -> Sketch226
  Refine = true
  Type = 0
FEATURE [Sketcher::SketchObject] Sketch233  label="m2_screw_holes013"
  MapMode = 5
  Placement = pos=(-22.25,0,0) rot=(0.57735,-0.57735,-0.57735;2.0944rad)
  Support = -> [Pocket003119]
  sketch-geometry (2):
    g0: Circle CenterX=-31.1478 CenterY=24.1208 CenterZ=0 NormalX=0 NormalY=0 NormalZ=1 AngleXU=0 Radius=1.25
    g1: Circle CenterX=-7.61619 CenterY=10.5 CenterZ=0 NormalX=0 NormalY=0 NormalZ=1 AngleXU=0 Radius=1.25
  constraints (2):
    c: Radius(g0) = 1.25
    c: Equal(g0,g1) = 1.25
FEATURE [PartDesign::Pad] Pad012084  label="servo_walls006"
  BaseFeature = -> Pocket003110
  Length = 12.5
  Length2 = 100
  Profile = -> Sketch227
  Refine = true
  Type = 0
FEATURE [Part::Fillet] Fillet008  label="rounder_q1_servo006"
  Base = -> Clone043
  Edges = 1 edges r=8: [Edge27]
  Placement = pos=(0,0,44) rot=(0,0,1;1.5708rad)
FEATURE [PartDesign::FeatureBase] Clone043
  BaseFeature = -> Pocket003113
FEATURE [PartDesign::Pocket] Pocket003120  label="q1-leg007"
  BaseFeature = -> Hole007
  Length = 5
  Length2 = 100
  Profile = -> Sketch254
  Refine = true
  Type = 0
FEATURE [App::Part] Part015  label="right_leg_center001"
  Group = -> [Pocket003127,Fusion007077,Fusion007078,Body025,Fusion007079,Pocket003122,Fusion007080,Fillet009,Body026,Part__Mirroring,Part__Mirroring001]
  License = CC BY 3.0
  LicenseURL = http://creativecommons.org/licenses/by/3.0/
  Origin = -> Origin043
  Placement = pos=(56.5,0,0) rot=(0,0,1;0rad)
FEATURE [Sketcher::SketchObject] Sketch238  label="q2_axis007"
  MapMode = 5
  Placement = pos=(-22.25,0,0) rot=(0.57735,-0.57735,-0.57735;2.0944rad)
  Support = -> [Pad012094]
  sketch-geometry (1):
    g0: Circle CenterX=-24 CenterY=20 CenterZ=0 NormalX=0 NormalY=0 NormalZ=1 AngleXU=0 Radius=1.75
  constraints (1):
    c: Radius(g0) = 1.75
FEATURE [PartDesign::Hole] Hole007  label="m2_screw_holes014"
  BaseFeature = -> Pocket003121
  Depth = 35
  DepthType = 0
  Diameter = 2.5
  DrillPoint = 1
  DrillPointAngle = 118
  HoleCutCountersinkAngle = 90
  HoleCutDepth = 0
  HoleCutDiameter = 0
  HoleCutType = 0
  ModelActualThread = false
  Profile = -> Sketch245
  Refine = true
  Tapered = false
  TaperedAngle = 90
  ThreadAngle = 0
  ThreadClass = 0
  ThreadCutOffInner = 0
  ThreadCutOffOuter = 0
  ThreadDirection = 0
  ThreadFit = 0
  ThreadPitch = 0
  ThreadSize = 0
  ThreadType = 0
  Threaded = false
FEATURE [PartDesign::Pocket] Pocket003121  label="cable_slot014"
  BaseFeature = -> Pocket003129
  Length = 5
  Length2 = 100
  Profile = -> Sketch247
  Refine = true
  Type = 0
FEATURE [PartDesign::Pad] Pad012087  label="servo_walls007"
  BaseFeature = -> Pocket003125
  Length = 12.5
  Length2 = 100
  Profile = -> Sketch257
  Refine = true
  Type = 0
FEATURE [Sketcher::SketchObject] Sketch241  label="front_wall014"
  ExternalGeometry = -> [Pad012087]
  MapMode = 5
  Placement = pos=(2,0,0) rot=(0.57735,0.57735,0.57735;2.0944rad)
  Support = -> [Pad012087]
  sketch-geometry (9):
    g0: ArcOfCircle CenterX=18.4487 CenterY=16.9211 CenterZ=0 NormalX=0 NormalY=0 NormalZ=1 AngleXU=0 Radius=3.06832 StartAngle=3.68648 EndAngle=5.44463
    g1: LineSegment StartX=10.969 StartY=5.00105 StartZ=0 EndX=34.5617 EndY=18.1373 EndZ=0
    g2: LineSegment StartX=12.6837 StartY=20.7712 StartZ=0 EndX=4.56905 EndY=16.0862 EndZ=0
    g3: LineSegment StartX=4.56905 StartY=16.0862 StartZ=0 EndX=10.969 EndY=5.00105 EndZ=0
    g4: ArcOfCircle CenterX=24 CenterY=19.9888 CenterZ=0 NormalX=0 NormalY=0 NormalZ=1 AngleXU=0 Radius=6.3928 StartAngle=4.13303 EndAngle=7.03916
    g5: LineSegment StartX=28.6514 StartY=24.3743 StartZ=0 EndX=26.2197 EndY=28.5862 EndZ=0
    g6: LineSegment StartX=26.2197 StartY=28.5862 StartZ=0 EndX=27.9517 EndY=29.5862 EndZ=0
    g7: LineSegment StartX=27.9517 StartY=29.5862 StartZ=0 EndX=34.5617 EndY=18.1373 EndZ=0
    g8: LineSegment StartX=12.6837 StartY=20.7712 StartZ=0 EndX=15.8247 EndY=15.3307 EndZ=0
  constraints (20):
    c: Coincident(g3,g2)
    c: Parallel(g-7,g3)
    c: Coincident(g-7,g2)
    c: Coincident(g1,g3)
    c: Parallel(g-8,g2)
    c: Coincident(g4,g0)
    c: PointOnObject(g4,g-4)
    c: Coincident(g5,g4)
    c: Coincident(g5,g-5)
    c: Coincident(g5,g6)
    c: Coincident(g6,g-5)
    c: Coincident(g6,g7)
    c: Parallel(g-9,g7)
    c: Coincident(g7,g1)
    c: Coincident(g8,g2)
    c: Coincident(g8,g0)
    c: Perpendicular(g8,g2)
    c: Distance(g2) = 9.37
    c: Distance(g3) = 12.8
    c: Distance(g7) = 13.22
FEATURE [Sketcher::SketchObject] Sketch245  label="m2_screw_holes015"
  MapMode = 5
  Placement = pos=(-22.25,0,0) rot=(0.57735,-0.57735,-0.57735;2.0944rad)
  Support = -> [Pocket003121]
  sketch-geometry (2):
    g0: Circle CenterX=-31.1478 CenterY=24.1208 CenterZ=0 NormalX=0 NormalY=0 NormalZ=1 AngleXU=0 Radius=1.25
    g1: Circle CenterX=-7.61619 CenterY=10.5 CenterZ=0 NormalX=0 NormalY=0 NormalZ=1 AngleXU=0 Radius=1.25
  constraints (2):
    c: Radius(g0) = 1.25
    c: Equal(g0,g1) = 1.25
FEATURE [Sketcher::SketchObject] Sketch247  label="cable_slot015"
  ExternalGeometry = -> [Pocket003129]
  MapMode = 5
  Placement = pos=(-3.873e-13,33.775,19.5) rot=(0,0.5,0.866025;3.14159rad)
  Support = -> [Pocket003129]
  sketch-geometry (4):
    g0: LineSegment StartX=20.25 StartY=3 StartZ=0 EndX=18.01 EndY=3 EndZ=0
    g1: LineSegment StartX=18.01 StartY=3 StartZ=0 EndX=18.01 EndY=12.5 EndZ=0
    g2: LineSegment StartX=18.01 StartY=12.5 StartZ=0 EndX=20.25 EndY=12.5 EndZ=0
    g3: LineSegment StartX=20.25 StartY=12.5 StartZ=0 EndX=20.25 EndY=3 EndZ=0
  constraints (11):
    c: Coincident(g0,g1)
    c: Coincident(g1,g2)
    c: Coincident(g2,g3)
    c: Coincident(g3,g0)
    c: Horizontal(g0)
    c: Horizontal(g2)
    c: Vertical(g1)
    c: Vertical(g3)
    c: DistanceX(g2,g2) = 2.24
    c: DistanceY(g1,g1) = 9.5
    c: DistanceX(g2,g-3) = 2
FEATURE [PartDesign::Body] Body025  label="Q1-base009"
  Group = -> [Sketch237,Pad012090,Sketch253,Sketch246,Pad012089,Pocket003126,Sketch240,Pocket003124,Sketch242,Pad012091,Sketch259,Pocket003125,Sketch257,Pad012087,Sketch241,Pad012092,Sketch245,Sketch252,Sketch255,Sketch247,Pad012094,Sketch238,Pad012095,Pocket003129,Pocket003121,Hole007,Sketch254,Pocket003120]
  Origin = -> Origin044
  Placement = pos=(0,0,44) rot=(0,0,1;1.5708rad)
  Tip = -> Pocket003120
FEATURE [PartDesign::Pad] Pad012092  label="front_wall015"
  BaseFeature = -> Pad012087
  Length = 3.715
  Length2 = 100
  Profile = -> Sketch241
  Refine = true
  Type = 0
FEATURE [Sketcher::SketchObject] Sketch252  label="back_wall014"
  ExternalGeometry = -> [Pad012092]
  MapMode = 5
  Placement = pos=(-20.5,0,0) rot=(0.57735,-0.57735,-0.57735;2.0944rad)
  Support = -> [Pad012092]
  sketch-geometry (9):
    g0: LineSegment StartX=5.71497 StartY=2.25 StartZ=0 EndX=-11.6041 EndY=2.25 EndZ=0
    g1: LineSegment StartX=-11.6041 StartY=2.25 StartZ=0 EndX=-38.6752 EndY=17.8795 EndZ=0
    g2: LineSegment StartX=-38.6752 StartY=17.8795 StartZ=0 EndX=-37.1752 EndY=20.4776 EndZ=0
    g3: LineSegment StartX=-37.1752 StartY=20.4776 StartZ=0 EndX=-34.2017 EndY=18.7609 EndZ=0
    g4: LineSegment StartX=-34.2017 StartY=18.7609 StartZ=0 EndX=-27.9517 EndY=29.5862 EndZ=0
    g5: LineSegment StartX=-27.9517 StartY=29.5862 StartZ=0 EndX=-4.56905 EndY=16.0862 EndZ=0
    g6: LineSegment StartX=-4.56905 StartY=16.0862 StartZ=0 EndX=-10.5379 EndY=5.74787 EndZ=0
    g7: LineSegment StartX=-10.5379 StartY=5.74787 StartZ=0 EndX=5.71497 EndY=5.75 EndZ=0
    g8: LineSegment StartX=5.71497 StartY=5.75 StartZ=0 EndX=5.71497 EndY=2.25 EndZ=0
  constraints (18):
    c: Coincident(g-11,g0)
    c: Coincident(g0,g-11)
    c: Coincident(g0,g1)
    c: Coincident(g1,g-4)
    c: Coincident(g1,g2)
    c: Coincident(g2,g-5)
    c: Coincident(g2,g3)
    c: Coincident(g3,g-6)
    c: Coincident(g3,g4)
    c: Coincident(g4,g-6)
    c: Coincident(g4,g5)
    c: Coincident(g5,g-7)
    c: Coincident(g5,g6)
    c: Coincident(g6,g-8)
    c: Coincident(g6,g7)
    c: Coincident(g7,g-10)
    c: Coincident(g7,g8)
    c: Coincident(g8,g0)
FEATURE [Sketcher::SketchObject] Sketch254  label="finger_hole007"
  ExternalGeometry = -> [Hole007]
  MapMode = 5
  Placement = pos=(2.5e-15,1.92674,-3.33722) rot=(1,0,0;3.66519rad)
  Support = -> [Hole007]
  sketch-geometry (2):
    g0: Circle CenterX=-8.2675 CenterY=-26.8039 CenterZ=0 NormalX=0 NormalY=0 NormalZ=1 AngleXU=0 Radius=6
    g1: LineSegment [constr] StartX=-8.2675 StartY=-11.1744 StartZ=0 EndX=-8.2675 EndY=-42.4334 EndZ=0
  constraints (7):
    c: Radius(g0) = 6
    c: PointOnObject(g1,g-3)
    c: PointOnObject(g1,g-4)
    c: Vertical(g1)
    c: PointOnObject(g0,g1)
    c: Symmetric(g-3,g-3,g1)
    c: Symmetric(g1,g1,g0)
FEATURE [Sketcher::SketchObject] Sketch255  label="servo_tollerance014"
  MapMode = 5
  Placement = pos=(2.152e-13,-5.82326,10.0862) rot=(1,0,0;0.523599rad)
  Support = -> [Pad012095]
  sketch-geometry (4):
    g0: LineSegment StartX=-20.5 StartY=37 StartZ=0 EndX=-21.25 EndY=37 EndZ=0
    g1: LineSegment StartX=-21.25 StartY=37 StartZ=0 EndX=-21.25 EndY=14 EndZ=0
    g2: LineSegment StartX=-21.25 StartY=14 StartZ=0 EndX=-20.5 EndY=14 EndZ=0
    g3: LineSegment StartX=-20.5 StartY=14 StartZ=0 EndX=-20.5 EndY=37 EndZ=0
  constraints (9):
    c: Coincident(g0,g1)
    c: Coincident(g1,g2)
    c: Coincident(g2,g3)
    c: Coincident(g3,g0)
    c: Horizontal(g0)
    c: Horizontal(g2)
    c: Vertical(g1)
    c: Vertical(g3)
    c: DistanceX(g0,g0) = 0.75
FEATURE [PartDesign::Pad] Pad012094  label="back_wall015"
  BaseFeature = -> Pad012092
  Length = 1.75
  Length2 = 100
  Profile = -> Sketch252
  Refine = true
  Type = 0
FEATURE [PartDesign::Pad] Pad012095  label="servo_axis007"
  BaseFeature = -> Pad012094
  Length = 3
  Length2 = 100
  Profile = -> Sketch238
  Refine = true
  Type = 0
FEATURE [Sketcher::SketchObject] Sketch257  label="servo-walls007"
  ExternalGeometry = -> [Pocket003125]
  MapMode = 5
  Placement = pos=(2.152e-13,-5.82326,10.0862) rot=(1,0,0;0.523599rad)
  Support = -> [Pad012094]
  sketch-geometry (24):
    g0: LineSegment StartX=-5 StartY=42.4334 StartZ=0 EndX=-5 EndY=37 EndZ=0
    g1: LineSegment StartX=-5 StartY=37 StartZ=0 EndX=-20.5 EndY=37 EndZ=0
    g2: LineSegment StartX=-20.5 StartY=37 StartZ=0 EndX=-20.5 EndY=39 EndZ=0
    g3: LineSegment StartX=2 StartY=39 StartZ=0 EndX=2 EndY=37 EndZ=0
    g4: LineSegment StartX=2 StartY=37 StartZ=0 EndX=-1.60533 EndY=37 EndZ=0
    g5: LineSegment StartX=-1.60533 StartY=37 StartZ=0 EndX=-1.60533 EndY=42.4334 EndZ=0
    g6: LineSegment StartX=-20.5 StartY=39 StartZ=0 EndX=-7 EndY=39 EndZ=0
    g7: LineSegment StartX=-7 StartY=39 StartZ=0 EndX=-7 EndY=42.4334 EndZ=0
    g8: LineSegment StartX=-7 StartY=42.4334 StartZ=0 EndX=-5 EndY=42.4334 EndZ=0
    g9: LineSegment StartX=2 StartY=39 StartZ=0 EndX=0.5 EndY=39 EndZ=0
    g10: LineSegment StartX=0.5 StartY=39 StartZ=0 EndX=0.5 EndY=42.4334 EndZ=0
    g11: LineSegment StartX=-1.60533 StartY=42.4334 StartZ=0 EndX=0.5 EndY=42.4334 EndZ=0
    g12: LineSegment StartX=-5 StartY=9.5 StartZ=0 EndX=-5 EndY=14 EndZ=0
    g13: LineSegment StartX=-5 StartY=14 StartZ=0 EndX=-20.5 EndY=14 EndZ=0
    g14: LineSegment StartX=-20.5 StartY=14 StartZ=0 EndX=-20.5 EndY=12 EndZ=0
    g15: LineSegment StartX=2 StartY=12 StartZ=0 EndX=2 EndY=14 EndZ=0
    g16: LineSegment StartX=2 StartY=14 StartZ=0 EndX=-1.61532 EndY=14 EndZ=0
    g17: LineSegment StartX=-1.61532 StartY=14 StartZ=0 EndX=-1.61532 EndY=9.5 EndZ=0
    g18: LineSegment StartX=-20.5 StartY=12 StartZ=0 EndX=-7 EndY=12 EndZ=0
    g19: LineSegment StartX=-7 StartY=12 StartZ=0 EndX=-7 EndY=9.5 EndZ=0
    g20: LineSegment StartX=-7 StartY=9.5 StartZ=0 EndX=-5 EndY=9.5 EndZ=0
    g21: LineSegment StartX=2 StartY=12 StartZ=0 EndX=0.5 EndY=12 EndZ=0
    g22: LineSegment StartX=0.5 StartY=12 StartZ=0 EndX=0.5 EndY=9.5 EndZ=0
    g23: LineSegment StartX=-1.61532 StartY=9.5 StartZ=0 EndX=0.5 EndY=9.5 EndZ=0
  constraints (50):
    c: Coincident(g0,g1)
    c: Coincident(g1,g2)
    c: Horizontal(g1)
    c: Vertical(g0)
    c: Vertical(g2)
    c: Coincident(g3,g4)
    c: Coincident(g4,g5)
    c: Horizontal(g4)
    c: Vertical(g3)
    c: Vertical(g5)
    c: Coincident(g2,g6)
    c: Horizontal(g6)
    c: Coincident(g6,g7)
    c: Vertical(g7)
    c: PointOnObject(g7,g-3)
    c: PointOnObject(g0,g-3)
    c: Coincident(g8,g7)
    c: Coincident(g8,g0)
    c: Coincident(g3,g9)
    c: Horizontal(g9)
    c: Coincident(g9,g10)
    c: PointOnObject(g10,g-3)
    c: Vertical(g10)
    c: PointOnObject(g5,g-3)
    c: Coincident(g11,g5)
    c: Coincident(g11,g10)
    c: Coincident(g12,g13)
    c: Coincident(g13,g14)
    c: Horizontal(g13)
    c: Vertical(g12)
    c: Vertical(g14)
    c: Coincident(g15,g16)
    c: Coincident(g16,g17)
    c: Horizontal(g16)
    c: Vertical(g15)
    c: Vertical(g17)
    c: Coincident(g14,g18)
    c: Horizontal(g18)
    c: Coincident(g18,g19)
    c: Vertical(g19)
    c: Coincident(g19,g20)
    c: Coincident(g20,g12)
    c: Horizontal(g20)
    c: Coincident(g15,g21)
    c: Horizontal(g21)
    c: Coincident(g21,g22)
    c: Vertical(g22)
    c: Coincident(g17,g23)
    c: Coincident(g23,g22)
    c: Horizontal(g23)
FEATURE [PartDesign::Pocket] Pocket003129  label="servo_tollerance015"
  BaseFeature = -> Pad012095
  Length = 12.5
  Length2 = 100
  Profile = -> Sketch255
  Refine = true
  Type = 0
FEATURE [PartDesign::Pocket] Pocket003130  label="q1-leg008"
  BaseFeature = -> Hole008
  Length = 5
  Length2 = 100
  Profile = -> Sketch281
  Refine = true
  Type = 0
FEATURE [App::Part] Part017  label="right_leg_002"
  Group = -> [Pocket003137,Fusion007081,Fusion007082,Body028,Fusion007083,Pocket003132,Fusion007084,Fillet010,Body029,Part__Mirroring002,Part__Mirroring003]
  License = CC BY 3.0
  LicenseURL = http://creativecommons.org/licenses/by/3.0/
  Origin = -> Origin048
  Placement = pos=(56.5,52.5,0) rot=(0,0,1;0rad)
FEATURE [Sketcher::SketchObject] Sketch265  label="q2_axis008"
  MapMode = 5
  Placement = pos=(-22.25,0,0) rot=(0.57735,-0.57735,-0.57735;2.0944rad)
  Support = -> [Pad012107]
  sketch-geometry (1):
    g0: Circle CenterX=-24 CenterY=20 CenterZ=0 NormalX=0 NormalY=0 NormalZ=1 AngleXU=0 Radius=1.75
  constraints (1):
    c: Radius(g0) = 1.75
FEATURE [PartDesign::Hole] Hole008  label="m2_screw_holes016"
  BaseFeature = -> Pocket003131
  Depth = 35
  DepthType = 0
  Diameter = 2.5
  DrillPoint = 1
  DrillPointAngle = 118
  HoleCutCountersinkAngle = 90
  HoleCutDepth = 0
  HoleCutDiameter = 0
  HoleCutType = 0
  ModelActualThread = false
  Profile = -> Sketch272
  Refine = true
  Tapered = false
  TaperedAngle = 90
  ThreadAngle = 0
  ThreadClass = 0
  ThreadCutOffInner = 0
  ThreadCutOffOuter = 0
  ThreadDirection = 0
  ThreadFit = 0
  ThreadPitch = 0
  ThreadSize = 0
  ThreadType = 0
  Threaded = false
FEATURE [PartDesign::Pocket] Pocket003131  label="cable_slot016"
  BaseFeature = -> Pocket003139
  Length = 5
  Length2 = 100
  Profile = -> Sketch274
  Refine = true
  Type = 0
FEATURE [PartDesign::Pad] Pad012100  label="servo_walls008"
  BaseFeature = -> Pocket003135
  Length = 12.5
  Length2 = 100
  Profile = -> Sketch284
  Refine = true
  Type = 0
FEATURE [Sketcher::SketchObject] Sketch268  label="front_wall016"
  ExternalGeometry = -> [Pad012100]
  MapMode = 5
  Placement = pos=(2,0,0) rot=(0.57735,0.57735,0.57735;2.0944rad)
  Support = -> [Pad012100]
  sketch-geometry (9):
    g0: ArcOfCircle CenterX=18.4487 CenterY=16.9211 CenterZ=0 NormalX=0 NormalY=0 NormalZ=1 AngleXU=0 Radius=3.06832 StartAngle=3.68648 EndAngle=5.44463
    g1: LineSegment StartX=10.969 StartY=5.00105 StartZ=0 EndX=34.5617 EndY=18.1373 EndZ=0
    g2: LineSegment StartX=12.6837 StartY=20.7712 StartZ=0 EndX=4.56905 EndY=16.0862 EndZ=0
    g3: LineSegment StartX=4.56905 StartY=16.0862 StartZ=0 EndX=10.969 EndY=5.00105 EndZ=0
    g4: ArcOfCircle CenterX=24 CenterY=19.9888 CenterZ=0 NormalX=0 NormalY=0 NormalZ=1 AngleXU=0 Radius=6.3928 StartAngle=4.13303 EndAngle=7.03916
    g5: LineSegment StartX=28.6514 StartY=24.3743 StartZ=0 EndX=26.2197 EndY=28.5862 EndZ=0
    g6: LineSegment StartX=26.2197 StartY=28.5862 StartZ=0 EndX=27.9517 EndY=29.5862 EndZ=0
    g7: LineSegment StartX=27.9517 StartY=29.5862 StartZ=0 EndX=34.5617 EndY=18.1373 EndZ=0
    g8: LineSegment StartX=12.6837 StartY=20.7712 StartZ=0 EndX=15.8247 EndY=15.3307 EndZ=0
  constraints (20):
    c: Coincident(g3,g2)
    c: Parallel(g-7,g3)
    c: Coincident(g-7,g2)
    c: Coincident(g1,g3)
    c: Parallel(g-8,g2)
    c: Coincident(g4,g0)
    c: PointOnObject(g4,g-4)
    c: Coincident(g5,g4)
    c: Coincident(g5,g-5)
    c: Coincident(g5,g6)
    c: Coincident(g6,g-5)
    c: Coincident(g6,g7)
    c: Parallel(g-9,g7)
    c: Coincident(g7,g1)
    c: Coincident(g8,g2)
    c: Coincident(g8,g0)
    c: Perpendicular(g8,g2)
    c: Distance(g2) = 9.37
    c: Distance(g3) = 12.8
    c: Distance(g7) = 13.22
FEATURE [Sketcher::SketchObject] Sketch272  label="m2_screw_holes017"
  MapMode = 5
  Placement = pos=(-22.25,0,0) rot=(0.57735,-0.57735,-0.57735;2.0944rad)
  Support = -> [Pocket003131]
  sketch-geometry (2):
    g0: Circle CenterX=-31.1478 CenterY=24.1208 CenterZ=0 NormalX=0 NormalY=0 NormalZ=1 AngleXU=0 Radius=1.25
    g1: Circle CenterX=-7.61619 CenterY=10.5 CenterZ=0 NormalX=0 NormalY=0 NormalZ=1 AngleXU=0 Radius=1.25
  constraints (2):
    c: Radius(g0) = 1.25
    c: Equal(g0,g1) = 1.25
FEATURE [Sketcher::SketchObject] Sketch274  label="cable_slot017"
  ExternalGeometry = -> [Pocket003139]
  MapMode = 5
  Placement = pos=(-3.873e-13,33.775,19.5) rot=(0,0.5,0.866025;3.14159rad)
  Support = -> [Pocket003139]
  sketch-geometry (4):
    g0: LineSegment StartX=20.25 StartY=3 StartZ=0 EndX=18.01 EndY=3 EndZ=0
    g1: LineSegment StartX=18.01 StartY=3 StartZ=0 EndX=18.01 EndY=12.5 EndZ=0
    g2: LineSegment StartX=18.01 StartY=12.5 StartZ=0 EndX=20.25 EndY=12.5 EndZ=0
    g3: LineSegment StartX=20.25 StartY=12.5 StartZ=0 EndX=20.25 EndY=3 EndZ=0
  constraints (11):
    c: Coincident(g0,g1)
    c: Coincident(g1,g2)
    c: Coincident(g2,g3)
    c: Coincident(g3,g0)
    c: Horizontal(g0)
    c: Horizontal(g2)
    c: Vertical(g1)
    c: Vertical(g3)
    c: DistanceX(g2,g2) = 2.24
    c: DistanceY(g1,g1) = 9.5
    c: DistanceX(g2,g-3) = 2
FEATURE [PartDesign::Body] Body028  label="Q1-base010"
  Group = -> [Sketch264,Pad012103,Sketch280,Sketch273,Pad012102,Pocket003136,Sketch267,Pocket003134,Sketch269,Pad012104,Sketch286,Pocket003135,Sketch284,Pad012100,Sketch268,Pad012105,Sketch272,Sketch279,Sketch282,Sketch274,Pad012107,Sketch265,Pad012108,Pocket003139,Pocket003131,Hole008,Sketch281,Pocket003130]
  Origin = -> Origin049
  Placement = pos=(0,0,44) rot=(0,0,1;1.5708rad)
  Tip = -> Pocket003130
FEATURE [PartDesign::Pad] Pad012105  label="front_wall017"
  BaseFeature = -> Pad012100
  Length = 3.715
  Length2 = 100
  Profile = -> Sketch268
  Refine = true
  Type = 0
FEATURE [Sketcher::SketchObject] Sketch279  label="back_wall016"
  ExternalGeometry = -> [Pad012105]
  MapMode = 5
  Placement = pos=(-20.5,0,0) rot=(0.57735,-0.57735,-0.57735;2.0944rad)
  Support = -> [Pad012105]
  sketch-geometry (9):
    g0: LineSegment StartX=5.71497 StartY=2.25 StartZ=0 EndX=-11.6041 EndY=2.25 EndZ=0
    g1: LineSegment StartX=-11.6041 StartY=2.25 StartZ=0 EndX=-38.6752 EndY=17.8795 EndZ=0
    g2: LineSegment StartX=-38.6752 StartY=17.8795 StartZ=0 EndX=-37.1752 EndY=20.4776 EndZ=0
    g3: LineSegment StartX=-37.1752 StartY=20.4776 StartZ=0 EndX=-34.2017 EndY=18.7609 EndZ=0
    g4: LineSegment StartX=-34.2017 StartY=18.7609 StartZ=0 EndX=-27.9517 EndY=29.5862 EndZ=0
    g5: LineSegment StartX=-27.9517 StartY=29.5862 StartZ=0 EndX=-4.56905 EndY=16.0862 EndZ=0
    g6: LineSegment StartX=-4.56905 StartY=16.0862 StartZ=0 EndX=-10.5379 EndY=5.74787 EndZ=0
    g7: LineSegment StartX=-10.5379 StartY=5.74787 StartZ=0 EndX=5.71497 EndY=5.75 EndZ=0
    g8: LineSegment StartX=5.71497 StartY=5.75 StartZ=0 EndX=5.71497 EndY=2.25 EndZ=0
  constraints (18):
    c: Coincident(g-11,g0)
    c: Coincident(g0,g-11)
    c: Coincident(g0,g1)
    c: Coincident(g1,g-4)
    c: Coincident(g1,g2)
    c: Coincident(g2,g-5)
    c: Coincident(g2,g3)
    c: Coincident(g3,g-6)
    c: Coincident(g3,g4)
    c: Coincident(g4,g-6)
    c: Coincident(g4,g5)
    c: Coincident(g5,g-7)
    c: Coincident(g5,g6)
    c: Coincident(g6,g-8)
    c: Coincident(g6,g7)
    c: Coincident(g7,g-10)
    c: Coincident(g7,g8)
    c: Coincident(g8,g0)
FEATURE [Sketcher::SketchObject] Sketch281  label="finger_hole008"
  ExternalGeometry = -> [Hole008]
  MapMode = 5
  Placement = pos=(2.5e-15,1.92674,-3.33722) rot=(1,0,0;3.66519rad)
  Support = -> [Hole008]
  sketch-geometry (2):
    g0: Circle CenterX=-8.2675 CenterY=-26.8039 CenterZ=0 NormalX=0 NormalY=0 NormalZ=1 AngleXU=0 Radius=6
    g1: LineSegment [constr] StartX=-8.2675 StartY=-11.1744 StartZ=0 EndX=-8.2675 EndY=-42.4334 EndZ=0
  constraints (7):
    c: Radius(g0) = 6
    c: PointOnObject(g1,g-3)
    c: PointOnObject(g1,g-4)
    c: Vertical(g1)
    c: PointOnObject(g0,g1)
    c: Symmetric(g-3,g-3,g1)
    c: Symmetric(g1,g1,g0)
FEATURE [Sketcher::SketchObject] Sketch282  label="servo_tollerance016"
  MapMode = 5
  Placement = pos=(2.152e-13,-5.82326,10.0862) rot=(1,0,0;0.523599rad)
  Support = -> [Pad012108]
  sketch-geometry (4):
    g0: LineSegment StartX=-20.5 StartY=37 StartZ=0 EndX=-21.25 EndY=37 EndZ=0
    g1: LineSegment StartX=-21.25 StartY=37 StartZ=0 EndX=-21.25 EndY=14 EndZ=0
    g2: LineSegment StartX=-21.25 StartY=14 StartZ=0 EndX=-20.5 EndY=14 EndZ=0
    g3: LineSegment StartX=-20.5 StartY=14 StartZ=0 EndX=-20.5 EndY=37 EndZ=0
  constraints (9):
    c: Coincident(g0,g1)
    c: Coincident(g1,g2)
    c: Coincident(g2,g3)
    c: Coincident(g3,g0)
    c: Horizontal(g0)
    c: Horizontal(g2)
    c: Vertical(g1)
    c: Vertical(g3)
    c: DistanceX(g0,g0) = 0.75
FEATURE [PartDesign::Pad] Pad012107  label="back_wall017"
  BaseFeature = -> Pad012105
  Length = 1.75
  Length2 = 100
  Profile = -> Sketch279
  Refine = true
  Type = 0
FEATURE [PartDesign::Pad] Pad012108  label="servo_axis008"
  BaseFeature = -> Pad012107
  Length = 3
  Length2 = 100
  Profile = -> Sketch265
  Refine = true
  Type = 0
FEATURE [Sketcher::SketchObject] Sketch284  label="servo-walls008"
  ExternalGeometry = -> [Pocket003135]
  MapMode = 5
  Placement = pos=(2.152e-13,-5.82326,10.0862) rot=(1,0,0;0.523599rad)
  Support = -> [Pad012107]
  sketch-geometry (24):
    g0: LineSegment StartX=-5 StartY=42.4334 StartZ=0 EndX=-5 EndY=37 EndZ=0
    g1: LineSegment StartX=-5 StartY=37 StartZ=0 EndX=-20.5 EndY=37 EndZ=0
    g2: LineSegment StartX=-20.5 StartY=37 StartZ=0 EndX=-20.5 EndY=39 EndZ=0
    g3: LineSegment StartX=2 StartY=39 StartZ=0 EndX=2 EndY=37 EndZ=0
    g4: LineSegment StartX=2 StartY=37 StartZ=0 EndX=-1.60533 EndY=37 EndZ=0
    g5: LineSegment StartX=-1.60533 StartY=37 StartZ=0 EndX=-1.60533 EndY=42.4334 EndZ=0
    g6: LineSegment StartX=-20.5 StartY=39 StartZ=0 EndX=-7 EndY=39 EndZ=0
    g7: LineSegment StartX=-7 StartY=39 StartZ=0 EndX=-7 EndY=42.4334 EndZ=0
    g8: LineSegment StartX=-7 StartY=42.4334 StartZ=0 EndX=-5 EndY=42.4334 EndZ=0
    g9: LineSegment StartX=2 StartY=39 StartZ=0 EndX=0.5 EndY=39 EndZ=0
    g10: LineSegment StartX=0.5 StartY=39 StartZ=0 EndX=0.5 EndY=42.4334 EndZ=0
    g11: LineSegment StartX=-1.60533 StartY=42.4334 StartZ=0 EndX=0.5 EndY=42.4334 EndZ=0
    g12: LineSegment StartX=-5 StartY=9.5 StartZ=0 EndX=-5 EndY=14 EndZ=0
    g13: LineSegment StartX=-5 StartY=14 StartZ=0 EndX=-20.5 EndY=14 EndZ=0
    g14: LineSegment StartX=-20.5 StartY=14 StartZ=0 EndX=-20.5 EndY=12 EndZ=0
    g15: LineSegment StartX=2 StartY=12 StartZ=0 EndX=2 EndY=14 EndZ=0
    g16: LineSegment StartX=2 StartY=14 StartZ=0 EndX=-1.61532 EndY=14 EndZ=0
    g17: LineSegment StartX=-1.61532 StartY=14 StartZ=0 EndX=-1.61532 EndY=9.5 EndZ=0
    g18: LineSegment StartX=-20.5 StartY=12 StartZ=0 EndX=-7 EndY=12 EndZ=0
    g19: LineSegment StartX=-7 StartY=12 StartZ=0 EndX=-7 EndY=9.5 EndZ=0
    g20: LineSegment StartX=-7 StartY=9.5 StartZ=0 EndX=-5 EndY=9.5 EndZ=0
    g21: LineSegment StartX=2 StartY=12 StartZ=0 EndX=0.5 EndY=12 EndZ=0
    g22: LineSegment StartX=0.5 StartY=12 StartZ=0 EndX=0.5 EndY=9.5 EndZ=0
    g23: LineSegment StartX=-1.61532 StartY=9.5 StartZ=0 EndX=0.5 EndY=9.5 EndZ=0
  constraints (50):
    c: Coincident(g0,g1)
    c: Coincident(g1,g2)
    c: Horizontal(g1)
    c: Vertical(g0)
    c: Vertical(g2)
    c: Coincident(g3,g4)
    c: Coincident(g4,g5)
    c: Horizontal(g4)
    c: Vertical(g3)
    c: Vertical(g5)
    c: Coincident(g2,g6)
    c: Horizontal(g6)
    c: Coincident(g6,g7)
    c: Vertical(g7)
    c: PointOnObject(g7,g-3)
    c: PointOnObject(g0,g-3)
    c: Coincident(g8,g7)
    c: Coincident(g8,g0)
    c: Coincident(g3,g9)
    c: Horizontal(g9)
    c: Coincident(g9,g10)
    c: PointOnObject(g10,g-3)
    c: Vertical(g10)
    c: PointOnObject(g5,g-3)
    c: Coincident(g11,g5)
    c: Coincident(g11,g10)
    c: Coincident(g12,g13)
    c: Coincident(g13,g14)
    c: Horizontal(g13)
    c: Vertical(g12)
    c: Vertical(g14)
    c: Coincident(g15,g16)
    c: Coincident(g16,g17)
    c: Horizontal(g16)
    c: Vertical(g15)
    c: Vertical(g17)
    c: Coincident(g14,g18)
    c: Horizontal(g18)
    c: Coincident(g18,g19)
    c: Vertical(g19)
    c: Coincident(g19,g20)
    c: Coincident(g20,g12)
    c: Horizontal(g20)
    c: Coincident(g15,g21)
    c: Horizontal(g21)
    c: Coincident(g21,g22)
    c: Vertical(g22)
    c: Coincident(g17,g23)
    c: Coincident(g23,g22)
    c: Horizontal(g23)
FEATURE [PartDesign::Pocket] Pocket003139  label="servo_tollerance017"
  BaseFeature = -> Pad012108
  Length = 12.5
  Length2 = 100
  Profile = -> Sketch282
  Refine = true
  Type = 0
FEATURE [PartDesign::Pocket] Pocket003140  label="q1-leg009"
  BaseFeature = -> Hole009
  Length = 5
  Length2 = 100
  Profile = -> Sketch307
  Refine = true
  Type = 0
FEATURE [App::Part] Part018  label="right_leg_003"
  Group = -> [Pocket003147,Fusion007085,Fusion007086,Body030,Fusion007087,Pocket003142,Fusion007088,Fillet011,Body031,Part__Mirroring004,Part__Mirroring005]
  License = CC BY 3.0
  LicenseURL = http://creativecommons.org/licenses/by/3.0/
  Origin = -> Origin051
  Placement = pos=(56.5,-52.5,0) rot=(0,0,1;0rad)
FEATURE [Sketcher::SketchObject] Sketch291  label="q2_axis009"
  MapMode = 5
  Placement = pos=(-22.25,0,0) rot=(0.57735,-0.57735,-0.57735;2.0944rad)
  Support = -> [Pad012119]
  sketch-geometry (1):
    g0: Circle CenterX=-24 CenterY=20 CenterZ=0 NormalX=0 NormalY=0 NormalZ=1 AngleXU=0 Radius=1.75
  constraints (1):
    c: Radius(g0) = 1.75
FEATURE [PartDesign::Hole] Hole009  label="m2_screw_holes018"
  BaseFeature = -> Pocket003141
  Depth = 35
  DepthType = 0
  Diameter = 2.5
  DrillPoint = 1
  DrillPointAngle = 118
  HoleCutCountersinkAngle = 90
  HoleCutDepth = 0
  HoleCutDiameter = 0
  HoleCutType = 0
  ModelActualThread = false
  Profile = -> Sketch298
  Refine = true
  Tapered = false
  TaperedAngle = 90
  ThreadAngle = 0
  ThreadClass = 0
  ThreadCutOffInner = 0
  ThreadCutOffOuter = 0
  ThreadDirection = 0
  ThreadFit = 0
  ThreadPitch = 0
  ThreadSize = 0
  ThreadType = 0
  Threaded = false
FEATURE [PartDesign::Pocket] Pocket003141  label="cable_slot018"
  BaseFeature = -> Pocket003149
  Length = 5
  Length2 = 100
  Profile = -> Sketch300
  Refine = true
  Type = 0
FEATURE [PartDesign::Pad] Pad012112  label="servo_walls009"
  BaseFeature = -> Pocket003145
  Length = 12.5
  Length2 = 100
  Profile = -> Sketch310
  Refine = true
  Type = 0
FEATURE [Sketcher::SketchObject] Sketch294  label="front_wall018"
  ExternalGeometry = -> [Pad012112]
  MapMode = 5
  Placement = pos=(2,0,0) rot=(0.57735,0.57735,0.57735;2.0944rad)
  Support = -> [Pad012112]
  sketch-geometry (9):
    g0: ArcOfCircle CenterX=18.4487 CenterY=16.9211 CenterZ=0 NormalX=0 NormalY=0 NormalZ=1 AngleXU=0 Radius=3.06832 StartAngle=3.68648 EndAngle=5.44463
    g1: LineSegment StartX=10.969 StartY=5.00105 StartZ=0 EndX=34.5617 EndY=18.1373 EndZ=0
    g2: LineSegment StartX=12.6837 StartY=20.7712 StartZ=0 EndX=4.56905 EndY=16.0862 EndZ=0
    g3: LineSegment StartX=4.56905 StartY=16.0862 StartZ=0 EndX=10.969 EndY=5.00105 EndZ=0
    g4: ArcOfCircle CenterX=24 CenterY=19.9888 CenterZ=0 NormalX=0 NormalY=0 NormalZ=1 AngleXU=0 Radius=6.3928 StartAngle=4.13303 EndAngle=7.03916
    g5: LineSegment StartX=28.6514 StartY=24.3743 StartZ=0 EndX=26.2197 EndY=28.5862 EndZ=0
    g6: LineSegment StartX=26.2197 StartY=28.5862 StartZ=0 EndX=27.9517 EndY=29.5862 EndZ=0
    g7: LineSegment StartX=27.9517 StartY=29.5862 StartZ=0 EndX=34.5617 EndY=18.1373 EndZ=0
    g8: LineSegment StartX=12.6837 StartY=20.7712 StartZ=0 EndX=15.8247 EndY=15.3307 EndZ=0
  constraints (20):
    c: Coincident(g3,g2)
    c: Parallel(g-7,g3)
    c: Coincident(g-7,g2)
    c: Coincident(g1,g3)
    c: Parallel(g-8,g2)
    c: Coincident(g4,g0)
    c: PointOnObject(g4,g-4)
    c: Coincident(g5,g4)
    c: Coincident(g5,g-5)
    c: Coincident(g5,g6)
    c: Coincident(g6,g-5)
    c: Coincident(g6,g7)
    c: Parallel(g-9,g7)
    c: Coincident(g7,g1)
    c: Coincident(g8,g2)
    c: Coincident(g8,g0)
    c: Perpendicular(g8,g2)
    c: Distance(g2) = 9.37
    c: Distance(g3) = 12.8
    c: Distance(g7) = 13.22
FEATURE [Sketcher::SketchObject] Sketch298  label="m2_screw_holes019"
  MapMode = 5
  Placement = pos=(-22.25,0,0) rot=(0.57735,-0.57735,-0.57735;2.0944rad)
  Support = -> [Pocket003141]
  sketch-geometry (2):
    g0: Circle CenterX=-31.1478 CenterY=24.1208 CenterZ=0 NormalX=0 NormalY=0 NormalZ=1 AngleXU=0 Radius=1.25
    g1: Circle CenterX=-7.61619 CenterY=10.5 CenterZ=0 NormalX=0 NormalY=0 NormalZ=1 AngleXU=0 Radius=1.25
  constraints (2):
    c: Radius(g0) = 1.25
    c: Equal(g0,g1) = 1.25
FEATURE [Sketcher::SketchObject] Sketch300  label="cable_slot019"
  ExternalGeometry = -> [Pocket003149]
  MapMode = 5
  Placement = pos=(-3.873e-13,33.775,19.5) rot=(0,0.5,0.866025;3.14159rad)
  Support = -> [Pocket003149]
  sketch-geometry (4):
    g0: LineSegment StartX=20.25 StartY=3 StartZ=0 EndX=18.01 EndY=3 EndZ=0
    g1: LineSegment StartX=18.01 StartY=3 StartZ=0 EndX=18.01 EndY=12.5 EndZ=0
    g2: LineSegment StartX=18.01 StartY=12.5 StartZ=0 EndX=20.25 EndY=12.5 EndZ=0
    g3: LineSegment StartX=20.25 StartY=12.5 StartZ=0 EndX=20.25 EndY=3 EndZ=0
  constraints (11):
    c: Coincident(g0,g1)
    c: Coincident(g1,g2)
    c: Coincident(g2,g3)
    c: Coincident(g3,g0)
    c: Horizontal(g0)
    c: Horizontal(g2)
    c: Vertical(g1)
    c: Vertical(g3)
    c: DistanceX(g2,g2) = 2.24
    c: DistanceY(g1,g1) = 9.5
    c: DistanceX(g2,g-3) = 2
FEATURE [PartDesign::Body] Body030  label="Q1-base011"
  Group = -> [Sketch290,Pad012115,Sketch306,Sketch299,Pad012114,Pocket003146,Sketch293,Pocket003144,Sketch295,Pad012116,Sketch312,Pocket003145,Sketch310,Pad012112,Sketch294,Pad012117,Sketch298,Sketch305,Sketch308,Sketch300,Pad012119,Sketch291,Pad012120,Pocket003149,Pocket003141,Hole009,Sketch307,Pocket003140]
  Origin = -> Origin052
  Placement = pos=(0,0,44) rot=(0,0,1;1.5708rad)
  Tip = -> Pocket003140
FEATURE [PartDesign::Pad] Pad012117  label="front_wall019"
  BaseFeature = -> Pad012112
  Length = 3.715
  Length2 = 100
  Profile = -> Sketch294
  Refine = true
  Type = 0
FEATURE [Sketcher::SketchObject] Sketch305  label="back_wall018"
  ExternalGeometry = -> [Pad012117]
  MapMode = 5
  Placement = pos=(-20.5,0,0) rot=(0.57735,-0.57735,-0.57735;2.0944rad)
  Support = -> [Pad012117]
  sketch-geometry (9):
    g0: LineSegment StartX=5.71497 StartY=2.25 StartZ=0 EndX=-11.6041 EndY=2.25 EndZ=0
    g1: LineSegment StartX=-11.6041 StartY=2.25 StartZ=0 EndX=-38.6752 EndY=17.8795 EndZ=0
    g2: LineSegment StartX=-38.6752 StartY=17.8795 StartZ=0 EndX=-37.1752 EndY=20.4776 EndZ=0
    g3: LineSegment StartX=-37.1752 StartY=20.4776 StartZ=0 EndX=-34.2017 EndY=18.7609 EndZ=0
    g4: LineSegment StartX=-34.2017 StartY=18.7609 StartZ=0 EndX=-27.9517 EndY=29.5862 EndZ=0
    g5: LineSegment StartX=-27.9517 StartY=29.5862 StartZ=0 EndX=-4.56905 EndY=16.0862 EndZ=0
    g6: LineSegment StartX=-4.56905 StartY=16.0862 StartZ=0 EndX=-10.5379 EndY=5.74787 EndZ=0
    g7: LineSegment StartX=-10.5379 StartY=5.74787 StartZ=0 EndX=5.71497 EndY=5.75 EndZ=0
    g8: LineSegment StartX=5.71497 StartY=5.75 StartZ=0 EndX=5.71497 EndY=2.25 EndZ=0
  constraints (18):
    c: Coincident(g-11,g0)
    c: Coincident(g0,g-11)
    c: Coincident(g0,g1)
    c: Coincident(g1,g-4)
    c: Coincident(g1,g2)
    c: Coincident(g2,g-5)
    c: Coincident(g2,g3)
    c: Coincident(g3,g-6)
    c: Coincident(g3,g4)
    c: Coincident(g4,g-6)
    c: Coincident(g4,g5)
    c: Coincident(g5,g-7)
    c: Coincident(g5,g6)
    c: Coincident(g6,g-8)
    c: Coincident(g6,g7)
    c: Coincident(g7,g-10)
    c: Coincident(g7,g8)
    c: Coincident(g8,g0)
FEATURE [Sketcher::SketchObject] Sketch307  label="finger_hole009"
  ExternalGeometry = -> [Hole009]
  MapMode = 5
  Placement = pos=(2.5e-15,1.92674,-3.33722) rot=(1,0,0;3.66519rad)
  Support = -> [Hole009]
  sketch-geometry (2):
    g0: Circle CenterX=-8.2675 CenterY=-26.8039 CenterZ=0 NormalX=0 NormalY=0 NormalZ=1 AngleXU=0 Radius=6
    g1: LineSegment [constr] StartX=-8.2675 StartY=-11.1744 StartZ=0 EndX=-8.2675 EndY=-42.4334 EndZ=0
  constraints (7):
    c: Radius(g0) = 6
    c: PointOnObject(g1,g-3)
    c: PointOnObject(g1,g-4)
    c: Vertical(g1)
    c: PointOnObject(g0,g1)
    c: Symmetric(g-3,g-3,g1)
    c: Symmetric(g1,g1,g0)
FEATURE [Sketcher::SketchObject] Sketch308  label="servo_tollerance018"
  MapMode = 5
  Placement = pos=(2.152e-13,-5.82326,10.0862) rot=(1,0,0;0.523599rad)
  Support = -> [Pad012120]
  sketch-geometry (4):
    g0: LineSegment StartX=-20.5 StartY=37 StartZ=0 EndX=-21.25 EndY=37 EndZ=0
    g1: LineSegment StartX=-21.25 StartY=37 StartZ=0 EndX=-21.25 EndY=14 EndZ=0
    g2: LineSegment StartX=-21.25 StartY=14 StartZ=0 EndX=-20.5 EndY=14 EndZ=0
    g3: LineSegment StartX=-20.5 StartY=14 StartZ=0 EndX=-20.5 EndY=37 EndZ=0
  constraints (9):
    c: Coincident(g0,g1)
    c: Coincident(g1,g2)
    c: Coincident(g2,g3)
    c: Coincident(g3,g0)
    c: Horizontal(g0)
    c: Horizontal(g2)
    c: Vertical(g1)
    c: Vertical(g3)
    c: DistanceX(g0,g0) = 0.75
FEATURE [PartDesign::Pad] Pad012119  label="back_wall019"
  BaseFeature = -> Pad012117
  Length = 1.75
  Length2 = 100
  Profile = -> Sketch305
  Refine = true
  Type = 0
FEATURE [PartDesign::Pad] Pad012120  label="servo_axis009"
  BaseFeature = -> Pad012119
  Length = 3
  Length2 = 100
  Profile = -> Sketch291
  Refine = true
  Type = 0
FEATURE [Sketcher::SketchObject] Sketch310  label="servo-walls009"
  ExternalGeometry = -> [Pocket003145]
  MapMode = 5
  Placement = pos=(2.152e-13,-5.82326,10.0862) rot=(1,0,0;0.523599rad)
  Support = -> [Pad012119]
  sketch-geometry (24):
    g0: LineSegment StartX=-5 StartY=42.4334 StartZ=0 EndX=-5 EndY=37 EndZ=0
    g1: LineSegment StartX=-5 StartY=37 StartZ=0 EndX=-20.5 EndY=37 EndZ=0
    g2: LineSegment StartX=-20.5 StartY=37 StartZ=0 EndX=-20.5 EndY=39 EndZ=0
    g3: LineSegment StartX=2 StartY=39 StartZ=0 EndX=2 EndY=37 EndZ=0
    g4: LineSegment StartX=2 StartY=37 StartZ=0 EndX=-1.60533 EndY=37 EndZ=0
    g5: LineSegment StartX=-1.60533 StartY=37 StartZ=0 EndX=-1.60533 EndY=42.4334 EndZ=0
    g6: LineSegment StartX=-20.5 StartY=39 StartZ=0 EndX=-7 EndY=39 EndZ=0
    g7: LineSegment StartX=-7 StartY=39 StartZ=0 EndX=-7 EndY=42.4334 EndZ=0
    g8: LineSegment StartX=-7 StartY=42.4334 StartZ=0 EndX=-5 EndY=42.4334 EndZ=0
    g9: LineSegment StartX=2 StartY=39 StartZ=0 EndX=0.5 EndY=39 EndZ=0
    g10: LineSegment StartX=0.5 StartY=39 StartZ=0 EndX=0.5 EndY=42.4334 EndZ=0
    g11: LineSegment StartX=-1.60533 StartY=42.4334 StartZ=0 EndX=0.5 EndY=42.4334 EndZ=0
    g12: LineSegment StartX=-5 StartY=9.5 StartZ=0 EndX=-5 EndY=14 EndZ=0
    g13: LineSegment StartX=-5 StartY=14 StartZ=0 EndX=-20.5 EndY=14 EndZ=0
    g14: LineSegment StartX=-20.5 StartY=14 StartZ=0 EndX=-20.5 EndY=12 EndZ=0
    g15: LineSegment StartX=2 StartY=12 StartZ=0 EndX=2 EndY=14 EndZ=0
    g16: LineSegment StartX=2 StartY=14 StartZ=0 EndX=-1.61532 EndY=14 EndZ=0
    g17: LineSegment StartX=-1.61532 StartY=14 StartZ=0 EndX=-1.61532 EndY=9.5 EndZ=0
    g18: LineSegment StartX=-20.5 StartY=12 StartZ=0 EndX=-7 EndY=12 EndZ=0
    g19: LineSegment StartX=-7 StartY=12 StartZ=0 EndX=-7 EndY=9.5 EndZ=0
    g20: LineSegment StartX=-7 StartY=9.5 StartZ=0 EndX=-5 EndY=9.5 EndZ=0
    g21: LineSegment StartX=2 StartY=12 StartZ=0 EndX=0.5 EndY=12 EndZ=0
    g22: LineSegment StartX=0.5 StartY=12 StartZ=0 EndX=0.5 EndY=9.5 EndZ=0
    g23: LineSegment StartX=-1.61532 StartY=9.5 StartZ=0 EndX=0.5 EndY=9.5 EndZ=0
  constraints (50):
    c: Coincident(g0,g1)
    c: Coincident(g1,g2)
    c: Horizontal(g1)
    c: Vertical(g0)
    c: Vertical(g2)
    c: Coincident(g3,g4)
    c: Coincident(g4,g5)
    c: Horizontal(g4)
    c: Vertical(g3)
    c: Vertical(g5)
    c: Coincident(g2,g6)
    c: Horizontal(g6)
    c: Coincident(g6,g7)
    c: Vertical(g7)
    c: PointOnObject(g7,g-3)
    c: PointOnObject(g0,g-3)
    c: Coincident(g8,g7)
    c: Coincident(g8,g0)
    c: Coincident(g3,g9)
    c: Horizontal(g9)
    c: Coincident(g9,g10)
    c: PointOnObject(g10,g-3)
    c: Vertical(g10)
    c: PointOnObject(g5,g-3)
    c: Coincident(g11,g5)
    c: Coincident(g11,g10)
    c: Coincident(g12,g13)
    c: Coincident(g13,g14)
    c: Horizontal(g13)
    c: Vertical(g12)
    c: Vertical(g14)
    c: Coincident(g15,g16)
    c: Coincident(g16,g17)
    c: Horizontal(g16)
    c: Vertical(g15)
    c: Vertical(g17)
    c: Coincident(g14,g18)
    c: Horizontal(g18)
    c: Coincident(g18,g19)
    c: Vertical(g19)
    c: Coincident(g19,g20)
    c: Coincident(g20,g12)
    c: Horizontal(g20)
    c: Coincident(g15,g21)
    c: Horizontal(g21)
    c: Coincident(g21,g22)
    c: Vertical(g22)
    c: Coincident(g17,g23)
    c: Coincident(g23,g22)
    c: Horizontal(g23)
FEATURE [PartDesign::Pocket] Pocket003149  label="servo_tollerance019"
  BaseFeature = -> Pad012120
  Length = 12.5
  Length2 = 100
  Profile = -> Sketch308
  Refine = true
  Type = 0
